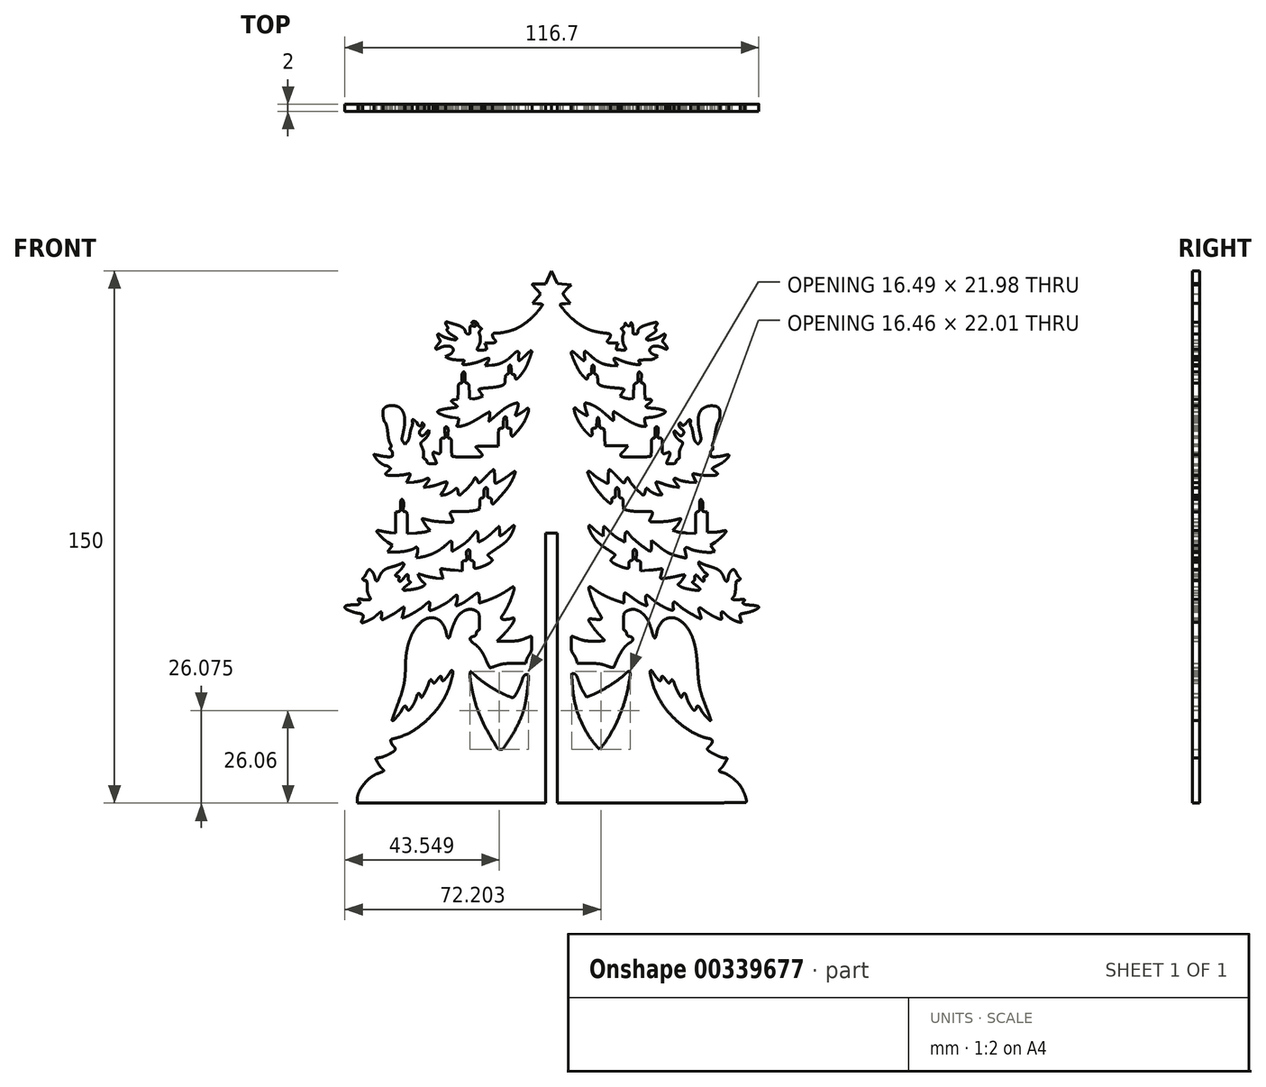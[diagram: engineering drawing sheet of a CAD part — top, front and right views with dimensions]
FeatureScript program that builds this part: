
annotation { "Feature Type Name" : "Feature", "Feature Type Description" : "" }
export const myFeature = defineFeature(function(context is Context, id is Id, definition is map)
    precondition{}
    {
        {
            var Q0;
            Q0=qCreatedBy(makeId("Front.planeOp"),FACE);
            var sketch = newSketch(context, id + "F0", { "sketchPlane" : qUnion([Q0])});
            skLineSegment(sketch, "E0", {"start": v(-52.5, 71.27) * mm, "end": v(-50.53, 71.13) * mm});
            skLineSegment(sketch, "E1", {"start": v(-50.53, 71.13) * mm, "end": v(-51.65, 70.04) * mm});
            skArc(sketch, "E2", {"start": v(-51.65, 70.04) * mm, "mid": v(-51.87, 69.82) * mm, "end": v(-52.08, 69.6) * mm});
            skArc(sketch, "E3", {"start": v(-52.08, 69.6) * mm, "mid": v(-52.26, 69.38) * mm, "end": v(-52.44, 69.15) * mm});
            skArc(sketch, "E4", {"start": v(-52.44, 69.15) * mm, "mid": v(-52.58, 68.96) * mm, "end": v(-52.7, 68.77) * mm});
            skArc(sketch, "E5", {"start": v(-52.7, 68.77) * mm, "mid": v(-52.75, 68.67) * mm, "end": v(-52.77, 68.56) * mm});
            skArc(sketch, "E6", {"start": v(-52.77, 68.56) * mm, "mid": v(-52.76, 68.45) * mm, "end": v(-52.72, 68.35) * mm});
            skArc(sketch, "E7", {"start": v(-52.72, 68.35) * mm, "mid": v(-52.6, 68.15) * mm, "end": v(-52.48, 67.95) * mm});
            skArc(sketch, "E8", {"start": v(-52.48, 67.95) * mm, "mid": v(-52.33, 67.72) * mm, "end": v(-52.16, 67.5) * mm});
            skArc(sketch, "E9", {"start": v(-52.16, 67.5) * mm, "mid": v(-51.98, 67.26) * mm, "end": v(-51.78, 67.03) * mm});
            skLineSegment(sketch, "E10", {"start": v(-51.78, 67.03) * mm, "end": v(-50.8, 65.88) * mm});
            skLineSegment(sketch, "E11", {"start": v(-50.8, 65.88) * mm, "end": v(-52.2, 65.8) * mm});
            skArc(sketch, "E12", {"start": v(-52.2, 65.8) * mm, "mid": v(-52.47, 65.77) * mm, "end": v(-52.74, 65.75) * mm});
            skArc(sketch, "E13", {"start": v(-52.74, 65.75) * mm, "mid": v(-52.96, 65.72) * mm, "end": v(-53.19, 65.69) * mm});
            skArc(sketch, "E14", {"start": v(-53.19, 65.69) * mm, "mid": v(-53.37, 65.66) * mm, "end": v(-53.55, 65.62) * mm});
            skArc(sketch, "E15", {"start": v(-53.55, 65.62) * mm, "mid": v(-53.59, 65.6) * mm, "end": v(-53.6, 65.55) * mm});
            skArc(sketch, "E16", {"start": v(-53.6, 65.55) * mm, "mid": v(-53.56, 65.3) * mm, "end": v(-53.44, 65.08) * mm});
            skArc(sketch, "E17", {"start": v(-53.44, 65.08) * mm, "mid": v(-52.9, 64.41) * mm, "end": v(-52.37, 63.76) * mm});
            skArc(sketch, "E18", {"start": v(-52.37, 63.76) * mm, "mid": v(-51.8, 63.1) * mm, "end": v(-51.2, 62.44) * mm});
            skArc(sketch, "E19", {"start": v(-51.2, 62.44) * mm, "mid": v(-50.7, 61.94) * mm, "end": v(-50.18, 61.47) * mm});
            skArc(sketch, "E20", {"start": v(-50.18, 61.47) * mm, "mid": v(-49.1, 60.6) * mm, "end": v(-47.97, 59.78) * mm});
            skArc(sketch, "E21", {"start": v(-47.97, 59.78) * mm, "mid": v(-47, 59.18) * mm, "end": v(-45.97, 58.67) * mm});
            skArc(sketch, "E22", {"start": v(-45.97, 58.67) * mm, "mid": v(-44.9, 58.26) * mm, "end": v(-43.81, 57.95) * mm});
            skArc(sketch, "E23", {"start": v(-43.81, 57.95) * mm, "mid": v(-42.5, 57.69) * mm, "end": v(-41.16, 57.5) * mm});
            skArc(sketch, "E24", {"start": v(-41.16, 57.5) * mm, "mid": v(-40.64, 57.44) * mm, "end": v(-40.13, 57.37) * mm});
            skArc(sketch, "E25", {"start": v(-40.13, 57.37) * mm, "mid": v(-39.9, 57.32) * mm, "end": v(-39.68, 57.24) * mm});
            skArc(sketch, "E26", {"start": v(-39.68, 57.24) * mm, "mid": v(-39.57, 57.16) * mm, "end": v(-39.49, 57.05) * mm});
            skArc(sketch, "E27", {"start": v(-39.49, 57.05) * mm, "mid": v(-39.45, 56.9) * mm, "end": v(-39.45, 56.75) * mm});
            skArc(sketch, "E28", {"start": v(-39.45, 56.75) * mm, "mid": v(-39.48, 56.63) * mm, "end": v(-39.52, 56.5) * mm});
            skArc(sketch, "E29", {"start": v(-39.52, 56.5) * mm, "mid": v(-39.57, 56.37) * mm, "end": v(-39.64, 56.23) * mm});
            skArc(sketch, "E30", {"start": v(-39.64, 56.23) * mm, "mid": v(-39.7, 56.1) * mm, "end": v(-39.78, 55.97) * mm});
            skArc(sketch, "E31", {"start": v(-39.78, 55.97) * mm, "mid": v(-39.86, 55.86) * mm, "end": v(-39.94, 55.76) * mm});
            skArc(sketch, "E32", {"start": v(-39.94, 55.76) * mm, "mid": v(-40.13, 55.51) * mm, "end": v(-40.3, 55.24) * mm});
            skArc(sketch, "E33", {"start": v(-40.3, 55.24) * mm, "mid": v(-40.32, 55.07) * mm, "end": v(-40.24, 54.91) * mm});
            skArc(sketch, "E34", {"start": v(-40.24, 54.91) * mm, "mid": v(-40.05, 54.78) * mm, "end": v(-39.82, 54.72) * mm});
            skArc(sketch, "E35", {"start": v(-39.82, 54.72) * mm, "mid": v(-39.32, 54.7) * mm, "end": v(-38.82, 54.68) * mm});
            skLineSegment(sketch, "E36", {"start": v(-38.82, 54.68) * mm, "end": v(-37.32, 54.68) * mm});
            skLineSegment(sketch, "E37", {"start": v(-37.32, 54.68) * mm, "end": v(-37.6, 53.84) * mm});
            skArc(sketch, "E38", {"start": v(-37.6, 53.84) * mm, "mid": v(-37.66, 53.67) * mm, "end": v(-37.71, 53.5) * mm});
            skArc(sketch, "E39", {"start": v(-37.71, 53.5) * mm, "mid": v(-37.75, 53.36) * mm, "end": v(-37.79, 53.21) * mm});
            skArc(sketch, "E40", {"start": v(-37.79, 53.21) * mm, "mid": v(-37.8, 53.1) * mm, "end": v(-37.83, 52.97) * mm});
            skArc(sketch, "E41", {"start": v(-37.83, 52.97) * mm, "mid": v(-37.82, 52.93) * mm, "end": v(-37.8, 52.9) * mm});
            skArc(sketch, "E42", {"start": v(-37.8, 52.9) * mm, "mid": v(-37.67, 52.8) * mm, "end": v(-37.51, 52.76) * mm});
            skArc(sketch, "E43", {"start": v(-37.51, 52.76) * mm, "mid": v(-37, 52.73) * mm, "end": v(-36.49, 52.71) * mm});
            skArc(sketch, "E44", {"start": v(-36.49, 52.71) * mm, "mid": v(-35.98, 52.7) * mm, "end": v(-35.46, 52.7) * mm});
            skArc(sketch, "E45", {"start": v(-35.46, 52.7) * mm, "mid": v(-35.31, 52.73) * mm, "end": v(-35.19, 52.82) * mm});
            skArc(sketch, "E46", {"start": v(-35.19, 52.82) * mm, "mid": v(-35.15, 52.87) * mm, "end": v(-35.14, 52.93) * mm});
            skArc(sketch, "E47", {"start": v(-35.14, 52.93) * mm, "mid": v(-35.15, 53.03) * mm, "end": v(-35.18, 53.13) * mm});
            skArc(sketch, "E48", {"start": v(-35.18, 53.13) * mm, "mid": v(-35.22, 53.26) * mm, "end": v(-35.27, 53.38) * mm});
            skArc(sketch, "E49", {"start": v(-35.27, 53.38) * mm, "mid": v(-35.33, 53.5) * mm, "end": v(-35.4, 53.63) * mm});
            skArc(sketch, "E50", {"start": v(-35.4, 53.63) * mm, "mid": v(-35.63, 54.02) * mm, "end": v(-35.8, 54.42) * mm});
            skArc(sketch, "E51", {"start": v(-35.8, 54.42) * mm, "mid": v(-35.92, 54.89) * mm, "end": v(-36.01, 55.36) * mm});
            skArc(sketch, "E52", {"start": v(-36.01, 55.36) * mm, "mid": v(-36.05, 55.82) * mm, "end": v(-36.05, 56.28) * mm});
            skArc(sketch, "E53", {"start": v(-36.05, 56.28) * mm, "mid": v(-35.99, 56.65) * mm, "end": v(-35.87, 57) * mm});
            skArc(sketch, "E54", {"start": v(-35.87, 57) * mm, "mid": v(-35.78, 57.2) * mm, "end": v(-35.72, 57.4) * mm});
            skArc(sketch, "E55", {"start": v(-35.72, 57.4) * mm, "mid": v(-35.69, 57.54) * mm, "end": v(-35.7, 57.68) * mm});
            skArc(sketch, "E56", {"start": v(-35.7, 57.68) * mm, "mid": v(-35.72, 57.82) * mm, "end": v(-35.78, 57.94) * mm});
            skArc(sketch, "E57", {"start": v(-35.78, 57.94) * mm, "mid": v(-35.9, 58.1) * mm, "end": v(-36.02, 58.25) * mm});
            skArc(sketch, "E58", {"start": v(-36.02, 58.25) * mm, "mid": v(-36.17, 58.42) * mm, "end": v(-36.3, 58.59) * mm});
            skArc(sketch, "E59", {"start": v(-36.3, 58.59) * mm, "mid": v(-36.35, 58.66) * mm, "end": v(-36.35, 58.75) * mm});
            skArc(sketch, "E60", {"start": v(-36.35, 58.75) * mm, "mid": v(-36.33, 58.83) * mm, "end": v(-36.27, 58.89) * mm});
            skArc(sketch, "E61", {"start": v(-36.27, 58.89) * mm, "mid": v(-36.1, 59) * mm, "end": v(-35.93, 59.1) * mm});
            skArc(sketch, "E62", {"start": v(-35.93, 59.1) * mm, "mid": v(-35.81, 59.16) * mm, "end": v(-35.7, 59.25) * mm});
            skArc(sketch, "E63", {"start": v(-35.7, 59.25) * mm, "mid": v(-35.6, 59.37) * mm, "end": v(-35.51, 59.49) * mm});
            skArc(sketch, "E64", {"start": v(-35.51, 59.49) * mm, "mid": v(-35.44, 59.62) * mm, "end": v(-35.38, 59.75) * mm});
            skArc(sketch, "E65", {"start": v(-35.38, 59.75) * mm, "mid": v(-35.34, 59.88) * mm, "end": v(-35.33, 60.01) * mm});
            skArc(sketch, "E66", {"start": v(-35.33, 60.01) * mm, "mid": v(-35.32, 60.15) * mm, "end": v(-35.31, 60.28) * mm});
            skArc(sketch, "E67", {"start": v(-35.31, 60.28) * mm, "mid": v(-35.3, 60.33) * mm, "end": v(-35.27, 60.37) * mm});
            skArc(sketch, "E68", {"start": v(-35.27, 60.37) * mm, "mid": v(-35.25, 60.38) * mm, "end": v(-35.22, 60.36) * mm});
            skArc(sketch, "E69", {"start": v(-35.22, 60.36) * mm, "mid": v(-35.18, 60.29) * mm, "end": v(-35.15, 60.2) * mm});
            skArc(sketch, "E70", {"start": v(-35.15, 60.2) * mm, "mid": v(-35, 59.94) * mm, "end": v(-34.8, 59.71) * mm});
            skArc(sketch, "E71", {"start": v(-34.8, 59.71) * mm, "mid": v(-34.56, 59.57) * mm, "end": v(-34.3, 59.52) * mm});
            skArc(sketch, "E72", {"start": v(-34.3, 59.52) * mm, "mid": v(-34.06, 59.57) * mm, "end": v(-33.87, 59.7) * mm});
            skArc(sketch, "E73", {"start": v(-33.87, 59.7) * mm, "mid": v(-33.74, 59.92) * mm, "end": v(-33.69, 60.17) * mm});
            skArc(sketch, "E74", {"start": v(-33.69, 60.17) * mm, "mid": v(-33.68, 60.3) * mm, "end": v(-33.68, 60.43) * mm});
            skArc(sketch, "E75", {"start": v(-33.68, 60.43) * mm, "mid": v(-33.67, 60.46) * mm, "end": v(-33.64, 60.47) * mm});
            skArc(sketch, "E76", {"start": v(-33.64, 60.47) * mm, "mid": v(-33.6, 60.47) * mm, "end": v(-33.57, 60.44) * mm});
            skArc(sketch, "E77", {"start": v(-33.57, 60.44) * mm, "mid": v(-33.5, 60.33) * mm, "end": v(-33.42, 60.2) * mm});
            skArc(sketch, "E78", {"start": v(-33.42, 60.2) * mm, "mid": v(-33.35, 60.1) * mm, "end": v(-33.31, 59.97) * mm});
            skArc(sketch, "E79", {"start": v(-33.31, 59.97) * mm, "mid": v(-33.26, 59.75) * mm, "end": v(-33.22, 59.53) * mm});
            skArc(sketch, "E80", {"start": v(-33.22, 59.53) * mm, "mid": v(-33.19, 59.27) * mm, "end": v(-33.16, 59.01) * mm});
            skArc(sketch, "E81", {"start": v(-33.16, 59.01) * mm, "mid": v(-33.15, 58.75) * mm, "end": v(-33.14, 58.48) * mm});
            skArc(sketch, "E82", {"start": v(-33.14, 58.48) * mm, "mid": v(-33.14, 58.09) * mm, "end": v(-33.12, 57.7) * mm});
            skArc(sketch, "E83", {"start": v(-33.12, 57.7) * mm, "mid": v(-33.1, 57.52) * mm, "end": v(-33.03, 57.37) * mm});
            skArc(sketch, "E84", {"start": v(-33.03, 57.37) * mm, "mid": v(-32.95, 57.27) * mm, "end": v(-32.84, 57.22) * mm});
            skArc(sketch, "E85", {"start": v(-32.84, 57.22) * mm, "mid": v(-32.64, 57.18) * mm, "end": v(-32.45, 57.17) * mm});
            skArc(sketch, "E86", {"start": v(-32.45, 57.17) * mm, "mid": v(-32.27, 57.18) * mm, "end": v(-32.1, 57.2) * mm});
            skArc(sketch, "E87", {"start": v(-32.1, 57.2) * mm, "mid": v(-32, 57.24) * mm, "end": v(-31.9, 57.3) * mm});
            skArc(sketch, "E88", {"start": v(-31.9, 57.3) * mm, "mid": v(-31.83, 57.39) * mm, "end": v(-31.8, 57.5) * mm});
            skArc(sketch, "E89", {"start": v(-31.8, 57.5) * mm, "mid": v(-31.76, 57.65) * mm, "end": v(-31.76, 57.82) * mm});
            skArc(sketch, "E90", {"start": v(-31.76, 57.82) * mm, "mid": v(-31.7, 58.17) * mm, "end": v(-31.56, 58.49) * mm});
            skArc(sketch, "E91", {"start": v(-31.56, 58.49) * mm, "mid": v(-31.32, 58.8) * mm, "end": v(-31.03, 59.05) * mm});
            skArc(sketch, "E92", {"start": v(-31.03, 59.05) * mm, "mid": v(-30.55, 59.33) * mm, "end": v(-30.05, 59.55) * mm});
            skArc(sketch, "E93", {"start": v(-30.05, 59.55) * mm, "mid": v(-29.25, 59.82) * mm, "end": v(-28.45, 60.07) * mm});
            skArc(sketch, "E94", {"start": v(-28.45, 60.07) * mm, "mid": v(-27.69, 60.27) * mm, "end": v(-26.92, 60.47) * mm});
            skArc(sketch, "E95", {"start": v(-26.92, 60.47) * mm, "mid": v(-26.64, 60.5) * mm, "end": v(-26.37, 60.44) * mm});
            skArc(sketch, "E96", {"start": v(-26.37, 60.44) * mm, "mid": v(-26.25, 60.33) * mm, "end": v(-26.25, 60.16) * mm});
            skArc(sketch, "E97", {"start": v(-26.25, 60.16) * mm, "mid": v(-26.43, 59.8) * mm, "end": v(-26.64, 59.46) * mm});
            skArc(sketch, "E98", {"start": v(-26.64, 59.46) * mm, "mid": v(-26.73, 59.33) * mm, "end": v(-26.8, 59.2) * mm});
            skArc(sketch, "E99", {"start": v(-26.8, 59.2) * mm, "mid": v(-26.85, 59.09) * mm, "end": v(-26.88, 58.97) * mm});
            skArc(sketch, "E100", {"start": v(-26.88, 58.97) * mm, "mid": v(-26.88, 58.89) * mm, "end": v(-26.87, 58.8) * mm});
            skArc(sketch, "E101", {"start": v(-26.87, 58.8) * mm, "mid": v(-26.84, 58.74) * mm, "end": v(-26.78, 58.7) * mm});
            skArc(sketch, "E102", {"start": v(-26.78, 58.7) * mm, "mid": v(-26.65, 58.57) * mm, "end": v(-26.58, 58.41) * mm});
            skArc(sketch, "E103", {"start": v(-26.58, 58.41) * mm, "mid": v(-26.57, 58.25) * mm, "end": v(-26.64, 58.1) * mm});
            skArc(sketch, "E104", {"start": v(-26.64, 58.1) * mm, "mid": v(-26.83, 57.86) * mm, "end": v(-27.06, 57.66) * mm});
            skArc(sketch, "E105", {"start": v(-27.06, 57.66) * mm, "mid": v(-27.54, 57.32) * mm, "end": v(-28.03, 56.99) * mm});
            skArc(sketch, "E106", {"start": v(-28.03, 56.99) * mm, "mid": v(-28.36, 56.77) * mm, "end": v(-28.67, 56.54) * mm});
            skArc(sketch, "E107", {"start": v(-28.67, 56.54) * mm, "mid": v(-28.9, 56.36) * mm, "end": v(-29.1, 56.17) * mm});
            skArc(sketch, "E108", {"start": v(-29.1, 56.17) * mm, "mid": v(-29.22, 56.03) * mm, "end": v(-29.32, 55.88) * mm});
            skArc(sketch, "E109", {"start": v(-29.32, 55.88) * mm, "mid": v(-29.34, 55.79) * mm, "end": v(-29.3, 55.7) * mm});
            skArc(sketch, "E110", {"start": v(-29.3, 55.7) * mm, "mid": v(-29.05, 55.54) * mm, "end": v(-28.76, 55.5) * mm});
            skArc(sketch, "E111", {"start": v(-28.76, 55.5) * mm, "mid": v(-28.2, 55.57) * mm, "end": v(-27.64, 55.67) * mm});
            skArc(sketch, "E112", {"start": v(-27.64, 55.67) * mm, "mid": v(-27, 55.84) * mm, "end": v(-26.39, 56.06) * mm});
            skArc(sketch, "E113", {"start": v(-26.39, 56.06) * mm, "mid": v(-25.83, 56.32) * mm, "end": v(-25.3, 56.62) * mm});
            skArc(sketch, "E114", {"start": v(-25.3, 56.62) * mm, "mid": v(-24.93, 56.84) * mm, "end": v(-24.57, 57.06) * mm});
            skArc(sketch, "E115", {"start": v(-24.57, 57.06) * mm, "mid": v(-24.41, 57.14) * mm, "end": v(-24.24, 57.2) * mm});
            skArc(sketch, "E116", {"start": v(-24.24, 57.2) * mm, "mid": v(-24.16, 57.2) * mm, "end": v(-24.08, 57.15) * mm});
            skArc(sketch, "E117", {"start": v(-24.08, 57.15) * mm, "mid": v(-24.03, 57.05) * mm, "end": v(-24.01, 56.95) * mm});
            skArc(sketch, "E118", {"start": v(-24.01, 56.95) * mm, "mid": v(-24.02, 56.83) * mm, "end": v(-24.05, 56.72) * mm});
            skArc(sketch, "E119", {"start": v(-24.05, 56.72) * mm, "mid": v(-24.1, 56.56) * mm, "end": v(-24.15, 56.42) * mm});
            skArc(sketch, "E120", {"start": v(-24.15, 56.42) * mm, "mid": v(-24.21, 56.26) * mm, "end": v(-24.29, 56.1) * mm});
            skArc(sketch, "E121", {"start": v(-24.29, 56.1) * mm, "mid": v(-24.37, 55.96) * mm, "end": v(-24.46, 55.82) * mm});
            skArc(sketch, "E122", {"start": v(-24.46, 55.82) * mm, "mid": v(-24.59, 55.63) * mm, "end": v(-24.7, 55.43) * mm});
            skArc(sketch, "E123", {"start": v(-24.7, 55.43) * mm, "mid": v(-24.74, 55.3) * mm, "end": v(-24.74, 55.17) * mm});
            skArc(sketch, "E124", {"start": v(-24.74, 55.17) * mm, "mid": v(-24.7, 55.03) * mm, "end": v(-24.61, 54.9) * mm});
            skArc(sketch, "E125", {"start": v(-24.61, 54.9) * mm, "mid": v(-24.4, 54.67) * mm, "end": v(-24.18, 54.43) * mm});
            skArc(sketch, "E126", {"start": v(-24.18, 54.43) * mm, "mid": v(-24.04, 54.28) * mm, "end": v(-23.9, 54.11) * mm});
            skArc(sketch, "E127", {"start": v(-23.9, 54.11) * mm, "mid": v(-23.79, 53.94) * mm, "end": v(-23.67, 53.77) * mm});
            skArc(sketch, "E128", {"start": v(-23.67, 53.77) * mm, "mid": v(-23.59, 53.61) * mm, "end": v(-23.5, 53.45) * mm});
            skArc(sketch, "E129", {"start": v(-23.5, 53.45) * mm, "mid": v(-23.47, 53.34) * mm, "end": v(-23.46, 53.23) * mm});
            skArc(sketch, "E130", {"start": v(-23.46, 53.23) * mm, "mid": v(-23.47, 53.11) * mm, "end": v(-23.51, 53) * mm});
            skArc(sketch, "E131", {"start": v(-23.51, 53) * mm, "mid": v(-23.57, 52.95) * mm, "end": v(-23.65, 52.93) * mm});
            skArc(sketch, "E132", {"start": v(-23.65, 52.93) * mm, "mid": v(-23.8, 52.95) * mm, "end": v(-23.94, 53) * mm});
            skArc(sketch, "E133", {"start": v(-23.94, 53) * mm, "mid": v(-24.29, 53.15) * mm, "end": v(-24.64, 53.3) * mm});
            skArc(sketch, "E134", {"start": v(-24.64, 53.3) * mm, "mid": v(-25.15, 53.51) * mm, "end": v(-25.67, 53.68) * mm});
            skArc(sketch, "E135", {"start": v(-25.67, 53.68) * mm, "mid": v(-26.15, 53.78) * mm, "end": v(-26.64, 53.82) * mm});
            skArc(sketch, "E136", {"start": v(-26.64, 53.82) * mm, "mid": v(-27.04, 53.8) * mm, "end": v(-27.44, 53.73) * mm});
            skArc(sketch, "E137", {"start": v(-27.44, 53.73) * mm, "mid": v(-27.74, 53.61) * mm, "end": v(-28, 53.41) * mm});
            skArc(sketch, "E138", {"start": v(-28, 53.41) * mm, "mid": v(-28.22, 53.14) * mm, "end": v(-28.36, 52.83) * mm});
            skArc(sketch, "E139", {"start": v(-28.36, 52.83) * mm, "mid": v(-28.39, 52.53) * mm, "end": v(-28.3, 52.25) * mm});
            skArc(sketch, "E140", {"start": v(-28.3, 52.25) * mm, "mid": v(-28.08, 51.95) * mm, "end": v(-27.8, 51.7) * mm});
            skArc(sketch, "E141", {"start": v(-27.8, 51.7) * mm, "mid": v(-27.31, 51.44) * mm, "end": v(-26.81, 51.2) * mm});
            skLineSegment(sketch, "E142", {"start": v(-26.81, 51.2) * mm, "end": v(-26.1, 50.9) * mm});
            skLineSegment(sketch, "E143", {"start": v(-26.1, 50.9) * mm, "end": v(-26.84, 50.42) * mm});
            skArc(sketch, "E144", {"start": v(-26.84, 50.42) * mm, "mid": v(-27.06, 50.3) * mm, "end": v(-27.3, 50.2) * mm});
            skArc(sketch, "E145", {"start": v(-27.3, 50.2) * mm, "mid": v(-27.58, 50.1) * mm, "end": v(-27.86, 50.04) * mm});
            skArc(sketch, "E146", {"start": v(-27.86, 50.04) * mm, "mid": v(-28.22, 49.99) * mm, "end": v(-28.59, 49.96) * mm});
            skArc(sketch, "E147", {"start": v(-28.59, 49.96) * mm, "mid": v(-29.06, 49.94) * mm, "end": v(-29.53, 49.93) * mm});
            skArc(sketch, "E148", {"start": v(-29.53, 49.93) * mm, "mid": v(-29.9, 49.93) * mm, "end": v(-30.28, 49.92) * mm});
            skArc(sketch, "E149", {"start": v(-30.28, 49.92) * mm, "mid": v(-30.6, 49.9) * mm, "end": v(-30.9, 49.9) * mm});
            skArc(sketch, "E150", {"start": v(-30.9, 49.9) * mm, "mid": v(-31.17, 49.87) * mm, "end": v(-31.43, 49.85) * mm});
            skArc(sketch, "E151", {"start": v(-31.43, 49.85) * mm, "mid": v(-31.47, 49.83) * mm, "end": v(-31.48, 49.8) * mm});
            skArc(sketch, "E152", {"start": v(-31.48, 49.8) * mm, "mid": v(-31.48, 49.76) * mm, "end": v(-31.47, 49.72) * mm});
            skArc(sketch, "E153", {"start": v(-31.47, 49.72) * mm, "mid": v(-31.43, 49.63) * mm, "end": v(-31.4, 49.55) * mm});
            skArc(sketch, "E154", {"start": v(-31.4, 49.55) * mm, "mid": v(-31.35, 49.45) * mm, "end": v(-31.3, 49.35) * mm});
            skArc(sketch, "E155", {"start": v(-31.3, 49.35) * mm, "mid": v(-31.25, 49.24) * mm, "end": v(-31.2, 49.13) * mm});
            skArc(sketch, "E156", {"start": v(-31.2, 49.13) * mm, "mid": v(-31.12, 48.98) * mm, "end": v(-31.06, 48.83) * mm});
            skArc(sketch, "E157", {"start": v(-31.06, 48.83) * mm, "mid": v(-31.05, 48.76) * mm, "end": v(-31.08, 48.7) * mm});
            skArc(sketch, "E158", {"start": v(-31.08, 48.7) * mm, "mid": v(-31.13, 48.64) * mm, "end": v(-31.2, 48.61) * mm});
            skArc(sketch, "E159", {"start": v(-31.2, 48.61) * mm, "mid": v(-31.39, 48.6) * mm, "end": v(-31.57, 48.6) * mm});
            skArc(sketch, "E160", {"start": v(-31.57, 48.6) * mm, "mid": v(-32.12, 48.62) * mm, "end": v(-32.67, 48.68) * mm});
            skArc(sketch, "E161", {"start": v(-32.67, 48.68) * mm, "mid": v(-33.37, 48.81) * mm, "end": v(-34.05, 48.96) * mm});
            skArc(sketch, "E162", {"start": v(-34.05, 48.96) * mm, "mid": v(-34.76, 49.15) * mm, "end": v(-35.46, 49.37) * mm});
            skArc(sketch, "E163", {"start": v(-35.46, 49.37) * mm, "mid": v(-36.08, 49.59) * mm, "end": v(-36.67, 49.84) * mm});
            skArc(sketch, "E164", {"start": v(-36.67, 49.84) * mm, "mid": v(-36.97, 49.97) * mm, "end": v(-37.27, 50.1) * mm});
            skArc(sketch, "E165", {"start": v(-37.27, 50.1) * mm, "mid": v(-37.54, 50.2) * mm, "end": v(-37.8, 50.28) * mm});
            skArc(sketch, "E166", {"start": v(-37.8, 50.28) * mm, "mid": v(-38.03, 50.34) * mm, "end": v(-38.26, 50.4) * mm});
            skArc(sketch, "E167", {"start": v(-38.26, 50.4) * mm, "mid": v(-38.35, 50.4) * mm, "end": v(-38.43, 50.37) * mm});
            skArc(sketch, "E168", {"start": v(-38.43, 50.37) * mm, "mid": v(-38.48, 50.32) * mm, "end": v(-38.5, 50.25) * mm});
            skArc(sketch, "E169", {"start": v(-38.5, 50.25) * mm, "mid": v(-38.47, 50.1) * mm, "end": v(-38.43, 49.97) * mm});
            skArc(sketch, "E170", {"start": v(-38.43, 49.97) * mm, "mid": v(-38.37, 49.8) * mm, "end": v(-38.3, 49.62) * mm});
            skArc(sketch, "E171", {"start": v(-38.3, 49.62) * mm, "mid": v(-38.2, 49.42) * mm, "end": v(-38.08, 49.23) * mm});
            skLineSegment(sketch, "E172", {"start": v(-38.08, 49.23) * mm, "end": v(-37.47, 48.25) * mm});
            skLineSegment(sketch, "E173", {"start": v(-37.47, 48.25) * mm, "end": v(-39.25, 48.37) * mm});
            skArc(sketch, "E174", {"start": v(-39.25, 48.37) * mm, "mid": v(-40.04, 48.45) * mm, "end": v(-40.82, 48.61) * mm});
            skArc(sketch, "E175", {"start": v(-40.82, 48.61) * mm, "mid": v(-41.56, 48.84) * mm, "end": v(-42.27, 49.13) * mm});
            skArc(sketch, "E176", {"start": v(-42.27, 49.13) * mm, "mid": v(-42.99, 49.52) * mm, "end": v(-43.66, 49.97) * mm});
            skArc(sketch, "E177", {"start": v(-43.66, 49.97) * mm, "mid": v(-44.38, 50.53) * mm, "end": v(-45.07, 51.15) * mm});
            skArc(sketch, "E178", {"start": v(-45.07, 51.15) * mm, "mid": v(-45.34, 51.4) * mm, "end": v(-45.61, 51.65) * mm});
            skArc(sketch, "E179", {"start": v(-45.61, 51.65) * mm, "mid": v(-45.86, 51.85) * mm, "end": v(-46.1, 52.04) * mm});
            skArc(sketch, "E180", {"start": v(-46.1, 52.04) * mm, "mid": v(-46.32, 52.2) * mm, "end": v(-46.53, 52.33) * mm});
            skArc(sketch, "E181", {"start": v(-46.53, 52.33) * mm, "mid": v(-46.6, 52.36) * mm, "end": v(-46.67, 52.34) * mm});
            skArc(sketch, "E182", {"start": v(-46.67, 52.34) * mm, "mid": v(-46.73, 52.29) * mm, "end": v(-46.75, 52.22) * mm});
            skArc(sketch, "E183", {"start": v(-46.75, 52.22) * mm, "mid": v(-46.78, 52.05) * mm, "end": v(-46.8, 51.87) * mm});
            skArc(sketch, "E184", {"start": v(-46.8, 51.87) * mm, "mid": v(-46.8, 51.66) * mm, "end": v(-46.8, 51.44) * mm});
            skArc(sketch, "E185", {"start": v(-46.8, 51.44) * mm, "mid": v(-46.78, 51.2) * mm, "end": v(-46.76, 50.95) * mm});
            skArc(sketch, "E186", {"start": v(-46.76, 50.95) * mm, "mid": v(-46.73, 50.68) * mm, "end": v(-46.71, 50.4) * mm});
            skArc(sketch, "E187", {"start": v(-46.71, 50.4) * mm, "mid": v(-46.71, 50.2) * mm, "end": v(-46.73, 50.02) * mm});
            skArc(sketch, "E188", {"start": v(-46.73, 50.02) * mm, "mid": v(-46.76, 49.9) * mm, "end": v(-46.8, 49.78) * mm});
            skArc(sketch, "E189", {"start": v(-46.8, 49.78) * mm, "mid": v(-46.85, 49.72) * mm, "end": v(-46.93, 49.7) * mm});
            skArc(sketch, "E190", {"start": v(-46.93, 49.7) * mm, "mid": v(-47.03, 49.72) * mm, "end": v(-47.12, 49.76) * mm});
            skArc(sketch, "E191", {"start": v(-47.12, 49.76) * mm, "mid": v(-47.34, 49.93) * mm, "end": v(-47.57, 50.1) * mm});
            skArc(sketch, "E192", {"start": v(-47.57, 50.1) * mm, "mid": v(-47.84, 50.32) * mm, "end": v(-48.1, 50.55) * mm});
            skArc(sketch, "E193", {"start": v(-48.1, 50.55) * mm, "mid": v(-48.38, 50.8) * mm, "end": v(-48.67, 51.07) * mm});
            skArc(sketch, "E194", {"start": v(-48.67, 51.07) * mm, "mid": v(-48.94, 51.34) * mm, "end": v(-49.23, 51.6) * mm});
            skArc(sketch, "E195", {"start": v(-49.23, 51.6) * mm, "mid": v(-49.48, 51.8) * mm, "end": v(-49.73, 52) * mm});
            skArc(sketch, "E196", {"start": v(-49.73, 52) * mm, "mid": v(-49.94, 52.16) * mm, "end": v(-50.16, 52.32) * mm});
            skArc(sketch, "E197", {"start": v(-50.16, 52.32) * mm, "mid": v(-50.23, 52.34) * mm, "end": v(-50.3, 52.32) * mm});
            skArc(sketch, "E198", {"start": v(-50.3, 52.32) * mm, "mid": v(-50.51, 52.05) * mm, "end": v(-50.5, 51.7) * mm});
            skArc(sketch, "E199", {"start": v(-50.5, 51.7) * mm, "mid": v(-50.06, 50.54) * mm, "end": v(-49.57, 49.38) * mm});
            skArc(sketch, "E200", {"start": v(-49.57, 49.38) * mm, "mid": v(-49.02, 48.21) * mm, "end": v(-48.42, 47.06) * mm});
            skArc(sketch, "E201", {"start": v(-48.42, 47.06) * mm, "mid": v(-47.9, 46.25) * mm, "end": v(-47.3, 45.5) * mm});
            skArc(sketch, "E202", {"start": v(-47.3, 45.5) * mm, "mid": v(-46.94, 45.11) * mm, "end": v(-46.56, 44.73) * mm});
            skArc(sketch, "E203", {"start": v(-46.56, 44.73) * mm, "mid": v(-46.37, 44.59) * mm, "end": v(-46.16, 44.5) * mm});
            skArc(sketch, "E204", {"start": v(-46.16, 44.5) * mm, "mid": v(-46.02, 44.52) * mm, "end": v(-45.94, 44.63) * mm});
            skArc(sketch, "E205", {"start": v(-45.94, 44.63) * mm, "mid": v(-45.88, 44.88) * mm, "end": v(-45.86, 45.14) * mm});
            skArc(sketch, "E206", {"start": v(-45.86, 45.14) * mm, "mid": v(-45.85, 45.3) * mm, "end": v(-45.83, 45.47) * mm});
            skArc(sketch, "E207", {"start": v(-45.83, 45.47) * mm, "mid": v(-45.8, 45.58) * mm, "end": v(-45.73, 45.68) * mm});
            skArc(sketch, "E208", {"start": v(-45.73, 45.68) * mm, "mid": v(-45.66, 45.75) * mm, "end": v(-45.56, 45.8) * mm});
            skArc(sketch, "E209", {"start": v(-45.56, 45.8) * mm, "mid": v(-45.44, 45.82) * mm, "end": v(-45.3, 45.83) * mm});
            skArc(sketch, "E210", {"start": v(-45.3, 45.83) * mm, "mid": v(-45.16, 45.85) * mm, "end": v(-45.02, 45.89) * mm});
            skArc(sketch, "E211", {"start": v(-45.02, 45.89) * mm, "mid": v(-44.92, 45.96) * mm, "end": v(-44.85, 46.05) * mm});
            skArc(sketch, "E212", {"start": v(-44.85, 46.05) * mm, "mid": v(-44.8, 46.22) * mm, "end": v(-44.77, 46.38) * mm});
            skArc(sketch, "E213", {"start": v(-44.77, 46.38) * mm, "mid": v(-44.76, 46.72) * mm, "end": v(-44.75, 47.06) * mm});
            skArc(sketch, "E214", {"start": v(-44.75, 47.06) * mm, "mid": v(-44.75, 47.3) * mm, "end": v(-44.73, 47.54) * mm});
            skArc(sketch, "E215", {"start": v(-44.73, 47.54) * mm, "mid": v(-44.71, 47.76) * mm, "end": v(-44.68, 47.97) * mm});
            skArc(sketch, "E216", {"start": v(-44.68, 47.97) * mm, "mid": v(-44.64, 48.14) * mm, "end": v(-44.6, 48.31) * mm});
            skArc(sketch, "E217", {"start": v(-44.6, 48.31) * mm, "mid": v(-44.56, 48.39) * mm, "end": v(-44.5, 48.45) * mm});
            skArc(sketch, "E218", {"start": v(-44.5, 48.45) * mm, "mid": v(-44.36, 48.47) * mm, "end": v(-44.25, 48.4) * mm});
            skArc(sketch, "E219", {"start": v(-44.25, 48.4) * mm, "mid": v(-44.13, 48.2) * mm, "end": v(-44.06, 48) * mm});
            skArc(sketch, "E220", {"start": v(-44.06, 48) * mm, "mid": v(-44, 47.69) * mm, "end": v(-43.97, 47.37) * mm});
            skArc(sketch, "E221", {"start": v(-43.97, 47.37) * mm, "mid": v(-44, 47.06) * mm, "end": v(-44.05, 46.76) * mm});
            skArc(sketch, "E222", {"start": v(-44.05, 46.76) * mm, "mid": v(-44.08, 46.58) * mm, "end": v(-44.1, 46.4) * mm});
            skArc(sketch, "E223", {"start": v(-44.1, 46.4) * mm, "mid": v(-44.1, 46.29) * mm, "end": v(-44.07, 46.17) * mm});
            skArc(sketch, "E224", {"start": v(-44.07, 46.17) * mm, "mid": v(-44.01, 46.09) * mm, "end": v(-43.93, 46.02) * mm});
            skArc(sketch, "E225", {"start": v(-43.93, 46.02) * mm, "mid": v(-43.8, 45.96) * mm, "end": v(-43.67, 45.92) * mm});
            skArc(sketch, "E226", {"start": v(-43.67, 45.92) * mm, "mid": v(-43.52, 45.86) * mm, "end": v(-43.4, 45.77) * mm});
            skArc(sketch, "E227", {"start": v(-43.4, 45.77) * mm, "mid": v(-43.29, 45.66) * mm, "end": v(-43.21, 45.52) * mm});
            skArc(sketch, "E228", {"start": v(-43.21, 45.52) * mm, "mid": v(-43.14, 45.32) * mm, "end": v(-43.1, 45.1) * mm});
            skArc(sketch, "E229", {"start": v(-43.1, 45.1) * mm, "mid": v(-43.06, 44.74) * mm, "end": v(-43.04, 44.38) * mm});
            skArc(sketch, "E230", {"start": v(-43.04, 44.38) * mm, "mid": v(-43, 43.94) * mm, "end": v(-42.96, 43.5) * mm});
            skArc(sketch, "E231", {"start": v(-42.96, 43.5) * mm, "mid": v(-42.9, 43.3) * mm, "end": v(-42.82, 43.12) * mm});
            skArc(sketch, "E232", {"start": v(-42.82, 43.12) * mm, "mid": v(-42.69, 42.97) * mm, "end": v(-42.52, 42.87) * mm});
            skArc(sketch, "E233", {"start": v(-42.52, 42.87) * mm, "mid": v(-42.19, 42.72) * mm, "end": v(-41.85, 42.6) * mm});
            skArc(sketch, "E234", {"start": v(-41.85, 42.6) * mm, "mid": v(-41.56, 42.5) * mm, "end": v(-41.26, 42.43) * mm});
            skArc(sketch, "E235", {"start": v(-41.26, 42.43) * mm, "mid": v(-40.79, 42.34) * mm, "end": v(-40.32, 42.27) * mm});
            skArc(sketch, "E236", {"start": v(-40.32, 42.27) * mm, "mid": v(-39.78, 42.2) * mm, "end": v(-39.25, 42.13) * mm});
            skArc(sketch, "E237", {"start": v(-39.25, 42.13) * mm, "mid": v(-38.72, 42.08) * mm, "end": v(-38.19, 42.04) * mm});
            skArc(sketch, "E238", {"start": v(-38.19, 42.04) * mm, "mid": v(-37.7, 42) * mm, "end": v(-37.2, 41.96) * mm});
            skArc(sketch, "E239", {"start": v(-37.2, 41.96) * mm, "mid": v(-36.8, 41.91) * mm, "end": v(-36.38, 41.85) * mm});
            skArc(sketch, "E240", {"start": v(-36.38, 41.85) * mm, "mid": v(-36.05, 41.8) * mm, "end": v(-35.72, 41.73) * mm});
            skArc(sketch, "E241", {"start": v(-35.72, 41.73) * mm, "mid": v(-35.65, 41.69) * mm, "end": v(-35.63, 41.62) * mm});
            skArc(sketch, "E242", {"start": v(-35.63, 41.62) * mm, "mid": v(-35.64, 41.54) * mm, "end": v(-35.66, 41.47) * mm});
            skArc(sketch, "E243", {"start": v(-35.66, 41.47) * mm, "mid": v(-35.73, 41.33) * mm, "end": v(-35.8, 41.2) * mm});
            skArc(sketch, "E244", {"start": v(-35.8, 41.2) * mm, "mid": v(-35.89, 41.03) * mm, "end": v(-35.98, 40.87) * mm});
            skArc(sketch, "E245", {"start": v(-35.98, 40.87) * mm, "mid": v(-36.1, 40.7) * mm, "end": v(-36.2, 40.55) * mm});
            skLineSegment(sketch, "E246", {"start": v(-36.2, 40.55) * mm, "end": v(-36.78, 39.74) * mm});
            skLineSegment(sketch, "E247", {"start": v(-36.78, 39.74) * mm, "end": v(-35.76, 39.31) * mm});
            skArc(sketch, "E248", {"start": v(-35.76, 39.31) * mm, "mid": v(-35.54, 39.23) * mm, "end": v(-35.3, 39.16) * mm});
            skArc(sketch, "E249", {"start": v(-35.3, 39.16) * mm, "mid": v(-35.05, 39.1) * mm, "end": v(-34.79, 39.04) * mm});
            skArc(sketch, "E250", {"start": v(-34.79, 39.04) * mm, "mid": v(-34.53, 39) * mm, "end": v(-34.28, 38.97) * mm});
            skArc(sketch, "E251", {"start": v(-34.28, 38.97) * mm, "mid": v(-34.07, 38.96) * mm, "end": v(-33.87, 38.97) * mm});
            skLineSegment(sketch, "E252", {"start": v(-33.87, 38.97) * mm, "end": v(-33, 39.06) * mm});
            skLineSegment(sketch, "E253", {"start": v(-33, 39.06) * mm, "end": v(-32.92, 41.18) * mm});
            skArc(sketch, "E254", {"start": v(-32.92, 41.18) * mm, "mid": v(-32.9, 41.82) * mm, "end": v(-32.86, 42.46) * mm});
            skArc(sketch, "E255", {"start": v(-32.86, 42.46) * mm, "mid": v(-32.82, 42.73) * mm, "end": v(-32.76, 43) * mm});
            skArc(sketch, "E256", {"start": v(-32.76, 43) * mm, "mid": v(-32.68, 43.14) * mm, "end": v(-32.57, 43.26) * mm});
            skArc(sketch, "E257", {"start": v(-32.57, 43.26) * mm, "mid": v(-32.4, 43.35) * mm, "end": v(-32.23, 43.4) * mm});
            skArc(sketch, "E258", {"start": v(-32.23, 43.4) * mm, "mid": v(-32.07, 43.43) * mm, "end": v(-31.9, 43.49) * mm});
            skArc(sketch, "E259", {"start": v(-31.9, 43.49) * mm, "mid": v(-31.81, 43.55) * mm, "end": v(-31.74, 43.65) * mm});
            skArc(sketch, "E260", {"start": v(-31.74, 43.65) * mm, "mid": v(-31.7, 43.8) * mm, "end": v(-31.68, 43.94) * mm});
            skArc(sketch, "E261", {"start": v(-31.68, 43.94) * mm, "mid": v(-31.69, 44.23) * mm, "end": v(-31.7, 44.51) * mm});
            skArc(sketch, "E262", {"start": v(-31.7, 44.51) * mm, "mid": v(-31.72, 44.73) * mm, "end": v(-31.73, 44.95) * mm});
            skArc(sketch, "E263", {"start": v(-31.73, 44.95) * mm, "mid": v(-31.73, 45.18) * mm, "end": v(-31.72, 45.4) * mm});
            skArc(sketch, "E264", {"start": v(-31.72, 45.4) * mm, "mid": v(-31.7, 45.62) * mm, "end": v(-31.68, 45.82) * mm});
            skArc(sketch, "E265", {"start": v(-31.68, 45.82) * mm, "mid": v(-31.65, 45.97) * mm, "end": v(-31.62, 46.12) * mm});
            skArc(sketch, "E266", {"start": v(-31.62, 46.12) * mm, "mid": v(-31.56, 46.26) * mm, "end": v(-31.5, 46.41) * mm});
            skArc(sketch, "E267", {"start": v(-31.5, 46.41) * mm, "mid": v(-31.46, 46.47) * mm, "end": v(-31.39, 46.52) * mm});
            skArc(sketch, "E268", {"start": v(-31.39, 46.52) * mm, "mid": v(-31.31, 46.53) * mm, "end": v(-31.24, 46.5) * mm});
            skArc(sketch, "E269", {"start": v(-31.24, 46.5) * mm, "mid": v(-31.13, 46.43) * mm, "end": v(-31.01, 46.34) * mm});
            skArc(sketch, "E270", {"start": v(-31.01, 46.34) * mm, "mid": v(-30.9, 46.23) * mm, "end": v(-30.82, 46.1) * mm});
            skArc(sketch, "E271", {"start": v(-30.82, 46.1) * mm, "mid": v(-30.76, 45.95) * mm, "end": v(-30.72, 45.78) * mm});
            skArc(sketch, "E272", {"start": v(-30.72, 45.78) * mm, "mid": v(-30.7, 45.56) * mm, "end": v(-30.7, 45.33) * mm});
            skArc(sketch, "E273", {"start": v(-30.7, 45.33) * mm, "mid": v(-30.73, 45) * mm, "end": v(-30.77, 44.67) * mm});
            skArc(sketch, "E274", {"start": v(-30.77, 44.67) * mm, "mid": v(-30.82, 44.28) * mm, "end": v(-30.86, 43.88) * mm});
            skArc(sketch, "E275", {"start": v(-30.86, 43.88) * mm, "mid": v(-30.86, 43.72) * mm, "end": v(-30.83, 43.56) * mm});
            skArc(sketch, "E276", {"start": v(-30.83, 43.56) * mm, "mid": v(-30.78, 43.46) * mm, "end": v(-30.69, 43.4) * mm});
            skArc(sketch, "E277", {"start": v(-30.69, 43.4) * mm, "mid": v(-30.54, 43.36) * mm, "end": v(-30.4, 43.34) * mm});
            skArc(sketch, "E278", {"start": v(-30.4, 43.34) * mm, "mid": v(-30.24, 43.32) * mm, "end": v(-30.1, 43.24) * mm});
            skArc(sketch, "E279", {"start": v(-30.1, 43.24) * mm, "mid": v(-29.99, 43.12) * mm, "end": v(-29.92, 42.98) * mm});
            skArc(sketch, "E280", {"start": v(-29.92, 42.98) * mm, "mid": v(-29.86, 42.7) * mm, "end": v(-29.83, 42.41) * mm});
            skArc(sketch, "E281", {"start": v(-29.83, 42.41) * mm, "mid": v(-29.8, 41.74) * mm, "end": v(-29.76, 41.06) * mm});
            skLineSegment(sketch, "E282", {"start": v(-29.76, 41.06) * mm, "end": v(-29.68, 38.78) * mm});
            skLineSegment(sketch, "E283", {"start": v(-29.68, 38.78) * mm, "end": v(-28.67, 38.78) * mm});
            skArc(sketch, "E284", {"start": v(-28.67, 38.78) * mm, "mid": v(-28.4, 38.78) * mm, "end": v(-28.13, 38.77) * mm});
            skArc(sketch, "E285", {"start": v(-28.13, 38.77) * mm, "mid": v(-28, 38.74) * mm, "end": v(-27.9, 38.7) * mm});
            skArc(sketch, "E286", {"start": v(-27.9, 38.7) * mm, "mid": v(-27.84, 38.64) * mm, "end": v(-27.83, 38.56) * mm});
            skArc(sketch, "E287", {"start": v(-27.83, 38.56) * mm, "mid": v(-27.85, 38.45) * mm, "end": v(-27.9, 38.34) * mm});
            skArc(sketch, "E288", {"start": v(-27.9, 38.34) * mm, "mid": v(-27.97, 38.23) * mm, "end": v(-28.04, 38.13) * mm});
            skArc(sketch, "E289", {"start": v(-28.04, 38.13) * mm, "mid": v(-28.16, 38) * mm, "end": v(-28.28, 37.88) * mm});
            skArc(sketch, "E290", {"start": v(-28.28, 37.88) * mm, "mid": v(-28.42, 37.75) * mm, "end": v(-28.57, 37.63) * mm});
            skArc(sketch, "E291", {"start": v(-28.57, 37.63) * mm, "mid": v(-28.7, 37.52) * mm, "end": v(-28.86, 37.42) * mm});
            skArc(sketch, "E292", {"start": v(-28.86, 37.42) * mm, "mid": v(-29.14, 37.2) * mm, "end": v(-29.4, 36.96) * mm});
            skArc(sketch, "E293", {"start": v(-29.4, 36.96) * mm, "mid": v(-29.46, 36.8) * mm, "end": v(-29.4, 36.64) * mm});
            skArc(sketch, "E294", {"start": v(-29.4, 36.64) * mm, "mid": v(-29.17, 36.49) * mm, "end": v(-28.92, 36.41) * mm});
            skArc(sketch, "E295", {"start": v(-28.92, 36.41) * mm, "mid": v(-28.3, 36.35) * mm, "end": v(-27.7, 36.3) * mm});
            skArc(sketch, "E296", {"start": v(-27.7, 36.3) * mm, "mid": v(-27.05, 36.25) * mm, "end": v(-26.4, 36.17) * mm});
            skArc(sketch, "E297", {"start": v(-26.4, 36.17) * mm, "mid": v(-25.79, 36.07) * mm, "end": v(-25.19, 35.92) * mm});
            skArc(sketch, "E298", {"start": v(-25.19, 35.92) * mm, "mid": v(-24.7, 35.78) * mm, "end": v(-24.21, 35.62) * mm});
            skArc(sketch, "E299", {"start": v(-24.21, 35.62) * mm, "mid": v(-24.07, 35.51) * mm, "end": v(-24.01, 35.34) * mm});
            skArc(sketch, "E300", {"start": v(-24.01, 35.34) * mm, "mid": v(-24.1, 35.04) * mm, "end": v(-24.33, 34.83) * mm});
            skArc(sketch, "E301", {"start": v(-24.33, 34.83) * mm, "mid": v(-25, 34.53) * mm, "end": v(-25.7, 34.26) * mm});
            skArc(sketch, "E302", {"start": v(-25.7, 34.26) * mm, "mid": v(-26.5, 34) * mm, "end": v(-27.31, 33.81) * mm});
            skArc(sketch, "E303", {"start": v(-27.31, 33.81) * mm, "mid": v(-28.04, 33.7) * mm, "end": v(-28.77, 33.66) * mm});
            skArc(sketch, "E304", {"start": v(-28.77, 33.66) * mm, "mid": v(-29.07, 33.66) * mm, "end": v(-29.38, 33.64) * mm});
            skArc(sketch, "E305", {"start": v(-29.38, 33.64) * mm, "mid": v(-29.52, 33.61) * mm, "end": v(-29.65, 33.55) * mm});
            skArc(sketch, "E306", {"start": v(-29.65, 33.55) * mm, "mid": v(-29.73, 33.46) * mm, "end": v(-29.78, 33.35) * mm});
            skArc(sketch, "E307", {"start": v(-29.78, 33.35) * mm, "mid": v(-29.81, 33.15) * mm, "end": v(-29.82, 32.96) * mm});
            skArc(sketch, "E308", {"start": v(-29.82, 32.96) * mm, "mid": v(-29.82, 32.8) * mm, "end": v(-29.8, 32.64) * mm});
            skArc(sketch, "E309", {"start": v(-29.8, 32.64) * mm, "mid": v(-29.77, 32.47) * mm, "end": v(-29.74, 32.3) * mm});
            skArc(sketch, "E310", {"start": v(-29.74, 32.3) * mm, "mid": v(-29.7, 32.13) * mm, "end": v(-29.64, 31.97) * mm});
            skArc(sketch, "E311", {"start": v(-29.64, 31.97) * mm, "mid": v(-29.6, 31.84) * mm, "end": v(-29.53, 31.71) * mm});
            skArc(sketch, "E312", {"start": v(-29.53, 31.71) * mm, "mid": v(-29.46, 31.56) * mm, "end": v(-29.4, 31.41) * mm});
            skArc(sketch, "E313", {"start": v(-29.4, 31.41) * mm, "mid": v(-29.4, 31.33) * mm, "end": v(-29.44, 31.27) * mm});
            skArc(sketch, "E314", {"start": v(-29.44, 31.27) * mm, "mid": v(-29.51, 31.21) * mm, "end": v(-29.6, 31.2) * mm});
            skArc(sketch, "E315", {"start": v(-29.6, 31.2) * mm, "mid": v(-29.85, 31.18) * mm, "end": v(-30.08, 31.18) * mm});
            skArc(sketch, "E316", {"start": v(-30.08, 31.18) * mm, "mid": v(-30.65, 31.22) * mm, "end": v(-31.2, 31.34) * mm});
            skArc(sketch, "E317", {"start": v(-31.2, 31.34) * mm, "mid": v(-31.9, 31.57) * mm, "end": v(-32.6, 31.85) * mm});
            skArc(sketch, "E318", {"start": v(-32.6, 31.85) * mm, "mid": v(-33.4, 32.23) * mm, "end": v(-34.2, 32.66) * mm});
            skArc(sketch, "E319", {"start": v(-34.2, 32.66) * mm, "mid": v(-35.1, 33.2) * mm, "end": v(-35.99, 33.78) * mm});
            skArc(sketch, "E320", {"start": v(-35.99, 33.78) * mm, "mid": v(-36.44, 34.07) * mm, "end": v(-36.89, 34.37) * mm});
            skArc(sketch, "E321", {"start": v(-36.89, 34.37) * mm, "mid": v(-37.28, 34.62) * mm, "end": v(-37.68, 34.87) * mm});
            skArc(sketch, "E322", {"start": v(-37.68, 34.87) * mm, "mid": v(-38.02, 35.08) * mm, "end": v(-38.36, 35.28) * mm});
            skArc(sketch, "E323", {"start": v(-38.36, 35.28) * mm, "mid": v(-38.44, 35.31) * mm, "end": v(-38.52, 35.32) * mm});
            skArc(sketch, "E324", {"start": v(-38.52, 35.32) * mm, "mid": v(-38.57, 35.3) * mm, "end": v(-38.6, 35.25) * mm});
            skArc(sketch, "E325", {"start": v(-38.6, 35.25) * mm, "mid": v(-38.62, 35.09) * mm, "end": v(-38.63, 34.92) * mm});
            skArc(sketch, "E326", {"start": v(-38.63, 34.92) * mm, "mid": v(-38.64, 34.7) * mm, "end": v(-38.64, 34.47) * mm});
            skArc(sketch, "E327", {"start": v(-38.64, 34.47) * mm, "mid": v(-38.63, 34.2) * mm, "end": v(-38.6, 33.93) * mm});
            skArc(sketch, "E328", {"start": v(-38.6, 33.93) * mm, "mid": v(-38.57, 33.44) * mm, "end": v(-38.55, 32.95) * mm});
            skArc(sketch, "E329", {"start": v(-38.55, 32.95) * mm, "mid": v(-38.6, 32.84) * mm, "end": v(-38.71, 32.83) * mm});
            skArc(sketch, "E330", {"start": v(-38.71, 32.83) * mm, "mid": v(-38.9, 32.92) * mm, "end": v(-39.08, 33.04) * mm});
            skArc(sketch, "E331", {"start": v(-39.08, 33.04) * mm, "mid": v(-40.1, 33.95) * mm, "end": v(-41.13, 34.85) * mm});
            skArc(sketch, "E332", {"start": v(-41.13, 34.85) * mm, "mid": v(-41.76, 35.39) * mm, "end": v(-42.41, 35.9) * mm});
            skArc(sketch, "E333", {"start": v(-42.41, 35.9) * mm, "mid": v(-43, 36.33) * mm, "end": v(-43.63, 36.72) * mm});
            skArc(sketch, "E334", {"start": v(-43.63, 36.72) * mm, "mid": v(-44.2, 37.03) * mm, "end": v(-44.8, 37.31) * mm});
            skArc(sketch, "E335", {"start": v(-44.8, 37.31) * mm, "mid": v(-45.35, 37.52) * mm, "end": v(-45.93, 37.69) * mm});
            skArc(sketch, "E336", {"start": v(-45.93, 37.69) * mm, "mid": v(-46.14, 37.73) * mm, "end": v(-46.36, 37.77) * mm});
            skArc(sketch, "E337", {"start": v(-46.36, 37.77) * mm, "mid": v(-46.46, 37.77) * mm, "end": v(-46.56, 37.73) * mm});
            skArc(sketch, "E338", {"start": v(-46.56, 37.73) * mm, "mid": v(-46.62, 37.66) * mm, "end": v(-46.65, 37.58) * mm});
            skArc(sketch, "E339", {"start": v(-46.65, 37.58) * mm, "mid": v(-46.67, 37.4) * mm, "end": v(-46.68, 37.22) * mm});
            skArc(sketch, "E340", {"start": v(-46.68, 37.22) * mm, "mid": v(-46.67, 37.06) * mm, "end": v(-46.64, 36.9) * mm});
            skArc(sketch, "E341", {"start": v(-46.64, 36.9) * mm, "mid": v(-46.6, 36.67) * mm, "end": v(-46.55, 36.44) * mm});
            skArc(sketch, "E342", {"start": v(-46.55, 36.44) * mm, "mid": v(-46.5, 36.19) * mm, "end": v(-46.42, 35.94) * mm});
            skArc(sketch, "E343", {"start": v(-46.42, 35.94) * mm, "mid": v(-46.35, 35.7) * mm, "end": v(-46.27, 35.47) * mm});
            skArc(sketch, "E344", {"start": v(-46.27, 35.47) * mm, "mid": v(-46.2, 35.26) * mm, "end": v(-46.13, 35.04) * mm});
            skArc(sketch, "E345", {"start": v(-46.13, 35.04) * mm, "mid": v(-46.08, 34.86) * mm, "end": v(-46.03, 34.67) * mm});
            skArc(sketch, "E346", {"start": v(-46.03, 34.67) * mm, "mid": v(-46, 34.51) * mm, "end": v(-45.97, 34.35) * mm});
            skArc(sketch, "E347", {"start": v(-45.97, 34.35) * mm, "mid": v(-45.97, 34.3) * mm, "end": v(-46, 34.26) * mm});
            skArc(sketch, "E348", {"start": v(-46, 34.26) * mm, "mid": v(-46.1, 34.2) * mm, "end": v(-46.23, 34.23) * mm});
            skArc(sketch, "E349", {"start": v(-46.23, 34.23) * mm, "mid": v(-46.79, 34.55) * mm, "end": v(-47.34, 34.88) * mm});
            skArc(sketch, "E350", {"start": v(-47.34, 34.88) * mm, "mid": v(-47.87, 35.2) * mm, "end": v(-48.38, 35.54) * mm});
            skArc(sketch, "E351", {"start": v(-48.38, 35.54) * mm, "mid": v(-48.65, 35.75) * mm, "end": v(-48.89, 36) * mm});
            skArc(sketch, "E352", {"start": v(-48.89, 36) * mm, "mid": v(-49.07, 36.2) * mm, "end": v(-49.28, 36.38) * mm});
            skArc(sketch, "E353", {"start": v(-49.28, 36.38) * mm, "mid": v(-49.41, 36.43) * mm, "end": v(-49.55, 36.4) * mm});
            skArc(sketch, "E354", {"start": v(-49.55, 36.4) * mm, "mid": v(-49.65, 36.29) * mm, "end": v(-49.69, 36.14) * mm});
            skArc(sketch, "E355", {"start": v(-49.69, 36.14) * mm, "mid": v(-49.67, 35.83) * mm, "end": v(-49.62, 35.53) * mm});
            skArc(sketch, "E356", {"start": v(-49.62, 35.53) * mm, "mid": v(-49.45, 34.85) * mm, "end": v(-49.21, 34.19) * mm});
            skArc(sketch, "E357", {"start": v(-49.21, 34.19) * mm, "mid": v(-48.86, 33.4) * mm, "end": v(-48.46, 32.62) * mm});
            skArc(sketch, "E358", {"start": v(-48.46, 32.62) * mm, "mid": v(-48.01, 31.84) * mm, "end": v(-47.52, 31.08) * mm});
            skArc(sketch, "E359", {"start": v(-47.52, 31.08) * mm, "mid": v(-47.04, 30.43) * mm, "end": v(-46.5, 29.82) * mm});
            skArc(sketch, "E360", {"start": v(-46.5, 29.82) * mm, "mid": v(-46, 29.3) * mm, "end": v(-45.5, 28.8) * mm});
            skArc(sketch, "E361", {"start": v(-45.5, 28.8) * mm, "mid": v(-45.22, 28.62) * mm, "end": v(-44.9, 28.54) * mm});
            skArc(sketch, "E362", {"start": v(-44.9, 28.54) * mm, "mid": v(-44.7, 28.6) * mm, "end": v(-44.6, 28.8) * mm});
            skArc(sketch, "E363", {"start": v(-44.6, 28.8) * mm, "mid": v(-44.6, 29.23) * mm, "end": v(-44.63, 29.67) * mm});
            skArc(sketch, "E364", {"start": v(-44.63, 29.67) * mm, "mid": v(-44.67, 29.95) * mm, "end": v(-44.7, 30.24) * mm});
            skArc(sketch, "E365", {"start": v(-44.7, 30.24) * mm, "mid": v(-44.7, 30.36) * mm, "end": v(-44.65, 30.47) * mm});
            skArc(sketch, "E366", {"start": v(-44.65, 30.47) * mm, "mid": v(-44.58, 30.55) * mm, "end": v(-44.49, 30.6) * mm});
            skArc(sketch, "E367", {"start": v(-44.49, 30.6) * mm, "mid": v(-44.29, 30.62) * mm, "end": v(-44.1, 30.62) * mm});
            skArc(sketch, "E368", {"start": v(-44.1, 30.62) * mm, "mid": v(-43.9, 30.64) * mm, "end": v(-43.7, 30.68) * mm});
            skArc(sketch, "E369", {"start": v(-43.7, 30.68) * mm, "mid": v(-43.58, 30.74) * mm, "end": v(-43.49, 30.85) * mm});
            skArc(sketch, "E370", {"start": v(-43.49, 30.85) * mm, "mid": v(-43.42, 31.03) * mm, "end": v(-43.38, 31.22) * mm});
            skArc(sketch, "E371", {"start": v(-43.38, 31.22) * mm, "mid": v(-43.34, 31.68) * mm, "end": v(-43.31, 32.15) * mm});
            skArc(sketch, "E372", {"start": v(-43.31, 32.15) * mm, "mid": v(-43.3, 32.44) * mm, "end": v(-43.26, 32.73) * mm});
            skArc(sketch, "E373", {"start": v(-43.26, 32.73) * mm, "mid": v(-43.23, 32.98) * mm, "end": v(-43.17, 33.22) * mm});
            skArc(sketch, "E374", {"start": v(-43.17, 33.22) * mm, "mid": v(-43.13, 33.4) * mm, "end": v(-43.07, 33.6) * mm});
            skArc(sketch, "E375", {"start": v(-43.07, 33.6) * mm, "mid": v(-43.02, 33.65) * mm, "end": v(-42.95, 33.67) * mm});
            skArc(sketch, "E376", {"start": v(-42.95, 33.67) * mm, "mid": v(-42.89, 33.65) * mm, "end": v(-42.84, 33.6) * mm});
            skArc(sketch, "E377", {"start": v(-42.84, 33.6) * mm, "mid": v(-42.78, 33.4) * mm, "end": v(-42.74, 33.22) * mm});
            skArc(sketch, "E378", {"start": v(-42.74, 33.22) * mm, "mid": v(-42.68, 32.98) * mm, "end": v(-42.65, 32.73) * mm});
            skArc(sketch, "E379", {"start": v(-42.65, 32.73) * mm, "mid": v(-42.62, 32.44) * mm, "end": v(-42.6, 32.15) * mm});
            skArc(sketch, "E380", {"start": v(-42.6, 32.15) * mm, "mid": v(-42.57, 31.7) * mm, "end": v(-42.53, 31.23) * mm});
            skArc(sketch, "E381", {"start": v(-42.53, 31.23) * mm, "mid": v(-42.5, 31.04) * mm, "end": v(-42.42, 30.86) * mm});
            skArc(sketch, "E382", {"start": v(-42.42, 30.86) * mm, "mid": v(-42.34, 30.75) * mm, "end": v(-42.22, 30.68) * mm});
            skArc(sketch, "E383", {"start": v(-42.22, 30.68) * mm, "mid": v(-42.03, 30.64) * mm, "end": v(-41.85, 30.62) * mm});
            skArc(sketch, "E384", {"start": v(-41.85, 30.62) * mm, "mid": v(-41.65, 30.6) * mm, "end": v(-41.46, 30.53) * mm});
            skArc(sketch, "E385", {"start": v(-41.46, 30.53) * mm, "mid": v(-41.34, 30.44) * mm, "end": v(-41.26, 30.3) * mm});
            skArc(sketch, "E386", {"start": v(-41.26, 30.3) * mm, "mid": v(-41.2, 30.03) * mm, "end": v(-41.16, 29.76) * mm});
            skArc(sketch, "E387", {"start": v(-41.16, 29.76) * mm, "mid": v(-41.13, 28.98) * mm, "end": v(-41.1, 28.2) * mm});
            skLineSegment(sketch, "E388", {"start": v(-41.1, 28.2) * mm, "end": v(-41.02, 25.78) * mm});
            skLineSegment(sketch, "E389", {"start": v(-41.02, 25.78) * mm, "end": v(-37.78, 25.78) * mm});
            skLineSegment(sketch, "E390", {"start": v(-37.78, 25.78) * mm, "end": v(-34.55, 25.78) * mm});
            skLineSegment(sketch, "E391", {"start": v(-34.55, 25.78) * mm, "end": v(-34.99, 25.1) * mm});
            skArc(sketch, "E392", {"start": v(-34.99, 25.1) * mm, "mid": v(-35.1, 24.94) * mm, "end": v(-35.2, 24.79) * mm});
            skArc(sketch, "E393", {"start": v(-35.2, 24.79) * mm, "mid": v(-35.36, 24.6) * mm, "end": v(-35.5, 24.43) * mm});
            skArc(sketch, "E394", {"start": v(-35.5, 24.43) * mm, "mid": v(-35.67, 24.25) * mm, "end": v(-35.84, 24.08) * mm});
            skArc(sketch, "E395", {"start": v(-35.84, 24.08) * mm, "mid": v(-36, 23.94) * mm, "end": v(-36.15, 23.8) * mm});
            skArc(sketch, "E396", {"start": v(-36.15, 23.8) * mm, "mid": v(-36.4, 23.51) * mm, "end": v(-36.58, 23.16) * mm});
            skArc(sketch, "E397", {"start": v(-36.58, 23.16) * mm, "mid": v(-36.55, 22.9) * mm, "end": v(-36.36, 22.73) * mm});
            skArc(sketch, "E398", {"start": v(-36.36, 22.73) * mm, "mid": v(-35.77, 22.58) * mm, "end": v(-35.16, 22.52) * mm});
            skArc(sketch, "E399", {"start": v(-35.16, 22.52) * mm, "mid": v(-33.74, 22.5) * mm, "end": v(-32.31, 22.5) * mm});
            skArc(sketch, "E400", {"start": v(-32.31, 22.5) * mm, "mid": v(-31.57, 22.52) * mm, "end": v(-30.82, 22.54) * mm});
            skArc(sketch, "E401", {"start": v(-30.82, 22.54) * mm, "mid": v(-30.17, 22.56) * mm, "end": v(-29.52, 22.6) * mm});
            skArc(sketch, "E402", {"start": v(-29.52, 22.6) * mm, "mid": v(-28.96, 22.62) * mm, "end": v(-28.41, 22.66) * mm});
            skArc(sketch, "E403", {"start": v(-28.41, 22.66) * mm, "mid": v(-28.3, 22.68) * mm, "end": v(-28.18, 22.73) * mm});
            skArc(sketch, "E404", {"start": v(-28.18, 22.73) * mm, "mid": v(-28.1, 22.8) * mm, "end": v(-28.06, 22.91) * mm});
            skArc(sketch, "E405", {"start": v(-28.06, 22.91) * mm, "mid": v(-28, 23.23) * mm, "end": v(-27.97, 23.55) * mm});
            skArc(sketch, "E406", {"start": v(-27.97, 23.55) * mm, "mid": v(-27.93, 23.97) * mm, "end": v(-27.9, 24.38) * mm});
            skArc(sketch, "E407", {"start": v(-27.9, 24.38) * mm, "mid": v(-27.9, 24.88) * mm, "end": v(-27.89, 25.39) * mm});
            skArc(sketch, "E408", {"start": v(-27.89, 25.39) * mm, "mid": v(-27.88, 26.13) * mm, "end": v(-27.87, 26.88) * mm});
            skArc(sketch, "E409", {"start": v(-27.87, 26.88) * mm, "mid": v(-27.85, 27.18) * mm, "end": v(-27.8, 27.48) * mm});
            skArc(sketch, "E410", {"start": v(-27.8, 27.48) * mm, "mid": v(-27.74, 27.63) * mm, "end": v(-27.63, 27.75) * mm});
            skArc(sketch, "E411", {"start": v(-27.63, 27.75) * mm, "mid": v(-27.5, 27.83) * mm, "end": v(-27.34, 27.86) * mm});
            skArc(sketch, "E412", {"start": v(-27.34, 27.86) * mm, "mid": v(-27.19, 27.88) * mm, "end": v(-27.05, 27.93) * mm});
            skArc(sketch, "E413", {"start": v(-27.05, 27.93) * mm, "mid": v(-26.95, 28) * mm, "end": v(-26.89, 28.1) * mm});
            skArc(sketch, "E414", {"start": v(-26.89, 28.1) * mm, "mid": v(-26.84, 28.3) * mm, "end": v(-26.83, 28.49) * mm});
            skArc(sketch, "E415", {"start": v(-26.83, 28.49) * mm, "mid": v(-26.84, 28.92) * mm, "end": v(-26.85, 29.36) * mm});
            skArc(sketch, "E416", {"start": v(-26.85, 29.36) * mm, "mid": v(-26.87, 29.87) * mm, "end": v(-26.87, 30.38) * mm});
            skArc(sketch, "E417", {"start": v(-26.87, 30.38) * mm, "mid": v(-26.84, 30.65) * mm, "end": v(-26.76, 30.9) * mm});
            skArc(sketch, "E418", {"start": v(-26.76, 30.9) * mm, "mid": v(-26.67, 31.03) * mm, "end": v(-26.54, 31.1) * mm});
            skArc(sketch, "E419", {"start": v(-26.54, 31.1) * mm, "mid": v(-26.37, 31.09) * mm, "end": v(-26.2, 31.03) * mm});
            skArc(sketch, "E420", {"start": v(-26.2, 31.03) * mm, "mid": v(-26.13, 30.95) * mm, "end": v(-26.07, 30.85) * mm});
            skArc(sketch, "E421", {"start": v(-26.07, 30.85) * mm, "mid": v(-26.03, 30.68) * mm, "end": v(-26, 30.5) * mm});
            skArc(sketch, "E422", {"start": v(-26, 30.5) * mm, "mid": v(-25.98, 30.26) * mm, "end": v(-25.98, 30.01) * mm});
            skArc(sketch, "E423", {"start": v(-25.98, 30.01) * mm, "mid": v(-26, 29.68) * mm, "end": v(-26.03, 29.34) * mm});
            skArc(sketch, "E424", {"start": v(-26.03, 29.34) * mm, "mid": v(-26.08, 28.87) * mm, "end": v(-26.12, 28.4) * mm});
            skArc(sketch, "E425", {"start": v(-26.12, 28.4) * mm, "mid": v(-26.11, 28.23) * mm, "end": v(-26.07, 28.06) * mm});
            skArc(sketch, "E426", {"start": v(-26.07, 28.06) * mm, "mid": v(-26, 27.96) * mm, "end": v(-25.9, 27.9) * mm});
            skArc(sketch, "E427", {"start": v(-25.9, 27.9) * mm, "mid": v(-25.7, 27.87) * mm, "end": v(-25.52, 27.86) * mm});
            skArc(sketch, "E428", {"start": v(-25.52, 27.86) * mm, "mid": v(-25.32, 27.84) * mm, "end": v(-25.13, 27.78) * mm});
            skArc(sketch, "E429", {"start": v(-25.13, 27.78) * mm, "mid": v(-25, 27.7) * mm, "end": v(-24.93, 27.56) * mm});
            skArc(sketch, "E430", {"start": v(-24.93, 27.56) * mm, "mid": v(-24.88, 27.31) * mm, "end": v(-24.86, 27.06) * mm});
            skArc(sketch, "E431", {"start": v(-24.86, 27.06) * mm, "mid": v(-24.85, 26.34) * mm, "end": v(-24.84, 25.62) * mm});
            skArc(sketch, "E432", {"start": v(-24.84, 25.62) * mm, "mid": v(-24.84, 24.8) * mm, "end": v(-24.82, 24) * mm});
            skArc(sketch, "E433", {"start": v(-24.82, 24) * mm, "mid": v(-24.76, 23.77) * mm, "end": v(-24.63, 23.57) * mm});
            skArc(sketch, "E434", {"start": v(-24.63, 23.57) * mm, "mid": v(-24.44, 23.47) * mm, "end": v(-24.23, 23.48) * mm});
            skArc(sketch, "E435", {"start": v(-24.23, 23.48) * mm, "mid": v(-23.65, 23.67) * mm, "end": v(-23.07, 23.88) * mm});
            skArc(sketch, "E436", {"start": v(-23.07, 23.88) * mm, "mid": v(-22.92, 23.9) * mm, "end": v(-22.77, 23.83) * mm});
            skArc(sketch, "E437", {"start": v(-22.77, 23.83) * mm, "mid": v(-22.67, 23.7) * mm, "end": v(-22.64, 23.55) * mm});
            skArc(sketch, "E438", {"start": v(-22.64, 23.55) * mm, "mid": v(-22.69, 23.23) * mm, "end": v(-22.78, 22.93) * mm});
            skArc(sketch, "E439", {"start": v(-22.78, 22.93) * mm, "mid": v(-22.97, 22.46) * mm, "end": v(-23.18, 22) * mm});
            skArc(sketch, "E440", {"start": v(-23.18, 22) * mm, "mid": v(-23.28, 21.78) * mm, "end": v(-23.38, 21.56) * mm});
            skArc(sketch, "E441", {"start": v(-23.38, 21.56) * mm, "mid": v(-23.46, 21.35) * mm, "end": v(-23.53, 21.15) * mm});
            skArc(sketch, "E442", {"start": v(-23.53, 21.15) * mm, "mid": v(-23.59, 20.99) * mm, "end": v(-23.63, 20.82) * mm});
            skArc(sketch, "E443", {"start": v(-23.63, 20.82) * mm, "mid": v(-23.64, 20.76) * mm, "end": v(-23.62, 20.7) * mm});
            skArc(sketch, "E444", {"start": v(-23.62, 20.7) * mm, "mid": v(-23.57, 20.65) * mm, "end": v(-23.52, 20.63) * mm});
            skArc(sketch, "E445", {"start": v(-23.52, 20.63) * mm, "mid": v(-23.34, 20.62) * mm, "end": v(-23.17, 20.6) * mm});
            skArc(sketch, "E446", {"start": v(-23.17, 20.6) * mm, "mid": v(-22.95, 20.6) * mm, "end": v(-22.73, 20.6) * mm});
            skArc(sketch, "E447", {"start": v(-22.73, 20.6) * mm, "mid": v(-22.49, 20.6) * mm, "end": v(-22.24, 20.62) * mm});
            skArc(sketch, "E448", {"start": v(-22.24, 20.62) * mm, "mid": v(-21.9, 20.66) * mm, "end": v(-21.56, 20.7) * mm});
            skArc(sketch, "E449", {"start": v(-21.56, 20.7) * mm, "mid": v(-21.38, 20.74) * mm, "end": v(-21.21, 20.81) * mm});
            skArc(sketch, "E450", {"start": v(-21.21, 20.81) * mm, "mid": v(-21.11, 20.89) * mm, "end": v(-21.04, 21) * mm});
            skArc(sketch, "E451", {"start": v(-21.04, 21) * mm, "mid": v(-20.99, 21.13) * mm, "end": v(-20.97, 21.28) * mm});
            skArc(sketch, "E452", {"start": v(-20.97, 21.28) * mm, "mid": v(-20.96, 21.4) * mm, "end": v(-20.93, 21.5) * mm});
            skArc(sketch, "E453", {"start": v(-20.93, 21.5) * mm, "mid": v(-20.88, 21.61) * mm, "end": v(-20.82, 21.71) * mm});
            skArc(sketch, "E454", {"start": v(-20.82, 21.71) * mm, "mid": v(-20.73, 21.8) * mm, "end": v(-20.64, 21.87) * mm});
            skArc(sketch, "E455", {"start": v(-20.64, 21.87) * mm, "mid": v(-20.53, 21.93) * mm, "end": v(-20.42, 21.97) * mm});
            skArc(sketch, "E456", {"start": v(-20.42, 21.97) * mm, "mid": v(-20.28, 22.02) * mm, "end": v(-20.14, 22.1) * mm});
            skArc(sketch, "E457", {"start": v(-20.14, 22.1) * mm, "mid": v(-20.06, 22.17) * mm, "end": v(-20, 22.28) * mm});
            skArc(sketch, "E458", {"start": v(-20, 22.28) * mm, "mid": v(-19.97, 22.42) * mm, "end": v(-19.96, 22.57) * mm});
            skArc(sketch, "E459", {"start": v(-19.96, 22.57) * mm, "mid": v(-19.99, 22.85) * mm, "end": v(-20.02, 23.12) * mm});
            skArc(sketch, "E460", {"start": v(-20.02, 23.12) * mm, "mid": v(-20.05, 23.38) * mm, "end": v(-20.06, 23.64) * mm});
            skArc(sketch, "E461", {"start": v(-20.06, 23.64) * mm, "mid": v(-20.04, 23.9) * mm, "end": v(-20, 24.15) * mm});
            skArc(sketch, "E462", {"start": v(-20, 24.15) * mm, "mid": v(-19.94, 24.4) * mm, "end": v(-19.86, 24.66) * mm});
            skArc(sketch, "E463", {"start": v(-19.86, 24.66) * mm, "mid": v(-19.74, 24.95) * mm, "end": v(-19.6, 25.22) * mm});
            skArc(sketch, "E464", {"start": v(-19.6, 25.22) * mm, "mid": v(-19.37, 25.68) * mm, "end": v(-19.15, 26.15) * mm});
            skArc(sketch, "E465", {"start": v(-19.15, 26.15) * mm, "mid": v(-19.1, 26.33) * mm, "end": v(-19.1, 26.53) * mm});
            skArc(sketch, "E466", {"start": v(-19.1, 26.53) * mm, "mid": v(-19.15, 26.69) * mm, "end": v(-19.27, 26.8) * mm});
            skArc(sketch, "E467", {"start": v(-19.27, 26.8) * mm, "mid": v(-19.56, 27) * mm, "end": v(-19.86, 27.16) * mm});
            skArc(sketch, "E468", {"start": v(-19.86, 27.16) * mm, "mid": v(-20.18, 27.36) * mm, "end": v(-20.47, 27.6) * mm});
            skArc(sketch, "E469", {"start": v(-20.47, 27.6) * mm, "mid": v(-20.76, 27.93) * mm, "end": v(-21.01, 28.28) * mm});
            skArc(sketch, "E470", {"start": v(-21.01, 28.28) * mm, "mid": v(-21.22, 28.64) * mm, "end": v(-21.4, 29.02) * mm});
            skArc(sketch, "E471", {"start": v(-21.4, 29.02) * mm, "mid": v(-21.5, 29.35) * mm, "end": v(-21.53, 29.7) * mm});
            skArc(sketch, "E472", {"start": v(-21.53, 29.7) * mm, "mid": v(-21.5, 29.78) * mm, "end": v(-21.46, 29.86) * mm});
            skArc(sketch, "E473", {"start": v(-21.46, 29.86) * mm, "mid": v(-21.4, 29.9) * mm, "end": v(-21.33, 29.88) * mm});
            skArc(sketch, "E474", {"start": v(-21.33, 29.88) * mm, "mid": v(-21.19, 29.8) * mm, "end": v(-21.06, 29.7) * mm});
            skArc(sketch, "E475", {"start": v(-21.06, 29.7) * mm, "mid": v(-20.81, 29.48) * mm, "end": v(-20.57, 29.25) * mm});
            skArc(sketch, "E476", {"start": v(-20.57, 29.25) * mm, "mid": v(-20.3, 29) * mm, "end": v(-20.03, 28.76) * mm});
            skArc(sketch, "E477", {"start": v(-20.03, 28.76) * mm, "mid": v(-19.88, 28.65) * mm, "end": v(-19.71, 28.56) * mm});
            skArc(sketch, "E478", {"start": v(-19.71, 28.56) * mm, "mid": v(-19.58, 28.53) * mm, "end": v(-19.45, 28.54) * mm});
            skArc(sketch, "E479", {"start": v(-19.45, 28.54) * mm, "mid": v(-19.31, 28.6) * mm, "end": v(-19.19, 28.68) * mm});
            skArc(sketch, "E480", {"start": v(-19.19, 28.68) * mm, "mid": v(-19, 28.87) * mm, "end": v(-18.86, 29.1) * mm});
            skArc(sketch, "E481", {"start": v(-18.86, 29.1) * mm, "mid": v(-18.79, 29.35) * mm, "end": v(-18.79, 29.6) * mm});
            skArc(sketch, "E482", {"start": v(-18.79, 29.6) * mm, "mid": v(-18.86, 29.86) * mm, "end": v(-19, 30.09) * mm});
            skArc(sketch, "E483", {"start": v(-19, 30.09) * mm, "mid": v(-19.2, 30.32) * mm, "end": v(-19.45, 30.51) * mm});
            skArc(sketch, "E484", {"start": v(-19.45, 30.51) * mm, "mid": v(-19.68, 30.69) * mm, "end": v(-19.87, 30.9) * mm});
            skArc(sketch, "E485", {"start": v(-19.87, 30.9) * mm, "mid": v(-20.01, 31.12) * mm, "end": v(-20.1, 31.38) * mm});
            skArc(sketch, "E486", {"start": v(-20.1, 31.38) * mm, "mid": v(-20.14, 31.6) * mm, "end": v(-20.12, 31.82) * mm});
            skArc(sketch, "E487", {"start": v(-20.12, 31.82) * mm, "mid": v(-20.04, 32) * mm, "end": v(-19.9, 32.13) * mm});
            skArc(sketch, "E488", {"start": v(-19.9, 32.13) * mm, "mid": v(-19.84, 32.15) * mm, "end": v(-19.79, 32.15) * mm});
            skArc(sketch, "E489", {"start": v(-19.79, 32.15) * mm, "mid": v(-19.73, 32.14) * mm, "end": v(-19.67, 32.11) * mm});
            skArc(sketch, "E490", {"start": v(-19.67, 32.11) * mm, "mid": v(-19.62, 32.07) * mm, "end": v(-19.57, 32.01) * mm});
            skArc(sketch, "E491", {"start": v(-19.57, 32.01) * mm, "mid": v(-19.52, 31.94) * mm, "end": v(-19.49, 31.87) * mm});
            skArc(sketch, "E492", {"start": v(-19.49, 31.87) * mm, "mid": v(-19.39, 31.69) * mm, "end": v(-19.24, 31.55) * mm});
            skArc(sketch, "E493", {"start": v(-19.24, 31.55) * mm, "mid": v(-19.07, 31.48) * mm, "end": v(-18.89, 31.5) * mm});
            skArc(sketch, "E494", {"start": v(-18.89, 31.5) * mm, "mid": v(-18.66, 31.59) * mm, "end": v(-18.46, 31.74) * mm});
            skArc(sketch, "E495", {"start": v(-18.46, 31.74) * mm, "mid": v(-18.2, 32) * mm, "end": v(-17.98, 32.28) * mm});
            skArc(sketch, "E496", {"start": v(-17.98, 32.28) * mm, "mid": v(-17.72, 32.6) * mm, "end": v(-17.45, 32.91) * mm});
            skArc(sketch, "E497", {"start": v(-17.45, 32.91) * mm, "mid": v(-17.28, 33.04) * mm, "end": v(-17.08, 33.09) * mm});
            skArc(sketch, "E498", {"start": v(-17.08, 33.09) * mm, "mid": v(-16.94, 33.04) * mm, "end": v(-16.87, 32.91) * mm});
            skArc(sketch, "E499", {"start": v(-16.87, 32.91) * mm, "mid": v(-16.87, 32.63) * mm, "end": v(-16.9, 32.35) * mm});
            skArc(sketch, "E500", {"start": v(-16.9, 32.35) * mm, "mid": v(-16.93, 32.19) * mm, "end": v(-16.94, 32.02) * mm});
            skArc(sketch, "E501", {"start": v(-16.94, 32.02) * mm, "mid": v(-16.93, 31.84) * mm, "end": v(-16.9, 31.67) * mm});
            skArc(sketch, "E502", {"start": v(-16.9, 31.67) * mm, "mid": v(-16.87, 31.5) * mm, "end": v(-16.82, 31.34) * mm});
            skArc(sketch, "E503", {"start": v(-16.82, 31.34) * mm, "mid": v(-16.77, 31.2) * mm, "end": v(-16.7, 31.09) * mm});
            skArc(sketch, "E504", {"start": v(-16.7, 31.09) * mm, "mid": v(-16.6, 30.95) * mm, "end": v(-16.54, 30.8) * mm});
            skArc(sketch, "E505", {"start": v(-16.54, 30.8) * mm, "mid": v(-16.45, 30.53) * mm, "end": v(-16.38, 30.26) * mm});
            skArc(sketch, "E506", {"start": v(-16.38, 30.26) * mm, "mid": v(-16.3, 29.94) * mm, "end": v(-16.23, 29.63) * mm});
            skArc(sketch, "E507", {"start": v(-16.23, 29.63) * mm, "mid": v(-16.18, 29.3) * mm, "end": v(-16.13, 28.97) * mm});
            skArc(sketch, "E508", {"start": v(-16.13, 28.97) * mm, "mid": v(-16.09, 28.61) * mm, "end": v(-16.02, 28.26) * mm});
            skArc(sketch, "E509", {"start": v(-16.02, 28.26) * mm, "mid": v(-15.95, 27.94) * mm, "end": v(-15.85, 27.63) * mm});
            skArc(sketch, "E510", {"start": v(-15.85, 27.63) * mm, "mid": v(-15.76, 27.38) * mm, "end": v(-15.65, 27.13) * mm});
            skArc(sketch, "E511", {"start": v(-15.65, 27.13) * mm, "mid": v(-15.54, 26.94) * mm, "end": v(-15.4, 26.78) * mm});
            skArc(sketch, "E512", {"start": v(-15.4, 26.78) * mm, "mid": v(-15.19, 26.55) * mm, "end": v(-14.96, 26.33) * mm});
            skArc(sketch, "E513", {"start": v(-14.96, 26.33) * mm, "mid": v(-14.86, 26.26) * mm, "end": v(-14.75, 26.25) * mm});
            skArc(sketch, "E514", {"start": v(-14.75, 26.25) * mm, "mid": v(-14.64, 26.27) * mm, "end": v(-14.56, 26.35) * mm});
            skArc(sketch, "E515", {"start": v(-14.56, 26.35) * mm, "mid": v(-14.38, 26.58) * mm, "end": v(-14.21, 26.83) * mm});
            skArc(sketch, "E516", {"start": v(-14.21, 26.83) * mm, "mid": v(-14.1, 27.03) * mm, "end": v(-14.01, 27.24) * mm});
            skArc(sketch, "E517", {"start": v(-14.01, 27.24) * mm, "mid": v(-13.96, 27.44) * mm, "end": v(-13.94, 27.65) * mm});
            skArc(sketch, "E518", {"start": v(-13.94, 27.65) * mm, "mid": v(-13.96, 27.93) * mm, "end": v(-14, 28.2) * mm});
            skArc(sketch, "E519", {"start": v(-14, 28.2) * mm, "mid": v(-14.11, 28.73) * mm, "end": v(-14.23, 29.25) * mm});
            skArc(sketch, "E520", {"start": v(-14.23, 29.25) * mm, "mid": v(-14.55, 30.92) * mm, "end": v(-14.73, 32.62) * mm});
            skArc(sketch, "E521", {"start": v(-14.73, 32.62) * mm, "mid": v(-14.66, 33.84) * mm, "end": v(-14.31, 35.02) * mm});
            skArc(sketch, "E522", {"start": v(-14.31, 35.02) * mm, "mid": v(-13.79, 35.84) * mm, "end": v(-13.02, 36.45) * mm});
            skArc(sketch, "E523", {"start": v(-13.02, 36.45) * mm, "mid": v(-12.02, 36.85) * mm, "end": v(-10.96, 36.98) * mm});
            skArc(sketch, "E524", {"start": v(-10.96, 36.98) * mm, "mid": v(-10.37, 36.95) * mm, "end": v(-9.8, 36.86) * mm});
            skArc(sketch, "E525", {"start": v(-9.8, 36.86) * mm, "mid": v(-9.4, 36.73) * mm, "end": v(-9.06, 36.49) * mm});
            skArc(sketch, "E526", {"start": v(-9.06, 36.49) * mm, "mid": v(-8.8, 36.17) * mm, "end": v(-8.66, 35.8) * mm});
            skArc(sketch, "E527", {"start": v(-8.66, 35.8) * mm, "mid": v(-8.56, 35.26) * mm, "end": v(-8.53, 34.72) * mm});
            skArc(sketch, "E528", {"start": v(-8.53, 34.72) * mm, "mid": v(-8.54, 34.4) * mm, "end": v(-8.56, 34.07) * mm});
            skArc(sketch, "E529", {"start": v(-8.56, 34.07) * mm, "mid": v(-8.6, 33.76) * mm, "end": v(-8.67, 33.46) * mm});
            skArc(sketch, "E530", {"start": v(-8.67, 33.46) * mm, "mid": v(-8.74, 33.18) * mm, "end": v(-8.83, 32.91) * mm});
            skArc(sketch, "E531", {"start": v(-8.83, 32.91) * mm, "mid": v(-8.94, 32.68) * mm, "end": v(-9.06, 32.45) * mm});
            skArc(sketch, "E532", {"start": v(-9.06, 32.45) * mm, "mid": v(-9.19, 32.22) * mm, "end": v(-9.29, 31.97) * mm});
            skArc(sketch, "E533", {"start": v(-9.29, 31.97) * mm, "mid": v(-9.42, 31.56) * mm, "end": v(-9.53, 31.15) * mm});
            skArc(sketch, "E534", {"start": v(-9.53, 31.15) * mm, "mid": v(-9.65, 30.68) * mm, "end": v(-9.76, 30.2) * mm});
            skArc(sketch, "E535", {"start": v(-9.76, 30.2) * mm, "mid": v(-9.85, 29.72) * mm, "end": v(-9.92, 29.24) * mm});
            skArc(sketch, "E536", {"start": v(-9.92, 29.24) * mm, "mid": v(-10, 28.78) * mm, "end": v(-10.07, 28.32) * mm});
            skArc(sketch, "E537", {"start": v(-10.07, 28.32) * mm, "mid": v(-10.15, 27.9) * mm, "end": v(-10.24, 27.48) * mm});
            skArc(sketch, "E538", {"start": v(-10.24, 27.48) * mm, "mid": v(-10.32, 27.13) * mm, "end": v(-10.41, 26.8) * mm});
            skArc(sketch, "E539", {"start": v(-10.41, 26.8) * mm, "mid": v(-10.46, 26.66) * mm, "end": v(-10.54, 26.54) * mm});
            skArc(sketch, "E540", {"start": v(-10.54, 26.54) * mm, "mid": v(-10.6, 26.45) * mm, "end": v(-10.63, 26.36) * mm});
            skArc(sketch, "E541", {"start": v(-10.63, 26.36) * mm, "mid": v(-10.66, 26.21) * mm, "end": v(-10.68, 26.06) * mm});
            skArc(sketch, "E542", {"start": v(-10.68, 26.06) * mm, "mid": v(-10.7, 25.9) * mm, "end": v(-10.7, 25.73) * mm});
            skArc(sketch, "E543", {"start": v(-10.7, 25.73) * mm, "mid": v(-10.68, 25.56) * mm, "end": v(-10.65, 25.4) * mm});
            skArc(sketch, "E544", {"start": v(-10.65, 25.4) * mm, "mid": v(-10.62, 25.2) * mm, "end": v(-10.6, 25.02) * mm});
            skArc(sketch, "E545", {"start": v(-10.6, 25.02) * mm, "mid": v(-10.6, 24.88) * mm, "end": v(-10.62, 24.74) * mm});
            skArc(sketch, "E546", {"start": v(-10.62, 24.74) * mm, "mid": v(-10.66, 24.64) * mm, "end": v(-10.72, 24.56) * mm});
            skArc(sketch, "E547", {"start": v(-10.72, 24.56) * mm, "mid": v(-10.8, 24.49) * mm, "end": v(-10.9, 24.44) * mm});
            skArc(sketch, "E548", {"start": v(-10.9, 24.44) * mm, "mid": v(-10.98, 24.39) * mm, "end": v(-11.05, 24.32) * mm});
            skArc(sketch, "E549", {"start": v(-11.05, 24.32) * mm, "mid": v(-11.12, 24.2) * mm, "end": v(-11.18, 24.09) * mm});
            skArc(sketch, "E550", {"start": v(-11.18, 24.09) * mm, "mid": v(-11.23, 23.94) * mm, "end": v(-11.27, 23.78) * mm});
            skArc(sketch, "E551", {"start": v(-11.27, 23.78) * mm, "mid": v(-11.29, 23.61) * mm, "end": v(-11.3, 23.44) * mm});
            skArc(sketch, "E552", {"start": v(-11.3, 23.44) * mm, "mid": v(-11.29, 23.19) * mm, "end": v(-11.26, 22.93) * mm});
            skArc(sketch, "E553", {"start": v(-11.26, 22.93) * mm, "mid": v(-11.21, 22.81) * mm, "end": v(-11.12, 22.72) * mm});
            skArc(sketch, "E554", {"start": v(-11.12, 22.72) * mm, "mid": v(-10.97, 22.65) * mm, "end": v(-10.81, 22.62) * mm});
            skArc(sketch, "E555", {"start": v(-10.81, 22.62) * mm, "mid": v(-10.38, 22.6) * mm, "end": v(-9.96, 22.6) * mm});
            skArc(sketch, "E556", {"start": v(-9.96, 22.6) * mm, "mid": v(-9.65, 22.61) * mm, "end": v(-9.35, 22.63) * mm});
            skArc(sketch, "E557", {"start": v(-9.35, 22.63) * mm, "mid": v(-9, 22.67) * mm, "end": v(-8.63, 22.72) * mm});
            skArc(sketch, "E558", {"start": v(-8.63, 22.72) * mm, "mid": v(-8.28, 22.78) * mm, "end": v(-7.92, 22.84) * mm});
            skArc(sketch, "E559", {"start": v(-7.92, 22.84) * mm, "mid": v(-7.62, 22.91) * mm, "end": v(-7.33, 23) * mm});
            skArc(sketch, "E560", {"start": v(-7.33, 23) * mm, "mid": v(-7.07, 23.07) * mm, "end": v(-6.82, 23.13) * mm});
            skArc(sketch, "E561", {"start": v(-6.82, 23.13) * mm, "mid": v(-6.61, 23.17) * mm, "end": v(-6.4, 23.2) * mm});
            skArc(sketch, "E562", {"start": v(-6.4, 23.2) * mm, "mid": v(-6.26, 23.2) * mm, "end": v(-6.12, 23.2) * mm});
            skArc(sketch, "E563", {"start": v(-6.12, 23.2) * mm, "mid": v(-6.06, 23.17) * mm, "end": v(-6.04, 23.11) * mm});
            skArc(sketch, "E564", {"start": v(-6.04, 23.11) * mm, "mid": v(-6.1, 22.78) * mm, "end": v(-6.26, 22.49) * mm});
            skArc(sketch, "E565", {"start": v(-6.26, 22.49) * mm, "mid": v(-6.61, 22.07) * mm, "end": v(-7, 21.67) * mm});
            skArc(sketch, "E566", {"start": v(-7, 21.67) * mm, "mid": v(-7.49, 21.26) * mm, "end": v(-8, 20.88) * mm});
            skArc(sketch, "E567", {"start": v(-8, 20.88) * mm, "mid": v(-8.53, 20.55) * mm, "end": v(-9.09, 20.27) * mm});
            skArc(sketch, "E568", {"start": v(-9.09, 20.27) * mm, "mid": v(-9.4, 20.13) * mm, "end": v(-9.72, 19.97) * mm});
            skArc(sketch, "E569", {"start": v(-9.72, 19.97) * mm, "mid": v(-10, 19.83) * mm, "end": v(-10.26, 19.68) * mm});
            skArc(sketch, "E570", {"start": v(-10.26, 19.68) * mm, "mid": v(-10.47, 19.55) * mm, "end": v(-10.67, 19.42) * mm});
            skArc(sketch, "E571", {"start": v(-10.67, 19.42) * mm, "mid": v(-10.72, 19.36) * mm, "end": v(-10.74, 19.3) * mm});
            skArc(sketch, "E572", {"start": v(-10.74, 19.3) * mm, "mid": v(-10.73, 19.22) * mm, "end": v(-10.7, 19.16) * mm});
            skArc(sketch, "E573", {"start": v(-10.7, 19.16) * mm, "mid": v(-10.6, 19.05) * mm, "end": v(-10.5, 18.94) * mm});
            skArc(sketch, "E574", {"start": v(-10.5, 18.94) * mm, "mid": v(-10.36, 18.81) * mm, "end": v(-10.21, 18.7) * mm});
            skArc(sketch, "E575", {"start": v(-10.21, 18.7) * mm, "mid": v(-10.05, 18.56) * mm, "end": v(-9.89, 18.44) * mm});
            skArc(sketch, "E576", {"start": v(-9.89, 18.44) * mm, "mid": v(-9.68, 18.29) * mm, "end": v(-9.48, 18.13) * mm});
            skArc(sketch, "E577", {"start": v(-9.48, 18.13) * mm, "mid": v(-9.38, 18.03) * mm, "end": v(-9.3, 17.91) * mm});
            skArc(sketch, "E578", {"start": v(-9.3, 17.91) * mm, "mid": v(-9.27, 17.83) * mm, "end": v(-9.28, 17.74) * mm});
            skArc(sketch, "E579", {"start": v(-9.28, 17.74) * mm, "mid": v(-9.33, 17.66) * mm, "end": v(-9.4, 17.6) * mm});
            skArc(sketch, "E580", {"start": v(-9.4, 17.6) * mm, "mid": v(-9.72, 17.45) * mm, "end": v(-10.07, 17.39) * mm});
            skArc(sketch, "E581", {"start": v(-10.07, 17.39) * mm, "mid": v(-11, 17.37) * mm, "end": v(-11.92, 17.37) * mm});
            skArc(sketch, "E582", {"start": v(-11.92, 17.37) * mm, "mid": v(-12.85, 17.39) * mm, "end": v(-13.77, 17.44) * mm});
            skArc(sketch, "E583", {"start": v(-13.77, 17.44) * mm, "mid": v(-14.38, 17.51) * mm, "end": v(-14.98, 17.65) * mm});
            skArc(sketch, "E584", {"start": v(-14.98, 17.65) * mm, "mid": v(-15.2, 17.7) * mm, "end": v(-15.4, 17.75) * mm});
            skArc(sketch, "E585", {"start": v(-15.4, 17.75) * mm, "mid": v(-15.6, 17.78) * mm, "end": v(-15.79, 17.8) * mm});
            skArc(sketch, "E586", {"start": v(-15.79, 17.8) * mm, "mid": v(-15.94, 17.82) * mm, "end": v(-16.1, 17.82) * mm});
            skArc(sketch, "E587", {"start": v(-16.1, 17.82) * mm, "mid": v(-16.17, 17.8) * mm, "end": v(-16.23, 17.77) * mm});
            skArc(sketch, "E588", {"start": v(-16.23, 17.77) * mm, "mid": v(-16.26, 17.7) * mm, "end": v(-16.26, 17.64) * mm});
            skArc(sketch, "E589", {"start": v(-16.26, 17.64) * mm, "mid": v(-16.22, 17.47) * mm, "end": v(-16.17, 17.31) * mm});
            skArc(sketch, "E590", {"start": v(-16.17, 17.31) * mm, "mid": v(-16.1, 17.1) * mm, "end": v(-16, 16.9) * mm});
            skArc(sketch, "E591", {"start": v(-16, 16.9) * mm, "mid": v(-15.9, 16.68) * mm, "end": v(-15.79, 16.46) * mm});
            skLineSegment(sketch, "E592", {"start": v(-15.79, 16.46) * mm, "end": v(-15.17, 15.34) * mm});
            skLineSegment(sketch, "E593", {"start": v(-15.17, 15.34) * mm, "end": v(-17.2, 15.5) * mm});
            skArc(sketch, "E594", {"start": v(-17.2, 15.5) * mm, "mid": v(-17.63, 15.53) * mm, "end": v(-18.05, 15.58) * mm});
            skArc(sketch, "E595", {"start": v(-18.05, 15.58) * mm, "mid": v(-18.48, 15.65) * mm, "end": v(-18.9, 15.73) * mm});
            skArc(sketch, "E596", {"start": v(-18.9, 15.73) * mm, "mid": v(-19.27, 15.81) * mm, "end": v(-19.64, 15.9) * mm});
            skArc(sketch, "E597", {"start": v(-19.64, 15.9) * mm, "mid": v(-19.87, 15.98) * mm, "end": v(-20.1, 16.08) * mm});
            skArc(sketch, "E598", {"start": v(-20.1, 16.08) * mm, "mid": v(-20.6, 16.32) * mm, "end": v(-21.11, 16.53) * mm});
            skArc(sketch, "E599", {"start": v(-21.11, 16.53) * mm, "mid": v(-21.33, 16.53) * mm, "end": v(-21.5, 16.4) * mm});
            skArc(sketch, "E600", {"start": v(-21.5, 16.4) * mm, "mid": v(-21.56, 16.17) * mm, "end": v(-21.5, 15.94) * mm});
            skArc(sketch, "E601", {"start": v(-21.5, 15.94) * mm, "mid": v(-21.16, 15.42) * mm, "end": v(-20.8, 14.93) * mm});
            skLineSegment(sketch, "E602", {"start": v(-20.8, 14.93) * mm, "end": v(-20.07, 13.97) * mm});
            skLineSegment(sketch, "E603", {"start": v(-20.07, 13.97) * mm, "end": v(-21.56, 14.17) * mm});
            skArc(sketch, "E604", {"start": v(-21.56, 14.17) * mm, "mid": v(-21.9, 14.22) * mm, "end": v(-22.25, 14.29) * mm});
            skArc(sketch, "E605", {"start": v(-22.25, 14.29) * mm, "mid": v(-22.67, 14.39) * mm, "end": v(-23.1, 14.5) * mm});
            skArc(sketch, "E606", {"start": v(-23.1, 14.5) * mm, "mid": v(-23.53, 14.62) * mm, "end": v(-23.96, 14.75) * mm});
            skArc(sketch, "E607", {"start": v(-23.96, 14.75) * mm, "mid": v(-24.33, 14.88) * mm, "end": v(-24.7, 15.02) * mm});
            skArc(sketch, "E608", {"start": v(-24.7, 15.02) * mm, "mid": v(-25.02, 15.14) * mm, "end": v(-25.35, 15.26) * mm});
            skArc(sketch, "E609", {"start": v(-25.35, 15.26) * mm, "mid": v(-25.63, 15.35) * mm, "end": v(-25.92, 15.43) * mm});
            skArc(sketch, "E610", {"start": v(-25.92, 15.43) * mm, "mid": v(-26.16, 15.48) * mm, "end": v(-26.4, 15.53) * mm});
            skArc(sketch, "E611", {"start": v(-26.4, 15.53) * mm, "mid": v(-26.48, 15.52) * mm, "end": v(-26.55, 15.48) * mm});
            skArc(sketch, "E612", {"start": v(-26.55, 15.48) * mm, "mid": v(-26.63, 15.34) * mm, "end": v(-26.62, 15.18) * mm});
            skArc(sketch, "E613", {"start": v(-26.62, 15.18) * mm, "mid": v(-26.44, 14.72) * mm, "end": v(-26.26, 14.27) * mm});
            skArc(sketch, "E614", {"start": v(-26.26, 14.27) * mm, "mid": v(-26.03, 13.77) * mm, "end": v(-25.77, 13.28) * mm});
            skArc(sketch, "E615", {"start": v(-25.77, 13.28) * mm, "mid": v(-25.52, 12.86) * mm, "end": v(-25.23, 12.44) * mm});
            skArc(sketch, "E616", {"start": v(-25.23, 12.44) * mm, "mid": v(-25.09, 12.24) * mm, "end": v(-24.95, 12.04) * mm});
            skArc(sketch, "E617", {"start": v(-24.95, 12.04) * mm, "mid": v(-24.93, 11.97) * mm, "end": v(-24.94, 11.9) * mm});
            skArc(sketch, "E618", {"start": v(-24.94, 11.9) * mm, "mid": v(-24.98, 11.85) * mm, "end": v(-25.05, 11.83) * mm});
            skArc(sketch, "E619", {"start": v(-25.05, 11.83) * mm, "mid": v(-25.28, 11.82) * mm, "end": v(-25.51, 11.82) * mm});
            skArc(sketch, "E620", {"start": v(-25.51, 11.82) * mm, "mid": v(-25.88, 11.85) * mm, "end": v(-26.25, 11.94) * mm});
            skArc(sketch, "E621", {"start": v(-26.25, 11.94) * mm, "mid": v(-26.74, 12.12) * mm, "end": v(-27.22, 12.33) * mm});
            skArc(sketch, "E622", {"start": v(-27.22, 12.33) * mm, "mid": v(-27.68, 12.57) * mm, "end": v(-28.14, 12.83) * mm});
            skArc(sketch, "E623", {"start": v(-28.14, 12.83) * mm, "mid": v(-28.44, 13.05) * mm, "end": v(-28.7, 13.32) * mm});
            skArc(sketch, "E624", {"start": v(-28.7, 13.32) * mm, "mid": v(-28.87, 13.5) * mm, "end": v(-29.06, 13.68) * mm});
            skArc(sketch, "E625", {"start": v(-29.06, 13.68) * mm, "mid": v(-29.18, 13.73) * mm, "end": v(-29.31, 13.7) * mm});
            skArc(sketch, "E626", {"start": v(-29.31, 13.7) * mm, "mid": v(-29.43, 13.6) * mm, "end": v(-29.5, 13.46) * mm});
            skArc(sketch, "E627", {"start": v(-29.5, 13.46) * mm, "mid": v(-29.6, 13.13) * mm, "end": v(-29.66, 12.79) * mm});
            skArc(sketch, "E628", {"start": v(-29.66, 12.79) * mm, "mid": v(-29.7, 12.6) * mm, "end": v(-29.75, 12.42) * mm});
            skArc(sketch, "E629", {"start": v(-29.75, 12.42) * mm, "mid": v(-29.8, 12.26) * mm, "end": v(-29.86, 12.1) * mm});
            skArc(sketch, "E630", {"start": v(-29.86, 12.1) * mm, "mid": v(-29.92, 12) * mm, "end": v(-29.98, 11.88) * mm});
            skArc(sketch, "E631", {"start": v(-29.98, 11.88) * mm, "mid": v(-30.03, 11.84) * mm, "end": v(-30.09, 11.82) * mm});
            skArc(sketch, "E632", {"start": v(-30.09, 11.82) * mm, "mid": v(-30.38, 11.88) * mm, "end": v(-30.63, 12.04) * mm});
            skArc(sketch, "E633", {"start": v(-30.63, 12.04) * mm, "mid": v(-31.34, 12.71) * mm, "end": v(-32.04, 13.4) * mm});
            skArc(sketch, "E634", {"start": v(-32.04, 13.4) * mm, "mid": v(-32.71, 14.1) * mm, "end": v(-33.36, 14.82) * mm});
            skArc(sketch, "E635", {"start": v(-33.36, 14.82) * mm, "mid": v(-33.72, 15.29) * mm, "end": v(-34.02, 15.79) * mm});
            skArc(sketch, "E636", {"start": v(-34.02, 15.79) * mm, "mid": v(-34.2, 16.13) * mm, "end": v(-34.38, 16.48) * mm});
            skArc(sketch, "E637", {"start": v(-34.38, 16.48) * mm, "mid": v(-34.46, 16.58) * mm, "end": v(-34.56, 16.66) * mm});
            skArc(sketch, "E638", {"start": v(-34.56, 16.66) * mm, "mid": v(-34.65, 16.69) * mm, "end": v(-34.73, 16.65) * mm});
            skArc(sketch, "E639", {"start": v(-34.73, 16.65) * mm, "mid": v(-34.86, 16.52) * mm, "end": v(-34.97, 16.38) * mm});
            skArc(sketch, "E640", {"start": v(-34.97, 16.38) * mm, "mid": v(-35.05, 16.27) * mm, "end": v(-35.12, 16.16) * mm});
            skArc(sketch, "E641", {"start": v(-35.12, 16.16) * mm, "mid": v(-35.18, 16.04) * mm, "end": v(-35.24, 15.91) * mm});
            skArc(sketch, "E642", {"start": v(-35.24, 15.91) * mm, "mid": v(-35.29, 15.8) * mm, "end": v(-35.32, 15.68) * mm});
            skArc(sketch, "E643", {"start": v(-35.32, 15.68) * mm, "mid": v(-35.34, 15.59) * mm, "end": v(-35.35, 15.5) * mm});
            skArc(sketch, "E644", {"start": v(-35.35, 15.5) * mm, "mid": v(-35.4, 15.36) * mm, "end": v(-35.51, 15.27) * mm});
            skArc(sketch, "E645", {"start": v(-35.51, 15.27) * mm, "mid": v(-35.68, 15.25) * mm, "end": v(-35.83, 15.3) * mm});
            skArc(sketch, "E646", {"start": v(-35.83, 15.3) * mm, "mid": v(-36.16, 15.56) * mm, "end": v(-36.47, 15.84) * mm});
            skArc(sketch, "E647", {"start": v(-36.47, 15.84) * mm, "mid": v(-37.06, 16.46) * mm, "end": v(-37.64, 17.07) * mm});
            skArc(sketch, "E648", {"start": v(-37.64, 17.07) * mm, "mid": v(-38, 17.45) * mm, "end": v(-38.35, 17.82) * mm});
            skArc(sketch, "E649", {"start": v(-38.35, 17.82) * mm, "mid": v(-38.67, 18.13) * mm, "end": v(-39, 18.44) * mm});
            skArc(sketch, "E650", {"start": v(-39, 18.44) * mm, "mid": v(-39.28, 18.7) * mm, "end": v(-39.56, 18.94) * mm});
            skArc(sketch, "E651", {"start": v(-39.56, 18.94) * mm, "mid": v(-39.64, 19) * mm, "end": v(-39.74, 19.01) * mm});
            skArc(sketch, "E652", {"start": v(-39.74, 19.01) * mm, "mid": v(-39.83, 18.98) * mm, "end": v(-39.88, 18.91) * mm});
            skArc(sketch, "E653", {"start": v(-39.88, 18.91) * mm, "mid": v(-39.93, 18.71) * mm, "end": v(-39.97, 18.5) * mm});
            skArc(sketch, "E654", {"start": v(-39.97, 18.5) * mm, "mid": v(-40.01, 18.2) * mm, "end": v(-40.03, 17.9) * mm});
            skArc(sketch, "E655", {"start": v(-40.03, 17.9) * mm, "mid": v(-40.05, 17.49) * mm, "end": v(-40.05, 17.07) * mm});
            skArc(sketch, "E656", {"start": v(-40.05, 17.07) * mm, "mid": v(-40.05, 16.7) * mm, "end": v(-40.06, 16.33) * mm});
            skArc(sketch, "E657", {"start": v(-40.06, 16.33) * mm, "mid": v(-40.07, 16.02) * mm, "end": v(-40.1, 15.7) * mm});
            skArc(sketch, "E658", {"start": v(-40.1, 15.7) * mm, "mid": v(-40.12, 15.45) * mm, "end": v(-40.14, 15.2) * mm});
            skArc(sketch, "E659", {"start": v(-40.14, 15.2) * mm, "mid": v(-40.16, 15.15) * mm, "end": v(-40.2, 15.14) * mm});
            skArc(sketch, "E660", {"start": v(-40.2, 15.14) * mm, "mid": v(-40.47, 15.17) * mm, "end": v(-40.72, 15.27) * mm});
            skArc(sketch, "E661", {"start": v(-40.72, 15.27) * mm, "mid": v(-41.38, 15.64) * mm, "end": v(-42.02, 16.01) * mm});
            skArc(sketch, "E662", {"start": v(-42.02, 16.01) * mm, "mid": v(-42.67, 16.41) * mm, "end": v(-43.31, 16.83) * mm});
            skArc(sketch, "E663", {"start": v(-43.31, 16.83) * mm, "mid": v(-43.75, 17.15) * mm, "end": v(-44.17, 17.5) * mm});
            skArc(sketch, "E664", {"start": v(-44.17, 17.5) * mm, "mid": v(-44.75, 18) * mm, "end": v(-45.33, 18.48) * mm});
            skArc(sketch, "E665", {"start": v(-45.33, 18.48) * mm, "mid": v(-45.54, 18.54) * mm, "end": v(-45.74, 18.45) * mm});
            skArc(sketch, "E666", {"start": v(-45.74, 18.45) * mm, "mid": v(-45.86, 18.24) * mm, "end": v(-45.84, 18) * mm});
            skArc(sketch, "E667", {"start": v(-45.84, 18) * mm, "mid": v(-45.53, 17.22) * mm, "end": v(-45.2, 16.46) * mm});
            skArc(sketch, "E668", {"start": v(-45.2, 16.46) * mm, "mid": v(-44.85, 15.74) * mm, "end": v(-44.45, 15.04) * mm});
            skArc(sketch, "E669", {"start": v(-44.45, 15.04) * mm, "mid": v(-43.9, 14.21) * mm, "end": v(-43.34, 13.41) * mm});
            skArc(sketch, "E670", {"start": v(-43.34, 13.41) * mm, "mid": v(-42.7, 12.6) * mm, "end": v(-42.05, 11.82) * mm});
            skArc(sketch, "E671", {"start": v(-42.05, 11.82) * mm, "mid": v(-41.42, 11.13) * mm, "end": v(-40.75, 10.48) * mm});
            skArc(sketch, "E672", {"start": v(-40.75, 10.48) * mm, "mid": v(-40.3, 10.07) * mm, "end": v(-39.85, 9.68) * mm});
            skArc(sketch, "E673", {"start": v(-39.85, 9.68) * mm, "mid": v(-39.65, 9.56) * mm, "end": v(-39.41, 9.5) * mm});
            skArc(sketch, "E674", {"start": v(-39.41, 9.5) * mm, "mid": v(-39.25, 9.56) * mm, "end": v(-39.16, 9.7) * mm});
            skArc(sketch, "E675", {"start": v(-39.16, 9.7) * mm, "mid": v(-39.1, 10.04) * mm, "end": v(-39.08, 10.4) * mm});
            skArc(sketch, "E676", {"start": v(-39.08, 10.4) * mm, "mid": v(-39.08, 10.57) * mm, "end": v(-39.06, 10.74) * mm});
            skArc(sketch, "E677", {"start": v(-39.06, 10.74) * mm, "mid": v(-39.02, 10.86) * mm, "end": v(-38.96, 10.96) * mm});
            skArc(sketch, "E678", {"start": v(-38.96, 10.96) * mm, "mid": v(-38.89, 11.04) * mm, "end": v(-38.8, 11.09) * mm});
            skArc(sketch, "E679", {"start": v(-38.8, 11.09) * mm, "mid": v(-38.66, 11.12) * mm, "end": v(-38.53, 11.13) * mm});
            skArc(sketch, "E680", {"start": v(-38.53, 11.13) * mm, "mid": v(-38.39, 11.14) * mm, "end": v(-38.25, 11.18) * mm});
            skArc(sketch, "E681", {"start": v(-38.25, 11.18) * mm, "mid": v(-38.15, 11.24) * mm, "end": v(-38.1, 11.33) * mm});
            skArc(sketch, "E682", {"start": v(-38.1, 11.33) * mm, "mid": v(-38.04, 11.47) * mm, "end": v(-38.03, 11.62) * mm});
            skArc(sketch, "E683", {"start": v(-38.03, 11.62) * mm, "mid": v(-38.04, 11.93) * mm, "end": v(-38.05, 12.24) * mm});
            skArc(sketch, "E684", {"start": v(-38.05, 12.24) * mm, "mid": v(-38.06, 12.68) * mm, "end": v(-38.04, 13.12) * mm});
            skArc(sketch, "E685", {"start": v(-38.04, 13.12) * mm, "mid": v(-37.98, 13.44) * mm, "end": v(-37.87, 13.74) * mm});
            skArc(sketch, "E686", {"start": v(-37.87, 13.74) * mm, "mid": v(-37.75, 13.87) * mm, "end": v(-37.6, 13.92) * mm});
            skArc(sketch, "E687", {"start": v(-37.6, 13.92) * mm, "mid": v(-37.42, 13.87) * mm, "end": v(-37.3, 13.76) * mm});
            skArc(sketch, "E688", {"start": v(-37.3, 13.76) * mm, "mid": v(-37.23, 13.64) * mm, "end": v(-37.19, 13.52) * mm});
            skArc(sketch, "E689", {"start": v(-37.19, 13.52) * mm, "mid": v(-37.14, 13.32) * mm, "end": v(-37.1, 13.12) * mm});
            skArc(sketch, "E690", {"start": v(-37.1, 13.12) * mm, "mid": v(-37.06, 12.88) * mm, "end": v(-37.04, 12.65) * mm});
            skArc(sketch, "E691", {"start": v(-37.04, 12.65) * mm, "mid": v(-37.02, 12.4) * mm, "end": v(-37.01, 12.17) * mm});
            skArc(sketch, "E692", {"start": v(-37.01, 12.17) * mm, "mid": v(-37, 11.85) * mm, "end": v(-37, 11.53) * mm});
            skArc(sketch, "E693", {"start": v(-37, 11.53) * mm, "mid": v(-36.97, 11.37) * mm, "end": v(-36.9, 11.21) * mm});
            skArc(sketch, "E694", {"start": v(-36.9, 11.21) * mm, "mid": v(-36.84, 11.12) * mm, "end": v(-36.75, 11.05) * mm});
            skArc(sketch, "E695", {"start": v(-36.75, 11.05) * mm, "mid": v(-36.61, 11) * mm, "end": v(-36.47, 11) * mm});
            skArc(sketch, "E696", {"start": v(-36.47, 11) * mm, "mid": v(-36.32, 10.97) * mm, "end": v(-36.19, 10.92) * mm});
            skArc(sketch, "E697", {"start": v(-36.19, 10.92) * mm, "mid": v(-36.08, 10.83) * mm, "end": v(-36.01, 10.71) * mm});
            skArc(sketch, "E698", {"start": v(-36.01, 10.71) * mm, "mid": v(-35.95, 10.5) * mm, "end": v(-35.91, 10.3) * mm});
            skArc(sketch, "E699", {"start": v(-35.91, 10.3) * mm, "mid": v(-35.88, 9.86) * mm, "end": v(-35.85, 9.42) * mm});
            skLineSegment(sketch, "E700", {"start": v(-35.85, 9.42) * mm, "end": v(-35.77, 7.85) * mm});
            skLineSegment(sketch, "E701", {"start": v(-35.77, 7.85) * mm, "end": v(-34.38, 7.47) * mm});
            skArc(sketch, "E702", {"start": v(-34.38, 7.47) * mm, "mid": v(-34.01, 7.39) * mm, "end": v(-33.63, 7.32) * mm});
            skArc(sketch, "E703", {"start": v(-33.63, 7.32) * mm, "mid": v(-33.14, 7.27) * mm, "end": v(-32.65, 7.22) * mm});
            skArc(sketch, "E704", {"start": v(-32.65, 7.22) * mm, "mid": v(-32.08, 7.2) * mm, "end": v(-31.52, 7.18) * mm});
            skArc(sketch, "E705", {"start": v(-31.52, 7.18) * mm, "mid": v(-30.91, 7.18) * mm, "end": v(-30.3, 7.19) * mm});
            skArc(sketch, "E706", {"start": v(-30.3, 7.19) * mm, "mid": v(-29.49, 7.21) * mm, "end": v(-28.67, 7.23) * mm});
            skArc(sketch, "E707", {"start": v(-28.67, 7.23) * mm, "mid": v(-28.35, 7.22) * mm, "end": v(-28.02, 7.18) * mm});
            skArc(sketch, "E708", {"start": v(-28.02, 7.18) * mm, "mid": v(-27.86, 7.13) * mm, "end": v(-27.73, 7.04) * mm});
            skArc(sketch, "E709", {"start": v(-27.73, 7.04) * mm, "mid": v(-27.64, 6.9) * mm, "end": v(-27.6, 6.76) * mm});
            skArc(sketch, "E710", {"start": v(-27.6, 6.76) * mm, "mid": v(-27.62, 6.63) * mm, "end": v(-27.64, 6.5) * mm});
            skArc(sketch, "E711", {"start": v(-27.64, 6.5) * mm, "mid": v(-27.69, 6.33) * mm, "end": v(-27.75, 6.16) * mm});
            skArc(sketch, "E712", {"start": v(-27.75, 6.16) * mm, "mid": v(-27.82, 5.97) * mm, "end": v(-27.9, 5.79) * mm});
            skArc(sketch, "E713", {"start": v(-27.9, 5.79) * mm, "mid": v(-27.98, 5.61) * mm, "end": v(-28.08, 5.44) * mm});
            skArc(sketch, "E714", {"start": v(-28.08, 5.44) * mm, "mid": v(-28.16, 5.29) * mm, "end": v(-28.24, 5.12) * mm});
            skArc(sketch, "E715", {"start": v(-28.24, 5.12) * mm, "mid": v(-28.3, 4.97) * mm, "end": v(-28.35, 4.82) * mm});
            skArc(sketch, "E716", {"start": v(-28.35, 4.82) * mm, "mid": v(-28.37, 4.7) * mm, "end": v(-28.38, 4.57) * mm});
            skArc(sketch, "E717", {"start": v(-28.38, 4.57) * mm, "mid": v(-28.37, 4.5) * mm, "end": v(-28.33, 4.43) * mm});
            skArc(sketch, "E718", {"start": v(-28.33, 4.43) * mm, "mid": v(-28.07, 4.26) * mm, "end": v(-27.77, 4.2) * mm});
            skArc(sketch, "E719", {"start": v(-27.77, 4.2) * mm, "mid": v(-26.63, 4.23) * mm, "end": v(-25.48, 4.28) * mm});
            skArc(sketch, "E720", {"start": v(-25.48, 4.28) * mm, "mid": v(-24.33, 4.35) * mm, "end": v(-23.19, 4.45) * mm});
            skArc(sketch, "E721", {"start": v(-23.19, 4.45) * mm, "mid": v(-22.36, 4.57) * mm, "end": v(-21.54, 4.74) * mm});
            skArc(sketch, "E722", {"start": v(-21.54, 4.74) * mm, "mid": v(-21.2, 4.83) * mm, "end": v(-20.88, 4.91) * mm});
            skArc(sketch, "E723", {"start": v(-20.88, 4.91) * mm, "mid": v(-20.59, 4.99) * mm, "end": v(-20.3, 5.06) * mm});
            skArc(sketch, "E724", {"start": v(-20.3, 5.06) * mm, "mid": v(-20.05, 5.12) * mm, "end": v(-19.8, 5.18) * mm});
            skArc(sketch, "E725", {"start": v(-19.8, 5.18) * mm, "mid": v(-19.75, 5.18) * mm, "end": v(-19.71, 5.19) * mm});
            skArc(sketch, "E726", {"start": v(-19.71, 5.19) * mm, "mid": v(-19.62, 5.13) * mm, "end": v(-19.6, 5.02) * mm});
            skArc(sketch, "E727", {"start": v(-19.6, 5.02) * mm, "mid": v(-19.78, 4.64) * mm, "end": v(-19.98, 4.27) * mm});
            skArc(sketch, "E728", {"start": v(-19.98, 4.27) * mm, "mid": v(-20.22, 3.85) * mm, "end": v(-20.5, 3.44) * mm});
            skArc(sketch, "E729", {"start": v(-20.5, 3.44) * mm, "mid": v(-20.75, 3.1) * mm, "end": v(-21.03, 2.78) * mm});
            skLineSegment(sketch, "E730", {"start": v(-21.03, 2.78) * mm, "end": v(-21.9, 1.89) * mm});
            skLineSegment(sketch, "E731", {"start": v(-21.9, 1.89) * mm, "end": v(-21.09, 1.58) * mm});
            skArc(sketch, "E732", {"start": v(-21.09, 1.58) * mm, "mid": v(-20.86, 1.5) * mm, "end": v(-20.63, 1.45) * mm});
            skArc(sketch, "E733", {"start": v(-20.63, 1.45) * mm, "mid": v(-20.22, 1.38) * mm, "end": v(-19.8, 1.32) * mm});
            skArc(sketch, "E734", {"start": v(-19.8, 1.32) * mm, "mid": v(-19.33, 1.25) * mm, "end": v(-18.85, 1.2) * mm});
            skArc(sketch, "E735", {"start": v(-18.85, 1.2) * mm, "mid": v(-18.36, 1.15) * mm, "end": v(-17.86, 1.11) * mm});
            skLineSegment(sketch, "E736", {"start": v(-17.86, 1.11) * mm, "end": v(-15.44, 0.96) * mm});
            skLineSegment(sketch, "E737", {"start": v(-15.44, 0.96) * mm, "end": v(-15.44, 4.02) * mm});
            skArc(sketch, "E738", {"start": v(-15.44, 4.02) * mm, "mid": v(-15.44, 5) * mm, "end": v(-15.43, 5.96) * mm});
            skArc(sketch, "E739", {"start": v(-15.43, 5.96) * mm, "mid": v(-15.4, 6.32) * mm, "end": v(-15.36, 6.67) * mm});
            skArc(sketch, "E740", {"start": v(-15.36, 6.67) * mm, "mid": v(-15.3, 6.85) * mm, "end": v(-15.18, 7) * mm});
            skArc(sketch, "E741", {"start": v(-15.18, 7) * mm, "mid": v(-15.02, 7.11) * mm, "end": v(-14.84, 7.17) * mm});
            skArc(sketch, "E742", {"start": v(-14.84, 7.17) * mm, "mid": v(-14.67, 7.21) * mm, "end": v(-14.5, 7.28) * mm});
            skArc(sketch, "E743", {"start": v(-14.5, 7.28) * mm, "mid": v(-14.4, 7.37) * mm, "end": v(-14.34, 7.5) * mm});
            skArc(sketch, "E744", {"start": v(-14.34, 7.5) * mm, "mid": v(-14.29, 7.69) * mm, "end": v(-14.27, 7.9) * mm});
            skArc(sketch, "E745", {"start": v(-14.27, 7.9) * mm, "mid": v(-14.28, 8.36) * mm, "end": v(-14.3, 8.82) * mm});
            skArc(sketch, "E746", {"start": v(-14.3, 8.82) * mm, "mid": v(-14.31, 9.35) * mm, "end": v(-14.3, 9.88) * mm});
            skArc(sketch, "E747", {"start": v(-14.3, 9.88) * mm, "mid": v(-14.23, 10.2) * mm, "end": v(-14.1, 10.5) * mm});
            skArc(sketch, "E748", {"start": v(-14.1, 10.5) * mm, "mid": v(-13.98, 10.58) * mm, "end": v(-13.84, 10.54) * mm});
            skArc(sketch, "E749", {"start": v(-13.84, 10.54) * mm, "mid": v(-13.67, 10.34) * mm, "end": v(-13.55, 10.1) * mm});
            skArc(sketch, "E750", {"start": v(-13.55, 10.1) * mm, "mid": v(-13.5, 9.95) * mm, "end": v(-13.47, 9.78) * mm});
            skArc(sketch, "E751", {"start": v(-13.47, 9.78) * mm, "mid": v(-13.44, 9.55) * mm, "end": v(-13.42, 9.31) * mm});
            skArc(sketch, "E752", {"start": v(-13.42, 9.31) * mm, "mid": v(-13.41, 9.05) * mm, "end": v(-13.41, 8.8) * mm});
            skArc(sketch, "E753", {"start": v(-13.41, 8.8) * mm, "mid": v(-13.42, 8.54) * mm, "end": v(-13.44, 8.3) * mm});
            skArc(sketch, "E754", {"start": v(-13.44, 8.3) * mm, "mid": v(-13.48, 7.93) * mm, "end": v(-13.5, 7.57) * mm});
            skArc(sketch, "E755", {"start": v(-13.5, 7.57) * mm, "mid": v(-13.5, 7.43) * mm, "end": v(-13.44, 7.3) * mm});
            skArc(sketch, "E756", {"start": v(-13.44, 7.3) * mm, "mid": v(-13.37, 7.2) * mm, "end": v(-13.26, 7.16) * mm});
            skArc(sketch, "E757", {"start": v(-13.26, 7.16) * mm, "mid": v(-13.06, 7.13) * mm, "end": v(-12.85, 7.12) * mm});
            skLineSegment(sketch, "E758", {"start": v(-12.85, 7.12) * mm, "end": v(-12.12, 7.12) * mm});
            skLineSegment(sketch, "E759", {"start": v(-12.12, 7.12) * mm, "end": v(-12.12, 4.22) * mm});
            skLineSegment(sketch, "E760", {"start": v(-12.12, 4.22) * mm, "end": v(-12.12, 1.31) * mm});
            skLineSegment(sketch, "E761", {"start": v(-12.12, 1.31) * mm, "end": v(-10.67, 1.32) * mm});
            skArc(sketch, "E762", {"start": v(-10.67, 1.32) * mm, "mid": v(-10.36, 1.32) * mm, "end": v(-10.04, 1.34) * mm});
            skArc(sketch, "E763", {"start": v(-10.04, 1.34) * mm, "mid": v(-9.69, 1.37) * mm, "end": v(-9.34, 1.4) * mm});
            skArc(sketch, "E764", {"start": v(-9.34, 1.4) * mm, "mid": v(-9, 1.45) * mm, "end": v(-8.67, 1.5) * mm});
            skArc(sketch, "E765", {"start": v(-8.67, 1.5) * mm, "mid": v(-8.41, 1.55) * mm, "end": v(-8.16, 1.61) * mm});
            skArc(sketch, "E766", {"start": v(-8.16, 1.61) * mm, "mid": v(-7.95, 1.67) * mm, "end": v(-7.74, 1.71) * mm});
            skArc(sketch, "E767", {"start": v(-7.74, 1.71) * mm, "mid": v(-7.55, 1.75) * mm, "end": v(-7.36, 1.77) * mm});
            skArc(sketch, "E768", {"start": v(-7.36, 1.77) * mm, "mid": v(-7.2, 1.79) * mm, "end": v(-7.05, 1.8) * mm});
            skArc(sketch, "E769", {"start": v(-7.05, 1.8) * mm, "mid": v(-7, 1.78) * mm, "end": v(-6.94, 1.75) * mm});
            skArc(sketch, "E770", {"start": v(-6.94, 1.75) * mm, "mid": v(-6.86, 1.57) * mm, "end": v(-6.91, 1.38) * mm});
            skArc(sketch, "E771", {"start": v(-6.91, 1.38) * mm, "mid": v(-7.32, 0.89) * mm, "end": v(-7.75, 0.4) * mm});
            skArc(sketch, "E772", {"start": v(-7.75, 0.4) * mm, "mid": v(-8.26, -0.12) * mm, "end": v(-8.8, -0.61) * mm});
            skArc(sketch, "E773", {"start": v(-8.8, -0.61) * mm, "mid": v(-9.32, -1.03) * mm, "end": v(-9.87, -1.42) * mm});
            skLineSegment(sketch, "E774", {"start": v(-9.87, -1.42) * mm, "end": v(-11.3, -2.36) * mm});
            skLineSegment(sketch, "E775", {"start": v(-11.3, -2.36) * mm, "end": v(-10.62, -3.26) * mm});
            skLineSegment(sketch, "E776", {"start": v(-10.62, -3.26) * mm, "end": v(-9.93, -4.16) * mm});
            skLineSegment(sketch, "E777", {"start": v(-9.93, -4.16) * mm, "end": v(-10.72, -4.27) * mm});
            skArc(sketch, "E778", {"start": v(-10.72, -4.27) * mm, "mid": v(-11.4, -4.33) * mm, "end": v(-12.07, -4.33) * mm});
            skArc(sketch, "E779", {"start": v(-12.07, -4.33) * mm, "mid": v(-13, -4.25) * mm, "end": v(-13.93, -4.14) * mm});
            skArc(sketch, "E780", {"start": v(-13.93, -4.14) * mm, "mid": v(-14.84, -4) * mm, "end": v(-15.74, -3.8) * mm});
            skArc(sketch, "E781", {"start": v(-15.74, -3.8) * mm, "mid": v(-16.32, -3.64) * mm, "end": v(-16.88, -3.4) * mm});
            skArc(sketch, "E782", {"start": v(-16.88, -3.4) * mm, "mid": v(-17.34, -3.17) * mm, "end": v(-17.82, -2.99) * mm});
            skArc(sketch, "E783", {"start": v(-17.82, -2.99) * mm, "mid": v(-18.07, -2.97) * mm, "end": v(-18.3, -3.08) * mm});
            skArc(sketch, "E784", {"start": v(-18.3, -3.08) * mm, "mid": v(-18.45, -3.28) * mm, "end": v(-18.48, -3.54) * mm});
            skArc(sketch, "E785", {"start": v(-18.48, -3.54) * mm, "mid": v(-18.4, -4.05) * mm, "end": v(-18.29, -4.56) * mm});
            skArc(sketch, "E786", {"start": v(-18.29, -4.56) * mm, "mid": v(-18.23, -4.79) * mm, "end": v(-18.17, -5.02) * mm});
            skArc(sketch, "E787", {"start": v(-18.17, -5.02) * mm, "mid": v(-18.13, -5.22) * mm, "end": v(-18.1, -5.42) * mm});
            skArc(sketch, "E788", {"start": v(-18.1, -5.42) * mm, "mid": v(-18.07, -5.58) * mm, "end": v(-18.04, -5.75) * mm});
            skArc(sketch, "E789", {"start": v(-18.04, -5.75) * mm, "mid": v(-18.05, -5.8) * mm, "end": v(-18.07, -5.83) * mm});
            skArc(sketch, "E790", {"start": v(-18.07, -5.83) * mm, "mid": v(-18.21, -5.91) * mm, "end": v(-18.38, -5.92) * mm});
            skArc(sketch, "E791", {"start": v(-18.38, -5.92) * mm, "mid": v(-19.2, -5.73) * mm, "end": v(-20, -5.53) * mm});
            skArc(sketch, "E792", {"start": v(-20, -5.53) * mm, "mid": v(-20.8, -5.31) * mm, "end": v(-21.6, -5.08) * mm});
            skArc(sketch, "E793", {"start": v(-21.6, -5.08) * mm, "mid": v(-22.2, -4.87) * mm, "end": v(-22.8, -4.63) * mm});
            skArc(sketch, "E794", {"start": v(-22.8, -4.63) * mm, "mid": v(-23.13, -4.47) * mm, "end": v(-23.46, -4.29) * mm});
            skArc(sketch, "E795", {"start": v(-23.46, -4.29) * mm, "mid": v(-23.9, -4.01) * mm, "end": v(-24.33, -3.73) * mm});
            skArc(sketch, "E796", {"start": v(-24.33, -3.73) * mm, "mid": v(-24.79, -3.42) * mm, "end": v(-25.23, -3.1) * mm});
            skArc(sketch, "E797", {"start": v(-25.23, -3.1) * mm, "mid": v(-25.64, -2.77) * mm, "end": v(-26.04, -2.45) * mm});
            skLineSegment(sketch, "E798", {"start": v(-26.04, -2.45) * mm, "end": v(-27.89, -0.88) * mm});
            skLineSegment(sketch, "E799", {"start": v(-27.89, -0.88) * mm, "end": v(-27.89, -2.41) * mm});
            skArc(sketch, "E800", {"start": v(-27.89, -2.41) * mm, "mid": v(-27.89, -2.7) * mm, "end": v(-27.9, -3) * mm});
            skArc(sketch, "E801", {"start": v(-27.9, -3) * mm, "mid": v(-27.92, -3.24) * mm, "end": v(-27.95, -3.5) * mm});
            skArc(sketch, "E802", {"start": v(-27.95, -3.5) * mm, "mid": v(-27.99, -3.68) * mm, "end": v(-28.03, -3.87) * mm});
            skArc(sketch, "E803", {"start": v(-28.03, -3.87) * mm, "mid": v(-28.06, -3.92) * mm, "end": v(-28.12, -3.94) * mm});
            skArc(sketch, "E804", {"start": v(-28.12, -3.94) * mm, "mid": v(-28.6, -3.86) * mm, "end": v(-29.04, -3.64) * mm});
            skArc(sketch, "E805", {"start": v(-29.04, -3.64) * mm, "mid": v(-30.11, -2.85) * mm, "end": v(-31.16, -2.04) * mm});
            skArc(sketch, "E806", {"start": v(-31.16, -2.04) * mm, "mid": v(-32.19, -1.19) * mm, "end": v(-33.19, -0.3) * mm});
            skArc(sketch, "E807", {"start": v(-33.19, -0.3) * mm, "mid": v(-33.79, 0.31) * mm, "end": v(-34.31, 1) * mm});
            skArc(sketch, "E808", {"start": v(-34.31, 1) * mm, "mid": v(-34.5, 1.23) * mm, "end": v(-34.73, 1.43) * mm});
            skArc(sketch, "E809", {"start": v(-34.73, 1.43) * mm, "mid": v(-34.9, 1.48) * mm, "end": v(-35.07, 1.4) * mm});
            skArc(sketch, "E810", {"start": v(-35.07, 1.4) * mm, "mid": v(-35.22, 1.18) * mm, "end": v(-35.3, 0.92) * mm});
            skArc(sketch, "E811", {"start": v(-35.3, 0.92) * mm, "mid": v(-35.34, 0.42) * mm, "end": v(-35.35, -0.09) * mm});
            skLineSegment(sketch, "E812", {"start": v(-35.35, -0.09) * mm, "end": v(-35.35, -1.46) * mm});
            skLineSegment(sketch, "E813", {"start": v(-35.35, -1.46) * mm, "end": v(-36.79, -0.73) * mm});
            skArc(sketch, "E814", {"start": v(-36.79, -0.73) * mm, "mid": v(-37.12, -0.55) * mm, "end": v(-37.44, -0.35) * mm});
            skArc(sketch, "E815", {"start": v(-37.44, -0.35) * mm, "mid": v(-37.84, -0.07) * mm, "end": v(-38.23, 0.22) * mm});
            skArc(sketch, "E816", {"start": v(-38.23, 0.22) * mm, "mid": v(-38.63, 0.54) * mm, "end": v(-39.02, 0.86) * mm});
            skArc(sketch, "E817", {"start": v(-39.02, 0.86) * mm, "mid": v(-39.36, 1.17) * mm, "end": v(-39.68, 1.49) * mm});
            skArc(sketch, "E818", {"start": v(-39.68, 1.49) * mm, "mid": v(-39.96, 1.77) * mm, "end": v(-40.25, 2.06) * mm});
            skArc(sketch, "E819", {"start": v(-40.25, 2.06) * mm, "mid": v(-40.5, 2.3) * mm, "end": v(-40.75, 2.54) * mm});
            skArc(sketch, "E820", {"start": v(-40.75, 2.54) * mm, "mid": v(-40.97, 2.74) * mm, "end": v(-41.19, 2.94) * mm});
            skArc(sketch, "E821", {"start": v(-41.19, 2.94) * mm, "mid": v(-41.23, 2.96) * mm, "end": v(-41.28, 2.97) * mm});
            skArc(sketch, "E822", {"start": v(-41.28, 2.97) * mm, "mid": v(-41.32, 2.96) * mm, "end": v(-41.34, 2.92) * mm});
            skArc(sketch, "E823", {"start": v(-41.34, 2.92) * mm, "mid": v(-41.37, 2.74) * mm, "end": v(-41.39, 2.56) * mm});
            skArc(sketch, "E824", {"start": v(-41.39, 2.56) * mm, "mid": v(-41.41, 2.34) * mm, "end": v(-41.42, 2.11) * mm});
            skArc(sketch, "E825", {"start": v(-41.42, 2.11) * mm, "mid": v(-41.43, 1.85) * mm, "end": v(-41.43, 1.58) * mm});
            skLineSegment(sketch, "E826", {"start": v(-41.43, 1.58) * mm, "end": v(-41.43, 0.18) * mm});
            skLineSegment(sketch, "E827", {"start": v(-41.43, 0.18) * mm, "end": v(-42.6, 1) * mm});
            skArc(sketch, "E828", {"start": v(-42.6, 1) * mm, "mid": v(-42.86, 1.17) * mm, "end": v(-43.1, 1.36) * mm});
            skArc(sketch, "E829", {"start": v(-43.1, 1.36) * mm, "mid": v(-43.37, 1.57) * mm, "end": v(-43.64, 1.78) * mm});
            skArc(sketch, "E830", {"start": v(-43.64, 1.78) * mm, "mid": v(-43.88, 1.99) * mm, "end": v(-44.12, 2.2) * mm});
            skArc(sketch, "E831", {"start": v(-44.12, 2.2) * mm, "mid": v(-44.29, 2.36) * mm, "end": v(-44.45, 2.53) * mm});
            skArc(sketch, "E832", {"start": v(-44.45, 2.53) * mm, "mid": v(-44.83, 2.9) * mm, "end": v(-45.23, 3.22) * mm});
            skArc(sketch, "E833", {"start": v(-45.23, 3.22) * mm, "mid": v(-45.43, 3.25) * mm, "end": v(-45.56, 3.1) * mm});
            skArc(sketch, "E834", {"start": v(-45.56, 3.1) * mm, "mid": v(-45.6, 2.77) * mm, "end": v(-45.53, 2.43) * mm});
            skArc(sketch, "E835", {"start": v(-45.53, 2.43) * mm, "mid": v(-45.23, 1.73) * mm, "end": v(-44.9, 1.05) * mm});
            skArc(sketch, "E836", {"start": v(-44.9, 1.05) * mm, "mid": v(-44.54, 0.41) * mm, "end": v(-44.13, -0.18) * mm});
            skArc(sketch, "E837", {"start": v(-44.13, -0.18) * mm, "mid": v(-43.66, -0.76) * mm, "end": v(-43.15, -1.3) * mm});
            skArc(sketch, "E838", {"start": v(-43.15, -1.3) * mm, "mid": v(-42.52, -1.88) * mm, "end": v(-41.85, -2.41) * mm});
            skArc(sketch, "E839", {"start": v(-41.85, -2.41) * mm, "mid": v(-41, -3.02) * mm, "end": v(-40.13, -3.59) * mm});
            skArc(sketch, "E840", {"start": v(-40.13, -3.59) * mm, "mid": v(-39.74, -3.84) * mm, "end": v(-39.36, -4.1) * mm});
            skArc(sketch, "E841", {"start": v(-39.36, -4.1) * mm, "mid": v(-39.03, -4.31) * mm, "end": v(-38.7, -4.54) * mm});
            skArc(sketch, "E842", {"start": v(-38.7, -4.54) * mm, "mid": v(-38.44, -4.74) * mm, "end": v(-38.17, -4.94) * mm});
            skArc(sketch, "E843", {"start": v(-38.17, -4.94) * mm, "mid": v(-38.13, -4.99) * mm, "end": v(-38.12, -5.05) * mm});
            skArc(sketch, "E844", {"start": v(-38.12, -5.05) * mm, "mid": v(-38.12, -5.1) * mm, "end": v(-38.15, -5.15) * mm});
            skArc(sketch, "E845", {"start": v(-38.15, -5.15) * mm, "mid": v(-38.23, -5.26) * mm, "end": v(-38.32, -5.36) * mm});
            skArc(sketch, "E846", {"start": v(-38.32, -5.36) * mm, "mid": v(-38.43, -5.49) * mm, "end": v(-38.54, -5.61) * mm});
            skArc(sketch, "E847", {"start": v(-38.54, -5.61) * mm, "mid": v(-38.67, -5.75) * mm, "end": v(-38.8, -5.87) * mm});
            skArc(sketch, "E848", {"start": v(-38.8, -5.87) * mm, "mid": v(-39, -6.07) * mm, "end": v(-39.2, -6.27) * mm});
            skArc(sketch, "E849", {"start": v(-39.2, -6.27) * mm, "mid": v(-39.28, -6.38) * mm, "end": v(-39.32, -6.5) * mm});
            skArc(sketch, "E850", {"start": v(-39.32, -6.5) * mm, "mid": v(-39.32, -6.6) * mm, "end": v(-39.29, -6.7) * mm});
            skArc(sketch, "E851", {"start": v(-39.29, -6.7) * mm, "mid": v(-39.18, -6.86) * mm, "end": v(-39.06, -7) * mm});
            skArc(sketch, "E852", {"start": v(-39.06, -7) * mm, "mid": v(-38.8, -7.25) * mm, "end": v(-38.5, -7.45) * mm});
            skArc(sketch, "E853", {"start": v(-38.5, -7.45) * mm, "mid": v(-37.97, -7.72) * mm, "end": v(-37.42, -7.98) * mm});
            skArc(sketch, "E854", {"start": v(-37.42, -7.98) * mm, "mid": v(-36.83, -8.24) * mm, "end": v(-36.22, -8.47) * mm});
            skArc(sketch, "E855", {"start": v(-36.22, -8.47) * mm, "mid": v(-35.69, -8.64) * mm, "end": v(-35.14, -8.77) * mm});
            skArc(sketch, "E856", {"start": v(-35.14, -8.77) * mm, "mid": v(-34.86, -8.82) * mm, "end": v(-34.57, -8.87) * mm});
            skArc(sketch, "E857", {"start": v(-34.57, -8.87) * mm, "mid": v(-34.45, -8.86) * mm, "end": v(-34.36, -8.8) * mm});
            skArc(sketch, "E858", {"start": v(-34.36, -8.8) * mm, "mid": v(-34.29, -8.7) * mm, "end": v(-34.26, -8.57) * mm});
            skArc(sketch, "E859", {"start": v(-34.26, -8.57) * mm, "mid": v(-34.25, -8.21) * mm, "end": v(-34.24, -7.85) * mm});
            skArc(sketch, "E860", {"start": v(-34.24, -7.85) * mm, "mid": v(-34.24, -7.55) * mm, "end": v(-34.22, -7.25) * mm});
            skArc(sketch, "E861", {"start": v(-34.22, -7.25) * mm, "mid": v(-34.2, -7.09) * mm, "end": v(-34.13, -6.93) * mm});
            skArc(sketch, "E862", {"start": v(-34.13, -6.93) * mm, "mid": v(-34.06, -6.83) * mm, "end": v(-33.95, -6.75) * mm});
            skArc(sketch, "E863", {"start": v(-33.95, -6.75) * mm, "mid": v(-33.8, -6.7) * mm, "end": v(-33.63, -6.65) * mm});
            skArc(sketch, "E864", {"start": v(-33.63, -6.65) * mm, "mid": v(-33.46, -6.61) * mm, "end": v(-33.3, -6.55) * mm});
            skArc(sketch, "E865", {"start": v(-33.3, -6.55) * mm, "mid": v(-33.2, -6.46) * mm, "end": v(-33.13, -6.35) * mm});
            skArc(sketch, "E866", {"start": v(-33.13, -6.35) * mm, "mid": v(-33.09, -6.17) * mm, "end": v(-33.07, -5.98) * mm});
            skArc(sketch, "E867", {"start": v(-33.07, -5.98) * mm, "mid": v(-33.08, -5.56) * mm, "end": v(-33.1, -5.14) * mm});
            skArc(sketch, "E868", {"start": v(-33.1, -5.14) * mm, "mid": v(-33.11, -4.84) * mm, "end": v(-33.11, -4.54) * mm});
            skArc(sketch, "E869", {"start": v(-33.11, -4.54) * mm, "mid": v(-33.1, -4.3) * mm, "end": v(-33.07, -4.05) * mm});
            skArc(sketch, "E870", {"start": v(-33.07, -4.05) * mm, "mid": v(-33.03, -3.87) * mm, "end": v(-32.98, -3.69) * mm});
            skArc(sketch, "E871", {"start": v(-32.98, -3.69) * mm, "mid": v(-32.93, -3.59) * mm, "end": v(-32.85, -3.52) * mm});
            skArc(sketch, "E872", {"start": v(-32.85, -3.52) * mm, "mid": v(-32.68, -3.47) * mm, "end": v(-32.5, -3.5) * mm});
            skArc(sketch, "E873", {"start": v(-32.5, -3.5) * mm, "mid": v(-32.34, -3.63) * mm, "end": v(-32.24, -3.8) * mm});
            skArc(sketch, "E874", {"start": v(-32.24, -3.8) * mm, "mid": v(-32.15, -4.13) * mm, "end": v(-32.1, -4.47) * mm});
            skArc(sketch, "E875", {"start": v(-32.1, -4.47) * mm, "mid": v(-32.11, -4.93) * mm, "end": v(-32.14, -5.4) * mm});
            skArc(sketch, "E876", {"start": v(-32.14, -5.4) * mm, "mid": v(-32.18, -5.8) * mm, "end": v(-32.22, -6.2) * mm});
            skArc(sketch, "E877", {"start": v(-32.22, -6.2) * mm, "mid": v(-32.2, -6.36) * mm, "end": v(-32.17, -6.52) * mm});
            skArc(sketch, "E878", {"start": v(-32.17, -6.52) * mm, "mid": v(-32.1, -6.6) * mm, "end": v(-32, -6.66) * mm});
            skArc(sketch, "E879", {"start": v(-32, -6.66) * mm, "mid": v(-31.8, -6.7) * mm, "end": v(-31.6, -6.7) * mm});
            skArc(sketch, "E880", {"start": v(-31.6, -6.7) * mm, "mid": v(-31.41, -6.72) * mm, "end": v(-31.22, -6.76) * mm});
            skArc(sketch, "E881", {"start": v(-31.22, -6.76) * mm, "mid": v(-31.1, -6.82) * mm, "end": v(-31.03, -6.92) * mm});
            skArc(sketch, "E882", {"start": v(-31.03, -6.92) * mm, "mid": v(-30.97, -7.09) * mm, "end": v(-30.94, -7.26) * mm});
            skArc(sketch, "E883", {"start": v(-30.94, -7.26) * mm, "mid": v(-30.93, -7.7) * mm, "end": v(-30.93, -8.13) * mm});
            skLineSegment(sketch, "E884", {"start": v(-30.93, -8.13) * mm, "end": v(-30.93, -9.55) * mm});
            skLineSegment(sketch, "E885", {"start": v(-30.93, -9.55) * mm, "end": v(-28.65, -9.38) * mm});
            skArc(sketch, "E886", {"start": v(-28.65, -9.38) * mm, "mid": v(-28.18, -9.34) * mm, "end": v(-27.71, -9.3) * mm});
            skArc(sketch, "E887", {"start": v(-27.71, -9.3) * mm, "mid": v(-27.26, -9.25) * mm, "end": v(-26.8, -9.2) * mm});
            skArc(sketch, "E888", {"start": v(-26.8, -9.2) * mm, "mid": v(-26.4, -9.15) * mm, "end": v(-26.01, -9.1) * mm});
            skArc(sketch, "E889", {"start": v(-26.01, -9.1) * mm, "mid": v(-25.79, -9.07) * mm, "end": v(-25.56, -9.02) * mm});
            skArc(sketch, "E890", {"start": v(-25.56, -9.02) * mm, "mid": v(-25.31, -8.97) * mm, "end": v(-25.06, -8.92) * mm});
            skArc(sketch, "E891", {"start": v(-25.06, -8.92) * mm, "mid": v(-24.97, -8.93) * mm, "end": v(-24.9, -8.97) * mm});
            skArc(sketch, "E892", {"start": v(-24.9, -8.97) * mm, "mid": v(-24.85, -9.05) * mm, "end": v(-24.84, -9.14) * mm});
            skArc(sketch, "E893", {"start": v(-24.84, -9.14) * mm, "mid": v(-24.88, -9.39) * mm, "end": v(-24.93, -9.64) * mm});
            skArc(sketch, "E894", {"start": v(-24.93, -9.64) * mm, "mid": v(-24.97, -9.81) * mm, "end": v(-25.01, -10) * mm});
            skArc(sketch, "E895", {"start": v(-25.01, -10) * mm, "mid": v(-25.06, -10.2) * mm, "end": v(-25.11, -10.4) * mm});
            skArc(sketch, "E896", {"start": v(-25.11, -10.4) * mm, "mid": v(-25.16, -10.6) * mm, "end": v(-25.21, -10.8) * mm});
            skArc(sketch, "E897", {"start": v(-25.21, -10.8) * mm, "mid": v(-25.25, -10.95) * mm, "end": v(-25.3, -11.1) * mm});
            skArc(sketch, "E898", {"start": v(-25.3, -11.1) * mm, "mid": v(-25.34, -11.3) * mm, "end": v(-25.36, -11.5) * mm});
            skArc(sketch, "E899", {"start": v(-25.36, -11.5) * mm, "mid": v(-25.33, -11.6) * mm, "end": v(-25.24, -11.66) * mm});
            skArc(sketch, "E900", {"start": v(-25.24, -11.66) * mm, "mid": v(-25.08, -11.7) * mm, "end": v(-24.91, -11.7) * mm});
            skArc(sketch, "E901", {"start": v(-24.91, -11.7) * mm, "mid": v(-24.34, -11.65) * mm, "end": v(-23.76, -11.59) * mm});
            skArc(sketch, "E902", {"start": v(-23.76, -11.59) * mm, "mid": v(-23.37, -11.54) * mm, "end": v(-22.98, -11.49) * mm});
            skArc(sketch, "E903", {"start": v(-22.98, -11.49) * mm, "mid": v(-22.52, -11.41) * mm, "end": v(-22.05, -11.33) * mm});
            skArc(sketch, "E904", {"start": v(-22.05, -11.33) * mm, "mid": v(-21.6, -11.25) * mm, "end": v(-21.13, -11.16) * mm});
            skArc(sketch, "E905", {"start": v(-21.13, -11.16) * mm, "mid": v(-20.75, -11.07) * mm, "end": v(-20.37, -10.98) * mm});
            skArc(sketch, "E906", {"start": v(-20.37, -10.98) * mm, "mid": v(-20.04, -10.9) * mm, "end": v(-19.72, -10.82) * mm});
            skArc(sketch, "E907", {"start": v(-19.72, -10.82) * mm, "mid": v(-19.43, -10.76) * mm, "end": v(-19.15, -10.71) * mm});
            skArc(sketch, "E908", {"start": v(-19.15, -10.71) * mm, "mid": v(-18.91, -10.68) * mm, "end": v(-18.68, -10.64) * mm});
            skArc(sketch, "E909", {"start": v(-18.68, -10.64) * mm, "mid": v(-18.61, -10.65) * mm, "end": v(-18.56, -10.68) * mm});
            skArc(sketch, "E910", {"start": v(-18.56, -10.68) * mm, "mid": v(-18.5, -10.81) * mm, "end": v(-18.52, -10.96) * mm});
            skArc(sketch, "E911", {"start": v(-18.52, -10.96) * mm, "mid": v(-18.78, -11.4) * mm, "end": v(-19.05, -11.83) * mm});
            skArc(sketch, "E912", {"start": v(-19.05, -11.83) * mm, "mid": v(-19.33, -12.25) * mm, "end": v(-19.64, -12.66) * mm});
            skArc(sketch, "E913", {"start": v(-19.64, -12.66) * mm, "mid": v(-19.85, -12.88) * mm, "end": v(-20.1, -13.06) * mm});
            skArc(sketch, "E914", {"start": v(-20.1, -13.06) * mm, "mid": v(-20.23, -13.15) * mm, "end": v(-20.35, -13.24) * mm});
            skArc(sketch, "E915", {"start": v(-20.35, -13.24) * mm, "mid": v(-20.4, -13.3) * mm, "end": v(-20.4, -13.36) * mm});
            skArc(sketch, "E916", {"start": v(-20.4, -13.36) * mm, "mid": v(-20.38, -13.44) * mm, "end": v(-20.33, -13.5) * mm});
            skArc(sketch, "E917", {"start": v(-20.33, -13.5) * mm, "mid": v(-20.18, -13.63) * mm, "end": v(-20.02, -13.76) * mm});
            skArc(sketch, "E918", {"start": v(-20.02, -13.76) * mm, "mid": v(-19.46, -14.1) * mm, "end": v(-18.85, -14.35) * mm});
            skArc(sketch, "E919", {"start": v(-18.85, -14.35) * mm, "mid": v(-17.86, -14.6) * mm, "end": v(-16.85, -14.8) * mm});
            skArc(sketch, "E920", {"start": v(-16.85, -14.8) * mm, "mid": v(-15.85, -14.96) * mm, "end": v(-14.84, -15.08) * mm});
            skArc(sketch, "E921", {"start": v(-14.84, -15.08) * mm, "mid": v(-14.5, -15.01) * mm, "end": v(-14.23, -14.77) * mm});
            skArc(sketch, "E922", {"start": v(-14.23, -14.77) * mm, "mid": v(-14.2, -14.7) * mm, "end": v(-14.24, -14.6) * mm});
            skArc(sketch, "E923", {"start": v(-14.24, -14.6) * mm, "mid": v(-14.36, -14.45) * mm, "end": v(-14.49, -14.3) * mm});
            skArc(sketch, "E924", {"start": v(-14.49, -14.3) * mm, "mid": v(-14.67, -14.12) * mm, "end": v(-14.87, -13.94) * mm});
            skArc(sketch, "E925", {"start": v(-14.87, -13.94) * mm, "mid": v(-15.12, -13.75) * mm, "end": v(-15.37, -13.57) * mm});
            skArc(sketch, "E926", {"start": v(-15.37, -13.57) * mm, "mid": v(-15.68, -13.35) * mm, "end": v(-15.99, -13.12) * mm});
            skArc(sketch, "E927", {"start": v(-15.99, -13.12) * mm, "mid": v(-16.14, -13) * mm, "end": v(-16.28, -12.84) * mm});
            skArc(sketch, "E928", {"start": v(-16.28, -12.84) * mm, "mid": v(-16.32, -12.76) * mm, "end": v(-16.32, -12.67) * mm});
            skArc(sketch, "E929", {"start": v(-16.32, -12.67) * mm, "mid": v(-16.28, -12.6) * mm, "end": v(-16.2, -12.57) * mm});
            skArc(sketch, "E930", {"start": v(-16.2, -12.57) * mm, "mid": v(-16.1, -12.53) * mm, "end": v(-16, -12.47) * mm});
            skArc(sketch, "E931", {"start": v(-16, -12.47) * mm, "mid": v(-15.9, -12.4) * mm, "end": v(-15.84, -12.3) * mm});
            skArc(sketch, "E932", {"start": v(-15.84, -12.3) * mm, "mid": v(-15.78, -12.17) * mm, "end": v(-15.75, -12.03) * mm});
            skArc(sketch, "E933", {"start": v(-15.75, -12.03) * mm, "mid": v(-15.73, -11.86) * mm, "end": v(-15.72, -11.68) * mm});
            skArc(sketch, "E934", {"start": v(-15.72, -11.68) * mm, "mid": v(-15.7, -11.33) * mm, "end": v(-15.65, -10.99) * mm});
            skArc(sketch, "E935", {"start": v(-15.65, -10.99) * mm, "mid": v(-15.57, -10.84) * mm, "end": v(-15.4, -10.77) * mm});
            skArc(sketch, "E936", {"start": v(-15.4, -10.77) * mm, "mid": v(-15.2, -10.8) * mm, "end": v(-15.03, -10.9) * mm});
            skArc(sketch, "E937", {"start": v(-15.03, -10.9) * mm, "mid": v(-14.7, -11.21) * mm, "end": v(-14.4, -11.55) * mm});
            skArc(sketch, "E938", {"start": v(-14.4, -11.55) * mm, "mid": v(-14.08, -11.9) * mm, "end": v(-13.74, -12.25) * mm});
            skArc(sketch, "E939", {"start": v(-13.74, -12.25) * mm, "mid": v(-13.52, -12.4) * mm, "end": v(-13.27, -12.5) * mm});
            skArc(sketch, "E940", {"start": v(-13.27, -12.5) * mm, "mid": v(-13.13, -12.46) * mm, "end": v(-13.05, -12.33) * mm});
            skArc(sketch, "E941", {"start": v(-13.05, -12.33) * mm, "mid": v(-13.03, -12.08) * mm, "end": v(-13.07, -11.82) * mm});
            skArc(sketch, "E942", {"start": v(-13.07, -11.82) * mm, "mid": v(-13.1, -11.64) * mm, "end": v(-13.14, -11.45) * mm});
            skArc(sketch, "E943", {"start": v(-13.14, -11.45) * mm, "mid": v(-13.13, -11.36) * mm, "end": v(-13.1, -11.26) * mm});
            skArc(sketch, "E944", {"start": v(-13.1, -11.26) * mm, "mid": v(-13.04, -11.2) * mm, "end": v(-12.96, -11.16) * mm});
            skArc(sketch, "E945", {"start": v(-12.96, -11.16) * mm, "mid": v(-12.82, -11.14) * mm, "end": v(-12.68, -11.13) * mm});
            skArc(sketch, "E946", {"start": v(-12.68, -11.13) * mm, "mid": v(-12.5, -11.1) * mm, "end": v(-12.32, -11.02) * mm});
            skArc(sketch, "E947", {"start": v(-12.32, -11.02) * mm, "mid": v(-12.2, -10.9) * mm, "end": v(-12.14, -10.75) * mm});
            skArc(sketch, "E948", {"start": v(-12.14, -10.75) * mm, "mid": v(-12.15, -10.58) * mm, "end": v(-12.22, -10.43) * mm});
            skArc(sketch, "E949", {"start": v(-12.22, -10.43) * mm, "mid": v(-12.36, -10.3) * mm, "end": v(-12.53, -10.2) * mm});
            skArc(sketch, "E950", {"start": v(-12.53, -10.2) * mm, "mid": v(-12.79, -10.06) * mm, "end": v(-13, -9.86) * mm});
            skArc(sketch, "E951", {"start": v(-13, -9.86) * mm, "mid": v(-13.4, -9.38) * mm, "end": v(-13.77, -8.88) * mm});
            skArc(sketch, "E952", {"start": v(-13.77, -8.88) * mm, "mid": v(-14.12, -8.38) * mm, "end": v(-14.46, -7.86) * mm});
            skArc(sketch, "E953", {"start": v(-14.46, -7.86) * mm, "mid": v(-14.57, -7.6) * mm, "end": v(-14.61, -7.32) * mm});
            skArc(sketch, "E954", {"start": v(-14.61, -7.32) * mm, "mid": v(-14.6, -7.22) * mm, "end": v(-14.59, -7.12) * mm});
            skArc(sketch, "E955", {"start": v(-14.59, -7.12) * mm, "mid": v(-14.55, -7.08) * mm, "end": v(-14.5, -7.06) * mm});
            skArc(sketch, "E956", {"start": v(-14.5, -7.06) * mm, "mid": v(-14.42, -7.07) * mm, "end": v(-14.34, -7.1) * mm});
            skArc(sketch, "E957", {"start": v(-14.34, -7.1) * mm, "mid": v(-14.16, -7.22) * mm, "end": v(-13.97, -7.34) * mm});
            skArc(sketch, "E958", {"start": v(-13.97, -7.34) * mm, "mid": v(-13.8, -7.45) * mm, "end": v(-13.6, -7.54) * mm});
            skArc(sketch, "E959", {"start": v(-13.6, -7.54) * mm, "mid": v(-13.26, -7.68) * mm, "end": v(-12.92, -7.81) * mm});
            skArc(sketch, "E960", {"start": v(-12.92, -7.81) * mm, "mid": v(-12.51, -7.96) * mm, "end": v(-12.11, -8.1) * mm});
            skArc(sketch, "E961", {"start": v(-12.11, -8.1) * mm, "mid": v(-11.7, -8.24) * mm, "end": v(-11.28, -8.36) * mm});
            skArc(sketch, "E962", {"start": v(-11.28, -8.36) * mm, "mid": v(-10.5, -8.61) * mm, "end": v(-9.73, -8.9) * mm});
            skArc(sketch, "E963", {"start": v(-9.73, -8.9) * mm, "mid": v(-9.22, -9.15) * mm, "end": v(-8.75, -9.47) * mm});
            skArc(sketch, "E964", {"start": v(-8.75, -9.47) * mm, "mid": v(-8.38, -9.82) * mm, "end": v(-8.08, -10.22) * mm});
            skArc(sketch, "E965", {"start": v(-8.08, -10.22) * mm, "mid": v(-7.78, -10.75) * mm, "end": v(-7.53, -11.3) * mm});
            skArc(sketch, "E966", {"start": v(-7.53, -11.3) * mm, "mid": v(-7.34, -11.77) * mm, "end": v(-7.11, -12.22) * mm});
            skArc(sketch, "E967", {"start": v(-7.11, -12.22) * mm, "mid": v(-6.96, -12.4) * mm, "end": v(-6.74, -12.46) * mm});
            skArc(sketch, "E968", {"start": v(-6.74, -12.46) * mm, "mid": v(-6.55, -12.4) * mm, "end": v(-6.43, -12.25) * mm});
            skArc(sketch, "E969", {"start": v(-6.43, -12.25) * mm, "mid": v(-6.32, -11.82) * mm, "end": v(-6.24, -11.38) * mm});
            skArc(sketch, "E970", {"start": v(-6.24, -11.38) * mm, "mid": v(-6.16, -10.96) * mm, "end": v(-6.04, -10.55) * mm});
            skArc(sketch, "E971", {"start": v(-6.04, -10.55) * mm, "mid": v(-5.88, -10.19) * mm, "end": v(-5.68, -9.84) * mm});
            skArc(sketch, "E972", {"start": v(-5.68, -9.84) * mm, "mid": v(-5.47, -9.58) * mm, "end": v(-5.22, -9.36) * mm});
            skArc(sketch, "E973", {"start": v(-5.22, -9.36) * mm, "mid": v(-5, -9.24) * mm, "end": v(-4.74, -9.2) * mm});
            skArc(sketch, "E974", {"start": v(-4.74, -9.2) * mm, "mid": v(-4.65, -9.2) * mm, "end": v(-4.57, -9.25) * mm});
            skArc(sketch, "E975", {"start": v(-4.57, -9.25) * mm, "mid": v(-4.46, -9.35) * mm, "end": v(-4.35, -9.46) * mm});
            skArc(sketch, "E976", {"start": v(-4.35, -9.46) * mm, "mid": v(-4.24, -9.6) * mm, "end": v(-4.15, -9.76) * mm});
            skArc(sketch, "E977", {"start": v(-4.15, -9.76) * mm, "mid": v(-4.05, -9.93) * mm, "end": v(-3.97, -10.11) * mm});
            skArc(sketch, "E978", {"start": v(-3.97, -10.11) * mm, "mid": v(-3.88, -10.3) * mm, "end": v(-3.8, -10.5) * mm});
            skArc(sketch, "E979", {"start": v(-3.8, -10.5) * mm, "mid": v(-3.69, -10.68) * mm, "end": v(-3.57, -10.87) * mm});
            skArc(sketch, "E980", {"start": v(-3.57, -10.87) * mm, "mid": v(-3.46, -11.03) * mm, "end": v(-3.35, -11.19) * mm});
            skArc(sketch, "E981", {"start": v(-3.35, -11.19) * mm, "mid": v(-3.26, -11.3) * mm, "end": v(-3.16, -11.39) * mm});
            skArc(sketch, "E982", {"start": v(-3.16, -11.39) * mm, "mid": v(-3.02, -11.53) * mm, "end": v(-2.9, -11.7) * mm});
            skArc(sketch, "E983", {"start": v(-2.9, -11.7) * mm, "mid": v(-2.87, -11.83) * mm, "end": v(-2.9, -11.97) * mm});
            skArc(sketch, "E984", {"start": v(-2.9, -11.97) * mm, "mid": v(-2.98, -12.1) * mm, "end": v(-3.11, -12.17) * mm});
            skArc(sketch, "E985", {"start": v(-3.11, -12.17) * mm, "mid": v(-3.32, -12.22) * mm, "end": v(-3.54, -12.23) * mm});
            skArc(sketch, "E986", {"start": v(-3.54, -12.23) * mm, "mid": v(-3.68, -12.26) * mm, "end": v(-3.8, -12.33) * mm});
            skArc(sketch, "E987", {"start": v(-3.8, -12.33) * mm, "mid": v(-3.9, -12.45) * mm, "end": v(-3.97, -12.6) * mm});
            skArc(sketch, "E988", {"start": v(-3.97, -12.6) * mm, "mid": v(-4.04, -12.86) * mm, "end": v(-4.07, -13.14) * mm});
            skArc(sketch, "E989", {"start": v(-4.07, -13.14) * mm, "mid": v(-4.12, -13.7) * mm, "end": v(-4.15, -14.28) * mm});
            skArc(sketch, "E990", {"start": v(-4.15, -14.28) * mm, "mid": v(-4.18, -14.79) * mm, "end": v(-4.23, -15.29) * mm});
            skArc(sketch, "E991", {"start": v(-4.23, -15.29) * mm, "mid": v(-4.27, -15.65) * mm, "end": v(-4.35, -16) * mm});
            skArc(sketch, "E992", {"start": v(-4.35, -16) * mm, "mid": v(-4.42, -16.27) * mm, "end": v(-4.52, -16.52) * mm});
            skArc(sketch, "E993", {"start": v(-4.52, -16.52) * mm, "mid": v(-4.63, -16.72) * mm, "end": v(-4.77, -16.9) * mm});
            skArc(sketch, "E994", {"start": v(-4.77, -16.9) * mm, "mid": v(-4.92, -17.08) * mm, "end": v(-5.07, -17.25) * mm});
            skArc(sketch, "E995", {"start": v(-5.07, -17.25) * mm, "mid": v(-5.12, -17.33) * mm, "end": v(-5.14, -17.42) * mm});
            skArc(sketch, "E996", {"start": v(-5.14, -17.42) * mm, "mid": v(-5.12, -17.48) * mm, "end": v(-5.07, -17.53) * mm});
            skArc(sketch, "E997", {"start": v(-5.07, -17.53) * mm, "mid": v(-4.95, -17.6) * mm, "end": v(-4.82, -17.65) * mm});
            skArc(sketch, "E998", {"start": v(-4.82, -17.65) * mm, "mid": v(-4.7, -17.7) * mm, "end": v(-4.56, -17.71) * mm});
            skArc(sketch, "E999", {"start": v(-4.56, -17.71) * mm, "mid": v(-4.33, -17.72) * mm, "end": v(-4.1, -17.73) * mm});
            skArc(sketch, "E1000", {"start": v(-4.1, -17.73) * mm, "mid": v(-3.82, -17.72) * mm, "end": v(-3.55, -17.7) * mm});
            skArc(sketch, "E1001", {"start": v(-3.55, -17.7) * mm, "mid": v(-3.27, -17.68) * mm, "end": v(-2.99, -17.65) * mm});
            skArc(sketch, "E1002", {"start": v(-2.99, -17.65) * mm, "mid": v(-2.55, -17.6) * mm, "end": v(-2.1, -17.56) * mm});
            skArc(sketch, "E1003", {"start": v(-2.1, -17.56) * mm, "mid": v(-1.9, -17.58) * mm, "end": v(-1.72, -17.65) * mm});
            skArc(sketch, "E1004", {"start": v(-1.72, -17.65) * mm, "mid": v(-1.65, -17.75) * mm, "end": v(-1.66, -17.88) * mm});
            skArc(sketch, "E1005", {"start": v(-1.66, -17.88) * mm, "mid": v(-1.8, -18.08) * mm, "end": v(-1.95, -18.26) * mm});
            skArc(sketch, "E1006", {"start": v(-1.95, -18.26) * mm, "mid": v(-2.05, -18.42) * mm, "end": v(-2.07, -18.61) * mm});
            skArc(sketch, "E1007", {"start": v(-2.07, -18.61) * mm, "mid": v(-2.01, -18.78) * mm, "end": v(-1.87, -18.9) * mm});
            skArc(sketch, "E1008", {"start": v(-1.87, -18.9) * mm, "mid": v(-1.54, -19.01) * mm, "end": v(-1.18, -19.08) * mm});
            skArc(sketch, "E1009", {"start": v(-1.18, -19.08) * mm, "mid": v(-0.54, -19.15) * mm, "end": v(0.1, -19.2) * mm});
            skArc(sketch, "E1010", {"start": v(0.1, -19.2) * mm, "mid": v(0.48, -19.23) * mm, "end": v(0.85, -19.27) * mm});
            skArc(sketch, "E1011", {"start": v(0.85, -19.27) * mm, "mid": v(1.18, -19.31) * mm, "end": v(1.52, -19.37) * mm});
            skArc(sketch, "E1012", {"start": v(1.52, -19.37) * mm, "mid": v(1.8, -19.43) * mm, "end": v(2.06, -19.5) * mm});
            skArc(sketch, "E1013", {"start": v(2.06, -19.5) * mm, "mid": v(2.18, -19.54) * mm, "end": v(2.29, -19.62) * mm});
            skArc(sketch, "E1014", {"start": v(2.29, -19.62) * mm, "mid": v(2.36, -19.82) * mm, "end": v(2.26, -20.01) * mm});
            skArc(sketch, "E1015", {"start": v(2.26, -20.01) * mm, "mid": v(1.84, -20.3) * mm, "end": v(1.4, -20.54) * mm});
            skArc(sketch, "E1016", {"start": v(1.4, -20.54) * mm, "mid": v(0.76, -20.82) * mm, "end": v(0.1, -21.05) * mm});
            skArc(sketch, "E1017", {"start": v(0.1, -21.05) * mm, "mid": v(-0.64, -21.26) * mm, "end": v(-1.4, -21.41) * mm});
            skArc(sketch, "E1018", {"start": v(-1.4, -21.41) * mm, "mid": v(-1.91, -21.5) * mm, "end": v(-2.43, -21.61) * mm});
            skArc(sketch, "E1019", {"start": v(-2.43, -21.61) * mm, "mid": v(-2.62, -21.67) * mm, "end": v(-2.8, -21.77) * mm});
            skArc(sketch, "E1020", {"start": v(-2.8, -21.77) * mm, "mid": v(-2.9, -21.87) * mm, "end": v(-2.94, -22) * mm});
            skArc(sketch, "E1021", {"start": v(-2.94, -22) * mm, "mid": v(-2.95, -22.22) * mm, "end": v(-2.93, -22.43) * mm});
            skArc(sketch, "E1022", {"start": v(-2.93, -22.43) * mm, "mid": v(-2.9, -22.59) * mm, "end": v(-2.86, -22.75) * mm});
            skArc(sketch, "E1023", {"start": v(-2.86, -22.75) * mm, "mid": v(-2.82, -22.92) * mm, "end": v(-2.77, -23.1) * mm});
            skArc(sketch, "E1024", {"start": v(-2.77, -23.1) * mm, "mid": v(-2.73, -23.26) * mm, "end": v(-2.67, -23.43) * mm});
            skArc(sketch, "E1025", {"start": v(-2.67, -23.43) * mm, "mid": v(-2.63, -23.56) * mm, "end": v(-2.58, -23.68) * mm});
            skArc(sketch, "E1026", {"start": v(-2.58, -23.68) * mm, "mid": v(-2.52, -23.83) * mm, "end": v(-2.48, -23.97) * mm});
            skArc(sketch, "E1027", {"start": v(-2.48, -23.97) * mm, "mid": v(-2.48, -24.04) * mm, "end": v(-2.53, -24.09) * mm});
            skArc(sketch, "E1028", {"start": v(-2.53, -24.09) * mm, "mid": v(-2.6, -24.11) * mm, "end": v(-2.69, -24.11) * mm});
            skArc(sketch, "E1029", {"start": v(-2.69, -24.11) * mm, "mid": v(-2.93, -24.06) * mm, "end": v(-3.16, -24) * mm});
            skArc(sketch, "E1030", {"start": v(-3.16, -24) * mm, "mid": v(-3.67, -23.86) * mm, "end": v(-4.17, -23.68) * mm});
            skArc(sketch, "E1031", {"start": v(-4.17, -23.68) * mm, "mid": v(-4.65, -23.47) * mm, "end": v(-5.12, -23.23) * mm});
            skArc(sketch, "E1032", {"start": v(-5.12, -23.23) * mm, "mid": v(-5.57, -22.96) * mm, "end": v(-6, -22.66) * mm});
            skArc(sketch, "E1033", {"start": v(-6, -22.66) * mm, "mid": v(-6.4, -22.35) * mm, "end": v(-6.77, -22) * mm});
            skArc(sketch, "E1034", {"start": v(-6.77, -22) * mm, "mid": v(-7.17, -21.6) * mm, "end": v(-7.6, -21.23) * mm});
            skArc(sketch, "E1035", {"start": v(-7.6, -21.23) * mm, "mid": v(-7.79, -21.13) * mm, "end": v(-8, -21.11) * mm});
            skArc(sketch, "E1036", {"start": v(-8, -21.11) * mm, "mid": v(-8.16, -21.2) * mm, "end": v(-8.23, -21.36) * mm});
            skArc(sketch, "E1037", {"start": v(-8.23, -21.36) * mm, "mid": v(-8.22, -21.78) * mm, "end": v(-8.18, -22.2) * mm});
            skArc(sketch, "E1038", {"start": v(-8.18, -22.2) * mm, "mid": v(-8.13, -22.54) * mm, "end": v(-8.1, -22.89) * mm});
            skArc(sketch, "E1039", {"start": v(-8.1, -22.89) * mm, "mid": v(-8.1, -23) * mm, "end": v(-8.14, -23.12) * mm});
            skArc(sketch, "E1040", {"start": v(-8.14, -23.12) * mm, "mid": v(-8.2, -23.18) * mm, "end": v(-8.28, -23.2) * mm});
            skArc(sketch, "E1041", {"start": v(-8.28, -23.2) * mm, "mid": v(-8.46, -23.17) * mm, "end": v(-8.62, -23.13) * mm});
            skArc(sketch, "E1042", {"start": v(-8.62, -23.13) * mm, "mid": v(-9.1, -22.96) * mm, "end": v(-9.58, -22.76) * mm});
            skArc(sketch, "E1043", {"start": v(-9.58, -22.76) * mm, "mid": v(-10.18, -22.46) * mm, "end": v(-10.77, -22.15) * mm});
            skArc(sketch, "E1044", {"start": v(-10.77, -22.15) * mm, "mid": v(-11.4, -21.8) * mm, "end": v(-12, -21.42) * mm});
            skArc(sketch, "E1045", {"start": v(-12, -21.42) * mm, "mid": v(-12.53, -21.06) * mm, "end": v(-13.05, -20.68) * mm});
            skArc(sketch, "E1046", {"start": v(-13.05, -20.68) * mm, "mid": v(-13.54, -20.33) * mm, "end": v(-14.04, -20) * mm});
            skArc(sketch, "E1047", {"start": v(-14.04, -20) * mm, "mid": v(-14.25, -19.95) * mm, "end": v(-14.45, -20.03) * mm});
            skArc(sketch, "E1048", {"start": v(-14.45, -20.03) * mm, "mid": v(-14.58, -20.22) * mm, "end": v(-14.58, -20.44) * mm});
            skArc(sketch, "E1049", {"start": v(-14.58, -20.44) * mm, "mid": v(-14.42, -21.05) * mm, "end": v(-14.22, -21.65) * mm});
            skArc(sketch, "E1050", {"start": v(-14.22, -21.65) * mm, "mid": v(-14.15, -21.88) * mm, "end": v(-14.07, -22.12) * mm});
            skArc(sketch, "E1051", {"start": v(-14.07, -22.12) * mm, "mid": v(-14, -22.32) * mm, "end": v(-13.95, -22.53) * mm});
            skArc(sketch, "E1052", {"start": v(-13.95, -22.53) * mm, "mid": v(-13.9, -22.7) * mm, "end": v(-13.87, -22.87) * mm});
            skArc(sketch, "E1053", {"start": v(-13.87, -22.87) * mm, "mid": v(-13.87, -22.9) * mm, "end": v(-13.89, -22.94) * mm});
            skArc(sketch, "E1054", {"start": v(-13.89, -22.94) * mm, "mid": v(-14.07, -23.03) * mm, "end": v(-14.28, -23) * mm});
            skArc(sketch, "E1055", {"start": v(-14.28, -23) * mm, "mid": v(-15.41, -22.37) * mm, "end": v(-16.54, -21.74) * mm});
            skArc(sketch, "E1056", {"start": v(-16.54, -21.74) * mm, "mid": v(-17.6, -21.12) * mm, "end": v(-18.65, -20.48) * mm});
            skArc(sketch, "E1057", {"start": v(-18.65, -20.48) * mm, "mid": v(-19.26, -20.05) * mm, "end": v(-19.83, -19.57) * mm});
            skArc(sketch, "E1058", {"start": v(-19.83, -19.57) * mm, "mid": v(-20.4, -19.05) * mm, "end": v(-20.98, -18.55) * mm});
            skArc(sketch, "E1059", {"start": v(-20.98, -18.55) * mm, "mid": v(-21.22, -18.41) * mm, "end": v(-21.49, -18.36) * mm});
            skArc(sketch, "E1060", {"start": v(-21.49, -18.36) * mm, "mid": v(-21.67, -18.43) * mm, "end": v(-21.76, -18.6) * mm});
            skArc(sketch, "E1061", {"start": v(-21.76, -18.6) * mm, "mid": v(-21.78, -19.08) * mm, "end": v(-21.76, -19.56) * mm});
            skArc(sketch, "E1062", {"start": v(-21.76, -19.56) * mm, "mid": v(-21.73, -19.93) * mm, "end": v(-21.71, -20.3) * mm});
            skArc(sketch, "E1063", {"start": v(-21.71, -20.3) * mm, "mid": v(-21.72, -20.44) * mm, "end": v(-21.76, -20.58) * mm});
            skArc(sketch, "E1064", {"start": v(-21.76, -20.58) * mm, "mid": v(-21.82, -20.65) * mm, "end": v(-21.91, -20.68) * mm});
            skArc(sketch, "E1065", {"start": v(-21.91, -20.68) * mm, "mid": v(-22.07, -20.67) * mm, "end": v(-22.22, -20.64) * mm});
            skArc(sketch, "E1066", {"start": v(-22.22, -20.64) * mm, "mid": v(-22.88, -20.42) * mm, "end": v(-23.54, -20.15) * mm});
            skArc(sketch, "E1067", {"start": v(-23.54, -20.15) * mm, "mid": v(-24.3, -19.78) * mm, "end": v(-25.06, -19.38) * mm});
            skArc(sketch, "E1068", {"start": v(-25.06, -19.38) * mm, "mid": v(-25.78, -18.95) * mm, "end": v(-26.5, -18.5) * mm});
            skArc(sketch, "E1069", {"start": v(-26.5, -18.5) * mm, "mid": v(-27.04, -18.1) * mm, "end": v(-27.56, -17.64) * mm});
            skArc(sketch, "E1070", {"start": v(-27.56, -17.64) * mm, "mid": v(-27.83, -17.4) * mm, "end": v(-28.1, -17.16) * mm});
            skArc(sketch, "E1071", {"start": v(-28.1, -17.16) * mm, "mid": v(-28.35, -16.95) * mm, "end": v(-28.6, -16.75) * mm});
            skArc(sketch, "E1072", {"start": v(-28.6, -16.75) * mm, "mid": v(-28.82, -16.6) * mm, "end": v(-29.04, -16.44) * mm});
            skArc(sketch, "E1073", {"start": v(-29.04, -16.44) * mm, "mid": v(-29.13, -16.4) * mm, "end": v(-29.23, -16.38) * mm});
            skArc(sketch, "E1074", {"start": v(-29.23, -16.38) * mm, "mid": v(-29.37, -16.43) * mm, "end": v(-29.46, -16.56) * mm});
            skArc(sketch, "E1075", {"start": v(-29.46, -16.56) * mm, "mid": v(-29.51, -16.87) * mm, "end": v(-29.53, -17.19) * mm});
            skArc(sketch, "E1076", {"start": v(-29.53, -17.19) * mm, "mid": v(-29.52, -17.58) * mm, "end": v(-29.47, -17.98) * mm});
            skArc(sketch, "E1077", {"start": v(-29.47, -17.98) * mm, "mid": v(-29.39, -18.36) * mm, "end": v(-29.27, -18.73) * mm});
            skArc(sketch, "E1078", {"start": v(-29.27, -18.73) * mm, "mid": v(-29.19, -18.96) * mm, "end": v(-29.1, -19.18) * mm});
            skArc(sketch, "E1079", {"start": v(-29.1, -19.18) * mm, "mid": v(-29.1, -19.25) * mm, "end": v(-29.13, -19.32) * mm});
            skArc(sketch, "E1080", {"start": v(-29.13, -19.32) * mm, "mid": v(-29.18, -19.36) * mm, "end": v(-29.24, -19.37) * mm});
            skArc(sketch, "E1081", {"start": v(-29.24, -19.37) * mm, "mid": v(-29.43, -19.32) * mm, "end": v(-29.61, -19.27) * mm});
            skArc(sketch, "E1082", {"start": v(-29.61, -19.27) * mm, "mid": v(-30.03, -19.12) * mm, "end": v(-30.44, -18.95) * mm});
            skArc(sketch, "E1083", {"start": v(-30.44, -18.95) * mm, "mid": v(-30.87, -18.74) * mm, "end": v(-31.28, -18.51) * mm});
            skArc(sketch, "E1084", {"start": v(-31.28, -18.51) * mm, "mid": v(-31.77, -18.2) * mm, "end": v(-32.25, -17.88) * mm});
            skArc(sketch, "E1085", {"start": v(-32.25, -17.88) * mm, "mid": v(-32.88, -17.42) * mm, "end": v(-33.5, -16.95) * mm});
            skArc(sketch, "E1086", {"start": v(-33.5, -16.95) * mm, "mid": v(-33.85, -16.7) * mm, "end": v(-34.2, -16.44) * mm});
            skArc(sketch, "E1087", {"start": v(-34.2, -16.44) * mm, "mid": v(-34.5, -16.23) * mm, "end": v(-34.81, -16.04) * mm});
            skArc(sketch, "E1088", {"start": v(-34.81, -16.04) * mm, "mid": v(-35.07, -15.88) * mm, "end": v(-35.33, -15.73) * mm});
            skArc(sketch, "E1089", {"start": v(-35.33, -15.73) * mm, "mid": v(-35.4, -15.72) * mm, "end": v(-35.46, -15.75) * mm});
            skArc(sketch, "E1090", {"start": v(-35.46, -15.75) * mm, "mid": v(-35.5, -15.81) * mm, "end": v(-35.53, -15.88) * mm});
            skArc(sketch, "E1091", {"start": v(-35.53, -15.88) * mm, "mid": v(-35.55, -16.07) * mm, "end": v(-35.58, -16.26) * mm});
            skArc(sketch, "E1092", {"start": v(-35.58, -16.26) * mm, "mid": v(-35.6, -16.5) * mm, "end": v(-35.62, -16.73) * mm});
            skArc(sketch, "E1093", {"start": v(-35.62, -16.73) * mm, "mid": v(-35.62, -17) * mm, "end": v(-35.63, -17.26) * mm});
            skArc(sketch, "E1094", {"start": v(-35.63, -17.26) * mm, "mid": v(-35.63, -17.51) * mm, "end": v(-35.63, -17.77) * mm});
            skArc(sketch, "E1095", {"start": v(-35.63, -17.77) * mm, "mid": v(-35.64, -17.99) * mm, "end": v(-35.65, -18.2) * mm});
            skArc(sketch, "E1096", {"start": v(-35.65, -18.2) * mm, "mid": v(-35.67, -18.38) * mm, "end": v(-35.68, -18.56) * mm});
            skArc(sketch, "E1097", {"start": v(-35.68, -18.56) * mm, "mid": v(-35.7, -18.58) * mm, "end": v(-35.72, -18.6) * mm});
            skArc(sketch, "E1098", {"start": v(-35.72, -18.6) * mm, "mid": v(-35.75, -18.6) * mm, "end": v(-35.79, -18.58) * mm});
            skArc(sketch, "E1099", {"start": v(-35.79, -18.58) * mm, "mid": v(-36.06, -18.5) * mm, "end": v(-36.34, -18.4) * mm});
            skArc(sketch, "E1100", {"start": v(-36.34, -18.4) * mm, "mid": v(-36.66, -18.3) * mm, "end": v(-36.98, -18.2) * mm});
            skArc(sketch, "E1101", {"start": v(-36.98, -18.2) * mm, "mid": v(-37.35, -18.07) * mm, "end": v(-37.72, -17.94) * mm});
            skArc(sketch, "E1102", {"start": v(-37.72, -17.94) * mm, "mid": v(-38.6, -17.62) * mm, "end": v(-39.48, -17.28) * mm});
            skArc(sketch, "E1103", {"start": v(-39.48, -17.28) * mm, "mid": v(-40.31, -16.91) * mm, "end": v(-41.13, -16.52) * mm});
            skArc(sketch, "E1104", {"start": v(-41.13, -16.52) * mm, "mid": v(-41.88, -16.12) * mm, "end": v(-42.62, -15.7) * mm});
            skArc(sketch, "E1105", {"start": v(-42.62, -15.7) * mm, "mid": v(-43.26, -15.28) * mm, "end": v(-43.89, -14.83) * mm});
            skArc(sketch, "E1106", {"start": v(-43.89, -14.83) * mm, "mid": v(-44.12, -14.65) * mm, "end": v(-44.37, -14.48) * mm});
            skArc(sketch, "E1107", {"start": v(-44.37, -14.48) * mm, "mid": v(-44.59, -14.35) * mm, "end": v(-44.81, -14.22) * mm});
            skArc(sketch, "E1108", {"start": v(-44.81, -14.22) * mm, "mid": v(-45, -14.13) * mm, "end": v(-45.18, -14.04) * mm});
            skArc(sketch, "E1109", {"start": v(-45.18, -14.04) * mm, "mid": v(-45.26, -14.03) * mm, "end": v(-45.34, -14.05) * mm});
            skArc(sketch, "E1110", {"start": v(-45.34, -14.05) * mm, "mid": v(-45.56, -14.31) * mm, "end": v(-45.58, -14.65) * mm});
            skArc(sketch, "E1111", {"start": v(-45.58, -14.65) * mm, "mid": v(-45.27, -15.72) * mm, "end": v(-44.92, -16.78) * mm});
            skArc(sketch, "E1112", {"start": v(-44.92, -16.78) * mm, "mid": v(-44.5, -17.94) * mm, "end": v(-44, -19.07) * mm});
            skArc(sketch, "E1113", {"start": v(-44, -19.07) * mm, "mid": v(-43.52, -20.05) * mm, "end": v(-42.95, -20.99) * mm});
            skArc(sketch, "E1114", {"start": v(-42.95, -20.99) * mm, "mid": v(-42.51, -21.7) * mm, "end": v(-42.1, -22.44) * mm});
            skArc(sketch, "E1115", {"start": v(-42.1, -22.44) * mm, "mid": v(-42.02, -22.73) * mm, "end": v(-42.08, -23.02) * mm});
            skArc(sketch, "E1116", {"start": v(-42.08, -23.02) * mm, "mid": v(-42.28, -23.22) * mm, "end": v(-42.55, -23.29) * mm});
            skArc(sketch, "E1117", {"start": v(-42.55, -23.29) * mm, "mid": v(-43.32, -23.24) * mm, "end": v(-44.09, -23.16) * mm});
            skArc(sketch, "E1118", {"start": v(-44.09, -23.16) * mm, "mid": v(-44.43, -23.13) * mm, "end": v(-44.77, -23.1) * mm});
            skArc(sketch, "E1119", {"start": v(-44.77, -23.1) * mm, "mid": v(-45, -23.09) * mm, "end": v(-45.22, -23.1) * mm});
            skArc(sketch, "E1120", {"start": v(-45.22, -23.1) * mm, "mid": v(-45.36, -23.12) * mm, "end": v(-45.5, -23.16) * mm});
            skArc(sketch, "E1121", {"start": v(-45.5, -23.16) * mm, "mid": v(-45.56, -23.2) * mm, "end": v(-45.58, -23.29) * mm});
            skArc(sketch, "E1122", {"start": v(-45.58, -23.29) * mm, "mid": v(-45.54, -23.6) * mm, "end": v(-45.4, -23.9) * mm});
            skArc(sketch, "E1123", {"start": v(-45.4, -23.9) * mm, "mid": v(-44.96, -24.57) * mm, "end": v(-44.5, -25.24) * mm});
            skArc(sketch, "E1124", {"start": v(-44.5, -25.24) * mm, "mid": v(-43.98, -25.94) * mm, "end": v(-43.43, -26.63) * mm});
            skArc(sketch, "E1125", {"start": v(-43.43, -26.63) * mm, "mid": v(-42.95, -27.18) * mm, "end": v(-42.43, -27.7) * mm});
            skArc(sketch, "E1126", {"start": v(-42.43, -27.7) * mm, "mid": v(-42.19, -27.95) * mm, "end": v(-41.95, -28.2) * mm});
            skArc(sketch, "E1127", {"start": v(-41.95, -28.2) * mm, "mid": v(-41.74, -28.42) * mm, "end": v(-41.53, -28.64) * mm});
            skArc(sketch, "E1128", {"start": v(-41.53, -28.64) * mm, "mid": v(-41.37, -28.83) * mm, "end": v(-41.2, -29.03) * mm});
            skArc(sketch, "E1129", {"start": v(-41.2, -29.03) * mm, "mid": v(-41.17, -29.09) * mm, "end": v(-41.16, -29.16) * mm});
            skArc(sketch, "E1130", {"start": v(-41.16, -29.16) * mm, "mid": v(-41.18, -29.22) * mm, "end": v(-41.24, -29.25) * mm});
            skArc(sketch, "E1131", {"start": v(-41.24, -29.25) * mm, "mid": v(-41.61, -29.28) * mm, "end": v(-41.99, -29.31) * mm});
            skArc(sketch, "E1132", {"start": v(-41.99, -29.31) * mm, "mid": v(-42.45, -29.34) * mm, "end": v(-42.9, -29.36) * mm});
            skArc(sketch, "E1133", {"start": v(-42.9, -29.36) * mm, "mid": v(-43.45, -29.37) * mm, "end": v(-44, -29.37) * mm});
            skArc(sketch, "E1134", {"start": v(-44, -29.37) * mm, "mid": v(-44.78, -29.36) * mm, "end": v(-45.56, -29.34) * mm});
            skArc(sketch, "E1135", {"start": v(-45.56, -29.34) * mm, "mid": v(-46.08, -29.3) * mm, "end": v(-46.6, -29.24) * mm});
            skArc(sketch, "E1136", {"start": v(-46.6, -29.24) * mm, "mid": v(-47.05, -29.15) * mm, "end": v(-47.5, -29.04) * mm});
            skArc(sketch, "E1137", {"start": v(-47.5, -29.04) * mm, "mid": v(-48, -28.87) * mm, "end": v(-48.48, -28.68) * mm});
            skArc(sketch, "E1138", {"start": v(-48.48, -28.68) * mm, "mid": v(-48.8, -28.55) * mm, "end": v(-49.14, -28.42) * mm});
            skArc(sketch, "E1139", {"start": v(-49.14, -28.42) * mm, "mid": v(-49.43, -28.3) * mm, "end": v(-49.72, -28.2) * mm});
            skArc(sketch, "E1140", {"start": v(-49.72, -28.2) * mm, "mid": v(-49.96, -28.1) * mm, "end": v(-50.21, -28.02) * mm});
            skArc(sketch, "E1141", {"start": v(-50.21, -28.02) * mm, "mid": v(-50.28, -28) * mm, "end": v(-50.35, -28) * mm});
            skArc(sketch, "E1142", {"start": v(-50.35, -28) * mm, "mid": v(-50.4, -28.02) * mm, "end": v(-50.43, -28.07) * mm});
            skArc(sketch, "E1143", {"start": v(-50.43, -28.07) * mm, "mid": v(-50.47, -28.34) * mm, "end": v(-50.5, -28.6) * mm});
            skArc(sketch, "E1144", {"start": v(-50.5, -28.6) * mm, "mid": v(-50.53, -28.95) * mm, "end": v(-50.54, -29.28) * mm});
            skArc(sketch, "E1145", {"start": v(-50.54, -29.28) * mm, "mid": v(-50.55, -29.69) * mm, "end": v(-50.56, -30.09) * mm});
            skArc(sketch, "E1146", {"start": v(-50.56, -30.09) * mm, "mid": v(-50.55, -30.68) * mm, "end": v(-50.53, -31.26) * mm});
            skArc(sketch, "E1147", {"start": v(-50.53, -31.26) * mm, "mid": v(-50.5, -31.62) * mm, "end": v(-50.44, -31.97) * mm});
            skArc(sketch, "E1148", {"start": v(-50.44, -31.97) * mm, "mid": v(-50.35, -32.25) * mm, "end": v(-50.23, -32.51) * mm});
            skArc(sketch, "E1149", {"start": v(-50.23, -32.51) * mm, "mid": v(-50.06, -32.8) * mm, "end": v(-49.87, -33.08) * mm});
            skArc(sketch, "E1150", {"start": v(-49.87, -33.08) * mm, "mid": v(-49.73, -33.28) * mm, "end": v(-49.6, -33.49) * mm});
            skArc(sketch, "E1151", {"start": v(-49.6, -33.49) * mm, "mid": v(-49.46, -33.72) * mm, "end": v(-49.33, -33.97) * mm});
            skArc(sketch, "E1152", {"start": v(-49.33, -33.97) * mm, "mid": v(-49.23, -34.2) * mm, "end": v(-49.13, -34.44) * mm});
            skArc(sketch, "E1153", {"start": v(-49.13, -34.44) * mm, "mid": v(-49.06, -34.63) * mm, "end": v(-49.01, -34.82) * mm});
            skLineSegment(sketch, "E1154", {"start": v(-49.01, -34.82) * mm, "end": v(-48.85, -35.65) * mm});
            skLineSegment(sketch, "E1155", {"start": v(-48.85, -35.65) * mm, "end": v(-45.62, -35.64) * mm});
            skArc(sketch, "E1156", {"start": v(-45.62, -35.64) * mm, "mid": v(-44.75, -35.64) * mm, "end": v(-43.87, -35.66) * mm});
            skArc(sketch, "E1157", {"start": v(-43.87, -35.66) * mm, "mid": v(-43.28, -35.69) * mm, "end": v(-42.7, -35.74) * mm});
            skArc(sketch, "E1158", {"start": v(-42.7, -35.74) * mm, "mid": v(-42.22, -35.82) * mm, "end": v(-41.75, -35.92) * mm});
            skArc(sketch, "E1159", {"start": v(-41.75, -35.92) * mm, "mid": v(-41.25, -36.07) * mm, "end": v(-40.75, -36.23) * mm});
            skArc(sketch, "E1160", {"start": v(-40.75, -36.23) * mm, "mid": v(-40.16, -36.45) * mm, "end": v(-39.57, -36.65) * mm});
            skArc(sketch, "E1161", {"start": v(-39.57, -36.65) * mm, "mid": v(-39.24, -36.74) * mm, "end": v(-38.9, -36.8) * mm});
            skArc(sketch, "E1162", {"start": v(-38.9, -36.8) * mm, "mid": v(-38.71, -36.81) * mm, "end": v(-38.53, -36.77) * mm});
            skArc(sketch, "E1163", {"start": v(-38.53, -36.77) * mm, "mid": v(-38.43, -36.7) * mm, "end": v(-38.4, -36.58) * mm});
            skArc(sketch, "E1164", {"start": v(-38.4, -36.58) * mm, "mid": v(-38.38, -36.49) * mm, "end": v(-38.36, -36.4) * mm});
            skArc(sketch, "E1165", {"start": v(-38.36, -36.4) * mm, "mid": v(-38.23, -36.08) * mm, "end": v(-38.1, -35.77) * mm});
            skArc(sketch, "E1166", {"start": v(-38.1, -35.77) * mm, "mid": v(-37.94, -35.4) * mm, "end": v(-37.77, -35.02) * mm});
            skArc(sketch, "E1167", {"start": v(-37.77, -35.02) * mm, "mid": v(-37.58, -34.6) * mm, "end": v(-37.39, -34.2) * mm});
            skArc(sketch, "E1168", {"start": v(-37.39, -34.2) * mm, "mid": v(-36.98, -33.39) * mm, "end": v(-36.55, -32.6) * mm});
            skArc(sketch, "E1169", {"start": v(-36.55, -32.6) * mm, "mid": v(-36.14, -31.95) * mm, "end": v(-35.7, -31.34) * mm});
            skArc(sketch, "E1170", {"start": v(-35.7, -31.34) * mm, "mid": v(-35.27, -30.85) * mm, "end": v(-34.81, -30.4) * mm});
            skArc(sketch, "E1171", {"start": v(-34.81, -30.4) * mm, "mid": v(-34.38, -30.05) * mm, "end": v(-33.91, -29.76) * mm});
            skArc(sketch, "E1172", {"start": v(-33.91, -29.76) * mm, "mid": v(-33.6, -29.56) * mm, "end": v(-33.34, -29.3) * mm});
            skArc(sketch, "E1173", {"start": v(-33.34, -29.3) * mm, "mid": v(-33.2, -29.04) * mm, "end": v(-33.16, -28.75) * mm});
            skArc(sketch, "E1174", {"start": v(-33.16, -28.75) * mm, "mid": v(-33.23, -28.49) * mm, "end": v(-33.4, -28.28) * mm});
            skArc(sketch, "E1175", {"start": v(-33.4, -28.28) * mm, "mid": v(-33.7, -28.13) * mm, "end": v(-34, -28.05) * mm});
            skArc(sketch, "E1176", {"start": v(-34, -28.05) * mm, "mid": v(-34.19, -28.02) * mm, "end": v(-34.37, -27.96) * mm});
            skArc(sketch, "E1177", {"start": v(-34.37, -27.96) * mm, "mid": v(-34.5, -27.9) * mm, "end": v(-34.61, -27.8) * mm});
            skArc(sketch, "E1178", {"start": v(-34.61, -27.8) * mm, "mid": v(-34.71, -27.69) * mm, "end": v(-34.78, -27.55) * mm});
            skArc(sketch, "E1179", {"start": v(-34.78, -27.55) * mm, "mid": v(-34.85, -27.35) * mm, "end": v(-34.9, -27.15) * mm});
            skArc(sketch, "E1180", {"start": v(-34.9, -27.15) * mm, "mid": v(-34.94, -27) * mm, "end": v(-34.99, -26.84) * mm});
            skArc(sketch, "E1181", {"start": v(-34.99, -26.84) * mm, "mid": v(-35.04, -26.7) * mm, "end": v(-35.12, -26.57) * mm});
            skArc(sketch, "E1182", {"start": v(-35.12, -26.57) * mm, "mid": v(-35.19, -26.48) * mm, "end": v(-35.27, -26.4) * mm});
            skArc(sketch, "E1183", {"start": v(-35.27, -26.4) * mm, "mid": v(-35.33, -26.35) * mm, "end": v(-35.41, -26.34) * mm});
            skArc(sketch, "E1184", {"start": v(-35.41, -26.34) * mm, "mid": v(-35.64, -26.24) * mm, "end": v(-35.74, -26.02) * mm});
            skArc(sketch, "E1185", {"start": v(-35.74, -26.02) * mm, "mid": v(-35.77, -25.03) * mm, "end": v(-35.78, -24.03) * mm});
            skArc(sketch, "E1186", {"start": v(-35.78, -24.03) * mm, "mid": v(-35.76, -23.04) * mm, "end": v(-35.7, -22.05) * mm});
            skArc(sketch, "E1187", {"start": v(-35.7, -22.05) * mm, "mid": v(-35.6, -21.63) * mm, "end": v(-35.38, -21.26) * mm});
            skArc(sketch, "E1188", {"start": v(-35.38, -21.26) * mm, "mid": v(-35.28, -21.16) * mm, "end": v(-35.17, -21.07) * mm});
            skArc(sketch, "E1189", {"start": v(-35.17, -21.07) * mm, "mid": v(-34.99, -20.96) * mm, "end": v(-34.8, -20.86) * mm});
            skArc(sketch, "E1190", {"start": v(-34.8, -20.86) * mm, "mid": v(-34.6, -20.76) * mm, "end": v(-34.37, -20.66) * mm});
            skArc(sketch, "E1191", {"start": v(-34.37, -20.66) * mm, "mid": v(-34.15, -20.59) * mm, "end": v(-33.93, -20.52) * mm});
            skArc(sketch, "E1192", {"start": v(-33.93, -20.52) * mm, "mid": v(-33.63, -20.45) * mm, "end": v(-33.32, -20.4) * mm});
            skArc(sketch, "E1193", {"start": v(-33.32, -20.4) * mm, "mid": v(-33.08, -20.37) * mm, "end": v(-32.83, -20.39) * mm});
            skArc(sketch, "E1194", {"start": v(-32.83, -20.39) * mm, "mid": v(-32.58, -20.43) * mm, "end": v(-32.33, -20.5) * mm});
            skArc(sketch, "E1195", {"start": v(-32.33, -20.5) * mm, "mid": v(-31.99, -20.62) * mm, "end": v(-31.65, -20.76) * mm});
            skArc(sketch, "E1196", {"start": v(-31.65, -20.76) * mm, "mid": v(-30.99, -21.12) * mm, "end": v(-30.39, -21.58) * mm});
            skArc(sketch, "E1197", {"start": v(-30.39, -21.58) * mm, "mid": v(-29.82, -22.15) * mm, "end": v(-29.34, -22.79) * mm});
            skArc(sketch, "E1198", {"start": v(-29.34, -22.79) * mm, "mid": v(-28.86, -23.6) * mm, "end": v(-28.47, -24.46) * mm});
            skArc(sketch, "E1199", {"start": v(-28.47, -24.46) * mm, "mid": v(-28.08, -25.57) * mm, "end": v(-27.74, -26.7) * mm});
            skArc(sketch, "E1200", {"start": v(-27.74, -26.7) * mm, "mid": v(-27.64, -27.05) * mm, "end": v(-27.53, -27.4) * mm});
            skArc(sketch, "E1201", {"start": v(-27.53, -27.4) * mm, "mid": v(-27.42, -27.7) * mm, "end": v(-27.3, -27.99) * mm});
            skArc(sketch, "E1202", {"start": v(-27.3, -27.99) * mm, "mid": v(-27.2, -28.2) * mm, "end": v(-27.1, -28.41) * mm});
            skArc(sketch, "E1203", {"start": v(-27.1, -28.41) * mm, "mid": v(-27.03, -28.46) * mm, "end": v(-26.95, -28.47) * mm});
            skArc(sketch, "E1204", {"start": v(-26.95, -28.47) * mm, "mid": v(-26.87, -28.42) * mm, "end": v(-26.82, -28.36) * mm});
            skArc(sketch, "E1205", {"start": v(-26.82, -28.36) * mm, "mid": v(-26.74, -28.2) * mm, "end": v(-26.68, -28.05) * mm});
            skArc(sketch, "E1206", {"start": v(-26.68, -28.05) * mm, "mid": v(-26.6, -27.84) * mm, "end": v(-26.55, -27.64) * mm});
            skArc(sketch, "E1207", {"start": v(-26.55, -27.64) * mm, "mid": v(-26.5, -27.4) * mm, "end": v(-26.45, -27.18) * mm});
            skArc(sketch, "E1208", {"start": v(-26.45, -27.18) * mm, "mid": v(-25.98, -25.6) * mm, "end": v(-25.16, -24.19) * mm});
            skArc(sketch, "E1209", {"start": v(-25.16, -24.19) * mm, "mid": v(-24.13, -23.27) * mm, "end": v(-22.83, -22.8) * mm});
            skArc(sketch, "E1210", {"start": v(-22.83, -22.8) * mm, "mid": v(-21.4, -22.85) * mm, "end": v(-20.06, -23.4) * mm});
            skArc(sketch, "E1211", {"start": v(-20.06, -23.4) * mm, "mid": v(-18.7, -24.5) * mm, "end": v(-17.58, -25.84) * mm});
            skArc(sketch, "E1212", {"start": v(-17.58, -25.84) * mm, "mid": v(-17, -26.82) * mm, "end": v(-16.51, -27.86) * mm});
            skArc(sketch, "E1213", {"start": v(-16.51, -27.86) * mm, "mid": v(-16.08, -29.03) * mm, "end": v(-15.74, -30.24) * mm});
            skArc(sketch, "E1214", {"start": v(-15.74, -30.24) * mm, "mid": v(-15.43, -31.7) * mm, "end": v(-15.21, -33.16) * mm});
            skArc(sketch, "E1215", {"start": v(-15.21, -33.16) * mm, "mid": v(-15.02, -35) * mm, "end": v(-14.9, -36.84) * mm});
            skArc(sketch, "E1216", {"start": v(-14.9, -36.84) * mm, "mid": v(-14.78, -38.54) * mm, "end": v(-14.64, -40.24) * mm});
            skArc(sketch, "E1217", {"start": v(-14.64, -40.24) * mm, "mid": v(-14.49, -41.42) * mm, "end": v(-14.27, -42.59) * mm});
            skArc(sketch, "E1218", {"start": v(-14.27, -42.59) * mm, "mid": v(-13.97, -43.75) * mm, "end": v(-13.61, -44.9) * mm});
            skArc(sketch, "E1219", {"start": v(-13.61, -44.9) * mm, "mid": v(-13.02, -46.53) * mm, "end": v(-12.4, -48.16) * mm});
            skArc(sketch, "E1220", {"start": v(-12.4, -48.16) * mm, "mid": v(-12.14, -48.83) * mm, "end": v(-11.88, -49.5) * mm});
            skArc(sketch, "E1221", {"start": v(-11.88, -49.5) * mm, "mid": v(-11.67, -50.06) * mm, "end": v(-11.47, -50.63) * mm});
            skArc(sketch, "E1222", {"start": v(-11.47, -50.63) * mm, "mid": v(-11.3, -51.12) * mm, "end": v(-11.12, -51.62) * mm});
            skArc(sketch, "E1223", {"start": v(-11.12, -51.62) * mm, "mid": v(-11.12, -51.67) * mm, "end": v(-11.14, -51.71) * mm});
            skArc(sketch, "E1224", {"start": v(-11.14, -51.71) * mm, "mid": v(-11.3, -51.78) * mm, "end": v(-11.46, -51.71) * mm});
            skArc(sketch, "E1225", {"start": v(-11.46, -51.71) * mm, "mid": v(-11.96, -51.21) * mm, "end": v(-12.45, -50.7) * mm});
            skArc(sketch, "E1226", {"start": v(-12.45, -50.7) * mm, "mid": v(-12.94, -50.16) * mm, "end": v(-13.4, -49.6) * mm});
            skArc(sketch, "E1227", {"start": v(-13.4, -49.6) * mm, "mid": v(-13.68, -49.19) * mm, "end": v(-13.92, -48.74) * mm});
            skArc(sketch, "E1228", {"start": v(-13.92, -48.74) * mm, "mid": v(-14.1, -48.4) * mm, "end": v(-14.3, -48.07) * mm});
            skArc(sketch, "E1229", {"start": v(-14.3, -48.07) * mm, "mid": v(-14.5, -47.85) * mm, "end": v(-14.72, -47.68) * mm});
            skArc(sketch, "E1230", {"start": v(-14.72, -47.68) * mm, "mid": v(-14.87, -47.64) * mm, "end": v(-15.02, -47.7) * mm});
            skArc(sketch, "E1231", {"start": v(-15.02, -47.7) * mm, "mid": v(-15.13, -47.84) * mm, "end": v(-15.17, -48) * mm});
            skArc(sketch, "E1232", {"start": v(-15.17, -48) * mm, "mid": v(-15.17, -48.1) * mm, "end": v(-15.2, -48.18) * mm});
            skArc(sketch, "E1233", {"start": v(-15.2, -48.18) * mm, "mid": v(-15.24, -48.28) * mm, "end": v(-15.29, -48.37) * mm});
            skArc(sketch, "E1234", {"start": v(-15.29, -48.37) * mm, "mid": v(-15.35, -48.47) * mm, "end": v(-15.42, -48.57) * mm});
            skArc(sketch, "E1235", {"start": v(-15.42, -48.57) * mm, "mid": v(-15.49, -48.65) * mm, "end": v(-15.57, -48.72) * mm});
            skArc(sketch, "E1236", {"start": v(-15.57, -48.72) * mm, "mid": v(-15.69, -48.8) * mm, "end": v(-15.82, -48.82) * mm});
            skArc(sketch, "E1237", {"start": v(-15.82, -48.82) * mm, "mid": v(-15.95, -48.8) * mm, "end": v(-16.06, -48.74) * mm});
            skArc(sketch, "E1238", {"start": v(-16.06, -48.74) * mm, "mid": v(-16.22, -48.6) * mm, "end": v(-16.35, -48.43) * mm});
            skArc(sketch, "E1239", {"start": v(-16.35, -48.43) * mm, "mid": v(-16.6, -48.08) * mm, "end": v(-16.83, -47.72) * mm});
            skArc(sketch, "E1240", {"start": v(-16.83, -47.72) * mm, "mid": v(-17, -47.43) * mm, "end": v(-17.17, -47.12) * mm});
            skArc(sketch, "E1241", {"start": v(-17.17, -47.12) * mm, "mid": v(-17.35, -46.78) * mm, "end": v(-17.52, -46.43) * mm});
            skArc(sketch, "E1242", {"start": v(-17.52, -46.43) * mm, "mid": v(-17.66, -46.1) * mm, "end": v(-17.8, -45.75) * mm});
            skArc(sketch, "E1243", {"start": v(-17.8, -45.75) * mm, "mid": v(-17.9, -45.48) * mm, "end": v(-17.98, -45.2) * mm});
            skArc(sketch, "E1244", {"start": v(-17.98, -45.2) * mm, "mid": v(-18.1, -44.8) * mm, "end": v(-18.25, -44.39) * mm});
            skArc(sketch, "E1245", {"start": v(-18.25, -44.39) * mm, "mid": v(-18.38, -44.2) * mm, "end": v(-18.57, -44.08) * mm});
            skArc(sketch, "E1246", {"start": v(-18.57, -44.08) * mm, "mid": v(-18.75, -44.08) * mm, "end": v(-18.9, -44.19) * mm});
            skArc(sketch, "E1247", {"start": v(-18.9, -44.19) * mm, "mid": v(-19.06, -44.47) * mm, "end": v(-19.2, -44.77) * mm});
            skArc(sketch, "E1248", {"start": v(-19.2, -44.77) * mm, "mid": v(-19.28, -44.98) * mm, "end": v(-19.37, -45.2) * mm});
            skArc(sketch, "E1249", {"start": v(-19.37, -45.2) * mm, "mid": v(-19.44, -45.24) * mm, "end": v(-19.52, -45.23) * mm});
            skArc(sketch, "E1250", {"start": v(-19.52, -45.23) * mm, "mid": v(-19.63, -45.14) * mm, "end": v(-19.7, -45.02) * mm});
            skArc(sketch, "E1251", {"start": v(-19.7, -45.02) * mm, "mid": v(-19.98, -44.53) * mm, "end": v(-20.26, -44.03) * mm});
            skArc(sketch, "E1252", {"start": v(-20.26, -44.03) * mm, "mid": v(-20.43, -43.7) * mm, "end": v(-20.59, -43.38) * mm});
            skArc(sketch, "E1253", {"start": v(-20.59, -43.38) * mm, "mid": v(-20.76, -43.02) * mm, "end": v(-20.92, -42.66) * mm});
            skArc(sketch, "E1254", {"start": v(-20.92, -42.66) * mm, "mid": v(-21.07, -42.32) * mm, "end": v(-21.2, -41.97) * mm});
            skArc(sketch, "E1255", {"start": v(-21.2, -41.97) * mm, "mid": v(-21.3, -41.7) * mm, "end": v(-21.39, -41.44) * mm});
            skArc(sketch, "E1256", {"start": v(-21.39, -41.44) * mm, "mid": v(-21.52, -41.04) * mm, "end": v(-21.68, -40.64) * mm});
            skArc(sketch, "E1257", {"start": v(-21.68, -40.64) * mm, "mid": v(-21.8, -40.44) * mm, "end": v(-21.98, -40.28) * mm});
            skArc(sketch, "E1258", {"start": v(-21.98, -40.28) * mm, "mid": v(-22.13, -40.25) * mm, "end": v(-22.26, -40.31) * mm});
            skArc(sketch, "E1259", {"start": v(-22.26, -40.31) * mm, "mid": v(-22.4, -40.5) * mm, "end": v(-22.5, -40.71) * mm});
            skArc(sketch, "E1260", {"start": v(-22.5, -40.71) * mm, "mid": v(-22.59, -40.92) * mm, "end": v(-22.73, -41.1) * mm});
            skArc(sketch, "E1261", {"start": v(-22.73, -41.1) * mm, "mid": v(-22.87, -41.17) * mm, "end": v(-23.03, -41.15) * mm});
            skArc(sketch, "E1262", {"start": v(-23.03, -41.15) * mm, "mid": v(-23.25, -41.02) * mm, "end": v(-23.44, -40.84) * mm});
            skArc(sketch, "E1263", {"start": v(-23.44, -40.84) * mm, "mid": v(-23.72, -40.47) * mm, "end": v(-23.99, -40.08) * mm});
            skArc(sketch, "E1264", {"start": v(-23.99, -40.08) * mm, "mid": v(-24.21, -39.76) * mm, "end": v(-24.46, -39.45) * mm});
            skArc(sketch, "E1265", {"start": v(-24.46, -39.45) * mm, "mid": v(-24.61, -39.32) * mm, "end": v(-24.8, -39.25) * mm});
            skArc(sketch, "E1266", {"start": v(-24.8, -39.25) * mm, "mid": v(-24.95, -39.28) * mm, "end": v(-25.04, -39.39) * mm});
            skArc(sketch, "E1267", {"start": v(-25.04, -39.39) * mm, "mid": v(-25.1, -39.63) * mm, "end": v(-25.12, -39.88) * mm});
            skArc(sketch, "E1268", {"start": v(-25.12, -39.88) * mm, "mid": v(-25.15, -40.14) * mm, "end": v(-25.23, -40.39) * mm});
            skArc(sketch, "E1269", {"start": v(-25.23, -40.39) * mm, "mid": v(-25.34, -40.5) * mm, "end": v(-25.5, -40.51) * mm});
            skArc(sketch, "E1270", {"start": v(-25.5, -40.51) * mm, "mid": v(-25.75, -40.4) * mm, "end": v(-25.96, -40.23) * mm});
            skArc(sketch, "E1271", {"start": v(-25.96, -40.23) * mm, "mid": v(-26.3, -39.84) * mm, "end": v(-26.62, -39.44) * mm});
            skArc(sketch, "E1272", {"start": v(-26.62, -39.44) * mm, "mid": v(-26.81, -39.18) * mm, "end": v(-27, -38.92) * mm});
            skArc(sketch, "E1273", {"start": v(-27, -38.92) * mm, "mid": v(-27.16, -38.7) * mm, "end": v(-27.32, -38.46) * mm});
            skArc(sketch, "E1274", {"start": v(-27.32, -38.46) * mm, "mid": v(-27.45, -38.26) * mm, "end": v(-27.57, -38.06) * mm});
            skArc(sketch, "E1275", {"start": v(-27.57, -38.06) * mm, "mid": v(-27.6, -37.99) * mm, "end": v(-27.6, -37.9) * mm});
            skArc(sketch, "E1276", {"start": v(-27.6, -37.9) * mm, "mid": v(-27.62, -37.86) * mm, "end": v(-27.64, -37.82) * mm});
            skArc(sketch, "E1277", {"start": v(-27.64, -37.82) * mm, "mid": v(-27.68, -37.78) * mm, "end": v(-27.73, -37.74) * mm});
            skArc(sketch, "E1278", {"start": v(-27.73, -37.74) * mm, "mid": v(-27.8, -37.71) * mm, "end": v(-27.87, -37.69) * mm});
            skArc(sketch, "E1279", {"start": v(-27.87, -37.69) * mm, "mid": v(-27.95, -37.68) * mm, "end": v(-28.03, -37.67) * mm});
            skArc(sketch, "E1280", {"start": v(-28.03, -37.67) * mm, "mid": v(-28.16, -37.7) * mm, "end": v(-28.25, -37.8) * mm});
            skArc(sketch, "E1281", {"start": v(-28.25, -37.8) * mm, "mid": v(-28.31, -37.92) * mm, "end": v(-28.33, -38.07) * mm});
            skArc(sketch, "E1282", {"start": v(-28.33, -38.07) * mm, "mid": v(-28.28, -38.4) * mm, "end": v(-28.21, -38.72) * mm});
            skArc(sketch, "E1283", {"start": v(-28.21, -38.72) * mm, "mid": v(-27.96, -39.76) * mm, "end": v(-27.7, -40.8) * mm});
            skArc(sketch, "E1284", {"start": v(-27.7, -40.8) * mm, "mid": v(-27, -43.01) * mm, "end": v(-26.03, -45.11) * mm});
            skArc(sketch, "E1285", {"start": v(-26.03, -45.11) * mm, "mid": v(-24.72, -47.26) * mm, "end": v(-23.2, -49.27) * mm});
            skArc(sketch, "E1286", {"start": v(-23.2, -49.27) * mm, "mid": v(-21.44, -51.17) * mm, "end": v(-19.5, -52.88) * mm});
            skArc(sketch, "E1287", {"start": v(-19.5, -52.88) * mm, "mid": v(-17.48, -54.34) * mm, "end": v(-15.3, -55.58) * mm});
            skArc(sketch, "E1288", {"start": v(-15.3, -55.58) * mm, "mid": v(-14.95, -55.75) * mm, "end": v(-14.6, -55.9) * mm});
            skArc(sketch, "E1289", {"start": v(-14.6, -55.9) * mm, "mid": v(-14.23, -56.07) * mm, "end": v(-13.85, -56.22) * mm});
            skArc(sketch, "E1290", {"start": v(-13.85, -56.22) * mm, "mid": v(-13.5, -56.35) * mm, "end": v(-13.16, -56.47) * mm});
            skArc(sketch, "E1291", {"start": v(-13.16, -56.47) * mm, "mid": v(-12.92, -56.54) * mm, "end": v(-12.68, -56.6) * mm});
            skArc(sketch, "E1292", {"start": v(-12.68, -56.6) * mm, "mid": v(-12.12, -56.72) * mm, "end": v(-11.56, -56.84) * mm});
            skArc(sketch, "E1293", {"start": v(-11.56, -56.84) * mm, "mid": v(-11.3, -56.92) * mm, "end": v(-11.07, -57.03) * mm});
            skArc(sketch, "E1294", {"start": v(-11.07, -57.03) * mm, "mid": v(-10.93, -57.13) * mm, "end": v(-10.83, -57.26) * mm});
            skArc(sketch, "E1295", {"start": v(-10.83, -57.26) * mm, "mid": v(-10.76, -57.43) * mm, "end": v(-10.74, -57.61) * mm});
            skArc(sketch, "E1296", {"start": v(-10.74, -57.61) * mm, "mid": v(-10.75, -57.74) * mm, "end": v(-10.8, -57.87) * mm});
            skArc(sketch, "E1297", {"start": v(-10.8, -57.87) * mm, "mid": v(-10.86, -58.04) * mm, "end": v(-10.95, -58.2) * mm});
            skArc(sketch, "E1298", {"start": v(-10.95, -58.2) * mm, "mid": v(-11.05, -58.38) * mm, "end": v(-11.17, -58.54) * mm});
            skArc(sketch, "E1299", {"start": v(-11.17, -58.54) * mm, "mid": v(-11.3, -58.7) * mm, "end": v(-11.43, -58.85) * mm});
            skArc(sketch, "E1300", {"start": v(-11.43, -58.85) * mm, "mid": v(-11.57, -58.99) * mm, "end": v(-11.7, -59.12) * mm});
            skArc(sketch, "E1301", {"start": v(-11.7, -59.12) * mm, "mid": v(-11.81, -59.25) * mm, "end": v(-11.92, -59.38) * mm});
            skArc(sketch, "E1302", {"start": v(-11.92, -59.38) * mm, "mid": v(-12.01, -59.49) * mm, "end": v(-12.1, -59.6) * mm});
            skArc(sketch, "E1303", {"start": v(-12.1, -59.6) * mm, "mid": v(-12.12, -59.64) * mm, "end": v(-12.12, -59.68) * mm});
            skArc(sketch, "E1304", {"start": v(-12.12, -59.68) * mm, "mid": v(-12.04, -60.02) * mm, "end": v(-11.8, -60.28) * mm});
            skArc(sketch, "E1305", {"start": v(-11.8, -60.28) * mm, "mid": v(-10.97, -60.78) * mm, "end": v(-10.13, -61.24) * mm});
            skArc(sketch, "E1306", {"start": v(-10.13, -61.24) * mm, "mid": v(-9.25, -61.67) * mm, "end": v(-8.35, -62.05) * mm});
            skArc(sketch, "E1307", {"start": v(-8.35, -62.05) * mm, "mid": v(-7.75, -62.22) * mm, "end": v(-7.14, -62.28) * mm});
            skArc(sketch, "E1308", {"start": v(-7.14, -62.28) * mm, "mid": v(-7.03, -62.28) * mm, "end": v(-6.93, -62.3) * mm});
            skArc(sketch, "E1309", {"start": v(-6.93, -62.3) * mm, "mid": v(-6.84, -62.3) * mm, "end": v(-6.75, -62.32) * mm});
            skArc(sketch, "E1310", {"start": v(-6.75, -62.32) * mm, "mid": v(-6.7, -62.35) * mm, "end": v(-6.63, -62.37) * mm});
            skArc(sketch, "E1311", {"start": v(-6.63, -62.37) * mm, "mid": v(-6.6, -62.4) * mm, "end": v(-6.6, -62.43) * mm});
            skArc(sketch, "E1312", {"start": v(-6.6, -62.43) * mm, "mid": v(-6.62, -62.65) * mm, "end": v(-6.7, -62.85) * mm});
            skArc(sketch, "E1313", {"start": v(-6.7, -62.85) * mm, "mid": v(-6.95, -63.31) * mm, "end": v(-7.22, -63.77) * mm});
            skArc(sketch, "E1314", {"start": v(-7.22, -63.77) * mm, "mid": v(-7.5, -64.22) * mm, "end": v(-7.79, -64.66) * mm});
            skArc(sketch, "E1315", {"start": v(-7.79, -64.66) * mm, "mid": v(-8, -64.92) * mm, "end": v(-8.22, -65.16) * mm});
            skArc(sketch, "E1316", {"start": v(-8.22, -65.16) * mm, "mid": v(-8.47, -65.4) * mm, "end": v(-8.7, -65.65) * mm});
            skArc(sketch, "E1317", {"start": v(-8.7, -65.65) * mm, "mid": v(-8.76, -65.79) * mm, "end": v(-8.74, -65.94) * mm});
            skArc(sketch, "E1318", {"start": v(-8.74, -65.94) * mm, "mid": v(-8.65, -66.08) * mm, "end": v(-8.5, -66.18) * mm});
            skArc(sketch, "E1319", {"start": v(-8.5, -66.18) * mm, "mid": v(-8.11, -66.3) * mm, "end": v(-7.72, -66.42) * mm});
            skArc(sketch, "E1320", {"start": v(-7.72, -66.42) * mm, "mid": v(-7.11, -66.63) * mm, "end": v(-6.54, -66.92) * mm});
            skArc(sketch, "E1321", {"start": v(-6.54, -66.92) * mm, "mid": v(-5.83, -67.36) * mm, "end": v(-5.15, -67.85) * mm});
            skArc(sketch, "E1322", {"start": v(-5.15, -67.85) * mm, "mid": v(-4.48, -68.4) * mm, "end": v(-3.83, -69) * mm});
            skArc(sketch, "E1323", {"start": v(-3.83, -69) * mm, "mid": v(-3.3, -69.58) * mm, "end": v(-2.82, -70.2) * mm});
            skArc(sketch, "E1324", {"start": v(-2.82, -70.2) * mm, "mid": v(-2.45, -70.77) * mm, "end": v(-2.13, -71.36) * mm});
            skArc(sketch, "E1325", {"start": v(-2.13, -71.36) * mm, "mid": v(-1.81, -72.07) * mm, "end": v(-1.53, -72.79) * mm});
            skArc(sketch, "E1326", {"start": v(-1.53, -72.79) * mm, "mid": v(-1.3, -73.46) * mm, "end": v(-1.11, -74.13) * mm});
            skArc(sketch, "E1327", {"start": v(-1.11, -74.13) * mm, "mid": v(-1.1, -74.44) * mm, "end": v(-1.2, -74.72) * mm});
            skArc(sketch, "E1328", {"start": v(-1.2, -74.72) * mm, "mid": v(-1.3, -74.82) * mm, "end": v(-1.44, -74.86) * mm});
            skArc(sketch, "E1329", {"start": v(-1.44, -74.86) * mm, "mid": v(-4.72, -74.9) * mm, "end": v(-7.99, -74.93) * mm});
            skArc(sketch, "E1330", {"start": v(-7.99, -74.93) * mm, "mid": v(-12.08, -74.96) * mm, "end": v(-16.18, -74.98) * mm});
            skArc(sketch, "E1331", {"start": v(-16.18, -74.98) * mm, "mid": v(-22.04, -75) * mm, "end": v(-27.9, -75) * mm});
            skLineSegment(sketch, "E1332", {"start": v(-27.9, -75) * mm, "end": v(-54.43, -75) * mm});
            skLineSegment(sketch, "E1333", {"start": v(-54.43, -75) * mm, "end": v(-54.43, -36.98) * mm});
            skLineSegment(sketch, "E1334", {"start": v(-54.43, -36.98) * mm, "end": v(-54.43, 1.04) * mm});
            skLineSegment(sketch, "E1335", {"start": v(-54.43, 1.04) * mm, "end": v(-56.09, 1.04) * mm});
            skLineSegment(sketch, "E1336", {"start": v(-56.09, 1.04) * mm, "end": v(-57.75, 1.04) * mm});
            skLineSegment(sketch, "E1337", {"start": v(-57.75, 1.04) * mm, "end": v(-57.75, -36.98) * mm});
            skLineSegment(sketch, "E1338", {"start": v(-57.75, -36.98) * mm, "end": v(-57.75, -75) * mm});
            skLineSegment(sketch, "E1339", {"start": v(-57.75, -75) * mm, "end": v(-84.3, -75) * mm});
            skLineSegment(sketch, "E1340", {"start": v(-84.3, -75) * mm, "end": v(-110.84, -75) * mm});
            skLineSegment(sketch, "E1341", {"start": v(-110.84, -75) * mm, "end": v(-110.83, -73.96) * mm});
            skArc(sketch, "E1342", {"start": v(-110.83, -73.96) * mm, "mid": v(-110.72, -72.91) * mm, "end": v(-110.38, -71.91) * mm});
            skArc(sketch, "E1343", {"start": v(-110.38, -71.91) * mm, "mid": v(-109.78, -70.78) * mm, "end": v(-109.04, -69.73) * mm});
            skArc(sketch, "E1344", {"start": v(-109.04, -69.73) * mm, "mid": v(-108.15, -68.74) * mm, "end": v(-107.14, -67.85) * mm});
            skArc(sketch, "E1345", {"start": v(-107.14, -67.85) * mm, "mid": v(-106.13, -67.18) * mm, "end": v(-105.02, -66.68) * mm});
            skArc(sketch, "E1346", {"start": v(-105.02, -66.68) * mm, "mid": v(-104.7, -66.56) * mm, "end": v(-104.4, -66.44) * mm});
            skArc(sketch, "E1347", {"start": v(-104.4, -66.44) * mm, "mid": v(-104.12, -66.32) * mm, "end": v(-103.86, -66.2) * mm});
            skArc(sketch, "E1348", {"start": v(-103.86, -66.2) * mm, "mid": v(-103.64, -66.1) * mm, "end": v(-103.43, -65.98) * mm});
            skArc(sketch, "E1349", {"start": v(-103.43, -65.98) * mm, "mid": v(-103.39, -65.94) * mm, "end": v(-103.37, -65.88) * mm});
            skArc(sketch, "E1350", {"start": v(-103.37, -65.88) * mm, "mid": v(-103.38, -65.83) * mm, "end": v(-103.4, -65.78) * mm});
            skArc(sketch, "E1351", {"start": v(-103.4, -65.78) * mm, "mid": v(-103.47, -65.68) * mm, "end": v(-103.54, -65.59) * mm});
            skArc(sketch, "E1352", {"start": v(-103.54, -65.59) * mm, "mid": v(-103.63, -65.48) * mm, "end": v(-103.73, -65.37) * mm});
            skArc(sketch, "E1353", {"start": v(-103.73, -65.37) * mm, "mid": v(-103.84, -65.26) * mm, "end": v(-103.95, -65.16) * mm});
            skArc(sketch, "E1354", {"start": v(-103.95, -65.16) * mm, "mid": v(-104.18, -64.93) * mm, "end": v(-104.38, -64.67) * mm});
            skArc(sketch, "E1355", {"start": v(-104.38, -64.67) * mm, "mid": v(-104.67, -64.23) * mm, "end": v(-104.95, -63.78) * mm});
            skArc(sketch, "E1356", {"start": v(-104.95, -63.78) * mm, "mid": v(-105.22, -63.33) * mm, "end": v(-105.48, -62.86) * mm});
            skArc(sketch, "E1357", {"start": v(-105.48, -62.86) * mm, "mid": v(-105.56, -62.67) * mm, "end": v(-105.58, -62.46) * mm});
            skArc(sketch, "E1358", {"start": v(-105.58, -62.46) * mm, "mid": v(-105.57, -62.43) * mm, "end": v(-105.54, -62.4) * mm});
            skArc(sketch, "E1359", {"start": v(-105.54, -62.4) * mm, "mid": v(-105.39, -62.37) * mm, "end": v(-105.24, -62.33) * mm});
            skArc(sketch, "E1360", {"start": v(-105.24, -62.33) * mm, "mid": v(-105.05, -62.28) * mm, "end": v(-104.86, -62.24) * mm});
            skArc(sketch, "E1361", {"start": v(-104.86, -62.24) * mm, "mid": v(-104.63, -62.2) * mm, "end": v(-104.4, -62.17) * mm});
            skArc(sketch, "E1362", {"start": v(-104.4, -62.17) * mm, "mid": v(-103.84, -62.05) * mm, "end": v(-103.29, -61.86) * mm});
            skArc(sketch, "E1363", {"start": v(-103.29, -61.86) * mm, "mid": v(-102.57, -61.55) * mm, "end": v(-101.87, -61.2) * mm});
            skArc(sketch, "E1364", {"start": v(-101.87, -61.2) * mm, "mid": v(-101.22, -60.84) * mm, "end": v(-100.58, -60.45) * mm});
            skArc(sketch, "E1365", {"start": v(-100.58, -60.45) * mm, "mid": v(-100.32, -60.22) * mm, "end": v(-100.15, -59.92) * mm});
            skArc(sketch, "E1366", {"start": v(-100.15, -59.92) * mm, "mid": v(-100.12, -59.82) * mm, "end": v(-100.13, -59.73) * mm});
            skArc(sketch, "E1367", {"start": v(-100.13, -59.73) * mm, "mid": v(-100.16, -59.6) * mm, "end": v(-100.2, -59.5) * mm});
            skArc(sketch, "E1368", {"start": v(-100.2, -59.5) * mm, "mid": v(-100.27, -59.36) * mm, "end": v(-100.36, -59.25) * mm});
            skArc(sketch, "E1369", {"start": v(-100.36, -59.25) * mm, "mid": v(-100.45, -59.13) * mm, "end": v(-100.56, -59.03) * mm});
            skArc(sketch, "E1370", {"start": v(-100.56, -59.03) * mm, "mid": v(-100.69, -58.92) * mm, "end": v(-100.8, -58.8) * mm});
            skArc(sketch, "E1371", {"start": v(-100.8, -58.8) * mm, "mid": v(-100.91, -58.63) * mm, "end": v(-101.02, -58.47) * mm});
            skArc(sketch, "E1372", {"start": v(-101.02, -58.47) * mm, "mid": v(-101.12, -58.3) * mm, "end": v(-101.2, -58.12) * mm});
            skArc(sketch, "E1373", {"start": v(-101.2, -58.12) * mm, "mid": v(-101.26, -57.96) * mm, "end": v(-101.31, -57.8) * mm});
            skArc(sketch, "E1374", {"start": v(-101.31, -57.8) * mm, "mid": v(-101.35, -57.6) * mm, "end": v(-101.38, -57.38) * mm});
            skArc(sketch, "E1375", {"start": v(-101.38, -57.38) * mm, "mid": v(-101.37, -57.26) * mm, "end": v(-101.32, -57.15) * mm});
            skArc(sketch, "E1376", {"start": v(-101.32, -57.15) * mm, "mid": v(-101.24, -57.06) * mm, "end": v(-101.13, -57) * mm});
            skArc(sketch, "E1377", {"start": v(-101.13, -57) * mm, "mid": v(-100.92, -56.93) * mm, "end": v(-100.7, -56.88) * mm});
            skArc(sketch, "E1378", {"start": v(-100.7, -56.88) * mm, "mid": v(-99.26, -56.5) * mm, "end": v(-97.86, -56) * mm});
            skArc(sketch, "E1379", {"start": v(-97.86, -56) * mm, "mid": v(-96.52, -55.41) * mm, "end": v(-95.23, -54.71) * mm});
            skArc(sketch, "E1380", {"start": v(-95.23, -54.71) * mm, "mid": v(-93.93, -53.87) * mm, "end": v(-92.7, -52.94) * mm});
            skArc(sketch, "E1381", {"start": v(-92.7, -52.94) * mm, "mid": v(-91.42, -51.82) * mm, "end": v(-90.2, -50.63) * mm});
            skArc(sketch, "E1382", {"start": v(-90.2, -50.63) * mm, "mid": v(-89.2, -49.55) * mm, "end": v(-88.27, -48.42) * mm});
            skArc(sketch, "E1383", {"start": v(-88.27, -48.42) * mm, "mid": v(-87.46, -47.32) * mm, "end": v(-86.71, -46.17) * mm});
            skArc(sketch, "E1384", {"start": v(-86.71, -46.17) * mm, "mid": v(-86.07, -45.03) * mm, "end": v(-85.5, -43.85) * mm});
            skArc(sketch, "E1385", {"start": v(-85.5, -43.85) * mm, "mid": v(-85.02, -42.64) * mm, "end": v(-84.62, -41.4) * mm});
            skArc(sketch, "E1386", {"start": v(-84.62, -41.4) * mm, "mid": v(-84.35, -40.45) * mm, "end": v(-84.1, -39.5) * mm});
            skArc(sketch, "E1387", {"start": v(-84.1, -39.5) * mm, "mid": v(-83.97, -38.98) * mm, "end": v(-83.9, -38.45) * mm});
            skArc(sketch, "E1388", {"start": v(-83.9, -38.45) * mm, "mid": v(-83.88, -38.16) * mm, "end": v(-83.91, -37.87) * mm});
            skArc(sketch, "E1389", {"start": v(-83.91, -37.87) * mm, "mid": v(-84, -37.73) * mm, "end": v(-84.16, -37.67) * mm});
            skArc(sketch, "E1390", {"start": v(-84.16, -37.67) * mm, "mid": v(-84.24, -37.68) * mm, "end": v(-84.32, -37.69) * mm});
            skArc(sketch, "E1391", {"start": v(-84.32, -37.69) * mm, "mid": v(-84.38, -37.71) * mm, "end": v(-84.45, -37.74) * mm});
            skArc(sketch, "E1392", {"start": v(-84.45, -37.74) * mm, "mid": v(-84.5, -37.78) * mm, "end": v(-84.54, -37.82) * mm});
            skArc(sketch, "E1393", {"start": v(-84.54, -37.82) * mm, "mid": v(-84.56, -37.86) * mm, "end": v(-84.57, -37.9) * mm});
            skArc(sketch, "E1394", {"start": v(-84.57, -37.9) * mm, "mid": v(-84.58, -37.99) * mm, "end": v(-84.6, -38.06) * mm});
            skArc(sketch, "E1395", {"start": v(-84.6, -38.06) * mm, "mid": v(-84.73, -38.26) * mm, "end": v(-84.86, -38.46) * mm});
            skArc(sketch, "E1396", {"start": v(-84.86, -38.46) * mm, "mid": v(-85.01, -38.7) * mm, "end": v(-85.18, -38.92) * mm});
            skArc(sketch, "E1397", {"start": v(-85.18, -38.92) * mm, "mid": v(-85.36, -39.18) * mm, "end": v(-85.55, -39.44) * mm});
            skArc(sketch, "E1398", {"start": v(-85.55, -39.44) * mm, "mid": v(-85.88, -39.84) * mm, "end": v(-86.22, -40.23) * mm});
            skArc(sketch, "E1399", {"start": v(-86.22, -40.23) * mm, "mid": v(-86.43, -40.4) * mm, "end": v(-86.67, -40.51) * mm});
            skArc(sketch, "E1400", {"start": v(-86.67, -40.51) * mm, "mid": v(-86.83, -40.5) * mm, "end": v(-86.95, -40.39) * mm});
            skArc(sketch, "E1401", {"start": v(-86.95, -40.39) * mm, "mid": v(-87.03, -40.14) * mm, "end": v(-87.06, -39.88) * mm});
            skArc(sketch, "E1402", {"start": v(-87.06, -39.88) * mm, "mid": v(-87.08, -39.63) * mm, "end": v(-87.14, -39.39) * mm});
            skArc(sketch, "E1403", {"start": v(-87.14, -39.39) * mm, "mid": v(-87.23, -39.28) * mm, "end": v(-87.37, -39.25) * mm});
            skArc(sketch, "E1404", {"start": v(-87.37, -39.25) * mm, "mid": v(-87.56, -39.32) * mm, "end": v(-87.72, -39.45) * mm});
            skArc(sketch, "E1405", {"start": v(-87.72, -39.45) * mm, "mid": v(-87.97, -39.76) * mm, "end": v(-88.2, -40.08) * mm});
            skArc(sketch, "E1406", {"start": v(-88.2, -40.08) * mm, "mid": v(-88.46, -40.47) * mm, "end": v(-88.74, -40.84) * mm});
            skArc(sketch, "E1407", {"start": v(-88.74, -40.84) * mm, "mid": v(-88.92, -41.02) * mm, "end": v(-89.15, -41.15) * mm});
            skArc(sketch, "E1408", {"start": v(-89.15, -41.15) * mm, "mid": v(-89.3, -41.17) * mm, "end": v(-89.45, -41.1) * mm});
            skArc(sketch, "E1409", {"start": v(-89.45, -41.1) * mm, "mid": v(-89.6, -40.92) * mm, "end": v(-89.68, -40.71) * mm});
            skArc(sketch, "E1410", {"start": v(-89.68, -40.71) * mm, "mid": v(-89.78, -40.5) * mm, "end": v(-89.92, -40.31) * mm});
            skArc(sketch, "E1411", {"start": v(-89.92, -40.31) * mm, "mid": v(-90.05, -40.25) * mm, "end": v(-90.2, -40.28) * mm});
            skArc(sketch, "E1412", {"start": v(-90.2, -40.28) * mm, "mid": v(-90.38, -40.44) * mm, "end": v(-90.5, -40.64) * mm});
            skArc(sketch, "E1413", {"start": v(-90.5, -40.64) * mm, "mid": v(-90.66, -41.04) * mm, "end": v(-90.79, -41.44) * mm});
            skArc(sketch, "E1414", {"start": v(-90.79, -41.44) * mm, "mid": v(-90.87, -41.7) * mm, "end": v(-90.97, -41.97) * mm});
            skArc(sketch, "E1415", {"start": v(-90.97, -41.97) * mm, "mid": v(-91.11, -42.32) * mm, "end": v(-91.26, -42.66) * mm});
            skArc(sketch, "E1416", {"start": v(-91.26, -42.66) * mm, "mid": v(-91.42, -43.02) * mm, "end": v(-91.59, -43.38) * mm});
            skArc(sketch, "E1417", {"start": v(-91.59, -43.38) * mm, "mid": v(-91.75, -43.7) * mm, "end": v(-91.92, -44.03) * mm});
            skArc(sketch, "E1418", {"start": v(-91.92, -44.03) * mm, "mid": v(-92.2, -44.53) * mm, "end": v(-92.47, -45.02) * mm});
            skArc(sketch, "E1419", {"start": v(-92.47, -45.02) * mm, "mid": v(-92.55, -45.14) * mm, "end": v(-92.66, -45.23) * mm});
            skArc(sketch, "E1420", {"start": v(-92.66, -45.23) * mm, "mid": v(-92.74, -45.24) * mm, "end": v(-92.8, -45.2) * mm});
            skArc(sketch, "E1421", {"start": v(-92.8, -45.2) * mm, "mid": v(-92.9, -44.98) * mm, "end": v(-92.99, -44.77) * mm});
            skArc(sketch, "E1422", {"start": v(-92.99, -44.77) * mm, "mid": v(-93.12, -44.47) * mm, "end": v(-93.28, -44.18) * mm});
            skArc(sketch, "E1423", {"start": v(-93.28, -44.18) * mm, "mid": v(-93.42, -44.08) * mm, "end": v(-93.6, -44.09) * mm});
            skArc(sketch, "E1424", {"start": v(-93.6, -44.09) * mm, "mid": v(-93.78, -44.22) * mm, "end": v(-93.9, -44.41) * mm});
            skArc(sketch, "E1425", {"start": v(-93.9, -44.41) * mm, "mid": v(-94.06, -44.86) * mm, "end": v(-94.2, -45.3) * mm});
            skArc(sketch, "E1426", {"start": v(-94.2, -45.3) * mm, "mid": v(-94.28, -45.6) * mm, "end": v(-94.39, -45.88) * mm});
            skArc(sketch, "E1427", {"start": v(-94.39, -45.88) * mm, "mid": v(-94.53, -46.23) * mm, "end": v(-94.68, -46.57) * mm});
            skArc(sketch, "E1428", {"start": v(-94.68, -46.57) * mm, "mid": v(-94.85, -46.9) * mm, "end": v(-95.03, -47.24) * mm});
            skArc(sketch, "E1429", {"start": v(-95.03, -47.24) * mm, "mid": v(-95.2, -47.53) * mm, "end": v(-95.38, -47.8) * mm});
            skArc(sketch, "E1430", {"start": v(-95.38, -47.8) * mm, "mid": v(-95.6, -48.13) * mm, "end": v(-95.84, -48.44) * mm});
            skArc(sketch, "E1431", {"start": v(-95.84, -48.44) * mm, "mid": v(-95.98, -48.6) * mm, "end": v(-96.14, -48.73) * mm});
            skArc(sketch, "E1432", {"start": v(-96.14, -48.73) * mm, "mid": v(-96.25, -48.8) * mm, "end": v(-96.38, -48.8) * mm});
            skArc(sketch, "E1433", {"start": v(-96.38, -48.8) * mm, "mid": v(-96.5, -48.78) * mm, "end": v(-96.62, -48.71) * mm});
            skArc(sketch, "E1434", {"start": v(-96.62, -48.71) * mm, "mid": v(-96.7, -48.64) * mm, "end": v(-96.77, -48.56) * mm});
            skArc(sketch, "E1435", {"start": v(-96.77, -48.56) * mm, "mid": v(-96.84, -48.47) * mm, "end": v(-96.9, -48.37) * mm});
            skArc(sketch, "E1436", {"start": v(-96.9, -48.37) * mm, "mid": v(-96.94, -48.28) * mm, "end": v(-96.98, -48.18) * mm});
            skArc(sketch, "E1437", {"start": v(-96.98, -48.18) * mm, "mid": v(-97, -48.1) * mm, "end": v(-97.01, -48) * mm});
            skArc(sketch, "E1438", {"start": v(-97.01, -48) * mm, "mid": v(-97.05, -47.84) * mm, "end": v(-97.16, -47.7) * mm});
            skArc(sketch, "E1439", {"start": v(-97.16, -47.7) * mm, "mid": v(-97.3, -47.64) * mm, "end": v(-97.45, -47.67) * mm});
            skArc(sketch, "E1440", {"start": v(-97.45, -47.67) * mm, "mid": v(-97.68, -47.84) * mm, "end": v(-97.87, -48.05) * mm});
            skArc(sketch, "E1441", {"start": v(-97.87, -48.05) * mm, "mid": v(-98.07, -48.37) * mm, "end": v(-98.24, -48.7) * mm});
            skArc(sketch, "E1442", {"start": v(-98.24, -48.7) * mm, "mid": v(-98.48, -49.17) * mm, "end": v(-98.78, -49.6) * mm});
            skArc(sketch, "E1443", {"start": v(-98.78, -49.6) * mm, "mid": v(-99.23, -50.17) * mm, "end": v(-99.7, -50.72) * mm});
            skArc(sketch, "E1444", {"start": v(-99.7, -50.72) * mm, "mid": v(-100.2, -51.24) * mm, "end": v(-100.69, -51.74) * mm});
            skArc(sketch, "E1445", {"start": v(-100.69, -51.74) * mm, "mid": v(-100.85, -51.8) * mm, "end": v(-101, -51.74) * mm});
            skArc(sketch, "E1446", {"start": v(-101, -51.74) * mm, "mid": v(-101.03, -51.69) * mm, "end": v(-101.03, -51.62) * mm});
            skArc(sketch, "E1447", {"start": v(-101.03, -51.62) * mm, "mid": v(-100.84, -51.05) * mm, "end": v(-100.65, -50.48) * mm});
            skArc(sketch, "E1448", {"start": v(-100.65, -50.48) * mm, "mid": v(-100.42, -49.83) * mm, "end": v(-100.18, -49.17) * mm});
            skArc(sketch, "E1449", {"start": v(-100.18, -49.17) * mm, "mid": v(-99.9, -48.4) * mm, "end": v(-99.6, -47.64) * mm});
            skArc(sketch, "E1450", {"start": v(-99.6, -47.64) * mm, "mid": v(-99.03, -46.09) * mm, "end": v(-98.49, -44.51) * mm});
            skArc(sketch, "E1451", {"start": v(-98.49, -44.51) * mm, "mid": v(-98.1, -43.25) * mm, "end": v(-97.79, -41.98) * mm});
            skArc(sketch, "E1452", {"start": v(-97.79, -41.98) * mm, "mid": v(-97.57, -40.82) * mm, "end": v(-97.41, -39.66) * mm});
            skArc(sketch, "E1453", {"start": v(-97.41, -39.66) * mm, "mid": v(-97.32, -38.44) * mm, "end": v(-97.29, -37.22) * mm});
            skArc(sketch, "E1454", {"start": v(-97.29, -37.22) * mm, "mid": v(-97.25, -35.6) * mm, "end": v(-97.13, -33.97) * mm});
            skArc(sketch, "E1455", {"start": v(-97.13, -33.97) * mm, "mid": v(-96.95, -32.52) * mm, "end": v(-96.67, -31.08) * mm});
            skArc(sketch, "E1456", {"start": v(-96.67, -31.08) * mm, "mid": v(-96.33, -29.78) * mm, "end": v(-95.9, -28.52) * mm});
            skArc(sketch, "E1457", {"start": v(-95.9, -28.52) * mm, "mid": v(-95.41, -27.39) * mm, "end": v(-94.83, -26.3) * mm});
            skArc(sketch, "E1458", {"start": v(-94.83, -26.3) * mm, "mid": v(-93.71, -24.8) * mm, "end": v(-92.33, -23.56) * mm});
            skArc(sketch, "E1459", {"start": v(-92.33, -23.56) * mm, "mid": v(-90.98, -22.9) * mm, "end": v(-89.48, -22.77) * mm});
            skArc(sketch, "E1460", {"start": v(-89.48, -22.77) * mm, "mid": v(-88.14, -23.2) * mm, "end": v(-87.07, -24.1) * mm});
            skArc(sketch, "E1461", {"start": v(-87.07, -24.1) * mm, "mid": v(-86.21, -25.57) * mm, "end": v(-85.73, -27.19) * mm});
            skArc(sketch, "E1462", {"start": v(-85.73, -27.19) * mm, "mid": v(-85.64, -27.62) * mm, "end": v(-85.52, -28.05) * mm});
            skArc(sketch, "E1463", {"start": v(-85.52, -28.05) * mm, "mid": v(-85.4, -28.27) * mm, "end": v(-85.21, -28.43) * mm});
            skArc(sketch, "E1464", {"start": v(-85.21, -28.43) * mm, "mid": v(-85.05, -28.46) * mm, "end": v(-84.92, -28.36) * mm});
            skArc(sketch, "E1465", {"start": v(-84.92, -28.36) * mm, "mid": v(-84.79, -28.1) * mm, "end": v(-84.7, -27.8) * mm});
            skArc(sketch, "E1466", {"start": v(-84.7, -27.8) * mm, "mid": v(-84.52, -27.07) * mm, "end": v(-84.3, -26.34) * mm});
            skArc(sketch, "E1467", {"start": v(-84.3, -26.34) * mm, "mid": v(-84, -25.5) * mm, "end": v(-83.68, -24.69) * mm});
            skArc(sketch, "E1468", {"start": v(-83.68, -24.69) * mm, "mid": v(-83.34, -23.92) * mm, "end": v(-82.98, -23.17) * mm});
            skArc(sketch, "E1469", {"start": v(-82.98, -23.17) * mm, "mid": v(-82.7, -22.66) * mm, "end": v(-82.36, -22.2) * mm});
            skArc(sketch, "E1470", {"start": v(-82.36, -22.2) * mm, "mid": v(-81.92, -21.7) * mm, "end": v(-81.42, -21.27) * mm});
            skArc(sketch, "E1471", {"start": v(-81.42, -21.27) * mm, "mid": v(-80.9, -20.93) * mm, "end": v(-80.32, -20.65) * mm});
            skArc(sketch, "E1472", {"start": v(-80.32, -20.65) * mm, "mid": v(-79.76, -20.48) * mm, "end": v(-79.17, -20.39) * mm});
            skArc(sketch, "E1473", {"start": v(-79.17, -20.39) * mm, "mid": v(-78.64, -20.4) * mm, "end": v(-78.12, -20.51) * mm});
            skArc(sketch, "E1474", {"start": v(-78.12, -20.51) * mm, "mid": v(-77.91, -20.59) * mm, "end": v(-77.72, -20.67) * mm});
            skArc(sketch, "E1475", {"start": v(-77.72, -20.67) * mm, "mid": v(-77.52, -20.76) * mm, "end": v(-77.33, -20.87) * mm});
            skArc(sketch, "E1476", {"start": v(-77.33, -20.87) * mm, "mid": v(-77.16, -20.97) * mm, "end": v(-77, -21.08) * mm});
            skArc(sketch, "E1477", {"start": v(-77, -21.08) * mm, "mid": v(-76.88, -21.17) * mm, "end": v(-76.79, -21.27) * mm});
            skArc(sketch, "E1478", {"start": v(-76.79, -21.27) * mm, "mid": v(-76.57, -21.63) * mm, "end": v(-76.48, -22.04) * mm});
            skArc(sketch, "E1479", {"start": v(-76.48, -22.04) * mm, "mid": v(-76.42, -23.03) * mm, "end": v(-76.4, -24.03) * mm});
            skArc(sketch, "E1480", {"start": v(-76.4, -24.03) * mm, "mid": v(-76.41, -25.03) * mm, "end": v(-76.44, -26.03) * mm});
            skArc(sketch, "E1481", {"start": v(-76.44, -26.03) * mm, "mid": v(-76.54, -26.25) * mm, "end": v(-76.76, -26.34) * mm});
            skArc(sketch, "E1482", {"start": v(-76.76, -26.34) * mm, "mid": v(-76.84, -26.35) * mm, "end": v(-76.91, -26.4) * mm});
            skArc(sketch, "E1483", {"start": v(-76.91, -26.4) * mm, "mid": v(-77, -26.48) * mm, "end": v(-77.06, -26.57) * mm});
            skArc(sketch, "E1484", {"start": v(-77.06, -26.57) * mm, "mid": v(-77.13, -26.7) * mm, "end": v(-77.2, -26.84) * mm});
            skArc(sketch, "E1485", {"start": v(-77.2, -26.84) * mm, "mid": v(-77.24, -27) * mm, "end": v(-77.28, -27.15) * mm});
            skArc(sketch, "E1486", {"start": v(-77.28, -27.15) * mm, "mid": v(-77.33, -27.35) * mm, "end": v(-77.4, -27.55) * mm});
            skArc(sketch, "E1487", {"start": v(-77.4, -27.55) * mm, "mid": v(-77.47, -27.69) * mm, "end": v(-77.56, -27.8) * mm});
            skArc(sketch, "E1488", {"start": v(-77.56, -27.8) * mm, "mid": v(-77.68, -27.9) * mm, "end": v(-77.8, -27.96) * mm});
            skArc(sketch, "E1489", {"start": v(-77.8, -27.96) * mm, "mid": v(-77.99, -28.02) * mm, "end": v(-78.17, -28.05) * mm});
            skArc(sketch, "E1490", {"start": v(-78.17, -28.05) * mm, "mid": v(-78.5, -28.13) * mm, "end": v(-78.8, -28.3) * mm});
            skArc(sketch, "E1491", {"start": v(-78.8, -28.3) * mm, "mid": v(-78.97, -28.5) * mm, "end": v(-79, -28.76) * mm});
            skArc(sketch, "E1492", {"start": v(-79, -28.76) * mm, "mid": v(-78.91, -29.1) * mm, "end": v(-78.72, -29.38) * mm});
            skArc(sketch, "E1493", {"start": v(-78.72, -29.38) * mm, "mid": v(-78.35, -29.73) * mm, "end": v(-77.94, -30.03) * mm});
            skArc(sketch, "E1494", {"start": v(-77.94, -30.03) * mm, "mid": v(-77.41, -30.42) * mm, "end": v(-76.93, -30.85) * mm});
            skArc(sketch, "E1495", {"start": v(-76.93, -30.85) * mm, "mid": v(-76.46, -31.36) * mm, "end": v(-76.03, -31.9) * mm});
            skArc(sketch, "E1496", {"start": v(-76.03, -31.9) * mm, "mid": v(-75.6, -32.55) * mm, "end": v(-75.22, -33.23) * mm});
            skArc(sketch, "E1497", {"start": v(-75.22, -33.23) * mm, "mid": v(-74.81, -34.06) * mm, "end": v(-74.44, -34.9) * mm});
            skArc(sketch, "E1498", {"start": v(-74.44, -34.9) * mm, "mid": v(-74.28, -35.27) * mm, "end": v(-74.12, -35.64) * mm});
            skArc(sketch, "E1499", {"start": v(-74.12, -35.64) * mm, "mid": v(-73.96, -35.96) * mm, "end": v(-73.8, -36.27) * mm});
            skArc(sketch, "E1500", {"start": v(-73.8, -36.27) * mm, "mid": v(-73.65, -36.52) * mm, "end": v(-73.5, -36.76) * mm});
            skArc(sketch, "E1501", {"start": v(-73.5, -36.76) * mm, "mid": v(-73.44, -36.82) * mm, "end": v(-73.36, -36.84) * mm});
            skArc(sketch, "E1502", {"start": v(-73.36, -36.84) * mm, "mid": v(-73.27, -36.84) * mm, "end": v(-73.18, -36.82) * mm});
            skArc(sketch, "E1503", {"start": v(-73.18, -36.82) * mm, "mid": v(-72.92, -36.74) * mm, "end": v(-72.67, -36.66) * mm});
            skArc(sketch, "E1504", {"start": v(-72.67, -36.66) * mm, "mid": v(-72.37, -36.57) * mm, "end": v(-72.08, -36.47) * mm});
            skArc(sketch, "E1505", {"start": v(-72.08, -36.47) * mm, "mid": v(-71.75, -36.35) * mm, "end": v(-71.42, -36.23) * mm});
            skArc(sketch, "E1506", {"start": v(-71.42, -36.23) * mm, "mid": v(-70.93, -36.07) * mm, "end": v(-70.43, -35.92) * mm});
            skArc(sketch, "E1507", {"start": v(-70.43, -35.92) * mm, "mid": v(-69.95, -35.82) * mm, "end": v(-69.48, -35.74) * mm});
            skArc(sketch, "E1508", {"start": v(-69.48, -35.74) * mm, "mid": v(-68.9, -35.69) * mm, "end": v(-68.3, -35.66) * mm});
            skArc(sketch, "E1509", {"start": v(-68.3, -35.66) * mm, "mid": v(-67.43, -35.64) * mm, "end": v(-66.55, -35.64) * mm});
            skLineSegment(sketch, "E1510", {"start": v(-66.55, -35.64) * mm, "end": v(-63.33, -35.65) * mm});
            skLineSegment(sketch, "E1511", {"start": v(-63.33, -35.65) * mm, "end": v(-63.19, -34.94) * mm});
            skArc(sketch, "E1512", {"start": v(-63.19, -34.94) * mm, "mid": v(-63.14, -34.76) * mm, "end": v(-63.08, -34.59) * mm});
            skArc(sketch, "E1513", {"start": v(-63.08, -34.59) * mm, "mid": v(-62.98, -34.35) * mm, "end": v(-62.88, -34.12) * mm});
            skArc(sketch, "E1514", {"start": v(-62.88, -34.12) * mm, "mid": v(-62.75, -33.87) * mm, "end": v(-62.61, -33.62) * mm});
            skArc(sketch, "E1515", {"start": v(-62.61, -33.62) * mm, "mid": v(-62.48, -33.4) * mm, "end": v(-62.33, -33.17) * mm});
            skArc(sketch, "E1516", {"start": v(-62.33, -33.17) * mm, "mid": v(-62.13, -32.85) * mm, "end": v(-61.96, -32.52) * mm});
            skArc(sketch, "E1517", {"start": v(-61.96, -32.52) * mm, "mid": v(-61.83, -32.24) * mm, "end": v(-61.75, -31.94) * mm});
            skArc(sketch, "E1518", {"start": v(-61.75, -31.94) * mm, "mid": v(-61.68, -31.57) * mm, "end": v(-61.65, -31.2) * mm});
            skArc(sketch, "E1519", {"start": v(-61.65, -31.2) * mm, "mid": v(-61.63, -30.63) * mm, "end": v(-61.62, -30.06) * mm});
            skArc(sketch, "E1520", {"start": v(-61.62, -30.06) * mm, "mid": v(-61.62, -29.66) * mm, "end": v(-61.63, -29.27) * mm});
            skArc(sketch, "E1521", {"start": v(-61.63, -29.27) * mm, "mid": v(-61.65, -28.93) * mm, "end": v(-61.68, -28.6) * mm});
            skArc(sketch, "E1522", {"start": v(-61.68, -28.6) * mm, "mid": v(-61.7, -28.33) * mm, "end": v(-61.74, -28.07) * mm});
            skArc(sketch, "E1523", {"start": v(-61.74, -28.07) * mm, "mid": v(-61.77, -28.02) * mm, "end": v(-61.83, -28) * mm});
            skArc(sketch, "E1524", {"start": v(-61.83, -28) * mm, "mid": v(-61.9, -28) * mm, "end": v(-61.97, -28.02) * mm});
            skArc(sketch, "E1525", {"start": v(-61.97, -28.02) * mm, "mid": v(-62.21, -28.1) * mm, "end": v(-62.46, -28.2) * mm});
            skArc(sketch, "E1526", {"start": v(-62.46, -28.2) * mm, "mid": v(-62.75, -28.3) * mm, "end": v(-63.04, -28.42) * mm});
            skArc(sketch, "E1527", {"start": v(-63.04, -28.42) * mm, "mid": v(-63.37, -28.55) * mm, "end": v(-63.7, -28.68) * mm});
            skArc(sketch, "E1528", {"start": v(-63.7, -28.68) * mm, "mid": v(-64.2, -28.87) * mm, "end": v(-64.7, -29.04) * mm});
            skArc(sketch, "E1529", {"start": v(-64.7, -29.04) * mm, "mid": v(-65.15, -29.16) * mm, "end": v(-65.6, -29.24) * mm});
            skArc(sketch, "E1530", {"start": v(-65.6, -29.24) * mm, "mid": v(-66.14, -29.3) * mm, "end": v(-66.69, -29.34) * mm});
            skArc(sketch, "E1531", {"start": v(-66.69, -29.34) * mm, "mid": v(-67.54, -29.36) * mm, "end": v(-68.38, -29.37) * mm});
            skLineSegment(sketch, "E1532", {"start": v(-68.38, -29.37) * mm, "end": v(-71.42, -29.38) * mm});
            skLineSegment(sketch, "E1533", {"start": v(-71.42, -29.38) * mm, "end": v(-69.73, -27.65) * mm});
            skArc(sketch, "E1534", {"start": v(-69.73, -27.65) * mm, "mid": v(-69.07, -26.95) * mm, "end": v(-68.44, -26.24) * mm});
            skArc(sketch, "E1535", {"start": v(-68.44, -26.24) * mm, "mid": v(-67.92, -25.61) * mm, "end": v(-67.44, -24.97) * mm});
            skArc(sketch, "E1536", {"start": v(-67.44, -24.97) * mm, "mid": v(-67.1, -24.44) * mm, "end": v(-66.78, -23.9) * mm});
            skArc(sketch, "E1537", {"start": v(-66.78, -23.9) * mm, "mid": v(-66.64, -23.56) * mm, "end": v(-66.6, -23.2) * mm});
            skArc(sketch, "E1538", {"start": v(-66.6, -23.2) * mm, "mid": v(-66.6, -23.08) * mm, "end": v(-66.62, -22.96) * mm});
            skArc(sketch, "E1539", {"start": v(-66.62, -22.96) * mm, "mid": v(-66.65, -22.9) * mm, "end": v(-66.7, -22.84) * mm});
            skArc(sketch, "E1540", {"start": v(-66.7, -22.84) * mm, "mid": v(-66.77, -22.81) * mm, "end": v(-66.85, -22.81) * mm});
            skArc(sketch, "E1541", {"start": v(-66.85, -22.81) * mm, "mid": v(-66.97, -22.84) * mm, "end": v(-67.08, -22.88) * mm});
            skArc(sketch, "E1542", {"start": v(-67.08, -22.88) * mm, "mid": v(-67.44, -23) * mm, "end": v(-67.81, -23.1) * mm});
            skArc(sketch, "E1543", {"start": v(-67.81, -23.1) * mm, "mid": v(-68.26, -23.17) * mm, "end": v(-68.7, -23.22) * mm});
            skArc(sketch, "E1544", {"start": v(-68.7, -23.22) * mm, "mid": v(-69.12, -23.24) * mm, "end": v(-69.54, -23.24) * mm});
            skArc(sketch, "E1545", {"start": v(-69.54, -23.24) * mm, "mid": v(-69.78, -23.2) * mm, "end": v(-70, -23.12) * mm});
            skArc(sketch, "E1546", {"start": v(-70, -23.12) * mm, "mid": v(-70.1, -23.04) * mm, "end": v(-70.19, -22.93) * mm});
            skArc(sketch, "E1547", {"start": v(-70.19, -22.93) * mm, "mid": v(-70.22, -22.82) * mm, "end": v(-70.21, -22.7) * mm});
            skArc(sketch, "E1548", {"start": v(-70.21, -22.7) * mm, "mid": v(-70.14, -22.51) * mm, "end": v(-70.05, -22.34) * mm});
            skArc(sketch, "E1549", {"start": v(-70.05, -22.34) * mm, "mid": v(-69.82, -21.98) * mm, "end": v(-69.59, -21.63) * mm});
            skArc(sketch, "E1550", {"start": v(-69.59, -21.63) * mm, "mid": v(-68.98, -20.67) * mm, "end": v(-68.44, -19.66) * mm});
            skArc(sketch, "E1551", {"start": v(-68.44, -19.66) * mm, "mid": v(-67.9, -18.47) * mm, "end": v(-67.4, -17.26) * mm});
            skArc(sketch, "E1552", {"start": v(-67.4, -17.26) * mm, "mid": v(-67.01, -16.14) * mm, "end": v(-66.65, -15) * mm});
            skArc(sketch, "E1553", {"start": v(-66.65, -15) * mm, "mid": v(-66.62, -14.54) * mm, "end": v(-66.78, -14.1) * mm});
            skArc(sketch, "E1554", {"start": v(-66.78, -14.1) * mm, "mid": v(-66.83, -14.06) * mm, "end": v(-66.9, -14.06) * mm});
            skArc(sketch, "E1555", {"start": v(-66.9, -14.06) * mm, "mid": v(-67.08, -14.14) * mm, "end": v(-67.25, -14.22) * mm});
            skArc(sketch, "E1556", {"start": v(-67.25, -14.22) * mm, "mid": v(-67.48, -14.34) * mm, "end": v(-67.7, -14.47) * mm});
            skArc(sketch, "E1557", {"start": v(-67.7, -14.47) * mm, "mid": v(-67.96, -14.64) * mm, "end": v(-68.2, -14.82) * mm});
            skArc(sketch, "E1558", {"start": v(-68.2, -14.82) * mm, "mid": v(-68.88, -15.29) * mm, "end": v(-69.58, -15.72) * mm});
            skArc(sketch, "E1559", {"start": v(-69.58, -15.72) * mm, "mid": v(-70.38, -16.17) * mm, "end": v(-71.2, -16.6) * mm});
            skArc(sketch, "E1560", {"start": v(-71.2, -16.6) * mm, "mid": v(-72.05, -17) * mm, "end": v(-72.91, -17.39) * mm});
            skArc(sketch, "E1561", {"start": v(-72.91, -17.39) * mm, "mid": v(-73.75, -17.72) * mm, "end": v(-74.6, -18.01) * mm});
            skArc(sketch, "E1562", {"start": v(-74.6, -18.01) * mm, "mid": v(-74.94, -18.13) * mm, "end": v(-75.28, -18.24) * mm});
            skArc(sketch, "E1563", {"start": v(-75.28, -18.24) * mm, "mid": v(-75.57, -18.33) * mm, "end": v(-75.86, -18.42) * mm});
            skArc(sketch, "E1564", {"start": v(-75.86, -18.42) * mm, "mid": v(-76.12, -18.5) * mm, "end": v(-76.37, -18.59) * mm});
            skArc(sketch, "E1565", {"start": v(-76.37, -18.59) * mm, "mid": v(-76.4, -18.6) * mm, "end": v(-76.41, -18.6) * mm});
            skArc(sketch, "E1566", {"start": v(-76.41, -18.6) * mm, "mid": v(-76.42, -18.59) * mm, "end": v(-76.43, -18.58) * mm});
            skArc(sketch, "E1567", {"start": v(-76.43, -18.58) * mm, "mid": v(-76.44, -18.4) * mm, "end": v(-76.44, -18.24) * mm});
            skArc(sketch, "E1568", {"start": v(-76.44, -18.24) * mm, "mid": v(-76.45, -18.05) * mm, "end": v(-76.45, -17.86) * mm});
            skArc(sketch, "E1569", {"start": v(-76.45, -17.86) * mm, "mid": v(-76.46, -17.63) * mm, "end": v(-76.46, -17.4) * mm});
            skArc(sketch, "E1570", {"start": v(-76.46, -17.4) * mm, "mid": v(-76.47, -16.8) * mm, "end": v(-76.52, -16.2) * mm});
            skArc(sketch, "E1571", {"start": v(-76.52, -16.2) * mm, "mid": v(-76.61, -15.99) * mm, "end": v(-76.81, -15.87) * mm});
            skArc(sketch, "E1572", {"start": v(-76.81, -15.87) * mm, "mid": v(-77.09, -15.87) * mm, "end": v(-77.34, -15.98) * mm});
            skArc(sketch, "E1573", {"start": v(-77.34, -15.98) * mm, "mid": v(-78, -16.45) * mm, "end": v(-78.66, -16.94) * mm});
            skArc(sketch, "E1574", {"start": v(-78.66, -16.94) * mm, "mid": v(-79.29, -17.41) * mm, "end": v(-79.92, -17.87) * mm});
            skArc(sketch, "E1575", {"start": v(-79.92, -17.87) * mm, "mid": v(-80.4, -18.2) * mm, "end": v(-80.9, -18.5) * mm});
            skArc(sketch, "E1576", {"start": v(-80.9, -18.5) * mm, "mid": v(-81.3, -18.74) * mm, "end": v(-81.73, -18.95) * mm});
            skArc(sketch, "E1577", {"start": v(-81.73, -18.95) * mm, "mid": v(-82.14, -19.12) * mm, "end": v(-82.56, -19.27) * mm});
            skArc(sketch, "E1578", {"start": v(-82.56, -19.27) * mm, "mid": v(-82.75, -19.32) * mm, "end": v(-82.93, -19.37) * mm});
            skArc(sketch, "E1579", {"start": v(-82.93, -19.37) * mm, "mid": v(-83, -19.36) * mm, "end": v(-83.05, -19.32) * mm});
            skArc(sketch, "E1580", {"start": v(-83.05, -19.32) * mm, "mid": v(-83.07, -19.25) * mm, "end": v(-83.07, -19.18) * mm});
            skArc(sketch, "E1581", {"start": v(-83.07, -19.18) * mm, "mid": v(-83, -18.96) * mm, "end": v(-82.9, -18.73) * mm});
            skArc(sketch, "E1582", {"start": v(-82.9, -18.73) * mm, "mid": v(-82.8, -18.38) * mm, "end": v(-82.72, -18.02) * mm});
            skArc(sketch, "E1583", {"start": v(-82.72, -18.02) * mm, "mid": v(-82.66, -17.63) * mm, "end": v(-82.64, -17.23) * mm});
            skArc(sketch, "E1584", {"start": v(-82.64, -17.23) * mm, "mid": v(-82.65, -16.89) * mm, "end": v(-82.68, -16.55) * mm});
            skArc(sketch, "E1585", {"start": v(-82.68, -16.55) * mm, "mid": v(-82.74, -16.43) * mm, "end": v(-82.86, -16.38) * mm});
            skArc(sketch, "E1586", {"start": v(-82.86, -16.38) * mm, "mid": v(-82.94, -16.4) * mm, "end": v(-83, -16.43) * mm});
            skArc(sketch, "E1587", {"start": v(-83, -16.43) * mm, "mid": v(-83.18, -16.56) * mm, "end": v(-83.36, -16.7) * mm});
            skArc(sketch, "E1588", {"start": v(-83.36, -16.7) * mm, "mid": v(-83.58, -16.87) * mm, "end": v(-83.78, -17.05) * mm});
            skArc(sketch, "E1589", {"start": v(-83.78, -17.05) * mm, "mid": v(-84.01, -17.26) * mm, "end": v(-84.24, -17.47) * mm});
            skArc(sketch, "E1590", {"start": v(-84.24, -17.47) * mm, "mid": v(-84.74, -17.9) * mm, "end": v(-85.27, -18.28) * mm});
            skArc(sketch, "E1591", {"start": v(-85.27, -18.28) * mm, "mid": v(-86.1, -18.8) * mm, "end": v(-86.94, -19.28) * mm});
            skArc(sketch, "E1592", {"start": v(-86.94, -19.28) * mm, "mid": v(-87.8, -19.74) * mm, "end": v(-88.69, -20.17) * mm});
            skArc(sketch, "E1593", {"start": v(-88.69, -20.17) * mm, "mid": v(-89.33, -20.44) * mm, "end": v(-90, -20.66) * mm});
            skArc(sketch, "E1594", {"start": v(-90, -20.66) * mm, "mid": v(-90.16, -20.7) * mm, "end": v(-90.33, -20.7) * mm});
            skArc(sketch, "E1595", {"start": v(-90.33, -20.7) * mm, "mid": v(-90.42, -20.68) * mm, "end": v(-90.48, -20.61) * mm});
            skArc(sketch, "E1596", {"start": v(-90.48, -20.61) * mm, "mid": v(-90.51, -20.48) * mm, "end": v(-90.52, -20.34) * mm});
            skArc(sketch, "E1597", {"start": v(-90.52, -20.34) * mm, "mid": v(-90.48, -19.96) * mm, "end": v(-90.44, -19.57) * mm});
            skArc(sketch, "E1598", {"start": v(-90.44, -19.57) * mm, "mid": v(-90.42, -19.32) * mm, "end": v(-90.4, -19.06) * mm});
            skArc(sketch, "E1599", {"start": v(-90.4, -19.06) * mm, "mid": v(-90.4, -18.86) * mm, "end": v(-90.42, -18.66) * mm});
            skArc(sketch, "E1600", {"start": v(-90.42, -18.66) * mm, "mid": v(-90.44, -18.53) * mm, "end": v(-90.48, -18.4) * mm});
            skArc(sketch, "E1601", {"start": v(-90.48, -18.4) * mm, "mid": v(-90.52, -18.34) * mm, "end": v(-90.58, -18.32) * mm});
            skArc(sketch, "E1602", {"start": v(-90.58, -18.32) * mm, "mid": v(-90.67, -18.33) * mm, "end": v(-90.74, -18.37) * mm});
            skArc(sketch, "E1603", {"start": v(-90.74, -18.37) * mm, "mid": v(-90.94, -18.5) * mm, "end": v(-91.13, -18.64) * mm});
            skArc(sketch, "E1604", {"start": v(-91.13, -18.64) * mm, "mid": v(-91.36, -18.82) * mm, "end": v(-91.58, -19) * mm});
            skArc(sketch, "E1605", {"start": v(-91.58, -19) * mm, "mid": v(-91.83, -19.2) * mm, "end": v(-92.07, -19.42) * mm});
            skArc(sketch, "E1606", {"start": v(-92.07, -19.42) * mm, "mid": v(-92.57, -19.86) * mm, "end": v(-93.11, -20.25) * mm});
            skArc(sketch, "E1607", {"start": v(-93.11, -20.25) * mm, "mid": v(-93.86, -20.74) * mm, "end": v(-94.62, -21.2) * mm});
            skArc(sketch, "E1608", {"start": v(-94.62, -21.2) * mm, "mid": v(-95.41, -21.66) * mm, "end": v(-96.22, -22.1) * mm});
            skArc(sketch, "E1609", {"start": v(-96.22, -22.1) * mm, "mid": v(-96.9, -22.42) * mm, "end": v(-97.6, -22.7) * mm});
            skLineSegment(sketch, "E1610", {"start": v(-97.6, -22.7) * mm, "end": v(-98.3, -22.97) * mm});
            skLineSegment(sketch, "E1611", {"start": v(-98.3, -22.97) * mm, "end": v(-97.89, -21.47) * mm});
            skArc(sketch, "E1612", {"start": v(-97.89, -21.47) * mm, "mid": v(-97.81, -21.18) * mm, "end": v(-97.74, -20.89) * mm});
            skArc(sketch, "E1613", {"start": v(-97.74, -20.89) * mm, "mid": v(-97.69, -20.63) * mm, "end": v(-97.65, -20.36) * mm});
            skArc(sketch, "E1614", {"start": v(-97.65, -20.36) * mm, "mid": v(-97.62, -20.15) * mm, "end": v(-97.6, -19.94) * mm});
            skArc(sketch, "E1615", {"start": v(-97.6, -19.94) * mm, "mid": v(-97.6, -19.86) * mm, "end": v(-97.65, -19.8) * mm});
            skArc(sketch, "E1616", {"start": v(-97.65, -19.8) * mm, "mid": v(-97.7, -19.77) * mm, "end": v(-97.78, -19.78) * mm});
            skArc(sketch, "E1617", {"start": v(-97.78, -19.78) * mm, "mid": v(-97.95, -19.86) * mm, "end": v(-98.12, -19.96) * mm});
            skArc(sketch, "E1618", {"start": v(-98.12, -19.96) * mm, "mid": v(-98.34, -20.09) * mm, "end": v(-98.54, -20.23) * mm});
            skArc(sketch, "E1619", {"start": v(-98.54, -20.23) * mm, "mid": v(-98.78, -20.4) * mm, "end": v(-99, -20.59) * mm});
            skArc(sketch, "E1620", {"start": v(-99, -20.59) * mm, "mid": v(-99.53, -21) * mm, "end": v(-100.08, -21.36) * mm});
            skArc(sketch, "E1621", {"start": v(-100.08, -21.36) * mm, "mid": v(-100.87, -21.83) * mm, "end": v(-101.67, -22.29) * mm});
            skArc(sketch, "E1622", {"start": v(-101.67, -22.29) * mm, "mid": v(-102.47, -22.72) * mm, "end": v(-103.28, -23.15) * mm});
            skArc(sketch, "E1623", {"start": v(-103.28, -23.15) * mm, "mid": v(-103.57, -23.26) * mm, "end": v(-103.89, -23.3) * mm});
            skArc(sketch, "E1624", {"start": v(-103.89, -23.3) * mm, "mid": v(-103.95, -23.28) * mm, "end": v(-103.98, -23.23) * mm});
            skArc(sketch, "E1625", {"start": v(-103.98, -23.23) * mm, "mid": v(-104, -23.1) * mm, "end": v(-104.03, -22.97) * mm});
            skArc(sketch, "E1626", {"start": v(-104.03, -22.97) * mm, "mid": v(-104.04, -22.8) * mm, "end": v(-104.04, -22.61) * mm});
            skArc(sketch, "E1627", {"start": v(-104.04, -22.61) * mm, "mid": v(-104.02, -22.4) * mm, "end": v(-104, -22.19) * mm});
            skArc(sketch, "E1628", {"start": v(-104, -22.19) * mm, "mid": v(-103.97, -21.97) * mm, "end": v(-103.96, -21.75) * mm});
            skArc(sketch, "E1629", {"start": v(-103.96, -21.75) * mm, "mid": v(-103.96, -21.58) * mm, "end": v(-103.97, -21.4) * mm});
            skArc(sketch, "E1630", {"start": v(-103.97, -21.4) * mm, "mid": v(-103.99, -21.27) * mm, "end": v(-104.02, -21.15) * mm});
            skArc(sketch, "E1631", {"start": v(-104.02, -21.15) * mm, "mid": v(-104.06, -21.1) * mm, "end": v(-104.12, -21.08) * mm});
            skArc(sketch, "E1632", {"start": v(-104.12, -21.08) * mm, "mid": v(-104.2, -21.1) * mm, "end": v(-104.28, -21.13) * mm});
            skArc(sketch, "E1633", {"start": v(-104.28, -21.13) * mm, "mid": v(-104.46, -21.26) * mm, "end": v(-104.64, -21.4) * mm});
            skArc(sketch, "E1634", {"start": v(-104.64, -21.4) * mm, "mid": v(-104.86, -21.57) * mm, "end": v(-105.07, -21.75) * mm});
            skArc(sketch, "E1635", {"start": v(-105.07, -21.75) * mm, "mid": v(-105.3, -21.95) * mm, "end": v(-105.52, -22.16) * mm});
            skArc(sketch, "E1636", {"start": v(-105.52, -22.16) * mm, "mid": v(-105.98, -22.55) * mm, "end": v(-106.48, -22.9) * mm});
            skArc(sketch, "E1637", {"start": v(-106.48, -22.9) * mm, "mid": v(-107.15, -23.26) * mm, "end": v(-107.83, -23.6) * mm});
            skArc(sketch, "E1638", {"start": v(-107.83, -23.6) * mm, "mid": v(-108.49, -23.89) * mm, "end": v(-109.16, -24.14) * mm});
            skArc(sketch, "E1639", {"start": v(-109.16, -24.14) * mm, "mid": v(-109.41, -24.16) * mm, "end": v(-109.63, -24.04) * mm});
            skArc(sketch, "E1640", {"start": v(-109.63, -24.04) * mm, "mid": v(-109.66, -24) * mm, "end": v(-109.67, -23.95) * mm});
            skArc(sketch, "E1641", {"start": v(-109.67, -23.95) * mm, "mid": v(-109.66, -23.86) * mm, "end": v(-109.64, -23.77) * mm});
            skArc(sketch, "E1642", {"start": v(-109.64, -23.77) * mm, "mid": v(-109.62, -23.67) * mm, "end": v(-109.58, -23.56) * mm});
            skArc(sketch, "E1643", {"start": v(-109.58, -23.56) * mm, "mid": v(-109.53, -23.45) * mm, "end": v(-109.48, -23.34) * mm});
            skArc(sketch, "E1644", {"start": v(-109.48, -23.34) * mm, "mid": v(-109.3, -22.96) * mm, "end": v(-109.16, -22.56) * mm});
            skArc(sketch, "E1645", {"start": v(-109.16, -22.56) * mm, "mid": v(-109.14, -22.3) * mm, "end": v(-109.22, -22.05) * mm});
            skArc(sketch, "E1646", {"start": v(-109.22, -22.05) * mm, "mid": v(-109.39, -21.85) * mm, "end": v(-109.62, -21.71) * mm});
            skArc(sketch, "E1647", {"start": v(-109.62, -21.71) * mm, "mid": v(-110.05, -21.6) * mm, "end": v(-110.5, -21.5) * mm});
            skArc(sketch, "E1648", {"start": v(-110.5, -21.5) * mm, "mid": v(-111.07, -21.4) * mm, "end": v(-111.63, -21.26) * mm});
            skArc(sketch, "E1649", {"start": v(-111.63, -21.26) * mm, "mid": v(-112.24, -21.07) * mm, "end": v(-112.83, -20.85) * mm});
            skArc(sketch, "E1650", {"start": v(-112.83, -20.85) * mm, "mid": v(-113.35, -20.63) * mm, "end": v(-113.86, -20.38) * mm});
            skArc(sketch, "E1651", {"start": v(-113.86, -20.38) * mm, "mid": v(-114.1, -20.2) * mm, "end": v(-114.3, -19.98) * mm});
            skArc(sketch, "E1652", {"start": v(-114.3, -19.98) * mm, "mid": v(-114.34, -19.8) * mm, "end": v(-114.3, -19.63) * mm});
            skArc(sketch, "E1653", {"start": v(-114.3, -19.63) * mm, "mid": v(-114.16, -19.47) * mm, "end": v(-113.98, -19.36) * mm});
            skArc(sketch, "E1654", {"start": v(-113.98, -19.36) * mm, "mid": v(-113.6, -19.26) * mm, "end": v(-113.23, -19.2) * mm});
            skArc(sketch, "E1655", {"start": v(-113.23, -19.2) * mm, "mid": v(-112.63, -19.16) * mm, "end": v(-112.03, -19.15) * mm});
            skArc(sketch, "E1656", {"start": v(-112.03, -19.15) * mm, "mid": v(-111.47, -19.14) * mm, "end": v(-110.92, -19.1) * mm});
            skArc(sketch, "E1657", {"start": v(-110.92, -19.1) * mm, "mid": v(-110.6, -19.03) * mm, "end": v(-110.28, -18.9) * mm});
            skArc(sketch, "E1658", {"start": v(-110.28, -18.9) * mm, "mid": v(-110.15, -18.79) * mm, "end": v(-110.1, -18.61) * mm});
            skArc(sketch, "E1659", {"start": v(-110.1, -18.61) * mm, "mid": v(-110.14, -18.4) * mm, "end": v(-110.25, -18.24) * mm});
            skArc(sketch, "E1660", {"start": v(-110.25, -18.24) * mm, "mid": v(-110.42, -18.05) * mm, "end": v(-110.56, -17.83) * mm});
            skArc(sketch, "E1661", {"start": v(-110.56, -17.83) * mm, "mid": v(-110.6, -17.68) * mm, "end": v(-110.56, -17.53) * mm});
            skArc(sketch, "E1662", {"start": v(-110.56, -17.53) * mm, "mid": v(-110.46, -17.43) * mm, "end": v(-110.32, -17.4) * mm});
            skArc(sketch, "E1663", {"start": v(-110.32, -17.4) * mm, "mid": v(-110.08, -17.43) * mm, "end": v(-109.85, -17.5) * mm});
            skArc(sketch, "E1664", {"start": v(-109.85, -17.5) * mm, "mid": v(-109.52, -17.6) * mm, "end": v(-109.17, -17.67) * mm});
            skArc(sketch, "E1665", {"start": v(-109.17, -17.67) * mm, "mid": v(-108.74, -17.73) * mm, "end": v(-108.31, -17.76) * mm});
            skArc(sketch, "E1666", {"start": v(-108.31, -17.76) * mm, "mid": v(-107.9, -17.76) * mm, "end": v(-107.5, -17.75) * mm});
            skArc(sketch, "E1667", {"start": v(-107.5, -17.75) * mm, "mid": v(-107.32, -17.7) * mm, "end": v(-107.17, -17.6) * mm});
            skArc(sketch, "E1668", {"start": v(-107.17, -17.6) * mm, "mid": v(-107.14, -17.55) * mm, "end": v(-107.14, -17.49) * mm});
            skArc(sketch, "E1669", {"start": v(-107.14, -17.49) * mm, "mid": v(-107.17, -17.36) * mm, "end": v(-107.2, -17.23) * mm});
            skArc(sketch, "E1670", {"start": v(-107.2, -17.23) * mm, "mid": v(-107.27, -17.07) * mm, "end": v(-107.34, -16.9) * mm});
            skArc(sketch, "E1671", {"start": v(-107.34, -16.9) * mm, "mid": v(-107.44, -16.73) * mm, "end": v(-107.54, -16.56) * mm});
            skArc(sketch, "E1672", {"start": v(-107.54, -16.56) * mm, "mid": v(-107.67, -16.32) * mm, "end": v(-107.78, -16.06) * mm});
            skArc(sketch, "E1673", {"start": v(-107.78, -16.06) * mm, "mid": v(-107.87, -15.78) * mm, "end": v(-107.94, -15.49) * mm});
            skArc(sketch, "E1674", {"start": v(-107.94, -15.49) * mm, "mid": v(-108, -15.15) * mm, "end": v(-108.04, -14.8) * mm});
            skArc(sketch, "E1675", {"start": v(-108.04, -14.8) * mm, "mid": v(-108.06, -14.38) * mm, "end": v(-108.07, -13.96) * mm});
            skArc(sketch, "E1676", {"start": v(-108.07, -13.96) * mm, "mid": v(-108.07, -13.47) * mm, "end": v(-108.09, -12.97) * mm});
            skArc(sketch, "E1677", {"start": v(-108.09, -12.97) * mm, "mid": v(-108.1, -12.75) * mm, "end": v(-108.16, -12.53) * mm});
            skArc(sketch, "E1678", {"start": v(-108.16, -12.53) * mm, "mid": v(-108.22, -12.4) * mm, "end": v(-108.32, -12.31) * mm});
            skArc(sketch, "E1679", {"start": v(-108.32, -12.31) * mm, "mid": v(-108.46, -12.25) * mm, "end": v(-108.6, -12.23) * mm});
            skArc(sketch, "E1680", {"start": v(-108.6, -12.23) * mm, "mid": v(-108.83, -12.22) * mm, "end": v(-109.05, -12.17) * mm});
            skArc(sketch, "E1681", {"start": v(-109.05, -12.17) * mm, "mid": v(-109.19, -12.1) * mm, "end": v(-109.28, -11.97) * mm});
            skArc(sketch, "E1682", {"start": v(-109.28, -11.97) * mm, "mid": v(-109.31, -11.83) * mm, "end": v(-109.27, -11.7) * mm});
            skArc(sketch, "E1683", {"start": v(-109.27, -11.7) * mm, "mid": v(-109.16, -11.53) * mm, "end": v(-109.02, -11.39) * mm});
            skArc(sketch, "E1684", {"start": v(-109.02, -11.39) * mm, "mid": v(-108.92, -11.3) * mm, "end": v(-108.83, -11.19) * mm});
            skArc(sketch, "E1685", {"start": v(-108.83, -11.19) * mm, "mid": v(-108.71, -11.03) * mm, "end": v(-108.6, -10.87) * mm});
            skArc(sketch, "E1686", {"start": v(-108.6, -10.87) * mm, "mid": v(-108.5, -10.68) * mm, "end": v(-108.39, -10.5) * mm});
            skArc(sketch, "E1687", {"start": v(-108.39, -10.5) * mm, "mid": v(-108.3, -10.3) * mm, "end": v(-108.2, -10.11) * mm});
            skArc(sketch, "E1688", {"start": v(-108.2, -10.11) * mm, "mid": v(-108.12, -9.93) * mm, "end": v(-108.03, -9.76) * mm});
            skArc(sketch, "E1689", {"start": v(-108.03, -9.76) * mm, "mid": v(-107.93, -9.6) * mm, "end": v(-107.81, -9.46) * mm});
            skArc(sketch, "E1690", {"start": v(-107.81, -9.46) * mm, "mid": v(-107.7, -9.35) * mm, "end": v(-107.59, -9.26) * mm});
            skArc(sketch, "E1691", {"start": v(-107.59, -9.26) * mm, "mid": v(-107.5, -9.2) * mm, "end": v(-107.4, -9.2) * mm});
            skArc(sketch, "E1692", {"start": v(-107.4, -9.2) * mm, "mid": v(-107.18, -9.24) * mm, "end": v(-106.98, -9.36) * mm});
            skArc(sketch, "E1693", {"start": v(-106.98, -9.36) * mm, "mid": v(-106.74, -9.62) * mm, "end": v(-106.53, -9.9) * mm});
            skArc(sketch, "E1694", {"start": v(-106.53, -9.9) * mm, "mid": v(-106.31, -10.26) * mm, "end": v(-106.13, -10.64) * mm});
            skArc(sketch, "E1695", {"start": v(-106.13, -10.64) * mm, "mid": v(-105.99, -11.04) * mm, "end": v(-105.88, -11.46) * mm});
            skArc(sketch, "E1696", {"start": v(-105.88, -11.46) * mm, "mid": v(-105.79, -11.84) * mm, "end": v(-105.66, -12.2) * mm});
            skArc(sketch, "E1697", {"start": v(-105.66, -12.2) * mm, "mid": v(-105.54, -12.35) * mm, "end": v(-105.36, -12.38) * mm});
            skArc(sketch, "E1698", {"start": v(-105.36, -12.38) * mm, "mid": v(-105.17, -12.31) * mm, "end": v(-105.03, -12.15) * mm});
            skArc(sketch, "E1699", {"start": v(-105.03, -12.15) * mm, "mid": v(-104.83, -11.74) * mm, "end": v(-104.65, -11.32) * mm});
            skArc(sketch, "E1700", {"start": v(-104.65, -11.32) * mm, "mid": v(-104.4, -10.75) * mm, "end": v(-104.09, -10.2) * mm});
            skArc(sketch, "E1701", {"start": v(-104.09, -10.2) * mm, "mid": v(-103.77, -9.79) * mm, "end": v(-103.39, -9.42) * mm});
            skArc(sketch, "E1702", {"start": v(-103.39, -9.42) * mm, "mid": v(-102.92, -9.1) * mm, "end": v(-102.4, -8.85) * mm});
            skArc(sketch, "E1703", {"start": v(-102.4, -8.85) * mm, "mid": v(-101.7, -8.6) * mm, "end": v(-100.97, -8.38) * mm});
            skArc(sketch, "E1704", {"start": v(-100.97, -8.38) * mm, "mid": v(-100.57, -8.28) * mm, "end": v(-100.18, -8.16) * mm});
            skArc(sketch, "E1705", {"start": v(-100.18, -8.16) * mm, "mid": v(-99.79, -8.03) * mm, "end": v(-99.4, -7.9) * mm});
            skArc(sketch, "E1706", {"start": v(-99.4, -7.9) * mm, "mid": v(-99.06, -7.76) * mm, "end": v(-98.72, -7.63) * mm});
            skArc(sketch, "E1707", {"start": v(-98.72, -7.63) * mm, "mid": v(-98.5, -7.52) * mm, "end": v(-98.3, -7.4) * mm});
            skArc(sketch, "E1708", {"start": v(-98.3, -7.4) * mm, "mid": v(-98.07, -7.33) * mm, "end": v(-97.83, -7.4) * mm});
            skArc(sketch, "E1709", {"start": v(-97.83, -7.4) * mm, "mid": v(-97.69, -7.59) * mm, "end": v(-97.7, -7.82) * mm});
            skArc(sketch, "E1710", {"start": v(-97.7, -7.82) * mm, "mid": v(-97.94, -8.36) * mm, "end": v(-98.28, -8.86) * mm});
            skArc(sketch, "E1711", {"start": v(-98.28, -8.86) * mm, "mid": v(-98.72, -9.37) * mm, "end": v(-99.21, -9.83) * mm});
            skArc(sketch, "E1712", {"start": v(-99.21, -9.83) * mm, "mid": v(-99.52, -10.1) * mm, "end": v(-99.8, -10.39) * mm});
            skArc(sketch, "E1713", {"start": v(-99.8, -10.39) * mm, "mid": v(-99.94, -10.57) * mm, "end": v(-100.02, -10.79) * mm});
            skArc(sketch, "E1714", {"start": v(-100.02, -10.79) * mm, "mid": v(-100, -10.93) * mm, "end": v(-99.9, -11.03) * mm});
            skArc(sketch, "E1715", {"start": v(-99.9, -11.03) * mm, "mid": v(-99.7, -11.1) * mm, "end": v(-99.5, -11.13) * mm});
            skArc(sketch, "E1716", {"start": v(-99.5, -11.13) * mm, "mid": v(-99.35, -11.14) * mm, "end": v(-99.21, -11.16) * mm});
            skArc(sketch, "E1717", {"start": v(-99.21, -11.16) * mm, "mid": v(-99.13, -11.2) * mm, "end": v(-99.08, -11.26) * mm});
            skArc(sketch, "E1718", {"start": v(-99.08, -11.26) * mm, "mid": v(-99.04, -11.36) * mm, "end": v(-99.04, -11.45) * mm});
            skArc(sketch, "E1719", {"start": v(-99.04, -11.45) * mm, "mid": v(-99.07, -11.64) * mm, "end": v(-99.1, -11.82) * mm});
            skArc(sketch, "E1720", {"start": v(-99.1, -11.82) * mm, "mid": v(-99.14, -12.08) * mm, "end": v(-99.1, -12.34) * mm});
            skArc(sketch, "E1721", {"start": v(-99.1, -12.34) * mm, "mid": v(-99.01, -12.48) * mm, "end": v(-98.84, -12.5) * mm});
            skArc(sketch, "E1722", {"start": v(-98.84, -12.5) * mm, "mid": v(-98.57, -12.4) * mm, "end": v(-98.34, -12.24) * mm});
            skArc(sketch, "E1723", {"start": v(-98.34, -12.24) * mm, "mid": v(-98.02, -11.9) * mm, "end": v(-97.72, -11.54) * mm});
            skArc(sketch, "E1724", {"start": v(-97.72, -11.54) * mm, "mid": v(-97.42, -11.16) * mm, "end": v(-97.1, -10.79) * mm});
            skArc(sketch, "E1725", {"start": v(-97.1, -10.79) * mm, "mid": v(-96.94, -10.67) * mm, "end": v(-96.74, -10.62) * mm});
            skArc(sketch, "E1726", {"start": v(-96.74, -10.62) * mm, "mid": v(-96.6, -10.68) * mm, "end": v(-96.52, -10.81) * mm});
            skArc(sketch, "E1727", {"start": v(-96.52, -10.81) * mm, "mid": v(-96.47, -11.17) * mm, "end": v(-96.46, -11.52) * mm});
            skArc(sketch, "E1728", {"start": v(-96.46, -11.52) * mm, "mid": v(-96.45, -11.75) * mm, "end": v(-96.43, -11.97) * mm});
            skArc(sketch, "E1729", {"start": v(-96.43, -11.97) * mm, "mid": v(-96.4, -12.13) * mm, "end": v(-96.35, -12.27) * mm});
            skArc(sketch, "E1730", {"start": v(-96.35, -12.27) * mm, "mid": v(-96.28, -12.38) * mm, "end": v(-96.2, -12.46) * mm});
            skArc(sketch, "E1731", {"start": v(-96.2, -12.46) * mm, "mid": v(-96.1, -12.53) * mm, "end": v(-95.98, -12.56) * mm});
            skArc(sketch, "E1732", {"start": v(-95.98, -12.56) * mm, "mid": v(-95.9, -12.6) * mm, "end": v(-95.86, -12.67) * mm});
            skArc(sketch, "E1733", {"start": v(-95.86, -12.67) * mm, "mid": v(-95.85, -12.76) * mm, "end": v(-95.9, -12.84) * mm});
            skArc(sketch, "E1734", {"start": v(-95.9, -12.84) * mm, "mid": v(-96.03, -13) * mm, "end": v(-96.18, -13.13) * mm});
            skArc(sketch, "E1735", {"start": v(-96.18, -13.13) * mm, "mid": v(-96.49, -13.36) * mm, "end": v(-96.8, -13.6) * mm});
            skArc(sketch, "E1736", {"start": v(-96.8, -13.6) * mm, "mid": v(-97.04, -13.78) * mm, "end": v(-97.28, -13.97) * mm});
            skArc(sketch, "E1737", {"start": v(-97.28, -13.97) * mm, "mid": v(-97.48, -14.15) * mm, "end": v(-97.67, -14.33) * mm});
            skArc(sketch, "E1738", {"start": v(-97.67, -14.33) * mm, "mid": v(-97.8, -14.48) * mm, "end": v(-97.93, -14.64) * mm});
            skArc(sketch, "E1739", {"start": v(-97.93, -14.64) * mm, "mid": v(-97.95, -14.72) * mm, "end": v(-97.93, -14.8) * mm});
            skArc(sketch, "E1740", {"start": v(-97.93, -14.8) * mm, "mid": v(-97.76, -14.96) * mm, "end": v(-97.54, -15) * mm});
            skArc(sketch, "E1741", {"start": v(-97.54, -15) * mm, "mid": v(-96.84, -14.97) * mm, "end": v(-96.15, -14.9) * mm});
            skArc(sketch, "E1742", {"start": v(-96.15, -14.9) * mm, "mid": v(-95.38, -14.8) * mm, "end": v(-94.61, -14.66) * mm});
            skArc(sketch, "E1743", {"start": v(-94.61, -14.66) * mm, "mid": v(-93.9, -14.5) * mm, "end": v(-93.2, -14.29) * mm});
            skArc(sketch, "E1744", {"start": v(-93.2, -14.29) * mm, "mid": v(-92.76, -14.13) * mm, "end": v(-92.32, -13.93) * mm});
            skArc(sketch, "E1745", {"start": v(-92.32, -13.93) * mm, "mid": v(-92.07, -13.78) * mm, "end": v(-91.86, -13.57) * mm});
            skArc(sketch, "E1746", {"start": v(-91.86, -13.57) * mm, "mid": v(-91.8, -13.4) * mm, "end": v(-91.81, -13.22) * mm});
            skArc(sketch, "E1747", {"start": v(-91.81, -13.22) * mm, "mid": v(-91.93, -13.02) * mm, "end": v(-92.1, -12.87) * mm});
            skArc(sketch, "E1748", {"start": v(-92.1, -12.87) * mm, "mid": v(-92.32, -12.71) * mm, "end": v(-92.52, -12.53) * mm});
            skArc(sketch, "E1749", {"start": v(-92.52, -12.53) * mm, "mid": v(-92.74, -12.28) * mm, "end": v(-92.95, -12.02) * mm});
            skArc(sketch, "E1750", {"start": v(-92.95, -12.02) * mm, "mid": v(-93.14, -11.75) * mm, "end": v(-93.31, -11.46) * mm});
            skArc(sketch, "E1751", {"start": v(-93.31, -11.46) * mm, "mid": v(-93.44, -11.2) * mm, "end": v(-93.53, -10.95) * mm});
            skLineSegment(sketch, "E1752", {"start": v(-93.53, -10.95) * mm, "end": v(-93.71, -10.35) * mm});
            skLineSegment(sketch, "E1753", {"start": v(-93.71, -10.35) * mm, "end": v(-92.04, -10.87) * mm});
            skArc(sketch, "E1754", {"start": v(-92.04, -10.87) * mm, "mid": v(-91.66, -10.98) * mm, "end": v(-91.27, -11.08) * mm});
            skArc(sketch, "E1755", {"start": v(-91.27, -11.08) * mm, "mid": v(-90.8, -11.2) * mm, "end": v(-90.33, -11.3) * mm});
            skArc(sketch, "E1756", {"start": v(-90.33, -11.3) * mm, "mid": v(-89.84, -11.38) * mm, "end": v(-89.36, -11.47) * mm});
            skArc(sketch, "E1757", {"start": v(-89.36, -11.47) * mm, "mid": v(-88.95, -11.53) * mm, "end": v(-88.54, -11.58) * mm});
            skLineSegment(sketch, "E1758", {"start": v(-88.54, -11.58) * mm, "end": v(-86.7, -11.77) * mm});
            skLineSegment(sketch, "E1759", {"start": v(-86.7, -11.77) * mm, "end": v(-86.88, -11.03) * mm});
            skArc(sketch, "E1760", {"start": v(-86.88, -11.03) * mm, "mid": v(-86.92, -10.87) * mm, "end": v(-86.96, -10.7) * mm});
            skArc(sketch, "E1761", {"start": v(-86.96, -10.7) * mm, "mid": v(-87, -10.5) * mm, "end": v(-87.06, -10.3) * mm});
            skArc(sketch, "E1762", {"start": v(-87.06, -10.3) * mm, "mid": v(-87.1, -10.1) * mm, "end": v(-87.15, -9.9) * mm});
            skArc(sketch, "E1763", {"start": v(-87.15, -9.9) * mm, "mid": v(-87.2, -9.74) * mm, "end": v(-87.23, -9.57) * mm});
            skArc(sketch, "E1764", {"start": v(-87.23, -9.57) * mm, "mid": v(-87.28, -9.35) * mm, "end": v(-87.32, -9.12) * mm});
            skArc(sketch, "E1765", {"start": v(-87.32, -9.12) * mm, "mid": v(-87.31, -9.04) * mm, "end": v(-87.26, -8.97) * mm});
            skArc(sketch, "E1766", {"start": v(-87.26, -8.97) * mm, "mid": v(-87.17, -8.93) * mm, "end": v(-87.07, -8.92) * mm});
            skArc(sketch, "E1767", {"start": v(-87.07, -8.92) * mm, "mid": v(-86.77, -8.97) * mm, "end": v(-86.47, -9.02) * mm});
            skArc(sketch, "E1768", {"start": v(-86.47, -9.02) * mm, "mid": v(-86.22, -9.07) * mm, "end": v(-85.97, -9.1) * mm});
            skArc(sketch, "E1769", {"start": v(-85.97, -9.1) * mm, "mid": v(-85.58, -9.15) * mm, "end": v(-85.18, -9.2) * mm});
            skArc(sketch, "E1770", {"start": v(-85.18, -9.2) * mm, "mid": v(-84.73, -9.25) * mm, "end": v(-84.28, -9.3) * mm});
            skArc(sketch, "E1771", {"start": v(-84.28, -9.3) * mm, "mid": v(-83.84, -9.34) * mm, "end": v(-83.4, -9.37) * mm});
            skLineSegment(sketch, "E1772", {"start": v(-83.4, -9.37) * mm, "end": v(-81.25, -9.54) * mm});
            skLineSegment(sketch, "E1773", {"start": v(-81.25, -9.54) * mm, "end": v(-81.25, -8.12) * mm});
            skArc(sketch, "E1774", {"start": v(-81.25, -8.12) * mm, "mid": v(-81.25, -7.68) * mm, "end": v(-81.23, -7.25) * mm});
            skArc(sketch, "E1775", {"start": v(-81.23, -7.25) * mm, "mid": v(-81.2, -7.07) * mm, "end": v(-81.15, -6.91) * mm});
            skArc(sketch, "E1776", {"start": v(-81.15, -6.91) * mm, "mid": v(-81.06, -6.8) * mm, "end": v(-80.95, -6.75) * mm});
            skArc(sketch, "E1777", {"start": v(-80.95, -6.75) * mm, "mid": v(-80.74, -6.72) * mm, "end": v(-80.53, -6.7) * mm});
            skArc(sketch, "E1778", {"start": v(-80.53, -6.7) * mm, "mid": v(-80.32, -6.7) * mm, "end": v(-80.1, -6.66) * mm});
            skArc(sketch, "E1779", {"start": v(-80.1, -6.66) * mm, "mid": v(-80, -6.62) * mm, "end": v(-79.94, -6.52) * mm});
            skArc(sketch, "E1780", {"start": v(-79.94, -6.52) * mm, "mid": v(-79.9, -6.38) * mm, "end": v(-79.9, -6.23) * mm});
            skArc(sketch, "E1781", {"start": v(-79.9, -6.23) * mm, "mid": v(-79.94, -5.8) * mm, "end": v(-80, -5.37) * mm});
            skArc(sketch, "E1782", {"start": v(-80, -5.37) * mm, "mid": v(-80.04, -5.04) * mm, "end": v(-80.07, -4.7) * mm});
            skArc(sketch, "E1783", {"start": v(-80.07, -4.7) * mm, "mid": v(-80.07, -4.48) * mm, "end": v(-80.05, -4.25) * mm});
            skArc(sketch, "E1784", {"start": v(-80.05, -4.25) * mm, "mid": v(-80.02, -4.1) * mm, "end": v(-79.96, -3.94) * mm});
            skArc(sketch, "E1785", {"start": v(-79.96, -3.94) * mm, "mid": v(-79.88, -3.8) * mm, "end": v(-79.77, -3.7) * mm});
            skArc(sketch, "E1786", {"start": v(-79.77, -3.7) * mm, "mid": v(-79.6, -3.6) * mm, "end": v(-79.42, -3.56) * mm});
            skArc(sketch, "E1787", {"start": v(-79.42, -3.56) * mm, "mid": v(-79.27, -3.6) * mm, "end": v(-79.17, -3.7) * mm});
            skArc(sketch, "E1788", {"start": v(-79.17, -3.7) * mm, "mid": v(-79.09, -3.97) * mm, "end": v(-79.05, -4.25) * mm});
            skArc(sketch, "E1789", {"start": v(-79.05, -4.25) * mm, "mid": v(-79.06, -4.75) * mm, "end": v(-79.08, -5.26) * mm});
            skArc(sketch, "E1790", {"start": v(-79.08, -5.26) * mm, "mid": v(-79.1, -5.64) * mm, "end": v(-79.1, -6.02) * mm});
            skArc(sketch, "E1791", {"start": v(-79.1, -6.02) * mm, "mid": v(-79.1, -6.2) * mm, "end": v(-79.05, -6.37) * mm});
            skArc(sketch, "E1792", {"start": v(-79.05, -6.37) * mm, "mid": v(-78.98, -6.47) * mm, "end": v(-78.88, -6.55) * mm});
            skArc(sketch, "E1793", {"start": v(-78.88, -6.55) * mm, "mid": v(-78.71, -6.62) * mm, "end": v(-78.55, -6.65) * mm});
            skArc(sketch, "E1794", {"start": v(-78.55, -6.65) * mm, "mid": v(-78.38, -6.7) * mm, "end": v(-78.23, -6.75) * mm});
            skArc(sketch, "E1795", {"start": v(-78.23, -6.75) * mm, "mid": v(-78.12, -6.83) * mm, "end": v(-78.04, -6.93) * mm});
            skArc(sketch, "E1796", {"start": v(-78.04, -6.93) * mm, "mid": v(-77.98, -7.09) * mm, "end": v(-77.96, -7.25) * mm});
            skArc(sketch, "E1797", {"start": v(-77.96, -7.25) * mm, "mid": v(-77.94, -7.55) * mm, "end": v(-77.93, -7.85) * mm});
            skArc(sketch, "E1798", {"start": v(-77.93, -7.85) * mm, "mid": v(-77.93, -8.21) * mm, "end": v(-77.92, -8.57) * mm});
            skArc(sketch, "E1799", {"start": v(-77.92, -8.57) * mm, "mid": v(-77.89, -8.7) * mm, "end": v(-77.82, -8.8) * mm});
            skArc(sketch, "E1800", {"start": v(-77.82, -8.8) * mm, "mid": v(-77.72, -8.86) * mm, "end": v(-77.61, -8.87) * mm});
            skArc(sketch, "E1801", {"start": v(-77.61, -8.87) * mm, "mid": v(-77.32, -8.82) * mm, "end": v(-77.03, -8.77) * mm});
            skArc(sketch, "E1802", {"start": v(-77.03, -8.77) * mm, "mid": v(-76.48, -8.63) * mm, "end": v(-75.94, -8.46) * mm});
            skArc(sketch, "E1803", {"start": v(-75.94, -8.46) * mm, "mid": v(-75.33, -8.23) * mm, "end": v(-74.73, -7.97) * mm});
            skArc(sketch, "E1804", {"start": v(-74.73, -7.97) * mm, "mid": v(-74.19, -7.7) * mm, "end": v(-73.66, -7.43) * mm});
            skArc(sketch, "E1805", {"start": v(-73.66, -7.43) * mm, "mid": v(-73.35, -7.21) * mm, "end": v(-73.07, -6.96) * mm});
            skArc(sketch, "E1806", {"start": v(-73.07, -6.96) * mm, "mid": v(-72.94, -6.8) * mm, "end": v(-72.8, -6.63) * mm});
            skArc(sketch, "E1807", {"start": v(-72.8, -6.63) * mm, "mid": v(-72.77, -6.53) * mm, "end": v(-72.77, -6.42) * mm});
            skArc(sketch, "E1808", {"start": v(-72.77, -6.42) * mm, "mid": v(-72.82, -6.31) * mm, "end": v(-72.9, -6.22) * mm});
            skArc(sketch, "E1809", {"start": v(-72.9, -6.22) * mm, "mid": v(-73.12, -6.03) * mm, "end": v(-73.34, -5.85) * mm});
            skArc(sketch, "E1810", {"start": v(-73.34, -5.85) * mm, "mid": v(-73.48, -5.73) * mm, "end": v(-73.62, -5.6) * mm});
            skArc(sketch, "E1811", {"start": v(-73.62, -5.6) * mm, "mid": v(-73.74, -5.5) * mm, "end": v(-73.84, -5.37) * mm});
            skArc(sketch, "E1812", {"start": v(-73.84, -5.37) * mm, "mid": v(-73.92, -5.27) * mm, "end": v(-74, -5.16) * mm});
            skArc(sketch, "E1813", {"start": v(-74, -5.16) * mm, "mid": v(-74.01, -5.1) * mm, "end": v(-74, -5.04) * mm});
            skArc(sketch, "E1814", {"start": v(-74, -5.04) * mm, "mid": v(-73.96, -4.96) * mm, "end": v(-73.9, -4.9) * mm});
            skArc(sketch, "E1815", {"start": v(-73.9, -4.9) * mm, "mid": v(-73.55, -4.64) * mm, "end": v(-73.2, -4.39) * mm});
            skArc(sketch, "E1816", {"start": v(-73.2, -4.39) * mm, "mid": v(-72.78, -4.1) * mm, "end": v(-72.36, -3.8) * mm});
            skArc(sketch, "E1817", {"start": v(-72.36, -3.8) * mm, "mid": v(-71.87, -3.47) * mm, "end": v(-71.38, -3.14) * mm});
            skArc(sketch, "E1818", {"start": v(-71.38, -3.14) * mm, "mid": v(-70.73, -2.71) * mm, "end": v(-70.1, -2.27) * mm});
            skArc(sketch, "E1819", {"start": v(-70.1, -2.27) * mm, "mid": v(-69.63, -1.9) * mm, "end": v(-69.17, -1.52) * mm});
            skArc(sketch, "E1820", {"start": v(-69.17, -1.52) * mm, "mid": v(-68.8, -1.17) * mm, "end": v(-68.46, -0.8) * mm});
            skArc(sketch, "E1821", {"start": v(-68.46, -0.8) * mm, "mid": v(-68.15, -0.42) * mm, "end": v(-67.86, -0.01) * mm});
            skArc(sketch, "E1822", {"start": v(-67.86, -0.01) * mm, "mid": v(-67.53, 0.51) * mm, "end": v(-67.24, 1.05) * mm});
            skArc(sketch, "E1823", {"start": v(-67.24, 1.05) * mm, "mid": v(-67, 1.6) * mm, "end": v(-66.78, 2.14) * mm});
            skArc(sketch, "E1824", {"start": v(-66.78, 2.14) * mm, "mid": v(-66.65, 2.58) * mm, "end": v(-66.55, 3.02) * mm});
            skArc(sketch, "E1825", {"start": v(-66.55, 3.02) * mm, "mid": v(-66.6, 3.18) * mm, "end": v(-66.74, 3.25) * mm});
            skArc(sketch, "E1826", {"start": v(-66.74, 3.25) * mm, "mid": v(-66.8, 3.24) * mm, "end": v(-66.87, 3.2) * mm});
            skArc(sketch, "E1827", {"start": v(-66.87, 3.2) * mm, "mid": v(-67.07, 3.05) * mm, "end": v(-67.27, 2.9) * mm});
            skArc(sketch, "E1828", {"start": v(-67.27, 2.9) * mm, "mid": v(-67.5, 2.7) * mm, "end": v(-67.73, 2.5) * mm});
            skArc(sketch, "E1829", {"start": v(-67.73, 2.5) * mm, "mid": v(-67.99, 2.28) * mm, "end": v(-68.24, 2.04) * mm});
            skArc(sketch, "E1830", {"start": v(-68.24, 2.04) * mm, "mid": v(-68.5, 1.8) * mm, "end": v(-68.78, 1.56) * mm});
            skArc(sketch, "E1831", {"start": v(-68.78, 1.56) * mm, "mid": v(-69.05, 1.32) * mm, "end": v(-69.33, 1.1) * mm});
            skArc(sketch, "E1832", {"start": v(-69.33, 1.1) * mm, "mid": v(-69.58, 0.9) * mm, "end": v(-69.82, 0.71) * mm});
            skArc(sketch, "E1833", {"start": v(-69.82, 0.71) * mm, "mid": v(-69.98, 0.6) * mm, "end": v(-70.14, 0.51) * mm});
            skArc(sketch, "E1834", {"start": v(-70.14, 0.51) * mm, "mid": v(-70.32, 0.43) * mm, "end": v(-70.5, 0.36) * mm});
            skArc(sketch, "E1835", {"start": v(-70.5, 0.36) * mm, "mid": v(-70.6, 0.36) * mm, "end": v(-70.66, 0.42) * mm});
            skArc(sketch, "E1836", {"start": v(-70.66, 0.42) * mm, "mid": v(-70.71, 0.55) * mm, "end": v(-70.73, 0.69) * mm});
            skArc(sketch, "E1837", {"start": v(-70.73, 0.69) * mm, "mid": v(-70.74, 1.13) * mm, "end": v(-70.74, 1.58) * mm});
            skArc(sketch, "E1838", {"start": v(-70.74, 1.58) * mm, "mid": v(-70.75, 1.85) * mm, "end": v(-70.75, 2.11) * mm});
            skArc(sketch, "E1839", {"start": v(-70.75, 2.11) * mm, "mid": v(-70.76, 2.34) * mm, "end": v(-70.78, 2.56) * mm});
            skArc(sketch, "E1840", {"start": v(-70.78, 2.56) * mm, "mid": v(-70.8, 2.75) * mm, "end": v(-70.81, 2.93) * mm});
            skArc(sketch, "E1841", {"start": v(-70.81, 2.93) * mm, "mid": v(-70.83, 2.96) * mm, "end": v(-70.86, 2.97) * mm});
            skArc(sketch, "E1842", {"start": v(-70.86, 2.97) * mm, "mid": v(-70.9, 2.97) * mm, "end": v(-70.94, 2.94) * mm});
            skArc(sketch, "E1843", {"start": v(-70.94, 2.94) * mm, "mid": v(-71.18, 2.73) * mm, "end": v(-71.41, 2.5) * mm});
            skArc(sketch, "E1844", {"start": v(-71.41, 2.5) * mm, "mid": v(-71.69, 2.25) * mm, "end": v(-71.96, 2) * mm});
            skArc(sketch, "E1845", {"start": v(-71.96, 2) * mm, "mid": v(-72.28, 1.69) * mm, "end": v(-72.59, 1.38) * mm});
            skArc(sketch, "E1846", {"start": v(-72.59, 1.38) * mm, "mid": v(-72.94, 1.05) * mm, "end": v(-73.3, 0.73) * mm});
            skArc(sketch, "E1847", {"start": v(-73.3, 0.73) * mm, "mid": v(-73.69, 0.4) * mm, "end": v(-74.1, 0.08) * mm});
            skArc(sketch, "E1848", {"start": v(-74.1, 0.08) * mm, "mid": v(-74.47, -0.2) * mm, "end": v(-74.85, -0.48) * mm});
            skArc(sketch, "E1849", {"start": v(-74.85, -0.48) * mm, "mid": v(-75.14, -0.66) * mm, "end": v(-75.44, -0.82) * mm});
            skLineSegment(sketch, "E1850", {"start": v(-75.44, -0.82) * mm, "end": v(-76.69, -1.44) * mm});
            skLineSegment(sketch, "E1851", {"start": v(-76.69, -1.44) * mm, "end": v(-76.77, 0.08) * mm});
            skArc(sketch, "E1852", {"start": v(-76.77, 0.08) * mm, "mid": v(-76.82, 0.65) * mm, "end": v(-76.89, 1.22) * mm});
            skArc(sketch, "E1853", {"start": v(-76.89, 1.22) * mm, "mid": v(-76.98, 1.42) * mm, "end": v(-77.17, 1.53) * mm});
            skArc(sketch, "E1854", {"start": v(-77.17, 1.53) * mm, "mid": v(-77.39, 1.53) * mm, "end": v(-77.57, 1.4) * mm});
            skArc(sketch, "E1855", {"start": v(-77.57, 1.4) * mm, "mid": v(-77.94, 0.96) * mm, "end": v(-78.29, 0.49) * mm});
            skArc(sketch, "E1856", {"start": v(-78.29, 0.49) * mm, "mid": v(-78.47, 0.24) * mm, "end": v(-78.67, 0) * mm});
            skArc(sketch, "E1857", {"start": v(-78.67, 0) * mm, "mid": v(-78.92, -0.28) * mm, "end": v(-79.18, -0.56) * mm});
            skArc(sketch, "E1858", {"start": v(-79.18, -0.56) * mm, "mid": v(-79.45, -0.83) * mm, "end": v(-79.72, -1.1) * mm});
            skArc(sketch, "E1859", {"start": v(-79.72, -1.1) * mm, "mid": v(-79.97, -1.33) * mm, "end": v(-80.22, -1.54) * mm});
            skArc(sketch, "E1860", {"start": v(-80.22, -1.54) * mm, "mid": v(-80.7, -1.9) * mm, "end": v(-81.2, -2.26) * mm});
            skArc(sketch, "E1861", {"start": v(-81.2, -2.26) * mm, "mid": v(-81.82, -2.67) * mm, "end": v(-82.45, -3.08) * mm});
            skArc(sketch, "E1862", {"start": v(-82.45, -3.08) * mm, "mid": v(-83.07, -3.46) * mm, "end": v(-83.7, -3.83) * mm});
            skArc(sketch, "E1863", {"start": v(-83.7, -3.83) * mm, "mid": v(-83.88, -3.91) * mm, "end": v(-84.08, -3.94) * mm});
            skArc(sketch, "E1864", {"start": v(-84.08, -3.94) * mm, "mid": v(-84.12, -3.92) * mm, "end": v(-84.14, -3.89) * mm});
            skArc(sketch, "E1865", {"start": v(-84.14, -3.89) * mm, "mid": v(-84.16, -3.74) * mm, "end": v(-84.17, -3.6) * mm});
            skArc(sketch, "E1866", {"start": v(-84.17, -3.6) * mm, "mid": v(-84.18, -3.4) * mm, "end": v(-84.19, -3.21) * mm});
            skArc(sketch, "E1867", {"start": v(-84.19, -3.21) * mm, "mid": v(-84.18, -2.99) * mm, "end": v(-84.17, -2.76) * mm});
            skArc(sketch, "E1868", {"start": v(-84.17, -2.76) * mm, "mid": v(-84.14, -2.15) * mm, "end": v(-84.14, -1.54) * mm});
            skArc(sketch, "E1869", {"start": v(-84.14, -1.54) * mm, "mid": v(-84.19, -1.35) * mm, "end": v(-84.32, -1.21) * mm});
            skArc(sketch, "E1870", {"start": v(-84.32, -1.21) * mm, "mid": v(-84.5, -1.17) * mm, "end": v(-84.68, -1.24) * mm});
            skArc(sketch, "E1871", {"start": v(-84.68, -1.24) * mm, "mid": v(-85.11, -1.6) * mm, "end": v(-85.53, -1.97) * mm});
            skArc(sketch, "E1872", {"start": v(-85.53, -1.97) * mm, "mid": v(-86.38, -2.7) * mm, "end": v(-87.27, -3.38) * mm});
            skArc(sketch, "E1873", {"start": v(-87.27, -3.38) * mm, "mid": v(-88.15, -3.95) * mm, "end": v(-89.07, -4.46) * mm});
            skArc(sketch, "E1874", {"start": v(-89.07, -4.46) * mm, "mid": v(-90.01, -4.88) * mm, "end": v(-90.98, -5.24) * mm});
            skArc(sketch, "E1875", {"start": v(-90.98, -5.24) * mm, "mid": v(-92, -5.52) * mm, "end": v(-93.04, -5.73) * mm});
            skLineSegment(sketch, "E1876", {"start": v(-93.04, -5.73) * mm, "end": v(-94.18, -5.91) * mm});
            skLineSegment(sketch, "E1877", {"start": v(-94.18, -5.91) * mm, "end": v(-93.89, -4.64) * mm});
            skArc(sketch, "E1878", {"start": v(-93.89, -4.64) * mm, "mid": v(-93.8, -4.18) * mm, "end": v(-93.75, -3.72) * mm});
            skArc(sketch, "E1879", {"start": v(-93.75, -3.72) * mm, "mid": v(-93.77, -3.4) * mm, "end": v(-93.86, -3.1) * mm});
            skArc(sketch, "E1880", {"start": v(-93.86, -3.1) * mm, "mid": v(-93.98, -2.96) * mm, "end": v(-94.16, -2.9) * mm});
            skArc(sketch, "E1881", {"start": v(-94.16, -2.9) * mm, "mid": v(-94.38, -2.93) * mm, "end": v(-94.58, -3.04) * mm});
            skArc(sketch, "E1882", {"start": v(-94.58, -3.04) * mm, "mid": v(-95.07, -3.36) * mm, "end": v(-95.6, -3.6) * mm});
            skArc(sketch, "E1883", {"start": v(-95.6, -3.6) * mm, "mid": v(-96.41, -3.82) * mm, "end": v(-97.23, -4) * mm});
            skArc(sketch, "E1884", {"start": v(-97.23, -4) * mm, "mid": v(-98.22, -4.14) * mm, "end": v(-99.2, -4.23) * mm});
            skArc(sketch, "E1885", {"start": v(-99.2, -4.23) * mm, "mid": v(-100.3, -4.26) * mm, "end": v(-101.38, -4.25) * mm});
            skLineSegment(sketch, "E1886", {"start": v(-101.38, -4.25) * mm, "end": v(-102.3, -4.22) * mm});
            skLineSegment(sketch, "E1887", {"start": v(-102.3, -4.22) * mm, "end": v(-101.58, -3.29) * mm});
            skLineSegment(sketch, "E1888", {"start": v(-101.58, -3.29) * mm, "end": v(-100.88, -2.36) * mm});
            skLineSegment(sketch, "E1889", {"start": v(-100.88, -2.36) * mm, "end": v(-102.31, -1.42) * mm});
            skArc(sketch, "E1890", {"start": v(-102.31, -1.42) * mm, "mid": v(-102.87, -1.03) * mm, "end": v(-103.4, -0.6) * mm});
            skArc(sketch, "E1891", {"start": v(-103.4, -0.6) * mm, "mid": v(-103.93, -0.1) * mm, "end": v(-104.44, 0.42) * mm});
            skArc(sketch, "E1892", {"start": v(-104.44, 0.42) * mm, "mid": v(-104.85, 0.9) * mm, "end": v(-105.25, 1.39) * mm});
            skArc(sketch, "E1893", {"start": v(-105.25, 1.39) * mm, "mid": v(-105.3, 1.58) * mm, "end": v(-105.22, 1.77) * mm});
            skArc(sketch, "E1894", {"start": v(-105.22, 1.77) * mm, "mid": v(-105.16, 1.8) * mm, "end": v(-105.1, 1.82) * mm});
            skArc(sketch, "E1895", {"start": v(-105.1, 1.82) * mm, "mid": v(-104.92, 1.82) * mm, "end": v(-104.75, 1.8) * mm});
            skArc(sketch, "E1896", {"start": v(-104.75, 1.8) * mm, "mid": v(-104.54, 1.78) * mm, "end": v(-104.33, 1.75) * mm});
            skArc(sketch, "E1897", {"start": v(-104.33, 1.75) * mm, "mid": v(-104.1, 1.7) * mm, "end": v(-103.86, 1.64) * mm});
            skArc(sketch, "E1898", {"start": v(-103.86, 1.64) * mm, "mid": v(-103.59, 1.58) * mm, "end": v(-103.31, 1.52) * mm});
            skArc(sketch, "E1899", {"start": v(-103.31, 1.52) * mm, "mid": v(-102.98, 1.46) * mm, "end": v(-102.64, 1.4) * mm});
            skArc(sketch, "E1900", {"start": v(-102.64, 1.4) * mm, "mid": v(-102.3, 1.34) * mm, "end": v(-101.95, 1.3) * mm});
            skArc(sketch, "E1901", {"start": v(-101.95, 1.3) * mm, "mid": v(-101.66, 1.25) * mm, "end": v(-101.37, 1.22) * mm});
            skLineSegment(sketch, "E1902", {"start": v(-101.37, 1.22) * mm, "end": v(-100.05, 1.1) * mm});
            skLineSegment(sketch, "E1903", {"start": v(-100.05, 1.1) * mm, "end": v(-100.05, 4.11) * mm});
            skLineSegment(sketch, "E1904", {"start": v(-100.05, 4.11) * mm, "end": v(-100.05, 7.12) * mm});
            skLineSegment(sketch, "E1905", {"start": v(-100.05, 7.12) * mm, "end": v(-99.36, 7.12) * mm});
            skArc(sketch, "E1906", {"start": v(-99.36, 7.12) * mm, "mid": v(-99.16, 7.14) * mm, "end": v(-98.96, 7.18) * mm});
            skArc(sketch, "E1907", {"start": v(-98.96, 7.18) * mm, "mid": v(-98.85, 7.24) * mm, "end": v(-98.77, 7.35) * mm});
            skArc(sketch, "E1908", {"start": v(-98.77, 7.35) * mm, "mid": v(-98.7, 7.54) * mm, "end": v(-98.69, 7.74) * mm});
            skArc(sketch, "E1909", {"start": v(-98.69, 7.74) * mm, "mid": v(-98.67, 8.25) * mm, "end": v(-98.67, 8.76) * mm});
            skArc(sketch, "E1910", {"start": v(-98.67, 8.76) * mm, "mid": v(-98.66, 9.08) * mm, "end": v(-98.65, 9.4) * mm});
            skArc(sketch, "E1911", {"start": v(-98.65, 9.4) * mm, "mid": v(-98.63, 9.7) * mm, "end": v(-98.59, 9.97) * mm});
            skArc(sketch, "E1912", {"start": v(-98.59, 9.97) * mm, "mid": v(-98.55, 10.2) * mm, "end": v(-98.5, 10.43) * mm});
            skArc(sketch, "E1913", {"start": v(-98.5, 10.43) * mm, "mid": v(-98.46, 10.51) * mm, "end": v(-98.4, 10.58) * mm});
            skArc(sketch, "E1914", {"start": v(-98.4, 10.58) * mm, "mid": v(-98.22, 10.6) * mm, "end": v(-98.08, 10.51) * mm});
            skArc(sketch, "E1915", {"start": v(-98.08, 10.51) * mm, "mid": v(-97.92, 10.24) * mm, "end": v(-97.82, 9.95) * mm});
            skArc(sketch, "E1916", {"start": v(-97.82, 9.95) * mm, "mid": v(-97.74, 9.55) * mm, "end": v(-97.7, 9.13) * mm});
            skArc(sketch, "E1917", {"start": v(-97.7, 9.13) * mm, "mid": v(-97.73, 8.74) * mm, "end": v(-97.8, 8.35) * mm});
            skArc(sketch, "E1918", {"start": v(-97.8, 8.35) * mm, "mid": v(-97.89, 8.03) * mm, "end": v(-97.96, 7.7) * mm});
            skArc(sketch, "E1919", {"start": v(-97.96, 7.7) * mm, "mid": v(-97.96, 7.52) * mm, "end": v(-97.91, 7.36) * mm});
            skArc(sketch, "E1920", {"start": v(-97.91, 7.36) * mm, "mid": v(-97.82, 7.24) * mm, "end": v(-97.7, 7.18) * mm});
            skArc(sketch, "E1921", {"start": v(-97.7, 7.18) * mm, "mid": v(-97.47, 7.13) * mm, "end": v(-97.24, 7.12) * mm});
            skArc(sketch, "E1922", {"start": v(-97.24, 7.12) * mm, "mid": v(-97.09, 7.09) * mm, "end": v(-96.97, 6.99) * mm});
            skArc(sketch, "E1923", {"start": v(-96.97, 6.99) * mm, "mid": v(-96.87, 6.82) * mm, "end": v(-96.81, 6.63) * mm});
            skArc(sketch, "E1924", {"start": v(-96.81, 6.63) * mm, "mid": v(-96.77, 6.25) * mm, "end": v(-96.75, 5.88) * mm});
            skArc(sketch, "E1925", {"start": v(-96.75, 5.88) * mm, "mid": v(-96.74, 4.96) * mm, "end": v(-96.73, 4.04) * mm});
            skLineSegment(sketch, "E1926", {"start": v(-96.73, 4.04) * mm, "end": v(-96.73, 0.96) * mm});
            skLineSegment(sketch, "E1927", {"start": v(-96.73, 0.96) * mm, "end": v(-94.31, 1.11) * mm});
            skArc(sketch, "E1928", {"start": v(-94.31, 1.11) * mm, "mid": v(-93.82, 1.15) * mm, "end": v(-93.33, 1.2) * mm});
            skArc(sketch, "E1929", {"start": v(-93.33, 1.2) * mm, "mid": v(-92.85, 1.25) * mm, "end": v(-92.37, 1.32) * mm});
            skArc(sketch, "E1930", {"start": v(-92.37, 1.32) * mm, "mid": v(-91.96, 1.38) * mm, "end": v(-91.55, 1.45) * mm});
            skArc(sketch, "E1931", {"start": v(-91.55, 1.45) * mm, "mid": v(-91.32, 1.5) * mm, "end": v(-91.1, 1.58) * mm});
            skLineSegment(sketch, "E1932", {"start": v(-91.1, 1.58) * mm, "end": v(-90.29, 1.89) * mm});
            skLineSegment(sketch, "E1933", {"start": v(-90.29, 1.89) * mm, "end": v(-91, 2.64) * mm});
            skArc(sketch, "E1934", {"start": v(-91, 2.64) * mm, "mid": v(-91.27, 2.96) * mm, "end": v(-91.52, 3.3) * mm});
            skArc(sketch, "E1935", {"start": v(-91.52, 3.3) * mm, "mid": v(-91.81, 3.74) * mm, "end": v(-92.09, 4.19) * mm});
            skArc(sketch, "E1936", {"start": v(-92.09, 4.19) * mm, "mid": v(-92.33, 4.61) * mm, "end": v(-92.56, 5.04) * mm});
            skArc(sketch, "E1937", {"start": v(-92.56, 5.04) * mm, "mid": v(-92.55, 5.14) * mm, "end": v(-92.47, 5.19) * mm});
            skArc(sketch, "E1938", {"start": v(-92.47, 5.19) * mm, "mid": v(-92.42, 5.18) * mm, "end": v(-92.37, 5.17) * mm});
            skArc(sketch, "E1939", {"start": v(-92.37, 5.17) * mm, "mid": v(-92.14, 5.12) * mm, "end": v(-91.9, 5.06) * mm});
            skArc(sketch, "E1940", {"start": v(-91.9, 5.06) * mm, "mid": v(-91.63, 5) * mm, "end": v(-91.36, 4.93) * mm});
            skArc(sketch, "E1941", {"start": v(-91.36, 4.93) * mm, "mid": v(-91.05, 4.85) * mm, "end": v(-90.73, 4.77) * mm});
            skArc(sketch, "E1942", {"start": v(-90.73, 4.77) * mm, "mid": v(-89.87, 4.57) * mm, "end": v(-89, 4.44) * mm});
            skArc(sketch, "E1943", {"start": v(-89, 4.44) * mm, "mid": v(-87.84, 4.32) * mm, "end": v(-86.67, 4.23) * mm});
            skArc(sketch, "E1944", {"start": v(-86.67, 4.23) * mm, "mid": v(-85.5, 4.17) * mm, "end": v(-84.32, 4.12) * mm});
            skArc(sketch, "E1945", {"start": v(-84.32, 4.12) * mm, "mid": v(-84.07, 4.18) * mm, "end": v(-83.88, 4.35) * mm});
            skArc(sketch, "E1946", {"start": v(-83.88, 4.35) * mm, "mid": v(-83.85, 4.43) * mm, "end": v(-83.84, 4.5) * mm});
            skArc(sketch, "E1947", {"start": v(-83.84, 4.5) * mm, "mid": v(-83.86, 4.64) * mm, "end": v(-83.89, 4.78) * mm});
            skArc(sketch, "E1948", {"start": v(-83.89, 4.78) * mm, "mid": v(-83.93, 4.94) * mm, "end": v(-84, 5.1) * mm});
            skArc(sketch, "E1949", {"start": v(-84, 5.1) * mm, "mid": v(-84.06, 5.27) * mm, "end": v(-84.14, 5.44) * mm});
            skArc(sketch, "E1950", {"start": v(-84.14, 5.44) * mm, "mid": v(-84.4, 5.98) * mm, "end": v(-84.6, 6.53) * mm});
            skArc(sketch, "E1951", {"start": v(-84.6, 6.53) * mm, "mid": v(-84.61, 6.79) * mm, "end": v(-84.47, 7) * mm});
            skArc(sketch, "E1952", {"start": v(-84.47, 7) * mm, "mid": v(-84.17, 7.16) * mm, "end": v(-83.85, 7.21) * mm});
            skArc(sketch, "E1953", {"start": v(-83.85, 7.21) * mm, "mid": v(-82.86, 7.21) * mm, "end": v(-81.87, 7.19) * mm});
            skArc(sketch, "E1954", {"start": v(-81.87, 7.19) * mm, "mid": v(-81.27, 7.18) * mm, "end": v(-80.66, 7.18) * mm});
            skArc(sketch, "E1955", {"start": v(-80.66, 7.18) * mm, "mid": v(-80.1, 7.2) * mm, "end": v(-79.53, 7.22) * mm});
            skArc(sketch, "E1956", {"start": v(-79.53, 7.22) * mm, "mid": v(-79.03, 7.27) * mm, "end": v(-78.54, 7.32) * mm});
            skArc(sketch, "E1957", {"start": v(-78.54, 7.32) * mm, "mid": v(-78.17, 7.39) * mm, "end": v(-77.8, 7.47) * mm});
            skLineSegment(sketch, "E1958", {"start": v(-77.8, 7.47) * mm, "end": v(-76.41, 7.85) * mm});
            skLineSegment(sketch, "E1959", {"start": v(-76.41, 7.85) * mm, "end": v(-76.33, 9.42) * mm});
            skArc(sketch, "E1960", {"start": v(-76.33, 9.42) * mm, "mid": v(-76.3, 9.86) * mm, "end": v(-76.26, 10.3) * mm});
            skArc(sketch, "E1961", {"start": v(-76.26, 10.3) * mm, "mid": v(-76.23, 10.5) * mm, "end": v(-76.16, 10.71) * mm});
            skArc(sketch, "E1962", {"start": v(-76.16, 10.71) * mm, "mid": v(-76.1, 10.83) * mm, "end": v(-75.99, 10.92) * mm});
            skArc(sketch, "E1963", {"start": v(-75.99, 10.92) * mm, "mid": v(-75.85, 10.97) * mm, "end": v(-75.7, 11) * mm});
            skArc(sketch, "E1964", {"start": v(-75.7, 11) * mm, "mid": v(-75.57, 11) * mm, "end": v(-75.43, 11.05) * mm});
            skArc(sketch, "E1965", {"start": v(-75.43, 11.05) * mm, "mid": v(-75.33, 11.12) * mm, "end": v(-75.27, 11.21) * mm});
            skArc(sketch, "E1966", {"start": v(-75.27, 11.21) * mm, "mid": v(-75.21, 11.37) * mm, "end": v(-75.19, 11.53) * mm});
            skArc(sketch, "E1967", {"start": v(-75.19, 11.53) * mm, "mid": v(-75.17, 11.85) * mm, "end": v(-75.16, 12.17) * mm});
            skArc(sketch, "E1968", {"start": v(-75.16, 12.17) * mm, "mid": v(-75.15, 12.6) * mm, "end": v(-75.1, 13.05) * mm});
            skArc(sketch, "E1969", {"start": v(-75.1, 13.05) * mm, "mid": v(-75.04, 13.35) * mm, "end": v(-74.93, 13.65) * mm});
            skArc(sketch, "E1970", {"start": v(-74.93, 13.65) * mm, "mid": v(-74.82, 13.8) * mm, "end": v(-74.67, 13.92) * mm});
            skArc(sketch, "E1971", {"start": v(-74.67, 13.92) * mm, "mid": v(-74.5, 13.95) * mm, "end": v(-74.35, 13.9) * mm});
            skArc(sketch, "E1972", {"start": v(-74.35, 13.9) * mm, "mid": v(-74.27, 13.83) * mm, "end": v(-74.21, 13.74) * mm});
            skArc(sketch, "E1973", {"start": v(-74.21, 13.74) * mm, "mid": v(-74.16, 13.57) * mm, "end": v(-74.13, 13.4) * mm});
            skArc(sketch, "E1974", {"start": v(-74.13, 13.4) * mm, "mid": v(-74.1, 13.18) * mm, "end": v(-74.1, 12.96) * mm});
            skArc(sketch, "E1975", {"start": v(-74.1, 12.96) * mm, "mid": v(-74.1, 12.69) * mm, "end": v(-74.1, 12.41) * mm});
            skArc(sketch, "E1976", {"start": v(-74.1, 12.41) * mm, "mid": v(-74.13, 12.04) * mm, "end": v(-74.14, 11.66) * mm});
            skArc(sketch, "E1977", {"start": v(-74.14, 11.66) * mm, "mid": v(-74.13, 11.5) * mm, "end": v(-74.08, 11.32) * mm});
            skArc(sketch, "E1978", {"start": v(-74.08, 11.32) * mm, "mid": v(-74.02, 11.22) * mm, "end": v(-73.91, 11.14) * mm});
            skArc(sketch, "E1979", {"start": v(-73.91, 11.14) * mm, "mid": v(-73.75, 11.08) * mm, "end": v(-73.58, 11.04) * mm});
            skArc(sketch, "E1980", {"start": v(-73.58, 11.04) * mm, "mid": v(-73.42, 11) * mm, "end": v(-73.27, 10.96) * mm});
            skArc(sketch, "E1981", {"start": v(-73.27, 10.96) * mm, "mid": v(-73.17, 10.9) * mm, "end": v(-73.08, 10.8) * mm});
            skArc(sketch, "E1982", {"start": v(-73.08, 10.8) * mm, "mid": v(-73.02, 10.68) * mm, "end": v(-72.98, 10.55) * mm});
            skArc(sketch, "E1983", {"start": v(-72.98, 10.55) * mm, "mid": v(-72.96, 10.35) * mm, "end": v(-72.96, 10.14) * mm});
            skArc(sketch, "E1984", {"start": v(-72.96, 10.14) * mm, "mid": v(-72.95, 9.99) * mm, "end": v(-72.94, 9.83) * mm});
            skArc(sketch, "E1985", {"start": v(-72.94, 9.83) * mm, "mid": v(-72.92, 9.7) * mm, "end": v(-72.88, 9.57) * mm});
            skArc(sketch, "E1986", {"start": v(-72.88, 9.57) * mm, "mid": v(-72.85, 9.48) * mm, "end": v(-72.8, 9.39) * mm});
            skArc(sketch, "E1987", {"start": v(-72.8, 9.39) * mm, "mid": v(-72.77, 9.35) * mm, "end": v(-72.71, 9.33) * mm});
            skArc(sketch, "E1988", {"start": v(-72.71, 9.33) * mm, "mid": v(-72.4, 9.4) * mm, "end": v(-72.14, 9.58) * mm});
            skArc(sketch, "E1989", {"start": v(-72.14, 9.58) * mm, "mid": v(-71.22, 10.6) * mm, "end": v(-70.31, 11.63) * mm});
            skArc(sketch, "E1990", {"start": v(-70.31, 11.63) * mm, "mid": v(-69.44, 12.65) * mm, "end": v(-68.6, 13.7) * mm});
            skArc(sketch, "E1991", {"start": v(-68.6, 13.7) * mm, "mid": v(-68.08, 14.42) * mm, "end": v(-67.61, 15.18) * mm});
            skArc(sketch, "E1992", {"start": v(-67.61, 15.18) * mm, "mid": v(-67.28, 15.8) * mm, "end": v(-66.96, 16.44) * mm});
            skArc(sketch, "E1993", {"start": v(-66.96, 16.44) * mm, "mid": v(-66.73, 16.96) * mm, "end": v(-66.52, 17.5) * mm});
            skArc(sketch, "E1994", {"start": v(-66.52, 17.5) * mm, "mid": v(-66.4, 17.88) * mm, "end": v(-66.31, 18.26) * mm});
            skArc(sketch, "E1995", {"start": v(-66.31, 18.26) * mm, "mid": v(-66.35, 18.4) * mm, "end": v(-66.47, 18.46) * mm});
            skArc(sketch, "E1996", {"start": v(-66.47, 18.46) * mm, "mid": v(-66.54, 18.45) * mm, "end": v(-66.6, 18.42) * mm});
            skArc(sketch, "E1997", {"start": v(-66.6, 18.42) * mm, "mid": v(-66.82, 18.28) * mm, "end": v(-67.03, 18.14) * mm});
            skArc(sketch, "E1998", {"start": v(-67.03, 18.14) * mm, "mid": v(-67.29, 17.97) * mm, "end": v(-67.54, 17.8) * mm});
            skArc(sketch, "E1999", {"start": v(-67.54, 17.8) * mm, "mid": v(-67.81, 17.59) * mm, "end": v(-68.1, 17.38) * mm});
            skArc(sketch, "E2000", {"start": v(-68.1, 17.38) * mm, "mid": v(-68.63, 16.98) * mm, "end": v(-69.18, 16.6) * mm});
            skArc(sketch, "E2001", {"start": v(-69.18, 16.6) * mm, "mid": v(-69.76, 16.23) * mm, "end": v(-70.36, 15.86) * mm});
            skArc(sketch, "E2002", {"start": v(-70.36, 15.86) * mm, "mid": v(-70.9, 15.55) * mm, "end": v(-71.45, 15.25) * mm});
            skArc(sketch, "E2003", {"start": v(-71.45, 15.25) * mm, "mid": v(-71.68, 15.17) * mm, "end": v(-71.91, 15.14) * mm});
            skArc(sketch, "E2004", {"start": v(-71.91, 15.14) * mm, "mid": v(-71.97, 15.16) * mm, "end": v(-72, 15.21) * mm});
            skArc(sketch, "E2005", {"start": v(-72, 15.21) * mm, "mid": v(-72.03, 15.46) * mm, "end": v(-72.06, 15.7) * mm});
            skArc(sketch, "E2006", {"start": v(-72.06, 15.7) * mm, "mid": v(-72.1, 16.02) * mm, "end": v(-72.11, 16.33) * mm});
            skArc(sketch, "E2007", {"start": v(-72.11, 16.33) * mm, "mid": v(-72.12, 16.7) * mm, "end": v(-72.13, 17.07) * mm});
            skArc(sketch, "E2008", {"start": v(-72.13, 17.07) * mm, "mid": v(-72.13, 17.46) * mm, "end": v(-72.14, 17.85) * mm});
            skArc(sketch, "E2009", {"start": v(-72.14, 17.85) * mm, "mid": v(-72.17, 18.16) * mm, "end": v(-72.2, 18.47) * mm});
            skArc(sketch, "E2010", {"start": v(-72.2, 18.47) * mm, "mid": v(-72.24, 18.7) * mm, "end": v(-72.3, 18.92) * mm});
            skArc(sketch, "E2011", {"start": v(-72.3, 18.92) * mm, "mid": v(-72.33, 18.98) * mm, "end": v(-72.4, 19.01) * mm});
            skArc(sketch, "E2012", {"start": v(-72.4, 19.01) * mm, "mid": v(-72.5, 19) * mm, "end": v(-72.58, 18.94) * mm});
            skArc(sketch, "E2013", {"start": v(-72.58, 18.94) * mm, "mid": v(-72.86, 18.7) * mm, "end": v(-73.14, 18.44) * mm});
            skArc(sketch, "E2014", {"start": v(-73.14, 18.44) * mm, "mid": v(-73.47, 18.13) * mm, "end": v(-73.8, 17.82) * mm});
            skArc(sketch, "E2015", {"start": v(-73.8, 17.82) * mm, "mid": v(-74.16, 17.45) * mm, "end": v(-74.51, 17.07) * mm});
            skArc(sketch, "E2016", {"start": v(-74.51, 17.07) * mm, "mid": v(-75.1, 16.45) * mm, "end": v(-75.71, 15.84) * mm});
            skArc(sketch, "E2017", {"start": v(-75.71, 15.84) * mm, "mid": v(-76.02, 15.56) * mm, "end": v(-76.35, 15.3) * mm});
            skArc(sketch, "E2018", {"start": v(-76.35, 15.3) * mm, "mid": v(-76.5, 15.25) * mm, "end": v(-76.67, 15.27) * mm});
            skArc(sketch, "E2019", {"start": v(-76.67, 15.27) * mm, "mid": v(-76.78, 15.36) * mm, "end": v(-76.83, 15.5) * mm});
            skArc(sketch, "E2020", {"start": v(-76.83, 15.5) * mm, "mid": v(-76.83, 15.59) * mm, "end": v(-76.85, 15.68) * mm});
            skArc(sketch, "E2021", {"start": v(-76.85, 15.68) * mm, "mid": v(-76.9, 15.8) * mm, "end": v(-76.94, 15.91) * mm});
            skArc(sketch, "E2022", {"start": v(-76.94, 15.91) * mm, "mid": v(-77, 16.04) * mm, "end": v(-77.06, 16.16) * mm});
            skArc(sketch, "E2023", {"start": v(-77.06, 16.16) * mm, "mid": v(-77.13, 16.27) * mm, "end": v(-77.2, 16.38) * mm});
            skArc(sketch, "E2024", {"start": v(-77.2, 16.38) * mm, "mid": v(-77.32, 16.52) * mm, "end": v(-77.45, 16.65) * mm});
            skArc(sketch, "E2025", {"start": v(-77.45, 16.65) * mm, "mid": v(-77.53, 16.69) * mm, "end": v(-77.62, 16.66) * mm});
            skArc(sketch, "E2026", {"start": v(-77.62, 16.66) * mm, "mid": v(-77.72, 16.58) * mm, "end": v(-77.8, 16.48) * mm});
            skArc(sketch, "E2027", {"start": v(-77.8, 16.48) * mm, "mid": v(-77.98, 16.13) * mm, "end": v(-78.16, 15.79) * mm});
            skArc(sketch, "E2028", {"start": v(-78.16, 15.79) * mm, "mid": v(-78.46, 15.28) * mm, "end": v(-78.82, 14.81) * mm});
            skArc(sketch, "E2029", {"start": v(-78.82, 14.81) * mm, "mid": v(-79.47, 14.1) * mm, "end": v(-80.14, 13.4) * mm});
            skArc(sketch, "E2030", {"start": v(-80.14, 13.4) * mm, "mid": v(-80.84, 12.71) * mm, "end": v(-81.55, 12.04) * mm});
            skArc(sketch, "E2031", {"start": v(-81.55, 12.04) * mm, "mid": v(-81.8, 11.88) * mm, "end": v(-82.1, 11.82) * mm});
            skArc(sketch, "E2032", {"start": v(-82.1, 11.82) * mm, "mid": v(-82.16, 11.83) * mm, "end": v(-82.2, 11.86) * mm});
            skArc(sketch, "E2033", {"start": v(-82.2, 11.86) * mm, "mid": v(-82.25, 11.9) * mm, "end": v(-82.3, 11.96) * mm});
            skArc(sketch, "E2034", {"start": v(-82.3, 11.96) * mm, "mid": v(-82.33, 12.04) * mm, "end": v(-82.36, 12.12) * mm});
            skArc(sketch, "E2035", {"start": v(-82.36, 12.12) * mm, "mid": v(-82.39, 12.21) * mm, "end": v(-82.4, 12.3) * mm});
            skArc(sketch, "E2036", {"start": v(-82.4, 12.3) * mm, "mid": v(-82.4, 12.4) * mm, "end": v(-82.42, 12.51) * mm});
            skArc(sketch, "E2037", {"start": v(-82.42, 12.51) * mm, "mid": v(-82.43, 12.63) * mm, "end": v(-82.44, 12.74) * mm});
            skArc(sketch, "E2038", {"start": v(-82.44, 12.74) * mm, "mid": v(-82.45, 12.85) * mm, "end": v(-82.46, 12.96) * mm});
            skArc(sketch, "E2039", {"start": v(-82.46, 12.96) * mm, "mid": v(-82.46, 13.04) * mm, "end": v(-82.47, 13.12) * mm});
            skArc(sketch, "E2040", {"start": v(-82.47, 13.12) * mm, "mid": v(-82.5, 13.3) * mm, "end": v(-82.58, 13.5) * mm});
            skArc(sketch, "E2041", {"start": v(-82.58, 13.5) * mm, "mid": v(-82.67, 13.6) * mm, "end": v(-82.8, 13.65) * mm});
            skArc(sketch, "E2042", {"start": v(-82.8, 13.65) * mm, "mid": v(-82.96, 13.65) * mm, "end": v(-83.12, 13.6) * mm});
            skArc(sketch, "E2043", {"start": v(-83.12, 13.6) * mm, "mid": v(-83.33, 13.45) * mm, "end": v(-83.53, 13.28) * mm});
            skArc(sketch, "E2044", {"start": v(-83.53, 13.28) * mm, "mid": v(-83.88, 12.99) * mm, "end": v(-84.26, 12.72) * mm});
            skArc(sketch, "E2045", {"start": v(-84.26, 12.72) * mm, "mid": v(-84.67, 12.47) * mm, "end": v(-85.1, 12.25) * mm});
            skArc(sketch, "E2046", {"start": v(-85.1, 12.25) * mm, "mid": v(-85.52, 12.07) * mm, "end": v(-85.95, 11.92) * mm});
            skArc(sketch, "E2047", {"start": v(-85.95, 11.92) * mm, "mid": v(-86.3, 11.85) * mm, "end": v(-86.65, 11.82) * mm});
            skLineSegment(sketch, "E2048", {"start": v(-86.65, 11.82) * mm, "end": v(-87.37, 11.82) * mm});
            skLineSegment(sketch, "E2049", {"start": v(-87.37, 11.82) * mm, "end": v(-86.8, 12.63) * mm});
            skArc(sketch, "E2050", {"start": v(-86.8, 12.63) * mm, "mid": v(-86.5, 13.06) * mm, "end": v(-86.25, 13.5) * mm});
            skArc(sketch, "E2051", {"start": v(-86.25, 13.5) * mm, "mid": v(-86.02, 13.96) * mm, "end": v(-85.81, 14.43) * mm});
            skArc(sketch, "E2052", {"start": v(-85.81, 14.43) * mm, "mid": v(-85.66, 14.84) * mm, "end": v(-85.52, 15.25) * mm});
            skArc(sketch, "E2053", {"start": v(-85.52, 15.25) * mm, "mid": v(-85.53, 15.4) * mm, "end": v(-85.63, 15.53) * mm});
            skArc(sketch, "E2054", {"start": v(-85.63, 15.53) * mm, "mid": v(-85.7, 15.56) * mm, "end": v(-85.79, 15.55) * mm});
            skArc(sketch, "E2055", {"start": v(-85.79, 15.55) * mm, "mid": v(-86.03, 15.5) * mm, "end": v(-86.27, 15.43) * mm});
            skArc(sketch, "E2056", {"start": v(-86.27, 15.43) * mm, "mid": v(-86.56, 15.35) * mm, "end": v(-86.85, 15.25) * mm});
            skArc(sketch, "E2057", {"start": v(-86.85, 15.25) * mm, "mid": v(-87.17, 15.14) * mm, "end": v(-87.5, 15.01) * mm});
            skArc(sketch, "E2058", {"start": v(-87.5, 15.01) * mm, "mid": v(-87.86, 14.88) * mm, "end": v(-88.23, 14.75) * mm});
            skArc(sketch, "E2059", {"start": v(-88.23, 14.75) * mm, "mid": v(-88.66, 14.62) * mm, "end": v(-89.09, 14.5) * mm});
            skArc(sketch, "E2060", {"start": v(-89.09, 14.5) * mm, "mid": v(-89.5, 14.39) * mm, "end": v(-89.93, 14.29) * mm});
            skArc(sketch, "E2061", {"start": v(-89.93, 14.29) * mm, "mid": v(-90.27, 14.22) * mm, "end": v(-90.62, 14.17) * mm});
            skLineSegment(sketch, "E2062", {"start": v(-90.62, 14.17) * mm, "end": v(-92.1, 13.97) * mm});
            skLineSegment(sketch, "E2063", {"start": v(-92.1, 13.97) * mm, "end": v(-91.38, 14.93) * mm});
            skArc(sketch, "E2064", {"start": v(-91.38, 14.93) * mm, "mid": v(-91.02, 15.42) * mm, "end": v(-90.68, 15.94) * mm});
            skArc(sketch, "E2065", {"start": v(-90.68, 15.94) * mm, "mid": v(-90.62, 16.17) * mm, "end": v(-90.68, 16.4) * mm});
            skArc(sketch, "E2066", {"start": v(-90.68, 16.4) * mm, "mid": v(-90.85, 16.53) * mm, "end": v(-91.06, 16.53) * mm});
            skArc(sketch, "E2067", {"start": v(-91.06, 16.53) * mm, "mid": v(-91.58, 16.32) * mm, "end": v(-92.08, 16.08) * mm});
            skArc(sketch, "E2068", {"start": v(-92.08, 16.08) * mm, "mid": v(-92.3, 15.98) * mm, "end": v(-92.54, 15.9) * mm});
            skArc(sketch, "E2069", {"start": v(-92.54, 15.9) * mm, "mid": v(-92.9, 15.81) * mm, "end": v(-93.28, 15.73) * mm});
            skArc(sketch, "E2070", {"start": v(-93.28, 15.73) * mm, "mid": v(-93.7, 15.65) * mm, "end": v(-94.12, 15.58) * mm});
            skArc(sketch, "E2071", {"start": v(-94.12, 15.58) * mm, "mid": v(-94.55, 15.53) * mm, "end": v(-94.97, 15.5) * mm});
            skLineSegment(sketch, "E2072", {"start": v(-94.97, 15.5) * mm, "end": v(-97, 15.34) * mm});
            skLineSegment(sketch, "E2073", {"start": v(-97, 15.34) * mm, "end": v(-96.4, 16.46) * mm});
            skArc(sketch, "E2074", {"start": v(-96.4, 16.46) * mm, "mid": v(-96.28, 16.68) * mm, "end": v(-96.17, 16.9) * mm});
            skArc(sketch, "E2075", {"start": v(-96.17, 16.9) * mm, "mid": v(-96.08, 17.1) * mm, "end": v(-96, 17.31) * mm});
            skArc(sketch, "E2076", {"start": v(-96, 17.31) * mm, "mid": v(-95.96, 17.47) * mm, "end": v(-95.91, 17.64) * mm});
            skArc(sketch, "E2077", {"start": v(-95.91, 17.64) * mm, "mid": v(-95.92, 17.7) * mm, "end": v(-95.95, 17.77) * mm});
            skArc(sketch, "E2078", {"start": v(-95.95, 17.77) * mm, "mid": v(-96.01, 17.8) * mm, "end": v(-96.08, 17.82) * mm});
            skArc(sketch, "E2079", {"start": v(-96.08, 17.82) * mm, "mid": v(-96.23, 17.82) * mm, "end": v(-96.39, 17.8) * mm});
            skArc(sketch, "E2080", {"start": v(-96.39, 17.8) * mm, "mid": v(-96.58, 17.78) * mm, "end": v(-96.77, 17.75) * mm});
            skArc(sketch, "E2081", {"start": v(-96.77, 17.75) * mm, "mid": v(-96.98, 17.7) * mm, "end": v(-97.2, 17.65) * mm});
            skArc(sketch, "E2082", {"start": v(-97.2, 17.65) * mm, "mid": v(-97.75, 17.52) * mm, "end": v(-98.32, 17.45) * mm});
            skArc(sketch, "E2083", {"start": v(-98.32, 17.45) * mm, "mid": v(-99.2, 17.4) * mm, "end": v(-100.1, 17.36) * mm});
            skArc(sketch, "E2084", {"start": v(-100.1, 17.36) * mm, "mid": v(-100.97, 17.35) * mm, "end": v(-101.85, 17.36) * mm});
            skArc(sketch, "E2085", {"start": v(-101.85, 17.36) * mm, "mid": v(-102.27, 17.4) * mm, "end": v(-102.67, 17.53) * mm});
            skArc(sketch, "E2086", {"start": v(-102.67, 17.53) * mm, "mid": v(-102.77, 17.58) * mm, "end": v(-102.85, 17.65) * mm});
            skArc(sketch, "E2087", {"start": v(-102.85, 17.65) * mm, "mid": v(-102.88, 17.73) * mm, "end": v(-102.86, 17.82) * mm});
            skArc(sketch, "E2088", {"start": v(-102.86, 17.82) * mm, "mid": v(-102.79, 17.94) * mm, "end": v(-102.7, 18.06) * mm});
            skArc(sketch, "E2089", {"start": v(-102.7, 18.06) * mm, "mid": v(-102.45, 18.28) * mm, "end": v(-102.21, 18.5) * mm});
            skArc(sketch, "E2090", {"start": v(-102.21, 18.5) * mm, "mid": v(-101.92, 18.75) * mm, "end": v(-101.64, 19) * mm});
            skArc(sketch, "E2091", {"start": v(-101.64, 19) * mm, "mid": v(-101.55, 19.1) * mm, "end": v(-101.5, 19.23) * mm});
            skArc(sketch, "E2092", {"start": v(-101.5, 19.23) * mm, "mid": v(-101.49, 19.33) * mm, "end": v(-101.54, 19.42) * mm});
            skArc(sketch, "E2093", {"start": v(-101.54, 19.42) * mm, "mid": v(-101.68, 19.57) * mm, "end": v(-101.83, 19.7) * mm});
            skArc(sketch, "E2094", {"start": v(-101.83, 19.7) * mm, "mid": v(-101.95, 19.78) * mm, "end": v(-102.06, 19.86) * mm});
            skArc(sketch, "E2095", {"start": v(-102.06, 19.86) * mm, "mid": v(-102.19, 19.93) * mm, "end": v(-102.31, 20) * mm});
            skArc(sketch, "E2096", {"start": v(-102.31, 20) * mm, "mid": v(-102.43, 20.04) * mm, "end": v(-102.55, 20.09) * mm});
            skArc(sketch, "E2097", {"start": v(-102.55, 20.09) * mm, "mid": v(-102.63, 20.1) * mm, "end": v(-102.72, 20.12) * mm});
            skArc(sketch, "E2098", {"start": v(-102.72, 20.12) * mm, "mid": v(-103.03, 20.16) * mm, "end": v(-103.33, 20.27) * mm});
            skArc(sketch, "E2099", {"start": v(-103.33, 20.27) * mm, "mid": v(-103.77, 20.53) * mm, "end": v(-104.2, 20.81) * mm});
            skArc(sketch, "E2100", {"start": v(-104.2, 20.81) * mm, "mid": v(-104.62, 21.14) * mm, "end": v(-105.03, 21.5) * mm});
            skArc(sketch, "E2101", {"start": v(-105.03, 21.5) * mm, "mid": v(-105.32, 21.82) * mm, "end": v(-105.57, 22.18) * mm});
            skArc(sketch, "E2102", {"start": v(-105.57, 22.18) * mm, "mid": v(-105.68, 22.35) * mm, "end": v(-105.79, 22.53) * mm});
            skArc(sketch, "E2103", {"start": v(-105.79, 22.53) * mm, "mid": v(-105.88, 22.7) * mm, "end": v(-105.97, 22.86) * mm});
            skArc(sketch, "E2104", {"start": v(-105.97, 22.86) * mm, "mid": v(-106.04, 23) * mm, "end": v(-106.11, 23.13) * mm});
            skArc(sketch, "E2105", {"start": v(-106.11, 23.13) * mm, "mid": v(-106.13, 23.17) * mm, "end": v(-106.14, 23.22) * mm});
            skArc(sketch, "E2106", {"start": v(-106.14, 23.22) * mm, "mid": v(-106.12, 23.25) * mm, "end": v(-106.09, 23.26) * mm});
            skArc(sketch, "E2107", {"start": v(-106.09, 23.26) * mm, "mid": v(-105.9, 23.23) * mm, "end": v(-105.71, 23.2) * mm});
            skArc(sketch, "E2108", {"start": v(-105.71, 23.2) * mm, "mid": v(-105.48, 23.16) * mm, "end": v(-105.25, 23.11) * mm});
            skArc(sketch, "E2109", {"start": v(-105.25, 23.11) * mm, "mid": v(-104.97, 23.05) * mm, "end": v(-104.7, 22.98) * mm});
            skArc(sketch, "E2110", {"start": v(-104.7, 22.98) * mm, "mid": v(-104.37, 22.9) * mm, "end": v(-104.05, 22.84) * mm});
            skArc(sketch, "E2111", {"start": v(-104.05, 22.84) * mm, "mid": v(-103.7, 22.77) * mm, "end": v(-103.33, 22.71) * mm});
            skArc(sketch, "E2112", {"start": v(-103.33, 22.71) * mm, "mid": v(-102.97, 22.67) * mm, "end": v(-102.62, 22.63) * mm});
            skArc(sketch, "E2113", {"start": v(-102.62, 22.63) * mm, "mid": v(-102.34, 22.61) * mm, "end": v(-102.07, 22.6) * mm});
            skArc(sketch, "E2114", {"start": v(-102.07, 22.6) * mm, "mid": v(-101.7, 22.6) * mm, "end": v(-101.34, 22.62) * mm});
            skArc(sketch, "E2115", {"start": v(-101.34, 22.62) * mm, "mid": v(-101.19, 22.65) * mm, "end": v(-101.05, 22.72) * mm});
            skArc(sketch, "E2116", {"start": v(-101.05, 22.72) * mm, "mid": v(-100.96, 22.82) * mm, "end": v(-100.92, 22.94) * mm});
            skArc(sketch, "E2117", {"start": v(-100.92, 22.94) * mm, "mid": v(-100.9, 23.18) * mm, "end": v(-100.88, 23.42) * mm});
            skArc(sketch, "E2118", {"start": v(-100.88, 23.42) * mm, "mid": v(-100.89, 23.6) * mm, "end": v(-100.91, 23.77) * mm});
            skArc(sketch, "E2119", {"start": v(-100.91, 23.77) * mm, "mid": v(-100.96, 23.93) * mm, "end": v(-101.01, 24.08) * mm});
            skArc(sketch, "E2120", {"start": v(-101.01, 24.08) * mm, "mid": v(-101.08, 24.21) * mm, "end": v(-101.16, 24.34) * mm});
            skArc(sketch, "E2121", {"start": v(-101.16, 24.34) * mm, "mid": v(-101.25, 24.43) * mm, "end": v(-101.35, 24.5) * mm});
            skArc(sketch, "E2122", {"start": v(-101.35, 24.5) * mm, "mid": v(-101.47, 24.57) * mm, "end": v(-101.59, 24.66) * mm});
            skArc(sketch, "E2123", {"start": v(-101.59, 24.66) * mm, "mid": v(-101.64, 24.72) * mm, "end": v(-101.67, 24.8) * mm});
            skArc(sketch, "E2124", {"start": v(-101.67, 24.8) * mm, "mid": v(-101.67, 24.88) * mm, "end": v(-101.64, 24.96) * mm});
            skArc(sketch, "E2125", {"start": v(-101.64, 24.96) * mm, "mid": v(-101.55, 25.08) * mm, "end": v(-101.46, 25.2) * mm});
            skArc(sketch, "E2126", {"start": v(-101.46, 25.2) * mm, "mid": v(-101.37, 25.33) * mm, "end": v(-101.29, 25.46) * mm});
            skArc(sketch, "E2127", {"start": v(-101.29, 25.46) * mm, "mid": v(-101.25, 25.57) * mm, "end": v(-101.24, 25.69) * mm});
            skArc(sketch, "E2128", {"start": v(-101.24, 25.69) * mm, "mid": v(-101.27, 25.82) * mm, "end": v(-101.31, 25.94) * mm});
            skArc(sketch, "E2129", {"start": v(-101.31, 25.94) * mm, "mid": v(-101.42, 26.13) * mm, "end": v(-101.53, 26.32) * mm});
            skArc(sketch, "E2130", {"start": v(-101.53, 26.32) * mm, "mid": v(-101.64, 26.5) * mm, "end": v(-101.72, 26.68) * mm});
            skArc(sketch, "E2131", {"start": v(-101.72, 26.68) * mm, "mid": v(-101.8, 26.95) * mm, "end": v(-101.9, 27.23) * mm});
            skArc(sketch, "E2132", {"start": v(-101.9, 27.23) * mm, "mid": v(-101.97, 27.54) * mm, "end": v(-102.04, 27.85) * mm});
            skArc(sketch, "E2133", {"start": v(-102.04, 27.85) * mm, "mid": v(-102.09, 28.16) * mm, "end": v(-102.13, 28.46) * mm});
            skArc(sketch, "E2134", {"start": v(-102.13, 28.46) * mm, "mid": v(-102.22, 29.28) * mm, "end": v(-102.32, 30.1) * mm});
            skArc(sketch, "E2135", {"start": v(-102.32, 30.1) * mm, "mid": v(-102.4, 30.63) * mm, "end": v(-102.51, 31.15) * mm});
            skArc(sketch, "E2136", {"start": v(-102.51, 31.15) * mm, "mid": v(-102.6, 31.51) * mm, "end": v(-102.73, 31.87) * mm});
            skArc(sketch, "E2137", {"start": v(-102.73, 31.87) * mm, "mid": v(-102.86, 32.12) * mm, "end": v(-103.03, 32.35) * mm});
            skArc(sketch, "E2138", {"start": v(-103.03, 32.35) * mm, "mid": v(-103.24, 32.66) * mm, "end": v(-103.37, 33.01) * mm});
            skArc(sketch, "E2139", {"start": v(-103.37, 33.01) * mm, "mid": v(-103.5, 33.59) * mm, "end": v(-103.57, 34.17) * mm});
            skArc(sketch, "E2140", {"start": v(-103.57, 34.17) * mm, "mid": v(-103.6, 34.76) * mm, "end": v(-103.6, 35.35) * mm});
            skArc(sketch, "E2141", {"start": v(-103.6, 35.35) * mm, "mid": v(-103.54, 35.74) * mm, "end": v(-103.4, 36.1) * mm});
            skArc(sketch, "E2142", {"start": v(-103.4, 36.1) * mm, "mid": v(-103.2, 36.38) * mm, "end": v(-102.93, 36.59) * mm});
            skArc(sketch, "E2143", {"start": v(-102.93, 36.59) * mm, "mid": v(-102.54, 36.79) * mm, "end": v(-102.12, 36.93) * mm});
            skArc(sketch, "E2144", {"start": v(-102.12, 36.93) * mm, "mid": v(-101.64, 37.03) * mm, "end": v(-101.15, 37.08) * mm});
            skArc(sketch, "E2145", {"start": v(-101.15, 37.08) * mm, "mid": v(-100.67, 37.06) * mm, "end": v(-100.2, 36.98) * mm});
            skArc(sketch, "E2146", {"start": v(-100.2, 36.98) * mm, "mid": v(-99.8, 36.88) * mm, "end": v(-99.42, 36.75) * mm});
            skArc(sketch, "E2147", {"start": v(-99.42, 36.75) * mm, "mid": v(-99.12, 36.6) * mm, "end": v(-98.84, 36.43) * mm});
            skArc(sketch, "E2148", {"start": v(-98.84, 36.43) * mm, "mid": v(-98.6, 36.22) * mm, "end": v(-98.4, 35.98) * mm});
            skArc(sketch, "E2149", {"start": v(-98.4, 35.98) * mm, "mid": v(-98.18, 35.67) * mm, "end": v(-98, 35.34) * mm});
            skArc(sketch, "E2150", {"start": v(-98, 35.34) * mm, "mid": v(-97.73, 34.72) * mm, "end": v(-97.56, 34.08) * mm});
            skArc(sketch, "E2151", {"start": v(-97.56, 34.08) * mm, "mid": v(-97.46, 33.38) * mm, "end": v(-97.44, 32.67) * mm});
            skArc(sketch, "E2152", {"start": v(-97.44, 32.67) * mm, "mid": v(-97.5, 31.72) * mm, "end": v(-97.64, 30.78) * mm});
            skArc(sketch, "E2153", {"start": v(-97.64, 30.78) * mm, "mid": v(-97.92, 29.28) * mm, "end": v(-98.24, 27.79) * mm});
            skArc(sketch, "E2154", {"start": v(-98.24, 27.79) * mm, "mid": v(-98.25, 27.67) * mm, "end": v(-98.24, 27.56) * mm});
            skArc(sketch, "E2155", {"start": v(-98.24, 27.56) * mm, "mid": v(-98.21, 27.41) * mm, "end": v(-98.17, 27.27) * mm});
            skArc(sketch, "E2156", {"start": v(-98.17, 27.27) * mm, "mid": v(-98.11, 27.12) * mm, "end": v(-98.04, 26.97) * mm});
            skArc(sketch, "E2157", {"start": v(-98.04, 26.97) * mm, "mid": v(-97.96, 26.84) * mm, "end": v(-97.86, 26.71) * mm});
            skLineSegment(sketch, "E2158", {"start": v(-97.86, 26.71) * mm, "end": v(-97.38, 26.12) * mm});
            skLineSegment(sketch, "E2159", {"start": v(-97.38, 26.12) * mm, "end": v(-96.8, 26.74) * mm});
            skArc(sketch, "E2160", {"start": v(-96.8, 26.74) * mm, "mid": v(-96.67, 26.9) * mm, "end": v(-96.56, 27.09) * mm});
            skArc(sketch, "E2161", {"start": v(-96.56, 27.09) * mm, "mid": v(-96.44, 27.33) * mm, "end": v(-96.33, 27.58) * mm});
            skArc(sketch, "E2162", {"start": v(-96.33, 27.58) * mm, "mid": v(-96.23, 27.87) * mm, "end": v(-96.15, 28.16) * mm});
            skArc(sketch, "E2163", {"start": v(-96.15, 28.16) * mm, "mid": v(-96.09, 28.47) * mm, "end": v(-96.04, 28.79) * mm});
            skArc(sketch, "E2164", {"start": v(-96.04, 28.79) * mm, "mid": v(-96, 29.09) * mm, "end": v(-95.94, 29.38) * mm});
            skArc(sketch, "E2165", {"start": v(-95.94, 29.38) * mm, "mid": v(-95.88, 29.7) * mm, "end": v(-95.8, 30) * mm});
            skArc(sketch, "E2166", {"start": v(-95.8, 30) * mm, "mid": v(-95.73, 30.29) * mm, "end": v(-95.65, 30.56) * mm});
            skArc(sketch, "E2167", {"start": v(-95.65, 30.56) * mm, "mid": v(-95.58, 30.76) * mm, "end": v(-95.5, 30.94) * mm});
            skArc(sketch, "E2168", {"start": v(-95.5, 30.94) * mm, "mid": v(-95.43, 31.1) * mm, "end": v(-95.37, 31.28) * mm});
            skArc(sketch, "E2169", {"start": v(-95.37, 31.28) * mm, "mid": v(-95.32, 31.47) * mm, "end": v(-95.29, 31.67) * mm});
            skArc(sketch, "E2170", {"start": v(-95.29, 31.67) * mm, "mid": v(-95.26, 31.87) * mm, "end": v(-95.25, 32.07) * mm});
            skArc(sketch, "E2171", {"start": v(-95.25, 32.07) * mm, "mid": v(-95.26, 32.23) * mm, "end": v(-95.28, 32.4) * mm});
            skArc(sketch, "E2172", {"start": v(-95.28, 32.4) * mm, "mid": v(-95.3, 32.53) * mm, "end": v(-95.32, 32.67) * mm});
            skArc(sketch, "E2173", {"start": v(-95.32, 32.67) * mm, "mid": v(-95.32, 32.79) * mm, "end": v(-95.32, 32.9) * mm});
            skArc(sketch, "E2174", {"start": v(-95.32, 32.9) * mm, "mid": v(-95.3, 32.98) * mm, "end": v(-95.29, 33.06) * mm});
            skArc(sketch, "E2175", {"start": v(-95.29, 33.06) * mm, "mid": v(-95.26, 33.1) * mm, "end": v(-95.22, 33.11) * mm});
            skArc(sketch, "E2176", {"start": v(-95.22, 33.11) * mm, "mid": v(-95.06, 33.09) * mm, "end": v(-94.9, 33.01) * mm});
            skArc(sketch, "E2177", {"start": v(-94.9, 33.01) * mm, "mid": v(-94.63, 32.8) * mm, "end": v(-94.36, 32.58) * mm});
            skArc(sketch, "E2178", {"start": v(-94.36, 32.58) * mm, "mid": v(-94.1, 32.35) * mm, "end": v(-93.85, 32.12) * mm});
            skArc(sketch, "E2179", {"start": v(-93.85, 32.12) * mm, "mid": v(-93.81, 32.03) * mm, "end": v(-93.85, 31.94) * mm});
            skArc(sketch, "E2180", {"start": v(-93.85, 31.94) * mm, "mid": v(-93.9, 31.84) * mm, "end": v(-93.86, 31.74) * mm});
            skArc(sketch, "E2181", {"start": v(-93.86, 31.74) * mm, "mid": v(-93.72, 31.6) * mm, "end": v(-93.56, 31.47) * mm});
            skArc(sketch, "E2182", {"start": v(-93.56, 31.47) * mm, "mid": v(-93.37, 31.36) * mm, "end": v(-93.16, 31.27) * mm});
            skArc(sketch, "E2183", {"start": v(-93.16, 31.27) * mm, "mid": v(-93.01, 31.26) * mm, "end": v(-92.88, 31.3) * mm});
            skArc(sketch, "E2184", {"start": v(-92.88, 31.3) * mm, "mid": v(-92.81, 31.35) * mm, "end": v(-92.76, 31.4) * mm});
            skArc(sketch, "E2185", {"start": v(-92.76, 31.4) * mm, "mid": v(-92.71, 31.49) * mm, "end": v(-92.67, 31.57) * mm});
            skArc(sketch, "E2186", {"start": v(-92.67, 31.57) * mm, "mid": v(-92.63, 31.66) * mm, "end": v(-92.6, 31.76) * mm});
            skArc(sketch, "E2187", {"start": v(-92.6, 31.76) * mm, "mid": v(-92.58, 31.86) * mm, "end": v(-92.58, 31.95) * mm});
            skArc(sketch, "E2188", {"start": v(-92.58, 31.95) * mm, "mid": v(-92.57, 32.08) * mm, "end": v(-92.56, 32.21) * mm});
            skArc(sketch, "E2189", {"start": v(-92.56, 32.21) * mm, "mid": v(-92.54, 32.24) * mm, "end": v(-92.5, 32.26) * mm});
            skArc(sketch, "E2190", {"start": v(-92.5, 32.26) * mm, "mid": v(-92.45, 32.24) * mm, "end": v(-92.41, 32.2) * mm});
            skArc(sketch, "E2191", {"start": v(-92.41, 32.2) * mm, "mid": v(-92.3, 32.05) * mm, "end": v(-92.17, 31.9) * mm});
            skArc(sketch, "E2192", {"start": v(-92.17, 31.9) * mm, "mid": v(-92.07, 31.75) * mm, "end": v(-91.99, 31.58) * mm});
            skArc(sketch, "E2193", {"start": v(-91.99, 31.58) * mm, "mid": v(-91.96, 31.46) * mm, "end": v(-91.98, 31.33) * mm});
            skArc(sketch, "E2194", {"start": v(-91.98, 31.33) * mm, "mid": v(-92.05, 31.2) * mm, "end": v(-92.14, 31.06) * mm});
            skArc(sketch, "E2195", {"start": v(-92.14, 31.06) * mm, "mid": v(-92.38, 30.83) * mm, "end": v(-92.62, 30.6) * mm});
            skArc(sketch, "E2196", {"start": v(-92.62, 30.6) * mm, "mid": v(-92.9, 30.3) * mm, "end": v(-93.14, 30) * mm});
            skArc(sketch, "E2197", {"start": v(-93.14, 30) * mm, "mid": v(-93.27, 29.75) * mm, "end": v(-93.34, 29.46) * mm});
            skArc(sketch, "E2198", {"start": v(-93.34, 29.46) * mm, "mid": v(-93.32, 29.22) * mm, "end": v(-93.23, 29) * mm});
            skArc(sketch, "E2199", {"start": v(-93.23, 29) * mm, "mid": v(-93.05, 28.78) * mm, "end": v(-92.83, 28.6) * mm});
            skArc(sketch, "E2200", {"start": v(-92.83, 28.6) * mm, "mid": v(-92.7, 28.54) * mm, "end": v(-92.57, 28.52) * mm});
            skArc(sketch, "E2201", {"start": v(-92.57, 28.52) * mm, "mid": v(-92.43, 28.53) * mm, "end": v(-92.3, 28.57) * mm});
            skArc(sketch, "E2202", {"start": v(-92.3, 28.57) * mm, "mid": v(-92.13, 28.67) * mm, "end": v(-91.98, 28.8) * mm});
            skArc(sketch, "E2203", {"start": v(-91.98, 28.8) * mm, "mid": v(-91.75, 29.03) * mm, "end": v(-91.52, 29.27) * mm});
            skLineSegment(sketch, "E2204", {"start": v(-91.52, 29.27) * mm, "end": v(-90.67, 30.2) * mm});
            skLineSegment(sketch, "E2205", {"start": v(-90.67, 30.2) * mm, "end": v(-90.66, 29.48) * mm});
            skArc(sketch, "E2206", {"start": v(-90.66, 29.48) * mm, "mid": v(-90.69, 29.2) * mm, "end": v(-90.78, 28.93) * mm});
            skArc(sketch, "E2207", {"start": v(-90.78, 28.93) * mm, "mid": v(-90.96, 28.6) * mm, "end": v(-91.18, 28.28) * mm});
            skArc(sketch, "E2208", {"start": v(-91.18, 28.28) * mm, "mid": v(-91.48, 27.92) * mm, "end": v(-91.81, 27.57) * mm});
            skArc(sketch, "E2209", {"start": v(-91.81, 27.57) * mm, "mid": v(-92.24, 27.19) * mm, "end": v(-92.68, 26.82) * mm});
            skArc(sketch, "E2210", {"start": v(-92.68, 26.82) * mm, "mid": v(-92.8, 26.71) * mm, "end": v(-92.89, 26.58) * mm});
            skArc(sketch, "E2211", {"start": v(-92.89, 26.58) * mm, "mid": v(-92.94, 26.46) * mm, "end": v(-92.95, 26.33) * mm});
            skArc(sketch, "E2212", {"start": v(-92.95, 26.33) * mm, "mid": v(-92.92, 26.14) * mm, "end": v(-92.86, 25.96) * mm});
            skArc(sketch, "E2213", {"start": v(-92.86, 25.96) * mm, "mid": v(-92.7, 25.58) * mm, "end": v(-92.55, 25.2) * mm});
            skArc(sketch, "E2214", {"start": v(-92.55, 25.2) * mm, "mid": v(-92.42, 24.9) * mm, "end": v(-92.3, 24.58) * mm});
            skArc(sketch, "E2215", {"start": v(-92.3, 24.58) * mm, "mid": v(-92.22, 24.3) * mm, "end": v(-92.16, 24.02) * mm});
            skArc(sketch, "E2216", {"start": v(-92.16, 24.02) * mm, "mid": v(-92.13, 23.76) * mm, "end": v(-92.11, 23.5) * mm});
            skArc(sketch, "E2217", {"start": v(-92.11, 23.5) * mm, "mid": v(-92.12, 23.26) * mm, "end": v(-92.15, 23.03) * mm});
            skArc(sketch, "E2218", {"start": v(-92.15, 23.03) * mm, "mid": v(-92.2, 22.78) * mm, "end": v(-92.22, 22.54) * mm});
            skArc(sketch, "E2219", {"start": v(-92.22, 22.54) * mm, "mid": v(-92.22, 22.4) * mm, "end": v(-92.19, 22.26) * mm});
            skArc(sketch, "E2220", {"start": v(-92.19, 22.26) * mm, "mid": v(-92.13, 22.16) * mm, "end": v(-92.04, 22.1) * mm});
            skArc(sketch, "E2221", {"start": v(-92.04, 22.1) * mm, "mid": v(-91.9, 22.02) * mm, "end": v(-91.76, 21.97) * mm});
            skArc(sketch, "E2222", {"start": v(-91.76, 21.97) * mm, "mid": v(-91.65, 21.93) * mm, "end": v(-91.54, 21.88) * mm});
            skArc(sketch, "E2223", {"start": v(-91.54, 21.88) * mm, "mid": v(-91.45, 21.8) * mm, "end": v(-91.36, 21.71) * mm});
            skArc(sketch, "E2224", {"start": v(-91.36, 21.71) * mm, "mid": v(-91.3, 21.61) * mm, "end": v(-91.24, 21.5) * mm});
            skArc(sketch, "E2225", {"start": v(-91.24, 21.5) * mm, "mid": v(-91.21, 21.4) * mm, "end": v(-91.2, 21.28) * mm});
            skArc(sketch, "E2226", {"start": v(-91.2, 21.28) * mm, "mid": v(-91.19, 21.13) * mm, "end": v(-91.14, 21) * mm});
            skArc(sketch, "E2227", {"start": v(-91.14, 21) * mm, "mid": v(-91.07, 20.89) * mm, "end": v(-90.96, 20.81) * mm});
            skArc(sketch, "E2228", {"start": v(-90.96, 20.81) * mm, "mid": v(-90.8, 20.74) * mm, "end": v(-90.61, 20.7) * mm});
            skArc(sketch, "E2229", {"start": v(-90.61, 20.7) * mm, "mid": v(-90.27, 20.66) * mm, "end": v(-89.94, 20.62) * mm});
            skArc(sketch, "E2230", {"start": v(-89.94, 20.62) * mm, "mid": v(-89.69, 20.6) * mm, "end": v(-89.44, 20.6) * mm});
            skArc(sketch, "E2231", {"start": v(-89.44, 20.6) * mm, "mid": v(-89.22, 20.6) * mm, "end": v(-89, 20.61) * mm});
            skArc(sketch, "E2232", {"start": v(-89, 20.61) * mm, "mid": v(-88.83, 20.63) * mm, "end": v(-88.66, 20.65) * mm});
            skArc(sketch, "E2233", {"start": v(-88.66, 20.65) * mm, "mid": v(-88.6, 20.68) * mm, "end": v(-88.54, 20.73) * mm});
            skArc(sketch, "E2234", {"start": v(-88.54, 20.73) * mm, "mid": v(-88.52, 20.8) * mm, "end": v(-88.52, 20.86) * mm});
            skArc(sketch, "E2235", {"start": v(-88.52, 20.86) * mm, "mid": v(-88.57, 21.03) * mm, "end": v(-88.62, 21.2) * mm});
            skArc(sketch, "E2236", {"start": v(-88.62, 21.2) * mm, "mid": v(-88.7, 21.4) * mm, "end": v(-88.77, 21.6) * mm});
            skArc(sketch, "E2237", {"start": v(-88.77, 21.6) * mm, "mid": v(-88.87, 21.81) * mm, "end": v(-88.98, 22.03) * mm});
            skArc(sketch, "E2238", {"start": v(-88.98, 22.03) * mm, "mid": v(-89.2, 22.48) * mm, "end": v(-89.4, 22.93) * mm});
            skArc(sketch, "E2239", {"start": v(-89.4, 22.93) * mm, "mid": v(-89.49, 23.24) * mm, "end": v(-89.53, 23.55) * mm});
            skArc(sketch, "E2240", {"start": v(-89.53, 23.55) * mm, "mid": v(-89.5, 23.7) * mm, "end": v(-89.4, 23.83) * mm});
            skArc(sketch, "E2241", {"start": v(-89.4, 23.83) * mm, "mid": v(-89.26, 23.9) * mm, "end": v(-89.1, 23.88) * mm});
            skArc(sketch, "E2242", {"start": v(-89.1, 23.88) * mm, "mid": v(-88.53, 23.67) * mm, "end": v(-87.94, 23.48) * mm});
            skArc(sketch, "E2243", {"start": v(-87.94, 23.48) * mm, "mid": v(-87.73, 23.47) * mm, "end": v(-87.55, 23.57) * mm});
            skArc(sketch, "E2244", {"start": v(-87.55, 23.57) * mm, "mid": v(-87.41, 23.77) * mm, "end": v(-87.36, 24) * mm});
            skArc(sketch, "E2245", {"start": v(-87.36, 24) * mm, "mid": v(-87.34, 24.8) * mm, "end": v(-87.33, 25.62) * mm});
            skArc(sketch, "E2246", {"start": v(-87.33, 25.62) * mm, "mid": v(-87.33, 26.35) * mm, "end": v(-87.32, 27.08) * mm});
            skArc(sketch, "E2247", {"start": v(-87.32, 27.08) * mm, "mid": v(-87.3, 27.33) * mm, "end": v(-87.24, 27.57) * mm});
            skArc(sketch, "E2248", {"start": v(-87.24, 27.57) * mm, "mid": v(-87.17, 27.7) * mm, "end": v(-87.04, 27.78) * mm});
            skArc(sketch, "E2249", {"start": v(-87.04, 27.78) * mm, "mid": v(-86.84, 27.84) * mm, "end": v(-86.64, 27.86) * mm});
            skArc(sketch, "E2250", {"start": v(-86.64, 27.86) * mm, "mid": v(-86.44, 27.87) * mm, "end": v(-86.23, 27.9) * mm});
            skArc(sketch, "E2251", {"start": v(-86.23, 27.9) * mm, "mid": v(-86.13, 27.96) * mm, "end": v(-86.06, 28.06) * mm});
            skArc(sketch, "E2252", {"start": v(-86.06, 28.06) * mm, "mid": v(-86.02, 28.22) * mm, "end": v(-86.02, 28.39) * mm});
            skArc(sketch, "E2253", {"start": v(-86.02, 28.39) * mm, "mid": v(-86.07, 28.86) * mm, "end": v(-86.12, 29.34) * mm});
            skArc(sketch, "E2254", {"start": v(-86.12, 29.34) * mm, "mid": v(-86.16, 29.69) * mm, "end": v(-86.18, 30.04) * mm});
            skArc(sketch, "E2255", {"start": v(-86.18, 30.04) * mm, "mid": v(-86.19, 30.28) * mm, "end": v(-86.17, 30.52) * mm});
            skArc(sketch, "E2256", {"start": v(-86.17, 30.52) * mm, "mid": v(-86.15, 30.7) * mm, "end": v(-86.1, 30.86) * mm});
            skArc(sketch, "E2257", {"start": v(-86.1, 30.86) * mm, "mid": v(-86.04, 30.96) * mm, "end": v(-85.95, 31.04) * mm});
            skArc(sketch, "E2258", {"start": v(-85.95, 31.04) * mm, "mid": v(-85.78, 31.1) * mm, "end": v(-85.6, 31.05) * mm});
            skArc(sketch, "E2259", {"start": v(-85.6, 31.05) * mm, "mid": v(-85.44, 30.93) * mm, "end": v(-85.34, 30.76) * mm});
            skArc(sketch, "E2260", {"start": v(-85.34, 30.76) * mm, "mid": v(-85.25, 30.44) * mm, "end": v(-85.22, 30.1) * mm});
            skArc(sketch, "E2261", {"start": v(-85.22, 30.1) * mm, "mid": v(-85.24, 29.64) * mm, "end": v(-85.28, 29.17) * mm});
            skArc(sketch, "E2262", {"start": v(-85.28, 29.17) * mm, "mid": v(-85.33, 28.78) * mm, "end": v(-85.37, 28.39) * mm});
            skArc(sketch, "E2263", {"start": v(-85.37, 28.39) * mm, "mid": v(-85.37, 28.22) * mm, "end": v(-85.33, 28.06) * mm});
            skArc(sketch, "E2264", {"start": v(-85.33, 28.06) * mm, "mid": v(-85.28, 27.97) * mm, "end": v(-85.18, 27.91) * mm});
            skArc(sketch, "E2265", {"start": v(-85.18, 27.91) * mm, "mid": v(-85.03, 27.87) * mm, "end": v(-84.87, 27.86) * mm});
            skArc(sketch, "E2266", {"start": v(-84.87, 27.86) * mm, "mid": v(-84.7, 27.83) * mm, "end": v(-84.55, 27.76) * mm});
            skArc(sketch, "E2267", {"start": v(-84.55, 27.76) * mm, "mid": v(-84.44, 27.64) * mm, "end": v(-84.38, 27.5) * mm});
            skArc(sketch, "E2268", {"start": v(-84.38, 27.5) * mm, "mid": v(-84.33, 27.2) * mm, "end": v(-84.3, 26.91) * mm});
            skArc(sketch, "E2269", {"start": v(-84.3, 26.91) * mm, "mid": v(-84.3, 26.15) * mm, "end": v(-84.3, 25.39) * mm});
            skArc(sketch, "E2270", {"start": v(-84.3, 25.39) * mm, "mid": v(-84.29, 24.88) * mm, "end": v(-84.27, 24.38) * mm});
            skArc(sketch, "E2271", {"start": v(-84.27, 24.38) * mm, "mid": v(-84.25, 23.97) * mm, "end": v(-84.2, 23.55) * mm});
            skArc(sketch, "E2272", {"start": v(-84.2, 23.55) * mm, "mid": v(-84.17, 23.23) * mm, "end": v(-84.12, 22.91) * mm});
            skArc(sketch, "E2273", {"start": v(-84.12, 22.91) * mm, "mid": v(-84.08, 22.8) * mm, "end": v(-84, 22.73) * mm});
            skArc(sketch, "E2274", {"start": v(-84, 22.73) * mm, "mid": v(-83.89, 22.68) * mm, "end": v(-83.77, 22.66) * mm});
            skArc(sketch, "E2275", {"start": v(-83.77, 22.66) * mm, "mid": v(-83.21, 22.62) * mm, "end": v(-82.66, 22.6) * mm});
            skArc(sketch, "E2276", {"start": v(-82.66, 22.6) * mm, "mid": v(-82, 22.56) * mm, "end": v(-81.36, 22.54) * mm});
            skArc(sketch, "E2277", {"start": v(-81.36, 22.54) * mm, "mid": v(-80.6, 22.52) * mm, "end": v(-79.86, 22.5) * mm});
            skArc(sketch, "E2278", {"start": v(-79.86, 22.5) * mm, "mid": v(-78.33, 22.5) * mm, "end": v(-76.8, 22.52) * mm});
            skArc(sketch, "E2279", {"start": v(-76.8, 22.52) * mm, "mid": v(-76.28, 22.58) * mm, "end": v(-75.79, 22.75) * mm});
            skArc(sketch, "E2280", {"start": v(-75.79, 22.75) * mm, "mid": v(-75.6, 22.96) * mm, "end": v(-75.63, 23.24) * mm});
            skArc(sketch, "E2281", {"start": v(-75.63, 23.24) * mm, "mid": v(-75.96, 23.73) * mm, "end": v(-76.35, 24.16) * mm});
            skArc(sketch, "E2282", {"start": v(-76.35, 24.16) * mm, "mid": v(-76.55, 24.36) * mm, "end": v(-76.75, 24.56) * mm});
            skArc(sketch, "E2283", {"start": v(-76.75, 24.56) * mm, "mid": v(-76.91, 24.74) * mm, "end": v(-77.08, 24.94) * mm});
            skArc(sketch, "E2284", {"start": v(-77.08, 24.94) * mm, "mid": v(-77.2, 25.1) * mm, "end": v(-77.33, 25.26) * mm});
            skArc(sketch, "E2285", {"start": v(-77.33, 25.26) * mm, "mid": v(-77.37, 25.33) * mm, "end": v(-77.38, 25.4) * mm});
            skArc(sketch, "E2286", {"start": v(-77.38, 25.4) * mm, "mid": v(-77.35, 25.47) * mm, "end": v(-77.3, 25.5) * mm});
            skArc(sketch, "E2287", {"start": v(-77.3, 25.5) * mm, "mid": v(-76.87, 25.54) * mm, "end": v(-76.45, 25.57) * mm});
            skArc(sketch, "E2288", {"start": v(-76.45, 25.57) * mm, "mid": v(-75.93, 25.6) * mm, "end": v(-75.42, 25.63) * mm});
            skArc(sketch, "E2289", {"start": v(-75.42, 25.63) * mm, "mid": v(-74.8, 25.64) * mm, "end": v(-74.2, 25.65) * mm});
            skLineSegment(sketch, "E2290", {"start": v(-74.2, 25.65) * mm, "end": v(-71.02, 25.65) * mm});
            skLineSegment(sketch, "E2291", {"start": v(-71.02, 25.65) * mm, "end": v(-71.02, 28.13) * mm});
            skArc(sketch, "E2292", {"start": v(-71.02, 28.13) * mm, "mid": v(-71.02, 28.96) * mm, "end": v(-71, 29.78) * mm});
            skArc(sketch, "E2293", {"start": v(-71, 29.78) * mm, "mid": v(-70.99, 30.04) * mm, "end": v(-70.93, 30.3) * mm});
            skArc(sketch, "E2294", {"start": v(-70.93, 30.3) * mm, "mid": v(-70.86, 30.44) * mm, "end": v(-70.73, 30.54) * mm});
            skArc(sketch, "E2295", {"start": v(-70.73, 30.54) * mm, "mid": v(-70.53, 30.6) * mm, "end": v(-70.33, 30.62) * mm});
            skArc(sketch, "E2296", {"start": v(-70.33, 30.62) * mm, "mid": v(-70.13, 30.64) * mm, "end": v(-69.93, 30.68) * mm});
            skArc(sketch, "E2297", {"start": v(-69.93, 30.68) * mm, "mid": v(-69.82, 30.74) * mm, "end": v(-69.74, 30.84) * mm});
            skArc(sketch, "E2298", {"start": v(-69.74, 30.84) * mm, "mid": v(-69.68, 31.02) * mm, "end": v(-69.65, 31.2) * mm});
            skArc(sketch, "E2299", {"start": v(-69.65, 31.2) * mm, "mid": v(-69.64, 31.66) * mm, "end": v(-69.64, 32.13) * mm});
            skArc(sketch, "E2300", {"start": v(-69.64, 32.13) * mm, "mid": v(-69.62, 32.58) * mm, "end": v(-69.59, 33.04) * mm});
            skArc(sketch, "E2301", {"start": v(-69.59, 33.04) * mm, "mid": v(-69.52, 33.36) * mm, "end": v(-69.42, 33.66) * mm});
            skArc(sketch, "E2302", {"start": v(-69.42, 33.66) * mm, "mid": v(-69.31, 33.8) * mm, "end": v(-69.16, 33.89) * mm});
            skArc(sketch, "E2303", {"start": v(-69.16, 33.89) * mm, "mid": v(-69, 33.9) * mm, "end": v(-68.87, 33.82) * mm});
            skArc(sketch, "E2304", {"start": v(-68.87, 33.82) * mm, "mid": v(-68.82, 33.75) * mm, "end": v(-68.8, 33.68) * mm});
            skArc(sketch, "E2305", {"start": v(-68.8, 33.68) * mm, "mid": v(-68.77, 33.46) * mm, "end": v(-68.75, 33.25) * mm});
            skArc(sketch, "E2306", {"start": v(-68.75, 33.25) * mm, "mid": v(-68.73, 32.98) * mm, "end": v(-68.71, 32.72) * mm});
            skArc(sketch, "E2307", {"start": v(-68.71, 32.72) * mm, "mid": v(-68.7, 32.43) * mm, "end": v(-68.7, 32.13) * mm});
            skArc(sketch, "E2308", {"start": v(-68.7, 32.13) * mm, "mid": v(-68.71, 31.67) * mm, "end": v(-68.7, 31.2) * mm});
            skArc(sketch, "E2309", {"start": v(-68.7, 31.2) * mm, "mid": v(-68.69, 31.02) * mm, "end": v(-68.63, 30.85) * mm});
            skArc(sketch, "E2310", {"start": v(-68.63, 30.85) * mm, "mid": v(-68.55, 30.74) * mm, "end": v(-68.44, 30.68) * mm});
            skArc(sketch, "E2311", {"start": v(-68.44, 30.68) * mm, "mid": v(-68.26, 30.64) * mm, "end": v(-68.07, 30.62) * mm});
            skArc(sketch, "E2312", {"start": v(-68.07, 30.62) * mm, "mid": v(-67.89, 30.61) * mm, "end": v(-67.7, 30.59) * mm});
            skArc(sketch, "E2313", {"start": v(-67.7, 30.59) * mm, "mid": v(-67.6, 30.54) * mm, "end": v(-67.53, 30.46) * mm});
            skArc(sketch, "E2314", {"start": v(-67.53, 30.46) * mm, "mid": v(-67.48, 30.34) * mm, "end": v(-67.46, 30.2) * mm});
            skArc(sketch, "E2315", {"start": v(-67.46, 30.2) * mm, "mid": v(-67.46, 29.94) * mm, "end": v(-67.47, 29.67) * mm});
            skArc(sketch, "E2316", {"start": v(-67.47, 29.67) * mm, "mid": v(-67.48, 29.47) * mm, "end": v(-67.48, 29.28) * mm});
            skArc(sketch, "E2317", {"start": v(-67.48, 29.28) * mm, "mid": v(-67.47, 29.1) * mm, "end": v(-67.45, 28.93) * mm});
            skArc(sketch, "E2318", {"start": v(-67.45, 28.93) * mm, "mid": v(-67.43, 28.78) * mm, "end": v(-67.4, 28.63) * mm});
            skArc(sketch, "E2319", {"start": v(-67.4, 28.63) * mm, "mid": v(-67.37, 28.56) * mm, "end": v(-67.32, 28.5) * mm});
            skArc(sketch, "E2320", {"start": v(-67.32, 28.5) * mm, "mid": v(-67.1, 28.4) * mm, "end": v(-66.88, 28.5) * mm});
            skArc(sketch, "E2321", {"start": v(-66.88, 28.5) * mm, "mid": v(-66.22, 29.2) * mm, "end": v(-65.59, 29.93) * mm});
            skArc(sketch, "E2322", {"start": v(-65.59, 29.93) * mm, "mid": v(-64.94, 30.73) * mm, "end": v(-64.34, 31.55) * mm});
            skArc(sketch, "E2323", {"start": v(-64.34, 31.55) * mm, "mid": v(-63.9, 32.24) * mm, "end": v(-63.51, 32.97) * mm});
            skArc(sketch, "E2324", {"start": v(-63.51, 32.97) * mm, "mid": v(-63.13, 33.85) * mm, "end": v(-62.78, 34.74) * mm});
            skArc(sketch, "E2325", {"start": v(-62.78, 34.74) * mm, "mid": v(-62.6, 35.36) * mm, "end": v(-62.51, 36) * mm});
            skArc(sketch, "E2326", {"start": v(-62.51, 36) * mm, "mid": v(-62.58, 36.19) * mm, "end": v(-62.78, 36.26) * mm});
            skArc(sketch, "E2327", {"start": v(-62.78, 36.26) * mm, "mid": v(-63.06, 36.18) * mm, "end": v(-63.3, 36) * mm});
            skArc(sketch, "E2328", {"start": v(-63.3, 36) * mm, "mid": v(-63.53, 35.74) * mm, "end": v(-63.81, 35.53) * mm});
            skArc(sketch, "E2329", {"start": v(-63.81, 35.53) * mm, "mid": v(-64.32, 35.2) * mm, "end": v(-64.85, 34.87) * mm});
            skArc(sketch, "E2330", {"start": v(-64.85, 34.87) * mm, "mid": v(-65.4, 34.55) * mm, "end": v(-65.95, 34.24) * mm});
            skArc(sketch, "E2331", {"start": v(-65.95, 34.24) * mm, "mid": v(-66.08, 34.22) * mm, "end": v(-66.2, 34.28) * mm});
            skArc(sketch, "E2332", {"start": v(-66.2, 34.28) * mm, "mid": v(-66.22, 34.33) * mm, "end": v(-66.23, 34.38) * mm});
            skArc(sketch, "E2333", {"start": v(-66.23, 34.38) * mm, "mid": v(-66.2, 34.52) * mm, "end": v(-66.17, 34.67) * mm});
            skArc(sketch, "E2334", {"start": v(-66.17, 34.67) * mm, "mid": v(-66.12, 34.84) * mm, "end": v(-66.06, 35.02) * mm});
            skArc(sketch, "E2335", {"start": v(-66.06, 35.02) * mm, "mid": v(-65.99, 35.22) * mm, "end": v(-65.9, 35.41) * mm});
            skArc(sketch, "E2336", {"start": v(-65.9, 35.41) * mm, "mid": v(-65.82, 35.63) * mm, "end": v(-65.75, 35.85) * mm});
            skArc(sketch, "E2337", {"start": v(-65.75, 35.85) * mm, "mid": v(-65.68, 36.09) * mm, "end": v(-65.61, 36.33) * mm});
            skArc(sketch, "E2338", {"start": v(-65.61, 36.33) * mm, "mid": v(-65.56, 36.56) * mm, "end": v(-65.52, 36.8) * mm});
            skArc(sketch, "E2339", {"start": v(-65.52, 36.8) * mm, "mid": v(-65.5, 36.97) * mm, "end": v(-65.49, 37.14) * mm});
            skArc(sketch, "E2340", {"start": v(-65.49, 37.14) * mm, "mid": v(-65.5, 37.35) * mm, "end": v(-65.51, 37.55) * mm});
            skArc(sketch, "E2341", {"start": v(-65.51, 37.55) * mm, "mid": v(-65.54, 37.65) * mm, "end": v(-65.6, 37.72) * mm});
            skArc(sketch, "E2342", {"start": v(-65.6, 37.72) * mm, "mid": v(-65.7, 37.76) * mm, "end": v(-65.8, 37.77) * mm});
            skArc(sketch, "E2343", {"start": v(-65.8, 37.77) * mm, "mid": v(-66, 37.74) * mm, "end": v(-66.21, 37.7) * mm});
            skArc(sketch, "E2344", {"start": v(-66.21, 37.7) * mm, "mid": v(-66.81, 37.51) * mm, "end": v(-67.4, 37.28) * mm});
            skArc(sketch, "E2345", {"start": v(-67.4, 37.28) * mm, "mid": v(-68.01, 36.98) * mm, "end": v(-68.61, 36.64) * mm});
            skArc(sketch, "E2346", {"start": v(-68.61, 36.64) * mm, "mid": v(-69.28, 36.2) * mm, "end": v(-69.93, 35.74) * mm});
            skArc(sketch, "E2347", {"start": v(-69.93, 35.74) * mm, "mid": v(-70.69, 35.13) * mm, "end": v(-71.42, 34.5) * mm});
            skArc(sketch, "E2348", {"start": v(-71.42, 34.5) * mm, "mid": v(-71.85, 34.14) * mm, "end": v(-72.27, 33.77) * mm});
            skArc(sketch, "E2349", {"start": v(-72.27, 33.77) * mm, "mid": v(-72.63, 33.46) * mm, "end": v(-73, 33.16) * mm});
            skArc(sketch, "E2350", {"start": v(-73, 33.16) * mm, "mid": v(-73.3, 32.9) * mm, "end": v(-73.63, 32.63) * mm});
            skArc(sketch, "E2351", {"start": v(-73.63, 32.63) * mm, "mid": v(-73.65, 32.63) * mm, "end": v(-73.68, 32.64) * mm});
            skArc(sketch, "E2352", {"start": v(-73.68, 32.64) * mm, "mid": v(-73.7, 32.66) * mm, "end": v(-73.7, 32.7) * mm});
            skArc(sketch, "E2353", {"start": v(-73.7, 32.7) * mm, "mid": v(-73.68, 32.86) * mm, "end": v(-73.66, 33.03) * mm});
            skArc(sketch, "E2354", {"start": v(-73.66, 33.03) * mm, "mid": v(-73.63, 33.22) * mm, "end": v(-73.6, 33.42) * mm});
            skArc(sketch, "E2355", {"start": v(-73.6, 33.42) * mm, "mid": v(-73.56, 33.65) * mm, "end": v(-73.52, 33.88) * mm});
            skArc(sketch, "E2356", {"start": v(-73.52, 33.88) * mm, "mid": v(-73.48, 34.1) * mm, "end": v(-73.45, 34.34) * mm});
            skArc(sketch, "E2357", {"start": v(-73.45, 34.34) * mm, "mid": v(-73.44, 34.55) * mm, "end": v(-73.43, 34.75) * mm});
            skArc(sketch, "E2358", {"start": v(-73.43, 34.75) * mm, "mid": v(-73.44, 34.92) * mm, "end": v(-73.45, 35.08) * mm});
            skArc(sketch, "E2359", {"start": v(-73.45, 35.08) * mm, "mid": v(-73.47, 35.14) * mm, "end": v(-73.52, 35.2) * mm});
            skArc(sketch, "E2360", {"start": v(-73.52, 35.2) * mm, "mid": v(-73.6, 35.22) * mm, "end": v(-73.69, 35.2) * mm});
            skArc(sketch, "E2361", {"start": v(-73.69, 35.2) * mm, "mid": v(-74.06, 35) * mm, "end": v(-74.44, 34.8) * mm});
            skArc(sketch, "E2362", {"start": v(-74.44, 34.8) * mm, "mid": v(-74.88, 34.55) * mm, "end": v(-75.32, 34.3) * mm});
            skArc(sketch, "E2363", {"start": v(-75.32, 34.3) * mm, "mid": v(-75.82, 33.98) * mm, "end": v(-76.32, 33.66) * mm});
            skArc(sketch, "E2364", {"start": v(-76.32, 33.66) * mm, "mid": v(-77.2, 33.1) * mm, "end": v(-78.1, 32.59) * mm});
            skArc(sketch, "E2365", {"start": v(-78.1, 32.59) * mm, "mid": v(-78.9, 32.18) * mm, "end": v(-79.72, 31.81) * mm});
            skArc(sketch, "E2366", {"start": v(-79.72, 31.81) * mm, "mid": v(-80.42, 31.55) * mm, "end": v(-81.14, 31.33) * mm});
            skArc(sketch, "E2367", {"start": v(-81.14, 31.33) * mm, "mid": v(-81.71, 31.22) * mm, "end": v(-82.3, 31.18) * mm});
            skArc(sketch, "E2368", {"start": v(-82.3, 31.18) * mm, "mid": v(-82.46, 31.18) * mm, "end": v(-82.63, 31.2) * mm});
            skArc(sketch, "E2369", {"start": v(-82.63, 31.2) * mm, "mid": v(-82.7, 31.21) * mm, "end": v(-82.77, 31.25) * mm});
            skArc(sketch, "E2370", {"start": v(-82.77, 31.25) * mm, "mid": v(-82.8, 31.3) * mm, "end": v(-82.8, 31.36) * mm});
            skArc(sketch, "E2371", {"start": v(-82.8, 31.36) * mm, "mid": v(-82.75, 31.44) * mm, "end": v(-82.7, 31.52) * mm});
            skArc(sketch, "E2372", {"start": v(-82.7, 31.52) * mm, "mid": v(-82.63, 31.61) * mm, "end": v(-82.58, 31.71) * mm});
            skArc(sketch, "E2373", {"start": v(-82.58, 31.71) * mm, "mid": v(-82.52, 31.86) * mm, "end": v(-82.46, 32) * mm});
            skArc(sketch, "E2374", {"start": v(-82.46, 32) * mm, "mid": v(-82.41, 32.18) * mm, "end": v(-82.37, 32.35) * mm});
            skArc(sketch, "E2375", {"start": v(-82.37, 32.35) * mm, "mid": v(-82.34, 32.52) * mm, "end": v(-82.31, 32.7) * mm});
            skLineSegment(sketch, "E2376", {"start": v(-82.31, 32.7) * mm, "end": v(-82.22, 33.53) * mm});
            skLineSegment(sketch, "E2377", {"start": v(-82.22, 33.53) * mm, "end": v(-84.04, 33.7) * mm});
            skArc(sketch, "E2378", {"start": v(-84.04, 33.7) * mm, "mid": v(-84.72, 33.8) * mm, "end": v(-85.38, 33.94) * mm});
            skArc(sketch, "E2379", {"start": v(-85.38, 33.94) * mm, "mid": v(-86.08, 34.14) * mm, "end": v(-86.76, 34.38) * mm});
            skArc(sketch, "E2380", {"start": v(-86.76, 34.38) * mm, "mid": v(-87.34, 34.62) * mm, "end": v(-87.91, 34.9) * mm});
            skArc(sketch, "E2381", {"start": v(-87.91, 34.9) * mm, "mid": v(-88.1, 35.06) * mm, "end": v(-88.16, 35.3) * mm});
            skArc(sketch, "E2382", {"start": v(-88.16, 35.3) * mm, "mid": v(-88.11, 35.48) * mm, "end": v(-87.97, 35.6) * mm});
            skArc(sketch, "E2383", {"start": v(-87.97, 35.6) * mm, "mid": v(-87.57, 35.74) * mm, "end": v(-87.16, 35.87) * mm});
            skArc(sketch, "E2384", {"start": v(-87.16, 35.87) * mm, "mid": v(-86.6, 36.01) * mm, "end": v(-86.02, 36.12) * mm});
            skArc(sketch, "E2385", {"start": v(-86.02, 36.12) * mm, "mid": v(-85.3, 36.23) * mm, "end": v(-84.58, 36.3) * mm});
            skArc(sketch, "E2386", {"start": v(-84.58, 36.3) * mm, "mid": v(-84.2, 36.35) * mm, "end": v(-83.83, 36.4) * mm});
            skArc(sketch, "E2387", {"start": v(-83.83, 36.4) * mm, "mid": v(-83.52, 36.45) * mm, "end": v(-83.2, 36.51) * mm});
            skArc(sketch, "E2388", {"start": v(-83.2, 36.51) * mm, "mid": v(-82.95, 36.57) * mm, "end": v(-82.7, 36.63) * mm});
            skArc(sketch, "E2389", {"start": v(-82.7, 36.63) * mm, "mid": v(-82.65, 36.66) * mm, "end": v(-82.63, 36.72) * mm});
            skArc(sketch, "E2390", {"start": v(-82.63, 36.72) * mm, "mid": v(-82.64, 36.79) * mm, "end": v(-82.68, 36.84) * mm});
            skArc(sketch, "E2391", {"start": v(-82.68, 36.84) * mm, "mid": v(-82.77, 36.95) * mm, "end": v(-82.88, 37.05) * mm});
            skArc(sketch, "E2392", {"start": v(-82.88, 37.05) * mm, "mid": v(-83, 37.18) * mm, "end": v(-83.14, 37.3) * mm});
            skArc(sketch, "E2393", {"start": v(-83.14, 37.3) * mm, "mid": v(-83.3, 37.42) * mm, "end": v(-83.46, 37.54) * mm});
            skArc(sketch, "E2394", {"start": v(-83.46, 37.54) * mm, "mid": v(-83.8, 37.78) * mm, "end": v(-84.11, 38.05) * mm});
            skArc(sketch, "E2395", {"start": v(-84.11, 38.05) * mm, "mid": v(-84.22, 38.19) * mm, "end": v(-84.25, 38.36) * mm});
            skArc(sketch, "E2396", {"start": v(-84.25, 38.36) * mm, "mid": v(-84.2, 38.5) * mm, "end": v(-84.06, 38.58) * mm});
            skArc(sketch, "E2397", {"start": v(-84.06, 38.58) * mm, "mid": v(-83.73, 38.65) * mm, "end": v(-83.4, 38.7) * mm});
            skLineSegment(sketch, "E2398", {"start": v(-83.4, 38.7) * mm, "end": v(-82.5, 38.78) * mm});
            skLineSegment(sketch, "E2399", {"start": v(-82.5, 38.78) * mm, "end": v(-82.41, 41.06) * mm});
            skArc(sketch, "E2400", {"start": v(-82.41, 41.06) * mm, "mid": v(-82.39, 41.75) * mm, "end": v(-82.35, 42.44) * mm});
            skArc(sketch, "E2401", {"start": v(-82.35, 42.44) * mm, "mid": v(-82.32, 42.72) * mm, "end": v(-82.26, 43) * mm});
            skArc(sketch, "E2402", {"start": v(-82.26, 43) * mm, "mid": v(-82.19, 43.13) * mm, "end": v(-82.07, 43.24) * mm});
            skArc(sketch, "E2403", {"start": v(-82.07, 43.24) * mm, "mid": v(-81.92, 43.32) * mm, "end": v(-81.76, 43.34) * mm});
            skArc(sketch, "E2404", {"start": v(-81.76, 43.34) * mm, "mid": v(-81.6, 43.35) * mm, "end": v(-81.45, 43.39) * mm});
            skArc(sketch, "E2405", {"start": v(-81.45, 43.39) * mm, "mid": v(-81.36, 43.44) * mm, "end": v(-81.3, 43.52) * mm});
            skArc(sketch, "E2406", {"start": v(-81.3, 43.52) * mm, "mid": v(-81.27, 43.66) * mm, "end": v(-81.27, 43.8) * mm});
            skArc(sketch, "E2407", {"start": v(-81.27, 43.8) * mm, "mid": v(-81.3, 44.13) * mm, "end": v(-81.36, 44.46) * mm});
            skArc(sketch, "E2408", {"start": v(-81.36, 44.46) * mm, "mid": v(-81.4, 44.87) * mm, "end": v(-81.4, 45.3) * mm});
            skArc(sketch, "E2409", {"start": v(-81.4, 45.3) * mm, "mid": v(-81.36, 45.67) * mm, "end": v(-81.26, 46.03) * mm});
            skArc(sketch, "E2410", {"start": v(-81.26, 46.03) * mm, "mid": v(-81.15, 46.26) * mm, "end": v(-81, 46.47) * mm});
            skArc(sketch, "E2411", {"start": v(-81, 46.47) * mm, "mid": v(-80.83, 46.54) * mm, "end": v(-80.66, 46.5) * mm});
            skArc(sketch, "E2412", {"start": v(-80.66, 46.5) * mm, "mid": v(-80.6, 46.44) * mm, "end": v(-80.56, 46.35) * mm});
            skArc(sketch, "E2413", {"start": v(-80.56, 46.35) * mm, "mid": v(-80.52, 46.16) * mm, "end": v(-80.49, 45.96) * mm});
            skArc(sketch, "E2414", {"start": v(-80.49, 45.96) * mm, "mid": v(-80.46, 45.71) * mm, "end": v(-80.45, 45.46) * mm});
            skArc(sketch, "E2415", {"start": v(-80.45, 45.46) * mm, "mid": v(-80.45, 45.18) * mm, "end": v(-80.46, 44.9) * mm});
            skArc(sketch, "E2416", {"start": v(-80.46, 44.9) * mm, "mid": v(-80.48, 44.49) * mm, "end": v(-80.49, 44.07) * mm});
            skArc(sketch, "E2417", {"start": v(-80.49, 44.07) * mm, "mid": v(-80.47, 43.88) * mm, "end": v(-80.43, 43.7) * mm});
            skArc(sketch, "E2418", {"start": v(-80.43, 43.7) * mm, "mid": v(-80.36, 43.58) * mm, "end": v(-80.26, 43.5) * mm});
            skArc(sketch, "E2419", {"start": v(-80.26, 43.5) * mm, "mid": v(-80.1, 43.43) * mm, "end": v(-79.94, 43.4) * mm});
            skArc(sketch, "E2420", {"start": v(-79.94, 43.4) * mm, "mid": v(-79.76, 43.35) * mm, "end": v(-79.6, 43.26) * mm});
            skArc(sketch, "E2421", {"start": v(-79.6, 43.26) * mm, "mid": v(-79.5, 43.14) * mm, "end": v(-79.42, 42.99) * mm});
            skArc(sketch, "E2422", {"start": v(-79.42, 42.99) * mm, "mid": v(-79.35, 42.72) * mm, "end": v(-79.32, 42.45) * mm});
            skArc(sketch, "E2423", {"start": v(-79.32, 42.45) * mm, "mid": v(-79.28, 41.81) * mm, "end": v(-79.26, 41.18) * mm});
            skLineSegment(sketch, "E2424", {"start": v(-79.26, 41.18) * mm, "end": v(-79.18, 39.06) * mm});
            skLineSegment(sketch, "E2425", {"start": v(-79.18, 39.06) * mm, "end": v(-78.3, 38.97) * mm});
            skArc(sketch, "E2426", {"start": v(-78.3, 38.97) * mm, "mid": v(-78.1, 38.96) * mm, "end": v(-77.9, 38.97) * mm});
            skArc(sketch, "E2427", {"start": v(-77.9, 38.97) * mm, "mid": v(-77.64, 39) * mm, "end": v(-77.4, 39.04) * mm});
            skArc(sketch, "E2428", {"start": v(-77.4, 39.04) * mm, "mid": v(-77.13, 39.1) * mm, "end": v(-76.87, 39.16) * mm});
            skArc(sketch, "E2429", {"start": v(-76.87, 39.16) * mm, "mid": v(-76.64, 39.23) * mm, "end": v(-76.42, 39.31) * mm});
            skLineSegment(sketch, "E2430", {"start": v(-76.42, 39.31) * mm, "end": v(-75.4, 39.74) * mm});
            skLineSegment(sketch, "E2431", {"start": v(-75.4, 39.74) * mm, "end": v(-75.97, 40.55) * mm});
            skArc(sketch, "E2432", {"start": v(-75.97, 40.55) * mm, "mid": v(-76.09, 40.7) * mm, "end": v(-76.2, 40.87) * mm});
            skArc(sketch, "E2433", {"start": v(-76.2, 40.87) * mm, "mid": v(-76.3, 41.03) * mm, "end": v(-76.38, 41.2) * mm});
            skArc(sketch, "E2434", {"start": v(-76.38, 41.2) * mm, "mid": v(-76.45, 41.33) * mm, "end": v(-76.52, 41.47) * mm});
            skArc(sketch, "E2435", {"start": v(-76.52, 41.47) * mm, "mid": v(-76.54, 41.54) * mm, "end": v(-76.55, 41.62) * mm});
            skArc(sketch, "E2436", {"start": v(-76.55, 41.62) * mm, "mid": v(-76.52, 41.69) * mm, "end": v(-76.46, 41.73) * mm});
            skArc(sketch, "E2437", {"start": v(-76.46, 41.73) * mm, "mid": v(-76.13, 41.8) * mm, "end": v(-75.8, 41.85) * mm});
            skArc(sketch, "E2438", {"start": v(-75.8, 41.85) * mm, "mid": v(-75.39, 41.91) * mm, "end": v(-74.97, 41.96) * mm});
            skArc(sketch, "E2439", {"start": v(-74.97, 41.96) * mm, "mid": v(-74.48, 42) * mm, "end": v(-74, 42.04) * mm});
            skArc(sketch, "E2440", {"start": v(-74, 42.04) * mm, "mid": v(-73.46, 42.08) * mm, "end": v(-72.93, 42.13) * mm});
            skArc(sketch, "E2441", {"start": v(-72.93, 42.13) * mm, "mid": v(-72.4, 42.2) * mm, "end": v(-71.86, 42.27) * mm});
            skArc(sketch, "E2442", {"start": v(-71.86, 42.27) * mm, "mid": v(-71.4, 42.34) * mm, "end": v(-70.92, 42.43) * mm});
            skArc(sketch, "E2443", {"start": v(-70.92, 42.43) * mm, "mid": v(-70.62, 42.5) * mm, "end": v(-70.33, 42.6) * mm});
            skArc(sketch, "E2444", {"start": v(-70.33, 42.6) * mm, "mid": v(-69.99, 42.72) * mm, "end": v(-69.65, 42.87) * mm});
            skArc(sketch, "E2445", {"start": v(-69.65, 42.87) * mm, "mid": v(-69.5, 42.97) * mm, "end": v(-69.36, 43.12) * mm});
            skArc(sketch, "E2446", {"start": v(-69.36, 43.12) * mm, "mid": v(-69.27, 43.3) * mm, "end": v(-69.22, 43.5) * mm});
            skArc(sketch, "E2447", {"start": v(-69.22, 43.5) * mm, "mid": v(-69.17, 43.94) * mm, "end": v(-69.14, 44.38) * mm});
            skArc(sketch, "E2448", {"start": v(-69.14, 44.38) * mm, "mid": v(-69.11, 44.75) * mm, "end": v(-69.07, 45.11) * mm});
            skArc(sketch, "E2449", {"start": v(-69.07, 45.11) * mm, "mid": v(-69.03, 45.33) * mm, "end": v(-68.96, 45.53) * mm});
            skArc(sketch, "E2450", {"start": v(-68.96, 45.53) * mm, "mid": v(-68.89, 45.66) * mm, "end": v(-68.78, 45.78) * mm});
            skArc(sketch, "E2451", {"start": v(-68.78, 45.78) * mm, "mid": v(-68.64, 45.86) * mm, "end": v(-68.5, 45.92) * mm});
            skArc(sketch, "E2452", {"start": v(-68.5, 45.92) * mm, "mid": v(-68.36, 45.96) * mm, "end": v(-68.23, 46.02) * mm});
            skArc(sketch, "E2453", {"start": v(-68.23, 46.02) * mm, "mid": v(-68.15, 46.08) * mm, "end": v(-68.09, 46.16) * mm});
            skArc(sketch, "E2454", {"start": v(-68.09, 46.16) * mm, "mid": v(-68.06, 46.26) * mm, "end": v(-68.05, 46.36) * mm});
            skArc(sketch, "E2455", {"start": v(-68.05, 46.36) * mm, "mid": v(-68.08, 46.51) * mm, "end": v(-68.12, 46.66) * mm});
            skArc(sketch, "E2456", {"start": v(-68.12, 46.66) * mm, "mid": v(-68.18, 46.95) * mm, "end": v(-68.2, 47.25) * mm});
            skArc(sketch, "E2457", {"start": v(-68.2, 47.25) * mm, "mid": v(-68.19, 47.59) * mm, "end": v(-68.13, 47.92) * mm});
            skArc(sketch, "E2458", {"start": v(-68.13, 47.92) * mm, "mid": v(-68.05, 48.16) * mm, "end": v(-67.94, 48.4) * mm});
            skArc(sketch, "E2459", {"start": v(-67.94, 48.4) * mm, "mid": v(-67.83, 48.47) * mm, "end": v(-67.7, 48.45) * mm});
            skArc(sketch, "E2460", {"start": v(-67.7, 48.45) * mm, "mid": v(-67.63, 48.4) * mm, "end": v(-67.59, 48.32) * mm});
            skArc(sketch, "E2461", {"start": v(-67.59, 48.32) * mm, "mid": v(-67.54, 48.15) * mm, "end": v(-67.5, 47.97) * mm});
            skArc(sketch, "E2462", {"start": v(-67.5, 47.97) * mm, "mid": v(-67.47, 47.76) * mm, "end": v(-67.44, 47.54) * mm});
            skArc(sketch, "E2463", {"start": v(-67.44, 47.54) * mm, "mid": v(-67.43, 47.3) * mm, "end": v(-67.43, 47.06) * mm});
            skArc(sketch, "E2464", {"start": v(-67.43, 47.06) * mm, "mid": v(-67.42, 46.72) * mm, "end": v(-67.4, 46.38) * mm});
            skArc(sketch, "E2465", {"start": v(-67.4, 46.38) * mm, "mid": v(-67.38, 46.22) * mm, "end": v(-67.32, 46.05) * mm});
            skArc(sketch, "E2466", {"start": v(-67.32, 46.05) * mm, "mid": v(-67.26, 45.96) * mm, "end": v(-67.16, 45.89) * mm});
            skArc(sketch, "E2467", {"start": v(-67.16, 45.89) * mm, "mid": v(-67.02, 45.85) * mm, "end": v(-66.87, 45.83) * mm});
            skArc(sketch, "E2468", {"start": v(-66.87, 45.83) * mm, "mid": v(-66.74, 45.82) * mm, "end": v(-66.61, 45.8) * mm});
            skArc(sketch, "E2469", {"start": v(-66.61, 45.8) * mm, "mid": v(-66.52, 45.75) * mm, "end": v(-66.44, 45.68) * mm});
            skArc(sketch, "E2470", {"start": v(-66.44, 45.68) * mm, "mid": v(-66.38, 45.58) * mm, "end": v(-66.35, 45.47) * mm});
            skArc(sketch, "E2471", {"start": v(-66.35, 45.47) * mm, "mid": v(-66.33, 45.3) * mm, "end": v(-66.32, 45.14) * mm});
            skArc(sketch, "E2472", {"start": v(-66.32, 45.14) * mm, "mid": v(-66.3, 44.88) * mm, "end": v(-66.26, 44.63) * mm});
            skArc(sketch, "E2473", {"start": v(-66.26, 44.63) * mm, "mid": v(-66.18, 44.52) * mm, "end": v(-66.06, 44.5) * mm});
            skArc(sketch, "E2474", {"start": v(-66.06, 44.5) * mm, "mid": v(-65.87, 44.55) * mm, "end": v(-65.7, 44.67) * mm});
            skArc(sketch, "E2475", {"start": v(-65.7, 44.67) * mm, "mid": v(-65.37, 45) * mm, "end": v(-65.03, 45.35) * mm});
            skArc(sketch, "E2476", {"start": v(-65.03, 45.35) * mm, "mid": v(-64.62, 45.82) * mm, "end": v(-64.23, 46.32) * mm});
            skArc(sketch, "E2477", {"start": v(-64.23, 46.32) * mm, "mid": v(-63.87, 46.84) * mm, "end": v(-63.54, 47.38) * mm});
            skArc(sketch, "E2478", {"start": v(-63.54, 47.38) * mm, "mid": v(-63.21, 48) * mm, "end": v(-62.92, 48.62) * mm});
            skArc(sketch, "E2479", {"start": v(-62.92, 48.62) * mm, "mid": v(-62.6, 49.38) * mm, "end": v(-62.3, 50.15) * mm});
            skArc(sketch, "E2480", {"start": v(-62.3, 50.15) * mm, "mid": v(-61.96, 51.13) * mm, "end": v(-61.62, 52.12) * mm});
            skArc(sketch, "E2481", {"start": v(-61.62, 52.12) * mm, "mid": v(-61.61, 52.3) * mm, "end": v(-61.72, 52.46) * mm});
            skArc(sketch, "E2482", {"start": v(-61.72, 52.46) * mm, "mid": v(-61.89, 52.51) * mm, "end": v(-62.05, 52.45) * mm});
            skArc(sketch, "E2483", {"start": v(-62.05, 52.45) * mm, "mid": v(-62.78, 51.77) * mm, "end": v(-63.5, 51.08) * mm});
            skArc(sketch, "E2484", {"start": v(-63.5, 51.08) * mm, "mid": v(-63.78, 50.82) * mm, "end": v(-64.07, 50.55) * mm});
            skArc(sketch, "E2485", {"start": v(-64.07, 50.55) * mm, "mid": v(-64.33, 50.33) * mm, "end": v(-64.6, 50.1) * mm});
            skArc(sketch, "E2486", {"start": v(-64.6, 50.1) * mm, "mid": v(-64.82, 49.93) * mm, "end": v(-65.05, 49.76) * mm});
            skArc(sketch, "E2487", {"start": v(-65.05, 49.76) * mm, "mid": v(-65.13, 49.72) * mm, "end": v(-65.22, 49.7) * mm});
            skArc(sketch, "E2488", {"start": v(-65.22, 49.7) * mm, "mid": v(-65.29, 49.72) * mm, "end": v(-65.33, 49.78) * mm});
            skArc(sketch, "E2489", {"start": v(-65.33, 49.78) * mm, "mid": v(-65.36, 49.9) * mm, "end": v(-65.39, 50.03) * mm});
            skArc(sketch, "E2490", {"start": v(-65.39, 50.03) * mm, "mid": v(-65.4, 50.22) * mm, "end": v(-65.4, 50.4) * mm});
            skArc(sketch, "E2491", {"start": v(-65.4, 50.4) * mm, "mid": v(-65.37, 50.66) * mm, "end": v(-65.34, 50.92) * mm});
            skArc(sketch, "E2492", {"start": v(-65.34, 50.92) * mm, "mid": v(-65.29, 51.45) * mm, "end": v(-65.28, 51.99) * mm});
            skArc(sketch, "E2493", {"start": v(-65.28, 51.99) * mm, "mid": v(-65.36, 52.2) * mm, "end": v(-65.56, 52.31) * mm});
            skArc(sketch, "E2494", {"start": v(-65.56, 52.31) * mm, "mid": v(-65.85, 52.3) * mm, "end": v(-66.1, 52.17) * mm});
            skArc(sketch, "E2495", {"start": v(-66.1, 52.17) * mm, "mid": v(-66.61, 51.7) * mm, "end": v(-67.1, 51.23) * mm});
            skArc(sketch, "E2496", {"start": v(-67.1, 51.23) * mm, "mid": v(-67.74, 50.63) * mm, "end": v(-68.42, 50.08) * mm});
            skArc(sketch, "E2497", {"start": v(-68.42, 50.08) * mm, "mid": v(-69.08, 49.63) * mm, "end": v(-69.78, 49.24) * mm});
            skArc(sketch, "E2498", {"start": v(-69.78, 49.24) * mm, "mid": v(-70.5, 48.93) * mm, "end": v(-71.25, 48.7) * mm});
            skArc(sketch, "E2499", {"start": v(-71.25, 48.7) * mm, "mid": v(-72.06, 48.51) * mm, "end": v(-72.88, 48.4) * mm});
            skLineSegment(sketch, "E2500", {"start": v(-72.88, 48.4) * mm, "end": v(-74.71, 48.23) * mm});
            skLineSegment(sketch, "E2501", {"start": v(-74.71, 48.23) * mm, "end": v(-74.1, 49.22) * mm});
            skArc(sketch, "E2502", {"start": v(-74.1, 49.22) * mm, "mid": v(-73.99, 49.41) * mm, "end": v(-73.89, 49.61) * mm});
            skArc(sketch, "E2503", {"start": v(-73.89, 49.61) * mm, "mid": v(-73.8, 49.79) * mm, "end": v(-73.75, 49.97) * mm});
            skArc(sketch, "E2504", {"start": v(-73.75, 49.97) * mm, "mid": v(-73.7, 50.1) * mm, "end": v(-73.69, 50.25) * mm});
            skArc(sketch, "E2505", {"start": v(-73.69, 50.25) * mm, "mid": v(-73.7, 50.32) * mm, "end": v(-73.75, 50.37) * mm});
            skArc(sketch, "E2506", {"start": v(-73.75, 50.37) * mm, "mid": v(-73.83, 50.4) * mm, "end": v(-73.92, 50.4) * mm});
            skArc(sketch, "E2507", {"start": v(-73.92, 50.4) * mm, "mid": v(-74.14, 50.34) * mm, "end": v(-74.37, 50.28) * mm});
            skArc(sketch, "E2508", {"start": v(-74.37, 50.28) * mm, "mid": v(-74.64, 50.2) * mm, "end": v(-74.9, 50.1) * mm});
            skArc(sketch, "E2509", {"start": v(-74.9, 50.1) * mm, "mid": v(-75.2, 49.97) * mm, "end": v(-75.5, 49.84) * mm});
            skArc(sketch, "E2510", {"start": v(-75.5, 49.84) * mm, "mid": v(-76.1, 49.59) * mm, "end": v(-76.71, 49.37) * mm});
            skArc(sketch, "E2511", {"start": v(-76.71, 49.37) * mm, "mid": v(-77.41, 49.15) * mm, "end": v(-78.12, 48.96) * mm});
            skArc(sketch, "E2512", {"start": v(-78.12, 48.96) * mm, "mid": v(-78.81, 48.81) * mm, "end": v(-79.5, 48.68) * mm});
            skArc(sketch, "E2513", {"start": v(-79.5, 48.68) * mm, "mid": v(-80.05, 48.62) * mm, "end": v(-80.6, 48.6) * mm});
            skArc(sketch, "E2514", {"start": v(-80.6, 48.6) * mm, "mid": v(-80.79, 48.6) * mm, "end": v(-80.97, 48.61) * mm});
            skArc(sketch, "E2515", {"start": v(-80.97, 48.61) * mm, "mid": v(-81.04, 48.64) * mm, "end": v(-81.1, 48.7) * mm});
            skArc(sketch, "E2516", {"start": v(-81.1, 48.7) * mm, "mid": v(-81.13, 48.76) * mm, "end": v(-81.12, 48.83) * mm});
            skArc(sketch, "E2517", {"start": v(-81.12, 48.83) * mm, "mid": v(-81.06, 48.98) * mm, "end": v(-80.98, 49.13) * mm});
            skArc(sketch, "E2518", {"start": v(-80.98, 49.13) * mm, "mid": v(-80.93, 49.24) * mm, "end": v(-80.87, 49.34) * mm});
            skArc(sketch, "E2519", {"start": v(-80.87, 49.34) * mm, "mid": v(-80.83, 49.44) * mm, "end": v(-80.78, 49.54) * mm});
            skArc(sketch, "E2520", {"start": v(-80.78, 49.54) * mm, "mid": v(-80.75, 49.63) * mm, "end": v(-80.71, 49.71) * mm});
            skArc(sketch, "E2521", {"start": v(-80.71, 49.71) * mm, "mid": v(-80.7, 49.75) * mm, "end": v(-80.7, 49.79) * mm});
            skArc(sketch, "E2522", {"start": v(-80.7, 49.79) * mm, "mid": v(-80.7, 49.82) * mm, "end": v(-80.74, 49.84) * mm});
            skArc(sketch, "E2523", {"start": v(-80.74, 49.84) * mm, "mid": v(-80.98, 49.86) * mm, "end": v(-81.2, 49.87) * mm});
            skArc(sketch, "E2524", {"start": v(-81.2, 49.87) * mm, "mid": v(-81.5, 49.9) * mm, "end": v(-81.77, 49.9) * mm});
            skArc(sketch, "E2525", {"start": v(-81.77, 49.9) * mm, "mid": v(-82.1, 49.9) * mm, "end": v(-82.44, 49.9) * mm});
            skArc(sketch, "E2526", {"start": v(-82.44, 49.9) * mm, "mid": v(-82.85, 49.92) * mm, "end": v(-83.25, 49.94) * mm});
            skArc(sketch, "E2527", {"start": v(-83.25, 49.94) * mm, "mid": v(-83.62, 49.98) * mm, "end": v(-83.98, 50.04) * mm});
            skArc(sketch, "E2528", {"start": v(-83.98, 50.04) * mm, "mid": v(-84.3, 50.1) * mm, "end": v(-84.61, 50.19) * mm});
            skArc(sketch, "E2529", {"start": v(-84.61, 50.19) * mm, "mid": v(-84.88, 50.28) * mm, "end": v(-85.13, 50.4) * mm});
            skLineSegment(sketch, "E2530", {"start": v(-85.13, 50.4) * mm, "end": v(-86.08, 50.89) * mm});
            skLineSegment(sketch, "E2531", {"start": v(-86.08, 50.89) * mm, "end": v(-85.4, 51.14) * mm});
            skArc(sketch, "E2532", {"start": v(-85.4, 51.14) * mm, "mid": v(-84.9, 51.37) * mm, "end": v(-84.43, 51.66) * mm});
            skArc(sketch, "E2533", {"start": v(-84.43, 51.66) * mm, "mid": v(-84.1, 51.98) * mm, "end": v(-83.86, 52.36) * mm});
            skArc(sketch, "E2534", {"start": v(-83.86, 52.36) * mm, "mid": v(-83.77, 52.7) * mm, "end": v(-83.82, 53.04) * mm});
            skArc(sketch, "E2535", {"start": v(-83.82, 53.04) * mm, "mid": v(-84, 53.34) * mm, "end": v(-84.27, 53.56) * mm});
            skArc(sketch, "E2536", {"start": v(-84.27, 53.56) * mm, "mid": v(-84.61, 53.7) * mm, "end": v(-84.97, 53.8) * mm});
            skArc(sketch, "E2537", {"start": v(-84.97, 53.8) * mm, "mid": v(-85.39, 53.83) * mm, "end": v(-85.81, 53.82) * mm});
            skArc(sketch, "E2538", {"start": v(-85.81, 53.82) * mm, "mid": v(-86.27, 53.76) * mm, "end": v(-86.72, 53.65) * mm});
            skArc(sketch, "E2539", {"start": v(-86.72, 53.65) * mm, "mid": v(-87.18, 53.5) * mm, "end": v(-87.62, 53.3) * mm});
            skArc(sketch, "E2540", {"start": v(-87.62, 53.3) * mm, "mid": v(-88.02, 53.1) * mm, "end": v(-88.44, 52.95) * mm});
            skArc(sketch, "E2541", {"start": v(-88.44, 52.95) * mm, "mid": v(-88.61, 52.96) * mm, "end": v(-88.73, 53.08) * mm});
            skArc(sketch, "E2542", {"start": v(-88.73, 53.08) * mm, "mid": v(-88.75, 53.3) * mm, "end": v(-88.67, 53.5) * mm});
            skArc(sketch, "E2543", {"start": v(-88.67, 53.5) * mm, "mid": v(-88.35, 53.95) * mm, "end": v(-88, 54.38) * mm});
            skArc(sketch, "E2544", {"start": v(-88, 54.38) * mm, "mid": v(-87.8, 54.63) * mm, "end": v(-87.6, 54.9) * mm});
            skArc(sketch, "E2545", {"start": v(-87.6, 54.9) * mm, "mid": v(-87.51, 55.04) * mm, "end": v(-87.46, 55.19) * mm});
            skArc(sketch, "E2546", {"start": v(-87.46, 55.19) * mm, "mid": v(-87.46, 55.32) * mm, "end": v(-87.5, 55.45) * mm});
            skArc(sketch, "E2547", {"start": v(-87.5, 55.45) * mm, "mid": v(-87.6, 55.65) * mm, "end": v(-87.73, 55.84) * mm});
            skArc(sketch, "E2548", {"start": v(-87.73, 55.84) * mm, "mid": v(-87.82, 55.97) * mm, "end": v(-87.9, 56.11) * mm});
            skArc(sketch, "E2549", {"start": v(-87.9, 56.11) * mm, "mid": v(-87.97, 56.27) * mm, "end": v(-88.03, 56.42) * mm});
            skArc(sketch, "E2550", {"start": v(-88.03, 56.42) * mm, "mid": v(-88.09, 56.57) * mm, "end": v(-88.13, 56.72) * mm});
            skArc(sketch, "E2551", {"start": v(-88.13, 56.72) * mm, "mid": v(-88.15, 56.84) * mm, "end": v(-88.16, 56.96) * mm});
            skArc(sketch, "E2552", {"start": v(-88.16, 56.96) * mm, "mid": v(-88.15, 57.07) * mm, "end": v(-88.12, 57.19) * mm});
            skArc(sketch, "E2553", {"start": v(-88.12, 57.19) * mm, "mid": v(-88.06, 57.24) * mm, "end": v(-87.99, 57.26) * mm});
            skArc(sketch, "E2554", {"start": v(-87.99, 57.26) * mm, "mid": v(-87.86, 57.22) * mm, "end": v(-87.74, 57.16) * mm});
            skArc(sketch, "E2555", {"start": v(-87.74, 57.16) * mm, "mid": v(-87.43, 56.96) * mm, "end": v(-87.12, 56.76) * mm});
            skArc(sketch, "E2556", {"start": v(-87.12, 56.76) * mm, "mid": v(-86.61, 56.47) * mm, "end": v(-86.08, 56.23) * mm});
            skArc(sketch, "E2557", {"start": v(-86.08, 56.23) * mm, "mid": v(-85.39, 56) * mm, "end": v(-84.69, 55.82) * mm});
            skArc(sketch, "E2558", {"start": v(-84.69, 55.82) * mm, "mid": v(-84.03, 55.68) * mm, "end": v(-83.36, 55.58) * mm});
            skArc(sketch, "E2559", {"start": v(-83.36, 55.58) * mm, "mid": v(-83.07, 55.6) * mm, "end": v(-82.82, 55.76) * mm});
            skArc(sketch, "E2560", {"start": v(-82.82, 55.76) * mm, "mid": v(-82.79, 55.82) * mm, "end": v(-82.78, 55.9) * mm});
            skArc(sketch, "E2561", {"start": v(-82.78, 55.9) * mm, "mid": v(-82.8, 55.98) * mm, "end": v(-82.85, 56.06) * mm});
            skArc(sketch, "E2562", {"start": v(-82.85, 56.06) * mm, "mid": v(-82.94, 56.16) * mm, "end": v(-83.05, 56.25) * mm});
            skArc(sketch, "E2563", {"start": v(-83.05, 56.25) * mm, "mid": v(-83.2, 56.35) * mm, "end": v(-83.36, 56.45) * mm});
            skArc(sketch, "E2564", {"start": v(-83.36, 56.45) * mm, "mid": v(-83.88, 56.75) * mm, "end": v(-84.38, 57.08) * mm});
            skArc(sketch, "E2565", {"start": v(-84.38, 57.08) * mm, "mid": v(-84.77, 57.37) * mm, "end": v(-85.12, 57.7) * mm});
            skArc(sketch, "E2566", {"start": v(-85.12, 57.7) * mm, "mid": v(-85.33, 57.95) * mm, "end": v(-85.5, 58.23) * mm});
            skArc(sketch, "E2567", {"start": v(-85.5, 58.23) * mm, "mid": v(-85.55, 58.42) * mm, "end": v(-85.47, 58.6) * mm});
            skArc(sketch, "E2568", {"start": v(-85.47, 58.6) * mm, "mid": v(-85.4, 58.7) * mm, "end": v(-85.35, 58.8) * mm});
            skArc(sketch, "E2569", {"start": v(-85.35, 58.8) * mm, "mid": v(-85.32, 58.9) * mm, "end": v(-85.32, 59) * mm});
            skArc(sketch, "E2570", {"start": v(-85.32, 59) * mm, "mid": v(-85.34, 59.12) * mm, "end": v(-85.39, 59.23) * mm});
            skArc(sketch, "E2571", {"start": v(-85.39, 59.23) * mm, "mid": v(-85.47, 59.37) * mm, "end": v(-85.56, 59.5) * mm});
            skArc(sketch, "E2572", {"start": v(-85.56, 59.5) * mm, "mid": v(-85.73, 59.76) * mm, "end": v(-85.87, 60.03) * mm});
            skArc(sketch, "E2573", {"start": v(-85.87, 60.03) * mm, "mid": v(-85.94, 60.23) * mm, "end": v(-85.95, 60.44) * mm});
            skArc(sketch, "E2574", {"start": v(-85.95, 60.44) * mm, "mid": v(-85.9, 60.56) * mm, "end": v(-85.79, 60.64) * mm});
            skArc(sketch, "E2575", {"start": v(-85.79, 60.64) * mm, "mid": v(-85.63, 60.66) * mm, "end": v(-85.47, 60.63) * mm});
            skArc(sketch, "E2576", {"start": v(-85.47, 60.63) * mm, "mid": v(-85.32, 60.57) * mm, "end": v(-85.18, 60.52) * mm});
            skArc(sketch, "E2577", {"start": v(-85.18, 60.52) * mm, "mid": v(-84.9, 60.43) * mm, "end": v(-84.61, 60.34) * mm});
            skArc(sketch, "E2578", {"start": v(-84.61, 60.34) * mm, "mid": v(-84.28, 60.24) * mm, "end": v(-83.95, 60.14) * mm});
            skArc(sketch, "E2579", {"start": v(-83.95, 60.14) * mm, "mid": v(-83.6, 60.04) * mm, "end": v(-83.25, 59.94) * mm});
            skArc(sketch, "E2580", {"start": v(-83.25, 59.94) * mm, "mid": v(-82.61, 59.74) * mm, "end": v(-82, 59.52) * mm});
            skArc(sketch, "E2581", {"start": v(-82, 59.52) * mm, "mid": v(-81.55, 59.31) * mm, "end": v(-81.14, 59.06) * mm});
            skArc(sketch, "E2582", {"start": v(-81.14, 59.06) * mm, "mid": v(-80.85, 58.81) * mm, "end": v(-80.61, 58.53) * mm});
            skArc(sketch, "E2583", {"start": v(-80.61, 58.53) * mm, "mid": v(-80.45, 58.23) * mm, "end": v(-80.37, 57.9) * mm});
            skArc(sketch, "E2584", {"start": v(-80.37, 57.9) * mm, "mid": v(-80.34, 57.77) * mm, "end": v(-80.29, 57.65) * mm});
            skArc(sketch, "E2585", {"start": v(-80.29, 57.65) * mm, "mid": v(-80.22, 57.54) * mm, "end": v(-80.14, 57.44) * mm});
            skArc(sketch, "E2586", {"start": v(-80.14, 57.44) * mm, "mid": v(-80.04, 57.36) * mm, "end": v(-79.93, 57.3) * mm});
            skArc(sketch, "E2587", {"start": v(-79.93, 57.3) * mm, "mid": v(-79.8, 57.25) * mm, "end": v(-79.66, 57.22) * mm});
            skArc(sketch, "E2588", {"start": v(-79.66, 57.22) * mm, "mid": v(-79.49, 57.2) * mm, "end": v(-79.32, 57.22) * mm});
            skArc(sketch, "E2589", {"start": v(-79.32, 57.22) * mm, "mid": v(-79.21, 57.26) * mm, "end": v(-79.14, 57.34) * mm});
            skArc(sketch, "E2590", {"start": v(-79.14, 57.34) * mm, "mid": v(-79.08, 57.49) * mm, "end": v(-79.05, 57.64) * mm});
            skArc(sketch, "E2591", {"start": v(-79.05, 57.64) * mm, "mid": v(-79.04, 58.01) * mm, "end": v(-79.04, 58.39) * mm});
            skArc(sketch, "E2592", {"start": v(-79.04, 58.39) * mm, "mid": v(-79.03, 58.8) * mm, "end": v(-79.02, 59.2) * mm});
            skArc(sketch, "E2593", {"start": v(-79.02, 59.2) * mm, "mid": v(-79, 59.34) * mm, "end": v(-78.93, 59.46) * mm});
            skArc(sketch, "E2594", {"start": v(-78.93, 59.46) * mm, "mid": v(-78.84, 59.53) * mm, "end": v(-78.73, 59.55) * mm});
            skArc(sketch, "E2595", {"start": v(-78.73, 59.55) * mm, "mid": v(-78.47, 59.52) * mm, "end": v(-78.2, 59.48) * mm});
            skArc(sketch, "E2596", {"start": v(-78.2, 59.48) * mm, "mid": v(-77.98, 59.43) * mm, "end": v(-77.74, 59.4) * mm});
            skArc(sketch, "E2597", {"start": v(-77.74, 59.4) * mm, "mid": v(-77.63, 59.4) * mm, "end": v(-77.52, 59.45) * mm});
            skArc(sketch, "E2598", {"start": v(-77.52, 59.45) * mm, "mid": v(-77.45, 59.5) * mm, "end": v(-77.41, 59.6) * mm});
            skArc(sketch, "E2599", {"start": v(-77.41, 59.6) * mm, "mid": v(-77.39, 59.76) * mm, "end": v(-77.38, 59.93) * mm});
            skArc(sketch, "E2600", {"start": v(-77.38, 59.93) * mm, "mid": v(-77.39, 60.1) * mm, "end": v(-77.4, 60.25) * mm});
            skArc(sketch, "E2601", {"start": v(-77.4, 60.25) * mm, "mid": v(-77.45, 60.34) * mm, "end": v(-77.51, 60.4) * mm});
            skArc(sketch, "E2602", {"start": v(-77.51, 60.4) * mm, "mid": v(-77.6, 60.45) * mm, "end": v(-77.71, 60.46) * mm});
            skArc(sketch, "E2603", {"start": v(-77.71, 60.46) * mm, "mid": v(-77.9, 60.44) * mm, "end": v(-78.1, 60.41) * mm});
            skArc(sketch, "E2604", {"start": v(-78.1, 60.41) * mm, "mid": v(-78.24, 60.39) * mm, "end": v(-78.39, 60.37) * mm});
            skArc(sketch, "E2605", {"start": v(-78.39, 60.37) * mm, "mid": v(-78.47, 60.37) * mm, "end": v(-78.55, 60.38) * mm});
            skArc(sketch, "E2606", {"start": v(-78.55, 60.38) * mm, "mid": v(-78.58, 60.4) * mm, "end": v(-78.59, 60.45) * mm});
            skArc(sketch, "E2607", {"start": v(-78.59, 60.45) * mm, "mid": v(-78.57, 60.5) * mm, "end": v(-78.54, 60.54) * mm});
            skArc(sketch, "E2608", {"start": v(-78.54, 60.54) * mm, "mid": v(-78.34, 60.68) * mm, "end": v(-78.1, 60.75) * mm});
            skArc(sketch, "E2609", {"start": v(-78.1, 60.75) * mm, "mid": v(-77.83, 60.76) * mm, "end": v(-77.56, 60.7) * mm});
            skArc(sketch, "E2610", {"start": v(-77.56, 60.7) * mm, "mid": v(-77.31, 60.59) * mm, "end": v(-77.1, 60.42) * mm});
            skArc(sketch, "E2611", {"start": v(-77.1, 60.42) * mm, "mid": v(-76.95, 60.23) * mm, "end": v(-76.88, 60) * mm});
            skArc(sketch, "E2612", {"start": v(-76.88, 60) * mm, "mid": v(-76.85, 59.87) * mm, "end": v(-76.8, 59.74) * mm});
            skArc(sketch, "E2613", {"start": v(-76.8, 59.74) * mm, "mid": v(-76.73, 59.6) * mm, "end": v(-76.65, 59.47) * mm});
            skArc(sketch, "E2614", {"start": v(-76.65, 59.47) * mm, "mid": v(-76.56, 59.35) * mm, "end": v(-76.45, 59.24) * mm});
            skArc(sketch, "E2615", {"start": v(-76.45, 59.24) * mm, "mid": v(-76.35, 59.15) * mm, "end": v(-76.23, 59.08) * mm});
            skArc(sketch, "E2616", {"start": v(-76.23, 59.08) * mm, "mid": v(-76.07, 58.99) * mm, "end": v(-75.9, 58.89) * mm});
            skArc(sketch, "E2617", {"start": v(-75.9, 58.89) * mm, "mid": v(-75.85, 58.83) * mm, "end": v(-75.82, 58.75) * mm});
            skArc(sketch, "E2618", {"start": v(-75.82, 58.75) * mm, "mid": v(-75.83, 58.66) * mm, "end": v(-75.87, 58.59) * mm});
            skArc(sketch, "E2619", {"start": v(-75.87, 58.59) * mm, "mid": v(-76, 58.42) * mm, "end": v(-76.15, 58.26) * mm});
            skArc(sketch, "E2620", {"start": v(-76.15, 58.26) * mm, "mid": v(-76.27, 58.1) * mm, "end": v(-76.39, 57.95) * mm});
            skArc(sketch, "E2621", {"start": v(-76.39, 57.95) * mm, "mid": v(-76.45, 57.82) * mm, "end": v(-76.48, 57.68) * mm});
            skArc(sketch, "E2622", {"start": v(-76.48, 57.68) * mm, "mid": v(-76.48, 57.53) * mm, "end": v(-76.45, 57.38) * mm});
            skArc(sketch, "E2623", {"start": v(-76.45, 57.38) * mm, "mid": v(-76.37, 57.14) * mm, "end": v(-76.28, 56.92) * mm});
            skArc(sketch, "E2624", {"start": v(-76.28, 56.92) * mm, "mid": v(-76.17, 56.55) * mm, "end": v(-76.1, 56.17) * mm});
            skArc(sketch, "E2625", {"start": v(-76.1, 56.17) * mm, "mid": v(-76.1, 55.74) * mm, "end": v(-76.13, 55.3) * mm});
            skArc(sketch, "E2626", {"start": v(-76.13, 55.3) * mm, "mid": v(-76.21, 54.86) * mm, "end": v(-76.34, 54.43) * mm});
            skArc(sketch, "E2627", {"start": v(-76.34, 54.43) * mm, "mid": v(-76.51, 54.02) * mm, "end": v(-76.73, 53.63) * mm});
            skArc(sketch, "E2628", {"start": v(-76.73, 53.63) * mm, "mid": v(-76.8, 53.5) * mm, "end": v(-76.87, 53.38) * mm});
            skArc(sketch, "E2629", {"start": v(-76.87, 53.38) * mm, "mid": v(-76.92, 53.25) * mm, "end": v(-76.96, 53.12) * mm});
            skArc(sketch, "E2630", {"start": v(-76.96, 53.12) * mm, "mid": v(-77, 53) * mm, "end": v(-77, 52.9) * mm});
            skArc(sketch, "E2631", {"start": v(-77, 52.9) * mm, "mid": v(-77, 52.83) * mm, "end": v(-76.98, 52.76) * mm});
            skArc(sketch, "E2632", {"start": v(-76.98, 52.76) * mm, "mid": v(-76.88, 52.67) * mm, "end": v(-76.74, 52.63) * mm});
            skArc(sketch, "E2633", {"start": v(-76.74, 52.63) * mm, "mid": v(-76.23, 52.64) * mm, "end": v(-75.73, 52.67) * mm});
            skArc(sketch, "E2634", {"start": v(-75.73, 52.67) * mm, "mid": v(-75.23, 52.7) * mm, "end": v(-74.74, 52.75) * mm});
            skArc(sketch, "E2635", {"start": v(-74.74, 52.75) * mm, "mid": v(-74.54, 52.8) * mm, "end": v(-74.37, 52.9) * mm});
            skArc(sketch, "E2636", {"start": v(-74.37, 52.9) * mm, "mid": v(-74.35, 52.94) * mm, "end": v(-74.35, 52.98) * mm});
            skArc(sketch, "E2637", {"start": v(-74.35, 52.98) * mm, "mid": v(-74.37, 53.1) * mm, "end": v(-74.39, 53.21) * mm});
            skArc(sketch, "E2638", {"start": v(-74.39, 53.21) * mm, "mid": v(-74.42, 53.36) * mm, "end": v(-74.46, 53.5) * mm});
            skArc(sketch, "E2639", {"start": v(-74.46, 53.5) * mm, "mid": v(-74.51, 53.67) * mm, "end": v(-74.57, 53.84) * mm});
            skLineSegment(sketch, "E2640", {"start": v(-74.57, 53.84) * mm, "end": v(-74.86, 54.68) * mm});
            skLineSegment(sketch, "E2641", {"start": v(-74.86, 54.68) * mm, "end": v(-73.36, 54.68) * mm});
            skArc(sketch, "E2642", {"start": v(-73.36, 54.68) * mm, "mid": v(-72.86, 54.7) * mm, "end": v(-72.36, 54.74) * mm});
            skArc(sketch, "E2643", {"start": v(-72.36, 54.74) * mm, "mid": v(-72.1, 54.81) * mm, "end": v(-71.9, 54.96) * mm});
            skArc(sketch, "E2644", {"start": v(-71.9, 54.96) * mm, "mid": v(-71.81, 55.13) * mm, "end": v(-71.85, 55.31) * mm});
            skArc(sketch, "E2645", {"start": v(-71.85, 55.31) * mm, "mid": v(-72.04, 55.57) * mm, "end": v(-72.26, 55.78) * mm});
            skArc(sketch, "E2646", {"start": v(-72.26, 55.78) * mm, "mid": v(-72.35, 55.87) * mm, "end": v(-72.42, 55.96) * mm});
            skArc(sketch, "E2647", {"start": v(-72.42, 55.96) * mm, "mid": v(-72.5, 56.09) * mm, "end": v(-72.56, 56.22) * mm});
            skArc(sketch, "E2648", {"start": v(-72.56, 56.22) * mm, "mid": v(-72.6, 56.36) * mm, "end": v(-72.65, 56.5) * mm});
            skArc(sketch, "E2649", {"start": v(-72.65, 56.5) * mm, "mid": v(-72.67, 56.65) * mm, "end": v(-72.68, 56.79) * mm});
            skArc(sketch, "E2650", {"start": v(-72.68, 56.79) * mm, "mid": v(-72.67, 56.97) * mm, "end": v(-72.64, 57.14) * mm});
            skArc(sketch, "E2651", {"start": v(-72.64, 57.14) * mm, "mid": v(-72.59, 57.25) * mm, "end": v(-72.5, 57.33) * mm});
            skArc(sketch, "E2652", {"start": v(-72.5, 57.33) * mm, "mid": v(-72.37, 57.4) * mm, "end": v(-72.22, 57.42) * mm});
            skArc(sketch, "E2653", {"start": v(-72.22, 57.42) * mm, "mid": v(-71.93, 57.44) * mm, "end": v(-71.64, 57.45) * mm});
            skArc(sketch, "E2654", {"start": v(-71.64, 57.45) * mm, "mid": v(-70.92, 57.48) * mm, "end": v(-70.21, 57.57) * mm});
            skArc(sketch, "E2655", {"start": v(-70.21, 57.57) * mm, "mid": v(-69.34, 57.73) * mm, "end": v(-68.47, 57.92) * mm});
            skArc(sketch, "E2656", {"start": v(-68.47, 57.92) * mm, "mid": v(-67.62, 58.15) * mm, "end": v(-66.79, 58.42) * mm});
            skArc(sketch, "E2657", {"start": v(-66.79, 58.42) * mm, "mid": v(-66.14, 58.67) * mm, "end": v(-65.53, 58.97) * mm});
            skArc(sketch, "E2658", {"start": v(-65.53, 58.97) * mm, "mid": v(-64.74, 59.43) * mm, "end": v(-63.98, 59.93) * mm});
            skArc(sketch, "E2659", {"start": v(-63.98, 59.93) * mm, "mid": v(-63.18, 60.5) * mm, "end": v(-62.42, 61.12) * mm});
            skArc(sketch, "E2660", {"start": v(-62.42, 61.12) * mm, "mid": v(-61.69, 61.76) * mm, "end": v(-60.98, 62.43) * mm});
            skArc(sketch, "E2661", {"start": v(-60.98, 62.43) * mm, "mid": v(-60.38, 63.07) * mm, "end": v(-59.82, 63.74) * mm});
            skArc(sketch, "E2662", {"start": v(-59.82, 63.74) * mm, "mid": v(-59.58, 64.05) * mm, "end": v(-59.35, 64.36) * mm});
            skArc(sketch, "E2663", {"start": v(-59.35, 64.36) * mm, "mid": v(-59.14, 64.64) * mm, "end": v(-58.94, 64.91) * mm});
            skArc(sketch, "E2664", {"start": v(-58.94, 64.91) * mm, "mid": v(-58.78, 65.15) * mm, "end": v(-58.62, 65.4) * mm});
            skArc(sketch, "E2665", {"start": v(-58.62, 65.4) * mm, "mid": v(-58.59, 65.45) * mm, "end": v(-58.58, 65.52) * mm});
            skArc(sketch, "E2666", {"start": v(-58.58, 65.52) * mm, "mid": v(-58.6, 65.57) * mm, "end": v(-58.64, 65.6) * mm});
            skArc(sketch, "E2667", {"start": v(-58.64, 65.6) * mm, "mid": v(-58.81, 65.64) * mm, "end": v(-59, 65.68) * mm});
            skArc(sketch, "E2668", {"start": v(-59, 65.68) * mm, "mid": v(-59.22, 65.72) * mm, "end": v(-59.45, 65.75) * mm});
            skArc(sketch, "E2669", {"start": v(-59.45, 65.75) * mm, "mid": v(-59.72, 65.77) * mm, "end": v(-59.99, 65.8) * mm});
            skLineSegment(sketch, "E2670", {"start": v(-59.99, 65.8) * mm, "end": v(-61.4, 65.88) * mm});
            skLineSegment(sketch, "E2671", {"start": v(-61.4, 65.88) * mm, "end": v(-60.24, 67.2) * mm});
            skLineSegment(sketch, "E2672", {"start": v(-60.24, 67.2) * mm, "end": v(-59.08, 68.5) * mm});
            skLineSegment(sketch, "E2673", {"start": v(-59.08, 68.5) * mm, "end": v(-60.33, 69.81) * mm});
            skArc(sketch, "E2674", {"start": v(-60.33, 69.81) * mm, "mid": v(-60.57, 70.06) * mm, "end": v(-60.8, 70.32) * mm});
            skArc(sketch, "E2675", {"start": v(-60.8, 70.32) * mm, "mid": v(-61, 70.54) * mm, "end": v(-61.19, 70.77) * mm});
            skArc(sketch, "E2676", {"start": v(-61.19, 70.77) * mm, "mid": v(-61.33, 70.95) * mm, "end": v(-61.48, 71.14) * mm});
            skArc(sketch, "E2677", {"start": v(-61.48, 71.14) * mm, "mid": v(-61.5, 71.19) * mm, "end": v(-61.47, 71.23) * mm});
            skArc(sketch, "E2678", {"start": v(-61.47, 71.23) * mm, "mid": v(-61.43, 71.26) * mm, "end": v(-61.38, 71.27) * mm});
            skArc(sketch, "E2679", {"start": v(-61.38, 71.27) * mm, "mid": v(-61.12, 71.29) * mm, "end": v(-60.87, 71.3) * mm});
            skArc(sketch, "E2680", {"start": v(-60.87, 71.3) * mm, "mid": v(-60.57, 71.3) * mm, "end": v(-60.27, 71.3) * mm});
            skArc(sketch, "E2681", {"start": v(-60.27, 71.3) * mm, "mid": v(-59.93, 71.3) * mm, "end": v(-59.58, 71.3) * mm});
            skLineSegment(sketch, "E2682", {"start": v(-59.58, 71.3) * mm, "end": v(-57.8, 71.26) * mm});
            skLineSegment(sketch, "E2683", {"start": v(-57.8, 71.26) * mm, "end": v(-56.93, 73.13) * mm});
            skLineSegment(sketch, "E2684", {"start": v(-56.93, 73.13) * mm, "end": v(-56.05, 75) * mm});
            skLineSegment(sketch, "E2685", {"start": v(-56.05, 75) * mm, "end": v(-55.26, 73.2) * mm});
            skLineSegment(sketch, "E2686", {"start": v(-55.26, 73.2) * mm, "end": v(-54.47, 71.4) * mm});
            skLineSegment(sketch, "E2687", {"start": v(-54.47, 71.4) * mm, "end": v(-52.5, 71.27) * mm});
            skArc(sketch, "E2688", {"start": v(110.37, 71.05) * mm, "mid": v(110.25, 70.06) * mm, "end": v(109.91, 69.12) * mm});
            skArc(sketch, "E2689", {"start": v(109.91, 69.12) * mm, "mid": v(109.28, 68) * mm, "end": v(108.53, 66.96) * mm});
            skArc(sketch, "E2690", {"start": v(108.53, 66.96) * mm, "mid": v(107.64, 65.96) * mm, "end": v(106.64, 65.06) * mm});
            skArc(sketch, "E2691", {"start": v(106.64, 65.06) * mm, "mid": v(105.68, 64.4) * mm, "end": v(104.63, 63.92) * mm});
            skArc(sketch, "E2692", {"start": v(104.63, 63.92) * mm, "mid": v(104.03, 63.7) * mm, "end": v(103.44, 63.45) * mm});
            skArc(sketch, "E2693", {"start": v(103.44, 63.45) * mm, "mid": v(103.23, 63.32) * mm, "end": v(103.07, 63.14) * mm});
            skArc(sketch, "E2694", {"start": v(103.07, 63.14) * mm, "mid": v(103.01, 62.97) * mm, "end": v(103.06, 62.79) * mm});
            skArc(sketch, "E2695", {"start": v(103.06, 62.79) * mm, "mid": v(103.27, 62.5) * mm, "end": v(103.5, 62.22) * mm});
            skArc(sketch, "E2696", {"start": v(103.5, 62.22) * mm, "mid": v(103.76, 61.92) * mm, "end": v(104, 61.62) * mm});
            skArc(sketch, "E2697", {"start": v(104, 61.62) * mm, "mid": v(104.27, 61.2) * mm, "end": v(104.54, 60.78) * mm});
            skArc(sketch, "E2698", {"start": v(104.54, 60.78) * mm, "mid": v(104.78, 60.37) * mm, "end": v(105.02, 59.95) * mm});
            skArc(sketch, "E2699", {"start": v(105.02, 59.95) * mm, "mid": v(105.09, 59.77) * mm, "end": v(105.11, 59.57) * mm});
            skArc(sketch, "E2700", {"start": v(105.11, 59.57) * mm, "mid": v(105.1, 59.54) * mm, "end": v(105.07, 59.52) * mm});
            skArc(sketch, "E2701", {"start": v(105.07, 59.52) * mm, "mid": v(104.9, 59.48) * mm, "end": v(104.73, 59.44) * mm});
            skArc(sketch, "E2702", {"start": v(104.73, 59.44) * mm, "mid": v(104.52, 59.4) * mm, "end": v(104.32, 59.35) * mm});
            skArc(sketch, "E2703", {"start": v(104.32, 59.35) * mm, "mid": v(104.07, 59.31) * mm, "end": v(103.82, 59.28) * mm});
            skArc(sketch, "E2704", {"start": v(103.82, 59.28) * mm, "mid": v(103.3, 59.18) * mm, "end": v(102.78, 59.03) * mm});
            skArc(sketch, "E2705", {"start": v(102.78, 59.03) * mm, "mid": v(102.19, 58.8) * mm, "end": v(101.6, 58.53) * mm});
            skArc(sketch, "E2706", {"start": v(101.6, 58.53) * mm, "mid": v(101.07, 58.24) * mm, "end": v(100.54, 57.92) * mm});
            skArc(sketch, "E2707", {"start": v(100.54, 57.92) * mm, "mid": v(100.19, 57.65) * mm, "end": v(99.88, 57.33) * mm});
            skArc(sketch, "E2708", {"start": v(99.88, 57.33) * mm, "mid": v(99.8, 57.2) * mm, "end": v(99.73, 57.07) * mm});
            skArc(sketch, "E2709", {"start": v(99.73, 57.07) * mm, "mid": v(99.7, 56.95) * mm, "end": v(99.72, 56.82) * mm});
            skArc(sketch, "E2710", {"start": v(99.72, 56.82) * mm, "mid": v(99.78, 56.66) * mm, "end": v(99.87, 56.52) * mm});
            skArc(sketch, "E2711", {"start": v(99.87, 56.52) * mm, "mid": v(100.05, 56.28) * mm, "end": v(100.24, 56.05) * mm});
            skArc(sketch, "E2712", {"start": v(100.24, 56.05) * mm, "mid": v(100.56, 55.64) * mm, "end": v(100.84, 55.21) * mm});
            skArc(sketch, "E2713", {"start": v(100.84, 55.21) * mm, "mid": v(100.95, 54.93) * mm, "end": v(100.95, 54.63) * mm});
            skArc(sketch, "E2714", {"start": v(100.95, 54.63) * mm, "mid": v(100.86, 54.39) * mm, "end": v(100.66, 54.22) * mm});
            skArc(sketch, "E2715", {"start": v(100.66, 54.22) * mm, "mid": v(100.3, 54.07) * mm, "end": v(99.93, 53.98) * mm});
            skArc(sketch, "E2716", {"start": v(99.93, 53.98) * mm, "mid": v(97.46, 53.32) * mm, "end": v(95.17, 52.2) * mm});
            skArc(sketch, "E2717", {"start": v(95.17, 52.2) * mm, "mid": v(92.65, 50.45) * mm, "end": v(90.34, 48.42) * mm});
            skArc(sketch, "E2718", {"start": v(90.34, 48.42) * mm, "mid": v(88.2, 46.08) * mm, "end": v(86.34, 43.52) * mm});
            skArc(sketch, "E2719", {"start": v(86.34, 43.52) * mm, "mid": v(84.98, 41.03) * mm, "end": v(84.02, 38.37) * mm});
            skArc(sketch, "E2720", {"start": v(84.02, 38.37) * mm, "mid": v(83.79, 37.5) * mm, "end": v(83.57, 36.62) * mm});
            skArc(sketch, "E2721", {"start": v(83.57, 36.62) * mm, "mid": v(83.46, 36.1) * mm, "end": v(83.39, 35.57) * mm});
            skArc(sketch, "E2722", {"start": v(83.39, 35.57) * mm, "mid": v(83.38, 35.27) * mm, "end": v(83.41, 34.97) * mm});
            skArc(sketch, "E2723", {"start": v(83.41, 34.97) * mm, "mid": v(83.5, 34.83) * mm, "end": v(83.65, 34.77) * mm});
            skArc(sketch, "E2724", {"start": v(83.65, 34.77) * mm, "mid": v(83.74, 34.78) * mm, "end": v(83.82, 34.81) * mm});
            skArc(sketch, "E2725", {"start": v(83.82, 34.81) * mm, "mid": v(83.91, 34.87) * mm, "end": v(84, 34.93) * mm});
            skArc(sketch, "E2726", {"start": v(84, 34.93) * mm, "mid": v(84.07, 35.02) * mm, "end": v(84.14, 35.1) * mm});
            skArc(sketch, "E2727", {"start": v(84.14, 35.1) * mm, "mid": v(84.2, 35.21) * mm, "end": v(84.23, 35.32) * mm});
            skArc(sketch, "E2728", {"start": v(84.23, 35.32) * mm, "mid": v(84.29, 35.46) * mm, "end": v(84.36, 35.6) * mm});
            skArc(sketch, "E2729", {"start": v(84.36, 35.6) * mm, "mid": v(84.5, 35.82) * mm, "end": v(84.64, 36.04) * mm});
            skArc(sketch, "E2730", {"start": v(84.64, 36.04) * mm, "mid": v(84.8, 36.29) * mm, "end": v(84.98, 36.53) * mm});
            skArc(sketch, "E2731", {"start": v(84.98, 36.53) * mm, "mid": v(85.17, 36.77) * mm, "end": v(85.36, 37) * mm});
            skLineSegment(sketch, "E2732", {"start": v(85.36, 37) * mm, "end": v(86.31, 38.14) * mm});
            skLineSegment(sketch, "E2733", {"start": v(86.31, 38.14) * mm, "end": v(86.48, 37.29) * mm});
            skArc(sketch, "E2734", {"start": v(86.48, 37.29) * mm, "mid": v(86.56, 37.02) * mm, "end": v(86.68, 36.77) * mm});
            skArc(sketch, "E2735", {"start": v(86.68, 36.77) * mm, "mid": v(86.82, 36.59) * mm, "end": v(87.01, 36.45) * mm});
            skArc(sketch, "E2736", {"start": v(87.01, 36.45) * mm, "mid": v(87.15, 36.43) * mm, "end": v(87.28, 36.5) * mm});
            skArc(sketch, "E2737", {"start": v(87.28, 36.5) * mm, "mid": v(87.38, 36.63) * mm, "end": v(87.42, 36.8) * mm});
            skArc(sketch, "E2738", {"start": v(87.42, 36.8) * mm, "mid": v(87.43, 36.9) * mm, "end": v(87.46, 36.98) * mm});
            skArc(sketch, "E2739", {"start": v(87.46, 36.98) * mm, "mid": v(87.54, 37.12) * mm, "end": v(87.62, 37.25) * mm});
            skArc(sketch, "E2740", {"start": v(87.62, 37.25) * mm, "mid": v(87.74, 37.4) * mm, "end": v(87.85, 37.55) * mm});
            skArc(sketch, "E2741", {"start": v(87.85, 37.55) * mm, "mid": v(87.99, 37.7) * mm, "end": v(88.13, 37.83) * mm});
            skArc(sketch, "E2742", {"start": v(88.13, 37.83) * mm, "mid": v(88.34, 38.03) * mm, "end": v(88.56, 38.22) * mm});
            skArc(sketch, "E2743", {"start": v(88.56, 38.22) * mm, "mid": v(88.66, 38.29) * mm, "end": v(88.77, 38.32) * mm});
            skArc(sketch, "E2744", {"start": v(88.77, 38.32) * mm, "mid": v(88.86, 38.32) * mm, "end": v(88.93, 38.27) * mm});
            skArc(sketch, "E2745", {"start": v(88.93, 38.27) * mm, "mid": v(89.03, 38.15) * mm, "end": v(89.1, 38.02) * mm});
            skArc(sketch, "E2746", {"start": v(89.1, 38.02) * mm, "mid": v(89.26, 37.8) * mm, "end": v(89.46, 37.63) * mm});
            skArc(sketch, "E2747", {"start": v(89.46, 37.63) * mm, "mid": v(89.64, 37.58) * mm, "end": v(89.81, 37.64) * mm});
            skArc(sketch, "E2748", {"start": v(89.81, 37.64) * mm, "mid": v(90.02, 37.85) * mm, "end": v(90.16, 38.1) * mm});
            skArc(sketch, "E2749", {"start": v(90.16, 38.1) * mm, "mid": v(90.35, 38.6) * mm, "end": v(90.52, 39.13) * mm});
            skArc(sketch, "E2750", {"start": v(90.52, 39.13) * mm, "mid": v(90.63, 39.47) * mm, "end": v(90.74, 39.8) * mm});
            skArc(sketch, "E2751", {"start": v(90.74, 39.8) * mm, "mid": v(90.88, 40.17) * mm, "end": v(91.03, 40.53) * mm});
            skArc(sketch, "E2752", {"start": v(91.03, 40.53) * mm, "mid": v(91.18, 40.87) * mm, "end": v(91.34, 41.2) * mm});
            skArc(sketch, "E2753", {"start": v(91.34, 41.2) * mm, "mid": v(91.47, 41.45) * mm, "end": v(91.6, 41.68) * mm});
            skLineSegment(sketch, "E2754", {"start": v(91.6, 41.68) * mm, "end": v(92.22, 42.65) * mm});
            skLineSegment(sketch, "E2755", {"start": v(92.22, 42.65) * mm, "end": v(92.5, 41.9) * mm});
            skArc(sketch, "E2756", {"start": v(92.5, 41.9) * mm, "mid": v(92.64, 41.58) * mm, "end": v(92.81, 41.28) * mm});
            skArc(sketch, "E2757", {"start": v(92.81, 41.28) * mm, "mid": v(92.96, 41.18) * mm, "end": v(93.13, 41.2) * mm});
            skArc(sketch, "E2758", {"start": v(93.13, 41.2) * mm, "mid": v(93.32, 41.34) * mm, "end": v(93.45, 41.54) * mm});
            skArc(sketch, "E2759", {"start": v(93.45, 41.54) * mm, "mid": v(93.6, 42.02) * mm, "end": v(93.75, 42.5) * mm});
            skArc(sketch, "E2760", {"start": v(93.75, 42.5) * mm, "mid": v(93.92, 43.06) * mm, "end": v(94.14, 43.6) * mm});
            skArc(sketch, "E2761", {"start": v(94.14, 43.6) * mm, "mid": v(94.46, 44.22) * mm, "end": v(94.8, 44.82) * mm});
            skArc(sketch, "E2762", {"start": v(94.8, 44.82) * mm, "mid": v(95.16, 45.36) * mm, "end": v(95.53, 45.88) * mm});
            skArc(sketch, "E2763", {"start": v(95.53, 45.88) * mm, "mid": v(95.73, 46.05) * mm, "end": v(95.98, 46.1) * mm});
            skArc(sketch, "E2764", {"start": v(95.98, 46.1) * mm, "mid": v(96.05, 46.1) * mm, "end": v(96.1, 46.06) * mm});
            skArc(sketch, "E2765", {"start": v(96.1, 46.06) * mm, "mid": v(96.17, 45.99) * mm, "end": v(96.22, 45.9) * mm});
            skArc(sketch, "E2766", {"start": v(96.22, 45.9) * mm, "mid": v(96.29, 45.8) * mm, "end": v(96.34, 45.68) * mm});
            skArc(sketch, "E2767", {"start": v(96.34, 45.68) * mm, "mid": v(96.39, 45.55) * mm, "end": v(96.43, 45.42) * mm});
            skArc(sketch, "E2768", {"start": v(96.43, 45.42) * mm, "mid": v(96.52, 45.14) * mm, "end": v(96.65, 44.89) * mm});
            skArc(sketch, "E2769", {"start": v(96.65, 44.89) * mm, "mid": v(96.78, 44.78) * mm, "end": v(96.95, 44.76) * mm});
            skArc(sketch, "E2770", {"start": v(96.95, 44.76) * mm, "mid": v(97.15, 44.85) * mm, "end": v(97.29, 45) * mm});
            skArc(sketch, "E2771", {"start": v(97.29, 45) * mm, "mid": v(97.46, 45.33) * mm, "end": v(97.6, 45.67) * mm});
            skArc(sketch, "E2772", {"start": v(97.6, 45.67) * mm, "mid": v(97.79, 46.1) * mm, "end": v(98.04, 46.48) * mm});
            skArc(sketch, "E2773", {"start": v(98.04, 46.48) * mm, "mid": v(98.49, 47.06) * mm, "end": v(98.96, 47.61) * mm});
            skArc(sketch, "E2774", {"start": v(98.96, 47.61) * mm, "mid": v(99.45, 48.15) * mm, "end": v(99.96, 48.67) * mm});
            skArc(sketch, "E2775", {"start": v(99.96, 48.67) * mm, "mid": v(100.17, 48.82) * mm, "end": v(100.43, 48.87) * mm});
            skArc(sketch, "E2776", {"start": v(100.43, 48.87) * mm, "mid": v(100.52, 48.83) * mm, "end": v(100.54, 48.73) * mm});
            skArc(sketch, "E2777", {"start": v(100.54, 48.73) * mm, "mid": v(100.44, 48.36) * mm, "end": v(100.33, 47.99) * mm});
            skArc(sketch, "E2778", {"start": v(100.33, 47.99) * mm, "mid": v(100.12, 47.38) * mm, "end": v(99.9, 46.78) * mm});
            skArc(sketch, "E2779", {"start": v(99.9, 46.78) * mm, "mid": v(99.46, 45.68) * mm, "end": v(99.03, 44.59) * mm});
            skArc(sketch, "E2780", {"start": v(99.03, 44.59) * mm, "mid": v(98.5, 43.22) * mm, "end": v(98, 41.84) * mm});
            skArc(sketch, "E2781", {"start": v(98, 41.84) * mm, "mid": v(97.67, 40.8) * mm, "end": v(97.41, 39.72) * mm});
            skArc(sketch, "E2782", {"start": v(97.41, 39.72) * mm, "mid": v(97.2, 38.6) * mm, "end": v(97.06, 37.49) * mm});
            skArc(sketch, "E2783", {"start": v(97.06, 37.49) * mm, "mid": v(96.92, 35.92) * mm, "end": v(96.82, 34.35) * mm});
            skArc(sketch, "E2784", {"start": v(96.82, 34.35) * mm, "mid": v(96.77, 33.44) * mm, "end": v(96.7, 32.52) * mm});
            skArc(sketch, "E2785", {"start": v(96.7, 32.52) * mm, "mid": v(96.62, 31.6) * mm, "end": v(96.53, 30.68) * mm});
            skArc(sketch, "E2786", {"start": v(96.53, 30.68) * mm, "mid": v(96.43, 29.87) * mm, "end": v(96.33, 29.06) * mm});
            skArc(sketch, "E2787", {"start": v(96.33, 29.06) * mm, "mid": v(96.25, 28.55) * mm, "end": v(96.15, 28.05) * mm});
            skArc(sketch, "E2788", {"start": v(96.15, 28.05) * mm, "mid": v(95.53, 25.98) * mm, "end": v(94.67, 24.01) * mm});
            skArc(sketch, "E2789", {"start": v(94.67, 24.01) * mm, "mid": v(93.68, 22.48) * mm, "end": v(92.4, 21.17) * mm});
            skArc(sketch, "E2790", {"start": v(92.4, 21.17) * mm, "mid": v(91.18, 20.4) * mm, "end": v(89.79, 20) * mm});
            skArc(sketch, "E2791", {"start": v(89.79, 20) * mm, "mid": v(88.46, 20.06) * mm, "end": v(87.24, 20.58) * mm});
            skArc(sketch, "E2792", {"start": v(87.24, 20.58) * mm, "mid": v(86.9, 20.85) * mm, "end": v(86.63, 21.18) * mm});
            skArc(sketch, "E2793", {"start": v(86.63, 21.18) * mm, "mid": v(86.27, 21.74) * mm, "end": v(85.94, 22.32) * mm});
            skArc(sketch, "E2794", {"start": v(85.94, 22.32) * mm, "mid": v(85.64, 22.92) * mm, "end": v(85.37, 23.54) * mm});
            skArc(sketch, "E2795", {"start": v(85.37, 23.54) * mm, "mid": v(85.25, 23.96) * mm, "end": v(85.2, 24.4) * mm});
            skArc(sketch, "E2796", {"start": v(85.2, 24.4) * mm, "mid": v(85.18, 24.65) * mm, "end": v(85.13, 24.89) * mm});
            skArc(sketch, "E2797", {"start": v(85.13, 24.89) * mm, "mid": v(85.05, 25.12) * mm, "end": v(84.94, 25.34) * mm});
            skArc(sketch, "E2798", {"start": v(84.94, 25.34) * mm, "mid": v(84.84, 25.48) * mm, "end": v(84.7, 25.6) * mm});
            skArc(sketch, "E2799", {"start": v(84.7, 25.6) * mm, "mid": v(84.6, 25.64) * mm, "end": v(84.5, 25.6) * mm});
            skArc(sketch, "E2800", {"start": v(84.5, 25.6) * mm, "mid": v(84.46, 25.53) * mm, "end": v(84.42, 25.46) * mm});
            skArc(sketch, "E2801", {"start": v(84.42, 25.46) * mm, "mid": v(84.34, 25.23) * mm, "end": v(84.26, 25) * mm});
            skArc(sketch, "E2802", {"start": v(84.26, 25) * mm, "mid": v(84.17, 24.73) * mm, "end": v(84.1, 24.45) * mm});
            skArc(sketch, "E2803", {"start": v(84.1, 24.45) * mm, "mid": v(84, 24.14) * mm, "end": v(83.92, 23.82) * mm});
            skArc(sketch, "E2804", {"start": v(83.92, 23.82) * mm, "mid": v(83.7, 23.05) * mm, "end": v(83.43, 22.28) * mm});
            skArc(sketch, "E2805", {"start": v(83.43, 22.28) * mm, "mid": v(83.14, 21.59) * mm, "end": v(82.8, 20.9) * mm});
            skArc(sketch, "E2806", {"start": v(82.8, 20.9) * mm, "mid": v(82.46, 20.3) * mm, "end": v(82.07, 19.72) * mm});
            skArc(sketch, "E2807", {"start": v(82.07, 19.72) * mm, "mid": v(81.67, 19.22) * mm, "end": v(81.23, 18.76) * mm});
            skArc(sketch, "E2808", {"start": v(81.23, 18.76) * mm, "mid": v(80.95, 18.5) * mm, "end": v(80.65, 18.27) * mm});
            skArc(sketch, "E2809", {"start": v(80.65, 18.27) * mm, "mid": v(80.41, 18.1) * mm, "end": v(80.15, 17.97) * mm});
            skArc(sketch, "E2810", {"start": v(80.15, 17.97) * mm, "mid": v(79.87, 17.87) * mm, "end": v(79.58, 17.8) * mm});
            skArc(sketch, "E2811", {"start": v(79.58, 17.8) * mm, "mid": v(79.18, 17.73) * mm, "end": v(78.78, 17.7) * mm});
            skArc(sketch, "E2812", {"start": v(78.78, 17.7) * mm, "mid": v(78.4, 17.67) * mm, "end": v(78, 17.66) * mm});
            skArc(sketch, "E2813", {"start": v(78, 17.66) * mm, "mid": v(77.74, 17.67) * mm, "end": v(77.47, 17.7) * mm});
            skArc(sketch, "E2814", {"start": v(77.47, 17.7) * mm, "mid": v(77.25, 17.77) * mm, "end": v(77.05, 17.86) * mm});
            skArc(sketch, "E2815", {"start": v(77.05, 17.86) * mm, "mid": v(76.83, 17.98) * mm, "end": v(76.63, 18.13) * mm});
            skArc(sketch, "E2816", {"start": v(76.63, 18.13) * mm, "mid": v(76.43, 18.32) * mm, "end": v(76.25, 18.53) * mm});
            skArc(sketch, "E2817", {"start": v(76.25, 18.53) * mm, "mid": v(76.13, 18.73) * mm, "end": v(76.05, 18.96) * mm});
            skArc(sketch, "E2818", {"start": v(76.05, 18.96) * mm, "mid": v(75.99, 19.28) * mm, "end": v(75.96, 19.61) * mm});
            skArc(sketch, "E2819", {"start": v(75.96, 19.61) * mm, "mid": v(75.95, 20.3) * mm, "end": v(75.94, 21) * mm});
            skArc(sketch, "E2820", {"start": v(75.94, 21) * mm, "mid": v(75.95, 21.6) * mm, "end": v(75.96, 22.2) * mm});
            skArc(sketch, "E2821", {"start": v(75.96, 22.2) * mm, "mid": v(75.98, 22.55) * mm, "end": v(76.03, 22.9) * mm});
            skArc(sketch, "E2822", {"start": v(76.03, 22.9) * mm, "mid": v(76.09, 23.13) * mm, "end": v(76.17, 23.36) * mm});
            skArc(sketch, "E2823", {"start": v(76.17, 23.36) * mm, "mid": v(76.27, 23.51) * mm, "end": v(76.4, 23.64) * mm});
            skArc(sketch, "E2824", {"start": v(76.4, 23.64) * mm, "mid": v(76.5, 23.73) * mm, "end": v(76.6, 23.82) * mm});
            skArc(sketch, "E2825", {"start": v(76.6, 23.82) * mm, "mid": v(76.68, 23.94) * mm, "end": v(76.76, 24.07) * mm});
            skArc(sketch, "E2826", {"start": v(76.76, 24.07) * mm, "mid": v(76.83, 24.2) * mm, "end": v(76.9, 24.35) * mm});
            skArc(sketch, "E2827", {"start": v(76.9, 24.35) * mm, "mid": v(76.93, 24.48) * mm, "end": v(76.96, 24.61) * mm});
            skArc(sketch, "E2828", {"start": v(76.96, 24.61) * mm, "mid": v(77, 24.76) * mm, "end": v(77.04, 24.9) * mm});
            skArc(sketch, "E2829", {"start": v(77.04, 24.9) * mm, "mid": v(77.11, 25.01) * mm, "end": v(77.2, 25.1) * mm});
            skArc(sketch, "E2830", {"start": v(77.2, 25.1) * mm, "mid": v(77.32, 25.19) * mm, "end": v(77.45, 25.24) * mm});
            skArc(sketch, "E2831", {"start": v(77.45, 25.24) * mm, "mid": v(77.63, 25.29) * mm, "end": v(77.8, 25.32) * mm});
            skArc(sketch, "E2832", {"start": v(77.8, 25.32) * mm, "mid": v(78.12, 25.4) * mm, "end": v(78.4, 25.57) * mm});
            skArc(sketch, "E2833", {"start": v(78.4, 25.57) * mm, "mid": v(78.56, 25.78) * mm, "end": v(78.61, 26.05) * mm});
            skArc(sketch, "E2834", {"start": v(78.61, 26.05) * mm, "mid": v(78.54, 26.35) * mm, "end": v(78.37, 26.6) * mm});
            skArc(sketch, "E2835", {"start": v(78.37, 26.6) * mm, "mid": v(78.07, 26.85) * mm, "end": v(77.74, 27.03) * mm});
            skArc(sketch, "E2836", {"start": v(77.74, 27.03) * mm, "mid": v(77.54, 27.12) * mm, "end": v(77.36, 27.23) * mm});
            skArc(sketch, "E2837", {"start": v(77.36, 27.23) * mm, "mid": v(77.14, 27.38) * mm, "end": v(76.92, 27.54) * mm});
            skArc(sketch, "E2838", {"start": v(76.92, 27.54) * mm, "mid": v(76.7, 27.72) * mm, "end": v(76.48, 27.9) * mm});
            skArc(sketch, "E2839", {"start": v(76.48, 27.9) * mm, "mid": v(76.3, 28.08) * mm, "end": v(76.11, 28.27) * mm});
            skArc(sketch, "E2840", {"start": v(76.11, 28.27) * mm, "mid": v(75.76, 28.72) * mm, "end": v(75.45, 29.2) * mm});
            skArc(sketch, "E2841", {"start": v(75.45, 29.2) * mm, "mid": v(74.94, 30.13) * mm, "end": v(74.44, 31.06) * mm});
            skArc(sketch, "E2842", {"start": v(74.44, 31.06) * mm, "mid": v(73.95, 32.03) * mm, "end": v(73.47, 33) * mm});
            skArc(sketch, "E2843", {"start": v(73.47, 33) * mm, "mid": v(73.35, 33.32) * mm, "end": v(73.31, 33.66) * mm});
            skArc(sketch, "E2844", {"start": v(73.31, 33.66) * mm, "mid": v(73.28, 33.81) * mm, "end": v(73.19, 33.94) * mm});
            skArc(sketch, "E2845", {"start": v(73.19, 33.94) * mm, "mid": v(73.04, 34.03) * mm, "end": v(72.88, 34.05) * mm});
            skArc(sketch, "E2846", {"start": v(72.88, 34.05) * mm, "mid": v(72.6, 34.02) * mm, "end": v(72.33, 33.95) * mm});
            skArc(sketch, "E2847", {"start": v(72.33, 33.95) * mm, "mid": v(71.9, 33.78) * mm, "end": v(71.48, 33.6) * mm});
            skArc(sketch, "E2848", {"start": v(71.48, 33.6) * mm, "mid": v(71.05, 33.43) * mm, "end": v(70.61, 33.28) * mm});
            skArc(sketch, "E2849", {"start": v(70.61, 33.28) * mm, "mid": v(70.17, 33.17) * mm, "end": v(69.72, 33.09) * mm});
            skArc(sketch, "E2850", {"start": v(69.72, 33.09) * mm, "mid": v(69.12, 33.02) * mm, "end": v(68.51, 32.98) * mm});
            skArc(sketch, "E2851", {"start": v(68.51, 32.98) * mm, "mid": v(67.53, 32.94) * mm, "end": v(66.54, 32.91) * mm});
            skArc(sketch, "E2852", {"start": v(66.54, 32.91) * mm, "mid": v(65.37, 32.89) * mm, "end": v(64.2, 32.85) * mm});
            skArc(sketch, "E2853", {"start": v(64.2, 32.85) * mm, "mid": v(63.8, 32.82) * mm, "end": v(63.4, 32.76) * mm});
            skArc(sketch, "E2854", {"start": v(63.4, 32.76) * mm, "mid": v(63.18, 32.69) * mm, "end": v(63, 32.56) * mm});
            skArc(sketch, "E2855", {"start": v(63, 32.56) * mm, "mid": v(62.86, 32.38) * mm, "end": v(62.77, 32.17) * mm});
            skArc(sketch, "E2856", {"start": v(62.77, 32.17) * mm, "mid": v(62.66, 31.82) * mm, "end": v(62.52, 31.47) * mm});
            skArc(sketch, "E2857", {"start": v(62.52, 31.47) * mm, "mid": v(62.31, 31.06) * mm, "end": v(62.09, 30.66) * mm});
            skArc(sketch, "E2858", {"start": v(62.09, 30.66) * mm, "mid": v(61.86, 30.3) * mm, "end": v(61.62, 29.93) * mm});
            skArc(sketch, "E2859", {"start": v(61.62, 29.93) * mm, "mid": v(61.51, 29.83) * mm, "end": v(61.36, 29.8) * mm});
            skArc(sketch, "E2860", {"start": v(61.36, 29.8) * mm, "mid": v(61.3, 29.77) * mm, "end": v(61.28, 29.72) * mm});
            skArc(sketch, "E2861", {"start": v(61.28, 29.72) * mm, "mid": v(61.24, 29.4) * mm, "end": v(61.21, 29.1) * mm});
            skArc(sketch, "E2862", {"start": v(61.21, 29.1) * mm, "mid": v(61.18, 28.71) * mm, "end": v(61.16, 28.33) * mm});
            skArc(sketch, "E2863", {"start": v(61.16, 28.33) * mm, "mid": v(61.15, 27.87) * mm, "end": v(61.15, 27.41) * mm});
            skArc(sketch, "E2864", {"start": v(61.15, 27.41) * mm, "mid": v(61.15, 26.7) * mm, "end": v(61.16, 26) * mm});
            skArc(sketch, "E2865", {"start": v(61.16, 26) * mm, "mid": v(61.18, 25.72) * mm, "end": v(61.23, 25.45) * mm});
            skArc(sketch, "E2866", {"start": v(61.23, 25.45) * mm, "mid": v(61.28, 25.33) * mm, "end": v(61.38, 25.25) * mm});
            skArc(sketch, "E2867", {"start": v(61.38, 25.25) * mm, "mid": v(61.5, 25.21) * mm, "end": v(61.63, 25.24) * mm});
            skArc(sketch, "E2868", {"start": v(61.63, 25.24) * mm, "mid": v(62.75, 25.68) * mm, "end": v(63.89, 26.1) * mm});
            skArc(sketch, "E2869", {"start": v(63.89, 26.1) * mm, "mid": v(64.8, 26.36) * mm, "end": v(65.73, 26.57) * mm});
            skArc(sketch, "E2870", {"start": v(65.73, 26.57) * mm, "mid": v(66.58, 26.69) * mm, "end": v(67.43, 26.73) * mm});
            skArc(sketch, "E2871", {"start": v(67.43, 26.73) * mm, "mid": v(68.35, 26.71) * mm, "end": v(69.26, 26.63) * mm});
            skLineSegment(sketch, "E2872", {"start": v(69.26, 26.63) * mm, "end": v(70.78, 26.44) * mm});
            skLineSegment(sketch, "E2873", {"start": v(70.78, 26.44) * mm, "end": v(69.02, 24.68) * mm});
            skArc(sketch, "E2874", {"start": v(69.02, 24.68) * mm, "mid": v(68.46, 24.1) * mm, "end": v(67.92, 23.48) * mm});
            skArc(sketch, "E2875", {"start": v(67.92, 23.48) * mm, "mid": v(67.44, 22.87) * mm, "end": v(66.98, 22.24) * mm});
            skArc(sketch, "E2876", {"start": v(66.98, 22.24) * mm, "mid": v(66.63, 21.69) * mm, "end": v(66.3, 21.12) * mm});
            skArc(sketch, "E2877", {"start": v(66.3, 21.12) * mm, "mid": v(66.17, 20.78) * mm, "end": v(66.12, 20.42) * mm});
            skArc(sketch, "E2878", {"start": v(66.12, 20.42) * mm, "mid": v(66.15, 20.35) * mm, "end": v(66.22, 20.31) * mm});
            skArc(sketch, "E2879", {"start": v(66.22, 20.31) * mm, "mid": v(66.43, 20.28) * mm, "end": v(66.65, 20.27) * mm});
            skArc(sketch, "E2880", {"start": v(66.65, 20.27) * mm, "mid": v(66.95, 20.26) * mm, "end": v(67.25, 20.26) * mm});
            skArc(sketch, "E2881", {"start": v(67.25, 20.26) * mm, "mid": v(67.66, 20.28) * mm, "end": v(68.06, 20.31) * mm});
            skArc(sketch, "E2882", {"start": v(68.06, 20.31) * mm, "mid": v(68.43, 20.34) * mm, "end": v(68.8, 20.36) * mm});
            skArc(sketch, "E2883", {"start": v(68.8, 20.36) * mm, "mid": v(69.11, 20.37) * mm, "end": v(69.43, 20.38) * mm});
            skArc(sketch, "E2884", {"start": v(69.43, 20.38) * mm, "mid": v(69.68, 20.37) * mm, "end": v(69.94, 20.37) * mm});
            skArc(sketch, "E2885", {"start": v(69.94, 20.37) * mm, "mid": v(69.98, 20.35) * mm, "end": v(70, 20.3) * mm});
            skArc(sketch, "E2886", {"start": v(70, 20.3) * mm, "mid": v(69.99, 20.24) * mm, "end": v(69.96, 20.19) * mm});
            skArc(sketch, "E2887", {"start": v(69.96, 20.19) * mm, "mid": v(69.8, 19.9) * mm, "end": v(69.64, 19.63) * mm});
            skArc(sketch, "E2888", {"start": v(69.64, 19.63) * mm, "mid": v(69.44, 19.3) * mm, "end": v(69.24, 18.98) * mm});
            skArc(sketch, "E2889", {"start": v(69.24, 18.98) * mm, "mid": v(69, 18.6) * mm, "end": v(68.77, 18.24) * mm});
            skArc(sketch, "E2890", {"start": v(68.77, 18.24) * mm, "mid": v(68.35, 17.55) * mm, "end": v(67.96, 16.85) * mm});
            skArc(sketch, "E2891", {"start": v(67.96, 16.85) * mm, "mid": v(67.6, 16.09) * mm, "end": v(67.25, 15.32) * mm});
            skArc(sketch, "E2892", {"start": v(67.25, 15.32) * mm, "mid": v(66.95, 14.53) * mm, "end": v(66.68, 13.73) * mm});
            skArc(sketch, "E2893", {"start": v(66.68, 13.73) * mm, "mid": v(66.46, 12.95) * mm, "end": v(66.27, 12.17) * mm});
            skArc(sketch, "E2894", {"start": v(66.27, 12.17) * mm, "mid": v(66.22, 11.85) * mm, "end": v(66.2, 11.52) * mm});
            skArc(sketch, "E2895", {"start": v(66.2, 11.52) * mm, "mid": v(66.26, 11.37) * mm, "end": v(66.4, 11.29) * mm});
            skArc(sketch, "E2896", {"start": v(66.4, 11.29) * mm, "mid": v(66.62, 11.28) * mm, "end": v(66.82, 11.36) * mm});
            skArc(sketch, "E2897", {"start": v(66.82, 11.36) * mm, "mid": v(67.23, 11.63) * mm, "end": v(67.62, 11.9) * mm});
            skArc(sketch, "E2898", {"start": v(67.62, 11.9) * mm, "mid": v(68.44, 12.48) * mm, "end": v(69.3, 13) * mm});
            skArc(sketch, "E2899", {"start": v(69.3, 13) * mm, "mid": v(70.35, 13.58) * mm, "end": v(71.42, 14.11) * mm});
            skArc(sketch, "E2900", {"start": v(71.42, 14.11) * mm, "mid": v(72.48, 14.6) * mm, "end": v(73.56, 15.04) * mm});
            skArc(sketch, "E2901", {"start": v(73.56, 15.04) * mm, "mid": v(74.4, 15.33) * mm, "end": v(75.28, 15.56) * mm});
            skArc(sketch, "E2902", {"start": v(75.28, 15.56) * mm, "mid": v(75.54, 15.62) * mm, "end": v(75.81, 15.66) * mm});
            skArc(sketch, "E2903", {"start": v(75.81, 15.66) * mm, "mid": v(75.9, 15.66) * mm, "end": v(76, 15.63) * mm});
            skArc(sketch, "E2904", {"start": v(76, 15.63) * mm, "mid": v(76.05, 15.57) * mm, "end": v(76.07, 15.5) * mm});
            skArc(sketch, "E2905", {"start": v(76.07, 15.5) * mm, "mid": v(76.04, 15.3) * mm, "end": v(76, 15.13) * mm});
            skArc(sketch, "E2906", {"start": v(76, 15.13) * mm, "mid": v(75.94, 14.81) * mm, "end": v(75.92, 14.49) * mm});
            skArc(sketch, "E2907", {"start": v(75.92, 14.49) * mm, "mid": v(75.94, 14.11) * mm, "end": v(76, 13.74) * mm});
            skArc(sketch, "E2908", {"start": v(76, 13.74) * mm, "mid": v(76.07, 13.41) * mm, "end": v(76.17, 13.1) * mm});
            skArc(sketch, "E2909", {"start": v(76.17, 13.1) * mm, "mid": v(76.26, 12.97) * mm, "end": v(76.4, 12.93) * mm});
            skArc(sketch, "E2910", {"start": v(76.4, 12.93) * mm, "mid": v(76.5, 12.94) * mm, "end": v(76.57, 12.97) * mm});
            skArc(sketch, "E2911", {"start": v(76.57, 12.97) * mm, "mid": v(76.77, 13.1) * mm, "end": v(76.97, 13.24) * mm});
            skArc(sketch, "E2912", {"start": v(76.97, 13.24) * mm, "mid": v(77.21, 13.41) * mm, "end": v(77.45, 13.6) * mm});
            skArc(sketch, "E2913", {"start": v(77.45, 13.6) * mm, "mid": v(77.7, 13.8) * mm, "end": v(77.96, 14) * mm});
            skArc(sketch, "E2914", {"start": v(77.96, 14) * mm, "mid": v(78.46, 14.39) * mm, "end": v(78.97, 14.75) * mm});
            skArc(sketch, "E2915", {"start": v(78.97, 14.75) * mm, "mid": v(79.66, 15.19) * mm, "end": v(80.37, 15.6) * mm});
            skArc(sketch, "E2916", {"start": v(80.37, 15.6) * mm, "mid": v(81.06, 16) * mm, "end": v(81.76, 16.39) * mm});
            skArc(sketch, "E2917", {"start": v(81.76, 16.39) * mm, "mid": v(82.02, 16.49) * mm, "end": v(82.3, 16.52) * mm});
            skArc(sketch, "E2918", {"start": v(82.3, 16.52) * mm, "mid": v(82.33, 16.5) * mm, "end": v(82.35, 16.47) * mm});
            skArc(sketch, "E2919", {"start": v(82.35, 16.47) * mm, "mid": v(82.35, 16.34) * mm, "end": v(82.35, 16.2) * mm});
            skArc(sketch, "E2920", {"start": v(82.35, 16.2) * mm, "mid": v(82.34, 16.02) * mm, "end": v(82.33, 15.85) * mm});
            skArc(sketch, "E2921", {"start": v(82.33, 15.85) * mm, "mid": v(82.3, 15.64) * mm, "end": v(82.27, 15.43) * mm});
            skArc(sketch, "E2922", {"start": v(82.27, 15.43) * mm, "mid": v(82.18, 14.8) * mm, "end": v(82.12, 14.16) * mm});
            skArc(sketch, "E2923", {"start": v(82.12, 14.16) * mm, "mid": v(82.18, 13.93) * mm, "end": v(82.35, 13.78) * mm});
            skArc(sketch, "E2924", {"start": v(82.35, 13.78) * mm, "mid": v(82.58, 13.74) * mm, "end": v(82.8, 13.83) * mm});
            skArc(sketch, "E2925", {"start": v(82.8, 13.83) * mm, "mid": v(83.33, 14.25) * mm, "end": v(83.85, 14.7) * mm});
            skArc(sketch, "E2926", {"start": v(83.85, 14.7) * mm, "mid": v(84.42, 15.18) * mm, "end": v(85.03, 15.62) * mm});
            skArc(sketch, "E2927", {"start": v(85.03, 15.62) * mm, "mid": v(85.8, 16.1) * mm, "end": v(86.57, 16.57) * mm});
            skArc(sketch, "E2928", {"start": v(86.57, 16.57) * mm, "mid": v(87.35, 16.98) * mm, "end": v(88.13, 17.35) * mm});
            skArc(sketch, "E2929", {"start": v(88.13, 17.35) * mm, "mid": v(88.73, 17.6) * mm, "end": v(89.35, 17.77) * mm});
            skArc(sketch, "E2930", {"start": v(89.35, 17.77) * mm, "mid": v(89.56, 17.8) * mm, "end": v(89.77, 17.83) * mm});
            skArc(sketch, "E2931", {"start": v(89.77, 17.83) * mm, "mid": v(89.87, 17.8) * mm, "end": v(89.94, 17.74) * mm});
            skArc(sketch, "E2932", {"start": v(89.94, 17.74) * mm, "mid": v(89.99, 17.61) * mm, "end": v(90, 17.48) * mm});
            skArc(sketch, "E2933", {"start": v(90, 17.48) * mm, "mid": v(89.98, 17.08) * mm, "end": v(89.95, 16.67) * mm});
            skArc(sketch, "E2934", {"start": v(89.95, 16.67) * mm, "mid": v(89.93, 16.43) * mm, "end": v(89.92, 16.2) * mm});
            skArc(sketch, "E2935", {"start": v(89.92, 16.2) * mm, "mid": v(89.92, 15.99) * mm, "end": v(89.93, 15.79) * mm});
            skArc(sketch, "E2936", {"start": v(89.93, 15.79) * mm, "mid": v(89.95, 15.63) * mm, "end": v(89.97, 15.48) * mm});
            skArc(sketch, "E2937", {"start": v(89.97, 15.48) * mm, "mid": v(90, 15.43) * mm, "end": v(90.04, 15.42) * mm});
            skArc(sketch, "E2938", {"start": v(90.04, 15.42) * mm, "mid": v(90.1, 15.43) * mm, "end": v(90.17, 15.46) * mm});
            skArc(sketch, "E2939", {"start": v(90.17, 15.46) * mm, "mid": v(90.37, 15.61) * mm, "end": v(90.57, 15.77) * mm});
            skArc(sketch, "E2940", {"start": v(90.57, 15.77) * mm, "mid": v(90.81, 15.96) * mm, "end": v(91.05, 16.16) * mm});
            skArc(sketch, "E2941", {"start": v(91.05, 16.16) * mm, "mid": v(91.31, 16.38) * mm, "end": v(91.57, 16.62) * mm});
            skArc(sketch, "E2942", {"start": v(91.57, 16.62) * mm, "mid": v(92.13, 17.08) * mm, "end": v(92.72, 17.51) * mm});
            skArc(sketch, "E2943", {"start": v(92.72, 17.51) * mm, "mid": v(93.54, 18.04) * mm, "end": v(94.37, 18.55) * mm});
            skArc(sketch, "E2944", {"start": v(94.37, 18.55) * mm, "mid": v(95.2, 19.02) * mm, "end": v(96.05, 19.47) * mm});
            skArc(sketch, "E2945", {"start": v(96.05, 19.47) * mm, "mid": v(96.65, 19.74) * mm, "end": v(97.27, 19.96) * mm});
            skArc(sketch, "E2946", {"start": v(97.27, 19.96) * mm, "mid": v(97.45, 20) * mm, "end": v(97.63, 20.04) * mm});
            skArc(sketch, "E2947", {"start": v(97.63, 20.04) * mm, "mid": v(97.7, 20.02) * mm, "end": v(97.73, 19.97) * mm});
            skArc(sketch, "E2948", {"start": v(97.73, 19.97) * mm, "mid": v(97.74, 19.87) * mm, "end": v(97.73, 19.77) * mm});
            skArc(sketch, "E2949", {"start": v(97.73, 19.77) * mm, "mid": v(97.61, 19.43) * mm, "end": v(97.5, 19.09) * mm});
            skArc(sketch, "E2950", {"start": v(97.5, 19.09) * mm, "mid": v(97.29, 18.46) * mm, "end": v(97.13, 17.83) * mm});
            skArc(sketch, "E2951", {"start": v(97.13, 17.83) * mm, "mid": v(97.12, 17.49) * mm, "end": v(97.24, 17.17) * mm});
            skArc(sketch, "E2952", {"start": v(97.24, 17.17) * mm, "mid": v(97.43, 17.03) * mm, "end": v(97.66, 17.07) * mm});
            skArc(sketch, "E2953", {"start": v(97.66, 17.07) * mm, "mid": v(98.03, 17.34) * mm, "end": v(98.36, 17.66) * mm});
            skArc(sketch, "E2954", {"start": v(98.36, 17.66) * mm, "mid": v(98.72, 18) * mm, "end": v(99.12, 18.29) * mm});
            skArc(sketch, "E2955", {"start": v(99.12, 18.29) * mm, "mid": v(99.94, 18.8) * mm, "end": v(100.78, 19.28) * mm});
            skArc(sketch, "E2956", {"start": v(100.78, 19.28) * mm, "mid": v(101.64, 19.76) * mm, "end": v(102.5, 20.22) * mm});
            skArc(sketch, "E2957", {"start": v(102.5, 20.22) * mm, "mid": v(102.83, 20.34) * mm, "end": v(103.18, 20.39) * mm});
            skArc(sketch, "E2958", {"start": v(103.18, 20.39) * mm, "mid": v(103.29, 20.37) * mm, "end": v(103.38, 20.33) * mm});
            skArc(sketch, "E2959", {"start": v(103.38, 20.33) * mm, "mid": v(103.45, 20.25) * mm, "end": v(103.5, 20.16) * mm});
            skArc(sketch, "E2960", {"start": v(103.5, 20.16) * mm, "mid": v(103.53, 20) * mm, "end": v(103.53, 19.84) * mm});
            skArc(sketch, "E2961", {"start": v(103.53, 19.84) * mm, "mid": v(103.52, 19.56) * mm, "end": v(103.5, 19.29) * mm});
            skArc(sketch, "E2962", {"start": v(103.5, 19.29) * mm, "mid": v(103.47, 18.88) * mm, "end": v(103.47, 18.46) * mm});
            skArc(sketch, "E2963", {"start": v(103.47, 18.46) * mm, "mid": v(103.52, 18.32) * mm, "end": v(103.66, 18.24) * mm});
            skArc(sketch, "E2964", {"start": v(103.66, 18.24) * mm, "mid": v(103.84, 18.25) * mm, "end": v(104, 18.33) * mm});
            skArc(sketch, "E2965", {"start": v(104, 18.33) * mm, "mid": v(104.36, 18.68) * mm, "end": v(104.71, 19.05) * mm});
            skArc(sketch, "E2966", {"start": v(104.71, 19.05) * mm, "mid": v(105.1, 19.41) * mm, "end": v(105.53, 19.74) * mm});
            skArc(sketch, "E2967", {"start": v(105.53, 19.74) * mm, "mid": v(106.13, 20.12) * mm, "end": v(106.74, 20.47) * mm});
            skArc(sketch, "E2968", {"start": v(106.74, 20.47) * mm, "mid": v(107.35, 20.78) * mm, "end": v(107.98, 21.06) * mm});
            skArc(sketch, "E2969", {"start": v(107.98, 21.06) * mm, "mid": v(108.36, 21.18) * mm, "end": v(108.77, 21.22) * mm});
            skArc(sketch, "E2970", {"start": v(108.77, 21.22) * mm, "mid": v(108.89, 21.21) * mm, "end": v(109, 21.19) * mm});
            skArc(sketch, "E2971", {"start": v(109, 21.19) * mm, "mid": v(109.07, 21.15) * mm, "end": v(109.1, 21.09) * mm});
            skArc(sketch, "E2972", {"start": v(109.1, 21.09) * mm, "mid": v(109.12, 21) * mm, "end": v(109.1, 20.9) * mm});
            skArc(sketch, "E2973", {"start": v(109.1, 20.9) * mm, "mid": v(109.04, 20.7) * mm, "end": v(108.98, 20.51) * mm});
            skArc(sketch, "E2974", {"start": v(108.98, 20.51) * mm, "mid": v(108.83, 20.1) * mm, "end": v(108.72, 19.67) * mm});
            skArc(sketch, "E2975", {"start": v(108.72, 19.67) * mm, "mid": v(108.69, 19.4) * mm, "end": v(108.72, 19.14) * mm});
            skArc(sketch, "E2976", {"start": v(108.72, 19.14) * mm, "mid": v(108.82, 18.97) * mm, "end": v(108.98, 18.84) * mm});
            skArc(sketch, "E2977", {"start": v(108.98, 18.84) * mm, "mid": v(109.22, 18.76) * mm, "end": v(109.47, 18.73) * mm});
            skArc(sketch, "E2978", {"start": v(109.47, 18.73) * mm, "mid": v(109.92, 18.71) * mm, "end": v(110.38, 18.65) * mm});
            skArc(sketch, "E2979", {"start": v(110.38, 18.65) * mm, "mid": v(110.91, 18.53) * mm, "end": v(111.44, 18.39) * mm});
            skArc(sketch, "E2980", {"start": v(111.44, 18.39) * mm, "mid": v(111.97, 18.21) * mm, "end": v(112.5, 18) * mm});
            skArc(sketch, "E2981", {"start": v(112.5, 18) * mm, "mid": v(112.95, 17.8) * mm, "end": v(113.4, 17.55) * mm});
            skLineSegment(sketch, "E2982", {"start": v(113.4, 17.55) * mm, "end": v(114.34, 16.96) * mm});
            skLineSegment(sketch, "E2983", {"start": v(114.34, 16.96) * mm, "end": v(113.53, 16.62) * mm});
            skArc(sketch, "E2984", {"start": v(113.53, 16.62) * mm, "mid": v(113.32, 16.54) * mm, "end": v(113.1, 16.48) * mm});
            skArc(sketch, "E2985", {"start": v(113.1, 16.48) * mm, "mid": v(112.8, 16.42) * mm, "end": v(112.49, 16.37) * mm});
            skArc(sketch, "E2986", {"start": v(112.49, 16.37) * mm, "mid": v(112.14, 16.32) * mm, "end": v(111.8, 16.29) * mm});
            skArc(sketch, "E2987", {"start": v(111.8, 16.29) * mm, "mid": v(111.46, 16.27) * mm, "end": v(111.13, 16.26) * mm});
            skArc(sketch, "E2988", {"start": v(111.13, 16.26) * mm, "mid": v(110.74, 16.25) * mm, "end": v(110.35, 16.23) * mm});
            skArc(sketch, "E2989", {"start": v(110.35, 16.23) * mm, "mid": v(110.11, 16.2) * mm, "end": v(109.88, 16.16) * mm});
            skArc(sketch, "E2990", {"start": v(109.88, 16.16) * mm, "mid": v(109.75, 16.11) * mm, "end": v(109.63, 16.04) * mm});
            skArc(sketch, "E2991", {"start": v(109.63, 16.04) * mm, "mid": v(109.56, 15.95) * mm, "end": v(109.54, 15.85) * mm});
            skArc(sketch, "E2992", {"start": v(109.54, 15.85) * mm, "mid": v(109.54, 15.76) * mm, "end": v(109.56, 15.68) * mm});
            skArc(sketch, "E2993", {"start": v(109.56, 15.68) * mm, "mid": v(109.58, 15.6) * mm, "end": v(109.62, 15.52) * mm});
            skArc(sketch, "E2994", {"start": v(109.62, 15.52) * mm, "mid": v(109.66, 15.44) * mm, "end": v(109.7, 15.37) * mm});
            skArc(sketch, "E2995", {"start": v(109.7, 15.37) * mm, "mid": v(109.76, 15.32) * mm, "end": v(109.81, 15.28) * mm});
            skArc(sketch, "E2996", {"start": v(109.81, 15.28) * mm, "mid": v(109.94, 15.17) * mm, "end": v(110.03, 15.02) * mm});
            skArc(sketch, "E2997", {"start": v(110.03, 15.02) * mm, "mid": v(110.02, 14.9) * mm, "end": v(109.93, 14.82) * mm});
            skArc(sketch, "E2998", {"start": v(109.93, 14.82) * mm, "mid": v(109.65, 14.76) * mm, "end": v(109.36, 14.74) * mm});
            skArc(sketch, "E2999", {"start": v(109.36, 14.74) * mm, "mid": v(108.83, 14.76) * mm, "end": v(108.3, 14.8) * mm});
            skArc(sketch, "E3000", {"start": v(108.3, 14.8) * mm, "mid": v(107.67, 14.84) * mm, "end": v(107.05, 14.87) * mm});
            skArc(sketch, "E3001", {"start": v(107.05, 14.87) * mm, "mid": v(106.83, 14.84) * mm, "end": v(106.63, 14.76) * mm});
            skArc(sketch, "E3002", {"start": v(106.63, 14.76) * mm, "mid": v(106.55, 14.64) * mm, "end": v(106.57, 14.5) * mm});
            skArc(sketch, "E3003", {"start": v(106.57, 14.5) * mm, "mid": v(106.75, 14.23) * mm, "end": v(106.96, 13.98) * mm});
            skArc(sketch, "E3004", {"start": v(106.96, 13.98) * mm, "mid": v(107.08, 13.81) * mm, "end": v(107.17, 13.63) * mm});
            skArc(sketch, "E3005", {"start": v(107.17, 13.63) * mm, "mid": v(107.27, 13.36) * mm, "end": v(107.35, 13.08) * mm});
            skArc(sketch, "E3006", {"start": v(107.35, 13.08) * mm, "mid": v(107.43, 12.72) * mm, "end": v(107.49, 12.36) * mm});
            skArc(sketch, "E3007", {"start": v(107.49, 12.36) * mm, "mid": v(107.54, 11.91) * mm, "end": v(107.58, 11.47) * mm});
            skArc(sketch, "E3008", {"start": v(107.58, 11.47) * mm, "mid": v(107.63, 10.88) * mm, "end": v(107.7, 10.3) * mm});
            skArc(sketch, "E3009", {"start": v(107.7, 10.3) * mm, "mid": v(107.74, 10.03) * mm, "end": v(107.81, 9.78) * mm});
            skArc(sketch, "E3010", {"start": v(107.81, 9.78) * mm, "mid": v(107.9, 9.63) * mm, "end": v(108.02, 9.52) * mm});
            skArc(sketch, "E3011", {"start": v(108.02, 9.52) * mm, "mid": v(108.18, 9.43) * mm, "end": v(108.36, 9.38) * mm});
            skArc(sketch, "E3012", {"start": v(108.36, 9.38) * mm, "mid": v(108.59, 9.34) * mm, "end": v(108.8, 9.27) * mm});
            skArc(sketch, "E3013", {"start": v(108.8, 9.27) * mm, "mid": v(108.9, 9.2) * mm, "end": v(108.95, 9.08) * mm});
            skArc(sketch, "E3014", {"start": v(108.95, 9.08) * mm, "mid": v(108.93, 8.93) * mm, "end": v(108.86, 8.8) * mm});
            skArc(sketch, "E3015", {"start": v(108.86, 8.8) * mm, "mid": v(108.65, 8.58) * mm, "end": v(108.43, 8.37) * mm});
            skArc(sketch, "E3016", {"start": v(108.43, 8.37) * mm, "mid": v(108.32, 8.26) * mm, "end": v(108.22, 8.15) * mm});
            skArc(sketch, "E3017", {"start": v(108.22, 8.15) * mm, "mid": v(108.12, 8.03) * mm, "end": v(108.04, 7.91) * mm});
            skArc(sketch, "E3018", {"start": v(108.04, 7.91) * mm, "mid": v(107.97, 7.8) * mm, "end": v(107.91, 7.7) * mm});
            skArc(sketch, "E3019", {"start": v(107.91, 7.7) * mm, "mid": v(107.89, 7.62) * mm, "end": v(107.88, 7.54) * mm});
            skArc(sketch, "E3020", {"start": v(107.88, 7.54) * mm, "mid": v(107.87, 7.45) * mm, "end": v(107.84, 7.38) * mm});
            skArc(sketch, "E3021", {"start": v(107.84, 7.38) * mm, "mid": v(107.78, 7.26) * mm, "end": v(107.71, 7.16) * mm});
            skArc(sketch, "E3022", {"start": v(107.71, 7.16) * mm, "mid": v(107.63, 7.04) * mm, "end": v(107.54, 6.92) * mm});
            skArc(sketch, "E3023", {"start": v(107.54, 6.92) * mm, "mid": v(107.43, 6.81) * mm, "end": v(107.32, 6.7) * mm});
            skArc(sketch, "E3024", {"start": v(107.32, 6.7) * mm, "mid": v(107.22, 6.62) * mm, "end": v(107.1, 6.53) * mm});
            skArc(sketch, "E3025", {"start": v(107.1, 6.53) * mm, "mid": v(107.02, 6.48) * mm, "end": v(106.93, 6.44) * mm});
            skArc(sketch, "E3026", {"start": v(106.93, 6.44) * mm, "mid": v(106.87, 6.43) * mm, "end": v(106.82, 6.45) * mm});
            skArc(sketch, "E3027", {"start": v(106.82, 6.45) * mm, "mid": v(106.78, 6.48) * mm, "end": v(106.77, 6.52) * mm});
            skArc(sketch, "E3028", {"start": v(106.77, 6.52) * mm, "mid": v(106.78, 6.59) * mm, "end": v(106.8, 6.65) * mm});
            skArc(sketch, "E3029", {"start": v(106.8, 6.65) * mm, "mid": v(106.82, 6.7) * mm, "end": v(106.85, 6.75) * mm});
            skArc(sketch, "E3030", {"start": v(106.85, 6.75) * mm, "mid": v(106.9, 6.79) * mm, "end": v(106.94, 6.82) * mm});
            skArc(sketch, "E3031", {"start": v(106.94, 6.82) * mm, "mid": v(107, 6.84) * mm, "end": v(107.05, 6.84) * mm});
            skArc(sketch, "E3032", {"start": v(107.05, 6.84) * mm, "mid": v(107.1, 6.86) * mm, "end": v(107.15, 6.89) * mm});
            skArc(sketch, "E3033", {"start": v(107.15, 6.89) * mm, "mid": v(107.2, 6.94) * mm, "end": v(107.24, 7) * mm});
            skArc(sketch, "E3034", {"start": v(107.24, 7) * mm, "mid": v(107.28, 7.1) * mm, "end": v(107.3, 7.19) * mm});
            skArc(sketch, "E3035", {"start": v(107.3, 7.19) * mm, "mid": v(107.32, 7.3) * mm, "end": v(107.32, 7.4) * mm});
            skArc(sketch, "E3036", {"start": v(107.32, 7.4) * mm, "mid": v(107.29, 7.59) * mm, "end": v(107.18, 7.75) * mm});
            skArc(sketch, "E3037", {"start": v(107.18, 7.75) * mm, "mid": v(107.01, 7.88) * mm, "end": v(106.82, 7.95) * mm});
            skArc(sketch, "E3038", {"start": v(106.82, 7.95) * mm, "mid": v(106.6, 7.96) * mm, "end": v(106.38, 7.91) * mm});
            skArc(sketch, "E3039", {"start": v(106.38, 7.91) * mm, "mid": v(106.2, 7.8) * mm, "end": v(106.06, 7.64) * mm});
            skArc(sketch, "E3040", {"start": v(106.06, 7.64) * mm, "mid": v(105.97, 7.57) * mm, "end": v(105.85, 7.56) * mm});
            skArc(sketch, "E3041", {"start": v(105.85, 7.56) * mm, "mid": v(105.72, 7.62) * mm, "end": v(105.63, 7.73) * mm});
            skArc(sketch, "E3042", {"start": v(105.63, 7.73) * mm, "mid": v(105.52, 7.97) * mm, "end": v(105.45, 8.22) * mm});
            skArc(sketch, "E3043", {"start": v(105.45, 8.22) * mm, "mid": v(105.4, 8.53) * mm, "end": v(105.4, 8.85) * mm});
            skArc(sketch, "E3044", {"start": v(105.4, 8.85) * mm, "mid": v(105.36, 9.15) * mm, "end": v(105.28, 9.44) * mm});
            skArc(sketch, "E3045", {"start": v(105.28, 9.44) * mm, "mid": v(105.16, 9.56) * mm, "end": v(104.99, 9.56) * mm});
            skArc(sketch, "E3046", {"start": v(104.99, 9.56) * mm, "mid": v(104.75, 9.4) * mm, "end": v(104.56, 9.18) * mm});
            skArc(sketch, "E3047", {"start": v(104.56, 9.18) * mm, "mid": v(104.3, 8.73) * mm, "end": v(104.07, 8.26) * mm});
            skArc(sketch, "E3048", {"start": v(104.07, 8.26) * mm, "mid": v(103.8, 7.74) * mm, "end": v(103.5, 7.24) * mm});
            skArc(sketch, "E3049", {"start": v(103.5, 7.24) * mm, "mid": v(103.19, 6.87) * mm, "end": v(102.83, 6.55) * mm});
            skArc(sketch, "E3050", {"start": v(102.83, 6.55) * mm, "mid": v(102.39, 6.26) * mm, "end": v(101.91, 6.05) * mm});
            skArc(sketch, "E3051", {"start": v(101.91, 6.05) * mm, "mid": v(101.22, 5.8) * mm, "end": v(100.52, 5.6) * mm});
            skArc(sketch, "E3052", {"start": v(100.52, 5.6) * mm, "mid": v(100.18, 5.51) * mm, "end": v(99.85, 5.4) * mm});
            skArc(sketch, "E3053", {"start": v(99.85, 5.4) * mm, "mid": v(99.5, 5.29) * mm, "end": v(99.14, 5.15) * mm});
            skArc(sketch, "E3054", {"start": v(99.14, 5.15) * mm, "mid": v(98.81, 5.02) * mm, "end": v(98.5, 4.89) * mm});
            skArc(sketch, "E3055", {"start": v(98.5, 4.89) * mm, "mid": v(98.25, 4.77) * mm, "end": v(98.02, 4.65) * mm});
            skArc(sketch, "E3056", {"start": v(98.02, 4.65) * mm, "mid": v(97.85, 4.55) * mm, "end": v(97.67, 4.46) * mm});
            skArc(sketch, "E3057", {"start": v(97.67, 4.46) * mm, "mid": v(97.52, 4.4) * mm, "end": v(97.37, 4.34) * mm});
            skArc(sketch, "E3058", {"start": v(97.37, 4.34) * mm, "mid": v(97.26, 4.32) * mm, "end": v(97.16, 4.31) * mm});
            skArc(sketch, "E3059", {"start": v(97.16, 4.31) * mm, "mid": v(97.11, 4.33) * mm, "end": v(97.1, 4.38) * mm});
            skArc(sketch, "E3060", {"start": v(97.1, 4.38) * mm, "mid": v(97.12, 4.63) * mm, "end": v(97.2, 4.87) * mm});
            skArc(sketch, "E3061", {"start": v(97.2, 4.87) * mm, "mid": v(97.39, 5.22) * mm, "end": v(97.6, 5.57) * mm});
            skArc(sketch, "E3062", {"start": v(97.6, 5.57) * mm, "mid": v(97.85, 5.95) * mm, "end": v(98.13, 6.31) * mm});
            skArc(sketch, "E3063", {"start": v(98.13, 6.31) * mm, "mid": v(98.42, 6.65) * mm, "end": v(98.73, 6.97) * mm});
            skArc(sketch, "E3064", {"start": v(98.73, 6.97) * mm, "mid": v(99.05, 7.28) * mm, "end": v(99.35, 7.6) * mm});
            skArc(sketch, "E3065", {"start": v(99.35, 7.6) * mm, "mid": v(99.47, 7.76) * mm, "end": v(99.54, 7.95) * mm});
            skArc(sketch, "E3066", {"start": v(99.54, 7.95) * mm, "mid": v(99.52, 8.07) * mm, "end": v(99.43, 8.15) * mm});
            skArc(sketch, "E3067", {"start": v(99.43, 8.15) * mm, "mid": v(99.22, 8.2) * mm, "end": v(99, 8.23) * mm});
            skArc(sketch, "E3068", {"start": v(99, 8.23) * mm, "mid": v(98.86, 8.24) * mm, "end": v(98.7, 8.26) * mm});
            skArc(sketch, "E3069", {"start": v(98.7, 8.26) * mm, "mid": v(98.62, 8.3) * mm, "end": v(98.57, 8.37) * mm});
            skArc(sketch, "E3070", {"start": v(98.57, 8.37) * mm, "mid": v(98.53, 8.48) * mm, "end": v(98.53, 8.6) * mm});
            skArc(sketch, "E3071", {"start": v(98.53, 8.6) * mm, "mid": v(98.57, 8.83) * mm, "end": v(98.61, 9.06) * mm});
            skArc(sketch, "E3072", {"start": v(98.61, 9.06) * mm, "mid": v(98.64, 9.21) * mm, "end": v(98.67, 9.37) * mm});
            skArc(sketch, "E3073", {"start": v(98.67, 9.37) * mm, "mid": v(98.68, 9.5) * mm, "end": v(98.68, 9.64) * mm});
            skArc(sketch, "E3074", {"start": v(98.68, 9.64) * mm, "mid": v(98.67, 9.74) * mm, "end": v(98.65, 9.83) * mm});
            skArc(sketch, "E3075", {"start": v(98.65, 9.83) * mm, "mid": v(98.62, 9.87) * mm, "end": v(98.58, 9.89) * mm});
            skArc(sketch, "E3076", {"start": v(98.58, 9.89) * mm, "mid": v(98.5, 9.87) * mm, "end": v(98.44, 9.84) * mm});
            skArc(sketch, "E3077", {"start": v(98.44, 9.84) * mm, "mid": v(98.26, 9.7) * mm, "end": v(98.07, 9.54) * mm});
            skArc(sketch, "E3078", {"start": v(98.07, 9.54) * mm, "mid": v(97.86, 9.36) * mm, "end": v(97.64, 9.17) * mm});
            skArc(sketch, "E3079", {"start": v(97.64, 9.17) * mm, "mid": v(97.4, 8.95) * mm, "end": v(97.17, 8.72) * mm});
            skLineSegment(sketch, "E3080", {"start": v(97.17, 8.72) * mm, "end": v(95.99, 7.56) * mm});
            skLineSegment(sketch, "E3081", {"start": v(95.99, 7.56) * mm, "end": v(95.99, 8.55) * mm});
            skArc(sketch, "E3082", {"start": v(95.99, 8.55) * mm, "mid": v(95.98, 8.78) * mm, "end": v(95.96, 9) * mm});
            skArc(sketch, "E3083", {"start": v(95.96, 9) * mm, "mid": v(95.93, 9.18) * mm, "end": v(95.87, 9.34) * mm});
            skArc(sketch, "E3084", {"start": v(95.87, 9.34) * mm, "mid": v(95.81, 9.47) * mm, "end": v(95.73, 9.58) * mm});
            skArc(sketch, "E3085", {"start": v(95.73, 9.58) * mm, "mid": v(95.64, 9.67) * mm, "end": v(95.54, 9.72) * mm});
            skArc(sketch, "E3086", {"start": v(95.54, 9.72) * mm, "mid": v(95.45, 9.78) * mm, "end": v(95.4, 9.86) * mm});
            skArc(sketch, "E3087", {"start": v(95.4, 9.86) * mm, "mid": v(95.38, 9.95) * mm, "end": v(95.41, 10.03) * mm});
            skArc(sketch, "E3088", {"start": v(95.41, 10.03) * mm, "mid": v(95.53, 10.17) * mm, "end": v(95.66, 10.29) * mm});
            skArc(sketch, "E3089", {"start": v(95.66, 10.29) * mm, "mid": v(95.94, 10.5) * mm, "end": v(96.23, 10.72) * mm});
            skArc(sketch, "E3090", {"start": v(96.23, 10.72) * mm, "mid": v(96.45, 10.89) * mm, "end": v(96.67, 11.06) * mm});
            skArc(sketch, "E3091", {"start": v(96.67, 11.06) * mm, "mid": v(96.85, 11.22) * mm, "end": v(97.03, 11.39) * mm});
            skArc(sketch, "E3092", {"start": v(97.03, 11.39) * mm, "mid": v(97.18, 11.53) * mm, "end": v(97.31, 11.67) * mm});
            skArc(sketch, "E3093", {"start": v(97.31, 11.67) * mm, "mid": v(97.35, 11.74) * mm, "end": v(97.37, 11.82) * mm});
            skArc(sketch, "E3094", {"start": v(97.37, 11.82) * mm, "mid": v(97.3, 12) * mm, "end": v(97.13, 12.07) * mm});
            skArc(sketch, "E3095", {"start": v(97.13, 12.07) * mm, "mid": v(96.53, 12.1) * mm, "end": v(95.93, 12.08) * mm});
            skArc(sketch, "E3096", {"start": v(95.93, 12.08) * mm, "mid": v(95.25, 12.04) * mm, "end": v(94.57, 11.96) * mm});
            skArc(sketch, "E3097", {"start": v(94.57, 11.96) * mm, "mid": v(93.95, 11.84) * mm, "end": v(93.34, 11.68) * mm});
            skArc(sketch, "E3098", {"start": v(93.34, 11.68) * mm, "mid": v(92.62, 11.46) * mm, "end": v(91.9, 11.21) * mm});
            skArc(sketch, "E3099", {"start": v(91.9, 11.21) * mm, "mid": v(91.69, 11.08) * mm, "end": v(91.53, 10.89) * mm});
            skArc(sketch, "E3100", {"start": v(91.53, 10.89) * mm, "mid": v(91.49, 10.67) * mm, "end": v(91.55, 10.45) * mm});
            skArc(sketch, "E3101", {"start": v(91.55, 10.45) * mm, "mid": v(91.88, 9.96) * mm, "end": v(92.23, 9.49) * mm});
            skArc(sketch, "E3102", {"start": v(92.23, 9.49) * mm, "mid": v(92.51, 9.1) * mm, "end": v(92.79, 8.72) * mm});
            skArc(sketch, "E3103", {"start": v(92.79, 8.72) * mm, "mid": v(92.96, 8.44) * mm, "end": v(93.12, 8.15) * mm});
            skArc(sketch, "E3104", {"start": v(93.12, 8.15) * mm, "mid": v(93.19, 7.98) * mm, "end": v(93.23, 7.8) * mm});
            skArc(sketch, "E3105", {"start": v(93.23, 7.8) * mm, "mid": v(93.21, 7.71) * mm, "end": v(93.13, 7.67) * mm});
            skArc(sketch, "E3106", {"start": v(93.13, 7.67) * mm, "mid": v(93.1, 7.68) * mm, "end": v(93.06, 7.68) * mm});
            skArc(sketch, "E3107", {"start": v(93.06, 7.68) * mm, "mid": v(92.74, 7.76) * mm, "end": v(92.43, 7.84) * mm});
            skArc(sketch, "E3108", {"start": v(92.43, 7.84) * mm, "mid": v(92.07, 7.92) * mm, "end": v(91.7, 8.01) * mm});
            skArc(sketch, "E3109", {"start": v(91.7, 8.01) * mm, "mid": v(91.29, 8.12) * mm, "end": v(90.87, 8.23) * mm});
            skArc(sketch, "E3110", {"start": v(90.87, 8.23) * mm, "mid": v(90.41, 8.34) * mm, "end": v(89.95, 8.44) * mm});
            skArc(sketch, "E3111", {"start": v(89.95, 8.44) * mm, "mid": v(89.47, 8.53) * mm, "end": v(88.98, 8.62) * mm});
            skArc(sketch, "E3112", {"start": v(88.98, 8.62) * mm, "mid": v(88.54, 8.68) * mm, "end": v(88.1, 8.74) * mm});
            skArc(sketch, "E3113", {"start": v(88.1, 8.74) * mm, "mid": v(87.79, 8.77) * mm, "end": v(87.48, 8.78) * mm});
            skArc(sketch, "E3114", {"start": v(87.48, 8.78) * mm, "mid": v(87.1, 8.78) * mm, "end": v(86.73, 8.77) * mm});
            skArc(sketch, "E3115", {"start": v(86.73, 8.77) * mm, "mid": v(86.59, 8.74) * mm, "end": v(86.46, 8.69) * mm});
            skArc(sketch, "E3116", {"start": v(86.46, 8.69) * mm, "mid": v(86.39, 8.61) * mm, "end": v(86.36, 8.51) * mm});
            skArc(sketch, "E3117", {"start": v(86.36, 8.51) * mm, "mid": v(86.38, 8.33) * mm, "end": v(86.42, 8.16) * mm});
            skArc(sketch, "E3118", {"start": v(86.42, 8.16) * mm, "mid": v(86.46, 8.01) * mm, "end": v(86.5, 7.86) * mm});
            skArc(sketch, "E3119", {"start": v(86.5, 7.86) * mm, "mid": v(86.55, 7.67) * mm, "end": v(86.6, 7.48) * mm});
            skArc(sketch, "E3120", {"start": v(86.6, 7.48) * mm, "mid": v(86.65, 7.28) * mm, "end": v(86.7, 7.08) * mm});
            skArc(sketch, "E3121", {"start": v(86.7, 7.08) * mm, "mid": v(86.74, 6.9) * mm, "end": v(86.77, 6.73) * mm});
            skArc(sketch, "E3122", {"start": v(86.77, 6.73) * mm, "mid": v(86.82, 6.49) * mm, "end": v(86.87, 6.24) * mm});
            skArc(sketch, "E3123", {"start": v(86.87, 6.24) * mm, "mid": v(86.86, 6.16) * mm, "end": v(86.82, 6.08) * mm});
            skArc(sketch, "E3124", {"start": v(86.82, 6.08) * mm, "mid": v(86.76, 6.03) * mm, "end": v(86.68, 6.03) * mm});
            skArc(sketch, "E3125", {"start": v(86.68, 6.03) * mm, "mid": v(86.48, 6.07) * mm, "end": v(86.28, 6.13) * mm});
            skArc(sketch, "E3126", {"start": v(86.28, 6.13) * mm, "mid": v(86.09, 6.18) * mm, "end": v(85.89, 6.21) * mm});
            skArc(sketch, "E3127", {"start": v(85.89, 6.21) * mm, "mid": v(85.5, 6.26) * mm, "end": v(85.1, 6.31) * mm});
            skArc(sketch, "E3128", {"start": v(85.1, 6.31) * mm, "mid": v(84.65, 6.36) * mm, "end": v(84.18, 6.4) * mm});
            skArc(sketch, "E3129", {"start": v(84.18, 6.4) * mm, "mid": v(83.7, 6.45) * mm, "end": v(83.22, 6.48) * mm});
            skLineSegment(sketch, "E3130", {"start": v(83.22, 6.48) * mm, "end": v(80.81, 6.64) * mm});
            skLineSegment(sketch, "E3131", {"start": v(80.81, 6.64) * mm, "end": v(80.73, 5.3) * mm});
            skArc(sketch, "E3132", {"start": v(80.73, 5.3) * mm, "mid": v(80.7, 4.91) * mm, "end": v(80.66, 4.53) * mm});
            skArc(sketch, "E3133", {"start": v(80.66, 4.53) * mm, "mid": v(80.62, 4.34) * mm, "end": v(80.54, 4.16) * mm});
            skArc(sketch, "E3134", {"start": v(80.54, 4.16) * mm, "mid": v(80.46, 4.04) * mm, "end": v(80.34, 3.96) * mm});
            skArc(sketch, "E3135", {"start": v(80.34, 3.96) * mm, "mid": v(80.17, 3.89) * mm, "end": v(79.99, 3.85) * mm});
            skArc(sketch, "E3136", {"start": v(79.99, 3.85) * mm, "mid": v(79.8, 3.81) * mm, "end": v(79.63, 3.76) * mm});
            skArc(sketch, "E3137", {"start": v(79.63, 3.76) * mm, "mid": v(79.53, 3.7) * mm, "end": v(79.46, 3.6) * mm});
            skArc(sketch, "E3138", {"start": v(79.46, 3.6) * mm, "mid": v(79.43, 3.46) * mm, "end": v(79.42, 3.31) * mm});
            skArc(sketch, "E3139", {"start": v(79.42, 3.31) * mm, "mid": v(79.46, 2.99) * mm, "end": v(79.5, 2.66) * mm});
            skArc(sketch, "E3140", {"start": v(79.5, 2.66) * mm, "mid": v(79.54, 2.43) * mm, "end": v(79.56, 2.2) * mm});
            skArc(sketch, "E3141", {"start": v(79.56, 2.2) * mm, "mid": v(79.56, 1.96) * mm, "end": v(79.55, 1.72) * mm});
            skArc(sketch, "E3142", {"start": v(79.55, 1.72) * mm, "mid": v(79.52, 1.5) * mm, "end": v(79.49, 1.3) * mm});
            skArc(sketch, "E3143", {"start": v(79.49, 1.3) * mm, "mid": v(79.44, 1.15) * mm, "end": v(79.38, 1) * mm});
            skArc(sketch, "E3144", {"start": v(79.38, 1) * mm, "mid": v(79.24, 0.81) * mm, "end": v(79.05, 0.68) * mm});
            skArc(sketch, "E3145", {"start": v(79.05, 0.68) * mm, "mid": v(78.89, 0.66) * mm, "end": v(78.76, 0.76) * mm});
            skArc(sketch, "E3146", {"start": v(78.76, 0.76) * mm, "mid": v(78.63, 1.05) * mm, "end": v(78.56, 1.36) * mm});
            skArc(sketch, "E3147", {"start": v(78.56, 1.36) * mm, "mid": v(78.53, 1.88) * mm, "end": v(78.53, 2.4) * mm});
            skArc(sketch, "E3148", {"start": v(78.53, 2.4) * mm, "mid": v(78.53, 2.8) * mm, "end": v(78.53, 3.2) * mm});
            skArc(sketch, "E3149", {"start": v(78.53, 3.2) * mm, "mid": v(78.5, 3.38) * mm, "end": v(78.46, 3.56) * mm});
            skArc(sketch, "E3150", {"start": v(78.46, 3.56) * mm, "mid": v(78.4, 3.67) * mm, "end": v(78.3, 3.74) * mm});
            skArc(sketch, "E3151", {"start": v(78.3, 3.74) * mm, "mid": v(78.16, 3.79) * mm, "end": v(78, 3.8) * mm});
            skArc(sketch, "E3152", {"start": v(78, 3.8) * mm, "mid": v(77.87, 3.82) * mm, "end": v(77.73, 3.86) * mm});
            skArc(sketch, "E3153", {"start": v(77.73, 3.86) * mm, "mid": v(77.63, 3.92) * mm, "end": v(77.56, 4.02) * mm});
            skArc(sketch, "E3154", {"start": v(77.56, 4.02) * mm, "mid": v(77.5, 4.17) * mm, "end": v(77.48, 4.33) * mm});
            skArc(sketch, "E3155", {"start": v(77.48, 4.33) * mm, "mid": v(77.47, 4.64) * mm, "end": v(77.46, 4.94) * mm});
            skLineSegment(sketch, "E3156", {"start": v(77.46, 4.94) * mm, "end": v(77.46, 6.09) * mm});
            skLineSegment(sketch, "E3157", {"start": v(77.46, 6.09) * mm, "end": v(76.47, 5.93) * mm});
            skArc(sketch, "E3158", {"start": v(76.47, 5.93) * mm, "mid": v(76.03, 5.83) * mm, "end": v(75.6, 5.7) * mm});
            skArc(sketch, "E3159", {"start": v(75.6, 5.7) * mm, "mid": v(75.05, 5.5) * mm, "end": v(74.52, 5.27) * mm});
            skArc(sketch, "E3160", {"start": v(74.52, 5.27) * mm, "mid": v(73.98, 5.02) * mm, "end": v(73.45, 4.74) * mm});
            skArc(sketch, "E3161", {"start": v(73.45, 4.74) * mm, "mid": v(73.04, 4.5) * mm, "end": v(72.64, 4.21) * mm});
            skArc(sketch, "E3162", {"start": v(72.64, 4.21) * mm, "mid": v(72.48, 4.08) * mm, "end": v(72.34, 3.94) * mm});
            skArc(sketch, "E3163", {"start": v(72.34, 3.94) * mm, "mid": v(72.29, 3.85) * mm, "end": v(72.28, 3.75) * mm});
            skArc(sketch, "E3164", {"start": v(72.28, 3.75) * mm, "mid": v(72.33, 3.62) * mm, "end": v(72.4, 3.5) * mm});
            skArc(sketch, "E3165", {"start": v(72.4, 3.5) * mm, "mid": v(72.66, 3.23) * mm, "end": v(72.91, 2.96) * mm});
            skArc(sketch, "E3166", {"start": v(72.91, 2.96) * mm, "mid": v(73.18, 2.67) * mm, "end": v(73.43, 2.36) * mm});
            skArc(sketch, "E3167", {"start": v(73.43, 2.36) * mm, "mid": v(73.5, 2.2) * mm, "end": v(73.47, 2.05) * mm});
            skArc(sketch, "E3168", {"start": v(73.47, 2.05) * mm, "mid": v(73.36, 1.88) * mm, "end": v(73.2, 1.76) * mm});
            skArc(sketch, "E3169", {"start": v(73.2, 1.76) * mm, "mid": v(72.64, 1.44) * mm, "end": v(72.07, 1.12) * mm});
            skArc(sketch, "E3170", {"start": v(72.07, 1.12) * mm, "mid": v(71.06, 0.53) * mm, "end": v(70.09, -0.14) * mm});
            skArc(sketch, "E3171", {"start": v(70.09, -0.14) * mm, "mid": v(69.2, -0.86) * mm, "end": v(68.38, -1.65) * mm});
            skArc(sketch, "E3172", {"start": v(68.38, -1.65) * mm, "mid": v(67.7, -2.42) * mm, "end": v(67.1, -3.25) * mm});
            skArc(sketch, "E3173", {"start": v(67.1, -3.25) * mm, "mid": v(66.66, -4) * mm, "end": v(66.35, -4.82) * mm});
            skArc(sketch, "E3174", {"start": v(66.35, -4.82) * mm, "mid": v(66.23, -5.27) * mm, "end": v(66.13, -5.72) * mm});
            skArc(sketch, "E3175", {"start": v(66.13, -5.72) * mm, "mid": v(66.15, -5.9) * mm, "end": v(66.27, -6.04) * mm});
            skArc(sketch, "E3176", {"start": v(66.27, -6.04) * mm, "mid": v(66.44, -6.08) * mm, "end": v(66.6, -6.02) * mm});
            skArc(sketch, "E3177", {"start": v(66.6, -6.02) * mm, "mid": v(66.93, -5.71) * mm, "end": v(67.25, -5.4) * mm});
            skArc(sketch, "E3178", {"start": v(67.25, -5.4) * mm, "mid": v(67.6, -5.02) * mm, "end": v(67.99, -4.66) * mm});
            skArc(sketch, "E3179", {"start": v(67.99, -4.66) * mm, "mid": v(68.43, -4.27) * mm, "end": v(68.9, -3.9) * mm});
            skArc(sketch, "E3180", {"start": v(68.9, -3.9) * mm, "mid": v(69.33, -3.55) * mm, "end": v(69.77, -3.22) * mm});
            skArc(sketch, "E3181", {"start": v(69.77, -3.22) * mm, "mid": v(69.92, -3.14) * mm, "end": v(70.1, -3.1) * mm});
            skArc(sketch, "E3182", {"start": v(70.1, -3.1) * mm, "mid": v(70.14, -3.13) * mm, "end": v(70.16, -3.17) * mm});
            skArc(sketch, "E3183", {"start": v(70.16, -3.17) * mm, "mid": v(70.2, -3.32) * mm, "end": v(70.22, -3.48) * mm});
            skArc(sketch, "E3184", {"start": v(70.22, -3.48) * mm, "mid": v(70.24, -3.68) * mm, "end": v(70.26, -3.88) * mm});
            skArc(sketch, "E3185", {"start": v(70.26, -3.88) * mm, "mid": v(70.27, -4.12) * mm, "end": v(70.27, -4.35) * mm});
            skArc(sketch, "E3186", {"start": v(70.27, -4.35) * mm, "mid": v(70.28, -4.6) * mm, "end": v(70.3, -4.83) * mm});
            skArc(sketch, "E3187", {"start": v(70.3, -4.83) * mm, "mid": v(70.32, -5.03) * mm, "end": v(70.35, -5.23) * mm});
            skArc(sketch, "E3188", {"start": v(70.35, -5.23) * mm, "mid": v(70.39, -5.38) * mm, "end": v(70.44, -5.53) * mm});
            skArc(sketch, "E3189", {"start": v(70.44, -5.53) * mm, "mid": v(70.48, -5.58) * mm, "end": v(70.54, -5.6) * mm});
            skArc(sketch, "E3190", {"start": v(70.54, -5.6) * mm, "mid": v(70.63, -5.58) * mm, "end": v(70.7, -5.54) * mm});
            skArc(sketch, "E3191", {"start": v(70.7, -5.54) * mm, "mid": v(70.9, -5.39) * mm, "end": v(71.08, -5.22) * mm});
            skArc(sketch, "E3192", {"start": v(71.08, -5.22) * mm, "mid": v(71.3, -5.02) * mm, "end": v(71.52, -4.81) * mm});
            skArc(sketch, "E3193", {"start": v(71.52, -4.81) * mm, "mid": v(71.76, -4.57) * mm, "end": v(71.99, -4.32) * mm});
            skArc(sketch, "E3194", {"start": v(71.99, -4.32) * mm, "mid": v(72.44, -3.87) * mm, "end": v(72.93, -3.45) * mm});
            skArc(sketch, "E3195", {"start": v(72.93, -3.45) * mm, "mid": v(73.57, -2.95) * mm, "end": v(74.23, -2.47) * mm});
            skArc(sketch, "E3196", {"start": v(74.23, -2.47) * mm, "mid": v(74.87, -2.04) * mm, "end": v(75.52, -1.63) * mm});
            skArc(sketch, "E3197", {"start": v(75.52, -1.63) * mm, "mid": v(75.82, -1.5) * mm, "end": v(76.15, -1.45) * mm});
            skArc(sketch, "E3198", {"start": v(76.15, -1.45) * mm, "mid": v(76.2, -1.47) * mm, "end": v(76.23, -1.52) * mm});
            skArc(sketch, "E3199", {"start": v(76.23, -1.52) * mm, "mid": v(76.27, -1.68) * mm, "end": v(76.3, -1.84) * mm});
            skArc(sketch, "E3200", {"start": v(76.3, -1.84) * mm, "mid": v(76.32, -2.06) * mm, "end": v(76.34, -2.27) * mm});
            skArc(sketch, "E3201", {"start": v(76.34, -2.27) * mm, "mid": v(76.35, -2.53) * mm, "end": v(76.36, -2.79) * mm});
            skArc(sketch, "E3202", {"start": v(76.36, -2.79) * mm, "mid": v(76.36, -3.05) * mm, "end": v(76.37, -3.31) * mm});
            skArc(sketch, "E3203", {"start": v(76.37, -3.31) * mm, "mid": v(76.38, -3.55) * mm, "end": v(76.4, -3.78) * mm});
            skArc(sketch, "E3204", {"start": v(76.4, -3.78) * mm, "mid": v(76.44, -3.98) * mm, "end": v(76.47, -4.17) * mm});
            skArc(sketch, "E3205", {"start": v(76.47, -4.17) * mm, "mid": v(76.5, -4.24) * mm, "end": v(76.54, -4.3) * mm});
            skArc(sketch, "E3206", {"start": v(76.54, -4.3) * mm, "mid": v(76.6, -4.33) * mm, "end": v(76.67, -4.31) * mm});
            skArc(sketch, "E3207", {"start": v(76.67, -4.31) * mm, "mid": v(76.89, -4.14) * mm, "end": v(77.1, -3.96) * mm});
            skArc(sketch, "E3208", {"start": v(77.1, -3.96) * mm, "mid": v(77.36, -3.72) * mm, "end": v(77.62, -3.47) * mm});
            skArc(sketch, "E3209", {"start": v(77.62, -3.47) * mm, "mid": v(77.91, -3.16) * mm, "end": v(78.2, -2.86) * mm});
            skArc(sketch, "E3210", {"start": v(78.2, -2.86) * mm, "mid": v(78.78, -2.25) * mm, "end": v(79.4, -1.7) * mm});
            skArc(sketch, "E3211", {"start": v(79.4, -1.7) * mm, "mid": v(80.24, -1.01) * mm, "end": v(81.1, -0.36) * mm});
            skArc(sketch, "E3212", {"start": v(81.1, -0.36) * mm, "mid": v(81.93, 0.24) * mm, "end": v(82.79, 0.82) * mm});
            skArc(sketch, "E3213", {"start": v(82.79, 0.82) * mm, "mid": v(83.13, 0.98) * mm, "end": v(83.5, 1.04) * mm});
            skArc(sketch, "E3214", {"start": v(83.5, 1.04) * mm, "mid": v(83.56, 1.02) * mm, "end": v(83.6, 0.97) * mm});
            skArc(sketch, "E3215", {"start": v(83.6, 0.97) * mm, "mid": v(83.62, 0.83) * mm, "end": v(83.64, 0.68) * mm});
            skArc(sketch, "E3216", {"start": v(83.64, 0.68) * mm, "mid": v(83.65, 0.49) * mm, "end": v(83.65, 0.3) * mm});
            skArc(sketch, "E3217", {"start": v(83.65, 0.3) * mm, "mid": v(83.64, 0.06) * mm, "end": v(83.62, -0.17) * mm});
            skArc(sketch, "E3218", {"start": v(83.62, -0.17) * mm, "mid": v(83.58, -0.69) * mm, "end": v(83.59, -1.21) * mm});
            skArc(sketch, "E3219", {"start": v(83.59, -1.21) * mm, "mid": v(83.68, -1.43) * mm, "end": v(83.88, -1.54) * mm});
            skArc(sketch, "E3220", {"start": v(83.88, -1.54) * mm, "mid": v(84.17, -1.52) * mm, "end": v(84.44, -1.4) * mm});
            skArc(sketch, "E3221", {"start": v(84.44, -1.4) * mm, "mid": v(85, -0.95) * mm, "end": v(85.54, -0.48) * mm});
            skArc(sketch, "E3222", {"start": v(85.54, -0.48) * mm, "mid": v(86.37, 0.2) * mm, "end": v(87.26, 0.81) * mm});
            skArc(sketch, "E3223", {"start": v(87.26, 0.81) * mm, "mid": v(88.29, 1.4) * mm, "end": v(89.35, 1.94) * mm});
            skArc(sketch, "E3224", {"start": v(89.35, 1.94) * mm, "mid": v(90.38, 2.36) * mm, "end": v(91.43, 2.72) * mm});
            skArc(sketch, "E3225", {"start": v(91.43, 2.72) * mm, "mid": v(92.26, 2.91) * mm, "end": v(93.1, 2.97) * mm});
            skArc(sketch, "E3226", {"start": v(93.1, 2.97) * mm, "mid": v(93.28, 2.96) * mm, "end": v(93.45, 2.94) * mm});
            skArc(sketch, "E3227", {"start": v(93.45, 2.94) * mm, "mid": v(93.53, 2.9) * mm, "end": v(93.59, 2.81) * mm});
            skArc(sketch, "E3228", {"start": v(93.59, 2.81) * mm, "mid": v(93.6, 2.68) * mm, "end": v(93.6, 2.55) * mm});
            skArc(sketch, "E3229", {"start": v(93.6, 2.55) * mm, "mid": v(93.52, 2.21) * mm, "end": v(93.44, 1.87) * mm});
            skArc(sketch, "E3230", {"start": v(93.44, 1.87) * mm, "mid": v(93.3, 1.3) * mm, "end": v(93.2, 0.71) * mm});
            skArc(sketch, "E3231", {"start": v(93.2, 0.71) * mm, "mid": v(93.23, 0.47) * mm, "end": v(93.37, 0.27) * mm});
            skArc(sketch, "E3232", {"start": v(93.37, 0.27) * mm, "mid": v(93.6, 0.17) * mm, "end": v(93.84, 0.19) * mm});
            skArc(sketch, "E3233", {"start": v(93.84, 0.19) * mm, "mid": v(94.4, 0.4) * mm, "end": v(94.95, 0.63) * mm});
            skArc(sketch, "E3234", {"start": v(94.95, 0.63) * mm, "mid": v(95.62, 0.9) * mm, "end": v(96.32, 1.1) * mm});
            skArc(sketch, "E3235", {"start": v(96.32, 1.1) * mm, "mid": v(97.22, 1.3) * mm, "end": v(98.13, 1.44) * mm});
            skArc(sketch, "E3236", {"start": v(98.13, 1.44) * mm, "mid": v(99.02, 1.54) * mm, "end": v(99.9, 1.6) * mm});
            skArc(sketch, "E3237", {"start": v(99.9, 1.6) * mm, "mid": v(100.51, 1.58) * mm, "end": v(101.11, 1.47) * mm});
            skLineSegment(sketch, "E3238", {"start": v(101.11, 1.47) * mm, "end": v(101.87, 1.28) * mm});
            skLineSegment(sketch, "E3239", {"start": v(101.87, 1.28) * mm, "end": v(101.14, 0.52) * mm});
            skArc(sketch, "E3240", {"start": v(101.14, 0.52) * mm, "mid": v(101, 0.37) * mm, "end": v(100.86, 0.22) * mm});
            skArc(sketch, "E3241", {"start": v(100.86, 0.22) * mm, "mid": v(100.74, 0.08) * mm, "end": v(100.63, -0.07) * mm});
            skArc(sketch, "E3242", {"start": v(100.63, -0.07) * mm, "mid": v(100.53, -0.2) * mm, "end": v(100.45, -0.31) * mm});
            skArc(sketch, "E3243", {"start": v(100.45, -0.31) * mm, "mid": v(100.42, -0.37) * mm, "end": v(100.41, -0.42) * mm});
            skArc(sketch, "E3244", {"start": v(100.41, -0.42) * mm, "mid": v(100.42, -0.48) * mm, "end": v(100.46, -0.52) * mm});
            skArc(sketch, "E3245", {"start": v(100.46, -0.52) * mm, "mid": v(100.59, -0.62) * mm, "end": v(100.72, -0.71) * mm});
            skArc(sketch, "E3246", {"start": v(100.72, -0.71) * mm, "mid": v(100.89, -0.82) * mm, "end": v(101.06, -0.93) * mm});
            skArc(sketch, "E3247", {"start": v(101.06, -0.93) * mm, "mid": v(101.26, -1.04) * mm, "end": v(101.46, -1.15) * mm});
            skArc(sketch, "E3248", {"start": v(101.46, -1.15) * mm, "mid": v(102.15, -1.56) * mm, "end": v(102.78, -2.05) * mm});
            skArc(sketch, "E3249", {"start": v(102.78, -2.05) * mm, "mid": v(103.48, -2.72) * mm, "end": v(104.12, -3.44) * mm});
            skArc(sketch, "E3250", {"start": v(104.12, -3.44) * mm, "mid": v(104.42, -3.88) * mm, "end": v(104.63, -4.37) * mm});
            skArc(sketch, "E3251", {"start": v(104.63, -4.37) * mm, "mid": v(104.58, -4.6) * mm, "end": v(104.35, -4.64) * mm});
            skArc(sketch, "E3252", {"start": v(104.35, -4.64) * mm, "mid": v(104, -4.53) * mm, "end": v(103.66, -4.46) * mm});
            skArc(sketch, "E3253", {"start": v(103.66, -4.46) * mm, "mid": v(102.74, -4.34) * mm, "end": v(101.82, -4.23) * mm});
            skArc(sketch, "E3254", {"start": v(101.82, -4.23) * mm, "mid": v(100.84, -4.11) * mm, "end": v(99.86, -4) * mm});
            skArc(sketch, "E3255", {"start": v(99.86, -4) * mm, "mid": v(99.73, -4.01) * mm, "end": v(99.62, -4.08) * mm});
            skArc(sketch, "E3256", {"start": v(99.62, -4.08) * mm, "mid": v(99.6, -4.12) * mm, "end": v(99.58, -4.17) * mm});
            skArc(sketch, "E3257", {"start": v(99.58, -4.17) * mm, "mid": v(99.56, -4.58) * mm, "end": v(99.54, -4.99) * mm});
            skArc(sketch, "E3258", {"start": v(99.54, -4.99) * mm, "mid": v(99.52, -5.46) * mm, "end": v(99.5, -5.93) * mm});
            skArc(sketch, "E3259", {"start": v(99.5, -5.93) * mm, "mid": v(99.5, -6.48) * mm, "end": v(99.49, -7.03) * mm});
            skArc(sketch, "E3260", {"start": v(99.49, -7.03) * mm, "mid": v(99.47, -7.93) * mm, "end": v(99.45, -8.83) * mm});
            skArc(sketch, "E3261", {"start": v(99.45, -8.83) * mm, "mid": v(99.42, -9.17) * mm, "end": v(99.36, -9.5) * mm});
            skArc(sketch, "E3262", {"start": v(99.36, -9.5) * mm, "mid": v(99.3, -9.67) * mm, "end": v(99.17, -9.81) * mm});
            skArc(sketch, "E3263", {"start": v(99.17, -9.81) * mm, "mid": v(99, -9.92) * mm, "end": v(98.82, -9.97) * mm});
            skArc(sketch, "E3264", {"start": v(98.82, -9.97) * mm, "mid": v(98.65, -10.01) * mm, "end": v(98.48, -10.09) * mm});
            skArc(sketch, "E3265", {"start": v(98.48, -10.09) * mm, "mid": v(98.37, -10.18) * mm, "end": v(98.3, -10.3) * mm});
            skArc(sketch, "E3266", {"start": v(98.3, -10.3) * mm, "mid": v(98.24, -10.51) * mm, "end": v(98.22, -10.73) * mm});
            skArc(sketch, "E3267", {"start": v(98.22, -10.73) * mm, "mid": v(98.2, -11.2) * mm, "end": v(98.2, -11.68) * mm});
            skArc(sketch, "E3268", {"start": v(98.2, -11.68) * mm, "mid": v(98.2, -12) * mm, "end": v(98.18, -12.32) * mm});
            skArc(sketch, "E3269", {"start": v(98.18, -12.32) * mm, "mid": v(98.15, -12.6) * mm, "end": v(98.12, -12.88) * mm});
            skArc(sketch, "E3270", {"start": v(98.12, -12.88) * mm, "mid": v(98.08, -13.1) * mm, "end": v(98.03, -13.33) * mm});
            skArc(sketch, "E3271", {"start": v(98.03, -13.33) * mm, "mid": v(98, -13.41) * mm, "end": v(97.92, -13.48) * mm});
            skArc(sketch, "E3272", {"start": v(97.92, -13.48) * mm, "mid": v(97.77, -13.5) * mm, "end": v(97.64, -13.42) * mm});
            skArc(sketch, "E3273", {"start": v(97.64, -13.42) * mm, "mid": v(97.48, -13.16) * mm, "end": v(97.36, -12.89) * mm});
            skArc(sketch, "E3274", {"start": v(97.36, -12.89) * mm, "mid": v(97.26, -12.53) * mm, "end": v(97.2, -12.17) * mm});
            skArc(sketch, "E3275", {"start": v(97.2, -12.17) * mm, "mid": v(97.2, -11.87) * mm, "end": v(97.25, -11.58) * mm});
            skArc(sketch, "E3276", {"start": v(97.25, -11.58) * mm, "mid": v(97.28, -11.45) * mm, "end": v(97.32, -11.32) * mm});
            skArc(sketch, "E3277", {"start": v(97.32, -11.32) * mm, "mid": v(97.36, -11.17) * mm, "end": v(97.4, -11.02) * mm});
            skArc(sketch, "E3278", {"start": v(97.4, -11.02) * mm, "mid": v(97.44, -10.88) * mm, "end": v(97.48, -10.73) * mm});
            skArc(sketch, "E3279", {"start": v(97.48, -10.73) * mm, "mid": v(97.52, -10.62) * mm, "end": v(97.55, -10.5) * mm});
            skArc(sketch, "E3280", {"start": v(97.55, -10.5) * mm, "mid": v(97.57, -10.4) * mm, "end": v(97.58, -10.27) * mm});
            skArc(sketch, "E3281", {"start": v(97.58, -10.27) * mm, "mid": v(97.55, -10.2) * mm, "end": v(97.5, -10.13) * mm});
            skArc(sketch, "E3282", {"start": v(97.5, -10.13) * mm, "mid": v(97.42, -10.07) * mm, "end": v(97.32, -10.04) * mm});
            skArc(sketch, "E3283", {"start": v(97.32, -10.04) * mm, "mid": v(97.15, -10.03) * mm, "end": v(96.97, -10.02) * mm});
            skLineSegment(sketch, "E3284", {"start": v(96.97, -10.02) * mm, "end": v(96.26, -10.02) * mm});
            skLineSegment(sketch, "E3285", {"start": v(96.26, -10.02) * mm, "end": v(96.26, -6.94) * mm});
            skLineSegment(sketch, "E3286", {"start": v(96.26, -6.94) * mm, "end": v(96.26, -3.86) * mm});
            skLineSegment(sketch, "E3287", {"start": v(96.26, -3.86) * mm, "end": v(93.52, -4) * mm});
            skArc(sketch, "E3288", {"start": v(93.52, -4) * mm, "mid": v(92.34, -4.08) * mm, "end": v(91.16, -4.17) * mm});
            skArc(sketch, "E3289", {"start": v(91.16, -4.17) * mm, "mid": v(90.76, -4.25) * mm, "end": v(90.37, -4.42) * mm});
            skArc(sketch, "E3290", {"start": v(90.37, -4.42) * mm, "mid": v(90.22, -4.6) * mm, "end": v(90.23, -4.84) * mm});
            skArc(sketch, "E3291", {"start": v(90.23, -4.84) * mm, "mid": v(90.44, -5.22) * mm, "end": v(90.71, -5.57) * mm});
            skArc(sketch, "E3292", {"start": v(90.71, -5.57) * mm, "mid": v(90.88, -5.78) * mm, "end": v(91.05, -5.99) * mm});
            skArc(sketch, "E3293", {"start": v(91.05, -5.99) * mm, "mid": v(91.22, -6.22) * mm, "end": v(91.38, -6.46) * mm});
            skArc(sketch, "E3294", {"start": v(91.38, -6.46) * mm, "mid": v(91.52, -6.7) * mm, "end": v(91.65, -6.94) * mm});
            skArc(sketch, "E3295", {"start": v(91.65, -6.94) * mm, "mid": v(91.74, -7.12) * mm, "end": v(91.82, -7.32) * mm});
            skArc(sketch, "E3296", {"start": v(91.82, -7.32) * mm, "mid": v(91.9, -7.56) * mm, "end": v(91.98, -7.8) * mm});
            skArc(sketch, "E3297", {"start": v(91.98, -7.8) * mm, "mid": v(92, -7.89) * mm, "end": v(91.98, -7.97) * mm});
            skArc(sketch, "E3298", {"start": v(91.98, -7.97) * mm, "mid": v(91.94, -8.02) * mm, "end": v(91.88, -8.03) * mm});
            skArc(sketch, "E3299", {"start": v(91.88, -8.03) * mm, "mid": v(91.75, -8) * mm, "end": v(91.63, -7.95) * mm});
            skArc(sketch, "E3300", {"start": v(91.63, -7.95) * mm, "mid": v(91.08, -7.77) * mm, "end": v(90.52, -7.63) * mm});
            skArc(sketch, "E3301", {"start": v(90.52, -7.63) * mm, "mid": v(89.59, -7.46) * mm, "end": v(88.65, -7.3) * mm});
            skArc(sketch, "E3302", {"start": v(88.65, -7.3) * mm, "mid": v(87.68, -7.17) * mm, "end": v(86.7, -7.06) * mm});
            skArc(sketch, "E3303", {"start": v(86.7, -7.06) * mm, "mid": v(85.94, -7) * mm, "end": v(85.18, -6.98) * mm});
            skArc(sketch, "E3304", {"start": v(85.18, -6.98) * mm, "mid": v(84.5, -6.99) * mm, "end": v(83.84, -7.02) * mm});
            skArc(sketch, "E3305", {"start": v(83.84, -7.02) * mm, "mid": v(83.6, -7.07) * mm, "end": v(83.4, -7.2) * mm});
            skArc(sketch, "E3306", {"start": v(83.4, -7.2) * mm, "mid": v(83.3, -7.38) * mm, "end": v(83.3, -7.57) * mm});
            skArc(sketch, "E3307", {"start": v(83.3, -7.57) * mm, "mid": v(83.48, -7.98) * mm, "end": v(83.68, -8.36) * mm});
            skArc(sketch, "E3308", {"start": v(83.68, -8.36) * mm, "mid": v(83.92, -8.83) * mm, "end": v(84.11, -9.31) * mm});
            skArc(sketch, "E3309", {"start": v(84.11, -9.31) * mm, "mid": v(84.11, -9.56) * mm, "end": v(83.96, -9.76) * mm});
            skArc(sketch, "E3310", {"start": v(83.96, -9.76) * mm, "mid": v(83.65, -9.92) * mm, "end": v(83.3, -9.98) * mm});
            skArc(sketch, "E3311", {"start": v(83.3, -9.98) * mm, "mid": v(82.28, -10) * mm, "end": v(81.26, -10.01) * mm});
            skArc(sketch, "E3312", {"start": v(81.26, -10.01) * mm, "mid": v(80.67, -10.02) * mm, "end": v(80.08, -10.04) * mm});
            skArc(sketch, "E3313", {"start": v(80.08, -10.04) * mm, "mid": v(79.47, -10.08) * mm, "end": v(78.86, -10.12) * mm});
            skArc(sketch, "E3314", {"start": v(78.86, -10.12) * mm, "mid": v(78.31, -10.17) * mm, "end": v(77.77, -10.24) * mm});
            skArc(sketch, "E3315", {"start": v(77.77, -10.24) * mm, "mid": v(77.4, -10.3) * mm, "end": v(77.05, -10.38) * mm});
            skLineSegment(sketch, "E3316", {"start": v(77.05, -10.38) * mm, "end": v(75.66, -10.75) * mm});
            skLineSegment(sketch, "E3317", {"start": v(75.66, -10.75) * mm, "end": v(75.76, -12.3) * mm});
            skArc(sketch, "E3318", {"start": v(75.76, -12.3) * mm, "mid": v(75.78, -12.77) * mm, "end": v(75.8, -13.24) * mm});
            skArc(sketch, "E3319", {"start": v(75.8, -13.24) * mm, "mid": v(75.79, -13.44) * mm, "end": v(75.74, -13.63) * mm});
            skArc(sketch, "E3320", {"start": v(75.74, -13.63) * mm, "mid": v(75.67, -13.75) * mm, "end": v(75.56, -13.83) * mm});
            skArc(sketch, "E3321", {"start": v(75.56, -13.83) * mm, "mid": v(75.4, -13.9) * mm, "end": v(75.2, -13.94) * mm});
            skArc(sketch, "E3322", {"start": v(75.2, -13.94) * mm, "mid": v(75.03, -13.98) * mm, "end": v(74.87, -14.04) * mm});
            skArc(sketch, "E3323", {"start": v(74.87, -14.04) * mm, "mid": v(74.76, -14.1) * mm, "end": v(74.69, -14.2) * mm});
            skArc(sketch, "E3324", {"start": v(74.69, -14.2) * mm, "mid": v(74.64, -14.35) * mm, "end": v(74.62, -14.51) * mm});
            skArc(sketch, "E3325", {"start": v(74.62, -14.51) * mm, "mid": v(74.62, -14.82) * mm, "end": v(74.64, -15.14) * mm});
            skArc(sketch, "E3326", {"start": v(74.64, -15.14) * mm, "mid": v(74.65, -15.58) * mm, "end": v(74.62, -16.02) * mm});
            skArc(sketch, "E3327", {"start": v(74.62, -16.02) * mm, "mid": v(74.57, -16.34) * mm, "end": v(74.45, -16.64) * mm});
            skArc(sketch, "E3328", {"start": v(74.45, -16.64) * mm, "mid": v(74.33, -16.77) * mm, "end": v(74.17, -16.82) * mm});
            skArc(sketch, "E3329", {"start": v(74.17, -16.82) * mm, "mid": v(74, -16.78) * mm, "end": v(73.86, -16.66) * mm});
            skArc(sketch, "E3330", {"start": v(73.86, -16.66) * mm, "mid": v(73.8, -16.55) * mm, "end": v(73.76, -16.43) * mm});
            skArc(sketch, "E3331", {"start": v(73.76, -16.43) * mm, "mid": v(73.72, -16.23) * mm, "end": v(73.68, -16.04) * mm});
            skArc(sketch, "E3332", {"start": v(73.68, -16.04) * mm, "mid": v(73.66, -15.82) * mm, "end": v(73.64, -15.6) * mm});
            skArc(sketch, "E3333", {"start": v(73.64, -15.6) * mm, "mid": v(73.64, -15.36) * mm, "end": v(73.65, -15.14) * mm});
            skArc(sketch, "E3334", {"start": v(73.65, -15.14) * mm, "mid": v(73.66, -14.83) * mm, "end": v(73.67, -14.51) * mm});
            skArc(sketch, "E3335", {"start": v(73.67, -14.51) * mm, "mid": v(73.65, -14.36) * mm, "end": v(73.6, -14.2) * mm});
            skArc(sketch, "E3336", {"start": v(73.6, -14.2) * mm, "mid": v(73.53, -14.1) * mm, "end": v(73.42, -14.04) * mm});
            skArc(sketch, "E3337", {"start": v(73.42, -14.04) * mm, "mid": v(73.26, -13.98) * mm, "end": v(73.09, -13.94) * mm});
            skArc(sketch, "E3338", {"start": v(73.09, -13.94) * mm, "mid": v(72.92, -13.9) * mm, "end": v(72.77, -13.86) * mm});
            skArc(sketch, "E3339", {"start": v(72.77, -13.86) * mm, "mid": v(72.67, -13.8) * mm, "end": v(72.6, -13.72) * mm});
            skArc(sketch, "E3340", {"start": v(72.6, -13.72) * mm, "mid": v(72.54, -13.61) * mm, "end": v(72.52, -13.5) * mm});
            skArc(sketch, "E3341", {"start": v(72.52, -13.5) * mm, "mid": v(72.52, -13.3) * mm, "end": v(72.54, -13.11) * mm});
            skArc(sketch, "E3342", {"start": v(72.54, -13.11) * mm, "mid": v(72.53, -12.84) * mm, "end": v(72.45, -12.58) * mm});
            skArc(sketch, "E3343", {"start": v(72.45, -12.58) * mm, "mid": v(72.32, -12.46) * mm, "end": v(72.14, -12.46) * mm});
            skArc(sketch, "E3344", {"start": v(72.14, -12.46) * mm, "mid": v(71.79, -12.64) * mm, "end": v(71.48, -12.87) * mm});
            skArc(sketch, "E3345", {"start": v(71.48, -12.87) * mm, "mid": v(70.85, -13.44) * mm, "end": v(70.24, -14.03) * mm});
            skArc(sketch, "E3346", {"start": v(70.24, -14.03) * mm, "mid": v(69.57, -14.72) * mm, "end": v(68.93, -15.44) * mm});
            skArc(sketch, "E3347", {"start": v(68.93, -15.44) * mm, "mid": v(68.36, -16.14) * mm, "end": v(67.83, -16.87) * mm});
            skArc(sketch, "E3348", {"start": v(67.83, -16.87) * mm, "mid": v(67.36, -17.58) * mm, "end": v(66.94, -18.31) * mm});
            skArc(sketch, "E3349", {"start": v(66.94, -18.31) * mm, "mid": v(66.58, -19.03) * mm, "end": v(66.27, -19.78) * mm});
            skArc(sketch, "E3350", {"start": v(66.27, -19.78) * mm, "mid": v(66.08, -20.3) * mm, "end": v(65.92, -20.82) * mm});
            skArc(sketch, "E3351", {"start": v(65.92, -20.82) * mm, "mid": v(65.9, -21.02) * mm, "end": v(65.97, -21.22) * mm});
            skArc(sketch, "E3352", {"start": v(65.97, -21.22) * mm, "mid": v(66.1, -21.3) * mm, "end": v(66.25, -21.27) * mm});
            skArc(sketch, "E3353", {"start": v(66.25, -21.27) * mm, "mid": v(66.58, -21.01) * mm, "end": v(66.89, -20.74) * mm});
            skArc(sketch, "E3354", {"start": v(66.89, -20.74) * mm, "mid": v(67.33, -20.35) * mm, "end": v(67.8, -20) * mm});
            skArc(sketch, "E3355", {"start": v(67.8, -20) * mm, "mid": v(68.51, -19.52) * mm, "end": v(69.24, -19.06) * mm});
            skArc(sketch, "E3356", {"start": v(69.24, -19.06) * mm, "mid": v(69.98, -18.62) * mm, "end": v(70.72, -18.2) * mm});
            skArc(sketch, "E3357", {"start": v(70.72, -18.2) * mm, "mid": v(71, -18.08) * mm, "end": v(71.3, -18.04) * mm});
            skArc(sketch, "E3358", {"start": v(71.3, -18.04) * mm, "mid": v(71.4, -18.07) * mm, "end": v(71.46, -18.14) * mm});
            skArc(sketch, "E3359", {"start": v(71.46, -18.14) * mm, "mid": v(71.53, -18.3) * mm, "end": v(71.57, -18.45) * mm});
            skArc(sketch, "E3360", {"start": v(71.57, -18.45) * mm, "mid": v(71.61, -18.71) * mm, "end": v(71.64, -18.98) * mm});
            skArc(sketch, "E3361", {"start": v(71.64, -18.98) * mm, "mid": v(71.65, -19.4) * mm, "end": v(71.65, -19.82) * mm});
            skArc(sketch, "E3362", {"start": v(71.65, -19.82) * mm, "mid": v(71.67, -20.45) * mm, "end": v(71.7, -21.08) * mm});
            skArc(sketch, "E3363", {"start": v(71.7, -21.08) * mm, "mid": v(71.78, -21.4) * mm, "end": v(71.92, -21.68) * mm});
            skArc(sketch, "E3364", {"start": v(71.92, -21.68) * mm, "mid": v(72.07, -21.78) * mm, "end": v(72.25, -21.75) * mm});
            skArc(sketch, "E3365", {"start": v(72.25, -21.75) * mm, "mid": v(72.5, -21.56) * mm, "end": v(72.69, -21.32) * mm});
            skArc(sketch, "E3366", {"start": v(72.69, -21.32) * mm, "mid": v(72.81, -21.14) * mm, "end": v(72.95, -20.98) * mm});
            skArc(sketch, "E3367", {"start": v(72.95, -20.98) * mm, "mid": v(73.2, -20.7) * mm, "end": v(73.45, -20.42) * mm});
            skArc(sketch, "E3368", {"start": v(73.45, -20.42) * mm, "mid": v(73.74, -20.1) * mm, "end": v(74.04, -19.8) * mm});
            skArc(sketch, "E3369", {"start": v(74.04, -19.8) * mm, "mid": v(74.35, -19.49) * mm, "end": v(74.66, -19.18) * mm});
            skLineSegment(sketch, "E3370", {"start": v(74.66, -19.18) * mm, "end": v(76.2, -17.7) * mm});
            skLineSegment(sketch, "E3371", {"start": v(76.2, -17.7) * mm, "end": v(76.42, -18.56) * mm});
            skArc(sketch, "E3372", {"start": v(76.42, -18.56) * mm, "mid": v(76.53, -18.87) * mm, "end": v(76.67, -19.17) * mm});
            skArc(sketch, "E3373", {"start": v(76.67, -19.17) * mm, "mid": v(76.8, -19.32) * mm, "end": v(77, -19.4) * mm});
            skArc(sketch, "E3374", {"start": v(77, -19.4) * mm, "mid": v(77.2, -19.36) * mm, "end": v(77.36, -19.25) * mm});
            skArc(sketch, "E3375", {"start": v(77.36, -19.25) * mm, "mid": v(77.55, -18.99) * mm, "end": v(77.7, -18.7) * mm});
            skArc(sketch, "E3376", {"start": v(77.7, -18.7) * mm, "mid": v(77.93, -18.24) * mm, "end": v(78.2, -17.8) * mm});
            skArc(sketch, "E3377", {"start": v(78.2, -17.8) * mm, "mid": v(78.53, -17.34) * mm, "end": v(78.88, -16.9) * mm});
            skArc(sketch, "E3378", {"start": v(78.88, -16.9) * mm, "mid": v(79.28, -16.47) * mm, "end": v(79.7, -16.06) * mm});
            skArc(sketch, "E3379", {"start": v(79.7, -16.06) * mm, "mid": v(80.16, -15.67) * mm, "end": v(80.63, -15.31) * mm});
            skArc(sketch, "E3380", {"start": v(80.63, -15.31) * mm, "mid": v(81.05, -15.01) * mm, "end": v(81.47, -14.72) * mm});
            skArc(sketch, "E3381", {"start": v(81.47, -14.72) * mm, "mid": v(81.6, -14.65) * mm, "end": v(81.73, -14.6) * mm});
            skArc(sketch, "E3382", {"start": v(81.73, -14.6) * mm, "mid": v(81.81, -14.62) * mm, "end": v(81.87, -14.7) * mm});
            skArc(sketch, "E3383", {"start": v(81.87, -14.7) * mm, "mid": v(81.9, -14.87) * mm, "end": v(81.93, -15.05) * mm});
            skArc(sketch, "E3384", {"start": v(81.93, -15.05) * mm, "mid": v(81.94, -15.19) * mm, "end": v(81.95, -15.32) * mm});
            skArc(sketch, "E3385", {"start": v(81.95, -15.32) * mm, "mid": v(81.96, -15.46) * mm, "end": v(81.97, -15.6) * mm});
            skArc(sketch, "E3386", {"start": v(81.97, -15.6) * mm, "mid": v(81.98, -15.72) * mm, "end": v(81.99, -15.85) * mm});
            skArc(sketch, "E3387", {"start": v(81.99, -15.85) * mm, "mid": v(82, -15.93) * mm, "end": v(82, -16.02) * mm});
            skArc(sketch, "E3388", {"start": v(82, -16.02) * mm, "mid": v(82.04, -16.22) * mm, "end": v(82.12, -16.4) * mm});
            skArc(sketch, "E3389", {"start": v(82.12, -16.4) * mm, "mid": v(82.22, -16.5) * mm, "end": v(82.35, -16.55) * mm});
            skArc(sketch, "E3390", {"start": v(82.35, -16.55) * mm, "mid": v(82.54, -16.52) * mm, "end": v(82.71, -16.44) * mm});
            skArc(sketch, "E3391", {"start": v(82.71, -16.44) * mm, "mid": v(82.96, -16.26) * mm, "end": v(83.2, -16.05) * mm});
            skArc(sketch, "E3392", {"start": v(83.2, -16.05) * mm, "mid": v(83.53, -15.76) * mm, "end": v(83.88, -15.48) * mm});
            skArc(sketch, "E3393", {"start": v(83.88, -15.48) * mm, "mid": v(84.18, -15.27) * mm, "end": v(84.5, -15.08) * mm});
            skArc(sketch, "E3394", {"start": v(84.5, -15.08) * mm, "mid": v(84.8, -14.95) * mm, "end": v(85.1, -14.84) * mm});
            skArc(sketch, "E3395", {"start": v(85.1, -14.84) * mm, "mid": v(85.43, -14.76) * mm, "end": v(85.76, -14.72) * mm});
            skArc(sketch, "E3396", {"start": v(85.76, -14.72) * mm, "mid": v(86.14, -14.7) * mm, "end": v(86.52, -14.67) * mm});
            skArc(sketch, "E3397", {"start": v(86.52, -14.67) * mm, "mid": v(86.63, -14.7) * mm, "end": v(86.72, -14.76) * mm});
            skArc(sketch, "E3398", {"start": v(86.72, -14.76) * mm, "mid": v(86.76, -14.85) * mm, "end": v(86.73, -14.94) * mm});
            skArc(sketch, "E3399", {"start": v(86.73, -14.94) * mm, "mid": v(86.53, -15.17) * mm, "end": v(86.33, -15.39) * mm});
            skArc(sketch, "E3400", {"start": v(86.33, -15.39) * mm, "mid": v(86.06, -15.72) * mm, "end": v(85.82, -16.09) * mm});
            skArc(sketch, "E3401", {"start": v(85.82, -16.09) * mm, "mid": v(85.58, -16.56) * mm, "end": v(85.37, -17.06) * mm});
            skArc(sketch, "E3402", {"start": v(85.37, -17.06) * mm, "mid": v(85.2, -17.52) * mm, "end": v(85.07, -18) * mm});
            skArc(sketch, "E3403", {"start": v(85.07, -18) * mm, "mid": v(85.07, -18.2) * mm, "end": v(85.17, -18.39) * mm});
            skArc(sketch, "E3404", {"start": v(85.17, -18.39) * mm, "mid": v(85.24, -18.43) * mm, "end": v(85.31, -18.44) * mm});
            skArc(sketch, "E3405", {"start": v(85.31, -18.44) * mm, "mid": v(85.48, -18.41) * mm, "end": v(85.64, -18.37) * mm});
            skArc(sketch, "E3406", {"start": v(85.64, -18.37) * mm, "mid": v(85.85, -18.32) * mm, "end": v(86.05, -18.24) * mm});
            skArc(sketch, "E3407", {"start": v(86.05, -18.24) * mm, "mid": v(86.28, -18.15) * mm, "end": v(86.5, -18.05) * mm});
            skArc(sketch, "E3408", {"start": v(86.5, -18.05) * mm, "mid": v(87, -17.82) * mm, "end": v(87.53, -17.62) * mm});
            skArc(sketch, "E3409", {"start": v(87.53, -17.62) * mm, "mid": v(88.11, -17.43) * mm, "end": v(88.7, -17.27) * mm});
            skArc(sketch, "E3410", {"start": v(88.7, -17.27) * mm, "mid": v(89.28, -17.13) * mm, "end": v(89.86, -17.03) * mm});
            skArc(sketch, "E3411", {"start": v(89.86, -17.03) * mm, "mid": v(90.34, -16.96) * mm, "end": v(90.83, -16.94) * mm});
            skLineSegment(sketch, "E3412", {"start": v(90.83, -16.94) * mm, "end": v(91.61, -16.93) * mm});
            skLineSegment(sketch, "E3413", {"start": v(91.61, -16.93) * mm, "end": v(90.9, -17.79) * mm});
            skArc(sketch, "E3414", {"start": v(90.9, -17.79) * mm, "mid": v(90.63, -18.12) * mm, "end": v(90.4, -18.48) * mm});
            skArc(sketch, "E3415", {"start": v(90.4, -18.48) * mm, "mid": v(90.26, -18.74) * mm, "end": v(90.19, -19.02) * mm});
            skArc(sketch, "E3416", {"start": v(90.19, -19.02) * mm, "mid": v(90.21, -19.17) * mm, "end": v(90.32, -19.27) * mm});
            skArc(sketch, "E3417", {"start": v(90.32, -19.27) * mm, "mid": v(90.5, -19.31) * mm, "end": v(90.66, -19.28) * mm});
            skArc(sketch, "E3418", {"start": v(90.66, -19.28) * mm, "mid": v(91.26, -19.04) * mm, "end": v(91.86, -18.81) * mm});
            skArc(sketch, "E3419", {"start": v(91.86, -18.81) * mm, "mid": v(92.33, -18.66) * mm, "end": v(92.82, -18.53) * mm});
            skArc(sketch, "E3420", {"start": v(92.82, -18.53) * mm, "mid": v(93.28, -18.44) * mm, "end": v(93.74, -18.38) * mm});
            skArc(sketch, "E3421", {"start": v(93.74, -18.38) * mm, "mid": v(94.28, -18.34) * mm, "end": v(94.82, -18.33) * mm});
            skLineSegment(sketch, "E3422", {"start": v(94.82, -18.33) * mm, "end": v(96.56, -18.32) * mm});
            skLineSegment(sketch, "E3423", {"start": v(96.56, -18.32) * mm, "end": v(95.96, -19.13) * mm});
            skArc(sketch, "E3424", {"start": v(95.96, -19.13) * mm, "mid": v(95.84, -19.3) * mm, "end": v(95.74, -19.47) * mm});
            skArc(sketch, "E3425", {"start": v(95.74, -19.47) * mm, "mid": v(95.65, -19.64) * mm, "end": v(95.58, -19.82) * mm});
            skArc(sketch, "E3426", {"start": v(95.58, -19.82) * mm, "mid": v(95.53, -19.97) * mm, "end": v(95.5, -20.13) * mm});
            skArc(sketch, "E3427", {"start": v(95.5, -20.13) * mm, "mid": v(95.49, -20.24) * mm, "end": v(95.51, -20.34) * mm});
            skArc(sketch, "E3428", {"start": v(95.51, -20.34) * mm, "mid": v(95.58, -20.45) * mm, "end": v(95.68, -20.53) * mm});
            skArc(sketch, "E3429", {"start": v(95.68, -20.53) * mm, "mid": v(95.8, -20.58) * mm, "end": v(95.94, -20.6) * mm});
            skArc(sketch, "E3430", {"start": v(95.94, -20.6) * mm, "mid": v(96.18, -20.6) * mm, "end": v(96.42, -20.55) * mm});
            skArc(sketch, "E3431", {"start": v(96.42, -20.55) * mm, "mid": v(96.92, -20.45) * mm, "end": v(97.42, -20.34) * mm});
            skArc(sketch, "E3432", {"start": v(97.42, -20.34) * mm, "mid": v(98.06, -20.21) * mm, "end": v(98.72, -20.14) * mm});
            skArc(sketch, "E3433", {"start": v(98.72, -20.14) * mm, "mid": v(99.49, -20.1) * mm, "end": v(100.26, -20.1) * mm});
            skArc(sketch, "E3434", {"start": v(100.26, -20.1) * mm, "mid": v(100.97, -20.12) * mm, "end": v(101.68, -20.18) * mm});
            skArc(sketch, "E3435", {"start": v(101.68, -20.18) * mm, "mid": v(102.06, -20.27) * mm, "end": v(102.42, -20.44) * mm});
            skArc(sketch, "E3436", {"start": v(102.42, -20.44) * mm, "mid": v(102.45, -20.48) * mm, "end": v(102.44, -20.53) * mm});
            skArc(sketch, "E3437", {"start": v(102.44, -20.53) * mm, "mid": v(102.38, -20.63) * mm, "end": v(102.32, -20.73) * mm});
            skArc(sketch, "E3438", {"start": v(102.32, -20.73) * mm, "mid": v(102.2, -20.87) * mm, "end": v(102.1, -21) * mm});
            skArc(sketch, "E3439", {"start": v(102.1, -21) * mm, "mid": v(101.94, -21.13) * mm, "end": v(101.78, -21.27) * mm});
            skArc(sketch, "E3440", {"start": v(101.78, -21.27) * mm, "mid": v(101.62, -21.41) * mm, "end": v(101.47, -21.56) * mm});
            skArc(sketch, "E3441", {"start": v(101.47, -21.56) * mm, "mid": v(101.34, -21.7) * mm, "end": v(101.21, -21.85) * mm});
            skArc(sketch, "E3442", {"start": v(101.21, -21.85) * mm, "mid": v(101.13, -21.97) * mm, "end": v(101.04, -22.1) * mm});
            skArc(sketch, "E3443", {"start": v(101.04, -22.1) * mm, "mid": v(101.02, -22.17) * mm, "end": v(101.03, -22.24) * mm});
            skArc(sketch, "E3444", {"start": v(101.03, -22.24) * mm, "mid": v(101.07, -22.32) * mm, "end": v(101.13, -22.38) * mm});
            skArc(sketch, "E3445", {"start": v(101.13, -22.38) * mm, "mid": v(101.33, -22.5) * mm, "end": v(101.53, -22.6) * mm});
            skArc(sketch, "E3446", {"start": v(101.53, -22.6) * mm, "mid": v(101.78, -22.74) * mm, "end": v(102.03, -22.86) * mm});
            skArc(sketch, "E3447", {"start": v(102.03, -22.86) * mm, "mid": v(102.31, -22.99) * mm, "end": v(102.6, -23.1) * mm});
            skArc(sketch, "E3448", {"start": v(102.6, -23.1) * mm, "mid": v(103.14, -23.36) * mm, "end": v(103.65, -23.68) * mm});
            skArc(sketch, "E3449", {"start": v(103.65, -23.68) * mm, "mid": v(104.22, -24.1) * mm, "end": v(104.76, -24.58) * mm});
            skArc(sketch, "E3450", {"start": v(104.76, -24.58) * mm, "mid": v(105.22, -25.02) * mm, "end": v(105.64, -25.5) * mm});
            skArc(sketch, "E3451", {"start": v(105.64, -25.5) * mm, "mid": v(105.72, -25.7) * mm, "end": v(105.63, -25.91) * mm});
            skArc(sketch, "E3452", {"start": v(105.63, -25.91) * mm, "mid": v(105.57, -25.95) * mm, "end": v(105.51, -25.95) * mm});
            skArc(sketch, "E3453", {"start": v(105.51, -25.95) * mm, "mid": v(105.2, -25.92) * mm, "end": v(104.9, -25.88) * mm});
            skArc(sketch, "E3454", {"start": v(104.9, -25.88) * mm, "mid": v(104.55, -25.83) * mm, "end": v(104.19, -25.77) * mm});
            skArc(sketch, "E3455", {"start": v(104.19, -25.77) * mm, "mid": v(103.77, -25.7) * mm, "end": v(103.36, -25.61) * mm});
            skArc(sketch, "E3456", {"start": v(103.36, -25.61) * mm, "mid": v(102.94, -25.53) * mm, "end": v(102.51, -25.46) * mm});
            skArc(sketch, "E3457", {"start": v(102.51, -25.46) * mm, "mid": v(102.13, -25.4) * mm, "end": v(101.73, -25.35) * mm});
            skArc(sketch, "E3458", {"start": v(101.73, -25.35) * mm, "mid": v(101.41, -25.32) * mm, "end": v(101.09, -25.3) * mm});
            skArc(sketch, "E3459", {"start": v(101.09, -25.3) * mm, "mid": v(100.95, -25.3) * mm, "end": v(100.82, -25.33) * mm});
            skArc(sketch, "E3460", {"start": v(100.82, -25.33) * mm, "mid": v(100.63, -25.46) * mm, "end": v(100.52, -25.65) * mm});
            skArc(sketch, "E3461", {"start": v(100.52, -25.65) * mm, "mid": v(100.44, -25.94) * mm, "end": v(100.42, -26.24) * mm});
            skArc(sketch, "E3462", {"start": v(100.42, -26.24) * mm, "mid": v(100.46, -26.57) * mm, "end": v(100.55, -26.88) * mm});
            skArc(sketch, "E3463", {"start": v(100.55, -26.88) * mm, "mid": v(100.69, -27.12) * mm, "end": v(100.88, -27.31) * mm});
            skArc(sketch, "E3464", {"start": v(100.88, -27.31) * mm, "mid": v(101, -27.4) * mm, "end": v(101.12, -27.52) * mm});
            skArc(sketch, "E3465", {"start": v(101.12, -27.52) * mm, "mid": v(101.18, -27.59) * mm, "end": v(101.2, -27.68) * mm});
            skArc(sketch, "E3466", {"start": v(101.2, -27.68) * mm, "mid": v(101.2, -27.77) * mm, "end": v(101.17, -27.85) * mm});
            skArc(sketch, "E3467", {"start": v(101.17, -27.85) * mm, "mid": v(101.08, -27.98) * mm, "end": v(101, -28.1) * mm});
            skArc(sketch, "E3468", {"start": v(101, -28.1) * mm, "mid": v(100.9, -28.23) * mm, "end": v(100.82, -28.36) * mm});
            skArc(sketch, "E3469", {"start": v(100.82, -28.36) * mm, "mid": v(100.78, -28.48) * mm, "end": v(100.78, -28.6) * mm});
            skArc(sketch, "E3470", {"start": v(100.78, -28.6) * mm, "mid": v(100.8, -28.73) * mm, "end": v(100.85, -28.86) * mm});
            skArc(sketch, "E3471", {"start": v(100.85, -28.86) * mm, "mid": v(100.96, -29.06) * mm, "end": v(101.08, -29.25) * mm});
            skArc(sketch, "E3472", {"start": v(101.08, -29.25) * mm, "mid": v(101.19, -29.43) * mm, "end": v(101.27, -29.62) * mm});
            skArc(sketch, "E3473", {"start": v(101.27, -29.62) * mm, "mid": v(101.37, -29.9) * mm, "end": v(101.45, -30.17) * mm});
            skArc(sketch, "E3474", {"start": v(101.45, -30.17) * mm, "mid": v(101.53, -30.48) * mm, "end": v(101.6, -30.8) * mm});
            skArc(sketch, "E3475", {"start": v(101.6, -30.8) * mm, "mid": v(101.64, -31.1) * mm, "end": v(101.68, -31.4) * mm});
            skArc(sketch, "E3476", {"start": v(101.68, -31.4) * mm, "mid": v(101.76, -32.18) * mm, "end": v(101.85, -32.97) * mm});
            skArc(sketch, "E3477", {"start": v(101.85, -32.97) * mm, "mid": v(101.93, -33.5) * mm, "end": v(102.03, -34.02) * mm});
            skArc(sketch, "E3478", {"start": v(102.03, -34.02) * mm, "mid": v(102.13, -34.39) * mm, "end": v(102.25, -34.75) * mm});
            skArc(sketch, "E3479", {"start": v(102.25, -34.75) * mm, "mid": v(102.37, -35) * mm, "end": v(102.54, -35.22) * mm});
            skArc(sketch, "E3480", {"start": v(102.54, -35.22) * mm, "mid": v(102.63, -35.35) * mm, "end": v(102.7, -35.5) * mm});
            skArc(sketch, "E3481", {"start": v(102.7, -35.5) * mm, "mid": v(102.79, -35.74) * mm, "end": v(102.86, -35.99) * mm});
            skArc(sketch, "E3482", {"start": v(102.86, -35.99) * mm, "mid": v(102.94, -36.28) * mm, "end": v(103, -36.57) * mm});
            skArc(sketch, "E3483", {"start": v(103, -36.57) * mm, "mid": v(103.05, -36.88) * mm, "end": v(103.09, -37.18) * mm});
            skArc(sketch, "E3484", {"start": v(103.09, -37.18) * mm, "mid": v(103.13, -37.64) * mm, "end": v(103.16, -38.09) * mm});
            skArc(sketch, "E3485", {"start": v(103.16, -38.09) * mm, "mid": v(103.15, -38.32) * mm, "end": v(103.1, -38.55) * mm});
            skArc(sketch, "E3486", {"start": v(103.1, -38.55) * mm, "mid": v(103.03, -38.73) * mm, "end": v(102.91, -38.89) * mm});
            skArc(sketch, "E3487", {"start": v(102.91, -38.89) * mm, "mid": v(102.7, -39.1) * mm, "end": v(102.48, -39.28) * mm});
            skArc(sketch, "E3488", {"start": v(102.48, -39.28) * mm, "mid": v(102.1, -39.53) * mm, "end": v(101.68, -39.7) * mm});
            skArc(sketch, "E3489", {"start": v(101.68, -39.7) * mm, "mid": v(101.2, -39.82) * mm, "end": v(100.69, -39.87) * mm});
            skArc(sketch, "E3490", {"start": v(100.69, -39.87) * mm, "mid": v(100.17, -39.86) * mm, "end": v(99.66, -39.78) * mm});
            skArc(sketch, "E3491", {"start": v(99.66, -39.78) * mm, "mid": v(99.2, -39.64) * mm, "end": v(98.76, -39.43) * mm});
            skArc(sketch, "E3492", {"start": v(98.76, -39.43) * mm, "mid": v(98.18, -39) * mm, "end": v(97.7, -38.43) * mm});
            skArc(sketch, "E3493", {"start": v(97.7, -38.43) * mm, "mid": v(97.34, -37.76) * mm, "end": v(97.12, -37.03) * mm});
            skArc(sketch, "E3494", {"start": v(97.12, -37.03) * mm, "mid": v(96.99, -36.07) * mm, "end": v(97, -35.1) * mm});
            skArc(sketch, "E3495", {"start": v(97, -35.1) * mm, "mid": v(97.13, -33.8) * mm, "end": v(97.34, -32.52) * mm});
            skArc(sketch, "E3496", {"start": v(97.34, -32.52) * mm, "mid": v(97.46, -31.8) * mm, "end": v(97.55, -31.1) * mm});
            skArc(sketch, "E3497", {"start": v(97.55, -31.1) * mm, "mid": v(97.58, -30.55) * mm, "end": v(97.55, -30.02) * mm});
            skArc(sketch, "E3498", {"start": v(97.55, -30.02) * mm, "mid": v(97.47, -29.67) * mm, "end": v(97.34, -29.34) * mm});
            skArc(sketch, "E3499", {"start": v(97.34, -29.34) * mm, "mid": v(97.18, -29.17) * mm, "end": v(96.96, -29.1) * mm});
            skArc(sketch, "E3500", {"start": v(96.96, -29.1) * mm, "mid": v(96.7, -29.15) * mm, "end": v(96.5, -29.3) * mm});
            skArc(sketch, "E3501", {"start": v(96.5, -29.3) * mm, "mid": v(96.26, -29.58) * mm, "end": v(96.07, -29.9) * mm});
            skArc(sketch, "E3502", {"start": v(96.07, -29.9) * mm, "mid": v(95.86, -30.34) * mm, "end": v(95.7, -30.8) * mm});
            skArc(sketch, "E3503", {"start": v(95.7, -30.8) * mm, "mid": v(95.55, -31.37) * mm, "end": v(95.44, -31.96) * mm});
            skArc(sketch, "E3504", {"start": v(95.44, -31.96) * mm, "mid": v(95.39, -32.27) * mm, "end": v(95.33, -32.58) * mm});
            skArc(sketch, "E3505", {"start": v(95.33, -32.58) * mm, "mid": v(95.26, -32.89) * mm, "end": v(95.19, -33.2) * mm});
            skArc(sketch, "E3506", {"start": v(95.19, -33.2) * mm, "mid": v(95.12, -33.45) * mm, "end": v(95.04, -33.71) * mm});
            skArc(sketch, "E3507", {"start": v(95.04, -33.71) * mm, "mid": v(95, -33.86) * mm, "end": v(94.92, -34) * mm});
            skArc(sketch, "E3508", {"start": v(94.92, -34) * mm, "mid": v(94.87, -34.12) * mm, "end": v(94.83, -34.24) * mm});
            skArc(sketch, "E3509", {"start": v(94.83, -34.24) * mm, "mid": v(94.8, -34.4) * mm, "end": v(94.78, -34.57) * mm});
            skArc(sketch, "E3510", {"start": v(94.78, -34.57) * mm, "mid": v(94.77, -34.75) * mm, "end": v(94.76, -34.93) * mm});
            skArc(sketch, "E3511", {"start": v(94.76, -34.93) * mm, "mid": v(94.78, -35.1) * mm, "end": v(94.8, -35.26) * mm});
            skArc(sketch, "E3512", {"start": v(94.8, -35.26) * mm, "mid": v(94.82, -35.4) * mm, "end": v(94.84, -35.55) * mm});
            skArc(sketch, "E3513", {"start": v(94.84, -35.55) * mm, "mid": v(94.85, -35.67) * mm, "end": v(94.84, -35.8) * mm});
            skArc(sketch, "E3514", {"start": v(94.84, -35.8) * mm, "mid": v(94.83, -35.88) * mm, "end": v(94.8, -35.96) * mm});
            skArc(sketch, "E3515", {"start": v(94.8, -35.96) * mm, "mid": v(94.77, -36) * mm, "end": v(94.73, -36.01) * mm});
            skArc(sketch, "E3516", {"start": v(94.73, -36.01) * mm, "mid": v(94.56, -35.99) * mm, "end": v(94.41, -35.9) * mm});
            skArc(sketch, "E3517", {"start": v(94.41, -35.9) * mm, "mid": v(94.19, -35.72) * mm, "end": v(93.98, -35.52) * mm});
            skArc(sketch, "E3518", {"start": v(93.98, -35.52) * mm, "mid": v(93.78, -35.3) * mm, "end": v(93.6, -35.08) * mm});
            skArc(sketch, "E3519", {"start": v(93.6, -35.08) * mm, "mid": v(93.53, -34.93) * mm, "end": v(93.5, -34.76) * mm});
            skArc(sketch, "E3520", {"start": v(93.5, -34.76) * mm, "mid": v(93.46, -34.57) * mm, "end": v(93.37, -34.42) * mm});
            skArc(sketch, "E3521", {"start": v(93.37, -34.42) * mm, "mid": v(93.22, -34.3) * mm, "end": v(93.05, -34.26) * mm});
            skArc(sketch, "E3522", {"start": v(93.05, -34.26) * mm, "mid": v(92.83, -34.28) * mm, "end": v(92.63, -34.35) * mm});
            skArc(sketch, "E3523", {"start": v(92.63, -34.35) * mm, "mid": v(92.44, -34.5) * mm, "end": v(92.29, -34.67) * mm});
            skLineSegment(sketch, "E3524", {"start": v(92.29, -34.67) * mm, "end": v(91.89, -35.24) * mm});
            skLineSegment(sketch, "E3525", {"start": v(91.89, -35.24) * mm, "end": v(91.59, -34.68) * mm});
            skArc(sketch, "E3526", {"start": v(91.59, -34.68) * mm, "mid": v(91.52, -34.52) * mm, "end": v(91.46, -34.37) * mm});
            skArc(sketch, "E3527", {"start": v(91.46, -34.37) * mm, "mid": v(91.45, -34.25) * mm, "end": v(91.47, -34.13) * mm});
            skArc(sketch, "E3528", {"start": v(91.47, -34.13) * mm, "mid": v(91.52, -34) * mm, "end": v(91.6, -33.9) * mm});
            skArc(sketch, "E3529", {"start": v(91.6, -33.9) * mm, "mid": v(91.76, -33.75) * mm, "end": v(91.92, -33.61) * mm});
            skArc(sketch, "E3530", {"start": v(91.92, -33.61) * mm, "mid": v(92.17, -33.4) * mm, "end": v(92.4, -33.15) * mm});
            skArc(sketch, "E3531", {"start": v(92.4, -33.15) * mm, "mid": v(92.57, -32.92) * mm, "end": v(92.71, -32.67) * mm});
            skArc(sketch, "E3532", {"start": v(92.71, -32.67) * mm, "mid": v(92.8, -32.43) * mm, "end": v(92.83, -32.18) * mm});
            skArc(sketch, "E3533", {"start": v(92.83, -32.18) * mm, "mid": v(92.83, -31.95) * mm, "end": v(92.77, -31.73) * mm});
            skArc(sketch, "E3534", {"start": v(92.77, -31.73) * mm, "mid": v(92.66, -31.55) * mm, "end": v(92.5, -31.41) * mm});
            skArc(sketch, "E3535", {"start": v(92.5, -31.41) * mm, "mid": v(92.32, -31.35) * mm, "end": v(92.13, -31.36) * mm});
            skArc(sketch, "E3536", {"start": v(92.13, -31.36) * mm, "mid": v(91.86, -31.46) * mm, "end": v(91.63, -31.62) * mm});
            skArc(sketch, "E3537", {"start": v(91.63, -31.62) * mm, "mid": v(91.31, -31.9) * mm, "end": v(91.01, -32.21) * mm});
            skLineSegment(sketch, "E3538", {"start": v(91.01, -32.21) * mm, "end": v(90.2, -33.11) * mm});
            skLineSegment(sketch, "E3539", {"start": v(90.2, -33.11) * mm, "end": v(90.19, -32.3) * mm});
            skArc(sketch, "E3540", {"start": v(90.19, -32.3) * mm, "mid": v(90.2, -32.07) * mm, "end": v(90.25, -31.85) * mm});
            skArc(sketch, "E3541", {"start": v(90.25, -31.85) * mm, "mid": v(90.34, -31.63) * mm, "end": v(90.45, -31.41) * mm});
            skArc(sketch, "E3542", {"start": v(90.45, -31.41) * mm, "mid": v(90.63, -31.17) * mm, "end": v(90.82, -30.94) * mm});
            skArc(sketch, "E3543", {"start": v(90.82, -30.94) * mm, "mid": v(91.11, -30.63) * mm, "end": v(91.42, -30.34) * mm});
            skLineSegment(sketch, "E3544", {"start": v(91.42, -30.34) * mm, "end": v(92.66, -29.18) * mm});
            skLineSegment(sketch, "E3545", {"start": v(92.66, -29.18) * mm, "end": v(92.09, -28) * mm});
            skArc(sketch, "E3546", {"start": v(92.09, -28) * mm, "mid": v(91.95, -27.7) * mm, "end": v(91.83, -27.4) * mm});
            skArc(sketch, "E3547", {"start": v(91.83, -27.4) * mm, "mid": v(91.75, -27.14) * mm, "end": v(91.69, -26.87) * mm});
            skArc(sketch, "E3548", {"start": v(91.69, -26.87) * mm, "mid": v(91.65, -26.62) * mm, "end": v(91.64, -26.37) * mm});
            skArc(sketch, "E3549", {"start": v(91.64, -26.37) * mm, "mid": v(91.66, -26.12) * mm, "end": v(91.7, -25.86) * mm});
            skArc(sketch, "E3550", {"start": v(91.7, -25.86) * mm, "mid": v(91.74, -25.6) * mm, "end": v(91.77, -25.34) * mm});
            skArc(sketch, "E3551", {"start": v(91.77, -25.34) * mm, "mid": v(91.77, -25.2) * mm, "end": v(91.74, -25.06) * mm});
            skArc(sketch, "E3552", {"start": v(91.74, -25.06) * mm, "mid": v(91.68, -24.96) * mm, "end": v(91.6, -24.88) * mm});
            skArc(sketch, "E3553", {"start": v(91.6, -24.88) * mm, "mid": v(91.45, -24.81) * mm, "end": v(91.3, -24.76) * mm});
            skArc(sketch, "E3554", {"start": v(91.3, -24.76) * mm, "mid": v(91.2, -24.72) * mm, "end": v(91.09, -24.67) * mm});
            skArc(sketch, "E3555", {"start": v(91.09, -24.67) * mm, "mid": v(90.99, -24.6) * mm, "end": v(90.9, -24.51) * mm});
            skArc(sketch, "E3556", {"start": v(90.9, -24.51) * mm, "mid": v(90.83, -24.42) * mm, "end": v(90.78, -24.32) * mm});
            skArc(sketch, "E3557", {"start": v(90.78, -24.32) * mm, "mid": v(90.74, -24.23) * mm, "end": v(90.73, -24.13) * mm});
            skArc(sketch, "E3558", {"start": v(90.73, -24.13) * mm, "mid": v(90.72, -24) * mm, "end": v(90.66, -23.9) * mm});
            skArc(sketch, "E3559", {"start": v(90.66, -23.9) * mm, "mid": v(90.58, -23.79) * mm, "end": v(90.47, -23.7) * mm});
            skArc(sketch, "E3560", {"start": v(90.47, -23.7) * mm, "mid": v(90.3, -23.63) * mm, "end": v(90.13, -23.57) * mm});
            skArc(sketch, "E3561", {"start": v(90.13, -23.57) * mm, "mid": v(89.86, -23.5) * mm, "end": v(89.58, -23.46) * mm});
            skArc(sketch, "E3562", {"start": v(89.58, -23.46) * mm, "mid": v(89.35, -23.43) * mm, "end": v(89.12, -23.4) * mm});
            skArc(sketch, "E3563", {"start": v(89.12, -23.4) * mm, "mid": v(88.91, -23.4) * mm, "end": v(88.7, -23.4) * mm});
            skArc(sketch, "E3564", {"start": v(88.7, -23.4) * mm, "mid": v(88.53, -23.4) * mm, "end": v(88.36, -23.43) * mm});
            skArc(sketch, "E3565", {"start": v(88.36, -23.43) * mm, "mid": v(88.27, -23.45) * mm, "end": v(88.2, -23.5) * mm});
            skArc(sketch, "E3566", {"start": v(88.2, -23.5) * mm, "mid": v(88.15, -23.58) * mm, "end": v(88.14, -23.67) * mm});
            skArc(sketch, "E3567", {"start": v(88.14, -23.67) * mm, "mid": v(88.16, -23.84) * mm, "end": v(88.2, -24) * mm});
            skArc(sketch, "E3568", {"start": v(88.2, -24) * mm, "mid": v(88.25, -24.22) * mm, "end": v(88.33, -24.43) * mm});
            skArc(sketch, "E3569", {"start": v(88.33, -24.43) * mm, "mid": v(88.42, -24.66) * mm, "end": v(88.52, -24.89) * mm});
            skArc(sketch, "E3570", {"start": v(88.52, -24.89) * mm, "mid": v(88.76, -25.41) * mm, "end": v(89, -25.95) * mm});
            skArc(sketch, "E3571", {"start": v(89, -25.95) * mm, "mid": v(89.06, -26.2) * mm, "end": v(89.07, -26.48) * mm});
            skArc(sketch, "E3572", {"start": v(89.07, -26.48) * mm, "mid": v(89, -26.62) * mm, "end": v(88.86, -26.68) * mm});
            skArc(sketch, "E3573", {"start": v(88.86, -26.68) * mm, "mid": v(88.6, -26.67) * mm, "end": v(88.37, -26.6) * mm});
            skArc(sketch, "E3574", {"start": v(88.37, -26.6) * mm, "mid": v(87.92, -26.46) * mm, "end": v(87.47, -26.34) * mm});
            skArc(sketch, "E3575", {"start": v(87.47, -26.34) * mm, "mid": v(87.25, -26.35) * mm, "end": v(87.08, -26.48) * mm});
            skArc(sketch, "E3576", {"start": v(87.08, -26.48) * mm, "mid": v(86.95, -26.72) * mm, "end": v(86.9, -26.99) * mm});
            skArc(sketch, "E3577", {"start": v(86.9, -26.99) * mm, "mid": v(86.87, -27.77) * mm, "end": v(86.86, -28.55) * mm});
            skArc(sketch, "E3578", {"start": v(86.86, -28.55) * mm, "mid": v(86.86, -29.26) * mm, "end": v(86.85, -29.98) * mm});
            skArc(sketch, "E3579", {"start": v(86.85, -29.98) * mm, "mid": v(86.83, -30.23) * mm, "end": v(86.77, -30.47) * mm});
            skArc(sketch, "E3580", {"start": v(86.77, -30.47) * mm, "mid": v(86.7, -30.6) * mm, "end": v(86.57, -30.68) * mm});
            skArc(sketch, "E3581", {"start": v(86.57, -30.68) * mm, "mid": v(86.38, -30.74) * mm, "end": v(86.18, -30.76) * mm});
            skArc(sketch, "E3582", {"start": v(86.18, -30.76) * mm, "mid": v(85.99, -30.77) * mm, "end": v(85.8, -30.8) * mm});
            skArc(sketch, "E3583", {"start": v(85.8, -30.8) * mm, "mid": v(85.7, -30.86) * mm, "end": v(85.62, -30.95) * mm});
            skArc(sketch, "E3584", {"start": v(85.62, -30.95) * mm, "mid": v(85.58, -31.1) * mm, "end": v(85.57, -31.26) * mm});
            skArc(sketch, "E3585", {"start": v(85.57, -31.26) * mm, "mid": v(85.6, -31.66) * mm, "end": v(85.64, -32.07) * mm});
            skArc(sketch, "E3586", {"start": v(85.64, -32.07) * mm, "mid": v(85.67, -32.34) * mm, "end": v(85.68, -32.6) * mm});
            skArc(sketch, "E3587", {"start": v(85.68, -32.6) * mm, "mid": v(85.67, -32.86) * mm, "end": v(85.66, -33.12) * mm});
            skArc(sketch, "E3588", {"start": v(85.66, -33.12) * mm, "mid": v(85.63, -33.34) * mm, "end": v(85.6, -33.56) * mm});
            skArc(sketch, "E3589", {"start": v(85.6, -33.56) * mm, "mid": v(85.56, -33.68) * mm, "end": v(85.5, -33.8) * mm});
            skArc(sketch, "E3590", {"start": v(85.5, -33.8) * mm, "mid": v(85.35, -33.92) * mm, "end": v(85.17, -33.96) * mm});
            skArc(sketch, "E3591", {"start": v(85.17, -33.96) * mm, "mid": v(85, -33.9) * mm, "end": v(84.89, -33.76) * mm});
            skArc(sketch, "E3592", {"start": v(84.89, -33.76) * mm, "mid": v(84.78, -33.42) * mm, "end": v(84.74, -33.06) * mm});
            skArc(sketch, "E3593", {"start": v(84.74, -33.06) * mm, "mid": v(84.75, -32.57) * mm, "end": v(84.79, -32.07) * mm});
            skArc(sketch, "E3594", {"start": v(84.79, -32.07) * mm, "mid": v(84.83, -31.69) * mm, "end": v(84.87, -31.3) * mm});
            skArc(sketch, "E3595", {"start": v(84.87, -31.3) * mm, "mid": v(84.86, -31.13) * mm, "end": v(84.83, -30.97) * mm});
            skArc(sketch, "E3596", {"start": v(84.83, -30.97) * mm, "mid": v(84.77, -30.88) * mm, "end": v(84.68, -30.81) * mm});
            skArc(sketch, "E3597", {"start": v(84.68, -30.81) * mm, "mid": v(84.54, -30.77) * mm, "end": v(84.38, -30.76) * mm});
            skArc(sketch, "E3598", {"start": v(84.38, -30.76) * mm, "mid": v(84.23, -30.74) * mm, "end": v(84.08, -30.67) * mm});
            skArc(sketch, "E3599", {"start": v(84.08, -30.67) * mm, "mid": v(83.97, -30.58) * mm, "end": v(83.9, -30.45) * mm});
            skArc(sketch, "E3600", {"start": v(83.9, -30.45) * mm, "mid": v(83.85, -30.21) * mm, "end": v(83.82, -29.97) * mm});
            skArc(sketch, "E3601", {"start": v(83.82, -29.97) * mm, "mid": v(83.8, -29.4) * mm, "end": v(83.79, -28.82) * mm});
            skArc(sketch, "E3602", {"start": v(83.79, -28.82) * mm, "mid": v(83.76, -27.66) * mm, "end": v(83.73, -26.49) * mm});
            skArc(sketch, "E3603", {"start": v(83.73, -26.49) * mm, "mid": v(83.69, -26.2) * mm, "end": v(83.58, -25.92) * mm});
            skArc(sketch, "E3604", {"start": v(83.58, -25.92) * mm, "mid": v(83.42, -25.73) * mm, "end": v(83.2, -25.63) * mm});
            skArc(sketch, "E3605", {"start": v(83.2, -25.63) * mm, "mid": v(82.62, -25.51) * mm, "end": v(82.02, -25.42) * mm});
            skArc(sketch, "E3606", {"start": v(82.02, -25.42) * mm, "mid": v(81.21, -25.34) * mm, "end": v(80.4, -25.3) * mm});
            skArc(sketch, "E3607", {"start": v(80.4, -25.3) * mm, "mid": v(79.28, -25.3) * mm, "end": v(78.16, -25.32) * mm});
            skArc(sketch, "E3608", {"start": v(78.16, -25.32) * mm, "mid": v(77.06, -25.36) * mm, "end": v(75.95, -25.42) * mm});
            skArc(sketch, "E3609", {"start": v(75.95, -25.42) * mm, "mid": v(75.6, -25.48) * mm, "end": v(75.27, -25.63) * mm});
            skArc(sketch, "E3610", {"start": v(75.27, -25.63) * mm, "mid": v(75.21, -25.7) * mm, "end": v(75.2, -25.79) * mm});
            skArc(sketch, "E3611", {"start": v(75.2, -25.79) * mm, "mid": v(75.22, -25.92) * mm, "end": v(75.27, -26.05) * mm});
            skArc(sketch, "E3612", {"start": v(75.27, -26.05) * mm, "mid": v(75.38, -26.24) * mm, "end": v(75.51, -26.42) * mm});
            skArc(sketch, "E3613", {"start": v(75.51, -26.42) * mm, "mid": v(75.72, -26.67) * mm, "end": v(75.93, -26.91) * mm});
            skArc(sketch, "E3614", {"start": v(75.93, -26.91) * mm, "mid": v(76.12, -27.13) * mm, "end": v(76.3, -27.35) * mm});
            skArc(sketch, "E3615", {"start": v(76.3, -27.35) * mm, "mid": v(76.47, -27.55) * mm, "end": v(76.62, -27.76) * mm});
            skArc(sketch, "E3616", {"start": v(76.62, -27.76) * mm, "mid": v(76.74, -27.94) * mm, "end": v(76.86, -28.12) * mm});
            skArc(sketch, "E3617", {"start": v(76.86, -28.12) * mm, "mid": v(76.9, -28.2) * mm, "end": v(76.9, -28.29) * mm});
            skArc(sketch, "E3618", {"start": v(76.9, -28.29) * mm, "mid": v(76.88, -28.37) * mm, "end": v(76.81, -28.41) * mm});
            skArc(sketch, "E3619", {"start": v(76.81, -28.41) * mm, "mid": v(76.63, -28.45) * mm, "end": v(76.44, -28.47) * mm});
            skArc(sketch, "E3620", {"start": v(76.44, -28.47) * mm, "mid": v(76.15, -28.48) * mm, "end": v(75.86, -28.47) * mm});
            skArc(sketch, "E3621", {"start": v(75.86, -28.47) * mm, "mid": v(75.45, -28.45) * mm, "end": v(75.04, -28.42) * mm});
            skArc(sketch, "E3622", {"start": v(75.04, -28.42) * mm, "mid": v(74.64, -28.39) * mm, "end": v(74.23, -28.37) * mm});
            skArc(sketch, "E3623", {"start": v(74.23, -28.37) * mm, "mid": v(73.78, -28.36) * mm, "end": v(73.32, -28.37) * mm});
            skArc(sketch, "E3624", {"start": v(73.32, -28.37) * mm, "mid": v(72.9, -28.38) * mm, "end": v(72.47, -28.4) * mm});
            skArc(sketch, "E3625", {"start": v(72.47, -28.4) * mm, "mid": v(72.14, -28.43) * mm, "end": v(71.81, -28.47) * mm});
            skLineSegment(sketch, "E3626", {"start": v(71.81, -28.47) * mm, "end": v(70.45, -28.69) * mm});
            skLineSegment(sketch, "E3627", {"start": v(70.45, -28.69) * mm, "end": v(70.43, -31.04) * mm});
            skArc(sketch, "E3628", {"start": v(70.43, -31.04) * mm, "mid": v(70.42, -31.58) * mm, "end": v(70.4, -32.13) * mm});
            skArc(sketch, "E3629", {"start": v(70.4, -32.13) * mm, "mid": v(70.38, -32.49) * mm, "end": v(70.33, -32.84) * mm});
            skArc(sketch, "E3630", {"start": v(70.33, -32.84) * mm, "mid": v(70.3, -33.07) * mm, "end": v(70.23, -33.29) * mm});
            skArc(sketch, "E3631", {"start": v(70.23, -33.29) * mm, "mid": v(70.17, -33.38) * mm, "end": v(70.07, -33.42) * mm});
            skArc(sketch, "E3632", {"start": v(70.07, -33.42) * mm, "mid": v(69.99, -33.43) * mm, "end": v(69.91, -33.44) * mm});
            skArc(sketch, "E3633", {"start": v(69.91, -33.44) * mm, "mid": v(69.83, -33.45) * mm, "end": v(69.74, -33.46) * mm});
            skArc(sketch, "E3634", {"start": v(69.74, -33.46) * mm, "mid": v(69.66, -33.46) * mm, "end": v(69.57, -33.47) * mm});
            skArc(sketch, "E3635", {"start": v(69.57, -33.47) * mm, "mid": v(69.5, -33.48) * mm, "end": v(69.44, -33.5) * mm});
            skArc(sketch, "E3636", {"start": v(69.44, -33.5) * mm, "mid": v(69.37, -33.52) * mm, "end": v(69.33, -33.58) * mm});
            skArc(sketch, "E3637", {"start": v(69.33, -33.58) * mm, "mid": v(69.29, -33.77) * mm, "end": v(69.25, -33.96) * mm});
            skArc(sketch, "E3638", {"start": v(69.25, -33.96) * mm, "mid": v(69.21, -34.2) * mm, "end": v(69.19, -34.45) * mm});
            skArc(sketch, "E3639", {"start": v(69.19, -34.45) * mm, "mid": v(69.17, -34.74) * mm, "end": v(69.17, -35.03) * mm});
            skArc(sketch, "E3640", {"start": v(69.17, -35.03) * mm, "mid": v(69.16, -35.32) * mm, "end": v(69.15, -35.62) * mm});
            skArc(sketch, "E3641", {"start": v(69.15, -35.62) * mm, "mid": v(69.12, -35.88) * mm, "end": v(69.09, -36.14) * mm});
            skArc(sketch, "E3642", {"start": v(69.09, -36.14) * mm, "mid": v(69.05, -36.35) * mm, "end": v(69, -36.56) * mm});
            skArc(sketch, "E3643", {"start": v(69, -36.56) * mm, "mid": v(68.96, -36.64) * mm, "end": v(68.89, -36.7) * mm});
            skArc(sketch, "E3644", {"start": v(68.89, -36.7) * mm, "mid": v(68.73, -36.73) * mm, "end": v(68.6, -36.64) * mm});
            skArc(sketch, "E3645", {"start": v(68.6, -36.64) * mm, "mid": v(68.44, -36.37) * mm, "end": v(68.32, -36.08) * mm});
            skArc(sketch, "E3646", {"start": v(68.32, -36.08) * mm, "mid": v(68.21, -35.67) * mm, "end": v(68.14, -35.25) * mm});
            skArc(sketch, "E3647", {"start": v(68.14, -35.25) * mm, "mid": v(68.11, -34.82) * mm, "end": v(68.12, -34.4) * mm});
            skArc(sketch, "E3648", {"start": v(68.12, -34.4) * mm, "mid": v(68.14, -34.12) * mm, "end": v(68.14, -33.85) * mm});
            skArc(sketch, "E3649", {"start": v(68.14, -33.85) * mm, "mid": v(68.13, -33.72) * mm, "end": v(68.08, -33.58) * mm});
            skArc(sketch, "E3650", {"start": v(68.08, -33.58) * mm, "mid": v(68.02, -33.5) * mm, "end": v(67.93, -33.44) * mm});
            skArc(sketch, "E3651", {"start": v(67.93, -33.44) * mm, "mid": v(67.79, -33.4) * mm, "end": v(67.65, -33.4) * mm});
            skArc(sketch, "E3652", {"start": v(67.65, -33.4) * mm, "mid": v(67.5, -33.38) * mm, "end": v(67.37, -33.34) * mm});
            skArc(sketch, "E3653", {"start": v(67.37, -33.34) * mm, "mid": v(67.27, -33.28) * mm, "end": v(67.2, -33.2) * mm});
            skArc(sketch, "E3654", {"start": v(67.2, -33.2) * mm, "mid": v(67.14, -33.07) * mm, "end": v(67.1, -32.93) * mm});
            skArc(sketch, "E3655", {"start": v(67.1, -32.93) * mm, "mid": v(67.09, -32.68) * mm, "end": v(67.08, -32.44) * mm});
            skArc(sketch, "E3656", {"start": v(67.08, -32.44) * mm, "mid": v(67.07, -32.25) * mm, "end": v(67.05, -32.07) * mm});
            skArc(sketch, "E3657", {"start": v(67.05, -32.07) * mm, "mid": v(67.02, -31.9) * mm, "end": v(66.98, -31.74) * mm});
            skArc(sketch, "E3658", {"start": v(66.98, -31.74) * mm, "mid": v(66.94, -31.61) * mm, "end": v(66.88, -31.49) * mm});
            skArc(sketch, "E3659", {"start": v(66.88, -31.49) * mm, "mid": v(66.83, -31.43) * mm, "end": v(66.77, -31.39) * mm});
            skArc(sketch, "E3660", {"start": v(66.77, -31.39) * mm, "mid": v(66.43, -31.38) * mm, "end": v(66.14, -31.55) * mm});
            skArc(sketch, "E3661", {"start": v(66.14, -31.55) * mm, "mid": v(65.46, -32.33) * mm, "end": v(64.8, -33.13) * mm});
            skArc(sketch, "E3662", {"start": v(64.8, -33.13) * mm, "mid": v(64.15, -34.02) * mm, "end": v(63.54, -34.94) * mm});
            skArc(sketch, "E3663", {"start": v(63.54, -34.94) * mm, "mid": v(63.1, -35.72) * mm, "end": v(62.74, -36.53) * mm});
            skArc(sketch, "E3664", {"start": v(62.74, -36.53) * mm, "mid": v(62.36, -37.52) * mm, "end": v(62, -38.51) * mm});
            skArc(sketch, "E3665", {"start": v(62, -38.51) * mm, "mid": v(61.98, -38.76) * mm, "end": v(62.07, -39) * mm});
            skArc(sketch, "E3666", {"start": v(62.07, -39) * mm, "mid": v(62.23, -39.11) * mm, "end": v(62.43, -39.07) * mm});
            skArc(sketch, "E3667", {"start": v(62.43, -39.07) * mm, "mid": v(63.12, -38.59) * mm, "end": v(63.8, -38.09) * mm});
            skArc(sketch, "E3668", {"start": v(63.8, -38.09) * mm, "mid": v(64.36, -37.67) * mm, "end": v(64.93, -37.27) * mm});
            skArc(sketch, "E3669", {"start": v(64.93, -37.27) * mm, "mid": v(65.17, -37.15) * mm, "end": v(65.43, -37.12) * mm});
            skArc(sketch, "E3670", {"start": v(65.43, -37.12) * mm, "mid": v(65.58, -37.2) * mm, "end": v(65.62, -37.36) * mm});
            skArc(sketch, "E3671", {"start": v(65.62, -37.36) * mm, "mid": v(65.53, -37.76) * mm, "end": v(65.41, -38.16) * mm});
            skArc(sketch, "E3672", {"start": v(65.41, -38.16) * mm, "mid": v(65.34, -38.38) * mm, "end": v(65.27, -38.61) * mm});
            skArc(sketch, "E3673", {"start": v(65.27, -38.61) * mm, "mid": v(65.2, -38.86) * mm, "end": v(65.15, -39.12) * mm});
            skArc(sketch, "E3674", {"start": v(65.15, -39.12) * mm, "mid": v(65.1, -39.36) * mm, "end": v(65.06, -39.6) * mm});
            skArc(sketch, "E3675", {"start": v(65.06, -39.6) * mm, "mid": v(65.04, -39.79) * mm, "end": v(65.03, -39.97) * mm});
            skArc(sketch, "E3676", {"start": v(65.03, -39.97) * mm, "mid": v(65.03, -40.19) * mm, "end": v(65.04, -40.4) * mm});
            skArc(sketch, "E3677", {"start": v(65.04, -40.4) * mm, "mid": v(65.07, -40.5) * mm, "end": v(65.13, -40.59) * mm});
            skArc(sketch, "E3678", {"start": v(65.13, -40.59) * mm, "mid": v(65.2, -40.63) * mm, "end": v(65.3, -40.64) * mm});
            skArc(sketch, "E3679", {"start": v(65.3, -40.64) * mm, "mid": v(65.47, -40.61) * mm, "end": v(65.64, -40.57) * mm});
            skArc(sketch, "E3680", {"start": v(65.64, -40.57) * mm, "mid": v(66.3, -40.36) * mm, "end": v(66.92, -40.1) * mm});
            skArc(sketch, "E3681", {"start": v(66.92, -40.1) * mm, "mid": v(67.6, -39.74) * mm, "end": v(68.27, -39.36) * mm});
            skArc(sketch, "E3682", {"start": v(68.27, -39.36) * mm, "mid": v(68.97, -38.9) * mm, "end": v(69.64, -38.41) * mm});
            skArc(sketch, "E3683", {"start": v(69.64, -38.41) * mm, "mid": v(70.32, -37.86) * mm, "end": v(70.97, -37.28) * mm});
            skArc(sketch, "E3684", {"start": v(70.97, -37.28) * mm, "mid": v(71.34, -36.93) * mm, "end": v(71.72, -36.6) * mm});
            skArc(sketch, "E3685", {"start": v(71.72, -36.6) * mm, "mid": v(72.05, -36.3) * mm, "end": v(72.38, -36) * mm});
            skArc(sketch, "E3686", {"start": v(72.38, -36) * mm, "mid": v(72.67, -35.76) * mm, "end": v(72.95, -35.52) * mm});
            skArc(sketch, "E3687", {"start": v(72.95, -35.52) * mm, "mid": v(73, -35.49) * mm, "end": v(73.06, -35.47) * mm});
            skArc(sketch, "E3688", {"start": v(73.06, -35.47) * mm, "mid": v(73.1, -35.49) * mm, "end": v(73.12, -35.52) * mm});
            skArc(sketch, "E3689", {"start": v(73.12, -35.52) * mm, "mid": v(73.12, -35.68) * mm, "end": v(73.12, -35.83) * mm});
            skArc(sketch, "E3690", {"start": v(73.12, -35.83) * mm, "mid": v(73.11, -36.03) * mm, "end": v(73.1, -36.23) * mm});
            skArc(sketch, "E3691", {"start": v(73.1, -36.23) * mm, "mid": v(73.07, -36.47) * mm, "end": v(73.04, -36.71) * mm});
            skArc(sketch, "E3692", {"start": v(73.04, -36.71) * mm, "mid": v(73, -36.96) * mm, "end": v(72.98, -37.2) * mm});
            skArc(sketch, "E3693", {"start": v(72.98, -37.2) * mm, "mid": v(72.96, -37.42) * mm, "end": v(72.96, -37.64) * mm});
            skArc(sketch, "E3694", {"start": v(72.96, -37.64) * mm, "mid": v(72.96, -37.8) * mm, "end": v(72.97, -37.98) * mm});
            skArc(sketch, "E3695", {"start": v(72.97, -37.98) * mm, "mid": v(73, -38.04) * mm, "end": v(73.04, -38.09) * mm});
            skArc(sketch, "E3696", {"start": v(73.04, -38.09) * mm, "mid": v(73.11, -38.11) * mm, "end": v(73.19, -38.1) * mm});
            skArc(sketch, "E3697", {"start": v(73.19, -38.1) * mm, "mid": v(73.52, -37.92) * mm, "end": v(73.84, -37.74) * mm});
            skArc(sketch, "E3698", {"start": v(73.84, -37.74) * mm, "mid": v(74.23, -37.52) * mm, "end": v(74.61, -37.29) * mm});
            skArc(sketch, "E3699", {"start": v(74.61, -37.29) * mm, "mid": v(75.06, -37) * mm, "end": v(75.5, -36.73) * mm});
            skArc(sketch, "E3700", {"start": v(75.5, -36.73) * mm, "mid": v(76.45, -36.1) * mm, "end": v(77.41, -35.5) * mm});
            skArc(sketch, "E3701", {"start": v(77.41, -35.5) * mm, "mid": v(78.08, -35.13) * mm, "end": v(78.76, -34.79) * mm});
            skArc(sketch, "E3702", {"start": v(78.76, -34.79) * mm, "mid": v(79.31, -34.55) * mm, "end": v(79.88, -34.36) * mm});
            skArc(sketch, "E3703", {"start": v(79.88, -34.36) * mm, "mid": v(80.44, -34.23) * mm, "end": v(81, -34.14) * mm});
            skArc(sketch, "E3704", {"start": v(81, -34.14) * mm, "mid": v(81.38, -34.1) * mm, "end": v(81.76, -34.06) * mm});
            skArc(sketch, "E3705", {"start": v(81.76, -34.06) * mm, "mid": v(81.9, -34.07) * mm, "end": v(82.02, -34.1) * mm});
            skArc(sketch, "E3706", {"start": v(82.02, -34.1) * mm, "mid": v(82.09, -34.17) * mm, "end": v(82.11, -34.26) * mm});
            skArc(sketch, "E3707", {"start": v(82.11, -34.26) * mm, "mid": v(82.1, -34.43) * mm, "end": v(82.05, -34.6) * mm});
            skArc(sketch, "E3708", {"start": v(82.05, -34.6) * mm, "mid": v(82.02, -34.72) * mm, "end": v(81.98, -34.85) * mm});
            skArc(sketch, "E3709", {"start": v(81.98, -34.85) * mm, "mid": v(81.94, -35) * mm, "end": v(81.9, -35.16) * mm});
            skArc(sketch, "E3710", {"start": v(81.9, -35.16) * mm, "mid": v(81.85, -35.3) * mm, "end": v(81.81, -35.45) * mm});
            skArc(sketch, "E3711", {"start": v(81.81, -35.45) * mm, "mid": v(81.78, -35.57) * mm, "end": v(81.74, -35.69) * mm});
            skArc(sketch, "E3712", {"start": v(81.74, -35.69) * mm, "mid": v(81.73, -35.83) * mm, "end": v(81.77, -35.96) * mm});
            skArc(sketch, "E3713", {"start": v(81.77, -35.96) * mm, "mid": v(81.85, -36.08) * mm, "end": v(81.97, -36.15) * mm});
            skArc(sketch, "E3714", {"start": v(81.97, -36.15) * mm, "mid": v(82.2, -36.24) * mm, "end": v(82.45, -36.3) * mm});
            skArc(sketch, "E3715", {"start": v(82.45, -36.3) * mm, "mid": v(83, -36.4) * mm, "end": v(83.54, -36.5) * mm});
            skArc(sketch, "E3716", {"start": v(83.54, -36.5) * mm, "mid": v(83.96, -36.56) * mm, "end": v(84.37, -36.65) * mm});
            skArc(sketch, "E3717", {"start": v(84.37, -36.65) * mm, "mid": v(84.83, -36.76) * mm, "end": v(85.28, -36.88) * mm});
            skArc(sketch, "E3718", {"start": v(85.28, -36.88) * mm, "mid": v(85.7, -37.01) * mm, "end": v(86.13, -37.15) * mm});
            skArc(sketch, "E3719", {"start": v(86.13, -37.15) * mm, "mid": v(86.45, -37.27) * mm, "end": v(86.76, -37.41) * mm});
            skLineSegment(sketch, "E3720", {"start": v(86.76, -37.41) * mm, "end": v(88.04, -38.03) * mm});
            skLineSegment(sketch, "E3721", {"start": v(88.04, -38.03) * mm, "end": v(87.24, -38.45) * mm});
            skArc(sketch, "E3722", {"start": v(87.24, -38.45) * mm, "mid": v(87.03, -38.55) * mm, "end": v(86.8, -38.62) * mm});
            skArc(sketch, "E3723", {"start": v(86.8, -38.62) * mm, "mid": v(86.43, -38.71) * mm, "end": v(86.05, -38.79) * mm});
            skArc(sketch, "E3724", {"start": v(86.05, -38.79) * mm, "mid": v(85.62, -38.86) * mm, "end": v(85.18, -38.92) * mm});
            skArc(sketch, "E3725", {"start": v(85.18, -38.92) * mm, "mid": v(84.74, -38.97) * mm, "end": v(84.3, -39) * mm});
            skArc(sketch, "E3726", {"start": v(84.3, -39) * mm, "mid": v(83.88, -39.03) * mm, "end": v(83.47, -39.06) * mm});
            skArc(sketch, "E3727", {"start": v(83.47, -39.06) * mm, "mid": v(83.1, -39.1) * mm, "end": v(82.75, -39.15) * mm});
            skArc(sketch, "E3728", {"start": v(82.75, -39.15) * mm, "mid": v(82.45, -39.2) * mm, "end": v(82.15, -39.24) * mm});
            skArc(sketch, "E3729", {"start": v(82.15, -39.24) * mm, "mid": v(82.08, -39.27) * mm, "end": v(82.03, -39.33) * mm});
            skArc(sketch, "E3730", {"start": v(82.03, -39.33) * mm, "mid": v(82.01, -39.4) * mm, "end": v(82.03, -39.45) * mm});
            skArc(sketch, "E3731", {"start": v(82.03, -39.45) * mm, "mid": v(82.15, -39.6) * mm, "end": v(82.28, -39.75) * mm});
            skArc(sketch, "E3732", {"start": v(82.28, -39.75) * mm, "mid": v(82.45, -39.92) * mm, "end": v(82.63, -40.1) * mm});
            skArc(sketch, "E3733", {"start": v(82.63, -40.1) * mm, "mid": v(82.85, -40.28) * mm, "end": v(83.07, -40.47) * mm});
            skLineSegment(sketch, "E3734", {"start": v(83.07, -40.47) * mm, "end": v(84.24, -41.4) * mm});
            skLineSegment(sketch, "E3735", {"start": v(84.24, -41.4) * mm, "end": v(83.13, -41.54) * mm});
            skLineSegment(sketch, "E3736", {"start": v(83.13, -41.54) * mm, "end": v(82.02, -41.68) * mm});
            skLineSegment(sketch, "E3737", {"start": v(82.02, -41.68) * mm, "end": v(81.94, -43.96) * mm});
            skArc(sketch, "E3738", {"start": v(81.94, -43.96) * mm, "mid": v(81.92, -44.65) * mm, "end": v(81.88, -45.34) * mm});
            skArc(sketch, "E3739", {"start": v(81.88, -45.34) * mm, "mid": v(81.85, -45.62) * mm, "end": v(81.79, -45.89) * mm});
            skArc(sketch, "E3740", {"start": v(81.79, -45.89) * mm, "mid": v(81.72, -46.03) * mm, "end": v(81.6, -46.15) * mm});
            skArc(sketch, "E3741", {"start": v(81.6, -46.15) * mm, "mid": v(81.45, -46.22) * mm, "end": v(81.29, -46.24) * mm});
            skArc(sketch, "E3742", {"start": v(81.29, -46.24) * mm, "mid": v(81.13, -46.26) * mm, "end": v(80.98, -46.3) * mm});
            skArc(sketch, "E3743", {"start": v(80.98, -46.3) * mm, "mid": v(80.9, -46.35) * mm, "end": v(80.84, -46.43) * mm});
            skArc(sketch, "E3744", {"start": v(80.84, -46.43) * mm, "mid": v(80.8, -46.58) * mm, "end": v(80.8, -46.73) * mm});
            skArc(sketch, "E3745", {"start": v(80.8, -46.73) * mm, "mid": v(80.84, -47.07) * mm, "end": v(80.89, -47.42) * mm});
            skArc(sketch, "E3746", {"start": v(80.89, -47.42) * mm, "mid": v(80.93, -47.84) * mm, "end": v(80.94, -48.27) * mm});
            skArc(sketch, "E3747", {"start": v(80.94, -48.27) * mm, "mid": v(80.91, -48.58) * mm, "end": v(80.83, -48.89) * mm});
            skArc(sketch, "E3748", {"start": v(80.83, -48.89) * mm, "mid": v(80.73, -49.05) * mm, "end": v(80.57, -49.17) * mm});
            skArc(sketch, "E3749", {"start": v(80.57, -49.17) * mm, "mid": v(80.4, -49.2) * mm, "end": v(80.23, -49.15) * mm});
            skArc(sketch, "E3750", {"start": v(80.23, -49.15) * mm, "mid": v(80.14, -49.07) * mm, "end": v(80.09, -48.97) * mm});
            skArc(sketch, "E3751", {"start": v(80.09, -48.97) * mm, "mid": v(80.04, -48.81) * mm, "end": v(80, -48.65) * mm});
            skArc(sketch, "E3752", {"start": v(80, -48.65) * mm, "mid": v(79.98, -48.42) * mm, "end": v(79.98, -48.2) * mm});
            skArc(sketch, "E3753", {"start": v(79.98, -48.2) * mm, "mid": v(80, -47.9) * mm, "end": v(80.02, -47.6) * mm});
            skArc(sketch, "E3754", {"start": v(80.02, -47.6) * mm, "mid": v(80.05, -47.18) * mm, "end": v(80.08, -46.77) * mm});
            skArc(sketch, "E3755", {"start": v(80.08, -46.77) * mm, "mid": v(80.07, -46.6) * mm, "end": v(80.03, -46.44) * mm});
            skArc(sketch, "E3756", {"start": v(80.03, -46.44) * mm, "mid": v(79.97, -46.35) * mm, "end": v(79.86, -46.3) * mm});
            skArc(sketch, "E3757", {"start": v(79.86, -46.3) * mm, "mid": v(79.69, -46.26) * mm, "end": v(79.5, -46.24) * mm});
            skArc(sketch, "E3758", {"start": v(79.5, -46.24) * mm, "mid": v(79.32, -46.22) * mm, "end": v(79.15, -46.16) * mm});
            skArc(sketch, "E3759", {"start": v(79.15, -46.16) * mm, "mid": v(79.02, -46.07) * mm, "end": v(78.95, -45.93) * mm});
            skArc(sketch, "E3760", {"start": v(78.95, -45.93) * mm, "mid": v(78.88, -45.69) * mm, "end": v(78.85, -45.44) * mm});
            skArc(sketch, "E3761", {"start": v(78.85, -45.44) * mm, "mid": v(78.82, -44.77) * mm, "end": v(78.79, -44.1) * mm});
            skLineSegment(sketch, "E3762", {"start": v(78.79, -44.1) * mm, "end": v(78.7, -41.96) * mm});
            skLineSegment(sketch, "E3763", {"start": v(78.7, -41.96) * mm, "end": v(77.63, -41.87) * mm});
            skArc(sketch, "E3764", {"start": v(77.63, -41.87) * mm, "mid": v(77.23, -41.86) * mm, "end": v(76.82, -41.89) * mm});
            skArc(sketch, "E3765", {"start": v(76.82, -41.89) * mm, "mid": v(76.37, -41.96) * mm, "end": v(75.92, -42.07) * mm});
            skArc(sketch, "E3766", {"start": v(75.92, -42.07) * mm, "mid": v(75.53, -42.2) * mm, "end": v(75.15, -42.34) * mm});
            skArc(sketch, "E3767", {"start": v(75.15, -42.34) * mm, "mid": v(75.02, -42.45) * mm, "end": v(74.98, -42.61) * mm});
            skArc(sketch, "E3768", {"start": v(74.98, -42.61) * mm, "mid": v(74.99, -42.67) * mm, "end": v(75, -42.72) * mm});
            skArc(sketch, "E3769", {"start": v(75, -42.72) * mm, "mid": v(75.07, -42.83) * mm, "end": v(75.14, -42.94) * mm});
            skArc(sketch, "E3770", {"start": v(75.14, -42.94) * mm, "mid": v(75.23, -43.07) * mm, "end": v(75.32, -43.2) * mm});
            skArc(sketch, "E3771", {"start": v(75.32, -43.2) * mm, "mid": v(75.42, -43.34) * mm, "end": v(75.53, -43.48) * mm});
            skArc(sketch, "E3772", {"start": v(75.53, -43.48) * mm, "mid": v(75.8, -43.85) * mm, "end": v(76.03, -44.25) * mm});
            skArc(sketch, "E3773", {"start": v(76.03, -44.25) * mm, "mid": v(76.06, -44.45) * mm, "end": v(75.96, -44.62) * mm});
            skArc(sketch, "E3774", {"start": v(75.96, -44.62) * mm, "mid": v(75.73, -44.77) * mm, "end": v(75.47, -44.82) * mm});
            skArc(sketch, "E3775", {"start": v(75.47, -44.82) * mm, "mid": v(74.71, -44.85) * mm, "end": v(73.95, -44.86) * mm});
            skArc(sketch, "E3776", {"start": v(73.95, -44.86) * mm, "mid": v(73.49, -44.87) * mm, "end": v(73.02, -44.9) * mm});
            skArc(sketch, "E3777", {"start": v(73.02, -44.9) * mm, "mid": v(72.5, -44.94) * mm, "end": v(71.98, -45) * mm});
            skArc(sketch, "E3778", {"start": v(71.98, -45) * mm, "mid": v(71.48, -45.06) * mm, "end": v(70.99, -45.14) * mm});
            skArc(sketch, "E3779", {"start": v(70.99, -45.14) * mm, "mid": v(70.6, -45.22) * mm, "end": v(70.22, -45.31) * mm});
            skLineSegment(sketch, "E3780", {"start": v(70.22, -45.31) * mm, "end": v(68.61, -45.76) * mm});
            skLineSegment(sketch, "E3781", {"start": v(68.61, -45.76) * mm, "end": v(68.61, -47.23) * mm});
            skArc(sketch, "E3782", {"start": v(68.61, -47.23) * mm, "mid": v(68.6, -47.6) * mm, "end": v(68.6, -48) * mm});
            skArc(sketch, "E3783", {"start": v(68.6, -48) * mm, "mid": v(68.57, -48.2) * mm, "end": v(68.52, -48.42) * mm});
            skArc(sketch, "E3784", {"start": v(68.52, -48.42) * mm, "mid": v(68.46, -48.55) * mm, "end": v(68.37, -48.66) * mm});
            skArc(sketch, "E3785", {"start": v(68.37, -48.66) * mm, "mid": v(68.26, -48.74) * mm, "end": v(68.13, -48.79) * mm});
            skArc(sketch, "E3786", {"start": v(68.13, -48.79) * mm, "mid": v(68, -48.82) * mm, "end": v(67.9, -48.9) * mm});
            skArc(sketch, "E3787", {"start": v(67.9, -48.9) * mm, "mid": v(67.81, -48.98) * mm, "end": v(67.75, -49.1) * mm});
            skArc(sketch, "E3788", {"start": v(67.75, -49.1) * mm, "mid": v(67.7, -49.26) * mm, "end": v(67.67, -49.43) * mm});
            skArc(sketch, "E3789", {"start": v(67.67, -49.43) * mm, "mid": v(67.65, -49.7) * mm, "end": v(67.65, -49.96) * mm});
            skArc(sketch, "E3790", {"start": v(67.65, -49.96) * mm, "mid": v(67.64, -50.17) * mm, "end": v(67.62, -50.39) * mm});
            skArc(sketch, "E3791", {"start": v(67.62, -50.39) * mm, "mid": v(67.6, -50.57) * mm, "end": v(67.55, -50.76) * mm});
            skArc(sketch, "E3792", {"start": v(67.55, -50.76) * mm, "mid": v(67.5, -50.9) * mm, "end": v(67.44, -51.03) * mm});
            skArc(sketch, "E3793", {"start": v(67.44, -51.03) * mm, "mid": v(67.38, -51.1) * mm, "end": v(67.3, -51.15) * mm});
            skArc(sketch, "E3794", {"start": v(67.3, -51.15) * mm, "mid": v(67.22, -51.15) * mm, "end": v(67.15, -51.12) * mm});
            skArc(sketch, "E3795", {"start": v(67.15, -51.12) * mm, "mid": v(67.08, -51.04) * mm, "end": v(67.04, -50.94) * mm});
            skArc(sketch, "E3796", {"start": v(67.04, -50.94) * mm, "mid": v(67, -50.76) * mm, "end": v(66.97, -50.58) * mm});
            skArc(sketch, "E3797", {"start": v(66.97, -50.58) * mm, "mid": v(66.96, -50.3) * mm, "end": v(66.95, -50) * mm});
            skArc(sketch, "E3798", {"start": v(66.95, -50) * mm, "mid": v(66.95, -49.65) * mm, "end": v(66.94, -49.3) * mm});
            skArc(sketch, "E3799", {"start": v(66.94, -49.3) * mm, "mid": v(66.91, -49.13) * mm, "end": v(66.86, -48.96) * mm});
            skArc(sketch, "E3800", {"start": v(66.86, -48.96) * mm, "mid": v(66.79, -48.86) * mm, "end": v(66.69, -48.8) * mm});
            skArc(sketch, "E3801", {"start": v(66.69, -48.8) * mm, "mid": v(66.55, -48.75) * mm, "end": v(66.4, -48.73) * mm});
            skArc(sketch, "E3802", {"start": v(66.4, -48.73) * mm, "mid": v(66.27, -48.72) * mm, "end": v(66.14, -48.7) * mm});
            skArc(sketch, "E3803", {"start": v(66.14, -48.7) * mm, "mid": v(66.05, -48.65) * mm, "end": v(65.97, -48.58) * mm});
            skArc(sketch, "E3804", {"start": v(65.97, -48.58) * mm, "mid": v(65.91, -48.48) * mm, "end": v(65.88, -48.37) * mm});
            skArc(sketch, "E3805", {"start": v(65.88, -48.37) * mm, "mid": v(65.86, -48.22) * mm, "end": v(65.85, -48.06) * mm});
            skArc(sketch, "E3806", {"start": v(65.85, -48.06) * mm, "mid": v(65.84, -47.92) * mm, "end": v(65.83, -47.79) * mm});
            skArc(sketch, "E3807", {"start": v(65.83, -47.79) * mm, "mid": v(65.8, -47.66) * mm, "end": v(65.77, -47.53) * mm});
            skArc(sketch, "E3808", {"start": v(65.77, -47.53) * mm, "mid": v(65.74, -47.43) * mm, "end": v(65.7, -47.33) * mm});
            skArc(sketch, "E3809", {"start": v(65.7, -47.33) * mm, "mid": v(65.65, -47.27) * mm, "end": v(65.6, -47.23) * mm});
            skArc(sketch, "E3810", {"start": v(65.6, -47.23) * mm, "mid": v(65.33, -47.18) * mm, "end": v(65.1, -47.32) * mm});
            skArc(sketch, "E3811", {"start": v(65.1, -47.32) * mm, "mid": v(64.46, -48.2) * mm, "end": v(63.84, -49.1) * mm});
            skArc(sketch, "E3812", {"start": v(63.84, -49.1) * mm, "mid": v(63.22, -50.07) * mm, "end": v(62.65, -51.08) * mm});
            skArc(sketch, "E3813", {"start": v(62.65, -51.08) * mm, "mid": v(62.23, -51.93) * mm, "end": v(61.88, -52.8) * mm});
            skArc(sketch, "E3814", {"start": v(61.88, -52.8) * mm, "mid": v(61.62, -53.57) * mm, "end": v(61.4, -54.34) * mm});
            skArc(sketch, "E3815", {"start": v(61.4, -54.34) * mm, "mid": v(61.34, -54.72) * mm, "end": v(61.38, -55.1) * mm});
            skArc(sketch, "E3816", {"start": v(61.38, -55.1) * mm, "mid": v(61.5, -55.23) * mm, "end": v(61.68, -55.2) * mm});
            skArc(sketch, "E3817", {"start": v(61.68, -55.2) * mm, "mid": v(62, -54.9) * mm, "end": v(62.3, -54.55) * mm});
            skArc(sketch, "E3818", {"start": v(62.3, -54.55) * mm, "mid": v(62.55, -54.23) * mm, "end": v(62.83, -53.94) * mm});
            skArc(sketch, "E3819", {"start": v(62.83, -53.94) * mm, "mid": v(63.22, -53.6) * mm, "end": v(63.61, -53.28) * mm});
            skArc(sketch, "E3820", {"start": v(63.61, -53.28) * mm, "mid": v(64, -53) * mm, "end": v(64.4, -52.73) * mm});
            skArc(sketch, "E3821", {"start": v(64.4, -52.73) * mm, "mid": v(64.6, -52.64) * mm, "end": v(64.84, -52.6) * mm});
            skArc(sketch, "E3822", {"start": v(64.84, -52.6) * mm, "mid": v(64.88, -52.62) * mm, "end": v(64.9, -52.66) * mm});
            skArc(sketch, "E3823", {"start": v(64.9, -52.66) * mm, "mid": v(64.9, -52.8) * mm, "end": v(64.9, -52.96) * mm});
            skArc(sketch, "E3824", {"start": v(64.9, -52.96) * mm, "mid": v(64.9, -53.15) * mm, "end": v(64.9, -53.35) * mm});
            skArc(sketch, "E3825", {"start": v(64.9, -53.35) * mm, "mid": v(64.87, -53.58) * mm, "end": v(64.84, -53.81) * mm});
            skArc(sketch, "E3826", {"start": v(64.84, -53.81) * mm, "mid": v(64.82, -54.05) * mm, "end": v(64.8, -54.29) * mm});
            skArc(sketch, "E3827", {"start": v(64.8, -54.29) * mm, "mid": v(64.8, -54.5) * mm, "end": v(64.8, -54.71) * mm});
            skArc(sketch, "E3828", {"start": v(64.8, -54.71) * mm, "mid": v(64.82, -54.88) * mm, "end": v(64.85, -55.05) * mm});
            skArc(sketch, "E3829", {"start": v(64.85, -55.05) * mm, "mid": v(64.88, -55.13) * mm, "end": v(64.94, -55.18) * mm});
            skArc(sketch, "E3830", {"start": v(64.94, -55.18) * mm, "mid": v(65.03, -55.2) * mm, "end": v(65.12, -55.18) * mm});
            skArc(sketch, "E3831", {"start": v(65.12, -55.18) * mm, "mid": v(65.33, -55.05) * mm, "end": v(65.55, -54.9) * mm});
            skArc(sketch, "E3832", {"start": v(65.55, -54.9) * mm, "mid": v(65.8, -54.7) * mm, "end": v(66.06, -54.5) * mm});
            skArc(sketch, "E3833", {"start": v(66.06, -54.5) * mm, "mid": v(66.34, -54.25) * mm, "end": v(66.62, -53.99) * mm});
            skArc(sketch, "E3834", {"start": v(66.62, -53.99) * mm, "mid": v(66.93, -53.7) * mm, "end": v(67.24, -53.43) * mm});
            skArc(sketch, "E3835", {"start": v(67.24, -53.43) * mm, "mid": v(67.58, -53.14) * mm, "end": v(67.93, -52.87) * mm});
            skArc(sketch, "E3836", {"start": v(67.93, -52.87) * mm, "mid": v(68.26, -52.62) * mm, "end": v(68.6, -52.39) * mm});
            skArc(sketch, "E3837", {"start": v(68.6, -52.39) * mm, "mid": v(68.84, -52.23) * mm, "end": v(69.1, -52.09) * mm});
            skArc(sketch, "E3838", {"start": v(69.1, -52.09) * mm, "mid": v(69.59, -51.86) * mm, "end": v(70.1, -51.68) * mm});
            skArc(sketch, "E3839", {"start": v(70.1, -51.68) * mm, "mid": v(70.73, -51.5) * mm, "end": v(71.37, -51.35) * mm});
            skArc(sketch, "E3840", {"start": v(71.37, -51.35) * mm, "mid": v(72, -51.23) * mm, "end": v(72.62, -51.15) * mm});
            skArc(sketch, "E3841", {"start": v(72.62, -51.15) * mm, "mid": v(73.07, -51.13) * mm, "end": v(73.5, -51.16) * mm});
            skArc(sketch, "E3842", {"start": v(73.5, -51.16) * mm, "mid": v(73.7, -51.2) * mm, "end": v(73.88, -51.24) * mm});
            skArc(sketch, "E3843", {"start": v(73.88, -51.24) * mm, "mid": v(73.94, -51.28) * mm, "end": v(73.97, -51.35) * mm});
            skArc(sketch, "E3844", {"start": v(73.97, -51.35) * mm, "mid": v(73.97, -51.45) * mm, "end": v(73.93, -51.54) * mm});
            skArc(sketch, "E3845", {"start": v(73.93, -51.54) * mm, "mid": v(73.76, -51.83) * mm, "end": v(73.6, -52.12) * mm});
            skArc(sketch, "E3846", {"start": v(73.6, -52.12) * mm, "mid": v(73.38, -52.48) * mm, "end": v(73.2, -52.86) * mm});
            skArc(sketch, "E3847", {"start": v(73.2, -52.86) * mm, "mid": v(73.17, -53.03) * mm, "end": v(73.25, -53.18) * mm});
            skArc(sketch, "E3848", {"start": v(73.25, -53.18) * mm, "mid": v(73.4, -53.27) * mm, "end": v(73.58, -53.25) * mm});
            skArc(sketch, "E3849", {"start": v(73.58, -53.25) * mm, "mid": v(73.99, -53.09) * mm, "end": v(74.38, -52.9) * mm});
            skArc(sketch, "E3850", {"start": v(74.38, -52.9) * mm, "mid": v(75.29, -52.5) * mm, "end": v(76.23, -52.17) * mm});
            skArc(sketch, "E3851", {"start": v(76.23, -52.17) * mm, "mid": v(77.4, -51.87) * mm, "end": v(78.6, -51.63) * mm});
            skArc(sketch, "E3852", {"start": v(78.6, -51.63) * mm, "mid": v(79.5, -51.5) * mm, "end": v(80.4, -51.45) * mm});
            skArc(sketch, "E3853", {"start": v(80.4, -51.45) * mm, "mid": v(80.6, -51.59) * mm, "end": v(80.56, -51.83) * mm});
            skArc(sketch, "E3854", {"start": v(80.56, -51.83) * mm, "mid": v(80.39, -52.04) * mm, "end": v(80.26, -52.28) * mm});
            skArc(sketch, "E3855", {"start": v(80.26, -52.28) * mm, "mid": v(80.25, -52.44) * mm, "end": v(80.35, -52.57) * mm});
            skArc(sketch, "E3856", {"start": v(80.35, -52.57) * mm, "mid": v(80.61, -52.69) * mm, "end": v(80.89, -52.74) * mm});
            skArc(sketch, "E3857", {"start": v(80.89, -52.74) * mm, "mid": v(81.5, -52.76) * mm, "end": v(82.1, -52.76) * mm});
            skArc(sketch, "E3858", {"start": v(82.1, -52.76) * mm, "mid": v(82.57, -52.76) * mm, "end": v(83.04, -52.78) * mm});
            skArc(sketch, "E3859", {"start": v(83.04, -52.78) * mm, "mid": v(83.39, -52.8) * mm, "end": v(83.74, -52.86) * mm});
            skArc(sketch, "E3860", {"start": v(83.74, -52.86) * mm, "mid": v(84.02, -52.93) * mm, "end": v(84.29, -53.01) * mm});
            skArc(sketch, "E3861", {"start": v(84.29, -53.01) * mm, "mid": v(84.53, -53.12) * mm, "end": v(84.76, -53.25) * mm});
            skLineSegment(sketch, "E3862", {"start": v(84.76, -53.25) * mm, "end": v(85.55, -53.77) * mm});
            skLineSegment(sketch, "E3863", {"start": v(85.55, -53.77) * mm, "end": v(84.4, -54.28) * mm});
            skArc(sketch, "E3864", {"start": v(84.4, -54.28) * mm, "mid": v(83.85, -54.61) * mm, "end": v(83.4, -55.07) * mm});
            skArc(sketch, "E3865", {"start": v(83.4, -55.07) * mm, "mid": v(83.23, -55.51) * mm, "end": v(83.34, -55.97) * mm});
            skArc(sketch, "E3866", {"start": v(83.34, -55.97) * mm, "mid": v(83.72, -56.38) * mm, "end": v(84.24, -56.6) * mm});
            skArc(sketch, "E3867", {"start": v(84.24, -56.6) * mm, "mid": v(85.01, -56.67) * mm, "end": v(85.79, -56.6) * mm});
            skArc(sketch, "E3868", {"start": v(85.79, -56.6) * mm, "mid": v(86, -56.57) * mm, "end": v(86.22, -56.51) * mm});
            skArc(sketch, "E3869", {"start": v(86.22, -56.51) * mm, "mid": v(86.44, -56.45) * mm, "end": v(86.66, -56.37) * mm});
            skArc(sketch, "E3870", {"start": v(86.66, -56.37) * mm, "mid": v(86.86, -56.3) * mm, "end": v(87.05, -56.2) * mm});
            skArc(sketch, "E3871", {"start": v(87.05, -56.2) * mm, "mid": v(87.2, -56.14) * mm, "end": v(87.32, -56.05) * mm});
            skArc(sketch, "E3872", {"start": v(87.32, -56.05) * mm, "mid": v(87.42, -55.97) * mm, "end": v(87.53, -55.9) * mm});
            skArc(sketch, "E3873", {"start": v(87.53, -55.9) * mm, "mid": v(87.64, -55.83) * mm, "end": v(87.74, -55.77) * mm});
            skArc(sketch, "E3874", {"start": v(87.74, -55.77) * mm, "mid": v(87.83, -55.73) * mm, "end": v(87.93, -55.68) * mm});
            skArc(sketch, "E3875", {"start": v(87.93, -55.68) * mm, "mid": v(87.98, -55.66) * mm, "end": v(88.04, -55.65) * mm});
            skArc(sketch, "E3876", {"start": v(88.04, -55.65) * mm, "mid": v(88.16, -55.7) * mm, "end": v(88.23, -55.8) * mm});
            skArc(sketch, "E3877", {"start": v(88.23, -55.8) * mm, "mid": v(88.24, -55.99) * mm, "end": v(88.21, -56.17) * mm});
            skArc(sketch, "E3878", {"start": v(88.21, -56.17) * mm, "mid": v(88.1, -56.44) * mm, "end": v(87.96, -56.7) * mm});
            skArc(sketch, "E3879", {"start": v(87.96, -56.7) * mm, "mid": v(87.77, -56.95) * mm, "end": v(87.55, -57.2) * mm});
            skArc(sketch, "E3880", {"start": v(87.55, -57.2) * mm, "mid": v(87.35, -57.4) * mm, "end": v(87.15, -57.63) * mm});
            skArc(sketch, "E3881", {"start": v(87.15, -57.63) * mm, "mid": v(87.07, -57.76) * mm, "end": v(87.02, -57.9) * mm});
            skArc(sketch, "E3882", {"start": v(87.02, -57.9) * mm, "mid": v(87.02, -58.05) * mm, "end": v(87.05, -58.19) * mm});
            skArc(sketch, "E3883", {"start": v(87.05, -58.19) * mm, "mid": v(87.16, -58.44) * mm, "end": v(87.28, -58.69) * mm});
            skArc(sketch, "E3884", {"start": v(87.28, -58.69) * mm, "mid": v(87.36, -58.85) * mm, "end": v(87.44, -59.03) * mm});
            skArc(sketch, "E3885", {"start": v(87.44, -59.03) * mm, "mid": v(87.5, -59.2) * mm, "end": v(87.57, -59.38) * mm});
            skArc(sketch, "E3886", {"start": v(87.57, -59.38) * mm, "mid": v(87.62, -59.54) * mm, "end": v(87.66, -59.7) * mm});
            skArc(sketch, "E3887", {"start": v(87.66, -59.7) * mm, "mid": v(87.69, -59.82) * mm, "end": v(87.7, -59.93) * mm});
            skArc(sketch, "E3888", {"start": v(87.7, -59.93) * mm, "mid": v(87.68, -60.02) * mm, "end": v(87.64, -60.1) * mm});
            skArc(sketch, "E3889", {"start": v(87.64, -60.1) * mm, "mid": v(87.59, -60.15) * mm, "end": v(87.52, -60.16) * mm});
            skArc(sketch, "E3890", {"start": v(87.52, -60.16) * mm, "mid": v(87.4, -60.11) * mm, "end": v(87.28, -60.05) * mm});
            skArc(sketch, "E3891", {"start": v(87.28, -60.05) * mm, "mid": v(87.03, -59.88) * mm, "end": v(86.8, -59.7) * mm});
            skArc(sketch, "E3892", {"start": v(86.8, -59.7) * mm, "mid": v(86.39, -59.43) * mm, "end": v(85.96, -59.18) * mm});
            skArc(sketch, "E3893", {"start": v(85.96, -59.18) * mm, "mid": v(85.5, -58.96) * mm, "end": v(85.03, -58.77) * mm});
            skArc(sketch, "E3894", {"start": v(85.03, -58.77) * mm, "mid": v(84.57, -58.62) * mm, "end": v(84.1, -58.5) * mm});
            skArc(sketch, "E3895", {"start": v(84.1, -58.5) * mm, "mid": v(83.67, -58.43) * mm, "end": v(83.24, -58.4) * mm});
            skArc(sketch, "E3896", {"start": v(83.24, -58.4) * mm, "mid": v(82.89, -58.43) * mm, "end": v(82.54, -58.48) * mm});
            skArc(sketch, "E3897", {"start": v(82.54, -58.48) * mm, "mid": v(82.4, -58.57) * mm, "end": v(82.36, -58.72) * mm});
            skArc(sketch, "E3898", {"start": v(82.36, -58.72) * mm, "mid": v(82.42, -58.93) * mm, "end": v(82.56, -59.08) * mm});
            skArc(sketch, "E3899", {"start": v(82.56, -59.08) * mm, "mid": v(82.94, -59.35) * mm, "end": v(83.34, -59.6) * mm});
            skArc(sketch, "E3900", {"start": v(83.34, -59.6) * mm, "mid": v(83.58, -59.75) * mm, "end": v(83.83, -59.9) * mm});
            skArc(sketch, "E3901", {"start": v(83.83, -59.9) * mm, "mid": v(84.08, -60.08) * mm, "end": v(84.32, -60.26) * mm});
            skArc(sketch, "E3902", {"start": v(84.32, -60.26) * mm, "mid": v(84.54, -60.43) * mm, "end": v(84.76, -60.6) * mm});
            skArc(sketch, "E3903", {"start": v(84.76, -60.6) * mm, "mid": v(84.9, -60.73) * mm, "end": v(85.04, -60.87) * mm});
            skArc(sketch, "E3904", {"start": v(85.04, -60.87) * mm, "mid": v(85.2, -61.04) * mm, "end": v(85.34, -61.21) * mm});
            skArc(sketch, "E3905", {"start": v(85.34, -61.21) * mm, "mid": v(85.38, -61.28) * mm, "end": v(85.4, -61.35) * mm});
            skArc(sketch, "E3906", {"start": v(85.4, -61.35) * mm, "mid": v(85.39, -61.4) * mm, "end": v(85.34, -61.43) * mm});
            skArc(sketch, "E3907", {"start": v(85.34, -61.43) * mm, "mid": v(85.23, -61.45) * mm, "end": v(85.1, -61.45) * mm});
            skArc(sketch, "E3908", {"start": v(85.1, -61.45) * mm, "mid": v(84.95, -61.47) * mm, "end": v(84.8, -61.52) * mm});
            skArc(sketch, "E3909", {"start": v(84.8, -61.52) * mm, "mid": v(84.7, -61.59) * mm, "end": v(84.67, -61.7) * mm});
            skArc(sketch, "E3910", {"start": v(84.67, -61.7) * mm, "mid": v(84.69, -61.84) * mm, "end": v(84.75, -61.96) * mm});
            skArc(sketch, "E3911", {"start": v(84.75, -61.96) * mm, "mid": v(84.9, -62.13) * mm, "end": v(85.07, -62.28) * mm});
            skArc(sketch, "E3912", {"start": v(85.07, -62.28) * mm, "mid": v(85.15, -62.36) * mm, "end": v(85.22, -62.45) * mm});
            skArc(sketch, "E3913", {"start": v(85.22, -62.45) * mm, "mid": v(85.3, -62.56) * mm, "end": v(85.36, -62.67) * mm});
            skArc(sketch, "E3914", {"start": v(85.36, -62.67) * mm, "mid": v(85.4, -62.79) * mm, "end": v(85.45, -62.9) * mm});
            skArc(sketch, "E3915", {"start": v(85.45, -62.9) * mm, "mid": v(85.47, -63.01) * mm, "end": v(85.48, -63.12) * mm});
            skArc(sketch, "E3916", {"start": v(85.48, -63.12) * mm, "mid": v(85.47, -63.25) * mm, "end": v(85.44, -63.38) * mm});
            skArc(sketch, "E3917", {"start": v(85.44, -63.38) * mm, "mid": v(85.4, -63.45) * mm, "end": v(85.32, -63.48) * mm});
            skArc(sketch, "E3918", {"start": v(85.32, -63.48) * mm, "mid": v(85.2, -63.49) * mm, "end": v(85.07, -63.46) * mm});
            skArc(sketch, "E3919", {"start": v(85.07, -63.46) * mm, "mid": v(84.75, -63.36) * mm, "end": v(84.44, -63.26) * mm});
            skArc(sketch, "E3920", {"start": v(84.44, -63.26) * mm, "mid": v(84.2, -63.17) * mm, "end": v(83.95, -63.09) * mm});
            skArc(sketch, "E3921", {"start": v(83.95, -63.09) * mm, "mid": v(83.63, -62.99) * mm, "end": v(83.3, -62.88) * mm});
            skArc(sketch, "E3922", {"start": v(83.3, -62.88) * mm, "mid": v(82.97, -62.78) * mm, "end": v(82.63, -62.68) * mm});
            skArc(sketch, "E3923", {"start": v(82.63, -62.68) * mm, "mid": v(82.33, -62.6) * mm, "end": v(82.02, -62.5) * mm});
            skArc(sketch, "E3924", {"start": v(82.02, -62.5) * mm, "mid": v(81.65, -62.39) * mm, "end": v(81.27, -62.26) * mm});
            skArc(sketch, "E3925", {"start": v(81.27, -62.26) * mm, "mid": v(81.03, -62.14) * mm, "end": v(80.8, -62) * mm});
            skArc(sketch, "E3926", {"start": v(80.8, -62) * mm, "mid": v(80.6, -61.82) * mm, "end": v(80.44, -61.63) * mm});
            skArc(sketch, "E3927", {"start": v(80.44, -61.63) * mm, "mid": v(80.25, -61.35) * mm, "end": v(80.09, -61.06) * mm});
            skArc(sketch, "E3928", {"start": v(80.09, -61.06) * mm, "mid": v(79.98, -60.86) * mm, "end": v(79.86, -60.66) * mm});
            skArc(sketch, "E3929", {"start": v(79.86, -60.66) * mm, "mid": v(79.75, -60.49) * mm, "end": v(79.64, -60.32) * mm});
            skArc(sketch, "E3930", {"start": v(79.64, -60.32) * mm, "mid": v(79.54, -60.2) * mm, "end": v(79.44, -60.07) * mm});
            skArc(sketch, "E3931", {"start": v(79.44, -60.07) * mm, "mid": v(79.39, -60.04) * mm, "end": v(79.33, -60.04) * mm});
            skArc(sketch, "E3932", {"start": v(79.33, -60.04) * mm, "mid": v(79.28, -60.04) * mm, "end": v(79.23, -60.05) * mm});
            skArc(sketch, "E3933", {"start": v(79.23, -60.05) * mm, "mid": v(79.17, -60.05) * mm, "end": v(79.11, -60.06) * mm});
            skArc(sketch, "E3934", {"start": v(79.11, -60.06) * mm, "mid": v(79.05, -60.06) * mm, "end": v(78.99, -60.07) * mm});
            skArc(sketch, "E3935", {"start": v(78.99, -60.07) * mm, "mid": v(78.93, -60.07) * mm, "end": v(78.88, -60.07) * mm});
            skArc(sketch, "E3936", {"start": v(78.88, -60.07) * mm, "mid": v(78.82, -60.09) * mm, "end": v(78.78, -60.14) * mm});
            skArc(sketch, "E3937", {"start": v(78.78, -60.14) * mm, "mid": v(78.72, -60.3) * mm, "end": v(78.67, -60.48) * mm});
            skArc(sketch, "E3938", {"start": v(78.67, -60.48) * mm, "mid": v(78.61, -60.7) * mm, "end": v(78.57, -60.93) * mm});
            skArc(sketch, "E3939", {"start": v(78.57, -60.93) * mm, "mid": v(78.53, -61.2) * mm, "end": v(78.5, -61.47) * mm});
            skArc(sketch, "E3940", {"start": v(78.5, -61.47) * mm, "mid": v(78.47, -61.76) * mm, "end": v(78.42, -62.04) * mm});
            skArc(sketch, "E3941", {"start": v(78.42, -62.04) * mm, "mid": v(78.36, -62.32) * mm, "end": v(78.28, -62.59) * mm});
            skArc(sketch, "E3942", {"start": v(78.28, -62.59) * mm, "mid": v(78.2, -62.82) * mm, "end": v(78.12, -63.04) * mm});
            skArc(sketch, "E3943", {"start": v(78.12, -63.04) * mm, "mid": v(78.04, -63.18) * mm, "end": v(77.95, -63.3) * mm});
            skArc(sketch, "E3944", {"start": v(77.95, -63.3) * mm, "mid": v(77.74, -63.45) * mm, "end": v(77.5, -63.55) * mm});
            skArc(sketch, "E3945", {"start": v(77.5, -63.55) * mm, "mid": v(77.22, -63.57) * mm, "end": v(76.95, -63.53) * mm});
            skArc(sketch, "E3946", {"start": v(76.95, -63.53) * mm, "mid": v(76.72, -63.43) * mm, "end": v(76.52, -63.27) * mm});
            skArc(sketch, "E3947", {"start": v(76.52, -63.27) * mm, "mid": v(76.4, -63.07) * mm, "end": v(76.36, -62.85) * mm});
            skArc(sketch, "E3948", {"start": v(76.36, -62.85) * mm, "mid": v(76.34, -62.74) * mm, "end": v(76.31, -62.63) * mm});
            skArc(sketch, "E3949", {"start": v(76.31, -62.63) * mm, "mid": v(76.25, -62.5) * mm, "end": v(76.17, -62.37) * mm});
            skArc(sketch, "E3950", {"start": v(76.17, -62.37) * mm, "mid": v(76.08, -62.24) * mm, "end": v(75.97, -62.12) * mm});
            skArc(sketch, "E3951", {"start": v(75.97, -62.12) * mm, "mid": v(75.86, -62.02) * mm, "end": v(75.73, -61.92) * mm});
            skArc(sketch, "E3952", {"start": v(75.73, -61.92) * mm, "mid": v(75.54, -61.79) * mm, "end": v(75.35, -61.65) * mm});
            skArc(sketch, "E3953", {"start": v(75.35, -61.65) * mm, "mid": v(75.3, -61.58) * mm, "end": v(75.27, -61.5) * mm});
            skArc(sketch, "E3954", {"start": v(75.27, -61.5) * mm, "mid": v(75.28, -61.43) * mm, "end": v(75.32, -61.36) * mm});
            skArc(sketch, "E3955", {"start": v(75.32, -61.36) * mm, "mid": v(75.47, -61.23) * mm, "end": v(75.63, -61.1) * mm});
            skArc(sketch, "E3956", {"start": v(75.63, -61.1) * mm, "mid": v(75.77, -60.99) * mm, "end": v(75.9, -60.85) * mm});
            skArc(sketch, "E3957", {"start": v(75.9, -60.85) * mm, "mid": v(75.97, -60.74) * mm, "end": v(76, -60.61) * mm});
            skArc(sketch, "E3958", {"start": v(76, -60.61) * mm, "mid": v(76, -60.45) * mm, "end": v(75.98, -60.3) * mm});
            skArc(sketch, "E3959", {"start": v(75.98, -60.3) * mm, "mid": v(75.88, -60) * mm, "end": v(75.78, -59.69) * mm});
            skArc(sketch, "E3960", {"start": v(75.78, -59.69) * mm, "mid": v(75.68, -59.38) * mm, "end": v(75.6, -59.07) * mm});
            skArc(sketch, "E3961", {"start": v(75.6, -59.07) * mm, "mid": v(75.56, -58.84) * mm, "end": v(75.55, -58.6) * mm});
            skArc(sketch, "E3962", {"start": v(75.55, -58.6) * mm, "mid": v(75.58, -58.36) * mm, "end": v(75.64, -58.1) * mm});
            skArc(sketch, "E3963", {"start": v(75.64, -58.1) * mm, "mid": v(75.75, -57.73) * mm, "end": v(75.89, -57.36) * mm});
            skArc(sketch, "E3964", {"start": v(75.89, -57.36) * mm, "mid": v(76.11, -56.73) * mm, "end": v(76.34, -56.1) * mm});
            skArc(sketch, "E3965", {"start": v(76.34, -56.1) * mm, "mid": v(76.37, -55.92) * mm, "end": v(76.36, -55.73) * mm});
            skArc(sketch, "E3966", {"start": v(76.36, -55.73) * mm, "mid": v(76.3, -55.6) * mm, "end": v(76.17, -55.53) * mm});
            skArc(sketch, "E3967", {"start": v(76.17, -55.53) * mm, "mid": v(75.85, -55.47) * mm, "end": v(75.53, -55.43) * mm});
            skArc(sketch, "E3968", {"start": v(75.53, -55.43) * mm, "mid": v(75.07, -55.42) * mm, "end": v(74.62, -55.44) * mm});
            skArc(sketch, "E3969", {"start": v(74.62, -55.44) * mm, "mid": v(74.36, -55.5) * mm, "end": v(74.14, -55.64) * mm});
            skArc(sketch, "E3970", {"start": v(74.14, -55.64) * mm, "mid": v(74, -55.83) * mm, "end": v(73.96, -56.05) * mm});
            skArc(sketch, "E3971", {"start": v(73.96, -56.05) * mm, "mid": v(74, -56.39) * mm, "end": v(74.09, -56.71) * mm});
            skLineSegment(sketch, "E3972", {"start": v(74.09, -56.71) * mm, "end": v(74.39, -57.57) * mm});
            skLineSegment(sketch, "E3973", {"start": v(74.39, -57.57) * mm, "end": v(73.23, -57.42) * mm});
            skArc(sketch, "E3974", {"start": v(73.23, -57.42) * mm, "mid": v(72.73, -57.38) * mm, "end": v(72.22, -57.36) * mm});
            skArc(sketch, "E3975", {"start": v(72.22, -57.36) * mm, "mid": v(71.94, -57.4) * mm, "end": v(71.68, -57.54) * mm});
            skArc(sketch, "E3976", {"start": v(71.68, -57.54) * mm, "mid": v(71.55, -57.7) * mm, "end": v(71.53, -57.9) * mm});
            skArc(sketch, "E3977", {"start": v(71.53, -57.9) * mm, "mid": v(71.61, -58.18) * mm, "end": v(71.76, -58.44) * mm});
            skArc(sketch, "E3978", {"start": v(71.76, -58.44) * mm, "mid": v(71.85, -58.58) * mm, "end": v(71.93, -58.73) * mm});
            skArc(sketch, "E3979", {"start": v(71.93, -58.73) * mm, "mid": v(72, -58.9) * mm, "end": v(72.08, -59.08) * mm});
            skArc(sketch, "E3980", {"start": v(72.08, -59.08) * mm, "mid": v(72.13, -59.25) * mm, "end": v(72.18, -59.43) * mm});
            skArc(sketch, "E3981", {"start": v(72.18, -59.43) * mm, "mid": v(72.2, -59.57) * mm, "end": v(72.2, -59.72) * mm});
            skArc(sketch, "E3982", {"start": v(72.2, -59.72) * mm, "mid": v(72.2, -59.9) * mm, "end": v(72.15, -60.06) * mm});
            skArc(sketch, "E3983", {"start": v(72.15, -60.06) * mm, "mid": v(72.08, -60.17) * mm, "end": v(71.98, -60.25) * mm});
            skArc(sketch, "E3984", {"start": v(71.98, -60.25) * mm, "mid": v(71.8, -60.3) * mm, "end": v(71.62, -60.33) * mm});
            skArc(sketch, "E3985", {"start": v(71.62, -60.33) * mm, "mid": v(71.19, -60.34) * mm, "end": v(70.76, -60.35) * mm});
            skArc(sketch, "E3986", {"start": v(70.76, -60.35) * mm, "mid": v(69.75, -60.4) * mm, "end": v(68.75, -60.53) * mm});
            skArc(sketch, "E3987", {"start": v(68.75, -60.53) * mm, "mid": v(67.75, -60.75) * mm, "end": v(66.76, -61.06) * mm});
            skArc(sketch, "E3988", {"start": v(66.76, -61.06) * mm, "mid": v(65.77, -61.46) * mm, "end": v(64.8, -61.93) * mm});
            skArc(sketch, "E3989", {"start": v(64.8, -61.93) * mm, "mid": v(63.84, -62.5) * mm, "end": v(62.92, -63.13) * mm});
            skArc(sketch, "E3990", {"start": v(62.92, -63.13) * mm, "mid": v(62.23, -63.67) * mm, "end": v(61.58, -64.26) * mm});
            skArc(sketch, "E3991", {"start": v(61.58, -64.26) * mm, "mid": v(60.74, -65.1) * mm, "end": v(59.92, -65.95) * mm});
            skArc(sketch, "E3992", {"start": v(59.92, -65.95) * mm, "mid": v(59.12, -66.82) * mm, "end": v(58.33, -67.7) * mm});
            skArc(sketch, "E3993", {"start": v(58.33, -67.7) * mm, "mid": v(58.16, -67.98) * mm, "end": v(58.1, -68.3) * mm});
            skArc(sketch, "E3994", {"start": v(58.1, -68.3) * mm, "mid": v(58.13, -68.38) * mm, "end": v(58.2, -68.45) * mm});
            skArc(sketch, "E3995", {"start": v(58.2, -68.45) * mm, "mid": v(58.32, -68.51) * mm, "end": v(58.46, -68.55) * mm});
            skArc(sketch, "E3996", {"start": v(58.46, -68.55) * mm, "mid": v(58.68, -68.6) * mm, "end": v(58.9, -68.62) * mm});
            skArc(sketch, "E3997", {"start": v(58.9, -68.62) * mm, "mid": v(59.22, -68.64) * mm, "end": v(59.54, -68.64) * mm});
            skLineSegment(sketch, "E3998", {"start": v(59.54, -68.64) * mm, "end": v(60.97, -68.64) * mm});
            skLineSegment(sketch, "E3999", {"start": v(60.97, -68.64) * mm, "end": v(60.3, -69.4) * mm});
            skArc(sketch, "E4000", {"start": v(60.3, -69.4) * mm, "mid": v(59.7, -70.07) * mm, "end": v(59.12, -70.74) * mm});
            skArc(sketch, "E4001", {"start": v(59.12, -70.74) * mm, "mid": v(58.99, -70.96) * mm, "end": v(58.92, -71.21) * mm});
            skArc(sketch, "E4002", {"start": v(58.92, -71.21) * mm, "mid": v(58.94, -71.45) * mm, "end": v(59.05, -71.67) * mm});
            skArc(sketch, "E4003", {"start": v(59.05, -71.67) * mm, "mid": v(59.48, -72.2) * mm, "end": v(59.93, -72.73) * mm});
            skLineSegment(sketch, "E4004", {"start": v(59.93, -72.73) * mm, "end": v(61.2, -74.17) * mm});
            skLineSegment(sketch, "E4005", {"start": v(61.2, -74.17) * mm, "end": v(59.23, -74.17) * mm});
            skLineSegment(sketch, "E4006", {"start": v(59.23, -74.17) * mm, "end": v(57.28, -74.17) * mm});
            skLineSegment(sketch, "E4007", {"start": v(57.28, -74.17) * mm, "end": v(57.28, -36.15) * mm});
            skLineSegment(sketch, "E4008", {"start": v(57.28, -36.15) * mm, "end": v(57.28, 1.87) * mm});
            skLineSegment(sketch, "E4009", {"start": v(57.28, 1.87) * mm, "end": v(55.62, 1.87) * mm});
            skLineSegment(sketch, "E4010", {"start": v(55.62, 1.87) * mm, "end": v(53.96, 1.87) * mm});
            skLineSegment(sketch, "E4011", {"start": v(53.96, 1.87) * mm, "end": v(53.96, -36.15) * mm});
            skLineSegment(sketch, "E4012", {"start": v(53.96, -36.15) * mm, "end": v(53.96, -74.17) * mm});
            skLineSegment(sketch, "E4013", {"start": v(53.96, -74.17) * mm, "end": v(51.99, -74.17) * mm});
            skLineSegment(sketch, "E4014", {"start": v(51.99, -74.17) * mm, "end": v(50.02, -74.17) * mm});
            skLineSegment(sketch, "E4015", {"start": v(50.02, -74.17) * mm, "end": v(51.27, -72.71) * mm});
            skLineSegment(sketch, "E4016", {"start": v(51.27, -72.71) * mm, "end": v(52.51, -71.25) * mm});
            skLineSegment(sketch, "E4017", {"start": v(52.51, -71.25) * mm, "end": v(51.4, -69.95) * mm});
            skLineSegment(sketch, "E4018", {"start": v(51.4, -69.95) * mm, "end": v(50.3, -68.64) * mm});
            skLineSegment(sketch, "E4019", {"start": v(50.3, -68.64) * mm, "end": v(51.72, -68.64) * mm});
            skArc(sketch, "E4020", {"start": v(51.72, -68.64) * mm, "mid": v(52.01, -68.64) * mm, "end": v(52.3, -68.62) * mm});
            skArc(sketch, "E4021", {"start": v(52.3, -68.62) * mm, "mid": v(52.53, -68.6) * mm, "end": v(52.75, -68.56) * mm});
            skArc(sketch, "E4022", {"start": v(52.75, -68.56) * mm, "mid": v(52.9, -68.51) * mm, "end": v(53.04, -68.46) * mm});
            skArc(sketch, "E4023", {"start": v(53.04, -68.46) * mm, "mid": v(53.1, -68.4) * mm, "end": v(53.13, -68.32) * mm});
            skArc(sketch, "E4024", {"start": v(53.13, -68.32) * mm, "mid": v(53.07, -68.01) * mm, "end": v(52.91, -67.74) * mm});
            skArc(sketch, "E4025", {"start": v(52.91, -67.74) * mm, "mid": v(52.29, -67.01) * mm, "end": v(51.65, -66.3) * mm});
            skArc(sketch, "E4026", {"start": v(51.65, -66.3) * mm, "mid": v(50.92, -65.54) * mm, "end": v(50.18, -64.8) * mm});
            skArc(sketch, "E4027", {"start": v(50.18, -64.8) * mm, "mid": v(49.47, -64.17) * mm, "end": v(48.74, -63.56) * mm});
            skArc(sketch, "E4028", {"start": v(48.74, -63.56) * mm, "mid": v(47.74, -62.81) * mm, "end": v(46.7, -62.13) * mm});
            skArc(sketch, "E4029", {"start": v(46.7, -62.13) * mm, "mid": v(45.7, -61.59) * mm, "end": v(44.67, -61.14) * mm});
            skArc(sketch, "E4030", {"start": v(44.67, -61.14) * mm, "mid": v(43.66, -60.8) * mm, "end": v(42.62, -60.55) * mm});
            skArc(sketch, "E4031", {"start": v(42.62, -60.55) * mm, "mid": v(41.56, -60.4) * mm, "end": v(40.5, -60.35) * mm});
            skArc(sketch, "E4032", {"start": v(40.5, -60.35) * mm, "mid": v(40.22, -60.34) * mm, "end": v(39.94, -60.33) * mm});
            skArc(sketch, "E4033", {"start": v(39.94, -60.33) * mm, "mid": v(39.69, -60.3) * mm, "end": v(39.44, -60.28) * mm});
            skArc(sketch, "E4034", {"start": v(39.44, -60.28) * mm, "mid": v(39.24, -60.24) * mm, "end": v(39.04, -60.2) * mm});
            skArc(sketch, "E4035", {"start": v(39.04, -60.2) * mm, "mid": v(38.97, -60.17) * mm, "end": v(38.91, -60.1) * mm});
            skArc(sketch, "E4036", {"start": v(38.91, -60.1) * mm, "mid": v(38.89, -60.04) * mm, "end": v(38.89, -59.96) * mm});
            skArc(sketch, "E4037", {"start": v(38.89, -59.96) * mm, "mid": v(38.93, -59.8) * mm, "end": v(38.97, -59.63) * mm});
            skArc(sketch, "E4038", {"start": v(38.97, -59.63) * mm, "mid": v(39.04, -59.43) * mm, "end": v(39.11, -59.24) * mm});
            skArc(sketch, "E4039", {"start": v(39.11, -59.24) * mm, "mid": v(39.2, -59.02) * mm, "end": v(39.31, -58.81) * mm});
            skArc(sketch, "E4040", {"start": v(39.31, -58.81) * mm, "mid": v(39.5, -58.4) * mm, "end": v(39.64, -57.98) * mm});
            skArc(sketch, "E4041", {"start": v(39.64, -57.98) * mm, "mid": v(39.65, -57.75) * mm, "end": v(39.53, -57.55) * mm});
            skArc(sketch, "E4042", {"start": v(39.53, -57.55) * mm, "mid": v(39.32, -57.4) * mm, "end": v(39.06, -57.35) * mm});
            skArc(sketch, "E4043", {"start": v(39.06, -57.35) * mm, "mid": v(38.51, -57.38) * mm, "end": v(37.96, -57.43) * mm});
            skArc(sketch, "E4044", {"start": v(37.96, -57.43) * mm, "mid": v(37.61, -57.47) * mm, "end": v(37.26, -57.5) * mm});
            skArc(sketch, "E4045", {"start": v(37.26, -57.5) * mm, "mid": v(37.13, -57.5) * mm, "end": v(37, -57.47) * mm});
            skArc(sketch, "E4046", {"start": v(37, -57.47) * mm, "mid": v(36.93, -57.42) * mm, "end": v(36.9, -57.35) * mm});
            skArc(sketch, "E4047", {"start": v(36.9, -57.35) * mm, "mid": v(36.92, -57.22) * mm, "end": v(36.96, -57.1) * mm});
            skArc(sketch, "E4048", {"start": v(36.96, -57.1) * mm, "mid": v(37.12, -56.65) * mm, "end": v(37.23, -56.2) * mm});
            skArc(sketch, "E4049", {"start": v(37.23, -56.2) * mm, "mid": v(37.22, -55.93) * mm, "end": v(37.1, -55.7) * mm});
            skArc(sketch, "E4050", {"start": v(37.1, -55.7) * mm, "mid": v(36.86, -55.53) * mm, "end": v(36.58, -55.44) * mm});
            skArc(sketch, "E4051", {"start": v(36.58, -55.44) * mm, "mid": v(35.97, -55.4) * mm, "end": v(35.36, -55.37) * mm});
            skArc(sketch, "E4052", {"start": v(35.36, -55.37) * mm, "mid": v(35.13, -55.4) * mm, "end": v(34.9, -55.46) * mm});
            skArc(sketch, "E4053", {"start": v(34.9, -55.46) * mm, "mid": v(34.74, -55.56) * mm, "end": v(34.62, -55.72) * mm});
            skArc(sketch, "E4054", {"start": v(34.62, -55.72) * mm, "mid": v(34.58, -55.88) * mm, "end": v(34.62, -56.04) * mm});
            skArc(sketch, "E4055", {"start": v(34.62, -56.04) * mm, "mid": v(34.72, -56.2) * mm, "end": v(34.87, -56.33) * mm});
            skArc(sketch, "E4056", {"start": v(34.87, -56.33) * mm, "mid": v(35.1, -56.54) * mm, "end": v(35.25, -56.8) * mm});
            skArc(sketch, "E4057", {"start": v(35.25, -56.8) * mm, "mid": v(35.4, -57.3) * mm, "end": v(35.5, -57.8) * mm});
            skArc(sketch, "E4058", {"start": v(35.5, -57.8) * mm, "mid": v(35.57, -58.35) * mm, "end": v(35.59, -58.9) * mm});
            skArc(sketch, "E4059", {"start": v(35.59, -58.9) * mm, "mid": v(35.55, -59.33) * mm, "end": v(35.44, -59.74) * mm});
            skArc(sketch, "E4060", {"start": v(35.44, -59.74) * mm, "mid": v(35.35, -60) * mm, "end": v(35.28, -60.26) * mm});
            skArc(sketch, "E4061", {"start": v(35.28, -60.26) * mm, "mid": v(35.25, -60.43) * mm, "end": v(35.25, -60.6) * mm});
            skArc(sketch, "E4062", {"start": v(35.25, -60.6) * mm, "mid": v(35.29, -60.74) * mm, "end": v(35.35, -60.88) * mm});
            skArc(sketch, "E4063", {"start": v(35.35, -60.88) * mm, "mid": v(35.47, -61.05) * mm, "end": v(35.6, -61.2) * mm});
            skArc(sketch, "E4064", {"start": v(35.6, -61.2) * mm, "mid": v(35.75, -61.38) * mm, "end": v(35.9, -61.56) * mm});
            skArc(sketch, "E4065", {"start": v(35.9, -61.56) * mm, "mid": v(35.94, -61.62) * mm, "end": v(35.94, -61.7) * mm});
            skArc(sketch, "E4066", {"start": v(35.94, -61.7) * mm, "mid": v(35.91, -61.76) * mm, "end": v(35.86, -61.8) * mm});
            skArc(sketch, "E4067", {"start": v(35.86, -61.8) * mm, "mid": v(35.67, -61.86) * mm, "end": v(35.49, -61.91) * mm});
            skArc(sketch, "E4068", {"start": v(35.49, -61.91) * mm, "mid": v(35.37, -61.95) * mm, "end": v(35.26, -62) * mm});
            skArc(sketch, "E4069", {"start": v(35.26, -62) * mm, "mid": v(35.15, -62.08) * mm, "end": v(35.06, -62.16) * mm});
            skArc(sketch, "E4070", {"start": v(35.06, -62.16) * mm, "mid": v(34.99, -62.25) * mm, "end": v(34.93, -62.34) * mm});
            skArc(sketch, "E4071", {"start": v(34.93, -62.34) * mm, "mid": v(34.9, -62.44) * mm, "end": v(34.88, -62.53) * mm});
            skArc(sketch, "E4072", {"start": v(34.88, -62.53) * mm, "mid": v(34.86, -62.74) * mm, "end": v(34.8, -62.93) * mm});
            skArc(sketch, "E4073", {"start": v(34.8, -62.93) * mm, "mid": v(34.7, -63.13) * mm, "end": v(34.56, -63.3) * mm});
            skArc(sketch, "E4074", {"start": v(34.56, -63.3) * mm, "mid": v(34.4, -63.45) * mm, "end": v(34.23, -63.57) * mm});
            skArc(sketch, "E4075", {"start": v(34.23, -63.57) * mm, "mid": v(34.06, -63.64) * mm, "end": v(33.88, -63.66) * mm});
            skArc(sketch, "E4076", {"start": v(33.88, -63.66) * mm, "mid": v(33.62, -63.62) * mm, "end": v(33.39, -63.5) * mm});
            skArc(sketch, "E4077", {"start": v(33.39, -63.5) * mm, "mid": v(33.17, -63.3) * mm, "end": v(33, -63.06) * mm});
            skArc(sketch, "E4078", {"start": v(33, -63.06) * mm, "mid": v(32.85, -62.72) * mm, "end": v(32.75, -62.37) * mm});
            skArc(sketch, "E4079", {"start": v(32.75, -62.37) * mm, "mid": v(32.69, -61.92) * mm, "end": v(32.67, -61.48) * mm});
            skArc(sketch, "E4080", {"start": v(32.67, -61.48) * mm, "mid": v(32.67, -61.22) * mm, "end": v(32.66, -60.96) * mm});
            skArc(sketch, "E4081", {"start": v(32.66, -60.96) * mm, "mid": v(32.64, -60.73) * mm, "end": v(32.62, -60.5) * mm});
            skArc(sketch, "E4082", {"start": v(32.62, -60.5) * mm, "mid": v(32.6, -60.31) * mm, "end": v(32.57, -60.13) * mm});
            skArc(sketch, "E4083", {"start": v(32.57, -60.13) * mm, "mid": v(32.55, -60.06) * mm, "end": v(32.51, -60) * mm});
            skArc(sketch, "E4084", {"start": v(32.51, -60) * mm, "mid": v(32.36, -59.91) * mm, "end": v(32.18, -59.9) * mm});
            skArc(sketch, "E4085", {"start": v(32.18, -59.9) * mm, "mid": v(31.96, -59.94) * mm, "end": v(31.76, -60.05) * mm});
            skArc(sketch, "E4086", {"start": v(31.76, -60.05) * mm, "mid": v(31.56, -60.22) * mm, "end": v(31.39, -60.42) * mm});
            skArc(sketch, "E4087", {"start": v(31.39, -60.42) * mm, "mid": v(31.26, -60.65) * mm, "end": v(31.19, -60.9) * mm});
            skArc(sketch, "E4088", {"start": v(31.19, -60.9) * mm, "mid": v(31.09, -61.23) * mm, "end": v(30.93, -61.52) * mm});
            skArc(sketch, "E4089", {"start": v(30.93, -61.52) * mm, "mid": v(30.7, -61.77) * mm, "end": v(30.44, -61.98) * mm});
            skArc(sketch, "E4090", {"start": v(30.44, -61.98) * mm, "mid": v(30.03, -62.2) * mm, "end": v(29.59, -62.39) * mm});
            skArc(sketch, "E4091", {"start": v(29.59, -62.39) * mm, "mid": v(28.85, -62.63) * mm, "end": v(28.1, -62.85) * mm});
            skArc(sketch, "E4092", {"start": v(28.1, -62.85) * mm, "mid": v(27.77, -62.94) * mm, "end": v(27.44, -63.04) * mm});
            skArc(sketch, "E4093", {"start": v(27.44, -63.04) * mm, "mid": v(27.11, -63.14) * mm, "end": v(26.8, -63.24) * mm});
            skArc(sketch, "E4094", {"start": v(26.8, -63.24) * mm, "mid": v(26.52, -63.32) * mm, "end": v(26.25, -63.41) * mm});
            skArc(sketch, "E4095", {"start": v(26.25, -63.41) * mm, "mid": v(26.1, -63.46) * mm, "end": v(25.96, -63.52) * mm});
            skArc(sketch, "E4096", {"start": v(25.96, -63.52) * mm, "mid": v(25.84, -63.57) * mm, "end": v(25.71, -63.6) * mm});
            skArc(sketch, "E4097", {"start": v(25.71, -63.6) * mm, "mid": v(25.65, -63.6) * mm, "end": v(25.6, -63.58) * mm});
            skArc(sketch, "E4098", {"start": v(25.6, -63.58) * mm, "mid": v(25.58, -63.53) * mm, "end": v(25.58, -63.48) * mm});
            skArc(sketch, "E4099", {"start": v(25.58, -63.48) * mm, "mid": v(25.61, -63.34) * mm, "end": v(25.66, -63.21) * mm});
            skArc(sketch, "E4100", {"start": v(25.66, -63.21) * mm, "mid": v(25.7, -63.1) * mm, "end": v(25.76, -62.98) * mm});
            skArc(sketch, "E4101", {"start": v(25.76, -62.98) * mm, "mid": v(25.83, -62.84) * mm, "end": v(25.9, -62.7) * mm});
            skArc(sketch, "E4102", {"start": v(25.9, -62.7) * mm, "mid": v(26, -62.57) * mm, "end": v(26.08, -62.44) * mm});
            skArc(sketch, "E4103", {"start": v(26.08, -62.44) * mm, "mid": v(26.16, -62.33) * mm, "end": v(26.25, -62.22) * mm});
            skArc(sketch, "E4104", {"start": v(26.25, -62.22) * mm, "mid": v(26.36, -62.08) * mm, "end": v(26.47, -61.94) * mm});
            skArc(sketch, "E4105", {"start": v(26.47, -61.94) * mm, "mid": v(26.5, -61.87) * mm, "end": v(26.51, -61.79) * mm});
            skArc(sketch, "E4106", {"start": v(26.51, -61.79) * mm, "mid": v(26.5, -61.72) * mm, "end": v(26.44, -61.68) * mm});
            skArc(sketch, "E4107", {"start": v(26.44, -61.68) * mm, "mid": v(26.32, -61.61) * mm, "end": v(26.2, -61.56) * mm});
            skArc(sketch, "E4108", {"start": v(26.2, -61.56) * mm, "mid": v(26.07, -61.5) * mm, "end": v(25.96, -61.43) * mm});
            skArc(sketch, "E4109", {"start": v(25.96, -61.43) * mm, "mid": v(25.91, -61.37) * mm, "end": v(25.9, -61.3) * mm});
            skArc(sketch, "E4110", {"start": v(25.9, -61.3) * mm, "mid": v(25.94, -61.2) * mm, "end": v(26, -61.1) * mm});
            skArc(sketch, "E4111", {"start": v(26, -61.1) * mm, "mid": v(26.18, -60.9) * mm, "end": v(26.36, -60.7) * mm});
            skArc(sketch, "E4112", {"start": v(26.36, -60.7) * mm, "mid": v(26.52, -60.54) * mm, "end": v(26.68, -60.4) * mm});
            skArc(sketch, "E4113", {"start": v(26.68, -60.4) * mm, "mid": v(26.9, -60.22) * mm, "end": v(27.12, -60.06) * mm});
            skArc(sketch, "E4114", {"start": v(27.12, -60.06) * mm, "mid": v(27.36, -59.9) * mm, "end": v(27.6, -59.73) * mm});
            skArc(sketch, "E4115", {"start": v(27.6, -59.73) * mm, "mid": v(27.82, -59.6) * mm, "end": v(28.05, -59.48) * mm});
            skArc(sketch, "E4116", {"start": v(28.05, -59.48) * mm, "mid": v(28.24, -59.37) * mm, "end": v(28.44, -59.25) * mm});
            skArc(sketch, "E4117", {"start": v(28.44, -59.25) * mm, "mid": v(28.6, -59.14) * mm, "end": v(28.74, -59.02) * mm});
            skArc(sketch, "E4118", {"start": v(28.74, -59.02) * mm, "mid": v(28.84, -58.92) * mm, "end": v(28.92, -58.81) * mm});
            skArc(sketch, "E4119", {"start": v(28.92, -58.81) * mm, "mid": v(28.95, -58.75) * mm, "end": v(28.93, -58.68) * mm});
            skArc(sketch, "E4120", {"start": v(28.93, -58.68) * mm, "mid": v(28.66, -58.43) * mm, "end": v(28.3, -58.36) * mm});
            skArc(sketch, "E4121", {"start": v(28.3, -58.36) * mm, "mid": v(27.54, -58.47) * mm, "end": v(26.8, -58.64) * mm});
            skArc(sketch, "E4122", {"start": v(26.8, -58.64) * mm, "mid": v(25.99, -58.9) * mm, "end": v(25.2, -59.22) * mm});
            skArc(sketch, "E4123", {"start": v(25.2, -59.22) * mm, "mid": v(24.59, -59.56) * mm, "end": v(24.03, -59.99) * mm});
            skArc(sketch, "E4124", {"start": v(24.03, -59.99) * mm, "mid": v(23.88, -60.12) * mm, "end": v(23.73, -60.25) * mm});
            skArc(sketch, "E4125", {"start": v(23.73, -60.25) * mm, "mid": v(23.68, -60.27) * mm, "end": v(23.62, -60.26) * mm});
            skArc(sketch, "E4126", {"start": v(23.62, -60.26) * mm, "mid": v(23.57, -60.22) * mm, "end": v(23.55, -60.17) * mm});
            skArc(sketch, "E4127", {"start": v(23.55, -60.17) * mm, "mid": v(23.55, -59.96) * mm, "end": v(23.54, -59.76) * mm});
            skArc(sketch, "E4128", {"start": v(23.54, -59.76) * mm, "mid": v(23.55, -59.6) * mm, "end": v(23.57, -59.46) * mm});
            skArc(sketch, "E4129", {"start": v(23.57, -59.46) * mm, "mid": v(23.62, -59.28) * mm, "end": v(23.67, -59.1) * mm});
            skArc(sketch, "E4130", {"start": v(23.67, -59.1) * mm, "mid": v(23.73, -58.94) * mm, "end": v(23.8, -58.77) * mm});
            skArc(sketch, "E4131", {"start": v(23.8, -58.77) * mm, "mid": v(23.88, -58.62) * mm, "end": v(23.96, -58.49) * mm});
            skArc(sketch, "E4132", {"start": v(23.96, -58.49) * mm, "mid": v(24.08, -58.3) * mm, "end": v(24.18, -58.12) * mm});
            skArc(sketch, "E4133", {"start": v(24.18, -58.12) * mm, "mid": v(24.22, -58) * mm, "end": v(24.21, -57.88) * mm});
            skArc(sketch, "E4134", {"start": v(24.21, -57.88) * mm, "mid": v(24.16, -57.74) * mm, "end": v(24.08, -57.62) * mm});
            skArc(sketch, "E4135", {"start": v(24.08, -57.62) * mm, "mid": v(23.89, -57.4) * mm, "end": v(23.69, -57.2) * mm});
            skArc(sketch, "E4136", {"start": v(23.69, -57.2) * mm, "mid": v(23.55, -57.05) * mm, "end": v(23.42, -56.9) * mm});
            skArc(sketch, "E4137", {"start": v(23.42, -56.9) * mm, "mid": v(23.3, -56.74) * mm, "end": v(23.2, -56.58) * mm});
            skArc(sketch, "E4138", {"start": v(23.2, -56.58) * mm, "mid": v(23.11, -56.43) * mm, "end": v(23.04, -56.28) * mm});
            skArc(sketch, "E4139", {"start": v(23.04, -56.28) * mm, "mid": v(23, -56.18) * mm, "end": v(23, -56.07) * mm});
            skArc(sketch, "E4140", {"start": v(23, -56.07) * mm, "mid": v(23, -55.92) * mm, "end": v(23.03, -55.77) * mm});
            skArc(sketch, "E4141", {"start": v(23.03, -55.77) * mm, "mid": v(23.08, -55.7) * mm, "end": v(23.16, -55.67) * mm});
            skArc(sketch, "E4142", {"start": v(23.16, -55.67) * mm, "mid": v(23.28, -55.69) * mm, "end": v(23.4, -55.73) * mm});
            skArc(sketch, "E4143", {"start": v(23.4, -55.73) * mm, "mid": v(23.66, -55.9) * mm, "end": v(23.92, -56.06) * mm});
            skArc(sketch, "E4144", {"start": v(23.92, -56.06) * mm, "mid": v(24.08, -56.15) * mm, "end": v(24.25, -56.23) * mm});
            skArc(sketch, "E4145", {"start": v(24.25, -56.23) * mm, "mid": v(24.49, -56.32) * mm, "end": v(24.73, -56.4) * mm});
            skArc(sketch, "E4146", {"start": v(24.73, -56.4) * mm, "mid": v(25, -56.48) * mm, "end": v(25.28, -56.55) * mm});
            skArc(sketch, "E4147", {"start": v(25.28, -56.55) * mm, "mid": v(25.55, -56.6) * mm, "end": v(25.81, -56.64) * mm});
            skArc(sketch, "E4148", {"start": v(25.81, -56.64) * mm, "mid": v(26.18, -56.69) * mm, "end": v(26.55, -56.72) * mm});
            skArc(sketch, "E4149", {"start": v(26.55, -56.72) * mm, "mid": v(26.75, -56.72) * mm, "end": v(26.95, -56.68) * mm});
            skArc(sketch, "E4150", {"start": v(26.95, -56.68) * mm, "mid": v(27.1, -56.61) * mm, "end": v(27.23, -56.5) * mm});
            skArc(sketch, "E4151", {"start": v(27.23, -56.5) * mm, "mid": v(27.4, -56.33) * mm, "end": v(27.53, -56.13) * mm});
            skArc(sketch, "E4152", {"start": v(27.53, -56.13) * mm, "mid": v(27.7, -55.83) * mm, "end": v(27.8, -55.51) * mm});
            skArc(sketch, "E4153", {"start": v(27.8, -55.51) * mm, "mid": v(27.83, -55.25) * mm, "end": v(27.77, -55) * mm});
            skArc(sketch, "E4154", {"start": v(27.77, -55) * mm, "mid": v(27.62, -54.75) * mm, "end": v(27.4, -54.57) * mm});
            skArc(sketch, "E4155", {"start": v(27.4, -54.57) * mm, "mid": v(27.06, -54.37) * mm, "end": v(26.7, -54.22) * mm});
            skArc(sketch, "E4156", {"start": v(26.7, -54.22) * mm, "mid": v(26.52, -54.15) * mm, "end": v(26.34, -54.07) * mm});
            skArc(sketch, "E4157", {"start": v(26.34, -54.07) * mm, "mid": v(26.18, -54) * mm, "end": v(26.03, -53.92) * mm});
            skArc(sketch, "E4158", {"start": v(26.03, -53.92) * mm, "mid": v(25.92, -53.85) * mm, "end": v(25.8, -53.78) * mm});
            skArc(sketch, "E4159", {"start": v(25.8, -53.78) * mm, "mid": v(25.77, -53.74) * mm, "end": v(25.76, -53.69) * mm});
            skArc(sketch, "E4160", {"start": v(25.76, -53.69) * mm, "mid": v(25.82, -53.5) * mm, "end": v(25.98, -53.36) * mm});
            skArc(sketch, "E4161", {"start": v(25.98, -53.36) * mm, "mid": v(26.44, -53.2) * mm, "end": v(26.92, -53.05) * mm});
            skArc(sketch, "E4162", {"start": v(26.92, -53.05) * mm, "mid": v(27.5, -52.92) * mm, "end": v(28.1, -52.83) * mm});
            skArc(sketch, "E4163", {"start": v(28.1, -52.83) * mm, "mid": v(28.69, -52.78) * mm, "end": v(29.28, -52.77) * mm});
            skArc(sketch, "E4164", {"start": v(29.28, -52.77) * mm, "mid": v(29.84, -52.77) * mm, "end": v(30.4, -52.74) * mm});
            skArc(sketch, "E4165", {"start": v(30.4, -52.74) * mm, "mid": v(30.66, -52.7) * mm, "end": v(30.9, -52.58) * mm});
            skArc(sketch, "E4166", {"start": v(30.9, -52.58) * mm, "mid": v(31, -52.44) * mm, "end": v(30.98, -52.28) * mm});
            skArc(sketch, "E4167", {"start": v(30.98, -52.28) * mm, "mid": v(30.85, -52.04) * mm, "end": v(30.68, -51.83) * mm});
            skArc(sketch, "E4168", {"start": v(30.68, -51.83) * mm, "mid": v(30.63, -51.6) * mm, "end": v(30.83, -51.46) * mm});
            skArc(sketch, "E4169", {"start": v(30.83, -51.46) * mm, "mid": v(31.59, -51.48) * mm, "end": v(32.34, -51.57) * mm});
            skArc(sketch, "E4170", {"start": v(32.34, -51.57) * mm, "mid": v(33.46, -51.8) * mm, "end": v(34.57, -52.08) * mm});
            skArc(sketch, "E4171", {"start": v(34.57, -52.08) * mm, "mid": v(35.6, -52.41) * mm, "end": v(36.6, -52.82) * mm});
            skArc(sketch, "E4172", {"start": v(36.6, -52.82) * mm, "mid": v(37, -53) * mm, "end": v(37.4, -53.16) * mm});
            skArc(sketch, "E4173", {"start": v(37.4, -53.16) * mm, "mid": v(37.56, -53.21) * mm, "end": v(37.72, -53.24) * mm});
            skArc(sketch, "E4174", {"start": v(37.72, -53.24) * mm, "mid": v(37.8, -53.22) * mm, "end": v(37.86, -53.16) * mm});
            skArc(sketch, "E4175", {"start": v(37.86, -53.16) * mm, "mid": v(37.9, -53.04) * mm, "end": v(37.92, -52.93) * mm});
            skArc(sketch, "E4176", {"start": v(37.92, -52.93) * mm, "mid": v(37.91, -52.81) * mm, "end": v(37.9, -52.7) * mm});
            skArc(sketch, "E4177", {"start": v(37.9, -52.7) * mm, "mid": v(37.85, -52.55) * mm, "end": v(37.8, -52.4) * mm});
            skArc(sketch, "E4178", {"start": v(37.8, -52.4) * mm, "mid": v(37.73, -52.26) * mm, "end": v(37.66, -52.1) * mm});
            skArc(sketch, "E4179", {"start": v(37.66, -52.1) * mm, "mid": v(37.58, -51.97) * mm, "end": v(37.5, -51.84) * mm});
            skArc(sketch, "E4180", {"start": v(37.5, -51.84) * mm, "mid": v(37.37, -51.65) * mm, "end": v(37.27, -51.45) * mm});
            skArc(sketch, "E4181", {"start": v(37.27, -51.45) * mm, "mid": v(37.26, -51.37) * mm, "end": v(37.32, -51.3) * mm});
            skArc(sketch, "E4182", {"start": v(37.32, -51.3) * mm, "mid": v(37.45, -51.25) * mm, "end": v(37.58, -51.23) * mm});
            skArc(sketch, "E4183", {"start": v(37.58, -51.23) * mm, "mid": v(38.13, -51.22) * mm, "end": v(38.67, -51.22) * mm});
            skArc(sketch, "E4184", {"start": v(38.67, -51.22) * mm, "mid": v(39.45, -51.27) * mm, "end": v(40.22, -51.4) * mm});
            skArc(sketch, "E4185", {"start": v(40.22, -51.4) * mm, "mid": v(40.99, -51.62) * mm, "end": v(41.72, -51.92) * mm});
            skArc(sketch, "E4186", {"start": v(41.72, -51.92) * mm, "mid": v(42.47, -52.31) * mm, "end": v(43.18, -52.78) * mm});
            skArc(sketch, "E4187", {"start": v(43.18, -52.78) * mm, "mid": v(43.9, -53.35) * mm, "end": v(44.58, -53.98) * mm});
            skArc(sketch, "E4188", {"start": v(44.58, -53.98) * mm, "mid": v(44.85, -54.25) * mm, "end": v(45.13, -54.5) * mm});
            skArc(sketch, "E4189", {"start": v(45.13, -54.5) * mm, "mid": v(45.38, -54.72) * mm, "end": v(45.63, -54.93) * mm});
            skArc(sketch, "E4190", {"start": v(45.63, -54.93) * mm, "mid": v(45.84, -55.08) * mm, "end": v(46.05, -55.24) * mm});
            skArc(sketch, "E4191", {"start": v(46.05, -55.24) * mm, "mid": v(46.13, -55.26) * mm, "end": v(46.2, -55.24) * mm});
            skArc(sketch, "E4192", {"start": v(46.2, -55.24) * mm, "mid": v(46.26, -55.19) * mm, "end": v(46.28, -55.12) * mm});
            skArc(sketch, "E4193", {"start": v(46.28, -55.12) * mm, "mid": v(46.3, -54.95) * mm, "end": v(46.32, -54.77) * mm});
            skArc(sketch, "E4194", {"start": v(46.32, -54.77) * mm, "mid": v(46.33, -54.56) * mm, "end": v(46.32, -54.34) * mm});
            skArc(sketch, "E4195", {"start": v(46.32, -54.34) * mm, "mid": v(46.3, -54.1) * mm, "end": v(46.29, -53.85) * mm});
            skArc(sketch, "E4196", {"start": v(46.29, -53.85) * mm, "mid": v(46.26, -53.61) * mm, "end": v(46.25, -53.37) * mm});
            skArc(sketch, "E4197", {"start": v(46.25, -53.37) * mm, "mid": v(46.25, -53.17) * mm, "end": v(46.26, -52.97) * mm});
            skArc(sketch, "E4198", {"start": v(46.26, -52.97) * mm, "mid": v(46.28, -52.82) * mm, "end": v(46.31, -52.68) * mm});
            skArc(sketch, "E4199", {"start": v(46.31, -52.68) * mm, "mid": v(46.34, -52.62) * mm, "end": v(46.4, -52.6) * mm});
            skArc(sketch, "E4200", {"start": v(46.4, -52.6) * mm, "mid": v(46.62, -52.64) * mm, "end": v(46.81, -52.73) * mm});
            skArc(sketch, "E4201", {"start": v(46.81, -52.73) * mm, "mid": v(47.22, -53.02) * mm, "end": v(47.61, -53.32) * mm});
            skArc(sketch, "E4202", {"start": v(47.61, -53.32) * mm, "mid": v(48.02, -53.65) * mm, "end": v(48.42, -54) * mm});
            skArc(sketch, "E4203", {"start": v(48.42, -54) * mm, "mid": v(48.73, -54.32) * mm, "end": v(49.01, -54.65) * mm});
            skArc(sketch, "E4204", {"start": v(49.01, -54.65) * mm, "mid": v(49.27, -54.93) * mm, "end": v(49.56, -55.18) * mm});
            skArc(sketch, "E4205", {"start": v(49.56, -55.18) * mm, "mid": v(49.73, -55.2) * mm, "end": v(49.84, -55.07) * mm});
            skArc(sketch, "E4206", {"start": v(49.84, -55.07) * mm, "mid": v(49.88, -54.72) * mm, "end": v(49.82, -54.38) * mm});
            skArc(sketch, "E4207", {"start": v(49.82, -54.38) * mm, "mid": v(49.62, -53.7) * mm, "end": v(49.39, -53.03) * mm});
            skArc(sketch, "E4208", {"start": v(49.39, -53.03) * mm, "mid": v(49.1, -52.26) * mm, "end": v(48.77, -51.5) * mm});
            skArc(sketch, "E4209", {"start": v(48.77, -51.5) * mm, "mid": v(48.46, -50.83) * mm, "end": v(48.1, -50.18) * mm});
            skArc(sketch, "E4210", {"start": v(48.1, -50.18) * mm, "mid": v(47.75, -49.58) * mm, "end": v(47.37, -49.01) * mm});
            skArc(sketch, "E4211", {"start": v(47.37, -49.01) * mm, "mid": v(46.97, -48.48) * mm, "end": v(46.54, -47.97) * mm});
            skArc(sketch, "E4212", {"start": v(46.54, -47.97) * mm, "mid": v(46.2, -47.61) * mm, "end": v(45.87, -47.26) * mm});
            skArc(sketch, "E4213", {"start": v(45.87, -47.26) * mm, "mid": v(45.74, -47.17) * mm, "end": v(45.59, -47.13) * mm});
            skArc(sketch, "E4214", {"start": v(45.59, -47.13) * mm, "mid": v(45.48, -47.16) * mm, "end": v(45.42, -47.26) * mm});
            skArc(sketch, "E4215", {"start": v(45.42, -47.26) * mm, "mid": v(45.4, -47.58) * mm, "end": v(45.39, -47.9) * mm});
            skArc(sketch, "E4216", {"start": v(45.39, -47.9) * mm, "mid": v(45.38, -48.11) * mm, "end": v(45.36, -48.32) * mm});
            skArc(sketch, "E4217", {"start": v(45.36, -48.32) * mm, "mid": v(45.33, -48.44) * mm, "end": v(45.27, -48.56) * mm});
            skArc(sketch, "E4218", {"start": v(45.27, -48.56) * mm, "mid": v(45.2, -48.64) * mm, "end": v(45.1, -48.69) * mm});
            skArc(sketch, "E4219", {"start": v(45.1, -48.69) * mm, "mid": v(44.97, -48.72) * mm, "end": v(44.83, -48.73) * mm});
            skArc(sketch, "E4220", {"start": v(44.83, -48.73) * mm, "mid": v(44.69, -48.75) * mm, "end": v(44.55, -48.8) * mm});
            skArc(sketch, "E4221", {"start": v(44.55, -48.8) * mm, "mid": v(44.45, -48.86) * mm, "end": v(44.38, -48.96) * mm});
            skArc(sketch, "E4222", {"start": v(44.38, -48.96) * mm, "mid": v(44.33, -49.13) * mm, "end": v(44.3, -49.3) * mm});
            skArc(sketch, "E4223", {"start": v(44.3, -49.3) * mm, "mid": v(44.29, -49.65) * mm, "end": v(44.28, -50) * mm});
            skArc(sketch, "E4224", {"start": v(44.28, -50) * mm, "mid": v(44.28, -50.3) * mm, "end": v(44.26, -50.58) * mm});
            skArc(sketch, "E4225", {"start": v(44.26, -50.58) * mm, "mid": v(44.24, -50.76) * mm, "end": v(44.2, -50.94) * mm});
            skArc(sketch, "E4226", {"start": v(44.2, -50.94) * mm, "mid": v(44.16, -51.04) * mm, "end": v(44.09, -51.12) * mm});
            skArc(sketch, "E4227", {"start": v(44.09, -51.12) * mm, "mid": v(44.02, -51.15) * mm, "end": v(43.94, -51.15) * mm});
            skArc(sketch, "E4228", {"start": v(43.94, -51.15) * mm, "mid": v(43.86, -51.1) * mm, "end": v(43.8, -51.03) * mm});
            skArc(sketch, "E4229", {"start": v(43.8, -51.03) * mm, "mid": v(43.74, -50.9) * mm, "end": v(43.69, -50.76) * mm});
            skArc(sketch, "E4230", {"start": v(43.69, -50.76) * mm, "mid": v(43.64, -50.57) * mm, "end": v(43.61, -50.39) * mm});
            skArc(sketch, "E4231", {"start": v(43.61, -50.39) * mm, "mid": v(43.6, -50.17) * mm, "end": v(43.6, -49.96) * mm});
            skArc(sketch, "E4232", {"start": v(43.6, -49.96) * mm, "mid": v(43.58, -49.7) * mm, "end": v(43.57, -49.43) * mm});
            skArc(sketch, "E4233", {"start": v(43.57, -49.43) * mm, "mid": v(43.54, -49.26) * mm, "end": v(43.48, -49.1) * mm});
            skArc(sketch, "E4234", {"start": v(43.48, -49.1) * mm, "mid": v(43.42, -48.98) * mm, "end": v(43.33, -48.9) * mm});
            skArc(sketch, "E4235", {"start": v(43.33, -48.9) * mm, "mid": v(43.23, -48.82) * mm, "end": v(43.1, -48.79) * mm});
            skArc(sketch, "E4236", {"start": v(43.1, -48.79) * mm, "mid": v(42.98, -48.74) * mm, "end": v(42.87, -48.66) * mm});
            skArc(sketch, "E4237", {"start": v(42.87, -48.66) * mm, "mid": v(42.78, -48.55) * mm, "end": v(42.72, -48.42) * mm});
            skArc(sketch, "E4238", {"start": v(42.72, -48.42) * mm, "mid": v(42.67, -48.2) * mm, "end": v(42.64, -48) * mm});
            skArc(sketch, "E4239", {"start": v(42.64, -48) * mm, "mid": v(42.63, -47.62) * mm, "end": v(42.62, -47.24) * mm});
            skArc(sketch, "E4240", {"start": v(42.62, -47.24) * mm, "mid": v(42.62, -46.77) * mm, "end": v(42.6, -46.3) * mm});
            skArc(sketch, "E4241", {"start": v(42.6, -46.3) * mm, "mid": v(42.57, -46.11) * mm, "end": v(42.49, -45.93) * mm});
            skArc(sketch, "E4242", {"start": v(42.49, -45.93) * mm, "mid": v(42.38, -45.79) * mm, "end": v(42.23, -45.69) * mm});
            skArc(sketch, "E4243", {"start": v(42.23, -45.69) * mm, "mid": v(41.9, -45.56) * mm, "end": v(41.59, -45.44) * mm});
            skArc(sketch, "E4244", {"start": v(41.59, -45.44) * mm, "mid": v(41.3, -45.36) * mm, "end": v(41.01, -45.3) * mm});
            skArc(sketch, "E4245", {"start": v(41.01, -45.3) * mm, "mid": v(40.54, -45.22) * mm, "end": v(40.06, -45.15) * mm});
            skArc(sketch, "E4246", {"start": v(40.06, -45.15) * mm, "mid": v(39.51, -45.08) * mm, "end": v(38.96, -45.03) * mm});
            skArc(sketch, "E4247", {"start": v(38.96, -45.03) * mm, "mid": v(38.4, -44.98) * mm, "end": v(37.85, -44.94) * mm});
            skArc(sketch, "E4248", {"start": v(37.85, -44.94) * mm, "mid": v(37.33, -44.9) * mm, "end": v(36.8, -44.86) * mm});
            skArc(sketch, "E4249", {"start": v(36.8, -44.86) * mm, "mid": v(36.37, -44.81) * mm, "end": v(35.94, -44.75) * mm});
            skArc(sketch, "E4250", {"start": v(35.94, -44.75) * mm, "mid": v(35.6, -44.7) * mm, "end": v(35.25, -44.63) * mm});
            skArc(sketch, "E4251", {"start": v(35.25, -44.63) * mm, "mid": v(35.18, -44.59) * mm, "end": v(35.16, -44.51) * mm});
            skArc(sketch, "E4252", {"start": v(35.16, -44.51) * mm, "mid": v(35.16, -44.43) * mm, "end": v(35.19, -44.35) * mm});
            skArc(sketch, "E4253", {"start": v(35.19, -44.35) * mm, "mid": v(35.25, -44.2) * mm, "end": v(35.32, -44.05) * mm});
            skArc(sketch, "E4254", {"start": v(35.32, -44.05) * mm, "mid": v(35.4, -43.87) * mm, "end": v(35.5, -43.7) * mm});
            skArc(sketch, "E4255", {"start": v(35.5, -43.7) * mm, "mid": v(35.6, -43.51) * mm, "end": v(35.71, -43.33) * mm});
            skLineSegment(sketch, "E4256", {"start": v(35.71, -43.33) * mm, "end": v(36.27, -42.43) * mm});
            skLineSegment(sketch, "E4257", {"start": v(36.27, -42.43) * mm, "end": v(35.4, -42.13) * mm});
            skArc(sketch, "E4258", {"start": v(35.4, -42.13) * mm, "mid": v(35.2, -42.06) * mm, "end": v(34.99, -42) * mm});
            skArc(sketch, "E4259", {"start": v(34.99, -42) * mm, "mid": v(34.73, -41.95) * mm, "end": v(34.47, -41.9) * mm});
            skArc(sketch, "E4260", {"start": v(34.47, -41.9) * mm, "mid": v(34.2, -41.87) * mm, "end": v(33.93, -41.84) * mm});
            skArc(sketch, "E4261", {"start": v(33.93, -41.84) * mm, "mid": v(33.7, -41.83) * mm, "end": v(33.46, -41.82) * mm});
            skLineSegment(sketch, "E4262", {"start": v(33.46, -41.82) * mm, "end": v(32.4, -41.82) * mm});
            skLineSegment(sketch, "E4263", {"start": v(32.4, -41.82) * mm, "end": v(32.4, -44.03) * mm});
            skArc(sketch, "E4264", {"start": v(32.4, -44.03) * mm, "mid": v(32.39, -44.73) * mm, "end": v(32.38, -45.43) * mm});
            skArc(sketch, "E4265", {"start": v(32.38, -45.43) * mm, "mid": v(32.36, -45.68) * mm, "end": v(32.3, -45.93) * mm});
            skArc(sketch, "E4266", {"start": v(32.3, -45.93) * mm, "mid": v(32.23, -46.07) * mm, "end": v(32.11, -46.16) * mm});
            skArc(sketch, "E4267", {"start": v(32.11, -46.16) * mm, "mid": v(31.94, -46.22) * mm, "end": v(31.76, -46.24) * mm});
            skArc(sketch, "E4268", {"start": v(31.76, -46.24) * mm, "mid": v(31.58, -46.26) * mm, "end": v(31.4, -46.3) * mm});
            skArc(sketch, "E4269", {"start": v(31.4, -46.3) * mm, "mid": v(31.3, -46.37) * mm, "end": v(31.22, -46.47) * mm});
            skArc(sketch, "E4270", {"start": v(31.22, -46.47) * mm, "mid": v(31.17, -46.65) * mm, "end": v(31.15, -46.83) * mm});
            skArc(sketch, "E4271", {"start": v(31.15, -46.83) * mm, "mid": v(31.14, -47.26) * mm, "end": v(31.14, -47.7) * mm});
            skArc(sketch, "E4272", {"start": v(31.14, -47.7) * mm, "mid": v(31.13, -48.06) * mm, "end": v(31.12, -48.42) * mm});
            skArc(sketch, "E4273", {"start": v(31.12, -48.42) * mm, "mid": v(31.1, -48.63) * mm, "end": v(31.06, -48.84) * mm});
            skArc(sketch, "E4274", {"start": v(31.06, -48.84) * mm, "mid": v(31, -48.96) * mm, "end": v(30.93, -49.06) * mm});
            skArc(sketch, "E4275", {"start": v(30.93, -49.06) * mm, "mid": v(30.84, -49.13) * mm, "end": v(30.73, -49.15) * mm});
            skArc(sketch, "E4276", {"start": v(30.73, -49.15) * mm, "mid": v(30.63, -49.13) * mm, "end": v(30.54, -49.06) * mm});
            skArc(sketch, "E4277", {"start": v(30.54, -49.06) * mm, "mid": v(30.46, -48.96) * mm, "end": v(30.42, -48.85) * mm});
            skArc(sketch, "E4278", {"start": v(30.42, -48.85) * mm, "mid": v(30.38, -48.64) * mm, "end": v(30.37, -48.43) * mm});
            skArc(sketch, "E4279", {"start": v(30.37, -48.43) * mm, "mid": v(30.37, -48.06) * mm, "end": v(30.38, -47.7) * mm});
            skArc(sketch, "E4280", {"start": v(30.38, -47.7) * mm, "mid": v(30.4, -47.28) * mm, "end": v(30.4, -46.86) * mm});
            skArc(sketch, "E4281", {"start": v(30.4, -46.86) * mm, "mid": v(30.38, -46.67) * mm, "end": v(30.34, -46.49) * mm});
            skArc(sketch, "E4282", {"start": v(30.34, -46.49) * mm, "mid": v(30.28, -46.38) * mm, "end": v(30.18, -46.31) * mm});
            skArc(sketch, "E4283", {"start": v(30.18, -46.31) * mm, "mid": v(30.04, -46.26) * mm, "end": v(29.9, -46.24) * mm});
            skArc(sketch, "E4284", {"start": v(29.9, -46.24) * mm, "mid": v(29.74, -46.22) * mm, "end": v(29.6, -46.14) * mm});
            skArc(sketch, "E4285", {"start": v(29.6, -46.14) * mm, "mid": v(29.5, -46.02) * mm, "end": v(29.44, -45.88) * mm});
            skArc(sketch, "E4286", {"start": v(29.44, -45.88) * mm, "mid": v(29.39, -45.6) * mm, "end": v(29.36, -45.3) * mm});
            skArc(sketch, "E4287", {"start": v(29.36, -45.3) * mm, "mid": v(29.35, -44.6) * mm, "end": v(29.35, -43.9) * mm});
            skLineSegment(sketch, "E4288", {"start": v(29.35, -43.9) * mm, "end": v(29.35, -41.54) * mm});
            skLineSegment(sketch, "E4289", {"start": v(29.35, -41.54) * mm, "end": v(28.18, -41.53) * mm});
            skLineSegment(sketch, "E4290", {"start": v(28.18, -41.53) * mm, "end": v(27, -41.52) * mm});
            skLineSegment(sketch, "E4291", {"start": v(27, -41.52) * mm, "end": v(28.04, -40.6) * mm});
            skArc(sketch, "E4292", {"start": v(28.04, -40.6) * mm, "mid": v(28.5, -40.18) * mm, "end": v(28.94, -39.74) * mm});
            skArc(sketch, "E4293", {"start": v(28.94, -39.74) * mm, "mid": v(29.03, -39.55) * mm, "end": v(29, -39.34) * mm});
            skArc(sketch, "E4294", {"start": v(29, -39.34) * mm, "mid": v(28.86, -39.17) * mm, "end": v(28.65, -39.1) * mm});
            skArc(sketch, "E4295", {"start": v(28.65, -39.1) * mm, "mid": v(27.98, -39.07) * mm, "end": v(27.32, -39.05) * mm});
            skArc(sketch, "E4296", {"start": v(27.32, -39.05) * mm, "mid": v(26.71, -39.04) * mm, "end": v(26.1, -39) * mm});
            skArc(sketch, "E4297", {"start": v(26.1, -39) * mm, "mid": v(25.53, -38.92) * mm, "end": v(24.96, -38.81) * mm});
            skArc(sketch, "E4298", {"start": v(24.96, -38.81) * mm, "mid": v(24.48, -38.7) * mm, "end": v(24, -38.54) * mm});
            skArc(sketch, "E4299", {"start": v(24, -38.54) * mm, "mid": v(23.7, -38.4) * mm, "end": v(23.44, -38.21) * mm});
            skArc(sketch, "E4300", {"start": v(23.44, -38.21) * mm, "mid": v(23.37, -38.03) * mm, "end": v(23.48, -37.87) * mm});
            skArc(sketch, "E4301", {"start": v(23.48, -37.87) * mm, "mid": v(23.98, -37.6) * mm, "end": v(24.5, -37.36) * mm});
            skArc(sketch, "E4302", {"start": v(24.5, -37.36) * mm, "mid": v(25.2, -37.1) * mm, "end": v(25.9, -36.87) * mm});
            skArc(sketch, "E4303", {"start": v(25.9, -36.87) * mm, "mid": v(26.66, -36.68) * mm, "end": v(27.42, -36.53) * mm});
            skLineSegment(sketch, "E4304", {"start": v(27.42, -36.53) * mm, "end": v(29.4, -36.2) * mm});
            skLineSegment(sketch, "E4305", {"start": v(29.4, -36.2) * mm, "end": v(29.24, -35.14) * mm});
            skArc(sketch, "E4306", {"start": v(29.24, -35.14) * mm, "mid": v(29.19, -34.8) * mm, "end": v(29.15, -34.45) * mm});
            skArc(sketch, "E4307", {"start": v(29.15, -34.45) * mm, "mid": v(29.15, -34.33) * mm, "end": v(29.2, -34.22) * mm});
            skArc(sketch, "E4308", {"start": v(29.2, -34.22) * mm, "mid": v(29.3, -34.14) * mm, "end": v(29.4, -34.1) * mm});
            skArc(sketch, "E4309", {"start": v(29.4, -34.1) * mm, "mid": v(29.68, -34.09) * mm, "end": v(29.97, -34.08) * mm});
            skArc(sketch, "E4310", {"start": v(29.97, -34.08) * mm, "mid": v(30.49, -34.12) * mm, "end": v(30.99, -34.25) * mm});
            skArc(sketch, "E4311", {"start": v(30.99, -34.25) * mm, "mid": v(31.68, -34.5) * mm, "end": v(32.36, -34.8) * mm});
            skArc(sketch, "E4312", {"start": v(32.36, -34.8) * mm, "mid": v(33.2, -35.2) * mm, "end": v(34, -35.66) * mm});
            skArc(sketch, "E4313", {"start": v(34, -35.66) * mm, "mid": v(34.94, -36.23) * mm, "end": v(35.86, -36.83) * mm});
            skArc(sketch, "E4314", {"start": v(35.86, -36.83) * mm, "mid": v(36.26, -37.1) * mm, "end": v(36.67, -37.37) * mm});
            skArc(sketch, "E4315", {"start": v(36.67, -37.37) * mm, "mid": v(37.02, -37.6) * mm, "end": v(37.37, -37.82) * mm});
            skArc(sketch, "E4316", {"start": v(37.37, -37.82) * mm, "mid": v(37.68, -38) * mm, "end": v(37.98, -38.2) * mm});
            skArc(sketch, "E4317", {"start": v(37.98, -38.2) * mm, "mid": v(38.04, -38.22) * mm, "end": v(38.1, -38.23) * mm});
            skArc(sketch, "E4318", {"start": v(38.1, -38.23) * mm, "mid": v(38.14, -38.2) * mm, "end": v(38.16, -38.17) * mm});
            skArc(sketch, "E4319", {"start": v(38.16, -38.17) * mm, "mid": v(38.17, -38) * mm, "end": v(38.18, -37.82) * mm});
            skArc(sketch, "E4320", {"start": v(38.18, -37.82) * mm, "mid": v(38.18, -37.6) * mm, "end": v(38.17, -37.37) * mm});
            skArc(sketch, "E4321", {"start": v(38.17, -37.37) * mm, "mid": v(38.16, -37.1) * mm, "end": v(38.14, -36.84) * mm});
            skArc(sketch, "E4322", {"start": v(38.14, -36.84) * mm, "mid": v(38.11, -36.58) * mm, "end": v(38.1, -36.31) * mm});
            skArc(sketch, "E4323", {"start": v(38.1, -36.31) * mm, "mid": v(38.08, -36.09) * mm, "end": v(38.07, -35.87) * mm});
            skArc(sketch, "E4324", {"start": v(38.07, -35.87) * mm, "mid": v(38.06, -35.68) * mm, "end": v(38.06, -35.5) * mm});
            skArc(sketch, "E4325", {"start": v(38.06, -35.5) * mm, "mid": v(38.07, -35.47) * mm, "end": v(38.1, -35.46) * mm});
            skArc(sketch, "E4326", {"start": v(38.1, -35.46) * mm, "mid": v(38.12, -35.47) * mm, "end": v(38.15, -35.48) * mm});
            skArc(sketch, "E4327", {"start": v(38.15, -35.48) * mm, "mid": v(38.45, -35.74) * mm, "end": v(38.75, -36) * mm});
            skArc(sketch, "E4328", {"start": v(38.75, -36) * mm, "mid": v(39.08, -36.3) * mm, "end": v(39.42, -36.6) * mm});
            skArc(sketch, "E4329", {"start": v(39.42, -36.6) * mm, "mid": v(39.8, -36.94) * mm, "end": v(40.2, -37.3) * mm});
            skArc(sketch, "E4330", {"start": v(40.2, -37.3) * mm, "mid": v(40.86, -37.87) * mm, "end": v(41.55, -38.43) * mm});
            skArc(sketch, "E4331", {"start": v(41.55, -38.43) * mm, "mid": v(42.22, -38.9) * mm, "end": v(42.91, -39.35) * mm});
            skArc(sketch, "E4332", {"start": v(42.91, -39.35) * mm, "mid": v(43.58, -39.73) * mm, "end": v(44.26, -40.07) * mm});
            skArc(sketch, "E4333", {"start": v(44.26, -40.07) * mm, "mid": v(44.92, -40.34) * mm, "end": v(45.6, -40.57) * mm});
            skArc(sketch, "E4334", {"start": v(45.6, -40.57) * mm, "mid": v(45.76, -40.61) * mm, "end": v(45.93, -40.64) * mm});
            skArc(sketch, "E4335", {"start": v(45.93, -40.64) * mm, "mid": v(46.02, -40.63) * mm, "end": v(46.1, -40.6) * mm});
            skArc(sketch, "E4336", {"start": v(46.1, -40.6) * mm, "mid": v(46.16, -40.52) * mm, "end": v(46.2, -40.43) * mm});
            skArc(sketch, "E4337", {"start": v(46.2, -40.43) * mm, "mid": v(46.21, -40.26) * mm, "end": v(46.22, -40.08) * mm});
            skArc(sketch, "E4338", {"start": v(46.22, -40.08) * mm, "mid": v(46.21, -39.9) * mm, "end": v(46.19, -39.74) * mm});
            skArc(sketch, "E4339", {"start": v(46.19, -39.74) * mm, "mid": v(46.15, -39.5) * mm, "end": v(46.1, -39.26) * mm});
            skArc(sketch, "E4340", {"start": v(46.1, -39.26) * mm, "mid": v(46.04, -39) * mm, "end": v(45.97, -38.75) * mm});
            skArc(sketch, "E4341", {"start": v(45.97, -38.75) * mm, "mid": v(45.9, -38.5) * mm, "end": v(45.81, -38.26) * mm});
            skArc(sketch, "E4342", {"start": v(45.81, -38.26) * mm, "mid": v(45.74, -38.04) * mm, "end": v(45.67, -37.81) * mm});
            skArc(sketch, "E4343", {"start": v(45.67, -37.81) * mm, "mid": v(45.63, -37.63) * mm, "end": v(45.6, -37.45) * mm});
            skArc(sketch, "E4344", {"start": v(45.6, -37.45) * mm, "mid": v(45.6, -37.32) * mm, "end": v(45.6, -37.2) * mm});
            skArc(sketch, "E4345", {"start": v(45.6, -37.2) * mm, "mid": v(45.63, -37.14) * mm, "end": v(45.68, -37.12) * mm});
            skArc(sketch, "E4346", {"start": v(45.68, -37.12) * mm, "mid": v(45.88, -37.15) * mm, "end": v(46.07, -37.22) * mm});
            skArc(sketch, "E4347", {"start": v(46.07, -37.22) * mm, "mid": v(46.55, -37.51) * mm, "end": v(47.03, -37.8) * mm});
            skArc(sketch, "E4348", {"start": v(47.03, -37.8) * mm, "mid": v(47.5, -38.1) * mm, "end": v(47.95, -38.42) * mm});
            skArc(sketch, "E4349", {"start": v(47.95, -38.42) * mm, "mid": v(48.14, -38.58) * mm, "end": v(48.28, -38.77) * mm});
            skArc(sketch, "E4350", {"start": v(48.28, -38.77) * mm, "mid": v(48.33, -38.83) * mm, "end": v(48.38, -38.88) * mm});
            skArc(sketch, "E4351", {"start": v(48.38, -38.88) * mm, "mid": v(48.46, -38.93) * mm, "end": v(48.54, -38.97) * mm});
            skArc(sketch, "E4352", {"start": v(48.54, -38.97) * mm, "mid": v(48.62, -39) * mm, "end": v(48.71, -39.03) * mm});
            skArc(sketch, "E4353", {"start": v(48.71, -39.03) * mm, "mid": v(48.8, -39.05) * mm, "end": v(48.89, -39.05) * mm});
            skArc(sketch, "E4354", {"start": v(48.89, -39.05) * mm, "mid": v(49.05, -39) * mm, "end": v(49.14, -38.85) * mm});
            skArc(sketch, "E4355", {"start": v(49.14, -38.85) * mm, "mid": v(49.17, -38.58) * mm, "end": v(49.14, -38.32) * mm});
            skArc(sketch, "E4356", {"start": v(49.14, -38.32) * mm, "mid": v(49, -37.84) * mm, "end": v(48.84, -37.37) * mm});
            skArc(sketch, "E4357", {"start": v(48.84, -37.37) * mm, "mid": v(48.52, -36.62) * mm, "end": v(48.18, -35.88) * mm});
            skArc(sketch, "E4358", {"start": v(48.18, -35.88) * mm, "mid": v(47.8, -35.15) * mm, "end": v(47.38, -34.47) * mm});
            skArc(sketch, "E4359", {"start": v(47.38, -34.47) * mm, "mid": v(46.8, -33.67) * mm, "end": v(46.2, -32.9) * mm});
            skArc(sketch, "E4360", {"start": v(46.2, -32.9) * mm, "mid": v(45.6, -32.2) * mm, "end": v(44.98, -31.53) * mm});
            skArc(sketch, "E4361", {"start": v(44.98, -31.53) * mm, "mid": v(44.74, -31.38) * mm, "end": v(44.45, -31.4) * mm});
            skArc(sketch, "E4362", {"start": v(44.45, -31.4) * mm, "mid": v(44.39, -31.43) * mm, "end": v(44.33, -31.48) * mm});
            skArc(sketch, "E4363", {"start": v(44.33, -31.48) * mm, "mid": v(44.27, -31.57) * mm, "end": v(44.22, -31.66) * mm});
            skArc(sketch, "E4364", {"start": v(44.22, -31.66) * mm, "mid": v(44.18, -31.78) * mm, "end": v(44.14, -31.9) * mm});
            skArc(sketch, "E4365", {"start": v(44.14, -31.9) * mm, "mid": v(44.12, -32.03) * mm, "end": v(44.1, -32.17) * mm});
            skArc(sketch, "E4366", {"start": v(44.1, -32.17) * mm, "mid": v(44.08, -32.59) * mm, "end": v(44.05, -33) * mm});
            skArc(sketch, "E4367", {"start": v(44.05, -33) * mm, "mid": v(44.03, -33.17) * mm, "end": v(43.97, -33.33) * mm});
            skArc(sketch, "E4368", {"start": v(43.97, -33.33) * mm, "mid": v(43.9, -33.41) * mm, "end": v(43.8, -33.46) * mm});
            skArc(sketch, "E4369", {"start": v(43.8, -33.46) * mm, "mid": v(43.67, -33.48) * mm, "end": v(43.52, -33.47) * mm});
            skArc(sketch, "E4370", {"start": v(43.52, -33.47) * mm, "mid": v(43.4, -33.47) * mm, "end": v(43.27, -33.51) * mm});
            skArc(sketch, "E4371", {"start": v(43.27, -33.51) * mm, "mid": v(43.17, -33.6) * mm, "end": v(43.1, -33.7) * mm});
            skArc(sketch, "E4372", {"start": v(43.1, -33.7) * mm, "mid": v(43.03, -33.9) * mm, "end": v(43, -34.12) * mm});
            skArc(sketch, "E4373", {"start": v(43, -34.12) * mm, "mid": v(42.94, -34.55) * mm, "end": v(42.9, -34.98) * mm});
            skArc(sketch, "E4374", {"start": v(42.9, -34.98) * mm, "mid": v(42.87, -35.29) * mm, "end": v(42.83, -35.6) * mm});
            skArc(sketch, "E4375", {"start": v(42.83, -35.6) * mm, "mid": v(42.78, -35.85) * mm, "end": v(42.72, -36.1) * mm});
            skArc(sketch, "E4376", {"start": v(42.72, -36.1) * mm, "mid": v(42.66, -36.3) * mm, "end": v(42.6, -36.5) * mm});
            skArc(sketch, "E4377", {"start": v(42.6, -36.5) * mm, "mid": v(42.55, -36.55) * mm, "end": v(42.48, -36.58) * mm});
            skArc(sketch, "E4378", {"start": v(42.48, -36.58) * mm, "mid": v(42.41, -36.55) * mm, "end": v(42.37, -36.5) * mm});
            skArc(sketch, "E4379", {"start": v(42.37, -36.5) * mm, "mid": v(42.3, -36.3) * mm, "end": v(42.25, -36.1) * mm});
            skArc(sketch, "E4380", {"start": v(42.25, -36.1) * mm, "mid": v(42.19, -35.85) * mm, "end": v(42.14, -35.6) * mm});
            skArc(sketch, "E4381", {"start": v(42.14, -35.6) * mm, "mid": v(42.1, -35.29) * mm, "end": v(42.07, -34.98) * mm});
            skArc(sketch, "E4382", {"start": v(42.07, -34.98) * mm, "mid": v(42.03, -34.54) * mm, "end": v(41.97, -34.1) * mm});
            skArc(sketch, "E4383", {"start": v(41.97, -34.1) * mm, "mid": v(41.93, -33.88) * mm, "end": v(41.86, -33.67) * mm});
            skArc(sketch, "E4384", {"start": v(41.86, -33.67) * mm, "mid": v(41.78, -33.55) * mm, "end": v(41.67, -33.46) * mm});
            skArc(sketch, "E4385", {"start": v(41.67, -33.46) * mm, "mid": v(41.53, -33.4) * mm, "end": v(41.38, -33.39) * mm});
            skArc(sketch, "E4386", {"start": v(41.38, -33.39) * mm, "mid": v(41.22, -33.36) * mm, "end": v(41.08, -33.28) * mm});
            skArc(sketch, "E4387", {"start": v(41.08, -33.28) * mm, "mid": v(40.97, -33.16) * mm, "end": v(40.9, -33) * mm});
            skArc(sketch, "E4388", {"start": v(40.9, -33) * mm, "mid": v(40.84, -32.72) * mm, "end": v(40.8, -32.42) * mm});
            skArc(sketch, "E4389", {"start": v(40.8, -32.42) * mm, "mid": v(40.77, -31.72) * mm, "end": v(40.75, -31) * mm});
            skLineSegment(sketch, "E4390", {"start": v(40.75, -31) * mm, "end": v(40.67, -28.62) * mm});
            skLineSegment(sketch, "E4391", {"start": v(40.67, -28.62) * mm, "end": v(39.02, -28.45) * mm});
            skArc(sketch, "E4392", {"start": v(39.02, -28.45) * mm, "mid": v(38.64, -28.42) * mm, "end": v(38.26, -28.4) * mm});
            skArc(sketch, "E4393", {"start": v(38.26, -28.4) * mm, "mid": v(37.8, -28.39) * mm, "end": v(37.35, -28.38) * mm});
            skArc(sketch, "E4394", {"start": v(37.35, -28.38) * mm, "mid": v(36.88, -28.39) * mm, "end": v(36.42, -28.4) * mm});
            skArc(sketch, "E4395", {"start": v(36.42, -28.4) * mm, "mid": v(36.03, -28.42) * mm, "end": v(35.64, -28.46) * mm});
            skArc(sketch, "E4396", {"start": v(35.64, -28.46) * mm, "mid": v(35, -28.52) * mm, "end": v(34.37, -28.56) * mm});
            skArc(sketch, "E4397", {"start": v(34.37, -28.56) * mm, "mid": v(34.23, -28.52) * mm, "end": v(34.17, -28.4) * mm});
            skArc(sketch, "E4398", {"start": v(34.17, -28.4) * mm, "mid": v(34.2, -28.22) * mm, "end": v(34.29, -28.06) * mm});
            skArc(sketch, "E4399", {"start": v(34.29, -28.06) * mm, "mid": v(34.9, -27.37) * mm, "end": v(35.53, -26.7) * mm});
            skArc(sketch, "E4400", {"start": v(35.53, -26.7) * mm, "mid": v(35.78, -26.41) * mm, "end": v(36.03, -26.13) * mm});
            skArc(sketch, "E4401", {"start": v(36.03, -26.13) * mm, "mid": v(36.1, -26.02) * mm, "end": v(36.15, -25.9) * mm});
            skArc(sketch, "E4402", {"start": v(36.15, -25.9) * mm, "mid": v(36.15, -25.81) * mm, "end": v(36.1, -25.74) * mm});
            skArc(sketch, "E4403", {"start": v(36.1, -25.74) * mm, "mid": v(35.97, -25.65) * mm, "end": v(35.82, -25.58) * mm});
            skArc(sketch, "E4404", {"start": v(35.82, -25.58) * mm, "mid": v(35.4, -25.46) * mm, "end": v(34.97, -25.41) * mm});
            skArc(sketch, "E4405", {"start": v(34.97, -25.41) * mm, "mid": v(33.42, -25.4) * mm, "end": v(31.87, -25.38) * mm});
            skArc(sketch, "E4406", {"start": v(31.87, -25.38) * mm, "mid": v(30.32, -25.39) * mm, "end": v(28.78, -25.4) * mm});
            skArc(sketch, "E4407", {"start": v(28.78, -25.4) * mm, "mid": v(28.33, -25.45) * mm, "end": v(27.9, -25.58) * mm});
            skArc(sketch, "E4408", {"start": v(27.9, -25.58) * mm, "mid": v(27.75, -25.66) * mm, "end": v(27.65, -25.8) * mm});
            skArc(sketch, "E4409", {"start": v(27.65, -25.8) * mm, "mid": v(27.56, -25.98) * mm, "end": v(27.5, -26.18) * mm});
            skArc(sketch, "E4410", {"start": v(27.5, -26.18) * mm, "mid": v(27.45, -26.53) * mm, "end": v(27.43, -26.88) * mm});
            skArc(sketch, "E4411", {"start": v(27.43, -26.88) * mm, "mid": v(27.42, -27.57) * mm, "end": v(27.41, -28.26) * mm});
            skArc(sketch, "E4412", {"start": v(27.41, -28.26) * mm, "mid": v(27.41, -29.02) * mm, "end": v(27.4, -29.78) * mm});
            skArc(sketch, "E4413", {"start": v(27.4, -29.78) * mm, "mid": v(27.38, -30.08) * mm, "end": v(27.33, -30.38) * mm});
            skArc(sketch, "E4414", {"start": v(27.33, -30.38) * mm, "mid": v(27.27, -30.53) * mm, "end": v(27.16, -30.65) * mm});
            skArc(sketch, "E4415", {"start": v(27.16, -30.65) * mm, "mid": v(27.02, -30.73) * mm, "end": v(26.86, -30.76) * mm});
            skArc(sketch, "E4416", {"start": v(26.86, -30.76) * mm, "mid": v(26.71, -30.78) * mm, "end": v(26.57, -30.83) * mm});
            skArc(sketch, "E4417", {"start": v(26.57, -30.83) * mm, "mid": v(26.47, -30.9) * mm, "end": v(26.4, -31.02) * mm});
            skArc(sketch, "E4418", {"start": v(26.4, -31.02) * mm, "mid": v(26.36, -31.2) * mm, "end": v(26.34, -31.4) * mm});
            skArc(sketch, "E4419", {"start": v(26.34, -31.4) * mm, "mid": v(26.34, -31.85) * mm, "end": v(26.35, -32.3) * mm});
            skArc(sketch, "E4420", {"start": v(26.35, -32.3) * mm, "mid": v(26.35, -32.82) * mm, "end": v(26.35, -33.35) * mm});
            skArc(sketch, "E4421", {"start": v(26.35, -33.35) * mm, "mid": v(26.32, -33.6) * mm, "end": v(26.25, -33.84) * mm});
            skArc(sketch, "E4422", {"start": v(26.25, -33.84) * mm, "mid": v(26.18, -33.95) * mm, "end": v(26.05, -34) * mm});
            skArc(sketch, "E4423", {"start": v(26.05, -34) * mm, "mid": v(25.9, -34) * mm, "end": v(25.74, -33.93) * mm});
            skArc(sketch, "E4424", {"start": v(25.74, -33.93) * mm, "mid": v(25.66, -33.86) * mm, "end": v(25.6, -33.76) * mm});
            skArc(sketch, "E4425", {"start": v(25.6, -33.76) * mm, "mid": v(25.56, -33.58) * mm, "end": v(25.53, -33.4) * mm});
            skArc(sketch, "E4426", {"start": v(25.53, -33.4) * mm, "mid": v(25.51, -33.15) * mm, "end": v(25.5, -32.9) * mm});
            skArc(sketch, "E4427", {"start": v(25.5, -32.9) * mm, "mid": v(25.52, -32.57) * mm, "end": v(25.54, -32.24) * mm});
            skArc(sketch, "E4428", {"start": v(25.54, -32.24) * mm, "mid": v(25.57, -31.78) * mm, "end": v(25.6, -31.32) * mm});
            skArc(sketch, "E4429", {"start": v(25.6, -31.32) * mm, "mid": v(25.6, -31.15) * mm, "end": v(25.55, -30.97) * mm});
            skArc(sketch, "E4430", {"start": v(25.55, -30.97) * mm, "mid": v(25.49, -30.87) * mm, "end": v(25.38, -30.81) * mm});
            skArc(sketch, "E4431", {"start": v(25.38, -30.81) * mm, "mid": v(25.2, -30.77) * mm, "end": v(25.02, -30.76) * mm});
            skArc(sketch, "E4432", {"start": v(25.02, -30.76) * mm, "mid": v(24.83, -30.74) * mm, "end": v(24.65, -30.68) * mm});
            skArc(sketch, "E4433", {"start": v(24.65, -30.68) * mm, "mid": v(24.53, -30.59) * mm, "end": v(24.46, -30.45) * mm});
            skArc(sketch, "E4434", {"start": v(24.46, -30.45) * mm, "mid": v(24.4, -30.2) * mm, "end": v(24.39, -29.96) * mm});
            skArc(sketch, "E4435", {"start": v(24.39, -29.96) * mm, "mid": v(24.38, -29.25) * mm, "end": v(24.37, -28.55) * mm});
            skArc(sketch, "E4436", {"start": v(24.37, -28.55) * mm, "mid": v(24.37, -27.77) * mm, "end": v(24.34, -26.99) * mm});
            skArc(sketch, "E4437", {"start": v(24.34, -26.99) * mm, "mid": v(24.29, -26.72) * mm, "end": v(24.16, -26.48) * mm});
            skArc(sketch, "E4438", {"start": v(24.16, -26.48) * mm, "mid": v(23.98, -26.35) * mm, "end": v(23.77, -26.34) * mm});
            skArc(sketch, "E4439", {"start": v(23.77, -26.34) * mm, "mid": v(23.31, -26.46) * mm, "end": v(22.87, -26.6) * mm});
            skArc(sketch, "E4440", {"start": v(22.87, -26.6) * mm, "mid": v(22.63, -26.67) * mm, "end": v(22.38, -26.67) * mm});
            skArc(sketch, "E4441", {"start": v(22.38, -26.67) * mm, "mid": v(22.23, -26.6) * mm, "end": v(22.16, -26.44) * mm});
            skArc(sketch, "E4442", {"start": v(22.16, -26.44) * mm, "mid": v(22.17, -26.15) * mm, "end": v(22.24, -25.86) * mm});
            skArc(sketch, "E4443", {"start": v(22.24, -25.86) * mm, "mid": v(22.46, -25.3) * mm, "end": v(22.7, -24.75) * mm});
            skArc(sketch, "E4444", {"start": v(22.7, -24.75) * mm, "mid": v(22.8, -24.52) * mm, "end": v(22.89, -24.3) * mm});
            skArc(sketch, "E4445", {"start": v(22.89, -24.3) * mm, "mid": v(22.96, -24.09) * mm, "end": v(23, -23.88) * mm});
            skArc(sketch, "E4446", {"start": v(23, -23.88) * mm, "mid": v(23.04, -23.72) * mm, "end": v(23.06, -23.56) * mm});
            skArc(sketch, "E4447", {"start": v(23.06, -23.56) * mm, "mid": v(23.04, -23.49) * mm, "end": v(23, -23.43) * mm});
            skArc(sketch, "E4448", {"start": v(23, -23.43) * mm, "mid": v(22.92, -23.4) * mm, "end": v(22.83, -23.38) * mm});
            skArc(sketch, "E4449", {"start": v(22.83, -23.38) * mm, "mid": v(22.66, -23.38) * mm, "end": v(22.49, -23.38) * mm});
            skArc(sketch, "E4450", {"start": v(22.49, -23.38) * mm, "mid": v(22.28, -23.39) * mm, "end": v(22.07, -23.4) * mm});
            skArc(sketch, "E4451", {"start": v(22.07, -23.4) * mm, "mid": v(21.85, -23.43) * mm, "end": v(21.63, -23.46) * mm});
            skArc(sketch, "E4452", {"start": v(21.63, -23.46) * mm, "mid": v(21.36, -23.51) * mm, "end": v(21.1, -23.57) * mm});
            skArc(sketch, "E4453", {"start": v(21.1, -23.57) * mm, "mid": v(20.92, -23.63) * mm, "end": v(20.76, -23.71) * mm});
            skArc(sketch, "E4454", {"start": v(20.76, -23.71) * mm, "mid": v(20.65, -23.8) * mm, "end": v(20.57, -23.9) * mm});
            skArc(sketch, "E4455", {"start": v(20.57, -23.9) * mm, "mid": v(20.52, -24) * mm, "end": v(20.5, -24.13) * mm});
            skArc(sketch, "E4456", {"start": v(20.5, -24.13) * mm, "mid": v(20.5, -24.23) * mm, "end": v(20.46, -24.32) * mm});
            skArc(sketch, "E4457", {"start": v(20.46, -24.32) * mm, "mid": v(20.4, -24.42) * mm, "end": v(20.33, -24.51) * mm});
            skArc(sketch, "E4458", {"start": v(20.33, -24.51) * mm, "mid": v(20.25, -24.6) * mm, "end": v(20.15, -24.67) * mm});
            skArc(sketch, "E4459", {"start": v(20.15, -24.67) * mm, "mid": v(20.05, -24.72) * mm, "end": v(19.93, -24.76) * mm});
            skArc(sketch, "E4460", {"start": v(19.93, -24.76) * mm, "mid": v(19.78, -24.81) * mm, "end": v(19.64, -24.88) * mm});
            skArc(sketch, "E4461", {"start": v(19.64, -24.88) * mm, "mid": v(19.56, -24.96) * mm, "end": v(19.5, -25.06) * mm});
            skArc(sketch, "E4462", {"start": v(19.5, -25.06) * mm, "mid": v(19.47, -25.2) * mm, "end": v(19.47, -25.34) * mm});
            skArc(sketch, "E4463", {"start": v(19.47, -25.34) * mm, "mid": v(19.5, -25.6) * mm, "end": v(19.54, -25.86) * mm});
            skArc(sketch, "E4464", {"start": v(19.54, -25.86) * mm, "mid": v(19.58, -26.12) * mm, "end": v(19.6, -26.37) * mm});
            skArc(sketch, "E4465", {"start": v(19.6, -26.37) * mm, "mid": v(19.58, -26.61) * mm, "end": v(19.55, -26.86) * mm});
            skArc(sketch, "E4466", {"start": v(19.55, -26.86) * mm, "mid": v(19.49, -27.11) * mm, "end": v(19.4, -27.36) * mm});
            skArc(sketch, "E4467", {"start": v(19.4, -27.36) * mm, "mid": v(19.28, -27.66) * mm, "end": v(19.15, -27.94) * mm});
            skArc(sketch, "E4468", {"start": v(19.15, -27.94) * mm, "mid": v(18.97, -28.33) * mm, "end": v(18.82, -28.73) * mm});
            skArc(sketch, "E4469", {"start": v(18.82, -28.73) * mm, "mid": v(18.75, -29.04) * mm, "end": v(18.74, -29.37) * mm});
            skArc(sketch, "E4470", {"start": v(18.74, -29.37) * mm, "mid": v(18.79, -29.58) * mm, "end": v(18.9, -29.77) * mm});
            skArc(sketch, "E4471", {"start": v(18.9, -29.77) * mm, "mid": v(19.07, -29.89) * mm, "end": v(19.26, -29.93) * mm});
            skArc(sketch, "E4472", {"start": v(19.26, -29.93) * mm, "mid": v(19.53, -29.98) * mm, "end": v(19.76, -30.13) * mm});
            skArc(sketch, "E4473", {"start": v(19.76, -30.13) * mm, "mid": v(20.08, -30.48) * mm, "end": v(20.38, -30.85) * mm});
            skArc(sketch, "E4474", {"start": v(20.38, -30.85) * mm, "mid": v(20.65, -31.26) * mm, "end": v(20.9, -31.7) * mm});
            skArc(sketch, "E4475", {"start": v(20.9, -31.7) * mm, "mid": v(21.01, -32.02) * mm, "end": v(21.05, -32.37) * mm});
            skLineSegment(sketch, "E4476", {"start": v(21.05, -32.37) * mm, "end": v(21.04, -33.11) * mm});
            skLineSegment(sketch, "E4477", {"start": v(21.04, -33.11) * mm, "end": v(20.22, -32.21) * mm});
            skArc(sketch, "E4478", {"start": v(20.22, -32.21) * mm, "mid": v(19.92, -31.9) * mm, "end": v(19.6, -31.62) * mm});
            skArc(sketch, "E4479", {"start": v(19.6, -31.62) * mm, "mid": v(19.37, -31.46) * mm, "end": v(19.1, -31.36) * mm});
            skArc(sketch, "E4480", {"start": v(19.1, -31.36) * mm, "mid": v(18.9, -31.35) * mm, "end": v(18.73, -31.42) * mm});
            skArc(sketch, "E4481", {"start": v(18.73, -31.42) * mm, "mid": v(18.57, -31.56) * mm, "end": v(18.46, -31.75) * mm});
            skArc(sketch, "E4482", {"start": v(18.46, -31.75) * mm, "mid": v(18.38, -31.98) * mm, "end": v(18.32, -32.22) * mm});
            skArc(sketch, "E4483", {"start": v(18.32, -32.22) * mm, "mid": v(18.31, -32.4) * mm, "end": v(18.34, -32.55) * mm});
            skArc(sketch, "E4484", {"start": v(18.34, -32.55) * mm, "mid": v(18.42, -32.72) * mm, "end": v(18.53, -32.87) * mm});
            skArc(sketch, "E4485", {"start": v(18.53, -32.87) * mm, "mid": v(18.75, -33.1) * mm, "end": v(18.98, -33.3) * mm});
            skArc(sketch, "E4486", {"start": v(18.98, -33.3) * mm, "mid": v(19.23, -33.54) * mm, "end": v(19.44, -33.8) * mm});
            skArc(sketch, "E4487", {"start": v(19.44, -33.8) * mm, "mid": v(19.57, -34.05) * mm, "end": v(19.65, -34.32) * mm});
            skArc(sketch, "E4488", {"start": v(19.65, -34.32) * mm, "mid": v(19.64, -34.53) * mm, "end": v(19.57, -34.73) * mm});
            skArc(sketch, "E4489", {"start": v(19.57, -34.73) * mm, "mid": v(19.44, -34.9) * mm, "end": v(19.26, -35) * mm});
            skArc(sketch, "E4490", {"start": v(19.26, -35) * mm, "mid": v(19.17, -35.03) * mm, "end": v(19.07, -35.04) * mm});
            skArc(sketch, "E4491", {"start": v(19.07, -35.04) * mm, "mid": v(19, -35.03) * mm, "end": v(18.94, -35) * mm});
            skArc(sketch, "E4492", {"start": v(18.94, -35) * mm, "mid": v(18.9, -34.93) * mm, "end": v(18.87, -34.86) * mm});
            skArc(sketch, "E4493", {"start": v(18.87, -34.86) * mm, "mid": v(18.85, -34.74) * mm, "end": v(18.84, -34.62) * mm});
            skArc(sketch, "E4494", {"start": v(18.84, -34.62) * mm, "mid": v(18.83, -34.5) * mm, "end": v(18.8, -34.39) * mm});
            skArc(sketch, "E4495", {"start": v(18.8, -34.39) * mm, "mid": v(18.77, -34.3) * mm, "end": v(18.7, -34.22) * mm});
            skArc(sketch, "E4496", {"start": v(18.7, -34.22) * mm, "mid": v(18.62, -34.15) * mm, "end": v(18.53, -34.11) * mm});
            skArc(sketch, "E4497", {"start": v(18.53, -34.11) * mm, "mid": v(18.41, -34.09) * mm, "end": v(18.3, -34.08) * mm});
            skArc(sketch, "E4498", {"start": v(18.3, -34.08) * mm, "mid": v(18.18, -34.08) * mm, "end": v(18.08, -34.1) * mm});
            skArc(sketch, "E4499", {"start": v(18.08, -34.1) * mm, "mid": v(17.99, -34.12) * mm, "end": v(17.9, -34.16) * mm});
            skArc(sketch, "E4500", {"start": v(17.9, -34.16) * mm, "mid": v(17.84, -34.2) * mm, "end": v(17.78, -34.25) * mm});
            skArc(sketch, "E4501", {"start": v(17.78, -34.25) * mm, "mid": v(17.75, -34.3) * mm, "end": v(17.74, -34.35) * mm});
            skArc(sketch, "E4502", {"start": v(17.74, -34.35) * mm, "mid": v(17.73, -34.54) * mm, "end": v(17.72, -34.73) * mm});
            skArc(sketch, "E4503", {"start": v(17.72, -34.73) * mm, "mid": v(17.7, -34.86) * mm, "end": v(17.66, -34.98) * mm});
            skArc(sketch, "E4504", {"start": v(17.66, -34.98) * mm, "mid": v(17.6, -35.1) * mm, "end": v(17.53, -35.21) * mm});
            skArc(sketch, "E4505", {"start": v(17.53, -35.21) * mm, "mid": v(17.4, -35.37) * mm, "end": v(17.26, -35.53) * mm});
            skArc(sketch, "E4506", {"start": v(17.26, -35.53) * mm, "mid": v(17.05, -35.74) * mm, "end": v(16.83, -35.93) * mm});
            skArc(sketch, "E4507", {"start": v(16.83, -35.93) * mm, "mid": v(16.7, -36) * mm, "end": v(16.55, -35.98) * mm});
            skArc(sketch, "E4508", {"start": v(16.55, -35.98) * mm, "mid": v(16.44, -35.9) * mm, "end": v(16.4, -35.78) * mm});
            skArc(sketch, "E4509", {"start": v(16.4, -35.78) * mm, "mid": v(16.4, -35.52) * mm, "end": v(16.43, -35.26) * mm});
            skArc(sketch, "E4510", {"start": v(16.43, -35.26) * mm, "mid": v(16.46, -35.09) * mm, "end": v(16.46, -34.92) * mm});
            skArc(sketch, "E4511", {"start": v(16.46, -34.92) * mm, "mid": v(16.45, -34.72) * mm, "end": v(16.43, -34.52) * mm});
            skArc(sketch, "E4512", {"start": v(16.43, -34.52) * mm, "mid": v(16.4, -34.32) * mm, "end": v(16.35, -34.13) * mm});
            skArc(sketch, "E4513", {"start": v(16.35, -34.13) * mm, "mid": v(16.29, -33.96) * mm, "end": v(16.22, -33.8) * mm});
            skArc(sketch, "E4514", {"start": v(16.22, -33.8) * mm, "mid": v(16.13, -33.62) * mm, "end": v(16.06, -33.44) * mm});
            skArc(sketch, "E4515", {"start": v(16.06, -33.44) * mm, "mid": v(15.98, -33.17) * mm, "end": v(15.9, -32.9) * mm});
            skArc(sketch, "E4516", {"start": v(15.9, -32.9) * mm, "mid": v(15.83, -32.6) * mm, "end": v(15.76, -32.3) * mm});
            skArc(sketch, "E4517", {"start": v(15.76, -32.3) * mm, "mid": v(15.7, -32.01) * mm, "end": v(15.66, -31.72) * mm});
            skArc(sketch, "E4518", {"start": v(15.66, -31.72) * mm, "mid": v(15.57, -31.19) * mm, "end": v(15.44, -30.66) * mm});
            skArc(sketch, "E4519", {"start": v(15.44, -30.66) * mm, "mid": v(15.3, -30.23) * mm, "end": v(15.1, -29.82) * mm});
            skArc(sketch, "E4520", {"start": v(15.1, -29.82) * mm, "mid": v(14.93, -29.54) * mm, "end": v(14.7, -29.28) * mm});
            skArc(sketch, "E4521", {"start": v(14.7, -29.28) * mm, "mid": v(14.5, -29.15) * mm, "end": v(14.27, -29.1) * mm});
            skArc(sketch, "E4522", {"start": v(14.27, -29.1) * mm, "mid": v(14.05, -29.15) * mm, "end": v(13.87, -29.29) * mm});
            skArc(sketch, "E4523", {"start": v(13.87, -29.29) * mm, "mid": v(13.72, -29.53) * mm, "end": v(13.62, -29.8) * mm});
            skArc(sketch, "E4524", {"start": v(13.62, -29.8) * mm, "mid": v(13.55, -30.2) * mm, "end": v(13.54, -30.6) * mm});
            skArc(sketch, "E4525", {"start": v(13.54, -30.6) * mm, "mid": v(13.58, -31.09) * mm, "end": v(13.65, -31.57) * mm});
            skArc(sketch, "E4526", {"start": v(13.65, -31.57) * mm, "mid": v(13.93, -33.07) * mm, "end": v(14.16, -34.58) * mm});
            skArc(sketch, "E4527", {"start": v(14.16, -34.58) * mm, "mid": v(14.24, -35.51) * mm, "end": v(14.2, -36.46) * mm});
            skArc(sketch, "E4528", {"start": v(14.2, -36.46) * mm, "mid": v(14.09, -37.14) * mm, "end": v(13.85, -37.8) * mm});
            skArc(sketch, "E4529", {"start": v(13.85, -37.8) * mm, "mid": v(13.5, -38.4) * mm, "end": v(13.04, -38.91) * mm});
            skArc(sketch, "E4530", {"start": v(13.04, -38.91) * mm, "mid": v(12.55, -39.3) * mm, "end": v(12, -39.57) * mm});
            skArc(sketch, "E4531", {"start": v(12, -39.57) * mm, "mid": v(11.36, -39.77) * mm, "end": v(10.7, -39.86) * mm});
            skArc(sketch, "E4532", {"start": v(10.7, -39.86) * mm, "mid": v(10.06, -39.84) * mm, "end": v(9.43, -39.72) * mm});
            skArc(sketch, "E4533", {"start": v(9.43, -39.72) * mm, "mid": v(8.93, -39.5) * mm, "end": v(8.5, -39.17) * mm});
            skArc(sketch, "E4534", {"start": v(8.5, -39.17) * mm, "mid": v(8.26, -38.86) * mm, "end": v(8.14, -38.49) * mm});
            skArc(sketch, "E4535", {"start": v(8.14, -38.49) * mm, "mid": v(8.07, -37.87) * mm, "end": v(8.05, -37.25) * mm});
            skArc(sketch, "E4536", {"start": v(8.05, -37.25) * mm, "mid": v(8.08, -36.62) * mm, "end": v(8.16, -36) * mm});
            skArc(sketch, "E4537", {"start": v(8.16, -36) * mm, "mid": v(8.29, -35.63) * mm, "end": v(8.52, -35.31) * mm});
            skArc(sketch, "E4538", {"start": v(8.52, -35.31) * mm, "mid": v(8.75, -35.02) * mm, "end": v(8.88, -34.68) * mm});
            skArc(sketch, "E4539", {"start": v(8.88, -34.68) * mm, "mid": v(9.16, -33.56) * mm, "end": v(9.42, -32.43) * mm});
            skArc(sketch, "E4540", {"start": v(9.42, -32.43) * mm, "mid": v(9.66, -31.28) * mm, "end": v(9.88, -30.12) * mm});
            skArc(sketch, "E4541", {"start": v(9.88, -30.12) * mm, "mid": v(10, -29.23) * mm, "end": v(10.09, -28.33) * mm});
            skArc(sketch, "E4542", {"start": v(10.09, -28.33) * mm, "mid": v(10.1, -28.14) * mm, "end": v(10.13, -27.96) * mm});
            skArc(sketch, "E4543", {"start": v(10.13, -27.96) * mm, "mid": v(10.18, -27.79) * mm, "end": v(10.23, -27.62) * mm});
            skArc(sketch, "E4544", {"start": v(10.23, -27.62) * mm, "mid": v(10.3, -27.48) * mm, "end": v(10.36, -27.34) * mm});
            skArc(sketch, "E4545", {"start": v(10.36, -27.34) * mm, "mid": v(10.42, -27.26) * mm, "end": v(10.5, -27.2) * mm});
            skArc(sketch, "E4546", {"start": v(10.5, -27.2) * mm, "mid": v(10.58, -27.13) * mm, "end": v(10.64, -27.05) * mm});
            skArc(sketch, "E4547", {"start": v(10.64, -27.05) * mm, "mid": v(10.7, -26.93) * mm, "end": v(10.74, -26.8) * mm});
            skArc(sketch, "E4548", {"start": v(10.74, -26.8) * mm, "mid": v(10.77, -26.65) * mm, "end": v(10.79, -26.5) * mm});
            skArc(sketch, "E4549", {"start": v(10.79, -26.5) * mm, "mid": v(10.79, -26.33) * mm, "end": v(10.78, -26.17) * mm});
            skArc(sketch, "E4550", {"start": v(10.78, -26.17) * mm, "mid": v(10.74, -25.93) * mm, "end": v(10.68, -25.7) * mm});
            skArc(sketch, "E4551", {"start": v(10.68, -25.7) * mm, "mid": v(10.62, -25.57) * mm, "end": v(10.51, -25.49) * mm});
            skArc(sketch, "E4552", {"start": v(10.51, -25.49) * mm, "mid": v(10.35, -25.43) * mm, "end": v(10.18, -25.42) * mm});
            skArc(sketch, "E4553", {"start": v(10.18, -25.42) * mm, "mid": v(9.74, -25.43) * mm, "end": v(9.3, -25.45) * mm});
            skArc(sketch, "E4554", {"start": v(9.3, -25.45) * mm, "mid": v(9, -25.47) * mm, "end": v(8.7, -25.5) * mm});
            skArc(sketch, "E4555", {"start": v(8.7, -25.5) * mm, "mid": v(8.36, -25.55) * mm, "end": v(8.01, -25.6) * mm});
            skArc(sketch, "E4556", {"start": v(8.01, -25.6) * mm, "mid": v(7.69, -25.64) * mm, "end": v(7.36, -25.7) * mm});
            skArc(sketch, "E4557", {"start": v(7.36, -25.7) * mm, "mid": v(7.1, -25.75) * mm, "end": v(6.86, -25.82) * mm});
            skArc(sketch, "E4558", {"start": v(6.86, -25.82) * mm, "mid": v(6.43, -25.92) * mm, "end": v(6, -26) * mm});
            skArc(sketch, "E4559", {"start": v(6, -26) * mm, "mid": v(5.82, -26) * mm, "end": v(5.68, -25.9) * mm});
            skArc(sketch, "E4560", {"start": v(5.68, -25.9) * mm, "mid": v(5.6, -25.78) * mm, "end": v(5.63, -25.63) * mm});
            skArc(sketch, "E4561", {"start": v(5.63, -25.63) * mm, "mid": v(5.82, -25.32) * mm, "end": v(6.03, -25.02) * mm});
            skArc(sketch, "E4562", {"start": v(6.03, -25.02) * mm, "mid": v(6.33, -24.65) * mm, "end": v(6.67, -24.31) * mm});
            skArc(sketch, "E4563", {"start": v(6.67, -24.31) * mm, "mid": v(7.1, -23.96) * mm, "end": v(7.53, -23.63) * mm});
            skArc(sketch, "E4564", {"start": v(7.53, -23.63) * mm, "mid": v(7.98, -23.35) * mm, "end": v(8.45, -23.1) * mm});
            skArc(sketch, "E4565", {"start": v(8.45, -23.1) * mm, "mid": v(8.83, -22.93) * mm, "end": v(9.24, -22.82) * mm});
            skArc(sketch, "E4566", {"start": v(9.24, -22.82) * mm, "mid": v(9.59, -22.74) * mm, "end": v(9.92, -22.61) * mm});
            skArc(sketch, "E4567", {"start": v(9.92, -22.61) * mm, "mid": v(10.08, -22.5) * mm, "end": v(10.16, -22.31) * mm});
            skArc(sketch, "E4568", {"start": v(10.16, -22.31) * mm, "mid": v(10.15, -22.1) * mm, "end": v(10.05, -21.9) * mm});
            skArc(sketch, "E4569", {"start": v(10.05, -21.9) * mm, "mid": v(9.78, -21.6) * mm, "end": v(9.5, -21.33) * mm});
            skArc(sketch, "E4570", {"start": v(9.5, -21.33) * mm, "mid": v(9.33, -21.18) * mm, "end": v(9.18, -21.02) * mm});
            skArc(sketch, "E4571", {"start": v(9.18, -21.02) * mm, "mid": v(9.05, -20.89) * mm, "end": v(8.94, -20.74) * mm});
            skArc(sketch, "E4572", {"start": v(8.94, -20.74) * mm, "mid": v(8.87, -20.64) * mm, "end": v(8.8, -20.52) * mm});
            skArc(sketch, "E4573", {"start": v(8.8, -20.52) * mm, "mid": v(8.8, -20.47) * mm, "end": v(8.83, -20.43) * mm});
            skArc(sketch, "E4574", {"start": v(8.83, -20.43) * mm, "mid": v(9.16, -20.27) * mm, "end": v(9.52, -20.2) * mm});
            skArc(sketch, "E4575", {"start": v(9.52, -20.2) * mm, "mid": v(10.25, -20.15) * mm, "end": v(10.97, -20.12) * mm});
            skArc(sketch, "E4576", {"start": v(10.97, -20.12) * mm, "mid": v(11.75, -20.12) * mm, "end": v(12.52, -20.16) * mm});
            skArc(sketch, "E4577", {"start": v(12.52, -20.16) * mm, "mid": v(13.17, -20.23) * mm, "end": v(13.8, -20.34) * mm});
            skArc(sketch, "E4578", {"start": v(13.8, -20.34) * mm, "mid": v(14.15, -20.4) * mm, "end": v(14.48, -20.47) * mm});
            skArc(sketch, "E4579", {"start": v(14.48, -20.47) * mm, "mid": v(14.78, -20.51) * mm, "end": v(15.07, -20.55) * mm});
            skArc(sketch, "E4580", {"start": v(15.07, -20.55) * mm, "mid": v(15.31, -20.56) * mm, "end": v(15.55, -20.58) * mm});
            skArc(sketch, "E4581", {"start": v(15.55, -20.58) * mm, "mid": v(15.62, -20.56) * mm, "end": v(15.68, -20.5) * mm});
            skArc(sketch, "E4582", {"start": v(15.68, -20.5) * mm, "mid": v(15.73, -20.37) * mm, "end": v(15.73, -20.23) * mm});
            skArc(sketch, "E4583", {"start": v(15.73, -20.23) * mm, "mid": v(15.68, -20) * mm, "end": v(15.6, -19.77) * mm});
            skArc(sketch, "E4584", {"start": v(15.6, -19.77) * mm, "mid": v(15.5, -19.51) * mm, "end": v(15.36, -19.26) * mm});
            skArc(sketch, "E4585", {"start": v(15.36, -19.26) * mm, "mid": v(15.2, -19.03) * mm, "end": v(15.03, -18.8) * mm});
            skArc(sketch, "E4586", {"start": v(15.03, -18.8) * mm, "mid": v(14.93, -18.67) * mm, "end": v(14.86, -18.53) * mm});
            skArc(sketch, "E4587", {"start": v(14.86, -18.53) * mm, "mid": v(14.86, -18.45) * mm, "end": v(14.92, -18.39) * mm});
            skArc(sketch, "E4588", {"start": v(14.92, -18.39) * mm, "mid": v(15.08, -18.34) * mm, "end": v(15.25, -18.33) * mm});
            skArc(sketch, "E4589", {"start": v(15.25, -18.33) * mm, "mid": v(15.78, -18.32) * mm, "end": v(16.3, -18.32) * mm});
            skArc(sketch, "E4590", {"start": v(16.3, -18.32) * mm, "mid": v(16.7, -18.33) * mm, "end": v(17.1, -18.35) * mm});
            skArc(sketch, "E4591", {"start": v(17.1, -18.35) * mm, "mid": v(17.52, -18.4) * mm, "end": v(17.94, -18.47) * mm});
            skArc(sketch, "E4592", {"start": v(17.94, -18.47) * mm, "mid": v(18.35, -18.55) * mm, "end": v(18.75, -18.64) * mm});
            skArc(sketch, "E4593", {"start": v(18.75, -18.64) * mm, "mid": v(19.11, -18.75) * mm, "end": v(19.46, -18.87) * mm});
            skArc(sketch, "E4594", {"start": v(19.46, -18.87) * mm, "mid": v(19.74, -18.98) * mm, "end": v(20.03, -19.08) * mm});
            skArc(sketch, "E4595", {"start": v(20.03, -19.08) * mm, "mid": v(20.27, -19.17) * mm, "end": v(20.51, -19.26) * mm});
            skArc(sketch, "E4596", {"start": v(20.51, -19.26) * mm, "mid": v(20.72, -19.34) * mm, "end": v(20.93, -19.41) * mm});
            skArc(sketch, "E4597", {"start": v(20.93, -19.41) * mm, "mid": v(20.96, -19.42) * mm, "end": v(20.99, -19.42) * mm});
            skArc(sketch, "E4598", {"start": v(20.99, -19.42) * mm, "mid": v(21.07, -19.39) * mm, "end": v(21.1, -19.3) * mm});
            skArc(sketch, "E4599", {"start": v(21.1, -19.3) * mm, "mid": v(21.05, -19.1) * mm, "end": v(20.99, -18.92) * mm});
            skArc(sketch, "E4600", {"start": v(20.99, -18.92) * mm, "mid": v(20.86, -18.65) * mm, "end": v(20.72, -18.4) * mm});
            skArc(sketch, "E4601", {"start": v(20.72, -18.4) * mm, "mid": v(20.52, -18.1) * mm, "end": v(20.32, -17.82) * mm});
            skLineSegment(sketch, "E4602", {"start": v(20.32, -17.82) * mm, "end": v(19.58, -16.85) * mm});
            skLineSegment(sketch, "E4603", {"start": v(19.58, -16.85) * mm, "end": v(21.21, -17.04) * mm});
            skArc(sketch, "E4604", {"start": v(21.21, -17.04) * mm, "mid": v(21.58, -17.1) * mm, "end": v(21.95, -17.16) * mm});
            skArc(sketch, "E4605", {"start": v(21.95, -17.16) * mm, "mid": v(22.38, -17.26) * mm, "end": v(22.8, -17.38) * mm});
            skArc(sketch, "E4606", {"start": v(22.8, -17.38) * mm, "mid": v(23.23, -17.5) * mm, "end": v(23.66, -17.64) * mm});
            skArc(sketch, "E4607", {"start": v(23.66, -17.64) * mm, "mid": v(24, -17.77) * mm, "end": v(24.35, -17.92) * mm});
            skArc(sketch, "E4608", {"start": v(24.35, -17.92) * mm, "mid": v(24.64, -18.05) * mm, "end": v(24.94, -18.17) * mm});
            skArc(sketch, "E4609", {"start": v(24.94, -18.17) * mm, "mid": v(25.2, -18.26) * mm, "end": v(25.48, -18.34) * mm});
            skArc(sketch, "E4610", {"start": v(25.48, -18.34) * mm, "mid": v(25.7, -18.4) * mm, "end": v(25.9, -18.44) * mm});
            skArc(sketch, "E4611", {"start": v(25.9, -18.44) * mm, "mid": v(26, -18.43) * mm, "end": v(26.07, -18.39) * mm});
            skArc(sketch, "E4612", {"start": v(26.07, -18.39) * mm, "mid": v(26.16, -18.22) * mm, "end": v(26.15, -18.04) * mm});
            skArc(sketch, "E4613", {"start": v(26.15, -18.04) * mm, "mid": v(25.9, -17.41) * mm, "end": v(25.65, -16.8) * mm});
            skArc(sketch, "E4614", {"start": v(25.65, -16.8) * mm, "mid": v(25.37, -16.19) * mm, "end": v(25.08, -15.6) * mm});
            skArc(sketch, "E4615", {"start": v(25.08, -15.6) * mm, "mid": v(24.91, -15.35) * mm, "end": v(24.68, -15.16) * mm});
            skArc(sketch, "E4616", {"start": v(24.68, -15.16) * mm, "mid": v(24.52, -15.04) * mm, "end": v(24.4, -14.9) * mm});
            skArc(sketch, "E4617", {"start": v(24.4, -14.9) * mm, "mid": v(24.36, -14.79) * mm, "end": v(24.42, -14.69) * mm});
            skArc(sketch, "E4618", {"start": v(24.42, -14.69) * mm, "mid": v(24.56, -14.6) * mm, "end": v(24.72, -14.57) * mm});
            skArc(sketch, "E4619", {"start": v(24.72, -14.57) * mm, "mid": v(25, -14.6) * mm, "end": v(25.27, -14.63) * mm});
            skArc(sketch, "E4620", {"start": v(25.27, -14.63) * mm, "mid": v(25.7, -14.73) * mm, "end": v(26.11, -14.85) * mm});
            skArc(sketch, "E4621", {"start": v(26.11, -14.85) * mm, "mid": v(26.5, -15) * mm, "end": v(26.88, -15.17) * mm});
            skArc(sketch, "E4622", {"start": v(26.88, -15.17) * mm, "mid": v(27.21, -15.36) * mm, "end": v(27.54, -15.58) * mm});
            skArc(sketch, "E4623", {"start": v(27.54, -15.58) * mm, "mid": v(27.82, -15.82) * mm, "end": v(28.08, -16.08) * mm});
            skArc(sketch, "E4624", {"start": v(28.08, -16.08) * mm, "mid": v(28.32, -16.32) * mm, "end": v(28.57, -16.56) * mm});
            skArc(sketch, "E4625", {"start": v(28.57, -16.56) * mm, "mid": v(28.7, -16.61) * mm, "end": v(28.83, -16.6) * mm});
            skArc(sketch, "E4626", {"start": v(28.83, -16.6) * mm, "mid": v(28.95, -16.5) * mm, "end": v(29.02, -16.35) * mm});
            skArc(sketch, "E4627", {"start": v(29.02, -16.35) * mm, "mid": v(29.1, -15.95) * mm, "end": v(29.18, -15.54) * mm});
            skLineSegment(sketch, "E4628", {"start": v(29.18, -15.54) * mm, "end": v(29.36, -14.42) * mm});
            skLineSegment(sketch, "E4629", {"start": v(29.36, -14.42) * mm, "end": v(30.14, -14.97) * mm});
            skArc(sketch, "E4630", {"start": v(30.14, -14.97) * mm, "mid": v(30.64, -15.35) * mm, "end": v(31.1, -15.76) * mm});
            skArc(sketch, "E4631", {"start": v(31.1, -15.76) * mm, "mid": v(31.65, -16.28) * mm, "end": v(32.16, -16.82) * mm});
            skArc(sketch, "E4632", {"start": v(32.16, -16.82) * mm, "mid": v(32.63, -17.35) * mm, "end": v(33.08, -17.9) * mm});
            skArc(sketch, "E4633", {"start": v(33.08, -17.9) * mm, "mid": v(33.32, -18.26) * mm, "end": v(33.52, -18.65) * mm});
            skArc(sketch, "E4634", {"start": v(33.52, -18.65) * mm, "mid": v(33.67, -18.95) * mm, "end": v(33.85, -19.22) * mm});
            skArc(sketch, "E4635", {"start": v(33.85, -19.22) * mm, "mid": v(34.01, -19.35) * mm, "end": v(34.22, -19.4) * mm});
            skArc(sketch, "E4636", {"start": v(34.22, -19.4) * mm, "mid": v(34.41, -19.33) * mm, "end": v(34.56, -19.19) * mm});
            skArc(sketch, "E4637", {"start": v(34.56, -19.19) * mm, "mid": v(34.7, -18.9) * mm, "end": v(34.8, -18.6) * mm});
            skLineSegment(sketch, "E4638", {"start": v(34.8, -18.6) * mm, "end": v(35.02, -17.76) * mm});
            skLineSegment(sketch, "E4639", {"start": v(35.02, -17.76) * mm, "end": v(36.13, -18.8) * mm});
            skArc(sketch, "E4640", {"start": v(36.13, -18.8) * mm, "mid": v(36.38, -19.04) * mm, "end": v(36.62, -19.28) * mm});
            skArc(sketch, "E4641", {"start": v(36.62, -19.28) * mm, "mid": v(36.9, -19.56) * mm, "end": v(37.17, -19.85) * mm});
            skArc(sketch, "E4642", {"start": v(37.17, -19.85) * mm, "mid": v(37.44, -20.13) * mm, "end": v(37.7, -20.42) * mm});
            skArc(sketch, "E4643", {"start": v(37.7, -20.42) * mm, "mid": v(37.9, -20.66) * mm, "end": v(38.11, -20.9) * mm});
            skArc(sketch, "E4644", {"start": v(38.11, -20.9) * mm, "mid": v(38.28, -21.11) * mm, "end": v(38.47, -21.3) * mm});
            skArc(sketch, "E4645", {"start": v(38.47, -21.3) * mm, "mid": v(38.63, -21.46) * mm, "end": v(38.81, -21.6) * mm});
            skArc(sketch, "E4646", {"start": v(38.81, -21.6) * mm, "mid": v(38.96, -21.7) * mm, "end": v(39.1, -21.8) * mm});
            skArc(sketch, "E4647", {"start": v(39.1, -21.8) * mm, "mid": v(39.2, -21.82) * mm, "end": v(39.28, -21.79) * mm});
            skArc(sketch, "E4648", {"start": v(39.28, -21.79) * mm, "mid": v(39.35, -21.72) * mm, "end": v(39.4, -21.62) * mm});
            skArc(sketch, "E4649", {"start": v(39.4, -21.62) * mm, "mid": v(39.45, -21.38) * mm, "end": v(39.5, -21.14) * mm});
            skArc(sketch, "E4650", {"start": v(39.5, -21.14) * mm, "mid": v(39.53, -20.83) * mm, "end": v(39.56, -20.52) * mm});
            skArc(sketch, "E4651", {"start": v(39.56, -20.52) * mm, "mid": v(39.58, -20.17) * mm, "end": v(39.58, -19.82) * mm});
            skArc(sketch, "E4652", {"start": v(39.58, -19.82) * mm, "mid": v(39.59, -19.46) * mm, "end": v(39.6, -19.1) * mm});
            skArc(sketch, "E4653", {"start": v(39.6, -19.1) * mm, "mid": v(39.62, -18.82) * mm, "end": v(39.66, -18.54) * mm});
            skArc(sketch, "E4654", {"start": v(39.66, -18.54) * mm, "mid": v(39.7, -18.33) * mm, "end": v(39.75, -18.13) * mm});
            skArc(sketch, "E4655", {"start": v(39.75, -18.13) * mm, "mid": v(39.8, -18.07) * mm, "end": v(39.87, -18.04) * mm});
            skArc(sketch, "E4656", {"start": v(39.87, -18.04) * mm, "mid": v(40.15, -18.07) * mm, "end": v(40.41, -18.17) * mm});
            skArc(sketch, "E4657", {"start": v(40.41, -18.17) * mm, "mid": v(40.93, -18.43) * mm, "end": v(41.43, -18.71) * mm});
            skArc(sketch, "E4658", {"start": v(41.43, -18.71) * mm, "mid": v(42, -19.06) * mm, "end": v(42.57, -19.43) * mm});
            skArc(sketch, "E4659", {"start": v(42.57, -19.43) * mm, "mid": v(43.13, -19.82) * mm, "end": v(43.67, -20.23) * mm});
            skArc(sketch, "E4660", {"start": v(43.67, -20.23) * mm, "mid": v(43.95, -20.45) * mm, "end": v(44.23, -20.66) * mm});
            skArc(sketch, "E4661", {"start": v(44.23, -20.66) * mm, "mid": v(44.47, -20.85) * mm, "end": v(44.72, -21.03) * mm});
            skArc(sketch, "E4662", {"start": v(44.72, -21.03) * mm, "mid": v(44.93, -21.18) * mm, "end": v(45.14, -21.33) * mm});
            skArc(sketch, "E4663", {"start": v(45.14, -21.33) * mm, "mid": v(45.19, -21.35) * mm, "end": v(45.24, -21.36) * mm});
            skArc(sketch, "E4664", {"start": v(45.24, -21.36) * mm, "mid": v(45.34, -21.31) * mm, "end": v(45.38, -21.21) * mm});
            skArc(sketch, "E4665", {"start": v(45.38, -21.21) * mm, "mid": v(45.35, -20.98) * mm, "end": v(45.3, -20.75) * mm});
            skArc(sketch, "E4666", {"start": v(45.3, -20.75) * mm, "mid": v(45.16, -20.34) * mm, "end": v(45, -19.95) * mm});
            skArc(sketch, "E4667", {"start": v(45, -19.95) * mm, "mid": v(44.7, -19.3) * mm, "end": v(44.4, -18.66) * mm});
            skArc(sketch, "E4668", {"start": v(44.4, -18.66) * mm, "mid": v(44.12, -18.12) * mm, "end": v(43.82, -17.6) * mm});
            skArc(sketch, "E4669", {"start": v(43.82, -17.6) * mm, "mid": v(43.5, -17.08) * mm, "end": v(43.14, -16.57) * mm});
            skArc(sketch, "E4670", {"start": v(43.14, -16.57) * mm, "mid": v(42.74, -16.04) * mm, "end": v(42.32, -15.53) * mm});
            skArc(sketch, "E4671", {"start": v(42.32, -15.53) * mm, "mid": v(41.82, -14.96) * mm, "end": v(41.3, -14.41) * mm});
            skArc(sketch, "E4672", {"start": v(41.3, -14.41) * mm, "mid": v(40.67, -13.75) * mm, "end": v(40.02, -13.11) * mm});
            skArc(sketch, "E4673", {"start": v(40.02, -13.11) * mm, "mid": v(39.65, -12.79) * mm, "end": v(39.25, -12.51) * mm});
            skArc(sketch, "E4674", {"start": v(39.25, -12.51) * mm, "mid": v(39.04, -12.44) * mm, "end": v(38.82, -12.46) * mm});
            skArc(sketch, "E4675", {"start": v(38.82, -12.46) * mm, "mid": v(38.65, -12.56) * mm, "end": v(38.58, -12.74) * mm});
            skArc(sketch, "E4676", {"start": v(38.58, -12.74) * mm, "mid": v(38.57, -12.82) * mm, "end": v(38.56, -12.9) * mm});
            skArc(sketch, "E4677", {"start": v(38.56, -12.9) * mm, "mid": v(38.55, -12.99) * mm, "end": v(38.54, -13.08) * mm});
            skArc(sketch, "E4678", {"start": v(38.54, -13.08) * mm, "mid": v(38.53, -13.18) * mm, "end": v(38.53, -13.28) * mm});
            skArc(sketch, "E4679", {"start": v(38.53, -13.28) * mm, "mid": v(38.52, -13.36) * mm, "end": v(38.5, -13.45) * mm});
            skArc(sketch, "E4680", {"start": v(38.5, -13.45) * mm, "mid": v(38.5, -13.53) * mm, "end": v(38.46, -13.6) * mm});
            skArc(sketch, "E4681", {"start": v(38.46, -13.6) * mm, "mid": v(38.4, -13.68) * mm, "end": v(38.33, -13.76) * mm});
            skArc(sketch, "E4682", {"start": v(38.33, -13.76) * mm, "mid": v(38.24, -13.83) * mm, "end": v(38.15, -13.89) * mm});
            skArc(sketch, "E4683", {"start": v(38.15, -13.89) * mm, "mid": v(38.05, -13.93) * mm, "end": v(37.94, -13.97) * mm});
            skArc(sketch, "E4684", {"start": v(37.94, -13.97) * mm, "mid": v(37.8, -14.02) * mm, "end": v(37.68, -14.1) * mm});
            skArc(sketch, "E4685", {"start": v(37.68, -14.1) * mm, "mid": v(37.6, -14.18) * mm, "end": v(37.54, -14.28) * mm});
            skArc(sketch, "E4686", {"start": v(37.54, -14.28) * mm, "mid": v(37.5, -14.44) * mm, "end": v(37.5, -14.6) * mm});
            skArc(sketch, "E4687", {"start": v(37.5, -14.6) * mm, "mid": v(37.51, -14.89) * mm, "end": v(37.54, -15.18) * mm});
            skArc(sketch, "E4688", {"start": v(37.54, -15.18) * mm, "mid": v(37.57, -15.6) * mm, "end": v(37.57, -16.02) * mm});
            skArc(sketch, "E4689", {"start": v(37.57, -16.02) * mm, "mid": v(37.51, -16.34) * mm, "end": v(37.4, -16.64) * mm});
            skArc(sketch, "E4690", {"start": v(37.4, -16.64) * mm, "mid": v(37.29, -16.77) * mm, "end": v(37.12, -16.82) * mm});
            skArc(sketch, "E4691", {"start": v(37.12, -16.82) * mm, "mid": v(36.95, -16.78) * mm, "end": v(36.82, -16.66) * mm});
            skArc(sketch, "E4692", {"start": v(36.82, -16.66) * mm, "mid": v(36.76, -16.54) * mm, "end": v(36.71, -16.42) * mm});
            skArc(sketch, "E4693", {"start": v(36.71, -16.42) * mm, "mid": v(36.67, -16.22) * mm, "end": v(36.63, -16.02) * mm});
            skArc(sketch, "E4694", {"start": v(36.63, -16.02) * mm, "mid": v(36.6, -15.79) * mm, "end": v(36.57, -15.55) * mm});
            skArc(sketch, "E4695", {"start": v(36.57, -15.55) * mm, "mid": v(36.55, -15.3) * mm, "end": v(36.54, -15.07) * mm});
            skArc(sketch, "E4696", {"start": v(36.54, -15.07) * mm, "mid": v(36.54, -14.75) * mm, "end": v(36.52, -14.43) * mm});
            skArc(sketch, "E4697", {"start": v(36.52, -14.43) * mm, "mid": v(36.5, -14.27) * mm, "end": v(36.44, -14.1) * mm});
            skArc(sketch, "E4698", {"start": v(36.44, -14.1) * mm, "mid": v(36.37, -14.01) * mm, "end": v(36.27, -13.95) * mm});
            skArc(sketch, "E4699", {"start": v(36.27, -13.95) * mm, "mid": v(36.13, -13.9) * mm, "end": v(35.99, -13.9) * mm});
            skArc(sketch, "E4700", {"start": v(35.99, -13.9) * mm, "mid": v(35.84, -13.87) * mm, "end": v(35.7, -13.82) * mm});
            skArc(sketch, "E4701", {"start": v(35.7, -13.82) * mm, "mid": v(35.6, -13.74) * mm, "end": v(35.53, -13.62) * mm});
            skArc(sketch, "E4702", {"start": v(35.53, -13.62) * mm, "mid": v(35.47, -13.42) * mm, "end": v(35.45, -13.2) * mm});
            skArc(sketch, "E4703", {"start": v(35.45, -13.2) * mm, "mid": v(35.44, -12.74) * mm, "end": v(35.43, -12.28) * mm});
            skLineSegment(sketch, "E4704", {"start": v(35.43, -12.28) * mm, "end": v(35.43, -10.66) * mm});
            skLineSegment(sketch, "E4705", {"start": v(35.43, -10.66) * mm, "end": v(33.84, -10.3) * mm});
            skArc(sketch, "E4706", {"start": v(33.84, -10.3) * mm, "mid": v(33.12, -10.17) * mm, "end": v(32.4, -10.1) * mm});
            skArc(sketch, "E4707", {"start": v(32.4, -10.1) * mm, "mid": v(31.3, -10.03) * mm, "end": v(30.22, -10) * mm});
            skArc(sketch, "E4708", {"start": v(30.22, -10) * mm, "mid": v(29.14, -9.98) * mm, "end": v(28.05, -9.99) * mm});
            skArc(sketch, "E4709", {"start": v(28.05, -9.99) * mm, "mid": v(27.7, -10.04) * mm, "end": v(27.38, -10.18) * mm});
            skArc(sketch, "E4710", {"start": v(27.38, -10.18) * mm, "mid": v(27.27, -10.19) * mm, "end": v(27.2, -10.1) * mm});
            skArc(sketch, "E4711", {"start": v(27.2, -10.1) * mm, "mid": v(27.16, -9.88) * mm, "end": v(27.16, -9.65) * mm});
            skArc(sketch, "E4712", {"start": v(27.16, -9.65) * mm, "mid": v(27.2, -9.3) * mm, "end": v(27.3, -8.97) * mm});
            skArc(sketch, "E4713", {"start": v(27.3, -8.97) * mm, "mid": v(27.4, -8.66) * mm, "end": v(27.55, -8.36) * mm});
            skArc(sketch, "E4714", {"start": v(27.55, -8.36) * mm, "mid": v(27.76, -7.97) * mm, "end": v(27.93, -7.57) * mm});
            skArc(sketch, "E4715", {"start": v(27.93, -7.57) * mm, "mid": v(27.94, -7.37) * mm, "end": v(27.83, -7.2) * mm});
            skArc(sketch, "E4716", {"start": v(27.83, -7.2) * mm, "mid": v(27.6, -7.07) * mm, "end": v(27.36, -7.01) * mm});
            skArc(sketch, "E4717", {"start": v(27.36, -7.01) * mm, "mid": v(26.63, -6.99) * mm, "end": v(25.91, -6.98) * mm});
            skArc(sketch, "E4718", {"start": v(25.91, -6.98) * mm, "mid": v(25.14, -7) * mm, "end": v(24.38, -7.06) * mm});
            skArc(sketch, "E4719", {"start": v(24.38, -7.06) * mm, "mid": v(23.45, -7.16) * mm, "end": v(22.53, -7.29) * mm});
            skArc(sketch, "E4720", {"start": v(22.53, -7.29) * mm, "mid": v(21.66, -7.44) * mm, "end": v(20.79, -7.61) * mm});
            skArc(sketch, "E4721", {"start": v(20.79, -7.61) * mm, "mid": v(20.19, -7.76) * mm, "end": v(19.6, -7.96) * mm});
            skArc(sketch, "E4722", {"start": v(19.6, -7.96) * mm, "mid": v(19.44, -8) * mm, "end": v(19.28, -7.96) * mm});
            skArc(sketch, "E4723", {"start": v(19.28, -7.96) * mm, "mid": v(19.19, -7.88) * mm, "end": v(19.17, -7.76) * mm});
            skArc(sketch, "E4724", {"start": v(19.17, -7.76) * mm, "mid": v(19.28, -7.47) * mm, "end": v(19.42, -7.2) * mm});
            skArc(sketch, "E4725", {"start": v(19.42, -7.2) * mm, "mid": v(19.76, -6.68) * mm, "end": v(20.1, -6.16) * mm});
            skArc(sketch, "E4726", {"start": v(20.1, -6.16) * mm, "mid": v(20.3, -5.88) * mm, "end": v(20.48, -5.6) * mm});
            skArc(sketch, "E4727", {"start": v(20.48, -5.6) * mm, "mid": v(20.63, -5.35) * mm, "end": v(20.77, -5.1) * mm});
            skArc(sketch, "E4728", {"start": v(20.77, -5.1) * mm, "mid": v(20.88, -4.9) * mm, "end": v(20.98, -4.69) * mm});
            skArc(sketch, "E4729", {"start": v(20.98, -4.69) * mm, "mid": v(20.99, -4.63) * mm, "end": v(20.96, -4.58) * mm});
            skArc(sketch, "E4730", {"start": v(20.96, -4.58) * mm, "mid": v(20.77, -4.44) * mm, "end": v(20.54, -4.35) * mm});
            skArc(sketch, "E4731", {"start": v(20.54, -4.35) * mm, "mid": v(20, -4.24) * mm, "end": v(19.44, -4.15) * mm});
            skArc(sketch, "E4732", {"start": v(19.44, -4.15) * mm, "mid": v(18.8, -4.06) * mm, "end": v(18.14, -4) * mm});
            skArc(sketch, "E4733", {"start": v(18.14, -4) * mm, "mid": v(17.5, -3.96) * mm, "end": v(16.84, -3.95) * mm});
            skLineSegment(sketch, "E4734", {"start": v(16.84, -3.95) * mm, "end": v(14.97, -3.94) * mm});
            skLineSegment(sketch, "E4735", {"start": v(14.97, -3.94) * mm, "end": v(14.97, -6.98) * mm});
            skLineSegment(sketch, "E4736", {"start": v(14.97, -6.98) * mm, "end": v(14.97, -10.02) * mm});
            skLineSegment(sketch, "E4737", {"start": v(14.97, -10.02) * mm, "end": v(14.26, -10.02) * mm});
            skArc(sketch, "E4738", {"start": v(14.26, -10.02) * mm, "mid": v(14.08, -10.03) * mm, "end": v(13.9, -10.04) * mm});
            skArc(sketch, "E4739", {"start": v(13.9, -10.04) * mm, "mid": v(13.8, -10.07) * mm, "end": v(13.73, -10.13) * mm});
            skArc(sketch, "E4740", {"start": v(13.73, -10.13) * mm, "mid": v(13.68, -10.2) * mm, "end": v(13.67, -10.28) * mm});
            skArc(sketch, "E4741", {"start": v(13.67, -10.28) * mm, "mid": v(13.68, -10.4) * mm, "end": v(13.72, -10.54) * mm});
            skArc(sketch, "E4742", {"start": v(13.72, -10.54) * mm, "mid": v(13.8, -10.87) * mm, "end": v(13.86, -11.22) * mm});
            skArc(sketch, "E4743", {"start": v(13.86, -11.22) * mm, "mid": v(13.9, -11.65) * mm, "end": v(13.91, -12.08) * mm});
            skArc(sketch, "E4744", {"start": v(13.91, -12.08) * mm, "mid": v(13.9, -12.49) * mm, "end": v(13.88, -12.9) * mm});
            skArc(sketch, "E4745", {"start": v(13.88, -12.9) * mm, "mid": v(13.84, -13.12) * mm, "end": v(13.74, -13.32) * mm});
            skArc(sketch, "E4746", {"start": v(13.74, -13.32) * mm, "mid": v(13.61, -13.43) * mm, "end": v(13.45, -13.46) * mm});
            skArc(sketch, "E4747", {"start": v(13.45, -13.46) * mm, "mid": v(13.28, -13.4) * mm, "end": v(13.17, -13.25) * mm});
            skArc(sketch, "E4748", {"start": v(13.17, -13.25) * mm, "mid": v(13.05, -12.9) * mm, "end": v(12.97, -12.53) * mm});
            skArc(sketch, "E4749", {"start": v(12.97, -12.53) * mm, "mid": v(12.93, -12) * mm, "end": v(12.9, -11.47) * mm});
            skArc(sketch, "E4750", {"start": v(12.9, -11.47) * mm, "mid": v(12.9, -11.02) * mm, "end": v(12.89, -10.56) * mm});
            skArc(sketch, "E4751", {"start": v(12.89, -10.56) * mm, "mid": v(12.86, -10.36) * mm, "end": v(12.8, -10.15) * mm});
            skArc(sketch, "E4752", {"start": v(12.8, -10.15) * mm, "mid": v(12.74, -10.04) * mm, "end": v(12.64, -9.96) * mm});
            skArc(sketch, "E4753", {"start": v(12.64, -9.96) * mm, "mid": v(12.5, -9.9) * mm, "end": v(12.35, -9.88) * mm});
            skArc(sketch, "E4754", {"start": v(12.35, -9.88) * mm, "mid": v(12.18, -9.85) * mm, "end": v(12.04, -9.76) * mm});
            skArc(sketch, "E4755", {"start": v(12.04, -9.76) * mm, "mid": v(11.93, -9.6) * mm, "end": v(11.86, -9.43) * mm});
            skArc(sketch, "E4756", {"start": v(11.86, -9.43) * mm, "mid": v(11.8, -9.08) * mm, "end": v(11.78, -8.72) * mm});
            skArc(sketch, "E4757", {"start": v(11.78, -8.72) * mm, "mid": v(11.74, -7.8) * mm, "end": v(11.71, -6.9) * mm});
            skLineSegment(sketch, "E4758", {"start": v(11.71, -6.9) * mm, "end": v(11.64, -3.9) * mm});
            skLineSegment(sketch, "E4759", {"start": v(11.64, -3.9) * mm, "end": v(10.05, -4.08) * mm});
            skArc(sketch, "E4760", {"start": v(10.05, -4.08) * mm, "mid": v(9.71, -4.13) * mm, "end": v(9.37, -4.17) * mm});
            skArc(sketch, "E4761", {"start": v(9.37, -4.17) * mm, "mid": v(9, -4.23) * mm, "end": v(8.63, -4.3) * mm});
            skArc(sketch, "E4762", {"start": v(8.63, -4.3) * mm, "mid": v(8.28, -4.35) * mm, "end": v(7.93, -4.42) * mm});
            skArc(sketch, "E4763", {"start": v(7.93, -4.42) * mm, "mid": v(7.67, -4.47) * mm, "end": v(7.4, -4.54) * mm});
            skArc(sketch, "E4764", {"start": v(7.4, -4.54) * mm, "mid": v(7.2, -4.58) * mm, "end": v(7, -4.63) * mm});
            skArc(sketch, "E4765", {"start": v(7, -4.63) * mm, "mid": v(6.8, -4.66) * mm, "end": v(6.62, -4.69) * mm});
            skArc(sketch, "E4766", {"start": v(6.62, -4.69) * mm, "mid": v(6.46, -4.7) * mm, "end": v(6.31, -4.7) * mm});
            skArc(sketch, "E4767", {"start": v(6.31, -4.7) * mm, "mid": v(6.26, -4.7) * mm, "end": v(6.2, -4.67) * mm});
            skArc(sketch, "E4768", {"start": v(6.2, -4.67) * mm, "mid": v(6.14, -4.5) * mm, "end": v(6.2, -4.33) * mm});
            skArc(sketch, "E4769", {"start": v(6.2, -4.33) * mm, "mid": v(6.85, -3.67) * mm, "end": v(7.5, -3.01) * mm});
            skArc(sketch, "E4770", {"start": v(7.5, -3.01) * mm, "mid": v(8.16, -2.38) * mm, "end": v(8.84, -1.78) * mm});
            skArc(sketch, "E4771", {"start": v(8.84, -1.78) * mm, "mid": v(9.3, -1.43) * mm, "end": v(9.79, -1.14) * mm});
            skArc(sketch, "E4772", {"start": v(9.79, -1.14) * mm, "mid": v(10.07, -1) * mm, "end": v(10.34, -0.83) * mm});
            skArc(sketch, "E4773", {"start": v(10.34, -0.83) * mm, "mid": v(10.47, -0.73) * mm, "end": v(10.59, -0.61) * mm});
            skArc(sketch, "E4774", {"start": v(10.59, -0.61) * mm, "mid": v(10.64, -0.5) * mm, "end": v(10.65, -0.39) * mm});
            skArc(sketch, "E4775", {"start": v(10.65, -0.39) * mm, "mid": v(10.62, -0.24) * mm, "end": v(10.57, -0.1) * mm});
            skArc(sketch, "E4776", {"start": v(10.57, -0.1) * mm, "mid": v(10.5, 0) * mm, "end": v(10.43, 0.11) * mm});
            skArc(sketch, "E4777", {"start": v(10.43, 0.11) * mm, "mid": v(10.34, 0.23) * mm, "end": v(10.25, 0.35) * mm});
            skArc(sketch, "E4778", {"start": v(10.25, 0.35) * mm, "mid": v(10.15, 0.47) * mm, "end": v(10.05, 0.58) * mm});
            skArc(sketch, "E4779", {"start": v(10.05, 0.58) * mm, "mid": v(9.96, 0.67) * mm, "end": v(9.86, 0.76) * mm});
            skArc(sketch, "E4780", {"start": v(9.86, 0.76) * mm, "mid": v(9.73, 1.12) * mm, "end": v(10, 1.4) * mm});
            skArc(sketch, "E4781", {"start": v(10, 1.4) * mm, "mid": v(10.86, 1.57) * mm, "end": v(11.74, 1.6) * mm});
            skArc(sketch, "E4782", {"start": v(11.74, 1.6) * mm, "mid": v(13.16, 1.46) * mm, "end": v(14.56, 1.2) * mm});
            skArc(sketch, "E4783", {"start": v(14.56, 1.2) * mm, "mid": v(15.73, 0.87) * mm, "end": v(16.84, 0.38) * mm});
            skArc(sketch, "E4784", {"start": v(16.84, 0.38) * mm, "mid": v(17.12, 0.24) * mm, "end": v(17.39, 0.11) * mm});
            skArc(sketch, "E4785", {"start": v(17.39, 0.11) * mm, "mid": v(17.5, 0.07) * mm, "end": v(17.63, 0.06) * mm});
            skArc(sketch, "E4786", {"start": v(17.63, 0.06) * mm, "mid": v(17.72, 0.07) * mm, "end": v(17.79, 0.13) * mm});
            skArc(sketch, "E4787", {"start": v(17.79, 0.13) * mm, "mid": v(17.86, 0.24) * mm, "end": v(17.92, 0.36) * mm});
            skArc(sketch, "E4788", {"start": v(17.92, 0.36) * mm, "mid": v(17.95, 0.48) * mm, "end": v(17.97, 0.6) * mm});
            skArc(sketch, "E4789", {"start": v(17.97, 0.6) * mm, "mid": v(17.96, 0.79) * mm, "end": v(17.95, 0.97) * mm});
            skArc(sketch, "E4790", {"start": v(17.95, 0.97) * mm, "mid": v(17.93, 1.18) * mm, "end": v(17.89, 1.4) * mm});
            skArc(sketch, "E4791", {"start": v(17.89, 1.4) * mm, "mid": v(17.84, 1.6) * mm, "end": v(17.79, 1.8) * mm});
            skArc(sketch, "E4792", {"start": v(17.79, 1.8) * mm, "mid": v(17.73, 2) * mm, "end": v(17.68, 2.2) * mm});
            skArc(sketch, "E4793", {"start": v(17.68, 2.2) * mm, "mid": v(17.64, 2.38) * mm, "end": v(17.6, 2.55) * mm});
            skArc(sketch, "E4794", {"start": v(17.6, 2.55) * mm, "mid": v(17.6, 2.7) * mm, "end": v(17.58, 2.84) * mm});
            skArc(sketch, "E4795", {"start": v(17.58, 2.84) * mm, "mid": v(17.59, 2.9) * mm, "end": v(17.62, 2.95) * mm});
            skArc(sketch, "E4796", {"start": v(17.62, 2.95) * mm, "mid": v(17.81, 3.06) * mm, "end": v(18.04, 3.07) * mm});
            skArc(sketch, "E4797", {"start": v(18.04, 3.07) * mm, "mid": v(18.83, 2.88) * mm, "end": v(19.6, 2.68) * mm});
            skArc(sketch, "E4798", {"start": v(19.6, 2.68) * mm, "mid": v(20.44, 2.43) * mm, "end": v(21.25, 2.16) * mm});
            skArc(sketch, "E4799", {"start": v(21.25, 2.16) * mm, "mid": v(21.95, 1.9) * mm, "end": v(22.62, 1.59) * mm});
            skArc(sketch, "E4800", {"start": v(22.62, 1.59) * mm, "mid": v(23, 1.39) * mm, "end": v(23.38, 1.17) * mm});
            skArc(sketch, "E4801", {"start": v(23.38, 1.17) * mm, "mid": v(23.81, 0.9) * mm, "end": v(24.24, 0.62) * mm});
            skArc(sketch, "E4802", {"start": v(24.24, 0.62) * mm, "mid": v(24.66, 0.33) * mm, "end": v(25.08, 0.02) * mm});
            skArc(sketch, "E4803", {"start": v(25.08, 0.02) * mm, "mid": v(25.42, -0.24) * mm, "end": v(25.74, -0.52) * mm});
            skArc(sketch, "E4804", {"start": v(25.74, -0.52) * mm, "mid": v(26.02, -0.77) * mm, "end": v(26.3, -1) * mm});
            skArc(sketch, "E4805", {"start": v(26.3, -1) * mm, "mid": v(26.54, -1.19) * mm, "end": v(26.8, -1.37) * mm});
            skArc(sketch, "E4806", {"start": v(26.8, -1.37) * mm, "mid": v(27, -1.5) * mm, "end": v(27.2, -1.63) * mm});
            skArc(sketch, "E4807", {"start": v(27.2, -1.63) * mm, "mid": v(27.28, -1.65) * mm, "end": v(27.34, -1.62) * mm});
            skArc(sketch, "E4808", {"start": v(27.34, -1.62) * mm, "mid": v(27.39, -1.55) * mm, "end": v(27.41, -1.48) * mm});
            skArc(sketch, "E4809", {"start": v(27.41, -1.48) * mm, "mid": v(27.43, -1.3) * mm, "end": v(27.45, -1.12) * mm});
            skArc(sketch, "E4810", {"start": v(27.45, -1.12) * mm, "mid": v(27.46, -0.9) * mm, "end": v(27.46, -0.68) * mm});
            skArc(sketch, "E4811", {"start": v(27.46, -0.68) * mm, "mid": v(27.46, -0.44) * mm, "end": v(27.45, -0.2) * mm});
            skArc(sketch, "E4812", {"start": v(27.45, -0.2) * mm, "mid": v(27.44, 0.1) * mm, "end": v(27.43, 0.38) * mm});
            skArc(sketch, "E4813", {"start": v(27.43, 0.38) * mm, "mid": v(27.44, 0.57) * mm, "end": v(27.48, 0.75) * mm});
            skArc(sketch, "E4814", {"start": v(27.48, 0.75) * mm, "mid": v(27.52, 0.86) * mm, "end": v(27.58, 0.96) * mm});
            skArc(sketch, "E4815", {"start": v(27.58, 0.96) * mm, "mid": v(27.65, 1.02) * mm, "end": v(27.74, 1.04) * mm});
            skArc(sketch, "E4816", {"start": v(27.74, 1.04) * mm, "mid": v(28.14, 0.98) * mm, "end": v(28.5, 0.8) * mm});
            skArc(sketch, "E4817", {"start": v(28.5, 0.8) * mm, "mid": v(29.36, 0.22) * mm, "end": v(30.2, -0.4) * mm});
            skArc(sketch, "E4818", {"start": v(30.2, -0.4) * mm, "mid": v(31.07, -1.06) * mm, "end": v(31.9, -1.75) * mm});
            skArc(sketch, "E4819", {"start": v(31.9, -1.75) * mm, "mid": v(32.52, -2.33) * mm, "end": v(33.1, -2.95) * mm});
            skArc(sketch, "E4820", {"start": v(33.1, -2.95) * mm, "mid": v(33.36, -3.24) * mm, "end": v(33.62, -3.52) * mm});
            skArc(sketch, "E4821", {"start": v(33.62, -3.52) * mm, "mid": v(33.85, -3.76) * mm, "end": v(34.1, -3.98) * mm});
            skArc(sketch, "E4822", {"start": v(34.1, -3.98) * mm, "mid": v(34.3, -4.15) * mm, "end": v(34.5, -4.32) * mm});
            skArc(sketch, "E4823", {"start": v(34.5, -4.32) * mm, "mid": v(34.57, -4.35) * mm, "end": v(34.65, -4.33) * mm});
            skArc(sketch, "E4824", {"start": v(34.65, -4.33) * mm, "mid": v(34.7, -4.27) * mm, "end": v(34.74, -4.2) * mm});
            skArc(sketch, "E4825", {"start": v(34.74, -4.2) * mm, "mid": v(34.78, -4.01) * mm, "end": v(34.81, -3.82) * mm});
            skArc(sketch, "E4826", {"start": v(34.81, -3.82) * mm, "mid": v(34.84, -3.59) * mm, "end": v(34.86, -3.35) * mm});
            skArc(sketch, "E4827", {"start": v(34.86, -3.35) * mm, "mid": v(34.88, -3.08) * mm, "end": v(34.88, -2.82) * mm});
            skArc(sketch, "E4828", {"start": v(34.88, -2.82) * mm, "mid": v(34.88, -2.56) * mm, "end": v(34.9, -2.3) * mm});
            skArc(sketch, "E4829", {"start": v(34.9, -2.3) * mm, "mid": v(34.91, -2.07) * mm, "end": v(34.94, -1.85) * mm});
            skArc(sketch, "E4830", {"start": v(34.94, -1.85) * mm, "mid": v(34.97, -1.68) * mm, "end": v(35, -1.52) * mm});
            skArc(sketch, "E4831", {"start": v(35, -1.52) * mm, "mid": v(35.04, -1.47) * mm, "end": v(35.09, -1.45) * mm});
            skArc(sketch, "E4832", {"start": v(35.09, -1.45) * mm, "mid": v(35.43, -1.5) * mm, "end": v(35.75, -1.64) * mm});
            skArc(sketch, "E4833", {"start": v(35.75, -1.64) * mm, "mid": v(36.4, -2.07) * mm, "end": v(37.06, -2.51) * mm});
            skArc(sketch, "E4834", {"start": v(37.06, -2.51) * mm, "mid": v(37.73, -3) * mm, "end": v(38.39, -3.53) * mm});
            skArc(sketch, "E4835", {"start": v(38.39, -3.53) * mm, "mid": v(38.9, -3.98) * mm, "end": v(39.36, -4.46) * mm});
            skArc(sketch, "E4836", {"start": v(39.36, -4.46) * mm, "mid": v(39.6, -4.73) * mm, "end": v(39.86, -4.98) * mm});
            skArc(sketch, "E4837", {"start": v(39.86, -4.98) * mm, "mid": v(40.07, -5.2) * mm, "end": v(40.3, -5.4) * mm});
            skArc(sketch, "E4838", {"start": v(40.3, -5.4) * mm, "mid": v(40.48, -5.54) * mm, "end": v(40.67, -5.69) * mm});
            skArc(sketch, "E4839", {"start": v(40.67, -5.69) * mm, "mid": v(40.73, -5.7) * mm, "end": v(40.79, -5.68) * mm});
            skArc(sketch, "E4840", {"start": v(40.79, -5.68) * mm, "mid": v(40.83, -5.62) * mm, "end": v(40.86, -5.55) * mm});
            skArc(sketch, "E4841", {"start": v(40.86, -5.55) * mm, "mid": v(40.89, -5.38) * mm, "end": v(40.91, -5.2) * mm});
            skArc(sketch, "E4842", {"start": v(40.91, -5.2) * mm, "mid": v(40.94, -4.99) * mm, "end": v(40.95, -4.77) * mm});
            skArc(sketch, "E4843", {"start": v(40.95, -4.77) * mm, "mid": v(40.96, -4.53) * mm, "end": v(40.96, -4.3) * mm});
            skLineSegment(sketch, "E4844", {"start": v(40.96, -4.3) * mm, "end": v(40.96, -3.08) * mm});
            skLineSegment(sketch, "E4845", {"start": v(40.96, -3.08) * mm, "end": v(41.82, -3.58) * mm});
            skArc(sketch, "E4846", {"start": v(41.82, -3.58) * mm, "mid": v(42.02, -3.7) * mm, "end": v(42.22, -3.84) * mm});
            skArc(sketch, "E4847", {"start": v(42.22, -3.84) * mm, "mid": v(42.48, -4.04) * mm, "end": v(42.73, -4.25) * mm});
            skArc(sketch, "E4848", {"start": v(42.73, -4.25) * mm, "mid": v(43, -4.48) * mm, "end": v(43.27, -4.71) * mm});
            skArc(sketch, "E4849", {"start": v(43.27, -4.71) * mm, "mid": v(43.51, -4.93) * mm, "end": v(43.75, -5.16) * mm});
            skArc(sketch, "E4850", {"start": v(43.75, -5.16) * mm, "mid": v(43.96, -5.37) * mm, "end": v(44.17, -5.57) * mm});
            skArc(sketch, "E4851", {"start": v(44.17, -5.57) * mm, "mid": v(44.36, -5.73) * mm, "end": v(44.56, -5.88) * mm});
            skArc(sketch, "E4852", {"start": v(44.56, -5.88) * mm, "mid": v(44.72, -5.98) * mm, "end": v(44.88, -6.08) * mm});
            skArc(sketch, "E4853", {"start": v(44.88, -6.08) * mm, "mid": v(44.95, -6.1) * mm, "end": v(45.01, -6.07) * mm});
            skArc(sketch, "E4854", {"start": v(45.01, -6.07) * mm, "mid": v(45.13, -5.85) * mm, "end": v(45.13, -5.61) * mm});
            skArc(sketch, "E4855", {"start": v(45.13, -5.61) * mm, "mid": v(44.97, -5.08) * mm, "end": v(44.78, -4.57) * mm});
            skArc(sketch, "E4856", {"start": v(44.78, -4.57) * mm, "mid": v(44.5, -3.97) * mm, "end": v(44.2, -3.4) * mm});
            skArc(sketch, "E4857", {"start": v(44.2, -3.4) * mm, "mid": v(43.85, -2.85) * mm, "end": v(43.46, -2.33) * mm});
            skArc(sketch, "E4858", {"start": v(43.46, -2.33) * mm, "mid": v(43.17, -1.99) * mm, "end": v(42.86, -1.66) * mm});
            skArc(sketch, "E4859", {"start": v(42.86, -1.66) * mm, "mid": v(42.46, -1.29) * mm, "end": v(42.04, -0.93) * mm});
            skArc(sketch, "E4860", {"start": v(42.04, -0.93) * mm, "mid": v(41.56, -0.55) * mm, "end": v(41.08, -0.19) * mm});
            skArc(sketch, "E4861", {"start": v(41.08, -0.19) * mm, "mid": v(40.55, 0.18) * mm, "end": v(40.02, 0.52) * mm});
            skArc(sketch, "E4862", {"start": v(40.02, 0.52) * mm, "mid": v(39.56, 0.81) * mm, "end": v(39.11, 1.1) * mm});
            skArc(sketch, "E4863", {"start": v(39.11, 1.1) * mm, "mid": v(38.73, 1.37) * mm, "end": v(38.35, 1.65) * mm});
            skArc(sketch, "E4864", {"start": v(38.35, 1.65) * mm, "mid": v(38.04, 1.88) * mm, "end": v(37.73, 2.12) * mm});
            skArc(sketch, "E4865", {"start": v(37.73, 2.12) * mm, "mid": v(37.67, 2.19) * mm, "end": v(37.65, 2.27) * mm});
            skArc(sketch, "E4866", {"start": v(37.65, 2.27) * mm, "mid": v(37.66, 2.34) * mm, "end": v(37.7, 2.41) * mm});
            skArc(sketch, "E4867", {"start": v(37.7, 2.41) * mm, "mid": v(37.78, 2.53) * mm, "end": v(37.87, 2.64) * mm});
            skArc(sketch, "E4868", {"start": v(37.87, 2.64) * mm, "mid": v(37.99, 2.77) * mm, "end": v(38.11, 2.9) * mm});
            skArc(sketch, "E4869", {"start": v(38.11, 2.9) * mm, "mid": v(38.26, 3.03) * mm, "end": v(38.4, 3.15) * mm});
            skArc(sketch, "E4870", {"start": v(38.4, 3.15) * mm, "mid": v(38.65, 3.35) * mm, "end": v(38.9, 3.56) * mm});
            skArc(sketch, "E4871", {"start": v(38.9, 3.56) * mm, "mid": v(38.96, 3.64) * mm, "end": v(39, 3.74) * mm});
            skArc(sketch, "E4872", {"start": v(39, 3.74) * mm, "mid": v(38.99, 3.83) * mm, "end": v(38.94, 3.9) * mm});
            skArc(sketch, "E4873", {"start": v(38.94, 3.9) * mm, "mid": v(38.78, 4.05) * mm, "end": v(38.61, 4.18) * mm});
            skArc(sketch, "E4874", {"start": v(38.61, 4.18) * mm, "mid": v(38.22, 4.46) * mm, "end": v(37.8, 4.7) * mm});
            skArc(sketch, "E4875", {"start": v(37.8, 4.7) * mm, "mid": v(37.29, 4.98) * mm, "end": v(36.77, 5.22) * mm});
            skArc(sketch, "E4876", {"start": v(36.77, 5.22) * mm, "mid": v(36.24, 5.45) * mm, "end": v(35.71, 5.65) * mm});
            skArc(sketch, "E4877", {"start": v(35.71, 5.65) * mm, "mid": v(35.27, 5.78) * mm, "end": v(34.83, 5.88) * mm});
            skLineSegment(sketch, "E4878", {"start": v(34.83, 5.88) * mm, "end": v(33.81, 6.07) * mm});
            skLineSegment(sketch, "E4879", {"start": v(33.81, 6.07) * mm, "end": v(33.72, 5) * mm});
            skArc(sketch, "E4880", {"start": v(33.72, 5) * mm, "mid": v(33.7, 4.73) * mm, "end": v(33.65, 4.46) * mm});
            skArc(sketch, "E4881", {"start": v(33.65, 4.46) * mm, "mid": v(33.6, 4.3) * mm, "end": v(33.53, 4.14) * mm});
            skArc(sketch, "E4882", {"start": v(33.53, 4.14) * mm, "mid": v(33.45, 4.04) * mm, "end": v(33.34, 3.95) * mm});
            skArc(sketch, "E4883", {"start": v(33.34, 3.95) * mm, "mid": v(33.2, 3.9) * mm, "end": v(33.05, 3.86) * mm});
            skArc(sketch, "E4884", {"start": v(33.05, 3.86) * mm, "mid": v(32.9, 3.82) * mm, "end": v(32.74, 3.76) * mm});
            skArc(sketch, "E4885", {"start": v(32.74, 3.76) * mm, "mid": v(32.64, 3.69) * mm, "end": v(32.58, 3.58) * mm});
            skArc(sketch, "E4886", {"start": v(32.58, 3.58) * mm, "mid": v(32.55, 3.42) * mm, "end": v(32.54, 3.26) * mm});
            skArc(sketch, "E4887", {"start": v(32.54, 3.26) * mm, "mid": v(32.57, 2.9) * mm, "end": v(32.6, 2.56) * mm});
            skArc(sketch, "E4888", {"start": v(32.6, 2.56) * mm, "mid": v(32.65, 2.03) * mm, "end": v(32.67, 1.5) * mm});
            skArc(sketch, "E4889", {"start": v(32.67, 1.5) * mm, "mid": v(32.65, 1.18) * mm, "end": v(32.57, 0.88) * mm});
            skArc(sketch, "E4890", {"start": v(32.57, 0.88) * mm, "mid": v(32.46, 0.74) * mm, "end": v(32.3, 0.68) * mm});
            skArc(sketch, "E4891", {"start": v(32.3, 0.68) * mm, "mid": v(32.11, 0.7) * mm, "end": v(31.94, 0.8) * mm});
            skArc(sketch, "E4892", {"start": v(31.94, 0.8) * mm, "mid": v(31.83, 0.9) * mm, "end": v(31.74, 1.04) * mm});
            skArc(sketch, "E4893", {"start": v(31.74, 1.04) * mm, "mid": v(31.67, 1.2) * mm, "end": v(31.63, 1.36) * mm});
            skArc(sketch, "E4894", {"start": v(31.63, 1.36) * mm, "mid": v(31.6, 1.58) * mm, "end": v(31.6, 1.8) * mm});
            skArc(sketch, "E4895", {"start": v(31.6, 1.8) * mm, "mid": v(31.62, 2.13) * mm, "end": v(31.65, 2.46) * mm});
            skArc(sketch, "E4896", {"start": v(31.65, 2.46) * mm, "mid": v(31.7, 2.85) * mm, "end": v(31.73, 3.24) * mm});
            skArc(sketch, "E4897", {"start": v(31.73, 3.24) * mm, "mid": v(31.72, 3.4) * mm, "end": v(31.69, 3.58) * mm});
            skArc(sketch, "E4898", {"start": v(31.69, 3.58) * mm, "mid": v(31.63, 3.68) * mm, "end": v(31.53, 3.76) * mm});
            skArc(sketch, "E4899", {"start": v(31.53, 3.76) * mm, "mid": v(31.37, 3.82) * mm, "end": v(31.2, 3.85) * mm});
            skArc(sketch, "E4900", {"start": v(31.2, 3.85) * mm, "mid": v(31.04, 3.9) * mm, "end": v(30.88, 3.96) * mm});
            skArc(sketch, "E4901", {"start": v(30.88, 3.96) * mm, "mid": v(30.77, 4.05) * mm, "end": v(30.69, 4.17) * mm});
            skArc(sketch, "E4902", {"start": v(30.69, 4.17) * mm, "mid": v(30.62, 4.36) * mm, "end": v(30.58, 4.55) * mm});
            skArc(sketch, "E4903", {"start": v(30.58, 4.55) * mm, "mid": v(30.54, 4.92) * mm, "end": v(30.5, 5.3) * mm});
            skLineSegment(sketch, "E4904", {"start": v(30.5, 5.3) * mm, "end": v(30.42, 6.64) * mm});
            skLineSegment(sketch, "E4905", {"start": v(30.42, 6.64) * mm, "end": v(28.02, 6.48) * mm});
            skArc(sketch, "E4906", {"start": v(28.02, 6.48) * mm, "mid": v(27.54, 6.45) * mm, "end": v(27.05, 6.4) * mm});
            skArc(sketch, "E4907", {"start": v(27.05, 6.4) * mm, "mid": v(26.6, 6.36) * mm, "end": v(26.13, 6.31) * mm});
            skArc(sketch, "E4908", {"start": v(26.13, 6.31) * mm, "mid": v(25.74, 6.27) * mm, "end": v(25.35, 6.21) * mm});
            skArc(sketch, "E4909", {"start": v(25.35, 6.21) * mm, "mid": v(25.15, 6.18) * mm, "end": v(24.96, 6.13) * mm});
            skArc(sketch, "E4910", {"start": v(24.96, 6.13) * mm, "mid": v(24.77, 6.07) * mm, "end": v(24.57, 6.03) * mm});
            skArc(sketch, "E4911", {"start": v(24.57, 6.03) * mm, "mid": v(24.49, 6.04) * mm, "end": v(24.42, 6.08) * mm});
            skArc(sketch, "E4912", {"start": v(24.42, 6.08) * mm, "mid": v(24.38, 6.16) * mm, "end": v(24.37, 6.25) * mm});
            skArc(sketch, "E4913", {"start": v(24.37, 6.25) * mm, "mid": v(24.4, 6.5) * mm, "end": v(24.45, 6.73) * mm});
            skArc(sketch, "E4914", {"start": v(24.45, 6.73) * mm, "mid": v(24.48, 6.9) * mm, "end": v(24.52, 7.09) * mm});
            skArc(sketch, "E4915", {"start": v(24.52, 7.09) * mm, "mid": v(24.56, 7.28) * mm, "end": v(24.61, 7.48) * mm});
            skArc(sketch, "E4916", {"start": v(24.61, 7.48) * mm, "mid": v(24.66, 7.67) * mm, "end": v(24.7, 7.86) * mm});
            skArc(sketch, "E4917", {"start": v(24.7, 7.86) * mm, "mid": v(24.75, 8.01) * mm, "end": v(24.8, 8.16) * mm});
            skArc(sketch, "E4918", {"start": v(24.8, 8.16) * mm, "mid": v(24.84, 8.33) * mm, "end": v(24.87, 8.52) * mm});
            skArc(sketch, "E4919", {"start": v(24.87, 8.52) * mm, "mid": v(24.85, 8.61) * mm, "end": v(24.78, 8.69) * mm});
            skArc(sketch, "E4920", {"start": v(24.78, 8.69) * mm, "mid": v(24.65, 8.74) * mm, "end": v(24.51, 8.77) * mm});
            skArc(sketch, "E4921", {"start": v(24.51, 8.77) * mm, "mid": v(24.14, 8.78) * mm, "end": v(23.76, 8.78) * mm});
            skArc(sketch, "E4922", {"start": v(23.76, 8.78) * mm, "mid": v(23.45, 8.77) * mm, "end": v(23.14, 8.74) * mm});
            skArc(sketch, "E4923", {"start": v(23.14, 8.74) * mm, "mid": v(22.7, 8.68) * mm, "end": v(22.25, 8.62) * mm});
            skArc(sketch, "E4924", {"start": v(22.25, 8.62) * mm, "mid": v(21.77, 8.53) * mm, "end": v(21.28, 8.44) * mm});
            skArc(sketch, "E4925", {"start": v(21.28, 8.44) * mm, "mid": v(20.82, 8.34) * mm, "end": v(20.36, 8.23) * mm});
            skArc(sketch, "E4926", {"start": v(20.36, 8.23) * mm, "mid": v(19.94, 8.12) * mm, "end": v(19.52, 8.02) * mm});
            skArc(sketch, "E4927", {"start": v(19.52, 8.02) * mm, "mid": v(19.16, 7.94) * mm, "end": v(18.8, 7.87) * mm});
            skArc(sketch, "E4928", {"start": v(18.8, 7.87) * mm, "mid": v(18.5, 7.81) * mm, "end": v(18.19, 7.76) * mm});
            skArc(sketch, "E4929", {"start": v(18.19, 7.76) * mm, "mid": v(18.13, 7.76) * mm, "end": v(18.08, 7.79) * mm});
            skArc(sketch, "E4930", {"start": v(18.08, 7.79) * mm, "mid": v(18.03, 7.9) * mm, "end": v(18.04, 8.02) * mm});
            skArc(sketch, "E4931", {"start": v(18.04, 8.02) * mm, "mid": v(18.2, 8.33) * mm, "end": v(18.36, 8.63) * mm});
            skArc(sketch, "E4932", {"start": v(18.36, 8.63) * mm, "mid": v(18.57, 8.98) * mm, "end": v(18.8, 9.31) * mm});
            skArc(sketch, "E4933", {"start": v(18.8, 9.31) * mm, "mid": v(19.06, 9.64) * mm, "end": v(19.34, 9.95) * mm});
            skArc(sketch, "E4934", {"start": v(19.34, 9.95) * mm, "mid": v(19.47, 10.1) * mm, "end": v(19.6, 10.25) * mm});
            skArc(sketch, "E4935", {"start": v(19.6, 10.25) * mm, "mid": v(19.7, 10.39) * mm, "end": v(19.8, 10.53) * mm});
            skArc(sketch, "E4936", {"start": v(19.8, 10.53) * mm, "mid": v(19.86, 10.64) * mm, "end": v(19.92, 10.76) * mm});
            skArc(sketch, "E4937", {"start": v(19.92, 10.76) * mm, "mid": v(19.92, 10.81) * mm, "end": v(19.9, 10.86) * mm});
            skArc(sketch, "E4938", {"start": v(19.9, 10.86) * mm, "mid": v(19.42, 11.22) * mm, "end": v(18.86, 11.44) * mm});
            skArc(sketch, "E4939", {"start": v(18.86, 11.44) * mm, "mid": v(17.66, 11.7) * mm, "end": v(16.44, 11.92) * mm});
            skArc(sketch, "E4940", {"start": v(16.44, 11.92) * mm, "mid": v(15.22, 12.1) * mm, "end": v(14, 12.23) * mm});
            skArc(sketch, "E4941", {"start": v(14, 12.23) * mm, "mid": v(13.71, 12.14) * mm, "end": v(13.59, 11.86) * mm});
            skArc(sketch, "E4942", {"start": v(13.59, 11.86) * mm, "mid": v(13.6, 11.79) * mm, "end": v(13.64, 11.73) * mm});
            skArc(sketch, "E4943", {"start": v(13.64, 11.73) * mm, "mid": v(13.78, 11.6) * mm, "end": v(13.91, 11.47) * mm});
            skArc(sketch, "E4944", {"start": v(13.91, 11.47) * mm, "mid": v(14.1, 11.33) * mm, "end": v(14.27, 11.18) * mm});
            skArc(sketch, "E4945", {"start": v(14.27, 11.18) * mm, "mid": v(14.48, 11.03) * mm, "end": v(14.7, 10.89) * mm});
            skArc(sketch, "E4946", {"start": v(14.7, 10.89) * mm, "mid": v(15.06, 10.64) * mm, "end": v(15.41, 10.37) * mm});
            skArc(sketch, "E4947", {"start": v(15.41, 10.37) * mm, "mid": v(15.59, 10.2) * mm, "end": v(15.73, 10) * mm});
            skArc(sketch, "E4948", {"start": v(15.73, 10) * mm, "mid": v(15.76, 9.87) * mm, "end": v(15.72, 9.74) * mm});
            skArc(sketch, "E4949", {"start": v(15.72, 9.74) * mm, "mid": v(15.6, 9.62) * mm, "end": v(15.46, 9.54) * mm});
            skArc(sketch, "E4950", {"start": v(15.46, 9.54) * mm, "mid": v(15.39, 9.5) * mm, "end": v(15.32, 9.47) * mm});
            skArc(sketch, "E4951", {"start": v(15.32, 9.47) * mm, "mid": v(15.26, 9.4) * mm, "end": v(15.2, 9.34) * mm});
            skArc(sketch, "E4952", {"start": v(15.2, 9.34) * mm, "mid": v(15.16, 9.27) * mm, "end": v(15.12, 9.2) * mm});
            skArc(sketch, "E4953", {"start": v(15.12, 9.2) * mm, "mid": v(15.1, 9.11) * mm, "end": v(15.08, 9.03) * mm});
            skArc(sketch, "E4954", {"start": v(15.08, 9.03) * mm, "mid": v(15.05, 8.58) * mm, "end": v(15, 8.13) * mm});
            skArc(sketch, "E4955", {"start": v(15, 8.13) * mm, "mid": v(14.96, 8.03) * mm, "end": v(14.87, 7.98) * mm});
            skArc(sketch, "E4956", {"start": v(14.87, 7.98) * mm, "mid": v(14.76, 7.98) * mm, "end": v(14.66, 8.04) * mm});
            skArc(sketch, "E4957", {"start": v(14.66, 8.04) * mm, "mid": v(14.31, 8.4) * mm, "end": v(13.97, 8.78) * mm});
            skArc(sketch, "E4958", {"start": v(13.97, 8.78) * mm, "mid": v(13.58, 9.2) * mm, "end": v(13.17, 9.61) * mm});
            skArc(sketch, "E4959", {"start": v(13.17, 9.61) * mm, "mid": v(12.97, 9.76) * mm, "end": v(12.74, 9.84) * mm});
            skArc(sketch, "E4960", {"start": v(12.74, 9.84) * mm, "mid": v(12.6, 9.8) * mm, "end": v(12.53, 9.68) * mm});
            skArc(sketch, "E4961", {"start": v(12.53, 9.68) * mm, "mid": v(12.54, 9.37) * mm, "end": v(12.58, 9.06) * mm});
            skArc(sketch, "E4962", {"start": v(12.58, 9.06) * mm, "mid": v(12.62, 8.83) * mm, "end": v(12.65, 8.6) * mm});
            skArc(sketch, "E4963", {"start": v(12.65, 8.6) * mm, "mid": v(12.65, 8.5) * mm, "end": v(12.62, 8.38) * mm});
            skArc(sketch, "E4964", {"start": v(12.62, 8.38) * mm, "mid": v(12.56, 8.3) * mm, "end": v(12.48, 8.26) * mm});
            skArc(sketch, "E4965", {"start": v(12.48, 8.26) * mm, "mid": v(12.34, 8.24) * mm, "end": v(12.2, 8.23) * mm});
            skArc(sketch, "E4966", {"start": v(12.2, 8.23) * mm, "mid": v(12, 8.2) * mm, "end": v(11.8, 8.15) * mm});
            skArc(sketch, "E4967", {"start": v(11.8, 8.15) * mm, "mid": v(11.71, 8.07) * mm, "end": v(11.7, 7.95) * mm});
            skArc(sketch, "E4968", {"start": v(11.7, 7.95) * mm, "mid": v(11.77, 7.76) * mm, "end": v(11.89, 7.6) * mm});
            skArc(sketch, "E4969", {"start": v(11.89, 7.6) * mm, "mid": v(12.2, 7.27) * mm, "end": v(12.5, 6.97) * mm});
            skArc(sketch, "E4970", {"start": v(12.5, 6.97) * mm, "mid": v(12.82, 6.65) * mm, "end": v(13.1, 6.32) * mm});
            skArc(sketch, "E4971", {"start": v(13.1, 6.32) * mm, "mid": v(13.39, 5.95) * mm, "end": v(13.64, 5.57) * mm});
            skArc(sketch, "E4972", {"start": v(13.64, 5.57) * mm, "mid": v(13.85, 5.23) * mm, "end": v(14.03, 4.87) * mm});
            skArc(sketch, "E4973", {"start": v(14.03, 4.87) * mm, "mid": v(14.11, 4.64) * mm, "end": v(14.14, 4.39) * mm});
            skArc(sketch, "E4974", {"start": v(14.14, 4.39) * mm, "mid": v(14.12, 4.34) * mm, "end": v(14.07, 4.32) * mm});
            skArc(sketch, "E4975", {"start": v(14.07, 4.32) * mm, "mid": v(13.93, 4.35) * mm, "end": v(13.8, 4.39) * mm});
            skArc(sketch, "E4976", {"start": v(13.8, 4.39) * mm, "mid": v(13.6, 4.45) * mm, "end": v(13.42, 4.53) * mm});
            skArc(sketch, "E4977", {"start": v(13.42, 4.53) * mm, "mid": v(13.2, 4.64) * mm, "end": v(12.97, 4.76) * mm});
            skArc(sketch, "E4978", {"start": v(12.97, 4.76) * mm, "mid": v(12.7, 4.9) * mm, "end": v(12.4, 5.03) * mm});
            skArc(sketch, "E4979", {"start": v(12.4, 5.03) * mm, "mid": v(12.05, 5.18) * mm, "end": v(11.7, 5.31) * mm});
            skArc(sketch, "E4980", {"start": v(11.7, 5.31) * mm, "mid": v(11.32, 5.45) * mm, "end": v(10.94, 5.57) * mm});
            skArc(sketch, "E4981", {"start": v(10.94, 5.57) * mm, "mid": v(10.6, 5.67) * mm, "end": v(10.27, 5.75) * mm});
            skArc(sketch, "E4982", {"start": v(10.27, 5.75) * mm, "mid": v(9.68, 5.92) * mm, "end": v(9.1, 6.16) * mm});
            skArc(sketch, "E4983", {"start": v(9.1, 6.16) * mm, "mid": v(8.61, 6.43) * mm, "end": v(8.16, 6.77) * mm});
            skArc(sketch, "E4984", {"start": v(8.16, 6.77) * mm, "mid": v(7.77, 7.16) * mm, "end": v(7.45, 7.6) * mm});
            skArc(sketch, "E4985", {"start": v(7.45, 7.6) * mm, "mid": v(7.17, 8.11) * mm, "end": v(6.95, 8.65) * mm});
            skArc(sketch, "E4986", {"start": v(6.95, 8.65) * mm, "mid": v(6.81, 9) * mm, "end": v(6.64, 9.32) * mm});
            skArc(sketch, "E4987", {"start": v(6.64, 9.32) * mm, "mid": v(6.48, 9.5) * mm, "end": v(6.26, 9.6) * mm});
            skArc(sketch, "E4988", {"start": v(6.26, 9.6) * mm, "mid": v(6.08, 9.57) * mm, "end": v(5.96, 9.44) * mm});
            skArc(sketch, "E4989", {"start": v(5.96, 9.44) * mm, "mid": v(5.88, 9.18) * mm, "end": v(5.85, 8.9) * mm});
            skArc(sketch, "E4990", {"start": v(5.85, 8.9) * mm, "mid": v(5.82, 8.55) * mm, "end": v(5.75, 8.2) * mm});
            skArc(sketch, "E4991", {"start": v(5.75, 8.2) * mm, "mid": v(5.61, 7.82) * mm, "end": v(5.44, 7.44) * mm});
            skArc(sketch, "E4992", {"start": v(5.44, 7.44) * mm, "mid": v(5.25, 7.1) * mm, "end": v(5.03, 6.78) * mm});
            skArc(sketch, "E4993", {"start": v(5.03, 6.78) * mm, "mid": v(4.85, 6.6) * mm, "end": v(4.62, 6.47) * mm});
            skArc(sketch, "E4994", {"start": v(4.62, 6.47) * mm, "mid": v(4.43, 6.44) * mm, "end": v(4.25, 6.47) * mm});
            skArc(sketch, "E4995", {"start": v(4.25, 6.47) * mm, "mid": v(4.02, 6.58) * mm, "end": v(3.82, 6.72) * mm});
            skArc(sketch, "E4996", {"start": v(3.82, 6.72) * mm, "mid": v(3.63, 6.9) * mm, "end": v(3.48, 7.1) * mm});
            skArc(sketch, "E4997", {"start": v(3.48, 7.1) * mm, "mid": v(3.39, 7.3) * mm, "end": v(3.36, 7.51) * mm});
            skArc(sketch, "E4998", {"start": v(3.36, 7.51) * mm, "mid": v(3.35, 7.6) * mm, "end": v(3.32, 7.68) * mm});
            skArc(sketch, "E4999", {"start": v(3.32, 7.68) * mm, "mid": v(3.26, 7.8) * mm, "end": v(3.2, 7.9) * mm});
            skArc(sketch, "E5000", {"start": v(3.2, 7.9) * mm, "mid": v(3.11, 8.03) * mm, "end": v(3.02, 8.15) * mm});
            skArc(sketch, "E5001", {"start": v(3.02, 8.15) * mm, "mid": v(2.92, 8.26) * mm, "end": v(2.8, 8.37) * mm});
            skArc(sketch, "E5002", {"start": v(2.8, 8.37) * mm, "mid": v(2.59, 8.58) * mm, "end": v(2.38, 8.8) * mm});
            skArc(sketch, "E5003", {"start": v(2.38, 8.8) * mm, "mid": v(2.3, 8.93) * mm, "end": v(2.28, 9.08) * mm});
            skArc(sketch, "E5004", {"start": v(2.28, 9.08) * mm, "mid": v(2.33, 9.2) * mm, "end": v(2.43, 9.27) * mm});
            skArc(sketch, "E5005", {"start": v(2.43, 9.27) * mm, "mid": v(2.65, 9.34) * mm, "end": v(2.88, 9.38) * mm});
            skArc(sketch, "E5006", {"start": v(2.88, 9.38) * mm, "mid": v(3.05, 9.43) * mm, "end": v(3.22, 9.52) * mm});
            skArc(sketch, "E5007", {"start": v(3.22, 9.52) * mm, "mid": v(3.34, 9.63) * mm, "end": v(3.42, 9.78) * mm});
            skArc(sketch, "E5008", {"start": v(3.42, 9.78) * mm, "mid": v(3.5, 10.03) * mm, "end": v(3.54, 10.29) * mm});
            skArc(sketch, "E5009", {"start": v(3.54, 10.29) * mm, "mid": v(3.6, 10.87) * mm, "end": v(3.64, 11.46) * mm});
            skArc(sketch, "E5010", {"start": v(3.64, 11.46) * mm, "mid": v(3.67, 11.86) * mm, "end": v(3.71, 12.25) * mm});
            skArc(sketch, "E5011", {"start": v(3.71, 12.25) * mm, "mid": v(3.77, 12.61) * mm, "end": v(3.83, 12.97) * mm});
            skArc(sketch, "E5012", {"start": v(3.83, 12.97) * mm, "mid": v(3.9, 13.26) * mm, "end": v(3.98, 13.56) * mm});
            skArc(sketch, "E5013", {"start": v(3.98, 13.56) * mm, "mid": v(4.03, 13.69) * mm, "end": v(4.12, 13.8) * mm});
            skArc(sketch, "E5014", {"start": v(4.12, 13.8) * mm, "mid": v(4.19, 13.88) * mm, "end": v(4.25, 13.96) * mm});
            skArc(sketch, "E5015", {"start": v(4.25, 13.96) * mm, "mid": v(4.31, 14.06) * mm, "end": v(4.36, 14.16) * mm});
            skArc(sketch, "E5016", {"start": v(4.36, 14.16) * mm, "mid": v(4.4, 14.26) * mm, "end": v(4.44, 14.36) * mm});
            skArc(sketch, "E5017", {"start": v(4.44, 14.36) * mm, "mid": v(4.46, 14.45) * mm, "end": v(4.47, 14.54) * mm});
            skArc(sketch, "E5018", {"start": v(4.47, 14.54) * mm, "mid": v(4.44, 14.64) * mm, "end": v(4.37, 14.72) * mm});
            skArc(sketch, "E5019", {"start": v(4.37, 14.72) * mm, "mid": v(4.25, 14.79) * mm, "end": v(4.12, 14.82) * mm});
            skArc(sketch, "E5020", {"start": v(4.12, 14.82) * mm, "mid": v(3.89, 14.85) * mm, "end": v(3.65, 14.85) * mm});
            skArc(sketch, "E5021", {"start": v(3.65, 14.85) * mm, "mid": v(3.22, 14.84) * mm, "end": v(2.8, 14.8) * mm});
            skArc(sketch, "E5022", {"start": v(2.8, 14.8) * mm, "mid": v(2.43, 14.79) * mm, "end": v(2.06, 14.77) * mm});
            skArc(sketch, "E5023", {"start": v(2.06, 14.77) * mm, "mid": v(1.82, 14.77) * mm, "end": v(1.57, 14.8) * mm});
            skArc(sketch, "E5024", {"start": v(1.57, 14.8) * mm, "mid": v(1.43, 14.82) * mm, "end": v(1.3, 14.86) * mm});
            skArc(sketch, "E5025", {"start": v(1.3, 14.86) * mm, "mid": v(1.25, 14.91) * mm, "end": v(1.25, 14.98) * mm});
            skArc(sketch, "E5026", {"start": v(1.25, 14.98) * mm, "mid": v(1.42, 15.42) * mm, "end": v(1.59, 15.86) * mm});
            skArc(sketch, "E5027", {"start": v(1.59, 15.86) * mm, "mid": v(1.6, 16) * mm, "end": v(1.54, 16.11) * mm});
            skArc(sketch, "E5028", {"start": v(1.54, 16.11) * mm, "mid": v(1.42, 16.2) * mm, "end": v(1.28, 16.24) * mm});
            skArc(sketch, "E5029", {"start": v(1.28, 16.24) * mm, "mid": v(0.71, 16.26) * mm, "end": v(0.14, 16.27) * mm});
            skArc(sketch, "E5030", {"start": v(0.14, 16.27) * mm, "mid": v(-0.48, 16.3) * mm, "end": v(-1.1, 16.33) * mm});
            skArc(sketch, "E5031", {"start": v(-1.1, 16.33) * mm, "mid": v(-1.56, 16.38) * mm, "end": v(-2, 16.47) * mm});
            skArc(sketch, "E5032", {"start": v(-2, 16.47) * mm, "mid": v(-2.3, 16.55) * mm, "end": v(-2.6, 16.67) * mm});
            skArc(sketch, "E5033", {"start": v(-2.6, 16.67) * mm, "mid": v(-2.72, 16.78) * mm, "end": v(-2.78, 16.94) * mm});
            skArc(sketch, "E5034", {"start": v(-2.78, 16.94) * mm, "mid": v(-2.73, 17.17) * mm, "end": v(-2.56, 17.33) * mm});
            skArc(sketch, "E5035", {"start": v(-2.56, 17.33) * mm, "mid": v(-2, 17.63) * mm, "end": v(-1.43, 17.9) * mm});
            skArc(sketch, "E5036", {"start": v(-1.43, 17.9) * mm, "mid": v(-0.78, 18.16) * mm, "end": v(-0.11, 18.39) * mm});
            skArc(sketch, "E5037", {"start": v(-0.11, 18.39) * mm, "mid": v(0.48, 18.54) * mm, "end": v(1.09, 18.64) * mm});
            skArc(sketch, "E5038", {"start": v(1.09, 18.64) * mm, "mid": v(1.58, 18.71) * mm, "end": v(2.06, 18.82) * mm});
            skArc(sketch, "E5039", {"start": v(2.06, 18.82) * mm, "mid": v(2.29, 18.92) * mm, "end": v(2.46, 19.1) * mm});
            skArc(sketch, "E5040", {"start": v(2.46, 19.1) * mm, "mid": v(2.55, 19.34) * mm, "end": v(2.54, 19.6) * mm});
            skArc(sketch, "E5041", {"start": v(2.54, 19.6) * mm, "mid": v(2.42, 20.06) * mm, "end": v(2.26, 20.51) * mm});
            skArc(sketch, "E5042", {"start": v(2.26, 20.51) * mm, "mid": v(2.2, 20.7) * mm, "end": v(2.13, 20.9) * mm});
            skArc(sketch, "E5043", {"start": v(2.13, 20.9) * mm, "mid": v(2.12, 21) * mm, "end": v(2.13, 21.09) * mm});
            skArc(sketch, "E5044", {"start": v(2.13, 21.09) * mm, "mid": v(2.17, 21.15) * mm, "end": v(2.23, 21.19) * mm});
            skArc(sketch, "E5045", {"start": v(2.23, 21.19) * mm, "mid": v(2.35, 21.2) * mm, "end": v(2.47, 21.22) * mm});
            skArc(sketch, "E5046", {"start": v(2.47, 21.22) * mm, "mid": v(2.85, 21.18) * mm, "end": v(3.23, 21.07) * mm});
            skArc(sketch, "E5047", {"start": v(3.23, 21.07) * mm, "mid": v(3.77, 20.83) * mm, "end": v(4.3, 20.57) * mm});
            skArc(sketch, "E5048", {"start": v(4.3, 20.57) * mm, "mid": v(4.86, 20.25) * mm, "end": v(5.41, 19.9) * mm});
            skArc(sketch, "E5049", {"start": v(5.41, 19.9) * mm, "mid": v(5.9, 19.54) * mm, "end": v(6.37, 19.15) * mm});
            skArc(sketch, "E5050", {"start": v(6.37, 19.15) * mm, "mid": v(6.67, 18.88) * mm, "end": v(6.98, 18.61) * mm});
            skArc(sketch, "E5051", {"start": v(6.98, 18.61) * mm, "mid": v(7.14, 18.5) * mm, "end": v(7.32, 18.4) * mm});
            skArc(sketch, "E5052", {"start": v(7.32, 18.4) * mm, "mid": v(7.42, 18.38) * mm, "end": v(7.52, 18.4) * mm});
            skArc(sketch, "E5053", {"start": v(7.52, 18.4) * mm, "mid": v(7.61, 18.47) * mm, "end": v(7.67, 18.57) * mm});
            skArc(sketch, "E5054", {"start": v(7.67, 18.57) * mm, "mid": v(7.7, 18.67) * mm, "end": v(7.73, 18.79) * mm});
            skArc(sketch, "E5055", {"start": v(7.73, 18.79) * mm, "mid": v(7.74, 18.93) * mm, "end": v(7.74, 19.08) * mm});
            skArc(sketch, "E5056", {"start": v(7.74, 19.08) * mm, "mid": v(7.74, 19.24) * mm, "end": v(7.72, 19.4) * mm});
            skArc(sketch, "E5057", {"start": v(7.72, 19.4) * mm, "mid": v(7.7, 19.55) * mm, "end": v(7.67, 19.7) * mm});
            skArc(sketch, "E5058", {"start": v(7.67, 19.7) * mm, "mid": v(7.63, 19.87) * mm, "end": v(7.6, 20.04) * mm});
            skArc(sketch, "E5059", {"start": v(7.6, 20.04) * mm, "mid": v(7.6, 20.14) * mm, "end": v(7.63, 20.24) * mm});
            skArc(sketch, "E5060", {"start": v(7.63, 20.24) * mm, "mid": v(7.67, 20.3) * mm, "end": v(7.73, 20.35) * mm});
            skArc(sketch, "E5061", {"start": v(7.73, 20.35) * mm, "mid": v(7.83, 20.38) * mm, "end": v(7.93, 20.4) * mm});
            skArc(sketch, "E5062", {"start": v(7.93, 20.4) * mm, "mid": v(8.26, 20.36) * mm, "end": v(8.58, 20.25) * mm});
            skArc(sketch, "E5063", {"start": v(8.58, 20.25) * mm, "mid": v(9.2, 19.96) * mm, "end": v(9.8, 19.65) * mm});
            skArc(sketch, "E5064", {"start": v(9.8, 19.65) * mm, "mid": v(10.47, 19.28) * mm, "end": v(11.13, 18.88) * mm});
            skArc(sketch, "E5065", {"start": v(11.13, 18.88) * mm, "mid": v(11.72, 18.48) * mm, "end": v(12.3, 18.06) * mm});
            skArc(sketch, "E5066", {"start": v(12.3, 18.06) * mm, "mid": v(12.95, 17.58) * mm, "end": v(13.6, 17.11) * mm});
            skArc(sketch, "E5067", {"start": v(13.6, 17.11) * mm, "mid": v(13.8, 17.04) * mm, "end": v(14, 17.09) * mm});
            skArc(sketch, "E5068", {"start": v(14, 17.09) * mm, "mid": v(14.12, 17.23) * mm, "end": v(14.14, 17.42) * mm});
            skArc(sketch, "E5069", {"start": v(14.14, 17.42) * mm, "mid": v(13.96, 18.12) * mm, "end": v(13.76, 18.83) * mm});
            skArc(sketch, "E5070", {"start": v(13.76, 18.83) * mm, "mid": v(13.68, 19.07) * mm, "end": v(13.62, 19.32) * mm});
            skArc(sketch, "E5071", {"start": v(13.62, 19.32) * mm, "mid": v(13.57, 19.53) * mm, "end": v(13.53, 19.74) * mm});
            skArc(sketch, "E5072", {"start": v(13.53, 19.74) * mm, "mid": v(13.5, 19.9) * mm, "end": v(13.48, 20.06) * mm});
            skArc(sketch, "E5073", {"start": v(13.48, 20.06) * mm, "mid": v(13.5, 20.1) * mm, "end": v(13.53, 20.12) * mm});
            skArc(sketch, "E5074", {"start": v(13.53, 20.12) * mm, "mid": v(13.92, 20.07) * mm, "end": v(14.29, 19.93) * mm});
            skArc(sketch, "E5075", {"start": v(14.29, 19.93) * mm, "mid": v(15.34, 19.36) * mm, "end": v(16.39, 18.78) * mm});
            skArc(sketch, "E5076", {"start": v(16.39, 18.78) * mm, "mid": v(17.41, 18.18) * mm, "end": v(18.42, 17.56) * mm});
            skArc(sketch, "E5077", {"start": v(18.42, 17.56) * mm, "mid": v(19.03, 17.14) * mm, "end": v(19.6, 16.67) * mm});
            skArc(sketch, "E5078", {"start": v(19.6, 16.67) * mm, "mid": v(19.87, 16.43) * mm, "end": v(20.15, 16.2) * mm});
            skArc(sketch, "E5079", {"start": v(20.15, 16.2) * mm, "mid": v(20.4, 15.99) * mm, "end": v(20.64, 15.79) * mm});
            skArc(sketch, "E5080", {"start": v(20.64, 15.79) * mm, "mid": v(20.86, 15.62) * mm, "end": v(21.07, 15.46) * mm});
            skArc(sketch, "E5081", {"start": v(21.07, 15.46) * mm, "mid": v(21.13, 15.43) * mm, "end": v(21.2, 15.42) * mm});
            skArc(sketch, "E5082", {"start": v(21.2, 15.42) * mm, "mid": v(21.24, 15.43) * mm, "end": v(21.26, 15.48) * mm});
            skArc(sketch, "E5083", {"start": v(21.26, 15.48) * mm, "mid": v(21.29, 15.63) * mm, "end": v(21.3, 15.79) * mm});
            skArc(sketch, "E5084", {"start": v(21.3, 15.79) * mm, "mid": v(21.31, 15.99) * mm, "end": v(21.31, 16.2) * mm});
            skArc(sketch, "E5085", {"start": v(21.31, 16.2) * mm, "mid": v(21.3, 16.43) * mm, "end": v(21.29, 16.67) * mm});
            skArc(sketch, "E5086", {"start": v(21.29, 16.67) * mm, "mid": v(21.26, 17.08) * mm, "end": v(21.24, 17.48) * mm});
            skArc(sketch, "E5087", {"start": v(21.24, 17.48) * mm, "mid": v(21.25, 17.61) * mm, "end": v(21.3, 17.74) * mm});
            skArc(sketch, "E5088", {"start": v(21.3, 17.74) * mm, "mid": v(21.37, 17.8) * mm, "end": v(21.46, 17.83) * mm});
            skArc(sketch, "E5089", {"start": v(21.46, 17.83) * mm, "mid": v(21.67, 17.8) * mm, "end": v(21.88, 17.76) * mm});
            skArc(sketch, "E5090", {"start": v(21.88, 17.76) * mm, "mid": v(22.52, 17.57) * mm, "end": v(23.13, 17.32) * mm});
            skArc(sketch, "E5091", {"start": v(23.13, 17.32) * mm, "mid": v(23.92, 16.95) * mm, "end": v(24.68, 16.55) * mm});
            skArc(sketch, "E5092", {"start": v(24.68, 16.55) * mm, "mid": v(25.45, 16.1) * mm, "end": v(26.2, 15.63) * mm});
            skArc(sketch, "E5093", {"start": v(26.2, 15.63) * mm, "mid": v(26.8, 15.2) * mm, "end": v(27.36, 14.72) * mm});
            skArc(sketch, "E5094", {"start": v(27.36, 14.72) * mm, "mid": v(27.63, 14.48) * mm, "end": v(27.9, 14.25) * mm});
            skArc(sketch, "E5095", {"start": v(27.9, 14.25) * mm, "mid": v(28.14, 14.04) * mm, "end": v(28.4, 13.85) * mm});
            skArc(sketch, "E5096", {"start": v(28.4, 13.85) * mm, "mid": v(28.6, 13.68) * mm, "end": v(28.81, 13.52) * mm});
            skArc(sketch, "E5097", {"start": v(28.81, 13.52) * mm, "mid": v(28.87, 13.5) * mm, "end": v(28.94, 13.48) * mm});
            skArc(sketch, "E5098", {"start": v(28.94, 13.48) * mm, "mid": v(28.99, 13.5) * mm, "end": v(29, 13.55) * mm});
            skArc(sketch, "E5099", {"start": v(29, 13.55) * mm, "mid": v(29.02, 13.74) * mm, "end": v(29.02, 13.93) * mm});
            skArc(sketch, "E5100", {"start": v(29.02, 13.93) * mm, "mid": v(29.02, 14.17) * mm, "end": v(29, 14.42) * mm});
            skArc(sketch, "E5101", {"start": v(29, 14.42) * mm, "mid": v(28.98, 14.7) * mm, "end": v(28.95, 15) * mm});
            skArc(sketch, "E5102", {"start": v(28.95, 15) * mm, "mid": v(28.91, 15.3) * mm, "end": v(28.89, 15.58) * mm});
            skArc(sketch, "E5103", {"start": v(28.89, 15.58) * mm, "mid": v(28.87, 15.83) * mm, "end": v(28.87, 16.08) * mm});
            skArc(sketch, "E5104", {"start": v(28.87, 16.08) * mm, "mid": v(28.87, 16.27) * mm, "end": v(28.88, 16.46) * mm});
            skArc(sketch, "E5105", {"start": v(28.88, 16.46) * mm, "mid": v(28.9, 16.5) * mm, "end": v(28.95, 16.52) * mm});
            skArc(sketch, "E5106", {"start": v(28.95, 16.52) * mm, "mid": v(29.22, 16.49) * mm, "end": v(29.47, 16.39) * mm});
            skArc(sketch, "E5107", {"start": v(29.47, 16.39) * mm, "mid": v(30.24, 15.95) * mm, "end": v(31, 15.51) * mm});
            skArc(sketch, "E5108", {"start": v(31, 15.51) * mm, "mid": v(31.75, 15.06) * mm, "end": v(32.5, 14.59) * mm});
            skArc(sketch, "E5109", {"start": v(32.5, 14.59) * mm, "mid": v(32.99, 14.24) * mm, "end": v(33.46, 13.86) * mm});
            skArc(sketch, "E5110", {"start": v(33.46, 13.86) * mm, "mid": v(33.68, 13.68) * mm, "end": v(33.9, 13.5) * mm});
            skArc(sketch, "E5111", {"start": v(33.9, 13.5) * mm, "mid": v(34.1, 13.35) * mm, "end": v(34.32, 13.2) * mm});
            skArc(sketch, "E5112", {"start": v(34.32, 13.2) * mm, "mid": v(34.5, 13.09) * mm, "end": v(34.68, 12.97) * mm});
            skArc(sketch, "E5113", {"start": v(34.68, 12.97) * mm, "mid": v(34.77, 12.94) * mm, "end": v(34.86, 12.93) * mm});
            skArc(sketch, "E5114", {"start": v(34.86, 12.93) * mm, "mid": v(34.93, 12.95) * mm, "end": v(34.98, 13) * mm});
            skArc(sketch, "E5115", {"start": v(34.98, 13) * mm, "mid": v(35.03, 13.16) * mm, "end": v(35.07, 13.31) * mm});
            skArc(sketch, "E5116", {"start": v(35.07, 13.31) * mm, "mid": v(35.11, 13.53) * mm, "end": v(35.14, 13.75) * mm});
            skArc(sketch, "E5117", {"start": v(35.14, 13.75) * mm, "mid": v(35.15, 14.03) * mm, "end": v(35.16, 14.3) * mm});
            skArc(sketch, "E5118", {"start": v(35.16, 14.3) * mm, "mid": v(35.16, 14.62) * mm, "end": v(35.18, 14.92) * mm});
            skArc(sketch, "E5119", {"start": v(35.18, 14.92) * mm, "mid": v(35.2, 15.14) * mm, "end": v(35.24, 15.35) * mm});
            skArc(sketch, "E5120", {"start": v(35.24, 15.35) * mm, "mid": v(35.29, 15.48) * mm, "end": v(35.35, 15.6) * mm});
            skArc(sketch, "E5121", {"start": v(35.35, 15.6) * mm, "mid": v(35.42, 15.66) * mm, "end": v(35.5, 15.68) * mm});
            skArc(sketch, "E5122", {"start": v(35.5, 15.68) * mm, "mid": v(36.02, 15.62) * mm, "end": v(36.51, 15.48) * mm});
            skArc(sketch, "E5123", {"start": v(36.51, 15.48) * mm, "mid": v(37.62, 15.02) * mm, "end": v(38.71, 14.55) * mm});
            skArc(sketch, "E5124", {"start": v(38.71, 14.55) * mm, "mid": v(39.83, 14.04) * mm, "end": v(40.94, 13.5) * mm});
            skArc(sketch, "E5125", {"start": v(40.94, 13.5) * mm, "mid": v(41.75, 13.06) * mm, "end": v(42.53, 12.57) * mm});
            skArc(sketch, "E5126", {"start": v(42.53, 12.57) * mm, "mid": v(42.92, 12.32) * mm, "end": v(43.3, 12.07) * mm});
            skArc(sketch, "E5127", {"start": v(43.3, 12.07) * mm, "mid": v(43.65, 11.86) * mm, "end": v(44, 11.65) * mm});
            skArc(sketch, "E5128", {"start": v(44, 11.65) * mm, "mid": v(44.3, 11.48) * mm, "end": v(44.6, 11.32) * mm});
            skArc(sketch, "E5129", {"start": v(44.6, 11.32) * mm, "mid": v(44.7, 11.28) * mm, "end": v(44.8, 11.27) * mm});
            skArc(sketch, "E5130", {"start": v(44.8, 11.27) * mm, "mid": v(45.07, 11.4) * mm, "end": v(45.13, 11.7) * mm});
            skArc(sketch, "E5131", {"start": v(45.13, 11.7) * mm, "mid": v(44.84, 12.77) * mm, "end": v(44.5, 13.83) * mm});
            skArc(sketch, "E5132", {"start": v(44.5, 13.83) * mm, "mid": v(44.07, 15.04) * mm, "end": v(43.56, 16.22) * mm});
            skArc(sketch, "E5133", {"start": v(43.56, 16.22) * mm, "mid": v(43.04, 17.26) * mm, "end": v(42.44, 18.26) * mm});
            skArc(sketch, "E5134", {"start": v(42.44, 18.26) * mm, "mid": v(42, 18.97) * mm, "end": v(41.58, 19.69) * mm});
            skArc(sketch, "E5135", {"start": v(41.58, 19.69) * mm, "mid": v(41.52, 19.94) * mm, "end": v(41.58, 20.2) * mm});
            skArc(sketch, "E5136", {"start": v(41.58, 20.2) * mm, "mid": v(41.77, 20.37) * mm, "end": v(42.02, 20.42) * mm});
            skArc(sketch, "E5137", {"start": v(42.02, 20.42) * mm, "mid": v(42.81, 20.37) * mm, "end": v(43.6, 20.29) * mm});
            skArc(sketch, "E5138", {"start": v(43.6, 20.29) * mm, "mid": v(43.94, 20.25) * mm, "end": v(44.27, 20.23) * mm});
            skArc(sketch, "E5139", {"start": v(44.27, 20.23) * mm, "mid": v(44.5, 20.22) * mm, "end": v(44.73, 20.23) * mm});
            skArc(sketch, "E5140", {"start": v(44.73, 20.23) * mm, "mid": v(44.88, 20.25) * mm, "end": v(45.02, 20.29) * mm});
            skArc(sketch, "E5141", {"start": v(45.02, 20.29) * mm, "mid": v(45.09, 20.34) * mm, "end": v(45.11, 20.41) * mm});
            skArc(sketch, "E5142", {"start": v(45.11, 20.41) * mm, "mid": v(45.06, 20.76) * mm, "end": v(44.92, 21.09) * mm});
            skArc(sketch, "E5143", {"start": v(44.92, 21.09) * mm, "mid": v(44.54, 21.7) * mm, "end": v(44.14, 22.3) * mm});
            skArc(sketch, "E5144", {"start": v(44.14, 22.3) * mm, "mid": v(43.65, 22.96) * mm, "end": v(43.12, 23.6) * mm});
            skArc(sketch, "E5145", {"start": v(43.12, 23.6) * mm, "mid": v(42.59, 24.2) * mm, "end": v(42.02, 24.76) * mm});
            skLineSegment(sketch, "E5146", {"start": v(42.02, 24.76) * mm, "end": v(40.4, 26.34) * mm});
            skLineSegment(sketch, "E5147", {"start": v(40.4, 26.34) * mm, "end": v(41.16, 26.51) * mm});
            skArc(sketch, "E5148", {"start": v(41.16, 26.51) * mm, "mid": v(42.08, 26.67) * mm, "end": v(43.02, 26.72) * mm});
            skArc(sketch, "E5149", {"start": v(43.02, 26.72) * mm, "mid": v(44.16, 26.67) * mm, "end": v(45.3, 26.56) * mm});
            skArc(sketch, "E5150", {"start": v(45.3, 26.56) * mm, "mid": v(46.38, 26.38) * mm, "end": v(47.45, 26.14) * mm});
            skArc(sketch, "E5151", {"start": v(47.45, 26.14) * mm, "mid": v(48.2, 25.87) * mm, "end": v(48.9, 25.5) * mm});
            skArc(sketch, "E5152", {"start": v(48.9, 25.5) * mm, "mid": v(49.22, 25.3) * mm, "end": v(49.56, 25.16) * mm});
            skArc(sketch, "E5153", {"start": v(49.56, 25.16) * mm, "mid": v(49.75, 25.16) * mm, "end": v(49.9, 25.27) * mm});
            skArc(sketch, "E5154", {"start": v(49.9, 25.27) * mm, "mid": v(50.01, 25.51) * mm, "end": v(50.06, 25.78) * mm});
            skArc(sketch, "E5155", {"start": v(50.06, 25.78) * mm, "mid": v(50.08, 26.54) * mm, "end": v(50.09, 27.3) * mm});
            skArc(sketch, "E5156", {"start": v(50.09, 27.3) * mm, "mid": v(50.08, 27.92) * mm, "end": v(50.07, 28.55) * mm});
            skArc(sketch, "E5157", {"start": v(50.07, 28.55) * mm, "mid": v(50.04, 28.9) * mm, "end": v(49.98, 29.24) * mm});
            skArc(sketch, "E5158", {"start": v(49.98, 29.24) * mm, "mid": v(49.9, 29.5) * mm, "end": v(49.78, 29.73) * mm});
            skArc(sketch, "E5159", {"start": v(49.78, 29.73) * mm, "mid": v(49.61, 29.98) * mm, "end": v(49.42, 30.2) * mm});
            skArc(sketch, "E5160", {"start": v(49.42, 30.2) * mm, "mid": v(49.28, 30.38) * mm, "end": v(49.15, 30.55) * mm});
            skArc(sketch, "E5161", {"start": v(49.15, 30.55) * mm, "mid": v(49, 30.78) * mm, "end": v(48.88, 31) * mm});
            skArc(sketch, "E5162", {"start": v(48.88, 31) * mm, "mid": v(48.76, 31.24) * mm, "end": v(48.66, 31.47) * mm});
            skArc(sketch, "E5163", {"start": v(48.66, 31.47) * mm, "mid": v(48.58, 31.68) * mm, "end": v(48.52, 31.9) * mm});
            skLineSegment(sketch, "E5164", {"start": v(48.52, 31.9) * mm, "end": v(48.3, 32.87) * mm});
            skLineSegment(sketch, "E5165", {"start": v(48.3, 32.87) * mm, "end": v(44.7, 32.94) * mm});
            skArc(sketch, "E5166", {"start": v(44.7, 32.94) * mm, "mid": v(43.73, 32.96) * mm, "end": v(42.76, 33) * mm});
            skArc(sketch, "E5167", {"start": v(42.76, 33) * mm, "mid": v(42.14, 33.04) * mm, "end": v(41.52, 33.1) * mm});
            skArc(sketch, "E5168", {"start": v(41.52, 33.1) * mm, "mid": v(41.04, 33.18) * mm, "end": v(40.57, 33.3) * mm});
            skArc(sketch, "E5169", {"start": v(40.57, 33.3) * mm, "mid": v(40.12, 33.43) * mm, "end": v(39.67, 33.6) * mm});
            skLineSegment(sketch, "E5170", {"start": v(39.67, 33.6) * mm, "end": v(38.25, 34.2) * mm});
            skLineSegment(sketch, "E5171", {"start": v(38.25, 34.2) * mm, "end": v(36.77, 31.23) * mm});
            skArc(sketch, "E5172", {"start": v(36.77, 31.23) * mm, "mid": v(36.34, 30.4) * mm, "end": v(35.9, 29.56) * mm});
            skArc(sketch, "E5173", {"start": v(35.9, 29.56) * mm, "mid": v(35.63, 29.1) * mm, "end": v(35.33, 28.64) * mm});
            skArc(sketch, "E5174", {"start": v(35.33, 28.64) * mm, "mid": v(35.06, 28.31) * mm, "end": v(34.75, 28.01) * mm});
            skArc(sketch, "E5175", {"start": v(34.75, 28.01) * mm, "mid": v(34.39, 27.71) * mm, "end": v(34, 27.44) * mm});
            skArc(sketch, "E5176", {"start": v(34, 27.44) * mm, "mid": v(33.51, 27.1) * mm, "end": v(33.06, 26.73) * mm});
            skArc(sketch, "E5177", {"start": v(33.06, 26.73) * mm, "mid": v(32.82, 26.43) * mm, "end": v(32.68, 26.08) * mm});
            skArc(sketch, "E5178", {"start": v(32.68, 26.08) * mm, "mid": v(32.68, 25.81) * mm, "end": v(32.83, 25.59) * mm});
            skArc(sketch, "E5179", {"start": v(32.83, 25.59) * mm, "mid": v(33.13, 25.4) * mm, "end": v(33.46, 25.28) * mm});
            skArc(sketch, "E5180", {"start": v(33.46, 25.28) * mm, "mid": v(33.66, 25.23) * mm, "end": v(33.86, 25.16) * mm});
            skArc(sketch, "E5181", {"start": v(33.86, 25.16) * mm, "mid": v(34, 25.08) * mm, "end": v(34.12, 24.98) * mm});
            skArc(sketch, "E5182", {"start": v(34.12, 24.98) * mm, "mid": v(34.22, 24.85) * mm, "end": v(34.3, 24.7) * mm});
            skArc(sketch, "E5183", {"start": v(34.3, 24.7) * mm, "mid": v(34.37, 24.5) * mm, "end": v(34.42, 24.28) * mm});
            skArc(sketch, "E5184", {"start": v(34.42, 24.28) * mm, "mid": v(34.46, 24.12) * mm, "end": v(34.51, 23.96) * mm});
            skArc(sketch, "E5185", {"start": v(34.51, 23.96) * mm, "mid": v(34.57, 23.82) * mm, "end": v(34.64, 23.68) * mm});
            skArc(sketch, "E5186", {"start": v(34.64, 23.68) * mm, "mid": v(34.71, 23.58) * mm, "end": v(34.8, 23.5) * mm});
            skArc(sketch, "E5187", {"start": v(34.8, 23.5) * mm, "mid": v(34.86, 23.45) * mm, "end": v(34.94, 23.43) * mm});
            skArc(sketch, "E5188", {"start": v(34.94, 23.43) * mm, "mid": v(35.05, 23.4) * mm, "end": v(35.11, 23.31) * mm});
            skArc(sketch, "E5189", {"start": v(35.11, 23.31) * mm, "mid": v(35.17, 23.1) * mm, "end": v(35.22, 22.9) * mm});
            skArc(sketch, "E5190", {"start": v(35.22, 22.9) * mm, "mid": v(35.26, 22.54) * mm, "end": v(35.28, 22.19) * mm});
            skArc(sketch, "E5191", {"start": v(35.28, 22.19) * mm, "mid": v(35.29, 21.61) * mm, "end": v(35.3, 21.03) * mm});
            skArc(sketch, "E5192", {"start": v(35.3, 21.03) * mm, "mid": v(35.29, 20.26) * mm, "end": v(35.27, 19.48) * mm});
            skArc(sketch, "E5193", {"start": v(35.27, 19.48) * mm, "mid": v(35.25, 19.18) * mm, "end": v(35.18, 18.88) * mm});
            skArc(sketch, "E5194", {"start": v(35.18, 18.88) * mm, "mid": v(35.1, 18.68) * mm, "end": v(34.95, 18.5) * mm});
            skArc(sketch, "E5195", {"start": v(34.95, 18.5) * mm, "mid": v(34.72, 18.3) * mm, "end": v(34.46, 18.13) * mm});
            skArc(sketch, "E5196", {"start": v(34.46, 18.13) * mm, "mid": v(34.27, 18.03) * mm, "end": v(34.08, 17.94) * mm});
            skArc(sketch, "E5197", {"start": v(34.08, 17.94) * mm, "mid": v(33.84, 17.85) * mm, "end": v(33.6, 17.78) * mm});
            skArc(sketch, "E5198", {"start": v(33.6, 17.78) * mm, "mid": v(33.35, 17.72) * mm, "end": v(33.1, 17.67) * mm});
            skArc(sketch, "E5199", {"start": v(33.1, 17.67) * mm, "mid": v(32.88, 17.64) * mm, "end": v(32.66, 17.63) * mm});
            skArc(sketch, "E5200", {"start": v(32.66, 17.63) * mm, "mid": v(31.85, 17.72) * mm, "end": v(31.08, 18) * mm});
            skArc(sketch, "E5201", {"start": v(31.08, 18) * mm, "mid": v(30.33, 18.44) * mm, "end": v(29.68, 19.03) * mm});
            skArc(sketch, "E5202", {"start": v(29.68, 19.03) * mm, "mid": v(29.02, 19.85) * mm, "end": v(28.48, 20.77) * mm});
            skArc(sketch, "E5203", {"start": v(28.48, 20.77) * mm, "mid": v(27.94, 21.98) * mm, "end": v(27.5, 23.23) * mm});
            skArc(sketch, "E5204", {"start": v(27.5, 23.23) * mm, "mid": v(27.23, 24) * mm, "end": v(26.94, 24.78) * mm});
            skArc(sketch, "E5205", {"start": v(26.94, 24.78) * mm, "mid": v(26.74, 25.17) * mm, "end": v(26.47, 25.52) * mm});
            skArc(sketch, "E5206", {"start": v(26.47, 25.52) * mm, "mid": v(26.3, 25.58) * mm, "end": v(26.17, 25.47) * mm});
            skArc(sketch, "E5207", {"start": v(26.17, 25.47) * mm, "mid": v(26.07, 25.15) * mm, "end": v(26.03, 24.8) * mm});
            skArc(sketch, "E5208", {"start": v(26.03, 24.8) * mm, "mid": v(25.94, 23.92) * mm, "end": v(25.68, 23.07) * mm});
            skArc(sketch, "E5209", {"start": v(25.68, 23.07) * mm, "mid": v(25.24, 22.2) * mm, "end": v(24.66, 21.43) * mm});
            skArc(sketch, "E5210", {"start": v(24.66, 21.43) * mm, "mid": v(24, 20.78) * mm, "end": v(23.25, 20.25) * mm});
            skArc(sketch, "E5211", {"start": v(23.25, 20.25) * mm, "mid": v(22.53, 19.94) * mm, "end": v(21.75, 19.84) * mm});
            skArc(sketch, "E5212", {"start": v(21.75, 19.84) * mm, "mid": v(21.33, 19.88) * mm, "end": v(20.92, 19.98) * mm});
            skArc(sketch, "E5213", {"start": v(20.92, 19.98) * mm, "mid": v(20.4, 20.2) * mm, "end": v(19.9, 20.44) * mm});
            skArc(sketch, "E5214", {"start": v(19.9, 20.44) * mm, "mid": v(19.38, 20.74) * mm, "end": v(18.88, 21.08) * mm});
            skArc(sketch, "E5215", {"start": v(18.88, 21.08) * mm, "mid": v(18.44, 21.44) * mm, "end": v(18.04, 21.83) * mm});
            skArc(sketch, "E5216", {"start": v(18.04, 21.83) * mm, "mid": v(17.24, 22.81) * mm, "end": v(16.57, 23.89) * mm});
            skArc(sketch, "E5217", {"start": v(16.57, 23.89) * mm, "mid": v(15.98, 25.12) * mm, "end": v(15.52, 26.41) * mm});
            skArc(sketch, "E5218", {"start": v(15.52, 26.41) * mm, "mid": v(15.11, 28.02) * mm, "end": v(14.83, 29.66) * mm});
            skArc(sketch, "E5219", {"start": v(14.83, 29.66) * mm, "mid": v(14.59, 31.8) * mm, "end": v(14.42, 33.94) * mm});
            skArc(sketch, "E5220", {"start": v(14.42, 33.94) * mm, "mid": v(14.31, 35.64) * mm, "end": v(14.16, 37.34) * mm});
            skArc(sketch, "E5221", {"start": v(14.16, 37.34) * mm, "mid": v(14.02, 38.5) * mm, "end": v(13.8, 39.64) * mm});
            skArc(sketch, "E5222", {"start": v(13.8, 39.64) * mm, "mid": v(13.52, 40.78) * mm, "end": v(13.17, 41.9) * mm});
            skArc(sketch, "E5223", {"start": v(13.17, 41.9) * mm, "mid": v(12.58, 43.56) * mm, "end": v(11.96, 45.2) * mm});
            skArc(sketch, "E5224", {"start": v(11.96, 45.2) * mm, "mid": v(11.7, 45.89) * mm, "end": v(11.44, 46.57) * mm});
            skArc(sketch, "E5225", {"start": v(11.44, 46.57) * mm, "mid": v(11.23, 47.15) * mm, "end": v(11.02, 47.73) * mm});
            skArc(sketch, "E5226", {"start": v(11.02, 47.73) * mm, "mid": v(10.85, 48.24) * mm, "end": v(10.67, 48.74) * mm});
            skArc(sketch, "E5227", {"start": v(10.67, 48.74) * mm, "mid": v(10.67, 48.8) * mm, "end": v(10.7, 48.84) * mm});
            skArc(sketch, "E5228", {"start": v(10.7, 48.84) * mm, "mid": v(10.86, 48.9) * mm, "end": v(11.02, 48.85) * mm});
            skArc(sketch, "E5229", {"start": v(11.02, 48.85) * mm, "mid": v(11.42, 48.48) * mm, "end": v(11.8, 48.1) * mm});
            skArc(sketch, "E5230", {"start": v(11.8, 48.1) * mm, "mid": v(12.22, 47.63) * mm, "end": v(12.61, 47.14) * mm});
            skArc(sketch, "E5231", {"start": v(12.61, 47.14) * mm, "mid": v(12.94, 46.67) * mm, "end": v(13.23, 46.18) * mm});
            skArc(sketch, "E5232", {"start": v(13.23, 46.18) * mm, "mid": v(13.38, 45.9) * mm, "end": v(13.54, 45.62) * mm});
            skArc(sketch, "E5233", {"start": v(13.54, 45.62) * mm, "mid": v(13.69, 45.38) * mm, "end": v(13.84, 45.15) * mm});
            skArc(sketch, "E5234", {"start": v(13.84, 45.15) * mm, "mid": v(13.97, 44.97) * mm, "end": v(14.1, 44.78) * mm});
            skArc(sketch, "E5235", {"start": v(14.1, 44.78) * mm, "mid": v(14.15, 44.74) * mm, "end": v(14.22, 44.73) * mm});
            skArc(sketch, "E5236", {"start": v(14.22, 44.73) * mm, "mid": v(14.27, 44.74) * mm, "end": v(14.32, 44.77) * mm});
            skArc(sketch, "E5237", {"start": v(14.32, 44.77) * mm, "mid": v(14.4, 44.85) * mm, "end": v(14.46, 44.93) * mm});
            skArc(sketch, "E5238", {"start": v(14.46, 44.93) * mm, "mid": v(14.54, 45.04) * mm, "end": v(14.6, 45.15) * mm});
            skArc(sketch, "E5239", {"start": v(14.6, 45.15) * mm, "mid": v(14.68, 45.28) * mm, "end": v(14.75, 45.42) * mm});
            skArc(sketch, "E5240", {"start": v(14.75, 45.42) * mm, "mid": v(14.81, 45.55) * mm, "end": v(14.88, 45.68) * mm});
            skArc(sketch, "E5241", {"start": v(14.88, 45.68) * mm, "mid": v(14.95, 45.8) * mm, "end": v(15.03, 45.9) * mm});
            skArc(sketch, "E5242", {"start": v(15.03, 45.9) * mm, "mid": v(15.1, 45.99) * mm, "end": v(15.18, 46.07) * mm});
            skArc(sketch, "E5243", {"start": v(15.18, 46.07) * mm, "mid": v(15.22, 46.1) * mm, "end": v(15.28, 46.1) * mm});
            skArc(sketch, "E5244", {"start": v(15.28, 46.1) * mm, "mid": v(15.5, 46.05) * mm, "end": v(15.69, 45.9) * mm});
            skArc(sketch, "E5245", {"start": v(15.69, 45.9) * mm, "mid": v(16.02, 45.45) * mm, "end": v(16.32, 44.98) * mm});
            skArc(sketch, "E5246", {"start": v(16.32, 44.98) * mm, "mid": v(16.64, 44.42) * mm, "end": v(16.93, 43.85) * mm});
            skArc(sketch, "E5247", {"start": v(16.93, 43.85) * mm, "mid": v(17.16, 43.29) * mm, "end": v(17.36, 42.72) * mm});
            skArc(sketch, "E5248", {"start": v(17.36, 42.72) * mm, "mid": v(17.54, 42.17) * mm, "end": v(17.75, 41.64) * mm});
            skArc(sketch, "E5249", {"start": v(17.75, 41.64) * mm, "mid": v(17.9, 41.4) * mm, "end": v(18.11, 41.2) * mm});
            skArc(sketch, "E5250", {"start": v(18.11, 41.2) * mm, "mid": v(18.29, 41.18) * mm, "end": v(18.43, 41.28) * mm});
            skArc(sketch, "E5251", {"start": v(18.43, 41.28) * mm, "mid": v(18.59, 41.56) * mm, "end": v(18.7, 41.87) * mm});
            skLineSegment(sketch, "E5252", {"start": v(18.7, 41.87) * mm, "end": v(18.88, 42.6) * mm});
            skLineSegment(sketch, "E5253", {"start": v(18.88, 42.6) * mm, "end": v(19.68, 41.4) * mm});
            skArc(sketch, "E5254", {"start": v(19.68, 41.4) * mm, "mid": v(19.85, 41.12) * mm, "end": v(20.01, 40.84) * mm});
            skArc(sketch, "E5255", {"start": v(20.01, 40.84) * mm, "mid": v(20.18, 40.5) * mm, "end": v(20.34, 40.15) * mm});
            skArc(sketch, "E5256", {"start": v(20.34, 40.15) * mm, "mid": v(20.5, 39.8) * mm, "end": v(20.63, 39.46) * mm});
            skArc(sketch, "E5257", {"start": v(20.63, 39.46) * mm, "mid": v(20.73, 39.16) * mm, "end": v(20.82, 38.86) * mm});
            skArc(sketch, "E5258", {"start": v(20.82, 38.86) * mm, "mid": v(20.95, 38.41) * mm, "end": v(21.09, 37.97) * mm});
            skArc(sketch, "E5259", {"start": v(21.09, 37.97) * mm, "mid": v(21.2, 37.77) * mm, "end": v(21.35, 37.62) * mm});
            skArc(sketch, "E5260", {"start": v(21.35, 37.62) * mm, "mid": v(21.5, 37.57) * mm, "end": v(21.65, 37.63) * mm});
            skArc(sketch, "E5261", {"start": v(21.65, 37.63) * mm, "mid": v(21.86, 37.8) * mm, "end": v(22.04, 38.02) * mm});
            skArc(sketch, "E5262", {"start": v(22.04, 38.02) * mm, "mid": v(22.15, 38.16) * mm, "end": v(22.26, 38.29) * mm});
            skArc(sketch, "E5263", {"start": v(22.26, 38.29) * mm, "mid": v(22.33, 38.34) * mm, "end": v(22.42, 38.35) * mm});
            skArc(sketch, "E5264", {"start": v(22.42, 38.35) * mm, "mid": v(22.52, 38.33) * mm, "end": v(22.6, 38.28) * mm});
            skArc(sketch, "E5265", {"start": v(22.6, 38.28) * mm, "mid": v(22.78, 38.13) * mm, "end": v(22.96, 37.98) * mm});
            skArc(sketch, "E5266", {"start": v(22.96, 37.98) * mm, "mid": v(23.08, 37.87) * mm, "end": v(23.19, 37.74) * mm});
            skArc(sketch, "E5267", {"start": v(23.19, 37.74) * mm, "mid": v(23.3, 37.6) * mm, "end": v(23.41, 37.46) * mm});
            skArc(sketch, "E5268", {"start": v(23.41, 37.46) * mm, "mid": v(23.5, 37.32) * mm, "end": v(23.6, 37.18) * mm});
            skArc(sketch, "E5269", {"start": v(23.6, 37.18) * mm, "mid": v(23.65, 37.07) * mm, "end": v(23.7, 36.95) * mm});
            skArc(sketch, "E5270", {"start": v(23.7, 36.95) * mm, "mid": v(23.78, 36.75) * mm, "end": v(23.92, 36.58) * mm});
            skArc(sketch, "E5271", {"start": v(23.92, 36.58) * mm, "mid": v(24.07, 36.48) * mm, "end": v(24.25, 36.44) * mm});
            skArc(sketch, "E5272", {"start": v(24.25, 36.44) * mm, "mid": v(24.41, 36.49) * mm, "end": v(24.54, 36.6) * mm});
            skArc(sketch, "E5273", {"start": v(24.54, 36.6) * mm, "mid": v(24.62, 36.77) * mm, "end": v(24.65, 36.97) * mm});
            skArc(sketch, "E5274", {"start": v(24.65, 36.97) * mm, "mid": v(24.65, 37.08) * mm, "end": v(24.67, 37.18) * mm});
            skArc(sketch, "E5275", {"start": v(24.67, 37.18) * mm, "mid": v(24.7, 37.29) * mm, "end": v(24.72, 37.4) * mm});
            skArc(sketch, "E5276", {"start": v(24.72, 37.4) * mm, "mid": v(24.76, 37.48) * mm, "end": v(24.8, 37.56) * mm});
            skArc(sketch, "E5277", {"start": v(24.8, 37.56) * mm, "mid": v(24.85, 37.62) * mm, "end": v(24.9, 37.66) * mm});
            skArc(sketch, "E5278", {"start": v(24.9, 37.66) * mm, "mid": v(25.06, 37.7) * mm, "end": v(25.2, 37.63) * mm});
            skArc(sketch, "E5279", {"start": v(25.2, 37.63) * mm, "mid": v(25.54, 37.3) * mm, "end": v(25.86, 36.96) * mm});
            skArc(sketch, "E5280", {"start": v(25.86, 36.96) * mm, "mid": v(26.2, 36.57) * mm, "end": v(26.5, 36.15) * mm});
            skArc(sketch, "E5281", {"start": v(26.5, 36.15) * mm, "mid": v(26.74, 35.78) * mm, "end": v(26.94, 35.4) * mm});
            skArc(sketch, "E5282", {"start": v(26.94, 35.4) * mm, "mid": v(27.07, 35.17) * mm, "end": v(27.23, 34.96) * mm});
            skArc(sketch, "E5283", {"start": v(27.23, 34.96) * mm, "mid": v(27.36, 34.88) * mm, "end": v(27.52, 34.88) * mm});
            skArc(sketch, "E5284", {"start": v(27.52, 34.88) * mm, "mid": v(27.66, 34.96) * mm, "end": v(27.73, 35.1) * mm});
            skArc(sketch, "E5285", {"start": v(27.73, 35.1) * mm, "mid": v(27.76, 35.37) * mm, "end": v(27.74, 35.63) * mm});
            skArc(sketch, "E5286", {"start": v(27.74, 35.63) * mm, "mid": v(27.1, 38.63) * mm, "end": v(25.95, 41.48) * mm});
            skArc(sketch, "E5287", {"start": v(25.95, 41.48) * mm, "mid": v(24.23, 44.41) * mm, "end": v(22.15, 47.11) * mm});
            skArc(sketch, "E5288", {"start": v(22.15, 47.11) * mm, "mid": v(19.78, 49.5) * mm, "end": v(17.14, 51.55) * mm});
            skArc(sketch, "E5289", {"start": v(17.14, 51.55) * mm, "mid": v(14.56, 52.97) * mm, "end": v(11.77, 53.88) * mm});
            skArc(sketch, "E5290", {"start": v(11.77, 53.88) * mm, "mid": v(11.23, 54.02) * mm, "end": v(10.7, 54.2) * mm});
            skArc(sketch, "E5291", {"start": v(10.7, 54.2) * mm, "mid": v(10.46, 54.36) * mm, "end": v(10.3, 54.6) * mm});
            skArc(sketch, "E5292", {"start": v(10.3, 54.6) * mm, "mid": v(10.27, 54.9) * mm, "end": v(10.36, 55.16) * mm});
            skArc(sketch, "E5293", {"start": v(10.36, 55.16) * mm, "mid": v(10.66, 55.62) * mm, "end": v(11, 56.05) * mm});
            skArc(sketch, "E5294", {"start": v(11, 56.05) * mm, "mid": v(11.18, 56.28) * mm, "end": v(11.36, 56.52) * mm});
            skArc(sketch, "E5295", {"start": v(11.36, 56.52) * mm, "mid": v(11.45, 56.66) * mm, "end": v(11.51, 56.82) * mm});
            skArc(sketch, "E5296", {"start": v(11.51, 56.82) * mm, "mid": v(11.53, 56.95) * mm, "end": v(11.5, 57.07) * mm});
            skArc(sketch, "E5297", {"start": v(11.5, 57.07) * mm, "mid": v(11.44, 57.2) * mm, "end": v(11.36, 57.33) * mm});
            skArc(sketch, "E5298", {"start": v(11.36, 57.33) * mm, "mid": v(11.05, 57.65) * mm, "end": v(10.7, 57.92) * mm});
            skArc(sketch, "E5299", {"start": v(10.7, 57.92) * mm, "mid": v(10.17, 58.24) * mm, "end": v(9.63, 58.53) * mm});
            skArc(sketch, "E5300", {"start": v(9.63, 58.53) * mm, "mid": v(9.05, 58.8) * mm, "end": v(8.46, 59.03) * mm});
            skArc(sketch, "E5301", {"start": v(8.46, 59.03) * mm, "mid": v(7.94, 59.18) * mm, "end": v(7.42, 59.28) * mm});
            skArc(sketch, "E5302", {"start": v(7.42, 59.28) * mm, "mid": v(7.17, 59.31) * mm, "end": v(6.92, 59.35) * mm});
            skArc(sketch, "E5303", {"start": v(6.92, 59.35) * mm, "mid": v(6.71, 59.4) * mm, "end": v(6.5, 59.43) * mm});
            skArc(sketch, "E5304", {"start": v(6.5, 59.43) * mm, "mid": v(6.33, 59.47) * mm, "end": v(6.16, 59.52) * mm});
            skArc(sketch, "E5305", {"start": v(6.16, 59.52) * mm, "mid": v(6.13, 59.53) * mm, "end": v(6.12, 59.56) * mm});
            skArc(sketch, "E5306", {"start": v(6.12, 59.56) * mm, "mid": v(6.15, 59.81) * mm, "end": v(6.23, 60.05) * mm});
            skArc(sketch, "E5307", {"start": v(6.23, 60.05) * mm, "mid": v(6.44, 60.46) * mm, "end": v(6.66, 60.86) * mm});
            skArc(sketch, "E5308", {"start": v(6.66, 60.86) * mm, "mid": v(6.9, 61.27) * mm, "end": v(7.17, 61.67) * mm});
            skArc(sketch, "E5309", {"start": v(7.17, 61.67) * mm, "mid": v(7.4, 61.95) * mm, "end": v(7.65, 62.21) * mm});
            skArc(sketch, "E5310", {"start": v(7.65, 62.21) * mm, "mid": v(7.88, 62.45) * mm, "end": v(8.09, 62.72) * mm});
            skArc(sketch, "E5311", {"start": v(8.09, 62.72) * mm, "mid": v(8.18, 62.92) * mm, "end": v(8.2, 63.14) * mm});
            skArc(sketch, "E5312", {"start": v(8.2, 63.14) * mm, "mid": v(8.15, 63.3) * mm, "end": v(8.02, 63.42) * mm});
            skArc(sketch, "E5313", {"start": v(8.02, 63.42) * mm, "mid": v(7.8, 63.5) * mm, "end": v(7.56, 63.53) * mm});
            skArc(sketch, "E5314", {"start": v(7.56, 63.53) * mm, "mid": v(7.14, 63.58) * mm, "end": v(6.74, 63.74) * mm});
            skArc(sketch, "E5315", {"start": v(6.74, 63.74) * mm, "mid": v(6.08, 64.1) * mm, "end": v(5.44, 64.51) * mm});
            skArc(sketch, "E5316", {"start": v(5.44, 64.51) * mm, "mid": v(4.75, 65) * mm, "end": v(4.1, 65.52) * mm});
            skArc(sketch, "E5317", {"start": v(4.1, 65.52) * mm, "mid": v(3.53, 66.02) * mm, "end": v(3, 66.56) * mm});
            skArc(sketch, "E5318", {"start": v(3, 66.56) * mm, "mid": v(2.5, 67.17) * mm, "end": v(2.06, 67.81) * mm});
            skArc(sketch, "E5319", {"start": v(2.06, 67.81) * mm, "mid": v(1.64, 68.54) * mm, "end": v(1.26, 69.3) * mm});
            skArc(sketch, "E5320", {"start": v(1.26, 69.3) * mm, "mid": v(0.98, 70) * mm, "end": v(0.74, 70.71) * mm});
            skArc(sketch, "E5321", {"start": v(0.74, 70.71) * mm, "mid": v(0.67, 71.15) * mm, "end": v(0.74, 71.58) * mm});
            skArc(sketch, "E5322", {"start": v(0.74, 71.58) * mm, "mid": v(0.93, 71.84) * mm, "end": v(1.23, 71.94) * mm});
            skArc(sketch, "E5323", {"start": v(1.23, 71.94) * mm, "mid": v(4.74, 72) * mm, "end": v(8.25, 72.03) * mm});
            skArc(sketch, "E5324", {"start": v(8.25, 72.03) * mm, "mid": v(14.24, 72.07) * mm, "end": v(20.23, 72.09) * mm});
            skArc(sketch, "E5325", {"start": v(20.23, 72.09) * mm, "mid": v(37.93, 72.1) * mm, "end": v(55.64, 72.1) * mm});
            skLineSegment(sketch, "E5326", {"start": v(55.64, 72.1) * mm, "end": v(110.37, 72.1) * mm});
            skLineSegment(sketch, "E5327", {"start": v(110.37, 72.1) * mm, "end": v(110.37, 71.05) * mm});
            skArc(sketch, "E5328", {"start": v(-35.08, -38.37) * mm, "mid": v(-35.88, -39.15) * mm, "end": v(-36.74, -39.86) * mm});
            skArc(sketch, "E5329", {"start": v(-36.74, -39.86) * mm, "mid": v(-37.95, -40.74) * mm, "end": v(-39.18, -41.58) * mm});
            skArc(sketch, "E5330", {"start": v(-39.18, -41.58) * mm, "mid": v(-40.5, -42.4) * mm, "end": v(-41.85, -43.17) * mm});
            skArc(sketch, "E5331", {"start": v(-41.85, -43.17) * mm, "mid": v(-43.04, -43.79) * mm, "end": v(-44.26, -44.33) * mm});
            skLineSegment(sketch, "E5332", {"start": v(-44.26, -44.33) * mm, "end": v(-46.12, -45.1) * mm});
            skLineSegment(sketch, "E5333", {"start": v(-46.12, -45.1) * mm, "end": v(-46.64, -44.36) * mm});
            skArc(sketch, "E5334", {"start": v(-46.64, -44.36) * mm, "mid": v(-46.93, -43.94) * mm, "end": v(-47.2, -43.5) * mm});
            skArc(sketch, "E5335", {"start": v(-47.2, -43.5) * mm, "mid": v(-47.42, -43.1) * mm, "end": v(-47.63, -42.69) * mm});
            skArc(sketch, "E5336", {"start": v(-47.63, -42.69) * mm, "mid": v(-47.84, -42.22) * mm, "end": v(-48.03, -41.74) * mm});
            skArc(sketch, "E5337", {"start": v(-48.03, -41.74) * mm, "mid": v(-48.27, -41.09) * mm, "end": v(-48.5, -40.44) * mm});
            skArc(sketch, "E5338", {"start": v(-48.5, -40.44) * mm, "mid": v(-48.66, -39.97) * mm, "end": v(-48.84, -39.5) * mm});
            skArc(sketch, "E5339", {"start": v(-48.84, -39.5) * mm, "mid": v(-48.96, -39.24) * mm, "end": v(-49.1, -38.98) * mm});
            skArc(sketch, "E5340", {"start": v(-49.1, -38.98) * mm, "mid": v(-49.24, -38.82) * mm, "end": v(-49.4, -38.69) * mm});
            skArc(sketch, "E5341", {"start": v(-49.4, -38.69) * mm, "mid": v(-49.56, -38.6) * mm, "end": v(-49.74, -38.55) * mm});
            skLineSegment(sketch, "E5342", {"start": v(-49.74, -38.55) * mm, "end": v(-50.37, -38.45) * mm});
            skLineSegment(sketch, "E5343", {"start": v(-50.37, -38.45) * mm, "end": v(-50.2, -41.59) * mm});
            skArc(sketch, "E5344", {"start": v(-50.2, -41.59) * mm, "mid": v(-49.97, -44) * mm, "end": v(-49.56, -46.38) * mm});
            skArc(sketch, "E5345", {"start": v(-49.56, -46.38) * mm, "mid": v(-48.96, -48.7) * mm, "end": v(-48.18, -50.95) * mm});
            skArc(sketch, "E5346", {"start": v(-48.18, -50.95) * mm, "mid": v(-47.23, -53.1) * mm, "end": v(-46.1, -55.17) * mm});
            skArc(sketch, "E5347", {"start": v(-46.1, -55.17) * mm, "mid": v(-44.82, -57.13) * mm, "end": v(-43.37, -58.96) * mm});
            skLineSegment(sketch, "E5348", {"start": v(-43.37, -58.96) * mm, "end": v(-42.54, -59.93) * mm});
            skLineSegment(sketch, "E5349", {"start": v(-42.54, -59.93) * mm, "end": v(-41.98, -59.24) * mm});
            skArc(sketch, "E5350", {"start": v(-41.98, -59.24) * mm, "mid": v(-40.73, -57.57) * mm, "end": v(-39.6, -55.8) * mm});
            skArc(sketch, "E5351", {"start": v(-39.6, -55.8) * mm, "mid": v(-38.48, -53.76) * mm, "end": v(-37.46, -51.66) * mm});
            skArc(sketch, "E5352", {"start": v(-37.46, -51.66) * mm, "mid": v(-36.53, -49.45) * mm, "end": v(-35.72, -47.2) * mm});
            skArc(sketch, "E5353", {"start": v(-35.72, -47.2) * mm, "mid": v(-35.07, -45) * mm, "end": v(-34.56, -42.79) * mm});
            skArc(sketch, "E5354", {"start": v(-34.56, -42.79) * mm, "mid": v(-34.25, -41.2) * mm, "end": v(-33.97, -39.6) * mm});
            skArc(sketch, "E5355", {"start": v(-33.97, -39.6) * mm, "mid": v(-33.9, -38.9) * mm, "end": v(-33.94, -38.2) * mm});
            skArc(sketch, "E5356", {"start": v(-33.94, -38.2) * mm, "mid": v(-34.08, -37.98) * mm, "end": v(-34.35, -37.93) * mm});
            skArc(sketch, "E5357", {"start": v(-34.35, -37.93) * mm, "mid": v(-34.75, -38.1) * mm, "end": v(-35.08, -38.37) * mm});
            skArc(sketch, "E5358", {"start": v(-79.04, -39.08) * mm, "mid": v(-79, -39.85) * mm, "end": v(-78.9, -40.62) * mm});
            skArc(sketch, "E5359", {"start": v(-78.9, -40.62) * mm, "mid": v(-78.68, -41.88) * mm, "end": v(-78.43, -43.14) * mm});
            skArc(sketch, "E5360", {"start": v(-78.43, -43.14) * mm, "mid": v(-78.14, -44.47) * mm, "end": v(-77.82, -45.78) * mm});
            skArc(sketch, "E5361", {"start": v(-77.82, -45.78) * mm, "mid": v(-77.53, -46.85) * mm, "end": v(-77.19, -47.9) * mm});
            skArc(sketch, "E5362", {"start": v(-77.19, -47.9) * mm, "mid": v(-76.5, -49.74) * mm, "end": v(-75.72, -51.53) * mm});
            skArc(sketch, "E5363", {"start": v(-75.72, -51.53) * mm, "mid": v(-74.7, -53.6) * mm, "end": v(-73.62, -55.62) * mm});
            skArc(sketch, "E5364", {"start": v(-73.62, -55.62) * mm, "mid": v(-72.53, -57.52) * mm, "end": v(-71.41, -59.4) * mm});
            skArc(sketch, "E5365", {"start": v(-71.41, -59.4) * mm, "mid": v(-71.01, -59.79) * mm, "end": v(-70.47, -59.93) * mm});
            skArc(sketch, "E5366", {"start": v(-70.47, -59.93) * mm, "mid": v(-69.92, -59.8) * mm, "end": v(-69.5, -59.42) * mm});
            skArc(sketch, "E5367", {"start": v(-69.5, -59.42) * mm, "mid": v(-68.5, -57.93) * mm, "end": v(-67.52, -56.4) * mm});
            skArc(sketch, "E5368", {"start": v(-67.52, -56.4) * mm, "mid": v(-66.54, -54.74) * mm, "end": v(-65.63, -53.04) * mm});
            skArc(sketch, "E5369", {"start": v(-65.63, -53.04) * mm, "mid": v(-64.92, -51.53) * mm, "end": v(-64.3, -49.98) * mm});
            skArc(sketch, "E5370", {"start": v(-64.3, -49.98) * mm, "mid": v(-63.82, -48.44) * mm, "end": v(-63.45, -46.86) * mm});
            skArc(sketch, "E5371", {"start": v(-63.45, -46.86) * mm, "mid": v(-63.11, -44.94) * mm, "end": v(-62.86, -43) * mm});
            skArc(sketch, "E5372", {"start": v(-62.86, -43) * mm, "mid": v(-62.68, -41.17) * mm, "end": v(-62.54, -39.34) * mm});
            skArc(sketch, "E5373", {"start": v(-62.54, -39.34) * mm, "mid": v(-62.69, -38.94) * mm, "end": v(-63.07, -38.78) * mm});
            skArc(sketch, "E5374", {"start": v(-63.07, -38.78) * mm, "mid": v(-63.3, -38.8) * mm, "end": v(-63.5, -38.88) * mm});
            skArc(sketch, "E5375", {"start": v(-63.5, -38.88) * mm, "mid": v(-63.7, -39) * mm, "end": v(-63.85, -39.15) * mm});
            skArc(sketch, "E5376", {"start": v(-63.85, -39.15) * mm, "mid": v(-64, -39.38) * mm, "end": v(-64.12, -39.64) * mm});
            skArc(sketch, "E5377", {"start": v(-64.12, -39.64) * mm, "mid": v(-64.26, -40.03) * mm, "end": v(-64.38, -40.44) * mm});
            skArc(sketch, "E5378", {"start": v(-64.38, -40.44) * mm, "mid": v(-64.47, -40.74) * mm, "end": v(-64.57, -41.04) * mm});
            skArc(sketch, "E5379", {"start": v(-64.57, -41.04) * mm, "mid": v(-64.73, -41.46) * mm, "end": v(-64.9, -41.87) * mm});
            skArc(sketch, "E5380", {"start": v(-64.9, -41.87) * mm, "mid": v(-65.1, -42.3) * mm, "end": v(-65.3, -42.75) * mm});
            skArc(sketch, "E5381", {"start": v(-65.3, -42.75) * mm, "mid": v(-65.49, -43.15) * mm, "end": v(-65.7, -43.55) * mm});
            skArc(sketch, "E5382", {"start": v(-65.7, -43.55) * mm, "mid": v(-66.06, -44.23) * mm, "end": v(-66.46, -44.9) * mm});
            skArc(sketch, "E5383", {"start": v(-66.46, -44.9) * mm, "mid": v(-66.67, -45.11) * mm, "end": v(-66.96, -45.22) * mm});
            skArc(sketch, "E5384", {"start": v(-66.96, -45.22) * mm, "mid": v(-67.31, -45.22) * mm, "end": v(-67.65, -45.12) * mm});
            skArc(sketch, "E5385", {"start": v(-67.65, -45.12) * mm, "mid": v(-68.77, -44.64) * mm, "end": v(-69.87, -44.14) * mm});
            skArc(sketch, "E5386", {"start": v(-69.87, -44.14) * mm, "mid": v(-70.83, -43.68) * mm, "end": v(-71.77, -43.17) * mm});
            skArc(sketch, "E5387", {"start": v(-71.77, -43.17) * mm, "mid": v(-72.83, -42.53) * mm, "end": v(-73.86, -41.87) * mm});
            skArc(sketch, "E5388", {"start": v(-73.86, -41.87) * mm, "mid": v(-74.87, -41.18) * mm, "end": v(-75.86, -40.47) * mm});
            skArc(sketch, "E5389", {"start": v(-75.86, -40.47) * mm, "mid": v(-76.67, -39.83) * mm, "end": v(-77.44, -39.15) * mm});
            skArc(sketch, "E5390", {"start": v(-77.44, -39.15) * mm, "mid": v(-77.69, -38.92) * mm, "end": v(-77.95, -38.7) * mm});
            skArc(sketch, "E5391", {"start": v(-77.95, -38.7) * mm, "mid": v(-78.17, -38.5) * mm, "end": v(-78.4, -38.3) * mm});
            skArc(sketch, "E5392", {"start": v(-78.4, -38.3) * mm, "mid": v(-78.6, -38.14) * mm, "end": v(-78.8, -37.98) * mm});
            skArc(sketch, "E5393", {"start": v(-78.8, -37.98) * mm, "mid": v(-78.84, -37.96) * mm, "end": v(-78.89, -37.95) * mm});
            skArc(sketch, "E5394", {"start": v(-78.89, -37.95) * mm, "mid": v(-78.93, -37.96) * mm, "end": v(-78.95, -38) * mm});
            skArc(sketch, "E5395", {"start": v(-78.95, -38) * mm, "mid": v(-78.97, -38.14) * mm, "end": v(-79, -38.28) * mm});
            skArc(sketch, "E5396", {"start": v(-79, -38.28) * mm, "mid": v(-79.01, -38.46) * mm, "end": v(-79.03, -38.65) * mm});
            skArc(sketch, "E5397", {"start": v(-79.03, -38.65) * mm, "mid": v(-79.04, -38.86) * mm, "end": v(-79.04, -39.08) * mm});
            skArc(sketch, "E5398", {"start": v(39.95, 55.02) * mm, "mid": v(38.94, 53.43) * mm, "end": v(37.97, 51.81) * mm});
            skArc(sketch, "E5399", {"start": v(37.97, 51.81) * mm, "mid": v(37.16, 50.3) * mm, "end": v(36.4, 48.75) * mm});
            skArc(sketch, "E5400", {"start": v(36.4, 48.75) * mm, "mid": v(35.75, 47.21) * mm, "end": v(35.17, 45.65) * mm});
            skArc(sketch, "E5401", {"start": v(35.17, 45.65) * mm, "mid": v(34.64, 44.02) * mm, "end": v(34.18, 42.36) * mm});
            skArc(sketch, "E5402", {"start": v(34.18, 42.36) * mm, "mid": v(33.92, 41.3) * mm, "end": v(33.7, 40.22) * mm});
            skArc(sketch, "E5403", {"start": v(33.7, 40.22) * mm, "mid": v(33.47, 39.02) * mm, "end": v(33.27, 37.82) * mm});
            skArc(sketch, "E5404", {"start": v(33.27, 37.82) * mm, "mid": v(33.1, 36.66) * mm, "end": v(32.92, 35.5) * mm});
            skArc(sketch, "E5405", {"start": v(32.92, 35.5) * mm, "mid": v(32.94, 35.3) * mm, "end": v(33.04, 35.13) * mm});
            skArc(sketch, "E5406", {"start": v(33.04, 35.13) * mm, "mid": v(33.1, 35.1) * mm, "end": v(33.15, 35.12) * mm});
            skArc(sketch, "E5407", {"start": v(33.15, 35.12) * mm, "mid": v(33.5, 35.36) * mm, "end": v(33.83, 35.6) * mm});
            skArc(sketch, "E5408", {"start": v(33.83, 35.6) * mm, "mid": v(34.22, 35.88) * mm, "end": v(34.61, 36.17) * mm});
            skArc(sketch, "E5409", {"start": v(34.61, 36.17) * mm, "mid": v(35.07, 36.53) * mm, "end": v(35.52, 36.89) * mm});
            skArc(sketch, "E5410", {"start": v(35.52, 36.89) * mm, "mid": v(36.5, 37.66) * mm, "end": v(37.5, 38.42) * mm});
            skArc(sketch, "E5411", {"start": v(37.5, 38.42) * mm, "mid": v(38.37, 39.02) * mm, "end": v(39.26, 39.6) * mm});
            skArc(sketch, "E5412", {"start": v(39.26, 39.6) * mm, "mid": v(40.13, 40.11) * mm, "end": v(41.03, 40.6) * mm});
            skArc(sketch, "E5413", {"start": v(41.03, 40.6) * mm, "mid": v(42.05, 41.09) * mm, "end": v(43.08, 41.56) * mm});
            skArc(sketch, "E5414", {"start": v(43.08, 41.56) * mm, "mid": v(43.74, 41.84) * mm, "end": v(44.41, 42.13) * mm});
            skArc(sketch, "E5415", {"start": v(44.41, 42.13) * mm, "mid": v(44.7, 42.22) * mm, "end": v(44.98, 42.3) * mm});
            skArc(sketch, "E5416", {"start": v(44.98, 42.3) * mm, "mid": v(45.16, 42.3) * mm, "end": v(45.33, 42.25) * mm});
            skArc(sketch, "E5417", {"start": v(45.33, 42.25) * mm, "mid": v(45.49, 42.16) * mm, "end": v(45.62, 42.03) * mm});
            skArc(sketch, "E5418", {"start": v(45.62, 42.03) * mm, "mid": v(45.92, 41.6) * mm, "end": v(46.18, 41.16) * mm});
            skArc(sketch, "E5419", {"start": v(46.18, 41.16) * mm, "mid": v(46.5, 40.55) * mm, "end": v(46.8, 39.93) * mm});
            skArc(sketch, "E5420", {"start": v(46.8, 39.93) * mm, "mid": v(47.08, 39.27) * mm, "end": v(47.34, 38.61) * mm});
            skArc(sketch, "E5421", {"start": v(47.34, 38.61) * mm, "mid": v(47.54, 38.04) * mm, "end": v(47.7, 37.46) * mm});
            skArc(sketch, "E5422", {"start": v(47.7, 37.46) * mm, "mid": v(47.8, 37.1) * mm, "end": v(47.92, 36.74) * mm});
            skArc(sketch, "E5423", {"start": v(47.92, 36.74) * mm, "mid": v(48, 36.51) * mm, "end": v(48.12, 36.3) * mm});
            skArc(sketch, "E5424", {"start": v(48.12, 36.3) * mm, "mid": v(48.23, 36.16) * mm, "end": v(48.36, 36.05) * mm});
            skArc(sketch, "E5425", {"start": v(48.36, 36.05) * mm, "mid": v(48.5, 35.97) * mm, "end": v(48.67, 35.93) * mm});
            skArc(sketch, "E5426", {"start": v(48.67, 35.93) * mm, "mid": v(48.84, 35.93) * mm, "end": v(49, 35.99) * mm});
            skArc(sketch, "E5427", {"start": v(49, 35.99) * mm, "mid": v(49.11, 36.09) * mm, "end": v(49.18, 36.23) * mm});
            skArc(sketch, "E5428", {"start": v(49.18, 36.23) * mm, "mid": v(49.23, 36.52) * mm, "end": v(49.24, 36.82) * mm});
            skArc(sketch, "E5429", {"start": v(49.24, 36.82) * mm, "mid": v(49.25, 37.69) * mm, "end": v(49.25, 38.55) * mm});
            skArc(sketch, "E5430", {"start": v(49.25, 38.55) * mm, "mid": v(49.15, 40.78) * mm, "end": v(48.84, 42.99) * mm});
            skArc(sketch, "E5431", {"start": v(48.84, 42.99) * mm, "mid": v(48.33, 45.24) * mm, "end": v(47.63, 47.45) * mm});
            skArc(sketch, "E5432", {"start": v(47.63, 47.45) * mm, "mid": v(46.76, 49.6) * mm, "end": v(45.7, 51.69) * mm});
            skArc(sketch, "E5433", {"start": v(45.7, 51.69) * mm, "mid": v(44.52, 53.62) * mm, "end": v(43.18, 55.45) * mm});
            skArc(sketch, "E5434", {"start": v(43.18, 55.45) * mm, "mid": v(42.93, 55.75) * mm, "end": v(42.68, 56.04) * mm});
            skArc(sketch, "E5435", {"start": v(42.68, 56.04) * mm, "mid": v(42.45, 56.3) * mm, "end": v(42.22, 56.56) * mm});
            skArc(sketch, "E5436", {"start": v(42.22, 56.56) * mm, "mid": v(42.02, 56.77) * mm, "end": v(41.82, 56.98) * mm});
            skArc(sketch, "E5437", {"start": v(41.82, 56.98) * mm, "mid": v(41.74, 57.04) * mm, "end": v(41.65, 57.08) * mm});
            skArc(sketch, "E5438", {"start": v(41.65, 57.08) * mm, "mid": v(41.57, 57.08) * mm, "end": v(41.5, 57.03) * mm});
            skArc(sketch, "E5439", {"start": v(41.5, 57.03) * mm, "mid": v(41.26, 56.77) * mm, "end": v(41.04, 56.5) * mm});
            skArc(sketch, "E5440", {"start": v(41.04, 56.5) * mm, "mid": v(40.78, 56.18) * mm, "end": v(40.52, 55.84) * mm});
            skArc(sketch, "E5441", {"start": v(40.52, 55.84) * mm, "mid": v(40.23, 55.43) * mm, "end": v(39.95, 55.02) * mm});
            skArc(sketch, "E5442", {"start": v(68.33, 55.5) * mm, "mid": v(67.32, 54.2) * mm, "end": v(66.4, 52.82) * mm});
            skArc(sketch, "E5443", {"start": v(66.4, 52.82) * mm, "mid": v(65.5, 51.27) * mm, "end": v(64.68, 49.67) * mm});
            skArc(sketch, "E5444", {"start": v(64.68, 49.67) * mm, "mid": v(63.95, 48) * mm, "end": v(63.3, 46.3) * mm});
            skArc(sketch, "E5445", {"start": v(63.3, 46.3) * mm, "mid": v(62.8, 44.66) * mm, "end": v(62.4, 42.98) * mm});
            skArc(sketch, "E5446", {"start": v(62.4, 42.98) * mm, "mid": v(62.22, 42) * mm, "end": v(62.1, 41) * mm});
            skArc(sketch, "E5447", {"start": v(62.1, 41) * mm, "mid": v(61.98, 39.72) * mm, "end": v(61.9, 38.44) * mm});
            skArc(sketch, "E5448", {"start": v(61.9, 38.44) * mm, "mid": v(61.84, 37.14) * mm, "end": v(61.8, 35.85) * mm});
            skArc(sketch, "E5449", {"start": v(61.8, 35.85) * mm, "mid": v(61.85, 35.61) * mm, "end": v(62.01, 35.44) * mm});
            skArc(sketch, "E5450", {"start": v(62.01, 35.44) * mm, "mid": v(62.21, 35.37) * mm, "end": v(62.42, 35.4) * mm});
            skArc(sketch, "E5451", {"start": v(62.42, 35.4) * mm, "mid": v(62.66, 35.51) * mm, "end": v(62.87, 35.68) * mm});
            skArc(sketch, "E5452", {"start": v(62.87, 35.68) * mm, "mid": v(63.08, 35.93) * mm, "end": v(63.25, 36.22) * mm});
            skArc(sketch, "E5453", {"start": v(63.25, 36.22) * mm, "mid": v(63.38, 36.56) * mm, "end": v(63.46, 36.9) * mm});
            skArc(sketch, "E5454", {"start": v(63.46, 36.9) * mm, "mid": v(63.58, 37.48) * mm, "end": v(63.76, 38.03) * mm});
            skArc(sketch, "E5455", {"start": v(63.76, 38.03) * mm, "mid": v(64.07, 38.8) * mm, "end": v(64.4, 39.56) * mm});
            skArc(sketch, "E5456", {"start": v(64.4, 39.56) * mm, "mid": v(64.76, 40.29) * mm, "end": v(65.13, 41) * mm});
            skArc(sketch, "E5457", {"start": v(65.13, 41) * mm, "mid": v(65.37, 41.35) * mm, "end": v(65.67, 41.65) * mm});
            skArc(sketch, "E5458", {"start": v(65.67, 41.65) * mm, "mid": v(65.81, 41.75) * mm, "end": v(65.97, 41.83) * mm});
            skArc(sketch, "E5459", {"start": v(65.97, 41.83) * mm, "mid": v(66.12, 41.87) * mm, "end": v(66.28, 41.88) * mm});
            skArc(sketch, "E5460", {"start": v(66.28, 41.88) * mm, "mid": v(66.5, 41.85) * mm, "end": v(66.7, 41.8) * mm});
            skArc(sketch, "E5461", {"start": v(66.7, 41.8) * mm, "mid": v(67.08, 41.67) * mm, "end": v(67.44, 41.54) * mm});
            skArc(sketch, "E5462", {"start": v(67.44, 41.54) * mm, "mid": v(68.59, 41.06) * mm, "end": v(69.7, 40.52) * mm});
            skArc(sketch, "E5463", {"start": v(69.7, 40.52) * mm, "mid": v(70.98, 39.82) * mm, "end": v(72.23, 39.07) * mm});
            skArc(sketch, "E5464", {"start": v(72.23, 39.07) * mm, "mid": v(73.45, 38.28) * mm, "end": v(74.63, 37.45) * mm});
            skArc(sketch, "E5465", {"start": v(74.63, 37.45) * mm, "mid": v(75.6, 36.69) * mm, "end": v(76.53, 35.87) * mm});
            skArc(sketch, "E5466", {"start": v(76.53, 35.87) * mm, "mid": v(77.06, 35.4) * mm, "end": v(77.6, 34.92) * mm});
            skArc(sketch, "E5467", {"start": v(77.6, 34.92) * mm, "mid": v(77.8, 34.82) * mm, "end": v(78.03, 34.82) * mm});
            skArc(sketch, "E5468", {"start": v(78.03, 34.82) * mm, "mid": v(78.19, 34.92) * mm, "end": v(78.25, 35.1) * mm});
            skArc(sketch, "E5469", {"start": v(78.25, 35.1) * mm, "mid": v(78.22, 35.66) * mm, "end": v(78.16, 36.22) * mm});
            skArc(sketch, "E5470", {"start": v(78.16, 36.22) * mm, "mid": v(77.9, 38.03) * mm, "end": v(77.57, 39.82) * mm});
            skArc(sketch, "E5471", {"start": v(77.57, 39.82) * mm, "mid": v(77.17, 41.55) * mm, "end": v(76.7, 43.27) * mm});
            skArc(sketch, "E5472", {"start": v(76.7, 43.27) * mm, "mid": v(76.15, 44.95) * mm, "end": v(75.54, 46.6) * mm});
            skArc(sketch, "E5473", {"start": v(75.54, 46.6) * mm, "mid": v(74.84, 48.24) * mm, "end": v(74.08, 49.84) * mm});
            skArc(sketch, "E5474", {"start": v(74.08, 49.84) * mm, "mid": v(73.56, 50.85) * mm, "end": v(73, 51.84) * mm});
            skArc(sketch, "E5475", {"start": v(73, 51.84) * mm, "mid": v(72.33, 52.98) * mm, "end": v(71.63, 54.1) * mm});
            skArc(sketch, "E5476", {"start": v(71.63, 54.1) * mm, "mid": v(70.95, 55.17) * mm, "end": v(70.26, 56.23) * mm});
            skArc(sketch, "E5477", {"start": v(70.26, 56.23) * mm, "mid": v(70, 56.53) * mm, "end": v(69.7, 56.76) * mm});
            skArc(sketch, "E5478", {"start": v(69.7, 56.76) * mm, "mid": v(69.64, 56.78) * mm, "end": v(69.57, 56.75) * mm});
            skArc(sketch, "E5479", {"start": v(69.57, 56.75) * mm, "mid": v(69.4, 56.6) * mm, "end": v(69.22, 56.45) * mm});
            skArc(sketch, "E5480", {"start": v(69.22, 56.45) * mm, "mid": v(69, 56.24) * mm, "end": v(68.8, 56.03) * mm});
            skArc(sketch, "E5481", {"start": v(68.8, 56.03) * mm, "mid": v(68.56, 55.77) * mm, "end": v(68.33, 55.5) * mm});
            skSolve(sketch);
        }
        {
            var Q0;
            Q0=makeQuery(id+"F0.imprint","IMPRINT",FACE,{"disambiguationData":[TD([[makeQuery(id+"F0.imprint","IMPRINT",EDGE,{"derivedFrom":sQuery(id+"F0.wireOp",EDGE,"E0")}),-1.0]])]});
            var Q1;
            Q1=makeQuery(id+"F0.imprint","IMPRINT",FACE,{"disambiguationData":[TD([[makeQuery(id+"F0.imprint","IMPRINT",EDGE,{"derivedFrom":sQuery(id+"F0.wireOp",EDGE,"E2688")}),-1.0]])]});
            extrude(context, id + "F1", {"entities" : qUnion([Q0, Q1]), "depth" : 2 * mm});
        }
    });
